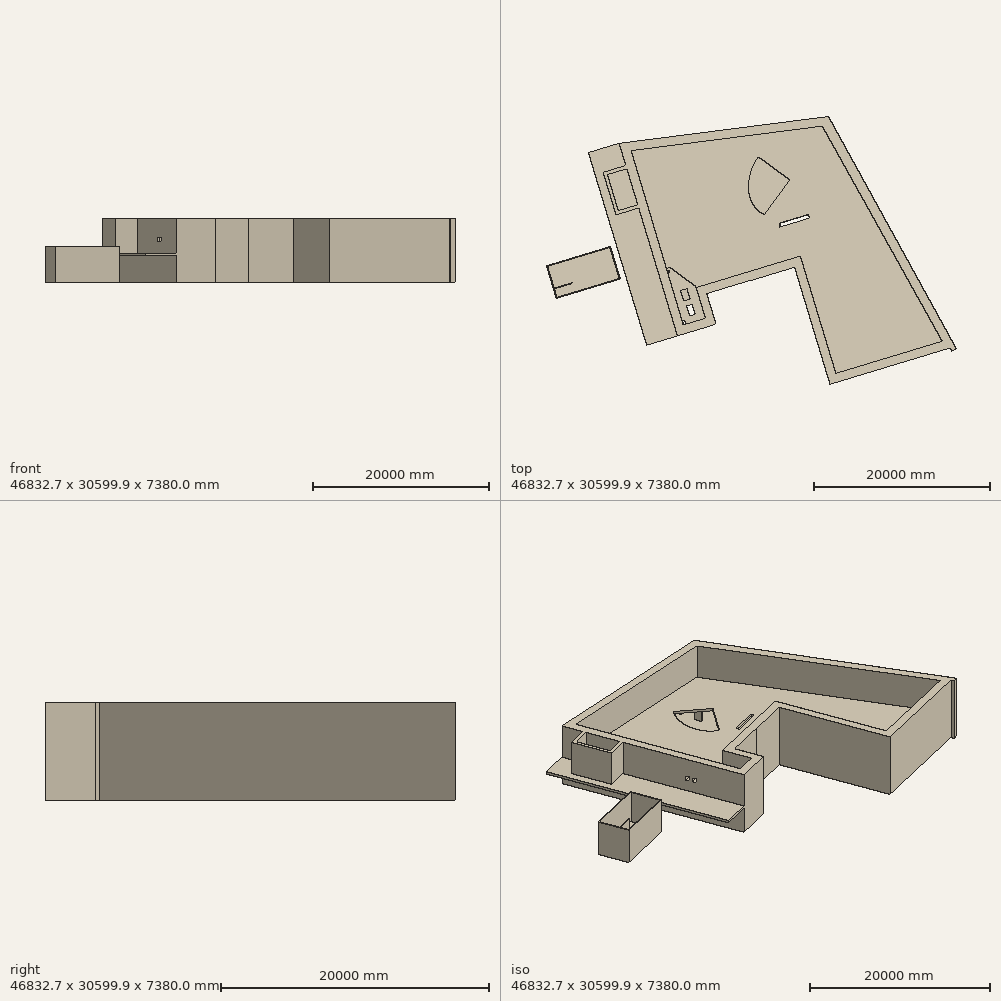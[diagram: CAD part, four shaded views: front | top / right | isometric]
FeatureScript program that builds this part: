
annotation { "Feature Type Name" : "Feature", "Feature Type Description" : "" }
export const myFeature = defineFeature(function(context is Context, id is Id, definition is map)
    precondition{}
    {
        {
            var Q0;
            Q0=qCreatedBy(makeId("Top.planeOp"),FACE);
            var sketch = newSketch(context, id + "F0", { "sketchPlane" : qUnion([Q0])});
            skLineSegment(sketch, "E0", {"start": v(49234.63, 59886.25) * mm, "end": v(49988.48, 60114.42) * mm});
            skLineSegment(sketch, "E1", {"start": v(49988.48, 60114.42) * mm, "end": v(49987.19, 60118.69) * mm});
            skLineSegment(sketch, "E2", {"start": v(49987.19, 60118.69) * mm, "end": v(50833.48, 60374.84) * mm});
            skLineSegment(sketch, "E3", {"start": v(50833.48, 60374.84) * mm, "end": v(51268.03, 58939.17) * mm});
            skLineSegment(sketch, "E4", {"start": v(51268.03, 58939.17) * mm, "end": v(50789.46, 58794.31) * mm});
            skLineSegment(sketch, "E5", {"start": v(50789.46, 58794.31) * mm, "end": v(51212.24, 57397.54) * mm});
            skLineSegment(sketch, "E6", {"start": v(51212.24, 57397.54) * mm, "end": v(53506.66, 49817.17) * mm});
            skLineSegment(sketch, "E7", {"start": v(53506.66, 49817.17) * mm, "end": v(54276.86, 47272.58) * mm});
            skLineSegment(sketch, "E8", {"start": v(54276.86, 47272.58) * mm, "end": v(54412.26, 46825.25) * mm});
            skLineSegment(sketch, "E9", {"start": v(54412.26, 46825.25) * mm, "end": v(62384.2, 49238.2) * mm});
            skLineSegment(sketch, "E10", {"start": v(62384.2, 49238.2) * mm, "end": v(62391.57, 49240.5) * mm});
            skLineSegment(sketch, "E11", {"start": v(62391.57, 49240.5) * mm, "end": v(50014.81, 71440.03) * mm});
            skLineSegment(sketch, "E12", {"start": v(50014.81, 71440.03) * mm, "end": v(49601.87, 74661.93) * mm});
            skLineSegment(sketch, "E13", {"start": v(49601.87, 74661.93) * mm, "end": v(39442.05, 73358.6) * mm});
            skLineSegment(sketch, "E14", {"start": v(39442.05, 73358.6) * mm, "end": v(40440.6, 70059.64) * mm});
            skLineSegment(sketch, "E15", {"start": v(40440.6, 70059.64) * mm, "end": v(33357.72, 67915.8) * mm});
            skLineSegment(sketch, "E16", {"start": v(33357.72, 67915.8) * mm, "end": v(31999.28, 72403.84) * mm});
            skLineSegment(sketch, "E17", {"start": v(31999.28, 72403.84) * mm, "end": v(31027.55, 72279.2) * mm});
            skLineSegment(sketch, "E18", {"start": v(31027.55, 72279.2) * mm, "end": v(32898.58, 66097.65) * mm});
            skLineSegment(sketch, "E19", {"start": v(32898.58, 66097.65) * mm, "end": v(32831.58, 66077.37) * mm});
            skLineSegment(sketch, "E20", {"start": v(32831.58, 66077.37) * mm, "end": v(35924.87, 55857.68) * mm});
            skLineSegment(sketch, "E21", {"start": v(35924.87, 55857.68) * mm, "end": v(35924.9, 55857.68) * mm});
            skLineSegment(sketch, "E22", {"start": v(35924.9, 55857.68) * mm, "end": v(36984.58, 52356.66) * mm});
            skLineSegment(sketch, "E23", {"start": v(36984.58, 52356.66) * mm, "end": v(39517.02, 53123.18) * mm});
            skLineSegment(sketch, "E24", {"start": v(39517.02, 53123.18) * mm, "end": v(38457.33, 56624.2) * mm});
            skLineSegment(sketch, "E25", {"start": v(38457.33, 56624.2) * mm, "end": v(38699.27, 56697.43) * mm});
            skLineSegment(sketch, "E26", {"start": v(38699.27, 56697.43) * mm, "end": v(38699.29, 56697.38) * mm});
            skLineSegment(sketch, "E27", {"start": v(38699.29, 56697.38) * mm, "end": v(39127.68, 56827.04) * mm});
            skLineSegment(sketch, "E28", {"start": v(39127.68, 56827.04) * mm, "end": v(38801.77, 57903.8) * mm});
            skLineSegment(sketch, "E29", {"start": v(38801.77, 57903.8) * mm, "end": v(42989.16, 59171.24) * mm});
            skLineSegment(sketch, "E30", {"start": v(42989.16, 59171.24) * mm, "end": v(43315.06, 58094.54) * mm});
            skLineSegment(sketch, "E31", {"start": v(43315.06, 58094.54) * mm, "end": v(44386.8, 58418.93) * mm});
            skLineSegment(sketch, "E32", {"start": v(44386.8, 58418.93) * mm, "end": v(43824.83, 60275.54) * mm});
            skLineSegment(sketch, "E33", {"start": v(43824.83, 60275.54) * mm, "end": v(48658.2, 61738.5) * mm});
            skLineSegment(sketch, "E34", {"start": v(48658.2, 61738.5) * mm, "end": v(48658.23, 61738.41) * mm});
            skLineSegment(sketch, "E35", {"start": v(48658.23, 61738.41) * mm, "end": v(48672.7, 61742.8) * mm});
            skLineSegment(sketch, "E36", {"start": v(48672.7, 61742.8) * mm, "end": v(48803.06, 61312.13) * mm});
            skLineSegment(sketch, "E37", {"start": v(48803.06, 61312.13) * mm, "end": v(49377.38, 61485.96) * mm});
            skLineSegment(sketch, "E38", {"start": v(49377.38, 61485.96) * mm, "end": v(49667.08, 60528.84) * mm});
            skLineSegment(sketch, "E39", {"start": v(49667.08, 60528.84) * mm, "end": v(49092.75, 60355) * mm});
            skLineSegment(sketch, "E40", {"start": v(49092.75, 60355) * mm, "end": v(49234.63, 59886.25) * mm});
            skLineSegment(sketch, "E41", {"start": v(54024.33, 50564.9) * mm, "end": v(51967.54, 57360.16) * mm});
            skLineSegment(sketch, "E42", {"start": v(51967.54, 57360.16) * mm, "end": v(51853.69, 57325.7) * mm});
            skLineSegment(sketch, "E43", {"start": v(51853.69, 57325.7) * mm, "end": v(51428.05, 58731.95) * mm});
            skLineSegment(sketch, "E44", {"start": v(51428.05, 58731.95) * mm, "end": v(51667.33, 58804.37) * mm});
            skLineSegment(sketch, "E45", {"start": v(51667.33, 58804.37) * mm, "end": v(52092.97, 57398.13) * mm});
            skLineSegment(sketch, "E46", {"start": v(52092.97, 57398.13) * mm, "end": v(54481.09, 58120.96) * mm});
            skLineSegment(sketch, "E47", {"start": v(54481.09, 58120.96) * mm, "end": v(53322.5, 61948.71) * mm});
            skLineSegment(sketch, "E48", {"start": v(53322.5, 61948.71) * mm, "end": v(53566.56, 62022.58) * mm});
            skLineSegment(sketch, "E49", {"start": v(53566.56, 62022.58) * mm, "end": v(54725.14, 58194.83) * mm});
            skLineSegment(sketch, "E50", {"start": v(54725.14, 58194.83) * mm, "end": v(54739.4, 58147.73) * mm});
            skLineSegment(sketch, "E51", {"start": v(54739.4, 58147.73) * mm, "end": v(55773.88, 58460.84) * mm});
            skLineSegment(sketch, "E52", {"start": v(55773.88, 58460.84) * mm, "end": v(59288.16, 52158.17) * mm});
            skLineSegment(sketch, "E53", {"start": v(59288.16, 52158.17) * mm, "end": v(54024.33, 50564.9) * mm});
            skLineSegment(sketch, "E54", {"start": v(51615.9, 65546.25) * mm, "end": v(50850.2, 65314.51) * mm});
            skLineSegment(sketch, "E55", {"start": v(50850.2, 65314.51) * mm, "end": v(50777.79, 65553.8) * mm});
            skLineSegment(sketch, "E56", {"start": v(50777.79, 65553.8) * mm, "end": v(51543.49, 65785.53) * mm});
            skLineSegment(sketch, "E57", {"start": v(51543.49, 65785.53) * mm, "end": v(51615.9, 65546.25) * mm});
            skLineSegment(sketch, "E58", {"start": v(51763.97, 62799.89) * mm, "end": v(51728.86, 62915.9) * mm});
            skLineSegment(sketch, "E59", {"start": v(51728.86, 62915.9) * mm, "end": v(52398.85, 63118.67) * mm});
            skLineSegment(sketch, "E60", {"start": v(52398.85, 63118.67) * mm, "end": v(52433.96, 63002.65) * mm});
            skLineSegment(sketch, "E61", {"start": v(52433.96, 63002.65) * mm, "end": v(51763.97, 62799.89) * mm});
            skLineSegment(sketch, "E62", {"start": v(48119.06, 63518.92) * mm, "end": v(48056.28, 63967.48) * mm});
            skLineSegment(sketch, "E63", {"start": v(48056.28, 63967.48) * mm, "end": v(51272.91, 64941.22) * mm});
            skLineSegment(sketch, "E64", {"start": v(51272.91, 64941.22) * mm, "end": v(51403.27, 64510.51) * mm});
            skLineSegment(sketch, "E65", {"start": v(51403.27, 64510.51) * mm, "end": v(48119.06, 63518.92) * mm});
            skLineSegment(sketch, "E66", {"start": v(57976.54, 65897.74) * mm, "end": v(66562.27, 50502.76) * mm});
            skLineSegment(sketch, "E67", {"start": v(66562.27, 50502.76) * mm, "end": v(65252.8, 50106.47) * mm});
            skLineSegment(sketch, "E68", {"start": v(65252.8, 50106.47) * mm, "end": v(51430.06, 74896.45) * mm});
            skLineSegment(sketch, "E69", {"start": v(51430.06, 74896.45) * mm, "end": v(52856, 75079.32) * mm});
            skLineSegment(sketch, "E70", {"start": v(52856, 75079.32) * mm, "end": v(52856, 75079.3) * mm});
            skLineSegment(sketch, "E71", {"start": v(52856, 75079.3) * mm, "end": v(52857.63, 75079.51) * mm});
            skLineSegment(sketch, "E72", {"start": v(52857.63, 75079.51) * mm, "end": v(57976.54, 65897.74) * mm});
            skLineSegment(sketch, "E73", {"start": v(51575.28, 74914.98) * mm, "end": v(65384.36, 50146.35) * mm});
            skLineSegment(sketch, "E74", {"start": v(65384.36, 50146.35) * mm, "end": v(62391.57, 49240.5) * mm});
            skLineSegment(sketch, "E75", {"start": v(62391.57, 49240.5) * mm, "end": v(50012.55, 71444.1) * mm});
            skLineSegment(sketch, "E76", {"start": v(50012.55, 71444.1) * mm, "end": v(49601.81, 74661.66) * mm});
            skLineSegment(sketch, "E77", {"start": v(49601.81, 74661.66) * mm, "end": v(51575.28, 74914.98) * mm});
            skCircle(sketch, "E78", {"center": v(0, 0) * mm, "radius": 1927.6 * mm});
            skLineSegment(sketch, "E79", {"start": v(0, 5000) * mm, "end": v(0, -5000) * mm});
            skLineSegment(sketch, "E80", {"start": v(5000, 0) * mm, "end": v(-5000, 0) * mm});
            skLineSegment(sketch, "E81", {"start": v(34100, 72522.1) * mm, "end": v(32052.06, 72259.39) * mm});
            skLineSegment(sketch, "E82", {"start": v(32052.06, 72259.39) * mm, "end": v(32032.97, 72408.17) * mm});
            skLineSegment(sketch, "E83", {"start": v(32032.97, 72408.17) * mm, "end": v(39441.15, 73358.44) * mm});
            skLineSegment(sketch, "E84", {"start": v(39441.15, 73358.44) * mm, "end": v(39460.24, 73209.66) * mm});
            skLineSegment(sketch, "E85", {"start": v(39460.24, 73209.66) * mm, "end": v(37865.53, 73005.14) * mm});
            skLineSegment(sketch, "E86", {"start": v(52182.8, 73250.46) * mm, "end": v(52173.55, 73267.05) * mm});
            skLineSegment(sketch, "E87", {"start": v(52173.55, 73267.05) * mm, "end": v(52159.34, 73259.13) * mm});
            skLineSegment(sketch, "E88", {"start": v(34858.83, 59379.88) * mm, "end": v(38413.86, 56763.64) * mm});
            skLineSegment(sketch, "E89", {"start": v(38413.86, 56763.64) * mm, "end": v(39517.39, 53123.3) * mm});
            skLineSegment(sketch, "E90", {"start": v(39517.39, 53123.3) * mm, "end": v(36984.58, 52356.66) * mm});
            skLineSegment(sketch, "E91", {"start": v(36984.58, 52356.66) * mm, "end": v(34858.83, 59379.88) * mm});
            skLineSegment(sketch, "E92", {"start": v(31997.32, 72403.55) * mm, "end": v(33353.34, 67923.5) * mm});
            skLineSegment(sketch, "E93", {"start": v(40437.2, 70067.64) * mm, "end": v(39441.15, 73358.44) * mm});
            skLineSegment(sketch, "E94", {"start": v(38345.1, 73217.84) * mm, "end": v(38345.1, 73217.85) * mm});
            skLineSegment(sketch, "E95", {"start": v(35567.85, 72861.58) * mm, "end": v(35567.85, 72861.59) * mm});
            skLineSegment(sketch, "E96", {"start": v(48630.18, 64524.82) * mm, "end": v(50782.31, 65176.37) * mm});
            skLineSegment(sketch, "E97", {"start": v(50853.58, 64936.6) * mm, "end": v(48702.6, 64285.54) * mm});
            skLineSegment(sketch, "E98", {"start": v(53328.4, 61951.88) * mm, "end": v(48991, 60639.04) * mm});
            skLineSegment(sketch, "E99", {"start": v(53328.4, 61951.88) * mm, "end": v(53400.82, 61712.6) * mm});
            skLineSegment(sketch, "E100", {"start": v(57239.17, 51925.82) * mm, "end": v(54176.2, 50998.75) * mm});
            skLineSegment(sketch, "E101", {"start": v(55604.89, 57867.13) * mm, "end": v(57345.71, 52125.24) * mm});
            skLineSegment(sketch, "E102", {"start": v(52345.35, 57047.72) * mm, "end": v(55408.08, 57974.72) * mm});
            skLineSegment(sketch, "E103", {"start": v(53976.63, 51105.79) * mm, "end": v(52238.56, 56848.23) * mm});
            skLineSegment(sketch, "E104", {"start": v(52391.7, 56894.58) * mm, "end": v(54129.84, 51151.89) * mm});
            skLineSegment(sketch, "E105", {"start": v(55454.43, 57821.58) * mm, "end": v(52391.7, 56894.58) * mm});
            skLineSegment(sketch, "E106", {"start": v(57192.58, 52078.89) * mm, "end": v(55454.43, 57821.58) * mm});
            skLineSegment(sketch, "E107", {"start": v(54129.84, 51151.89) * mm, "end": v(57192.58, 52078.89) * mm});
            skLineSegment(sketch, "E108", {"start": v(54176.2, 50998.75) * mm, "end": v(54023.05, 50952.4) * mm});
            skLineSegment(sketch, "E109", {"start": v(54023.05, 50952.4) * mm, "end": v(54020.55, 50960.69) * mm});
            skLineSegment(sketch, "E110", {"start": v(54020.55, 50960.69) * mm, "end": v(54086.56, 50980.7) * mm});
            skArc(sketch, "E111", {"start": v(54086.56, 50980.7) * mm, "mid": v(54091.32, 50984.6) * mm, "end": v(54091.92, 50990.7) * mm});
            skLineSegment(sketch, "E112", {"start": v(54091.92, 50990.7) * mm, "end": v(54055.4, 51111.92) * mm});
            skArc(sketch, "E113", {"start": v(54055.4, 51111.92) * mm, "mid": v(54051.1, 51116.56) * mm, "end": v(54044.8, 51117.1) * mm});
            skLineSegment(sketch, "E114", {"start": v(54044.8, 51117.1) * mm, "end": v(53979.21, 51097.25) * mm});
            skLineSegment(sketch, "E115", {"start": v(53979.21, 51097.25) * mm, "end": v(53976.7, 51105.54) * mm});
            skLineSegment(sketch, "E116", {"start": v(53976.7, 51105.54) * mm, "end": v(54129.84, 51151.89) * mm});
            skLineSegment(sketch, "E117", {"start": v(54129.84, 51151.89) * mm, "end": v(54132.35, 51143.6) * mm});
            skLineSegment(sketch, "E118", {"start": v(54132.35, 51143.6) * mm, "end": v(54066.16, 51123.56) * mm});
            skArc(sketch, "E119", {"start": v(54066.16, 51123.56) * mm, "mid": v(54061.44, 51119.65) * mm, "end": v(54060.82, 51113.56) * mm});
            skLineSegment(sketch, "E120", {"start": v(54060.82, 51113.56) * mm, "end": v(54097.35, 50992.34) * mm});
            skArc(sketch, "E121", {"start": v(54097.35, 50992.34) * mm, "mid": v(54101.31, 50987.56) * mm, "end": v(54107.5, 50987) * mm});
            skLineSegment(sketch, "E122", {"start": v(54107.5, 50987) * mm, "end": v(54173.68, 51007.04) * mm});
            skLineSegment(sketch, "E123", {"start": v(54173.68, 51007.04) * mm, "end": v(54176.2, 50998.75) * mm});
            skLineSegment(sketch, "E124", {"start": v(57392.07, 51972.1) * mm, "end": v(57238.93, 51925.75) * mm});
            skLineSegment(sketch, "E125", {"start": v(57238.93, 51925.75) * mm, "end": v(57236.42, 51934.04) * mm});
            skLineSegment(sketch, "E126", {"start": v(57236.42, 51934.04) * mm, "end": v(57302.44, 51954.06) * mm});
            skArc(sketch, "E127", {"start": v(57302.44, 51954.06) * mm, "mid": v(57307.19, 51957.94) * mm, "end": v(57307.8, 51964.05) * mm});
            skLineSegment(sketch, "E128", {"start": v(57307.8, 51964.05) * mm, "end": v(57271.27, 52085.27) * mm});
            skArc(sketch, "E129", {"start": v(57271.27, 52085.27) * mm, "mid": v(57266.98, 52089.9) * mm, "end": v(57260.68, 52090.45) * mm});
            skLineSegment(sketch, "E130", {"start": v(57260.68, 52090.45) * mm, "end": v(57195.08, 52070.6) * mm});
            skLineSegment(sketch, "E131", {"start": v(57195.08, 52070.6) * mm, "end": v(57192.58, 52078.89) * mm});
            skLineSegment(sketch, "E132", {"start": v(57192.58, 52078.89) * mm, "end": v(57345.71, 52125.24) * mm});
            skLineSegment(sketch, "E133", {"start": v(57345.71, 52125.24) * mm, "end": v(57348.22, 52116.95) * mm});
            skLineSegment(sketch, "E134", {"start": v(57348.22, 52116.95) * mm, "end": v(57282.03, 52096.92) * mm});
            skArc(sketch, "E135", {"start": v(57282.03, 52096.92) * mm, "mid": v(57277.31, 52093) * mm, "end": v(57276.69, 52086.9) * mm});
            skLineSegment(sketch, "E136", {"start": v(57276.69, 52086.9) * mm, "end": v(57313.22, 51965.7) * mm});
            skArc(sketch, "E137", {"start": v(57313.22, 51965.7) * mm, "mid": v(57317.18, 51960.91) * mm, "end": v(57323.37, 51960.36) * mm});
            skLineSegment(sketch, "E138", {"start": v(57323.37, 51960.36) * mm, "end": v(57389.56, 51980.4) * mm});
            skLineSegment(sketch, "E139", {"start": v(57389.56, 51980.4) * mm, "end": v(57392.07, 51972.1) * mm});
            skLineSegment(sketch, "E140", {"start": v(55607.57, 57867.94) * mm, "end": v(55454.43, 57821.58) * mm});
            skLineSegment(sketch, "E141", {"start": v(55454.43, 57821.58) * mm, "end": v(55451.92, 57829.87) * mm});
            skLineSegment(sketch, "E142", {"start": v(55451.92, 57829.87) * mm, "end": v(55517.94, 57849.9) * mm});
            skArc(sketch, "E143", {"start": v(55517.94, 57849.9) * mm, "mid": v(55522.7, 57853.78) * mm, "end": v(55523.3, 57859.89) * mm});
            skLineSegment(sketch, "E144", {"start": v(55523.3, 57859.89) * mm, "end": v(55486.78, 57981.1) * mm});
            skArc(sketch, "E145", {"start": v(55486.78, 57981.1) * mm, "mid": v(55482.48, 57985.74) * mm, "end": v(55476.18, 57986.29) * mm});
            skLineSegment(sketch, "E146", {"start": v(55476.18, 57986.29) * mm, "end": v(55410.59, 57966.43) * mm});
            skLineSegment(sketch, "E147", {"start": v(55410.59, 57966.43) * mm, "end": v(55408.08, 57974.72) * mm});
            skLineSegment(sketch, "E148", {"start": v(55408.08, 57974.72) * mm, "end": v(55561.22, 58021.08) * mm});
            skLineSegment(sketch, "E149", {"start": v(55561.22, 58021.08) * mm, "end": v(55563.73, 58012.79) * mm});
            skLineSegment(sketch, "E150", {"start": v(55563.73, 58012.79) * mm, "end": v(55497.54, 57992.75) * mm});
            skArc(sketch, "E151", {"start": v(55497.54, 57992.75) * mm, "mid": v(55492.82, 57988.84) * mm, "end": v(55492.2, 57982.74) * mm});
            skLineSegment(sketch, "E152", {"start": v(55492.2, 57982.74) * mm, "end": v(55528.73, 57861.53) * mm});
            skArc(sketch, "E153", {"start": v(55528.73, 57861.53) * mm, "mid": v(55532.69, 57856.75) * mm, "end": v(55538.87, 57856.2) * mm});
            skLineSegment(sketch, "E154", {"start": v(55538.87, 57856.2) * mm, "end": v(55605.06, 57876.23) * mm});
            skLineSegment(sketch, "E155", {"start": v(55605.06, 57876.23) * mm, "end": v(55607.57, 57867.94) * mm});
            skLineSegment(sketch, "E156", {"start": v(52391.7, 56894.58) * mm, "end": v(52238.56, 56848.23) * mm});
            skLineSegment(sketch, "E157", {"start": v(52238.56, 56848.23) * mm, "end": v(52236.05, 56856.52) * mm});
            skLineSegment(sketch, "E158", {"start": v(52236.05, 56856.52) * mm, "end": v(52302.07, 56876.54) * mm});
            skArc(sketch, "E159", {"start": v(52302.07, 56876.54) * mm, "mid": v(52306.82, 56880.43) * mm, "end": v(52307.43, 56886.53) * mm});
            skLineSegment(sketch, "E160", {"start": v(52307.43, 56886.53) * mm, "end": v(52270.9, 57007.75) * mm});
            skArc(sketch, "E161", {"start": v(52270.9, 57007.75) * mm, "mid": v(52266.6, 57012.4) * mm, "end": v(52260.3, 57012.93) * mm});
            skLineSegment(sketch, "E162", {"start": v(52260.3, 57012.93) * mm, "end": v(52194.72, 56993.08) * mm});
            skLineSegment(sketch, "E163", {"start": v(52194.72, 56993.08) * mm, "end": v(52192.2, 57001.37) * mm});
            skLineSegment(sketch, "E164", {"start": v(52192.2, 57001.37) * mm, "end": v(52345.35, 57047.72) * mm});
            skLineSegment(sketch, "E165", {"start": v(52345.35, 57047.72) * mm, "end": v(52347.86, 57039.43) * mm});
            skLineSegment(sketch, "E166", {"start": v(52347.86, 57039.43) * mm, "end": v(52281.67, 57019.4) * mm});
            skArc(sketch, "E167", {"start": v(52281.67, 57019.4) * mm, "mid": v(52276.94, 57015.49) * mm, "end": v(52276.32, 57009.39) * mm});
            skLineSegment(sketch, "E168", {"start": v(52276.32, 57009.39) * mm, "end": v(52312.86, 56888.17) * mm});
            skArc(sketch, "E169", {"start": v(52312.86, 56888.17) * mm, "mid": v(52316.82, 56883.4) * mm, "end": v(52323, 56882.84) * mm});
            skLineSegment(sketch, "E170", {"start": v(52323, 56882.84) * mm, "end": v(52389.19, 56902.87) * mm});
            skLineSegment(sketch, "E171", {"start": v(52389.19, 56902.87) * mm, "end": v(52391.7, 56894.58) * mm});
            skLineSegment(sketch, "E172", {"start": v(55694.63, 56724.4) * mm, "end": v(55675.8, 56786.62) * mm});
            skLineSegment(sketch, "E173", {"start": v(55675.8, 56786.62) * mm, "end": v(55672.2, 56785.53) * mm});
            skArc(sketch, "E174", {"start": v(55672.2, 56785.53) * mm, "mid": v(55669.63, 56783.5) * mm, "end": v(55669.12, 56780.27) * mm});
            skLineSegment(sketch, "E175", {"start": v(55669.12, 56780.27) * mm, "end": v(55678.43, 56737.44) * mm});
            skArc(sketch, "E176", {"start": v(55671.21, 56725.15) * mm, "mid": v(55677.22, 56729.88) * mm, "end": v(55678.43, 56737.44) * mm});
            skLineSegment(sketch, "E177", {"start": v(55671.21, 56725.15) * mm, "end": v(55560.55, 56691.66) * mm});
            skArc(sketch, "E178", {"start": v(55547.74, 56697.88) * mm, "mid": v(55552.93, 56692.26) * mm, "end": v(55560.55, 56691.66) * mm});
            skLineSegment(sketch, "E179", {"start": v(55547.74, 56697.88) * mm, "end": v(55531.74, 56738.69) * mm});
            skArc(sketch, "E180", {"start": v(55531.74, 56738.69) * mm, "mid": v(55529.51, 56741.1) * mm, "end": v(55526.24, 56741.35) * mm});
            skLineSegment(sketch, "E181", {"start": v(55526.24, 56741.35) * mm, "end": v(55522.66, 56740.27) * mm});
            skLineSegment(sketch, "E182", {"start": v(55522.66, 56740.27) * mm, "end": v(55541.49, 56678.05) * mm});
            skLineSegment(sketch, "E183", {"start": v(55541.49, 56678.05) * mm, "end": v(55694.63, 56724.4) * mm});
            skLineSegment(sketch, "E184", {"start": v(55616.8, 56429.2) * mm, "end": v(55635.64, 56366.99) * mm});
            skLineSegment(sketch, "E185", {"start": v(55635.64, 56366.99) * mm, "end": v(55639.22, 56368.08) * mm});
            skArc(sketch, "E186", {"start": v(55639.22, 56368.08) * mm, "mid": v(55641.8, 56370.1) * mm, "end": v(55642.32, 56373.34) * mm});
            skLineSegment(sketch, "E187", {"start": v(55642.32, 56373.34) * mm, "end": v(55633, 56416.17) * mm});
            skArc(sketch, "E188", {"start": v(55640.22, 56428.45) * mm, "mid": v(55634.2, 56423.72) * mm, "end": v(55633, 56416.17) * mm});
            skLineSegment(sketch, "E189", {"start": v(55640.22, 56428.45) * mm, "end": v(55750.88, 56461.95) * mm});
            skArc(sketch, "E190", {"start": v(55763.7, 56455.73) * mm, "mid": v(55758.5, 56461.34) * mm, "end": v(55750.88, 56461.95) * mm});
            skLineSegment(sketch, "E191", {"start": v(55763.7, 56455.73) * mm, "end": v(55779.7, 56414.92) * mm});
            skArc(sketch, "E192", {"start": v(55779.7, 56414.92) * mm, "mid": v(55781.92, 56412.51) * mm, "end": v(55785.19, 56412.26) * mm});
            skLineSegment(sketch, "E193", {"start": v(55785.19, 56412.26) * mm, "end": v(55788.78, 56413.34) * mm});
            skLineSegment(sketch, "E194", {"start": v(55788.78, 56413.34) * mm, "end": v(55769.95, 56475.55) * mm});
            skLineSegment(sketch, "E195", {"start": v(55769.95, 56475.55) * mm, "end": v(55616.8, 56429.2) * mm});
            skCircle(sketch, "E196", {"center": v(55655.72, 56576.8) * mm, "radius": 0.25 * mm});
            skCircle(sketch, "E197", {"center": v(55655.72, 56576.8) * mm, "radius": 57.5 * mm});
            skCircle(sketch, "E198", {"center": v(55655.72, 56576.8) * mm, "radius": 59.5 * mm});
            skCircle(sketch, "E199", {"center": v(55655.72, 56576.8) * mm, "radius": 63.5 * mm});
            skLineSegment(sketch, "E200", {"start": v(55607.5, 56356.38) * mm, "end": v(55636.22, 56365.08) * mm});
            skLineSegment(sketch, "E201", {"start": v(55636.22, 56365.08) * mm, "end": v(55621.73, 56412.93) * mm});
            skLineSegment(sketch, "E202", {"start": v(55621.73, 56412.93) * mm, "end": v(55593.02, 56404.24) * mm});
            skLineSegment(sketch, "E203", {"start": v(55593.02, 56404.24) * mm, "end": v(55607.5, 56356.38) * mm});
            skLineSegment(sketch, "E204", {"start": v(55636.22, 56365.08) * mm, "end": v(55635.64, 56366.99) * mm});
            skLineSegment(sketch, "E205", {"start": v(55635.64, 56366.99) * mm, "end": v(55621.73, 56412.93) * mm});
            skLineSegment(sketch, "E206", {"start": v(52875.62, 55599.52) * mm, "end": v(52894.45, 55537.3) * mm});
            skLineSegment(sketch, "E207", {"start": v(52894.45, 55537.3) * mm, "end": v(52898.03, 55538.4) * mm});
            skArc(sketch, "E208", {"start": v(52898.03, 55538.4) * mm, "mid": v(52900.6, 55540.42) * mm, "end": v(52901.13, 55543.66) * mm});
            skLineSegment(sketch, "E209", {"start": v(52901.13, 55543.66) * mm, "end": v(52891.81, 55586.5) * mm});
            skArc(sketch, "E210", {"start": v(52899.03, 55598.77) * mm, "mid": v(52893.02, 55594.04) * mm, "end": v(52891.81, 55586.5) * mm});
            skLineSegment(sketch, "E211", {"start": v(52899.03, 55598.77) * mm, "end": v(53009.69, 55632.26) * mm});
            skArc(sketch, "E212", {"start": v(53022.5, 55626.05) * mm, "mid": v(53017.31, 55631.66) * mm, "end": v(53009.69, 55632.26) * mm});
            skLineSegment(sketch, "E213", {"start": v(53022.5, 55626.05) * mm, "end": v(53038.5, 55585.24) * mm});
            skArc(sketch, "E214", {"start": v(53038.5, 55585.24) * mm, "mid": v(53040.73, 55582.83) * mm, "end": v(53044, 55582.57) * mm});
            skLineSegment(sketch, "E215", {"start": v(53044, 55582.57) * mm, "end": v(53047.59, 55583.66) * mm});
            skLineSegment(sketch, "E216", {"start": v(53047.59, 55583.66) * mm, "end": v(53028.76, 55645.87) * mm});
            skLineSegment(sketch, "E217", {"start": v(53028.76, 55645.87) * mm, "end": v(52875.62, 55599.52) * mm});
            skLineSegment(sketch, "E218", {"start": v(52953.44, 55894.72) * mm, "end": v(52934.6, 55956.94) * mm});
            skLineSegment(sketch, "E219", {"start": v(52934.6, 55956.94) * mm, "end": v(52931.02, 55955.85) * mm});
            skArc(sketch, "E220", {"start": v(52931.02, 55955.85) * mm, "mid": v(52928.44, 55953.82) * mm, "end": v(52927.92, 55950.59) * mm});
            skLineSegment(sketch, "E221", {"start": v(52927.92, 55950.59) * mm, "end": v(52937.24, 55907.75) * mm});
            skArc(sketch, "E222", {"start": v(52930.02, 55895.47) * mm, "mid": v(52936.03, 55900.2) * mm, "end": v(52937.24, 55907.75) * mm});
            skLineSegment(sketch, "E223", {"start": v(52930.02, 55895.47) * mm, "end": v(52819.36, 55861.98) * mm});
            skArc(sketch, "E224", {"start": v(52806.55, 55868.2) * mm, "mid": v(52811.74, 55862.58) * mm, "end": v(52819.36, 55861.98) * mm});
            skLineSegment(sketch, "E225", {"start": v(52806.55, 55868.2) * mm, "end": v(52790.55, 55909) * mm});
            skArc(sketch, "E226", {"start": v(52790.55, 55909) * mm, "mid": v(52788.32, 55911.41) * mm, "end": v(52785.05, 55911.67) * mm});
            skLineSegment(sketch, "E227", {"start": v(52785.05, 55911.67) * mm, "end": v(52781.47, 55910.59) * mm});
            skLineSegment(sketch, "E228", {"start": v(52781.47, 55910.59) * mm, "end": v(52800.3, 55848.37) * mm});
            skLineSegment(sketch, "E229", {"start": v(52800.3, 55848.37) * mm, "end": v(52953.44, 55894.72) * mm});
            skCircle(sketch, "E230", {"center": v(52914.53, 55747.12) * mm, "radius": 0.25 * mm});
            skCircle(sketch, "E231", {"center": v(52914.53, 55747.12) * mm, "radius": 57.5 * mm});
            skCircle(sketch, "E232", {"center": v(52914.53, 55747.12) * mm, "radius": 59.5 * mm});
            skCircle(sketch, "E233", {"center": v(52914.53, 55747.12) * mm, "radius": 63.5 * mm});
            skLineSegment(sketch, "E234", {"start": v(53045.04, 55592.08) * mm, "end": v(53073.75, 55600.77) * mm});
            skLineSegment(sketch, "E235", {"start": v(53073.75, 55600.77) * mm, "end": v(53062.4, 55638.3) * mm});
            skLineSegment(sketch, "E236", {"start": v(53062.4, 55638.3) * mm, "end": v(53033.68, 55629.6) * mm});
            skLineSegment(sketch, "E237", {"start": v(53033.68, 55629.6) * mm, "end": v(53045.04, 55592.08) * mm});
            skLineSegment(sketch, "E238", {"start": v(53076.88, 55590.44) * mm, "end": v(53073.75, 55600.77) * mm});
            skLineSegment(sketch, "E239", {"start": v(53048.16, 55581.75) * mm, "end": v(53076.88, 55590.44) * mm});
            skLineSegment(sketch, "E240", {"start": v(53048.16, 55581.75) * mm, "end": v(53047.59, 55583.66) * mm});
            skLineSegment(sketch, "E241", {"start": v(53889.54, 52249.6) * mm, "end": v(53908.37, 52187.4) * mm});
            skLineSegment(sketch, "E242", {"start": v(53908.37, 52187.4) * mm, "end": v(53911.96, 52188.48) * mm});
            skArc(sketch, "E243", {"start": v(53911.96, 52188.48) * mm, "mid": v(53914.53, 52190.5) * mm, "end": v(53915.05, 52193.74) * mm});
            skLineSegment(sketch, "E244", {"start": v(53915.05, 52193.74) * mm, "end": v(53905.74, 52236.57) * mm});
            skArc(sketch, "E245", {"start": v(53912.96, 52248.85) * mm, "mid": v(53906.95, 52244.12) * mm, "end": v(53905.74, 52236.57) * mm});
            skLineSegment(sketch, "E246", {"start": v(53912.96, 52248.85) * mm, "end": v(54023.61, 52282.35) * mm});
            skArc(sketch, "E247", {"start": v(54036.43, 52276.13) * mm, "mid": v(54031.24, 52281.74) * mm, "end": v(54023.61, 52282.35) * mm});
            skLineSegment(sketch, "E248", {"start": v(54036.43, 52276.13) * mm, "end": v(54052.43, 52235.32) * mm});
            skArc(sketch, "E249", {"start": v(54052.43, 52235.32) * mm, "mid": v(54054.66, 52232.91) * mm, "end": v(54057.92, 52232.66) * mm});
            skLineSegment(sketch, "E250", {"start": v(54057.92, 52232.66) * mm, "end": v(54061.51, 52233.74) * mm});
            skLineSegment(sketch, "E251", {"start": v(54061.51, 52233.74) * mm, "end": v(54042.68, 52295.95) * mm});
            skLineSegment(sketch, "E252", {"start": v(54042.68, 52295.95) * mm, "end": v(53889.54, 52249.6) * mm});
            skLineSegment(sketch, "E253", {"start": v(53967.36, 52544.8) * mm, "end": v(53948.53, 52607.02) * mm});
            skLineSegment(sketch, "E254", {"start": v(53948.53, 52607.02) * mm, "end": v(53944.94, 52605.93) * mm});
            skArc(sketch, "E255", {"start": v(53944.94, 52605.93) * mm, "mid": v(53942.37, 52603.9) * mm, "end": v(53941.85, 52600.67) * mm});
            skLineSegment(sketch, "E256", {"start": v(53941.85, 52600.67) * mm, "end": v(53951.17, 52557.84) * mm});
            skArc(sketch, "E257", {"start": v(53943.95, 52545.55) * mm, "mid": v(53949.96, 52550.28) * mm, "end": v(53951.17, 52557.84) * mm});
            skLineSegment(sketch, "E258", {"start": v(53943.95, 52545.55) * mm, "end": v(53833.3, 52512.06) * mm});
            skArc(sketch, "E259", {"start": v(53820.47, 52518.28) * mm, "mid": v(53825.67, 52512.66) * mm, "end": v(53833.3, 52512.06) * mm});
            skLineSegment(sketch, "E260", {"start": v(53820.47, 52518.28) * mm, "end": v(53804.47, 52559.09) * mm});
            skArc(sketch, "E261", {"start": v(53804.47, 52559.09) * mm, "mid": v(53802.25, 52561.5) * mm, "end": v(53798.98, 52561.75) * mm});
            skLineSegment(sketch, "E262", {"start": v(53798.98, 52561.75) * mm, "end": v(53795.4, 52560.67) * mm});
            skLineSegment(sketch, "E263", {"start": v(53795.4, 52560.67) * mm, "end": v(53814.22, 52498.45) * mm});
            skLineSegment(sketch, "E264", {"start": v(53814.22, 52498.45) * mm, "end": v(53967.36, 52544.8) * mm});
            skCircle(sketch, "E265", {"center": v(53928.45, 52397.2) * mm, "radius": 0.25 * mm});
            skCircle(sketch, "E266", {"center": v(53928.45, 52397.2) * mm, "radius": 57.5 * mm});
            skCircle(sketch, "E267", {"center": v(53928.45, 52397.2) * mm, "radius": 59.5 * mm});
            skCircle(sketch, "E268", {"center": v(53928.45, 52397.2) * mm, "radius": 63.5 * mm});
            skLineSegment(sketch, "E269", {"start": v(53976.67, 52617.62) * mm, "end": v(53947.95, 52608.93) * mm});
            skLineSegment(sketch, "E270", {"start": v(53947.95, 52608.93) * mm, "end": v(53962.44, 52561.08) * mm});
            skLineSegment(sketch, "E271", {"start": v(53962.44, 52561.08) * mm, "end": v(53991.15, 52569.77) * mm});
            skLineSegment(sketch, "E272", {"start": v(53991.15, 52569.77) * mm, "end": v(53976.67, 52617.62) * mm});
            skLineSegment(sketch, "E273", {"start": v(53947.95, 52608.93) * mm, "end": v(53948.53, 52607.02) * mm});
            skLineSegment(sketch, "E274", {"start": v(53948.53, 52607.02) * mm, "end": v(53962.44, 52561.08) * mm});
            skLineSegment(sketch, "E275", {"start": v(56708.55, 53374.49) * mm, "end": v(56689.72, 53436.7) * mm});
            skLineSegment(sketch, "E276", {"start": v(56689.72, 53436.7) * mm, "end": v(56686.13, 53435.61) * mm});
            skArc(sketch, "E277", {"start": v(56686.13, 53435.61) * mm, "mid": v(56683.56, 53433.59) * mm, "end": v(56683.04, 53430.35) * mm});
            skLineSegment(sketch, "E278", {"start": v(56683.04, 53430.35) * mm, "end": v(56692.36, 53387.52) * mm});
            skArc(sketch, "E279", {"start": v(56685.14, 53375.24) * mm, "mid": v(56691.15, 53379.96) * mm, "end": v(56692.36, 53387.52) * mm});
            skLineSegment(sketch, "E280", {"start": v(56685.14, 53375.24) * mm, "end": v(56574.48, 53341.74) * mm});
            skArc(sketch, "E281", {"start": v(56561.66, 53347.96) * mm, "mid": v(56566.86, 53342.35) * mm, "end": v(56574.48, 53341.74) * mm});
            skLineSegment(sketch, "E282", {"start": v(56561.66, 53347.96) * mm, "end": v(56545.66, 53388.77) * mm});
            skArc(sketch, "E283", {"start": v(56545.66, 53388.77) * mm, "mid": v(56543.44, 53391.18) * mm, "end": v(56540.17, 53391.43) * mm});
            skLineSegment(sketch, "E284", {"start": v(56540.17, 53391.43) * mm, "end": v(56536.58, 53390.35) * mm});
            skLineSegment(sketch, "E285", {"start": v(56536.58, 53390.35) * mm, "end": v(56555.41, 53328.14) * mm});
            skLineSegment(sketch, "E286", {"start": v(56555.41, 53328.14) * mm, "end": v(56708.55, 53374.49) * mm});
            skLineSegment(sketch, "E287", {"start": v(56630.73, 53079.28) * mm, "end": v(56649.56, 53017.07) * mm});
            skLineSegment(sketch, "E288", {"start": v(56649.56, 53017.07) * mm, "end": v(56653.15, 53018.16) * mm});
            skArc(sketch, "E289", {"start": v(56653.15, 53018.16) * mm, "mid": v(56655.73, 53020.18) * mm, "end": v(56656.24, 53023.42) * mm});
            skLineSegment(sketch, "E290", {"start": v(56656.24, 53023.42) * mm, "end": v(56646.93, 53066.25) * mm});
            skArc(sketch, "E291", {"start": v(56654.15, 53078.53) * mm, "mid": v(56648.14, 53073.8) * mm, "end": v(56646.93, 53066.25) * mm});
            skLineSegment(sketch, "E292", {"start": v(56654.15, 53078.53) * mm, "end": v(56764.8, 53112.03) * mm});
            skArc(sketch, "E293", {"start": v(56777.62, 53105.81) * mm, "mid": v(56772.43, 53111.43) * mm, "end": v(56764.8, 53112.03) * mm});
            skLineSegment(sketch, "E294", {"start": v(56777.62, 53105.81) * mm, "end": v(56793.62, 53065) * mm});
            skArc(sketch, "E295", {"start": v(56793.62, 53065) * mm, "mid": v(56795.85, 53062.6) * mm, "end": v(56799.11, 53062.34) * mm});
            skLineSegment(sketch, "E296", {"start": v(56799.11, 53062.34) * mm, "end": v(56802.7, 53063.42) * mm});
            skLineSegment(sketch, "E297", {"start": v(56802.7, 53063.42) * mm, "end": v(56783.87, 53125.64) * mm});
            skLineSegment(sketch, "E298", {"start": v(56783.87, 53125.64) * mm, "end": v(56630.73, 53079.28) * mm});
            skCircle(sketch, "E299", {"center": v(56669.64, 53226.89) * mm, "radius": 0.25 * mm});
            skCircle(sketch, "E300", {"center": v(56669.64, 53226.89) * mm, "radius": 57.5 * mm});
            skCircle(sketch, "E301", {"center": v(56669.64, 53226.89) * mm, "radius": 59.5 * mm});
            skCircle(sketch, "E302", {"center": v(56669.64, 53226.89) * mm, "radius": 63.5 * mm});
            skLineSegment(sketch, "E303", {"start": v(56539.13, 53381.93) * mm, "end": v(56510.42, 53373.23) * mm});
            skLineSegment(sketch, "E304", {"start": v(56510.42, 53373.23) * mm, "end": v(56521.77, 53335.72) * mm});
            skLineSegment(sketch, "E305", {"start": v(56521.77, 53335.72) * mm, "end": v(56550.49, 53344.4) * mm});
            skLineSegment(sketch, "E306", {"start": v(56550.49, 53344.4) * mm, "end": v(56539.13, 53381.93) * mm});
            skLineSegment(sketch, "E307", {"start": v(56507.29, 53383.57) * mm, "end": v(56510.42, 53373.23) * mm});
            skLineSegment(sketch, "E308", {"start": v(56536, 53392.26) * mm, "end": v(56507.29, 53383.57) * mm});
            skLineSegment(sketch, "E309", {"start": v(56536, 53392.26) * mm, "end": v(56536.58, 53390.35) * mm});
            skLineSegment(sketch, "E310", {"start": v(54409.66, 51283.84) * mm, "end": v(52697.54, 56940.4) * mm});
            skLineSegment(sketch, "E311", {"start": v(52697.54, 56940.4) * mm, "end": v(55174.56, 57690.15) * mm});
            skLineSegment(sketch, "E312", {"start": v(55174.56, 57690.15) * mm, "end": v(56886.68, 52033.59) * mm});
            skLineSegment(sketch, "E313", {"start": v(56886.68, 52033.59) * mm, "end": v(54409.66, 51283.84) * mm});
            skLineSegment(sketch, "E314", {"start": v(67446.81, 49725.81) * mm, "end": v(53744.87, 45578.51) * mm});
            skLineSegment(sketch, "E315", {"start": v(67150.92, 50263.13) * mm, "end": v(54145.32, 46326.6) * mm});
            skLineSegment(sketch, "E316", {"start": v(53744.87, 45578.51) * mm, "end": v(49515.03, 59553.16) * mm});
            skLineSegment(sketch, "E317", {"start": v(50089.3, 59726.98) * mm, "end": v(49515.03, 59553.16) * mm});
            skLineSegment(sketch, "E318", {"start": v(54145.32, 46326.6) * mm, "end": v(50089.3, 59726.98) * mm});
            skLineSegment(sketch, "E319", {"start": v(53235.88, 75531.31) * mm, "end": v(30437.41, 72606.72) * mm});
            skLineSegment(sketch, "E320", {"start": v(53564.5, 76178.39) * mm, "end": v(29657.7, 73111.61) * mm});
            skLineSegment(sketch, "E321", {"start": v(30437.41, 72606.72) * mm, "end": v(36717.97, 51856.85) * mm});
            skLineSegment(sketch, "E322", {"start": v(29657.7, 73111.61) * mm, "end": v(36317.52, 51108.76) * mm});
            skLineSegment(sketch, "E323", {"start": v(38916.37, 56343.94) * mm, "end": v(44571.14, 58055.53) * mm});
            skLineSegment(sketch, "E324", {"start": v(39664.46, 55943.5) * mm, "end": v(44744.96, 57481.26) * mm});
            skLineSegment(sketch, "E325", {"start": v(36717.97, 51856.85) * mm, "end": v(39976.03, 52843) * mm});
            skLineSegment(sketch, "E326", {"start": v(36317.52, 51108.76) * mm, "end": v(40724.12, 52442.55) * mm});
            skLineSegment(sketch, "E327", {"start": v(39976.03, 52843) * mm, "end": v(38916.37, 56343.94) * mm});
            skLineSegment(sketch, "E328", {"start": v(40724.12, 52442.55) * mm, "end": v(39664.46, 55943.5) * mm});
            skLineSegment(sketch, "E329", {"start": v(67662.85, 49333.51) * mm, "end": v(53235.88, 75531.31) * mm});
            skLineSegment(sketch, "E330", {"start": v(67150.92, 50263.13) * mm, "end": v(53235.88, 75531.31) * mm});
            skLineSegment(sketch, "E331", {"start": v(68188.43, 49622.94) * mm, "end": v(53564.5, 76178.39) * mm});
            skLineSegment(sketch, "E332", {"start": v(67662.85, 49333.51) * mm, "end": v(67446.81, 49725.81) * mm});
            skLineSegment(sketch, "E333", {"start": v(68188.43, 49622.94) * mm, "end": v(67662.85, 49333.51) * mm});
            skLineSegment(sketch, "E334", {"start": v(38841.66, 63847.55) * mm, "end": v(39375.14, 64572.39) * mm});
            skLineSegment(sketch, "E335", {"start": v(39616.76, 64394.56) * mm, "end": v(39375.14, 64572.39) * mm});
            skLineSegment(sketch, "E336", {"start": v(39083.27, 63669.72) * mm, "end": v(39616.76, 64394.56) * mm});
            skLineSegment(sketch, "E337", {"start": v(39083.27, 63669.72) * mm, "end": v(38841.66, 63847.55) * mm});
            skLineSegment(sketch, "E338", {"start": v(34646.67, 67032.26) * mm, "end": v(35364.5, 67249.58) * mm});
            skLineSegment(sketch, "E339", {"start": v(35451.43, 66962.45) * mm, "end": v(35364.5, 67249.58) * mm});
            skLineSegment(sketch, "E340", {"start": v(34733.6, 66745.13) * mm, "end": v(35451.43, 66962.45) * mm});
            skLineSegment(sketch, "E341", {"start": v(34733.6, 66745.13) * mm, "end": v(34646.67, 67032.26) * mm});
            skLineSegment(sketch, "E342", {"start": v(41369.6, 67281.8) * mm, "end": v(41932.72, 68046.92) * mm});
            skLineSegment(sketch, "E343", {"start": v(42174.33, 67869.09) * mm, "end": v(41932.72, 68046.92) * mm});
            skLineSegment(sketch, "E344", {"start": v(41611.2, 67103.98) * mm, "end": v(42174.33, 67869.09) * mm});
            skLineSegment(sketch, "E345", {"start": v(41611.2, 67103.98) * mm, "end": v(41369.6, 67281.8) * mm});
            skLineSegment(sketch, "E346", {"start": v(47761.24, 64287.93) * mm, "end": v(48622.63, 64548.71) * mm});
            skLineSegment(sketch, "E347", {"start": v(48709.55, 64261.58) * mm, "end": v(48622.63, 64548.71) * mm});
            skLineSegment(sketch, "E348", {"start": v(47848.16, 64000.8) * mm, "end": v(48709.55, 64261.58) * mm});
            skLineSegment(sketch, "E349", {"start": v(47848.16, 64000.8) * mm, "end": v(47761.24, 64287.93) * mm});
            skLineSegment(sketch, "E350", {"start": v(50775.12, 65200.15) * mm, "end": v(51636.5, 65460.94) * mm});
            skLineSegment(sketch, "E351", {"start": v(51723.43, 65173.8) * mm, "end": v(51636.5, 65460.94) * mm});
            skLineSegment(sketch, "E352", {"start": v(50862.04, 64913.02) * mm, "end": v(51723.43, 65173.8) * mm});
            skLineSegment(sketch, "E353", {"start": v(50862.04, 64913.02) * mm, "end": v(50775.12, 65200.15) * mm});
            skLineSegment(sketch, "E354", {"start": v(51286.26, 57153.17) * mm, "end": v(54486.1, 58121.7) * mm});
            skLineSegment(sketch, "E355", {"start": v(52093.19, 57397.4) * mm, "end": v(54486.1, 58121.7) * mm});
            skLineSegment(sketch, "E356", {"start": v(51358.69, 56913.89) * mm, "end": v(54558.52, 57882.41) * mm});
            skLineSegment(sketch, "E357", {"start": v(51286.26, 57153.17) * mm, "end": v(51853.9, 57324.98) * mm});
            skLineSegment(sketch, "E358", {"start": v(54486.1, 58121.7) * mm, "end": v(54558.1, 57883.79) * mm});
            skLineSegment(sketch, "E359", {"start": v(54558.1, 57883.79) * mm, "end": v(54558.52, 57882.41) * mm});
            skLineSegment(sketch, "E360", {"start": v(54485.98, 58121.66) * mm, "end": v(53326.1, 61953.71) * mm});
            skLineSegment(sketch, "E361", {"start": v(53565.37, 62026.14) * mm, "end": v(53326.1, 61953.71) * mm});
            skLineSegment(sketch, "E362", {"start": v(54739.33, 58147.6) * mm, "end": v(53565.37, 62026.14) * mm});
            skLineSegment(sketch, "E363", {"start": v(54739.44, 58147.63) * mm, "end": v(55773.63, 58460.66) * mm});
            skLineSegment(sketch, "E364", {"start": v(54558.1, 57883.79) * mm, "end": v(55677.4, 58222.57) * mm});
            skLineSegment(sketch, "E365", {"start": v(52846.86, 58791.21) * mm, "end": v(52082.47, 61316.09) * mm});
            skLineSegment(sketch, "E366", {"start": v(52321.74, 61388.52) * mm, "end": v(52082.47, 61316.09) * mm});
            skLineSegment(sketch, "E367", {"start": v(53086.14, 58863.65) * mm, "end": v(52321.74, 61388.52) * mm});
            skLineSegment(sketch, "E368", {"start": v(53086.14, 58863.65) * mm, "end": v(52846.86, 58791.21) * mm});
            skLineSegment(sketch, "E369", {"start": v(57793.68, 52268.9) * mm, "end": v(58968.18, 52624.48) * mm});
            skLineSegment(sketch, "E370", {"start": v(59098.58, 52193.79) * mm, "end": v(58968.18, 52624.48) * mm});
            skLineSegment(sketch, "E371", {"start": v(57924.07, 51838.21) * mm, "end": v(59098.58, 52193.79) * mm});
            skLineSegment(sketch, "E372", {"start": v(57924.07, 51838.21) * mm, "end": v(57793.68, 52268.9) * mm});
            skLineSegment(sketch, "E373", {"start": v(55773.63, 58460.66) * mm, "end": v(59287.5, 52158.7) * mm});
            skLineSegment(sketch, "E374", {"start": v(55677.4, 58222.57) * mm, "end": v(58991.9, 52278.2) * mm});
            skLineSegment(sketch, "E375", {"start": v(59287.5, 52158.7) * mm, "end": v(53342.63, 50359.31) * mm});
            skLineSegment(sketch, "E376", {"start": v(58991.9, 52278.2) * mm, "end": v(53284.69, 50550.73) * mm});
            skFitSpline(sketch, "E377", {"points": [v(50033.58, 70237.61) * mm, v(50033.58, 70157.21) * mm, v(50114.02, 70018.01) * mm, v(50253.28, 69937.61) * mm, v(50414.15, 69937.61) * mm, v(50553.4, 70018.01) * mm, v(50633.84, 70157.21) * mm, v(50633.84, 70318.01) * mm, v(50553.4, 70457.21) * mm, v(50414.15, 70537.61) * mm, v(50253.28, 70537.61) * mm, v(50114.02, 70457.21) * mm, v(50033.58, 70318.01) * mm, v(50033.58, 70237.61) * mm]});
            skLineSegment(sketch, "E378", {"start": v(30437.38, 72606.71) * mm, "end": v(53075.2, 75510.7) * mm});
            skLineSegment(sketch, "E379", {"start": v(31027.58, 72279.15) * mm, "end": v(52857.63, 75079.51) * mm});
            skLineSegment(sketch, "E380", {"start": v(66559.72, 50502.1) * mm, "end": v(54412.29, 46825.33) * mm});
            skLineSegment(sketch, "E381", {"start": v(39517.02, 53123.18) * mm, "end": v(38457.35, 56624.15) * mm});
            skLineSegment(sketch, "E382", {"start": v(39977.46, 52844.63) * mm, "end": v(38917.8, 56345.6) * mm});
            skLineSegment(sketch, "E383", {"start": v(38457.35, 56624.15) * mm, "end": v(44386.82, 58418.88) * mm});
            skLineSegment(sketch, "E384", {"start": v(44502.7, 58036.03) * mm, "end": v(44386.82, 58418.88) * mm});
            skLineSegment(sketch, "E385", {"start": v(38917.8, 56345.6) * mm, "end": v(44502.7, 58036.03) * mm});
            skLineSegment(sketch, "E386", {"start": v(54412.29, 46825.33) * mm, "end": v(50356.27, 60225.7) * mm});
            skLineSegment(sketch, "E387", {"start": v(50089.3, 59726.98) * mm, "end": v(49336.06, 59499) * mm});
            skLineSegment(sketch, "E388", {"start": v(49220.18, 59881.84) * mm, "end": v(49336.06, 59499) * mm});
            skLineSegment(sketch, "E389", {"start": v(50356.27, 60225.7) * mm, "end": v(49220.18, 59881.84) * mm});
            skLineSegment(sketch, "E390", {"start": v(66559.72, 50502.1) * mm, "end": v(52857.63, 75079.51) * mm});
            skLineSegment(sketch, "E391", {"start": v(67150.92, 50263.13) * mm, "end": v(53075.2, 75510.7) * mm});
            skLineSegment(sketch, "E392", {"start": v(32831.65, 66077.32) * mm, "end": v(36984.61, 52356.67) * mm});
            skLineSegment(sketch, "E393", {"start": v(32448.8, 65961.44) * mm, "end": v(36717.64, 51857.95) * mm});
            skLineSegment(sketch, "E394", {"start": v(36984.61, 52356.67) * mm, "end": v(39517.02, 53123.18) * mm});
            skLineSegment(sketch, "E395", {"start": v(36717.64, 51857.95) * mm, "end": v(39977.46, 52844.63) * mm});
            skLineSegment(sketch, "E396", {"start": v(32448.77, 65961.43) * mm, "end": v(30437.38, 72606.71) * mm});
            skLineSegment(sketch, "E397", {"start": v(32898.61, 66097.6) * mm, "end": v(31027.58, 72279.15) * mm});
            skLineSegment(sketch, "E398", {"start": v(32448.77, 65961.43) * mm, "end": v(32448.8, 65961.44) * mm});
            skLineSegment(sketch, "E399", {"start": v(32831.65, 66077.32) * mm, "end": v(32898.61, 66097.6) * mm});
            skCircle(sketch, "E400", {"center": v(40161.14, 53266.98) * mm, "radius": 300 * mm});
            skCircle(sketch, "E401", {"center": v(39509.32, 55420.5) * mm, "radius": 300 * mm});
            skCircle(sketch, "E402", {"center": v(39726.6, 54702.66) * mm, "radius": 300 * mm});
            skCircle(sketch, "E403", {"center": v(39943.87, 53984.82) * mm, "radius": 300 * mm});
            skCircle(sketch, "E404", {"center": v(53400.19, 75854.85) * mm, "radius": 300 * mm});
            skCircle(sketch, "E405", {"center": v(53759.7, 75202) * mm, "radius": 300 * mm});
            skCircle(sketch, "E406", {"center": v(54119.23, 74549.16) * mm, "radius": 300 * mm});
            skCircle(sketch, "E407", {"center": v(54478.74, 73896.31) * mm, "radius": 300 * mm});
            skCircle(sketch, "E408", {"center": v(54838.26, 73243.47) * mm, "radius": 300 * mm});
            skCircle(sketch, "E409", {"center": v(55197.78, 72590.62) * mm, "radius": 300 * mm});
            skCircle(sketch, "E410", {"center": v(55557.3, 71937.77) * mm, "radius": 300 * mm});
            skCircle(sketch, "E411", {"center": v(55916.82, 71284.93) * mm, "radius": 300 * mm});
            skCircle(sketch, "E412", {"center": v(56276.34, 70632.08) * mm, "radius": 300 * mm});
            skCircle(sketch, "E413", {"center": v(56635.85, 69979.24) * mm, "radius": 300 * mm});
            skCircle(sketch, "E414", {"center": v(56995.37, 69326.4) * mm, "radius": 300 * mm});
            skCircle(sketch, "E415", {"center": v(57354.9, 68673.55) * mm, "radius": 300 * mm});
            skCircle(sketch, "E416", {"center": v(57714.4, 68020.7) * mm, "radius": 300 * mm});
            skCircle(sketch, "E417", {"center": v(58073.93, 67367.85) * mm, "radius": 300 * mm});
            skCircle(sketch, "E418", {"center": v(58433.45, 66715) * mm, "radius": 300 * mm});
            skCircle(sketch, "E419", {"center": v(58792.97, 66062.16) * mm, "radius": 300 * mm});
            skCircle(sketch, "E420", {"center": v(59152.48, 65409.32) * mm, "radius": 300 * mm});
            skCircle(sketch, "E421", {"center": v(59512, 64756.47) * mm, "radius": 300 * mm});
            skCircle(sketch, "E422", {"center": v(59871.52, 64103.62) * mm, "radius": 300 * mm});
            skCircle(sketch, "E423", {"center": v(60231.04, 63450.78) * mm, "radius": 300 * mm});
            skCircle(sketch, "E424", {"center": v(60590.56, 62797.93) * mm, "radius": 300 * mm});
            skCircle(sketch, "E425", {"center": v(60950.08, 62145.09) * mm, "radius": 300 * mm});
            skCircle(sketch, "E426", {"center": v(61309.6, 61492.24) * mm, "radius": 300 * mm});
            skCircle(sketch, "E427", {"center": v(61669.11, 60839.4) * mm, "radius": 300 * mm});
            skCircle(sketch, "E428", {"center": v(62028.63, 60186.55) * mm, "radius": 300 * mm});
            skCircle(sketch, "E429", {"center": v(62388.15, 59533.7) * mm, "radius": 300 * mm});
            skCircle(sketch, "E430", {"center": v(62747.67, 58880.86) * mm, "radius": 300 * mm});
            skCircle(sketch, "E431", {"center": v(63107.19, 58228.01) * mm, "radius": 300 * mm});
            skCircle(sketch, "E432", {"center": v(63466.7, 57575.16) * mm, "radius": 300 * mm});
            skCircle(sketch, "E433", {"center": v(63826.22, 56922.32) * mm, "radius": 300 * mm});
            skCircle(sketch, "E434", {"center": v(64185.74, 56269.47) * mm, "radius": 300 * mm});
            skCircle(sketch, "E435", {"center": v(64545.26, 55616.63) * mm, "radius": 300 * mm});
            skCircle(sketch, "E436", {"center": v(64904.78, 54963.78) * mm, "radius": 300 * mm});
            skCircle(sketch, "E437", {"center": v(65264.3, 54310.94) * mm, "radius": 300 * mm});
            skCircle(sketch, "E438", {"center": v(65623.81, 53658.09) * mm, "radius": 300 * mm});
            skCircle(sketch, "E439", {"center": v(65983.33, 53005.24) * mm, "radius": 300 * mm});
            skCircle(sketch, "E440", {"center": v(66342.85, 52352.4) * mm, "radius": 300 * mm});
            skCircle(sketch, "E441", {"center": v(66702.37, 51699.55) * mm, "radius": 300 * mm});
            skCircle(sketch, "E442", {"center": v(67061.89, 51046.7) * mm, "radius": 300 * mm});
            skCircle(sketch, "E443", {"center": v(67421.4, 50393.86) * mm, "radius": 300 * mm});
            skCircle(sketch, "E444", {"center": v(67780.92, 49741.01) * mm, "radius": 300 * mm});
            skCircle(sketch, "E445", {"center": v(53579.95, 75528.43) * mm, "radius": 300 * mm});
            skCircle(sketch, "E446", {"center": v(53939.47, 74875.58) * mm, "radius": 300 * mm});
            skCircle(sketch, "E447", {"center": v(54298.99, 74222.74) * mm, "radius": 300 * mm});
            skCircle(sketch, "E448", {"center": v(54658.5, 73569.89) * mm, "radius": 300 * mm});
            skCircle(sketch, "E449", {"center": v(55018.02, 72917.04) * mm, "radius": 300 * mm});
            skCircle(sketch, "E450", {"center": v(55377.54, 72264.2) * mm, "radius": 300 * mm});
            skCircle(sketch, "E451", {"center": v(55737.06, 71611.35) * mm, "radius": 300 * mm});
            skCircle(sketch, "E452", {"center": v(56096.58, 70958.5) * mm, "radius": 300 * mm});
            skCircle(sketch, "E453", {"center": v(56456.1, 70305.66) * mm, "radius": 300 * mm});
            skCircle(sketch, "E454", {"center": v(56815.61, 69652.81) * mm, "radius": 300 * mm});
            skCircle(sketch, "E455", {"center": v(57175.13, 68999.97) * mm, "radius": 300 * mm});
            skCircle(sketch, "E456", {"center": v(57534.65, 68347.12) * mm, "radius": 300 * mm});
            skCircle(sketch, "E457", {"center": v(57894.17, 67694.28) * mm, "radius": 300 * mm});
            skCircle(sketch, "E458", {"center": v(58253.69, 67041.43) * mm, "radius": 300 * mm});
            skCircle(sketch, "E459", {"center": v(58613.2, 66388.58) * mm, "radius": 300 * mm});
            skCircle(sketch, "E460", {"center": v(58972.72, 65735.74) * mm, "radius": 300 * mm});
            skCircle(sketch, "E461", {"center": v(59332.24, 65082.9) * mm, "radius": 300 * mm});
            skCircle(sketch, "E462", {"center": v(59691.76, 64430.05) * mm, "radius": 300 * mm});
            skCircle(sketch, "E463", {"center": v(60051.28, 63777.2) * mm, "radius": 300 * mm});
            skCircle(sketch, "E464", {"center": v(60410.8, 63124.35) * mm, "radius": 300 * mm});
            skCircle(sketch, "E465", {"center": v(60770.32, 62471.5) * mm, "radius": 300 * mm});
            skCircle(sketch, "E466", {"center": v(61129.83, 61818.66) * mm, "radius": 300 * mm});
            skCircle(sketch, "E467", {"center": v(61489.35, 61165.82) * mm, "radius": 300 * mm});
            skCircle(sketch, "E468", {"center": v(61848.87, 60512.97) * mm, "radius": 300 * mm});
            skCircle(sketch, "E469", {"center": v(62208.39, 59860.13) * mm, "radius": 300 * mm});
            skCircle(sketch, "E470", {"center": v(62567.9, 59207.28) * mm, "radius": 300 * mm});
            skCircle(sketch, "E471", {"center": v(62927.43, 58554.43) * mm, "radius": 300 * mm});
            skCircle(sketch, "E472", {"center": v(63286.94, 57901.59) * mm, "radius": 300 * mm});
            skCircle(sketch, "E473", {"center": v(63646.46, 57248.74) * mm, "radius": 300 * mm});
            skCircle(sketch, "E474", {"center": v(64005.98, 56595.9) * mm, "radius": 300 * mm});
            skCircle(sketch, "E475", {"center": v(64725.02, 55290.2) * mm, "radius": 300 * mm});
            skCircle(sketch, "E476", {"center": v(65084.54, 54637.36) * mm, "radius": 300 * mm});
            skCircle(sketch, "E477", {"center": v(65444.05, 53984.51) * mm, "radius": 300 * mm});
            skCircle(sketch, "E478", {"center": v(64365.5, 55943.05) * mm, "radius": 300 * mm});
            skCircle(sketch, "E479", {"center": v(65803.57, 53331.67) * mm, "radius": 300 * mm});
            skCircle(sketch, "E480", {"center": v(66163.1, 52678.82) * mm, "radius": 300 * mm});
            skCircle(sketch, "E481", {"center": v(66882.13, 51373.13) * mm, "radius": 300 * mm});
            skCircle(sketch, "E482", {"center": v(67241.65, 50720.28) * mm, "radius": 300 * mm});
            skCircle(sketch, "E483", {"center": v(67601.17, 50067.44) * mm, "radius": 300 * mm});
            skCircle(sketch, "E484", {"center": v(66522.61, 52025.97) * mm, "radius": 300 * mm});
            skCircle(sketch, "E485", {"center": v(49888.89, 59352.88) * mm, "radius": 300 * mm});
            skCircle(sketch, "E486", {"center": v(53945.1, 45952.56) * mm, "radius": 300 * mm});
            skCircle(sketch, "E487", {"center": v(44086.3, 57596.56) * mm, "radius": 300 * mm});
            skCircle(sketch, "E488", {"center": v(30047.42, 72859.15) * mm, "radius": 300 * mm});
            skCircle(sketch, "E489", {"center": v(42647.96, 57161.2) * mm, "radius": 300 * mm});
            skCircle(sketch, "E490", {"center": v(43367, 57378.84) * mm, "radius": 300 * mm});
            skCircle(sketch, "E491", {"center": v(33483.8, 61505.57) * mm, "radius": 300 * mm});
            skCircle(sketch, "E492", {"center": v(33275.53, 62192.53) * mm, "radius": 300 * mm});
            skCircle(sketch, "E493", {"center": v(33066.54, 62883.79) * mm, "radius": 300 * mm});
            skCircle(sketch, "E494", {"center": v(32860.74, 63564.43) * mm, "radius": 300 * mm});
            skCircle(sketch, "E495", {"center": v(32644.34, 64279.4) * mm, "radius": 300 * mm});
            skCircle(sketch, "E496", {"center": v(32427.93, 64994.36) * mm, "radius": 300 * mm});
            skCircle(sketch, "E497", {"center": v(32211.53, 65709.33) * mm, "radius": 300 * mm});
            skCircle(sketch, "E498", {"center": v(31995.12, 66424.3) * mm, "radius": 300 * mm});
            skCircle(sketch, "E499", {"center": v(31778.71, 67139.26) * mm, "radius": 300 * mm});
            skCircle(sketch, "E500", {"center": v(31562.3, 67854.23) * mm, "radius": 300 * mm});
            skCircle(sketch, "E501", {"center": v(31345.9, 68569.2) * mm, "radius": 300 * mm});
            skCircle(sketch, "E502", {"center": v(31129.5, 69284.16) * mm, "radius": 300 * mm});
            skCircle(sketch, "E503", {"center": v(30913.1, 69999.13) * mm, "radius": 300 * mm});
            skCircle(sketch, "E504", {"center": v(30696.68, 70714.1) * mm, "radius": 300 * mm});
            skCircle(sketch, "E505", {"center": v(30480.28, 71429.06) * mm, "radius": 300 * mm});
            skCircle(sketch, "E506", {"center": v(30263.87, 72144.03) * mm, "radius": 300 * mm});
            skCircle(sketch, "E507", {"center": v(30777.44, 72952.8) * mm, "radius": 300 * mm});
            skCircle(sketch, "E508", {"center": v(31507.46, 73046.44) * mm, "radius": 300 * mm});
            skCircle(sketch, "E509", {"center": v(32237.47, 73140.09) * mm, "radius": 300 * mm});
            skCircle(sketch, "E510", {"center": v(32967.5, 73233.74) * mm, "radius": 300 * mm});
            skCircle(sketch, "E511", {"center": v(33697.51, 73327.38) * mm, "radius": 300 * mm});
            skCircle(sketch, "E512", {"center": v(34427.53, 73421.03) * mm, "radius": 300 * mm});
            skCircle(sketch, "E513", {"center": v(35157.55, 73514.68) * mm, "radius": 300 * mm});
            skCircle(sketch, "E514", {"center": v(35887.56, 73608.32) * mm, "radius": 300 * mm});
            skCircle(sketch, "E515", {"center": v(36617.58, 73701.97) * mm, "radius": 300 * mm});
            skCircle(sketch, "E516", {"center": v(37347.6, 73795.62) * mm, "radius": 300 * mm});
            skCircle(sketch, "E517", {"center": v(38077.62, 73889.27) * mm, "radius": 300 * mm});
            skCircle(sketch, "E518", {"center": v(38807.64, 73982.91) * mm, "radius": 300 * mm});
            skCircle(sketch, "E519", {"center": v(39537.65, 74076.56) * mm, "radius": 300 * mm});
            skCircle(sketch, "E520", {"center": v(40267.67, 74170.2) * mm, "radius": 300 * mm});
            skCircle(sketch, "E521", {"center": v(40997.7, 74263.85) * mm, "radius": 300 * mm});
            skCircle(sketch, "E522", {"center": v(41727.7, 74357.5) * mm, "radius": 300 * mm});
            skCircle(sketch, "E523", {"center": v(42457.73, 74451.15) * mm, "radius": 300 * mm});
            skCircle(sketch, "E524", {"center": v(43187.74, 74544.8) * mm, "radius": 300 * mm});
            skCircle(sketch, "E525", {"center": v(43917.76, 74638.44) * mm, "radius": 300 * mm});
            skCircle(sketch, "E526", {"center": v(44647.78, 74732.09) * mm, "radius": 300 * mm});
            skCircle(sketch, "E527", {"center": v(45377.8, 74825.74) * mm, "radius": 300 * mm});
            skCircle(sketch, "E528", {"center": v(46107.82, 74919.38) * mm, "radius": 300 * mm});
            skCircle(sketch, "E529", {"center": v(46837.83, 75013.03) * mm, "radius": 300 * mm});
            skCircle(sketch, "E530", {"center": v(47567.85, 75106.68) * mm, "radius": 300 * mm});
            skCircle(sketch, "E531", {"center": v(48297.87, 75200.32) * mm, "radius": 300 * mm});
            skCircle(sketch, "E532", {"center": v(49027.89, 75293.97) * mm, "radius": 300 * mm});
            skCircle(sketch, "E533", {"center": v(49757.9, 75387.62) * mm, "radius": 300 * mm});
            skCircle(sketch, "E534", {"center": v(50487.92, 75481.26) * mm, "radius": 300 * mm});
            skCircle(sketch, "E535", {"center": v(51217.94, 75574.91) * mm, "radius": 300 * mm});
            skCircle(sketch, "E536", {"center": v(51947.96, 75668.56) * mm, "radius": 300 * mm});
            skCircle(sketch, "E537", {"center": v(52677.98, 75762.2) * mm, "radius": 300 * mm});
            skCircle(sketch, "E538", {"center": v(54664.85, 46170.41) * mm, "radius": 300 * mm});
            skCircle(sketch, "E539", {"center": v(55384.6, 46388.28) * mm, "radius": 300 * mm});
            skCircle(sketch, "E540", {"center": v(56104.35, 46606.14) * mm, "radius": 300 * mm});
            skCircle(sketch, "E541", {"center": v(56824.1, 46824) * mm, "radius": 300 * mm});
            skCircle(sketch, "E542", {"center": v(57543.85, 47041.87) * mm, "radius": 300 * mm});
            skCircle(sketch, "E543", {"center": v(58263.6, 47259.73) * mm, "radius": 300 * mm});
            skCircle(sketch, "E544", {"center": v(58983.35, 47477.6) * mm, "radius": 300 * mm});
            skCircle(sketch, "E545", {"center": v(59703.1, 47695.46) * mm, "radius": 300 * mm});
            skCircle(sketch, "E546", {"center": v(60422.84, 47913.33) * mm, "radius": 300 * mm});
            skCircle(sketch, "E547", {"center": v(61142.6, 48131.2) * mm, "radius": 300 * mm});
            skCircle(sketch, "E548", {"center": v(61862.34, 48349.06) * mm, "radius": 300 * mm});
            skCircle(sketch, "E549", {"center": v(62582.1, 48566.92) * mm, "radius": 300 * mm});
            skCircle(sketch, "E550", {"center": v(63301.84, 48784.78) * mm, "radius": 300 * mm});
            skCircle(sketch, "E551", {"center": v(64021.6, 49002.65) * mm, "radius": 300 * mm});
            skCircle(sketch, "E552", {"center": v(64741.34, 49220.51) * mm, "radius": 300 * mm});
            skCircle(sketch, "E553", {"center": v(65461.09, 49438.38) * mm, "radius": 300 * mm});
            skCircle(sketch, "E554", {"center": v(66180.84, 49656.24) * mm, "radius": 300 * mm});
            skCircle(sketch, "E555", {"center": v(66900.59, 49874.1) * mm, "radius": 300 * mm});
            skCircle(sketch, "E556", {"center": v(53731.58, 46657.95) * mm, "radius": 300 * mm});
            skCircle(sketch, "E557", {"center": v(53518.06, 47363.34) * mm, "radius": 300 * mm});
            skCircle(sketch, "E558", {"center": v(53304.54, 48068.73) * mm, "radius": 300 * mm});
            skCircle(sketch, "E559", {"center": v(53091.02, 48774.13) * mm, "radius": 300 * mm});
            skCircle(sketch, "E560", {"center": v(52877.5, 49479.52) * mm, "radius": 300 * mm});
            skCircle(sketch, "E561", {"center": v(52663.99, 50184.91) * mm, "radius": 300 * mm});
            skCircle(sketch, "E562", {"center": v(52450.47, 50890.3) * mm, "radius": 300 * mm});
            skCircle(sketch, "E563", {"center": v(52236.95, 51595.7) * mm, "radius": 300 * mm});
            skCircle(sketch, "E564", {"center": v(52023.43, 52301.1) * mm, "radius": 300 * mm});
            skCircle(sketch, "E565", {"center": v(51809.91, 53006.48) * mm, "radius": 300 * mm});
            skCircle(sketch, "E566", {"center": v(51596.4, 53711.88) * mm, "radius": 300 * mm});
            skCircle(sketch, "E567", {"center": v(51382.87, 54417.27) * mm, "radius": 300 * mm});
            skCircle(sketch, "E568", {"center": v(51169.35, 55122.66) * mm, "radius": 300 * mm});
            skCircle(sketch, "E569", {"center": v(50955.84, 55828.05) * mm, "radius": 300 * mm});
            skCircle(sketch, "E570", {"center": v(50742.32, 56533.45) * mm, "radius": 300 * mm});
            skCircle(sketch, "E571", {"center": v(50528.8, 57238.84) * mm, "radius": 300 * mm});
            skCircle(sketch, "E572", {"center": v(50315.28, 57944.23) * mm, "radius": 300 * mm});
            skCircle(sketch, "E573", {"center": v(50101.76, 58649.62) * mm, "radius": 300 * mm});
            skLineSegment(sketch, "E574", {"start": v(40350.08, 52642.78) * mm, "end": v(39290.08, 56144.84) * mm});
            skLineSegment(sketch, "E575", {"start": v(36517.3, 51483.84) * mm, "end": v(35457.62, 54984.83) * mm});
            skLineSegment(sketch, "E576", {"start": v(53945.1, 45952.56) * mm, "end": v(49888.89, 59352.88) * mm});
            skLineSegment(sketch, "E577", {"start": v(53945.1, 45952.56) * mm, "end": v(66900.59, 49874.1) * mm});
            skLineSegment(sketch, "E578", {"start": v(53400.19, 75854.85) * mm, "end": v(67780.92, 49741.01) * mm});
            skLineSegment(sketch, "E579", {"start": v(30047.42, 72859.15) * mm, "end": v(53400.19, 75854.85) * mm});
            skCircle(sketch, "E580", {"center": v(33621.22, 60726.77) * mm, "radius": 375 * mm});
            skLineSegment(sketch, "E581", {"start": v(35123.8, 56106.32) * mm, "end": v(35600.08, 54499.8) * mm});
            skLineSegment(sketch, "E582", {"start": v(34931.23, 56052.24) * mm, "end": v(35408.33, 54442.95) * mm});
            skLineSegment(sketch, "E583", {"start": v(34713.87, 57650.93) * mm, "end": v(35123.8, 56106.32) * mm});
            skLineSegment(sketch, "E584", {"start": v(34522.07, 57593.97) * mm, "end": v(34931.23, 56052.24) * mm});
            skLineSegment(sketch, "E585", {"start": v(34069.7, 59608.22) * mm, "end": v(34713.87, 57650.93) * mm});
            skLineSegment(sketch, "E586", {"start": v(33879.73, 59545.7) * mm, "end": v(34522.07, 57593.97) * mm});
            skLineSegment(sketch, "E587", {"start": v(33879.73, 59545.7) * mm, "end": v(34069.7, 59608.22) * mm});
            skCircle(sketch, "E588", {"center": v(35503.23, 54471.13) * mm, "radius": 375 * mm});
            skCircle(sketch, "E589", {"center": v(35024.65, 56078.4) * mm, "radius": 375 * mm});
            skCircle(sketch, "E590", {"center": v(34617.97, 57622.45) * mm, "radius": 300 * mm});
            skCircle(sketch, "E591", {"center": v(33974.72, 59576.96) * mm, "radius": 375 * mm});
            skCircle(sketch, "E592", {"center": v(35948.4, 52971.91) * mm, "radius": 375 * mm});
            skCircle(sketch, "E593", {"center": v(36387.31, 51517) * mm, "radius": 375 * mm});
            skCircle(sketch, "E594", {"center": v(37796.6, 51792.76) * mm, "radius": 375 * mm});
            skCircle(sketch, "E595", {"center": v(39835.27, 56332.54) * mm, "radius": 375 * mm});
            skCircle(sketch, "E596", {"center": v(41846.6, 56950.07) * mm, "radius": 375 * mm});
            skLineSegment(sketch, "E597", {"start": v(35706.21, 54140.42) * mm, "end": v(35937.9, 53360.17) * mm});
            skLineSegment(sketch, "E598", {"start": v(35746.17, 53303.24) * mm, "end": v(35937.9, 53360.17) * mm});
            skLineSegment(sketch, "E599", {"start": v(35514.49, 54083.49) * mm, "end": v(35746.17, 53303.24) * mm});
            skLineSegment(sketch, "E600", {"start": v(35514.49, 54083.49) * mm, "end": v(35706.21, 54140.42) * mm});
            skLineSegment(sketch, "E601", {"start": v(36152.82, 52642.08) * mm, "end": v(36375.12, 51905.21) * mm});
            skLineSegment(sketch, "E602", {"start": v(36183.64, 51847.45) * mm, "end": v(36375.12, 51905.21) * mm});
            skLineSegment(sketch, "E603", {"start": v(35961.34, 52584.32) * mm, "end": v(36183.64, 51847.45) * mm});
            skLineSegment(sketch, "E604", {"start": v(35961.34, 52584.32) * mm, "end": v(36152.82, 52642.08) * mm});
            skLineSegment(sketch, "E605", {"start": v(36736.53, 51687.4) * mm, "end": v(37409.39, 51818.95) * mm});
            skLineSegment(sketch, "E606", {"start": v(37447.76, 51622.67) * mm, "end": v(37409.39, 51818.95) * mm});
            skLineSegment(sketch, "E607", {"start": v(36774.9, 51491.12) * mm, "end": v(37447.76, 51622.67) * mm});
            skLineSegment(sketch, "E608", {"start": v(36774.9, 51491.12) * mm, "end": v(36736.53, 51687.4) * mm});
            skLineSegment(sketch, "E609", {"start": v(40164.4, 56538.2) * mm, "end": v(41458.77, 56935.6) * mm});
            skLineSegment(sketch, "E610", {"start": v(41517.47, 56744.4) * mm, "end": v(41458.77, 56935.6) * mm});
            skLineSegment(sketch, "E611", {"start": v(40223.1, 56347) * mm, "end": v(41517.47, 56744.4) * mm});
            skLineSegment(sketch, "E612", {"start": v(40223.1, 56347) * mm, "end": v(40164.4, 56538.2) * mm});
            skCircle(sketch, "E613", {"center": v(38530.81, 52093.36) * mm, "radius": 300 * mm});
            skCircle(sketch, "E614", {"center": v(39248.7, 52310.48) * mm, "radius": 300 * mm});
            skCircle(sketch, "E615", {"center": v(39966.5, 52527.84) * mm, "radius": 300 * mm});
            skLineSegment(sketch, "E616", {"start": v(39290.08, 56144.84) * mm, "end": v(49888.89, 59352.88) * mm});
            skLineSegment(sketch, "E617", {"start": v(36517.4, 51483.94) * mm, "end": v(40348.6, 52643.57) * mm});
            skLineSegment(sketch, "E618", {"start": v(30047.42, 72859.15) * mm, "end": v(36517.66, 51482.64) * mm});
            skLineSegment(sketch, "E619", {"start": v(43861.14, 60155.86) * mm, "end": v(43459.76, 61481.53) * mm});
            skLineSegment(sketch, "E620", {"start": v(43746.89, 61568.47) * mm, "end": v(43459.76, 61481.53) * mm});
            skLineSegment(sketch, "E621", {"start": v(44148.27, 60242.8) * mm, "end": v(43746.89, 61568.47) * mm});
            skLineSegment(sketch, "E622", {"start": v(44643.85, 60262.18) * mm, "end": v(44184.43, 60123.13) * mm});
            skLineSegment(sketch, "E623", {"start": v(44571.42, 60501.46) * mm, "end": v(43824.88, 60275.5) * mm});
            skLineSegment(sketch, "E624", {"start": v(46706.46, 60886.47) * mm, "end": v(45505.25, 60522.9) * mm});
            skLineSegment(sketch, "E625", {"start": v(46634.04, 61125.75) * mm, "end": v(45432.83, 60762.18) * mm});
            skLineSegment(sketch, "E626", {"start": v(48505.85, 61431.1) * mm, "end": v(47759.3, 61205.13) * mm});
            skLineSegment(sketch, "E627", {"start": v(48672.7, 61742.8) * mm, "end": v(47686.87, 61444.41) * mm});
            skLineSegment(sketch, "E628", {"start": v(45469.04, 60642.54) * mm, "end": v(45505.25, 60522.9) * mm});
            skLineSegment(sketch, "E629", {"start": v(44607.63, 60381.82) * mm, "end": v(44643.85, 60262.18) * mm});
            skLineSegment(sketch, "E630", {"start": v(45469.04, 60642.54) * mm, "end": v(45432.83, 60762.18) * mm});
            skLineSegment(sketch, "E631", {"start": v(44607.63, 60381.82) * mm, "end": v(44571.42, 60501.46) * mm});
            skLineSegment(sketch, "E632", {"start": v(44571.42, 60501.46) * mm, "end": v(45432.83, 60762.18) * mm});
            skLineSegment(sketch, "E633", {"start": v(44643.85, 60262.18) * mm, "end": v(45505.25, 60522.9) * mm});
            skLineSegment(sketch, "E634", {"start": v(47723.08, 61324.77) * mm, "end": v(47759.3, 61205.13) * mm});
            skLineSegment(sketch, "E635", {"start": v(46670.25, 61006.11) * mm, "end": v(46706.46, 60886.47) * mm});
            skLineSegment(sketch, "E636", {"start": v(47723.08, 61324.77) * mm, "end": v(47686.87, 61444.41) * mm});
            skLineSegment(sketch, "E637", {"start": v(46670.25, 61006.11) * mm, "end": v(46634.04, 61125.75) * mm});
            skLineSegment(sketch, "E638", {"start": v(46634.04, 61125.75) * mm, "end": v(47686.87, 61444.41) * mm});
            skLineSegment(sketch, "E639", {"start": v(46706.46, 60886.47) * mm, "end": v(47759.3, 61205.13) * mm});
            skLineSegment(sketch, "E640", {"start": v(48672.7, 61742.8) * mm, "end": v(49476.62, 59086.75) * mm});
            skLineSegment(sketch, "E641", {"start": v(48505.85, 61431.1) * mm, "end": v(49091.04, 59497.67) * mm});
            skLineSegment(sketch, "E642", {"start": v(44184.43, 60123.13) * mm, "end": v(44769.56, 58189.64) * mm});
            skLineSegment(sketch, "E643", {"start": v(43824.88, 60275.5) * mm, "end": v(44628.7, 57619.38) * mm});
            skLineSegment(sketch, "E644", {"start": v(46549.88, 58728.5) * mm, "end": v(45964.7, 60661.96) * mm});
            skLineSegment(sketch, "E645", {"start": v(46741.3, 58786.45) * mm, "end": v(46156.12, 60719.9) * mm});
            skLineSegment(sketch, "E646", {"start": v(49725.98, 58953.26) * mm, "end": v(44495.22, 57370.06) * mm});
            skLineSegment(sketch, "E647", {"start": v(49476.62, 59086.75) * mm, "end": v(44628.7, 57619.42) * mm});
            skLineSegment(sketch, "E648", {"start": v(49476.62, 59086.75) * mm, "end": v(44628.7, 57619.38) * mm});
            skLineSegment(sketch, "E649", {"start": v(46549.88, 58728.5) * mm, "end": v(44769.56, 58189.64) * mm});
            skLineSegment(sketch, "E650", {"start": v(49091.04, 59497.67) * mm, "end": v(46741.3, 58786.45) * mm});
            skLineSegment(sketch, "E651", {"start": v(44386.73, 58418.85) * mm, "end": v(44628.7, 57619.42) * mm});
            skLineSegment(sketch, "E652", {"start": v(44195.31, 58360.91) * mm, "end": v(44495.22, 57370.06) * mm});
            skLineSegment(sketch, "E653", {"start": v(44195.31, 58360.91) * mm, "end": v(44386.73, 58418.85) * mm});
            skLineSegment(sketch, "E654", {"start": v(49476.62, 59086.75) * mm, "end": v(49350.51, 59503.37) * mm});
            skLineSegment(sketch, "E655", {"start": v(49725.98, 58953.26) * mm, "end": v(49541.94, 59561.3) * mm});
            skLineSegment(sketch, "E656", {"start": v(34583.64, 74073.32) * mm, "end": v(34277.71, 74103.31) * mm});
            skLineSegment(sketch, "E657", {"start": v(36509.2, 74336.72) * mm, "end": v(36210.42, 74264.44) * mm});
            skLineSegment(sketch, "E658", {"start": v(38568.06, 74568.37) * mm, "end": v(38260.66, 74568.37) * mm});
            skLineSegment(sketch, "E659", {"start": v(40630.85, 74832.8) * mm, "end": v(40326.88, 74787.02) * mm});
            skLineSegment(sketch, "E660", {"start": v(42529.89, 75035.76) * mm, "end": v(42224.21, 75003.22) * mm});
            skLineSegment(sketch, "E661", {"start": v(44620.7, 75346.4) * mm, "end": v(44315.83, 75306.98) * mm});
            skLineSegment(sketch, "E662", {"start": v(46260.89, 75467.94) * mm, "end": v(45954.04, 75449.5) * mm});
            skLineSegment(sketch, "E663", {"start": v(48411.94, 75732.02) * mm, "end": v(48106.56, 75696.83) * mm});
            skLineSegment(sketch, "E664", {"start": v(34308.4, 74416.31) * mm, "end": v(34614.33, 74386.32) * mm});
            skLineSegment(sketch, "E665", {"start": v(34306.57, 74397.7) * mm, "end": v(34612.5, 74367.7) * mm});
            skLineSegment(sketch, "E666", {"start": v(34614.33, 74386.32) * mm, "end": v(34612.5, 74367.7) * mm});
            skLineSegment(sketch, "E667", {"start": v(34585.47, 74091.93) * mm, "end": v(34583.64, 74073.32) * mm});
            skLineSegment(sketch, "E668", {"start": v(34585.47, 74091.93) * mm, "end": v(34279.53, 74121.92) * mm});
            skLineSegment(sketch, "E669", {"start": v(34277.71, 74103.31) * mm, "end": v(34279.53, 74121.92) * mm});
            skLineSegment(sketch, "E670", {"start": v(34306.57, 74397.7) * mm, "end": v(34308.4, 74416.31) * mm});
            skLineSegment(sketch, "E671", {"start": v(34465.5, 74382.12) * mm, "end": v(34438.47, 74106.34) * mm});
            skLineSegment(sketch, "E672", {"start": v(34453.57, 74383.29) * mm, "end": v(34426.53, 74107.51) * mm});
            skLineSegment(sketch, "E673", {"start": v(36136.47, 74570.12) * mm, "end": v(36435.25, 74642.4) * mm});
            skLineSegment(sketch, "E674", {"start": v(36140.87, 74551.95) * mm, "end": v(36439.65, 74624.22) * mm});
            skLineSegment(sketch, "E675", {"start": v(36435.25, 74642.4) * mm, "end": v(36439.65, 74624.22) * mm});
            skLineSegment(sketch, "E676", {"start": v(36504.8, 74354.9) * mm, "end": v(36509.2, 74336.72) * mm});
            skLineSegment(sketch, "E677", {"start": v(36504.8, 74354.9) * mm, "end": v(36206.02, 74282.62) * mm});
            skLineSegment(sketch, "E678", {"start": v(36210.42, 74264.44) * mm, "end": v(36206.02, 74282.62) * mm});
            skLineSegment(sketch, "E679", {"start": v(36140.87, 74551.95) * mm, "end": v(36136.47, 74570.12) * mm});
            skLineSegment(sketch, "E680", {"start": v(36296.1, 74589.5) * mm, "end": v(36361.24, 74320.16) * mm});
            skLineSegment(sketch, "E681", {"start": v(36284.43, 74586.68) * mm, "end": v(36349.58, 74317.34) * mm});
            skLineSegment(sketch, "E682", {"start": v(38260.66, 74882.87) * mm, "end": v(38568.06, 74882.87) * mm});
            skLineSegment(sketch, "E683", {"start": v(38260.66, 74864.17) * mm, "end": v(38568.06, 74864.17) * mm});
            skLineSegment(sketch, "E684", {"start": v(38568.06, 74882.87) * mm, "end": v(38568.06, 74864.17) * mm});
            skLineSegment(sketch, "E685", {"start": v(38568.06, 74587.07) * mm, "end": v(38568.06, 74568.37) * mm});
            skLineSegment(sketch, "E686", {"start": v(38568.06, 74587.07) * mm, "end": v(38260.66, 74587.07) * mm});
            skLineSegment(sketch, "E687", {"start": v(38260.66, 74568.37) * mm, "end": v(38260.66, 74587.07) * mm});
            skLineSegment(sketch, "E688", {"start": v(38260.66, 74864.17) * mm, "end": v(38260.66, 74882.87) * mm});
            skLineSegment(sketch, "E689", {"start": v(38420.36, 74864.17) * mm, "end": v(38420.36, 74587.07) * mm});
            skLineSegment(sketch, "E690", {"start": v(38408.36, 74864.17) * mm, "end": v(38408.36, 74587.07) * mm});
            skLineSegment(sketch, "E691", {"start": v(40280.05, 75098.01) * mm, "end": v(40584.02, 75143.79) * mm});
            skLineSegment(sketch, "E692", {"start": v(40282.83, 75079.52) * mm, "end": v(40586.8, 75125.3) * mm});
            skLineSegment(sketch, "E693", {"start": v(40584.02, 75143.79) * mm, "end": v(40586.8, 75125.3) * mm});
            skLineSegment(sketch, "E694", {"start": v(40628.07, 74851.29) * mm, "end": v(40630.85, 74832.8) * mm});
            skLineSegment(sketch, "E695", {"start": v(40628.07, 74851.29) * mm, "end": v(40324.1, 74805.5) * mm});
            skLineSegment(sketch, "E696", {"start": v(40326.88, 74787.02) * mm, "end": v(40324.1, 74805.5) * mm});
            skLineSegment(sketch, "E697", {"start": v(40282.83, 75079.52) * mm, "end": v(40280.05, 75098.01) * mm});
            skLineSegment(sketch, "E698", {"start": v(40440.75, 75103.3) * mm, "end": v(40482.02, 74829.3) * mm});
            skLineSegment(sketch, "E699", {"start": v(40428.89, 75101.51) * mm, "end": v(40470.15, 74827.5) * mm});
            skLineSegment(sketch, "E700", {"start": v(42190.92, 75315.95) * mm, "end": v(42496.6, 75348.5) * mm});
            skLineSegment(sketch, "E701", {"start": v(42192.9, 75297.36) * mm, "end": v(42498.58, 75329.9) * mm});
            skLineSegment(sketch, "E702", {"start": v(42496.6, 75348.5) * mm, "end": v(42498.58, 75329.9) * mm});
            skLineSegment(sketch, "E703", {"start": v(42527.9, 75054.35) * mm, "end": v(42529.89, 75035.76) * mm});
            skLineSegment(sketch, "E704", {"start": v(42527.9, 75054.35) * mm, "end": v(42222.24, 75021.82) * mm});
            skLineSegment(sketch, "E705", {"start": v(42224.21, 75003.22) * mm, "end": v(42222.24, 75021.82) * mm});
            skLineSegment(sketch, "E706", {"start": v(42192.9, 75297.36) * mm, "end": v(42190.92, 75315.95) * mm});
            skLineSegment(sketch, "E707", {"start": v(42351.7, 75314.26) * mm, "end": v(42381.04, 75038.72) * mm});
            skLineSegment(sketch, "E708", {"start": v(42339.77, 75313) * mm, "end": v(42369.1, 75037.45) * mm});
            skLineSegment(sketch, "E709", {"start": v(44275.5, 75618.88) * mm, "end": v(44580.37, 75658.3) * mm});
            skLineSegment(sketch, "E710", {"start": v(44277.9, 75600.34) * mm, "end": v(44582.77, 75639.76) * mm});
            skLineSegment(sketch, "E711", {"start": v(44580.37, 75658.3) * mm, "end": v(44582.77, 75639.76) * mm});
            skLineSegment(sketch, "E712", {"start": v(44618.3, 75364.94) * mm, "end": v(44620.7, 75346.4) * mm});
            skLineSegment(sketch, "E713", {"start": v(44618.3, 75364.94) * mm, "end": v(44313.44, 75325.53) * mm});
            skLineSegment(sketch, "E714", {"start": v(44315.83, 75306.98) * mm, "end": v(44313.44, 75325.53) * mm});
            skLineSegment(sketch, "E715", {"start": v(44277.9, 75600.34) * mm, "end": v(44275.5, 75618.88) * mm});
            skLineSegment(sketch, "E716", {"start": v(44436.28, 75620.82) * mm, "end": v(44471.82, 75346) * mm});
            skLineSegment(sketch, "E717", {"start": v(44424.38, 75619.28) * mm, "end": v(44459.92, 75344.46) * mm});
            skLineSegment(sketch, "E718", {"start": v(45935.18, 75763.44) * mm, "end": v(46242.02, 75781.88) * mm});
            skLineSegment(sketch, "E719", {"start": v(45936.3, 75744.77) * mm, "end": v(46243.14, 75763.21) * mm});
            skLineSegment(sketch, "E720", {"start": v(46242.02, 75781.88) * mm, "end": v(46243.14, 75763.21) * mm});
            skLineSegment(sketch, "E721", {"start": v(46259.76, 75486.61) * mm, "end": v(46260.89, 75467.94) * mm});
            skLineSegment(sketch, "E722", {"start": v(46259.76, 75486.61) * mm, "end": v(45952.92, 75468.17) * mm});
            skLineSegment(sketch, "E723", {"start": v(45954.04, 75449.5) * mm, "end": v(45952.92, 75468.17) * mm});
            skLineSegment(sketch, "E724", {"start": v(45936.3, 75744.77) * mm, "end": v(45935.18, 75763.44) * mm});
            skLineSegment(sketch, "E725", {"start": v(46095.71, 75754.35) * mm, "end": v(46112.33, 75477.75) * mm});
            skLineSegment(sketch, "E726", {"start": v(46083.73, 75753.63) * mm, "end": v(46100.35, 75477.03) * mm});
            skLineSegment(sketch, "E727", {"start": v(48070.56, 76009.27) * mm, "end": v(48375.94, 76044.45) * mm});
            skLineSegment(sketch, "E728", {"start": v(48072.7, 75990.69) * mm, "end": v(48378.08, 76025.87) * mm});
            skLineSegment(sketch, "E729", {"start": v(48375.94, 76044.45) * mm, "end": v(48378.08, 76025.87) * mm});
            skLineSegment(sketch, "E730", {"start": v(48409.8, 75750.6) * mm, "end": v(48411.94, 75732.02) * mm});
            skLineSegment(sketch, "E731", {"start": v(48409.8, 75750.6) * mm, "end": v(48104.42, 75715.4) * mm});
            skLineSegment(sketch, "E732", {"start": v(48106.56, 75696.83) * mm, "end": v(48104.42, 75715.4) * mm});
            skLineSegment(sketch, "E733", {"start": v(48072.7, 75990.69) * mm, "end": v(48070.56, 76009.27) * mm});
            skLineSegment(sketch, "E734", {"start": v(48231.35, 76008.97) * mm, "end": v(48263.07, 75733.69) * mm});
            skLineSegment(sketch, "E735", {"start": v(48219.43, 76007.6) * mm, "end": v(48251.15, 75732.31) * mm});
            skLineSegment(sketch, "E736", {"start": v(34452, 74244.23) * mm, "end": v(34440.05, 74245.4) * mm});
            skLineSegment(sketch, "E737", {"start": v(36328.67, 74454.83) * mm, "end": v(36317, 74452) * mm});
            skLineSegment(sketch, "E738", {"start": v(38420.36, 74725.62) * mm, "end": v(38408.36, 74725.62) * mm});
            skLineSegment(sketch, "E739", {"start": v(40461.39, 74966.3) * mm, "end": v(40449.52, 74964.5) * mm});
            skLineSegment(sketch, "E740", {"start": v(42366.37, 75176.5) * mm, "end": v(42354.44, 75175.22) * mm});
            skLineSegment(sketch, "E741", {"start": v(44454.05, 75483.4) * mm, "end": v(44442.15, 75481.87) * mm});
            skLineSegment(sketch, "E742", {"start": v(46104.02, 75616.05) * mm, "end": v(46092.04, 75615.33) * mm});
            skLineSegment(sketch, "E743", {"start": v(48247.21, 75871.33) * mm, "end": v(48235.3, 75869.95) * mm});
            skCircle(sketch, "E744", {"center": v(34446.02, 74244.82) * mm, "radius": 300 * mm});
            skCircle(sketch, "E745", {"center": v(36322.84, 74453.42) * mm, "radius": 300 * mm});
            skCircle(sketch, "E746", {"center": v(38414.36, 74725.62) * mm, "radius": 300 * mm});
            skCircle(sketch, "E747", {"center": v(40455.45, 74965.4) * mm, "radius": 300 * mm});
            skCircle(sketch, "E748", {"center": v(42360.4, 75175.86) * mm, "radius": 300 * mm});
            skCircle(sketch, "E749", {"center": v(44448.1, 75482.64) * mm, "radius": 300 * mm});
            skCircle(sketch, "E750", {"center": v(46098.03, 75615.7) * mm, "radius": 300 * mm});
            skCircle(sketch, "E751", {"center": v(48241.25, 75870.64) * mm, "radius": 300 * mm});
            skLineSegment(sketch, "E752", {"start": v(35107.62, 70149.24) * mm, "end": v(35339.38, 69383.55) * mm});
            skLineSegment(sketch, "E753", {"start": v(35052.25, 69296.64) * mm, "end": v(35339.38, 69383.55) * mm});
            skLineSegment(sketch, "E754", {"start": v(34820.49, 70062.33) * mm, "end": v(35052.25, 69296.64) * mm});
            skLineSegment(sketch, "E755", {"start": v(34820.49, 70062.33) * mm, "end": v(35107.62, 70149.24) * mm});
            skLineSegment(sketch, "E756", {"start": v(44215.6, 60106.43) * mm, "end": v(45947.99, 60630.79) * mm});
            skLineSegment(sketch, "E757", {"start": v(45947.99, 60630.79) * mm, "end": v(46469.45, 58907.97) * mm});
            skLineSegment(sketch, "E758", {"start": v(46469.45, 58907.97) * mm, "end": v(44737.06, 58383.62) * mm});
            skLineSegment(sketch, "E759", {"start": v(44737.06, 58383.62) * mm, "end": v(44215.6, 60106.43) * mm});
            skLineSegment(sketch, "E760", {"start": v(46187.33, 60703.22) * mm, "end": v(48489.2, 61399.95) * mm});
            skLineSegment(sketch, "E761", {"start": v(48489.2, 61399.95) * mm, "end": v(49059.9, 59514.43) * mm});
            skLineSegment(sketch, "E762", {"start": v(49059.9, 59514.43) * mm, "end": v(46758.03, 58817.7) * mm});
            skLineSegment(sketch, "E763", {"start": v(46758.03, 58817.7) * mm, "end": v(46187.33, 60703.22) * mm});
            skLineSegment(sketch, "E764", {"start": v(46187.3, 60703.2) * mm, "end": v(49055.09, 59512.96) * mm});
            skLineSegment(sketch, "E765", {"start": v(48489.16, 61399.93) * mm, "end": v(46758, 58817.68) * mm});
            skLineSegment(sketch, "E766", {"start": v(45947.99, 60630.79) * mm, "end": v(44737.06, 58383.62) * mm});
            skLineSegment(sketch, "E767", {"start": v(44215.6, 60106.43) * mm, "end": v(46469.45, 58907.97) * mm});
            skLineSegment(sketch, "E768", {"start": v(51853.9, 57324.98) * mm, "end": v(51428.05, 58731.95) * mm});
            skLineSegment(sketch, "E769", {"start": v(51667.33, 58804.37) * mm, "end": v(51428.05, 58731.95) * mm});
            skLineSegment(sketch, "E770", {"start": v(52093.19, 57397.4) * mm, "end": v(51667.33, 58804.37) * mm});
            skLineSegment(sketch, "E771", {"start": v(58318.92, 63332.61) * mm, "end": v(58586.76, 62852.24) * mm});
            skLineSegment(sketch, "E772", {"start": v(58368.41, 62730.5) * mm, "end": v(58586.76, 62852.24) * mm});
            skLineSegment(sketch, "E773", {"start": v(58100.57, 63210.86) * mm, "end": v(58368.41, 62730.5) * mm});
            skLineSegment(sketch, "E774", {"start": v(58100.57, 63210.86) * mm, "end": v(58318.92, 63332.61) * mm});
            skLineSegment(sketch, "E775", {"start": v(59393.32, 61405.46) * mm, "end": v(59661.17, 60925.09) * mm});
            skLineSegment(sketch, "E776", {"start": v(59442.82, 60803.34) * mm, "end": v(59661.17, 60925.09) * mm});
            skLineSegment(sketch, "E777", {"start": v(59174.97, 61283.7) * mm, "end": v(59442.82, 60803.34) * mm});
            skLineSegment(sketch, "E778", {"start": v(59174.97, 61283.7) * mm, "end": v(59393.32, 61405.46) * mm});
            skLineSegment(sketch, "E779", {"start": v(61824.92, 57043.9) * mm, "end": v(62092.77, 56563.53) * mm});
            skLineSegment(sketch, "E780", {"start": v(61874.42, 56441.78) * mm, "end": v(62092.77, 56563.53) * mm});
            skLineSegment(sketch, "E781", {"start": v(61606.57, 56922.15) * mm, "end": v(61874.42, 56441.78) * mm});
            skLineSegment(sketch, "E782", {"start": v(61606.57, 56922.15) * mm, "end": v(61824.92, 57043.9) * mm});
            skLineSegment(sketch, "E783", {"start": v(62899.33, 55116.74) * mm, "end": v(63167.18, 54636.37) * mm});
            skLineSegment(sketch, "E784", {"start": v(62948.82, 54514.62) * mm, "end": v(63167.18, 54636.37) * mm});
            skLineSegment(sketch, "E785", {"start": v(62680.98, 54995) * mm, "end": v(62948.82, 54514.62) * mm});
            skLineSegment(sketch, "E786", {"start": v(62680.98, 54995) * mm, "end": v(62899.33, 55116.74) * mm});
            skLineSegment(sketch, "E787", {"start": v(55887.31, 67694.17) * mm, "end": v(56155.16, 67213.8) * mm});
            skLineSegment(sketch, "E788", {"start": v(55936.81, 67092.05) * mm, "end": v(56155.16, 67213.8) * mm});
            skLineSegment(sketch, "E789", {"start": v(55668.96, 67572.42) * mm, "end": v(55936.81, 67092.05) * mm});
            skLineSegment(sketch, "E790", {"start": v(55668.96, 67572.42) * mm, "end": v(55887.31, 67694.17) * mm});
            skLineSegment(sketch, "E791", {"start": v(54812.9, 69621.33) * mm, "end": v(55080.76, 69140.96) * mm});
            skLineSegment(sketch, "E792", {"start": v(54862.4, 69019.2) * mm, "end": v(55080.76, 69140.96) * mm});
            skLineSegment(sketch, "E793", {"start": v(54594.56, 69499.58) * mm, "end": v(54862.4, 69019.2) * mm});
            skLineSegment(sketch, "E794", {"start": v(54594.56, 69499.58) * mm, "end": v(54812.9, 69621.33) * mm});
            skLineSegment(sketch, "E795", {"start": v(50015.8, 71438.24) * mm, "end": v(49814.94, 71412.6) * mm});
            skLineSegment(sketch, "E796", {"start": v(49814.94, 71412.6) * mm, "end": v(49697.18, 72335.11) * mm});
            skLineSegment(sketch, "E797", {"start": v(49697.18, 72335.11) * mm, "end": v(49895.57, 72360.44) * mm});
            skLineSegment(sketch, "E798", {"start": v(49895.57, 72360.44) * mm, "end": v(49601.81, 74661.66) * mm});
            skLineSegment(sketch, "E799", {"start": v(51575.28, 74914.98) * mm, "end": v(64828.2, 51143.91) * mm});
            skLineSegment(sketch, "E800", {"start": v(64828.2, 51143.91) * mm, "end": v(64867.16, 51074.04) * mm});
            skLineSegment(sketch, "E801", {"start": v(64867.16, 51074.04) * mm, "end": v(62198.73, 49586.37) * mm});
            skLineSegment(sketch, "E802", {"start": v(62198.73, 49586.37) * mm, "end": v(62159.78, 49656.24) * mm});
            skLineSegment(sketch, "E803", {"start": v(62159.78, 49656.24) * mm, "end": v(50015.8, 71438.24) * mm});
            skLineSegment(sketch, "E804", {"start": v(53322.5, 61948.71) * mm, "end": v(49005.84, 60642.15) * mm});
            skLineSegment(sketch, "E805", {"start": v(53394.94, 61709.43) * mm, "end": v(52319.25, 61383.85) * mm});
            skLineSegment(sketch, "E806", {"start": v(52079.98, 61311.4) * mm, "end": v(49078.26, 60402.87) * mm});
            skLineSegment(sketch, "E807", {"start": v(52380.65, 73984.06) * mm, "end": v(52648.5, 73503.69) * mm});
            skLineSegment(sketch, "E808", {"start": v(52430.15, 73381.94) * mm, "end": v(52648.5, 73503.69) * mm});
            skLineSegment(sketch, "E809", {"start": v(52162.3, 73862.3) * mm, "end": v(52430.15, 73381.94) * mm});
            skLineSegment(sketch, "E810", {"start": v(52162.3, 73862.3) * mm, "end": v(52380.65, 73984.06) * mm});
            skLineSegment(sketch, "E811", {"start": v(50300.92, 71953.99) * mm, "end": v(62498.94, 50074.53) * mm});
            skLineSegment(sketch, "E812", {"start": v(62498.94, 50074.53) * mm, "end": v(64486, 51182.33) * mm});
            skLineSegment(sketch, "E813", {"start": v(64486, 51182.33) * mm, "end": v(52287.98, 73061.8) * mm});
            skArc(sketch, "E814", {"start": v(52287.98, 73061.8) * mm, "mid": v(51704.03, 73726.48) * mm, "end": v(50922.1, 74140.48) * mm});
            skLineSegment(sketch, "E815", {"start": v(50922.1, 74140.48) * mm, "end": v(50300.92, 71953.99) * mm});
            skLineSegment(sketch, "E816", {"start": v(50085.9, 71928.95) * mm, "end": v(62421.65, 49802.45) * mm});
            skLineSegment(sketch, "E817", {"start": v(62421.65, 49802.45) * mm, "end": v(64758.08, 51105.03) * mm});
            skLineSegment(sketch, "E818", {"start": v(64758.08, 51105.03) * mm, "end": v(52461.17, 73161.86) * mm});
            skLineSegment(sketch, "E819", {"start": v(52461.17, 73161.86) * mm, "end": v(52459.6, 73164.5) * mm});
            skArc(sketch, "E820", {"start": v(52459.6, 73164.5) * mm, "mid": v(51827.99, 73883.44) * mm, "end": v(50982.25, 74331.22) * mm});
            skLineSegment(sketch, "E821", {"start": v(50982.25, 74331.22) * mm, "end": v(50785.97, 74393.1) * mm});
            skLineSegment(sketch, "E822", {"start": v(50785.97, 74393.1) * mm, "end": v(50085.9, 71928.95) * mm});
            skLineSegment(sketch, "E823", {"start": v(35085.6, 70142.58) * mm, "end": v(34311.4, 72700.4) * mm});
            skLineSegment(sketch, "E824", {"start": v(34842.5, 70069) * mm, "end": v(34055.95, 72667.63) * mm});
            skLineSegment(sketch, "E825", {"start": v(37225.7, 69095.58) * mm, "end": v(36066.45, 72925.54) * mm});
            skLineSegment(sketch, "E826", {"start": v(36982.59, 69022) * mm, "end": v(35810.98, 72892.77) * mm});
            skLineSegment(sketch, "E827", {"start": v(38895.86, 69601.11) * mm, "end": v(37821.48, 73150.67) * mm});
            skLineSegment(sketch, "E828", {"start": v(38652.76, 69527.53) * mm, "end": v(37566.02, 73117.9) * mm});
            skLineSegment(sketch, "E829", {"start": v(34899.58, 69801.04) * mm, "end": v(32962.5, 69214.73) * mm});
            skLineSegment(sketch, "E830", {"start": v(32962.5, 69214.73) * mm, "end": v(33036.1, 68971.62) * mm});
            skLineSegment(sketch, "E831", {"start": v(33036.1, 68971.62) * mm, "end": v(34973.16, 69557.93) * mm});
            skLineSegment(sketch, "E832", {"start": v(36591.76, 70313.23) * mm, "end": v(35186.71, 69887.95) * mm});
            skLineSegment(sketch, "E833", {"start": v(35186.71, 69887.95) * mm, "end": v(35260.3, 69644.84) * mm});
            skLineSegment(sketch, "E834", {"start": v(35260.3, 69644.84) * mm, "end": v(36665.34, 70070.12) * mm});
            skLineSegment(sketch, "E835", {"start": v(36908.45, 70143.7) * mm, "end": v(38335.51, 70575.64) * mm});
            skLineSegment(sketch, "E836", {"start": v(38578.62, 70649.23) * mm, "end": v(40119.97, 71115.76) * mm});
            skLineSegment(sketch, "E837", {"start": v(40119.97, 71115.76) * mm, "end": v(40046.38, 71358.87) * mm});
            skLineSegment(sketch, "E838", {"start": v(40046.38, 71358.87) * mm, "end": v(38505.04, 70892.34) * mm});
            skLineSegment(sketch, "E839", {"start": v(38261.93, 70818.75) * mm, "end": v(36834.87, 70386.8) * mm});
            skLineSegment(sketch, "E840", {"start": v(35375.27, 69394.4) * mm, "end": v(35613.43, 68607.58) * mm});
            skLineSegment(sketch, "E841", {"start": v(35613.43, 68607.58) * mm, "end": v(35254.51, 68498.95) * mm});
            skLineSegment(sketch, "E842", {"start": v(35254.51, 68498.95) * mm, "end": v(35016.36, 69285.77) * mm});
            skLineSegment(sketch, "E843", {"start": v(35016.36, 69285.77) * mm, "end": v(35375.27, 69394.4) * mm});
            skLineSegment(sketch, "E844", {"start": v(37610.07, 72972.37) * mm, "end": v(36110.5, 72780) * mm});
            skLineSegment(sketch, "E845", {"start": v(35855.03, 72747.23) * mm, "end": v(34355.46, 72554.87) * mm});
            skLineSegment(sketch, "E846", {"start": v(36360.56, 71077.05) * mm, "end": v(34933.5, 70645.1) * mm});
            skLineSegment(sketch, "E847", {"start": v(34690.4, 70571.5) * mm, "end": v(32730.07, 69978.12) * mm});
            skLineSegment(sketch, "E848", {"start": v(32730.07, 69978.12) * mm, "end": v(32686.62, 70121.69) * mm});
            skLineSegment(sketch, "E849", {"start": v(32686.62, 70121.69) * mm, "end": v(34646.95, 70715.07) * mm});
            skLineSegment(sketch, "E850", {"start": v(34890.05, 70788.66) * mm, "end": v(36317.1, 71220.62) * mm});
            skLineSegment(sketch, "E851", {"start": v(36560.22, 71294.2) * mm, "end": v(37987.27, 71726.17) * mm});
            skLineSegment(sketch, "E852", {"start": v(38230.38, 71799.76) * mm, "end": v(39771.33, 72266.2) * mm});
            skLineSegment(sketch, "E853", {"start": v(39771.33, 72266.2) * mm, "end": v(39814.79, 72122.63) * mm});
            skLineSegment(sketch, "E854", {"start": v(39814.79, 72122.63) * mm, "end": v(38273.83, 71656.2) * mm});
            skLineSegment(sketch, "E855", {"start": v(38030.73, 71582.6) * mm, "end": v(36603.67, 71150.64) * mm});
            skLineSegment(sketch, "E856", {"start": v(36270.52, 72251.33) * mm, "end": v(37697.57, 72683.29) * mm});
            skLineSegment(sketch, "E857", {"start": v(37940.68, 72756.88) * mm, "end": v(39481.63, 73223.31) * mm});
            skLineSegment(sketch, "E858", {"start": v(39481.63, 73223.31) * mm, "end": v(39525.09, 73079.75) * mm});
            skLineSegment(sketch, "E859", {"start": v(39525.09, 73079.75) * mm, "end": v(37984.13, 72613.3) * mm});
            skLineSegment(sketch, "E860", {"start": v(37741.03, 72539.72) * mm, "end": v(36313.97, 72107.76) * mm});
            skLineSegment(sketch, "E861", {"start": v(36070.86, 72034.17) * mm, "end": v(34643.8, 71602.2) * mm});
            skLineSegment(sketch, "E862", {"start": v(34400.7, 71528.62) * mm, "end": v(32440.37, 70935.24) * mm});
            skLineSegment(sketch, "E863", {"start": v(32440.37, 70935.24) * mm, "end": v(32396.92, 71078.8) * mm});
            skLineSegment(sketch, "E864", {"start": v(32396.92, 71078.8) * mm, "end": v(34357.25, 71672.19) * mm});
            skLineSegment(sketch, "E865", {"start": v(34600.35, 71745.78) * mm, "end": v(36027.4, 72177.74) * mm});
            skLineSegment(sketch, "E866", {"start": v(32136.19, 71940.21) * mm, "end": v(34096.5, 72533.66) * mm});
            skLineSegment(sketch, "E867", {"start": v(34096.5, 72533.66) * mm, "end": v(34139.95, 72390.1) * mm});
            skLineSegment(sketch, "E868", {"start": v(34139.95, 72390.1) * mm, "end": v(32179.64, 71796.65) * mm});
            skLineSegment(sketch, "E869", {"start": v(32179.64, 71796.65) * mm, "end": v(32136.19, 71940.21) * mm});
            skLineSegment(sketch, "E870", {"start": v(35569.98, 68751.14) * mm, "end": v(36939.13, 69165.57) * mm});
            skLineSegment(sketch, "E871", {"start": v(37182.24, 69239.16) * mm, "end": v(38609.3, 69671.12) * mm});
            skLineSegment(sketch, "E872", {"start": v(38852.4, 69744.7) * mm, "end": v(40393.35, 70211.15) * mm});
            skLineSegment(sketch, "E873", {"start": v(40393.35, 70211.15) * mm, "end": v(40436.81, 70067.58) * mm});
            skLineSegment(sketch, "E874", {"start": v(40436.81, 70067.58) * mm, "end": v(33352.1, 67923.07) * mm});
            skLineSegment(sketch, "E875", {"start": v(33352.1, 67923.07) * mm, "end": v(33308.64, 68066.64) * mm});
            skLineSegment(sketch, "E876", {"start": v(33308.64, 68066.64) * mm, "end": v(35211.06, 68642.5) * mm});
            skLineSegment(sketch, "E877", {"start": v(52859.03, 63328.75) * mm, "end": v(52815.57, 63472.31) * mm});
            skLineSegment(sketch, "E878", {"start": v(52815.57, 63472.31) * mm, "end": v(52959.14, 63515.77) * mm});
            skLineSegment(sketch, "E879", {"start": v(52959.14, 63515.77) * mm, "end": v(53002.6, 63372.2) * mm});
            skLineSegment(sketch, "E880", {"start": v(53002.6, 63372.2) * mm, "end": v(52859.03, 63328.75) * mm});
            skLineSegment(sketch, "E881", {"start": v(50777.79, 65553.8) * mm, "end": v(51615.9, 65546.25) * mm});
            skLineSegment(sketch, "E882", {"start": v(52399.2, 63117.5) * mm, "end": v(52433.96, 63002.65) * mm});
            skLineSegment(sketch, "E883", {"start": v(51763.97, 62799.89) * mm, "end": v(51729.21, 62914.74) * mm});
            skLineSegment(sketch, "E884", {"start": v(51729.21, 62914.74) * mm, "end": v(52399.2, 63117.5) * mm});
            skLineSegment(sketch, "E885", {"start": v(52433.96, 63002.65) * mm, "end": v(51729.21, 62914.74) * mm});
            skLineSegment(sketch, "E886", {"start": v(48056.28, 63967.48) * mm, "end": v(51403.27, 64510.51) * mm});
            skLineSegment(sketch, "E887", {"start": v(48119.06, 63518.92) * mm, "end": v(48056.22, 63967.7) * mm});
            skLineSegment(sketch, "E888", {"start": v(48056.22, 63967.7) * mm, "end": v(51272.91, 64941.22) * mm});
            skLineSegment(sketch, "E889", {"start": v(4.94, 5000) * mm, "end": v(0, -5000) * mm});
            skLineSegment(sketch, "E890", {"start": v(5000, 0) * mm, "end": v(-5000, -4.94) * mm});
            skCircle(sketch, "E891", {"center": v(0, -2.47) * mm, "radius": 1929.43 * mm});
            skLineSegment(sketch, "E892", {"start": v(55288.15, 51156.63) * mm, "end": v(55346.09, 50965.2) * mm});
            skLineSegment(sketch, "E893", {"start": v(55346.09, 50965.2) * mm, "end": v(54676.1, 50762.41) * mm});
            skLineSegment(sketch, "E894", {"start": v(54676.1, 50762.41) * mm, "end": v(54618.17, 50953.84) * mm});
            skLineSegment(sketch, "E895", {"start": v(54618.17, 50953.84) * mm, "end": v(55288.15, 51156.63) * mm});
            skLineSegment(sketch, "E896", {"start": v(56436.78, 51503.96) * mm, "end": v(56494.72, 51312.54) * mm});
            skLineSegment(sketch, "E897", {"start": v(56494.72, 51312.54) * mm, "end": v(55824.74, 51109.75) * mm});
            skLineSegment(sketch, "E898", {"start": v(55824.74, 51109.75) * mm, "end": v(55766.8, 51301.17) * mm});
            skLineSegment(sketch, "E899", {"start": v(55766.8, 51301.17) * mm, "end": v(56436.78, 51503.96) * mm});
            skLineSegment(sketch, "E900", {"start": v(32882.84, 66524.7) * mm, "end": v(32930.7, 66539.19) * mm});
            skLineSegment(sketch, "E901", {"start": v(32139.44, 71933.99) * mm, "end": v(33354.29, 67920.36) * mm});
            skLineSegment(sketch, "E902", {"start": v(40437.2, 70067.64) * mm, "end": v(39582.82, 72886.93) * mm});
            skLineSegment(sketch, "E903", {"start": v(33353.34, 67923.5) * mm, "end": v(40437.2, 70067.64) * mm});
            skLineSegment(sketch, "E904", {"start": v(48803.1, 61312.14) * mm, "end": v(49377.38, 61485.96) * mm});
            skLineSegment(sketch, "E905", {"start": v(49667.08, 60528.84) * mm, "end": v(49092.8, 60355.02) * mm});
            skLineSegment(sketch, "E906", {"start": v(49092.8, 60355.02) * mm, "end": v(48803.1, 61312.14) * mm});
            skLineSegment(sketch, "E907", {"start": v(48803.1, 61312.14) * mm, "end": v(49667.08, 60528.84) * mm});
            skLineSegment(sketch, "E908", {"start": v(36888.61, 52850.02) * mm, "end": v(37127.49, 52922.32) * mm});
            skLineSegment(sketch, "E909", {"start": v(37127.49, 52922.32) * mm, "end": v(37272.34, 52443.76) * mm});
            skLineSegment(sketch, "E910", {"start": v(37272.34, 52443.76) * mm, "end": v(37033.46, 52371.46) * mm});
            skLineSegment(sketch, "E911", {"start": v(37033.46, 52371.46) * mm, "end": v(36888.61, 52850.02) * mm});
            skLineSegment(sketch, "E912", {"start": v(37033.46, 52371.46) * mm, "end": v(37127.49, 52922.32) * mm});
            skLineSegment(sketch, "E913", {"start": v(48012.96, 74458.04) * mm, "end": v(48044.72, 74210.49) * mm});
            skLineSegment(sketch, "E914", {"start": v(48044.72, 74210.49) * mm, "end": v(47548.78, 74146.87) * mm});
            skLineSegment(sketch, "E915", {"start": v(47548.78, 74146.87) * mm, "end": v(47517.02, 74394.42) * mm});
            skLineSegment(sketch, "E916", {"start": v(47517.02, 74394.42) * mm, "end": v(48012.96, 74458.04) * mm});
            skLineSegment(sketch, "E917", {"start": v(47517.02, 74394.42) * mm, "end": v(48044.72, 74210.49) * mm});
            skLineSegment(sketch, "E918", {"start": v(53750.5, 67368.35) * mm, "end": v(54375, 67716.51) * mm});
            skLineSegment(sketch, "E919", {"start": v(54375, 67716.51) * mm, "end": v(54723.16, 67092) * mm});
            skLineSegment(sketch, "E920", {"start": v(54723.16, 67092) * mm, "end": v(54098.66, 66743.84) * mm});
            skLineSegment(sketch, "E921", {"start": v(54098.66, 66743.84) * mm, "end": v(53750.5, 67368.35) * mm});
            skLineSegment(sketch, "E922", {"start": v(60461.83, 56798.62) * mm, "end": v(60185.5, 55825.95) * mm});
            skLineSegment(sketch, "E923", {"start": v(59837.33, 56450.45) * mm, "end": v(60461.83, 56798.62) * mm});
            skLineSegment(sketch, "E924", {"start": v(60461.83, 56798.62) * mm, "end": v(60810, 56174.12) * mm});
            skLineSegment(sketch, "E925", {"start": v(60810, 56174.12) * mm, "end": v(60185.5, 55825.95) * mm});
            skLineSegment(sketch, "E926", {"start": v(60185.5, 55825.95) * mm, "end": v(59837.33, 56450.45) * mm});
            skLineSegment(sketch, "E927", {"start": v(60810, 56174.12) * mm, "end": v(59837.33, 56450.45) * mm});
            skLineSegment(sketch, "E928", {"start": v(54375, 67716.51) * mm, "end": v(54098.66, 66743.84) * mm});
            skLineSegment(sketch, "E929", {"start": v(54723.16, 67092) * mm, "end": v(53750.5, 67368.35) * mm});
            skLineSegment(sketch, "E930", {"start": v(60786.28, 51104.38) * mm, "end": v(61212.6, 51342.09) * mm});
            skLineSegment(sketch, "E931", {"start": v(61212.6, 51342.09) * mm, "end": v(61456.1, 50905.39) * mm});
            skLineSegment(sketch, "E932", {"start": v(61456.1, 50905.39) * mm, "end": v(61029.78, 50667.68) * mm});
            skLineSegment(sketch, "E933", {"start": v(61029.78, 50667.68) * mm, "end": v(60786.28, 51104.38) * mm});
            skLineSegment(sketch, "E934", {"start": v(56066.37, 59569.28) * mm, "end": v(56492.7, 59806.99) * mm});
            skLineSegment(sketch, "E935", {"start": v(56492.7, 59806.99) * mm, "end": v(56736.2, 59370.28) * mm});
            skLineSegment(sketch, "E936", {"start": v(56736.2, 59370.28) * mm, "end": v(56309.87, 59132.57) * mm});
            skLineSegment(sketch, "E937", {"start": v(56309.87, 59132.57) * mm, "end": v(56066.37, 59569.28) * mm});
            skLineSegment(sketch, "E938", {"start": v(58411.88, 55362.74) * mm, "end": v(58838.2, 55600.45) * mm});
            skLineSegment(sketch, "E939", {"start": v(58838.2, 55600.45) * mm, "end": v(59081.7, 55163.75) * mm});
            skLineSegment(sketch, "E940", {"start": v(59081.7, 55163.75) * mm, "end": v(58655.38, 54926.04) * mm});
            skLineSegment(sketch, "E941", {"start": v(58655.38, 54926.04) * mm, "end": v(58411.88, 55362.74) * mm});
            skLineSegment(sketch, "E942", {"start": v(50444.2, 69652.33) * mm, "end": v(50876.96, 69893.63) * mm});
            skLineSegment(sketch, "E943", {"start": v(50876.96, 69893.63) * mm, "end": v(51120.46, 69456.93) * mm});
            skLineSegment(sketch, "E944", {"start": v(51120.46, 69456.93) * mm, "end": v(50687.7, 69215.63) * mm});
            skLineSegment(sketch, "E945", {"start": v(50687.7, 69215.63) * mm, "end": v(50444.2, 69652.33) * mm});
            skLineSegment(sketch, "E946", {"start": v(49895.57, 72360.44) * mm, "end": v(50013.33, 71437.92) * mm});
            skLineSegment(sketch, "E947", {"start": v(50013.33, 71437.92) * mm, "end": v(49814.94, 71412.6) * mm});
            skLineSegment(sketch, "E948", {"start": v(49304.21, 74623.77) * mm, "end": v(49601.8, 74661.76) * mm});
            skLineSegment(sketch, "E949", {"start": v(49601.8, 74661.76) * mm, "end": v(49677.77, 74066.6) * mm});
            skLineSegment(sketch, "E950", {"start": v(49677.77, 74066.6) * mm, "end": v(49380.19, 74028.6) * mm});
            skLineSegment(sketch, "E951", {"start": v(49380.19, 74028.6) * mm, "end": v(49304.21, 74623.77) * mm});
            skLineSegment(sketch, "E952", {"start": v(42989.16, 59171.24) * mm, "end": v(43315.07, 58094.48) * mm});
            skLineSegment(sketch, "E953", {"start": v(43315.07, 58094.48) * mm, "end": v(39127.68, 56827.04) * mm});
            skLineSegment(sketch, "E954", {"start": v(42989.16, 59171.24) * mm, "end": v(39127.68, 56827.04) * mm});
            skLineSegment(sketch, "E955", {"start": v(43315.07, 58094.48) * mm, "end": v(38801.77, 57903.8) * mm});
            skLineSegment(sketch, "E956", {"start": v(53966.18, 50757) * mm, "end": v(52040.19, 57120.16) * mm});
            skLineSegment(sketch, "E957", {"start": v(52040.19, 57120.16) * mm, "end": v(55677.4, 58222.57) * mm});
            skLineSegment(sketch, "E958", {"start": v(55677.4, 58222.57) * mm, "end": v(58823.27, 52580.61) * mm});
            skLineSegment(sketch, "E959", {"start": v(58823.27, 52580.61) * mm, "end": v(57793.68, 52268.9) * mm});
            skLineSegment(sketch, "E960", {"start": v(57793.68, 52268.9) * mm, "end": v(57891.69, 51945.18) * mm});
            skLineSegment(sketch, "E961", {"start": v(57891.69, 51945.18) * mm, "end": v(53966.18, 50757) * mm});
            skLineSegment(sketch, "E962", {"start": v(53966.18, 50757) * mm, "end": v(55677.4, 58222.57) * mm});
            skLineSegment(sketch, "E963", {"start": v(58823.27, 52580.61) * mm, "end": v(52040.19, 57120.16) * mm});
            skLineSegment(sketch, "E964", {"start": v(50354.93, 60230) * mm, "end": v(50833.48, 60374.84) * mm});
            skLineSegment(sketch, "E965", {"start": v(51268.03, 58939.17) * mm, "end": v(50789.48, 58794.32) * mm});
            skLineSegment(sketch, "E966", {"start": v(50789.48, 58794.32) * mm, "end": v(50354.93, 60230) * mm});
            skLineSegment(sketch, "E967", {"start": v(50354.93, 60230) * mm, "end": v(51268.03, 58939.17) * mm});
            skLineSegment(sketch, "E968", {"start": v(53162.93, 64776.44) * mm, "end": v(53595.41, 65017.58) * mm});
            skLineSegment(sketch, "E969", {"start": v(53595.41, 65017.58) * mm, "end": v(53838.91, 64580.88) * mm});
            skLineSegment(sketch, "E970", {"start": v(53838.91, 64580.88) * mm, "end": v(53406.43, 64339.73) * mm});
            skLineSegment(sketch, "E971", {"start": v(53406.43, 64339.73) * mm, "end": v(53162.93, 64776.44) * mm});
            skLineSegment(sketch, "E972", {"start": v(49750.6, 74680.66) * mm, "end": v(50345.77, 74756.63) * mm});
            skLineSegment(sketch, "E973", {"start": v(50345.77, 74756.63) * mm, "end": v(50421.75, 74161.46) * mm});
            skLineSegment(sketch, "E974", {"start": v(50421.75, 74161.46) * mm, "end": v(49826.58, 74085.49) * mm});
            skLineSegment(sketch, "E975", {"start": v(49826.58, 74085.49) * mm, "end": v(49750.6, 74680.66) * mm});
            skLineSegment(sketch, "E976", {"start": v(49826.58, 74085.49) * mm, "end": v(50345.77, 74756.63) * mm});
            skLineSegment(sketch, "E977", {"start": v(50421.75, 74161.46) * mm, "end": v(49750.6, 74680.66) * mm});
            skLineSegment(sketch, "E978", {"start": v(54817.6, 58562.1) * mm, "end": v(55009.03, 58620.04) * mm});
            skLineSegment(sketch, "E979", {"start": v(55009.03, 58620.04) * mm, "end": v(55066.97, 58428.62) * mm});
            skLineSegment(sketch, "E980", {"start": v(55066.97, 58428.62) * mm, "end": v(54875.54, 58370.68) * mm});
            skLineSegment(sketch, "E981", {"start": v(54875.54, 58370.68) * mm, "end": v(54817.6, 58562.1) * mm});
            skLineSegment(sketch, "E982", {"start": v(54875.54, 58370.68) * mm, "end": v(55007.31, 58619.53) * mm});
            skLineSegment(sketch, "E983", {"start": v(44014.37, 73479.49) * mm, "end": v(44212.74, 73504.92) * mm});
            skLineSegment(sketch, "E984", {"start": v(44212.74, 73504.92) * mm, "end": v(44238.18, 73306.54) * mm});
            skLineSegment(sketch, "E985", {"start": v(44238.18, 73306.54) * mm, "end": v(44039.8, 73281.1) * mm});
            skLineSegment(sketch, "E986", {"start": v(44039.8, 73281.1) * mm, "end": v(44014.37, 73479.49) * mm});
            skLineSegment(sketch, "E987", {"start": v(44039.8, 73281.1) * mm, "end": v(44210.97, 73504.7) * mm});
            skLineSegment(sketch, "E988", {"start": v(44450.64, 73789) * mm, "end": v(44649.01, 73814.43) * mm});
            skLineSegment(sketch, "E989", {"start": v(44649.01, 73814.43) * mm, "end": v(44674.45, 73616.05) * mm});
            skLineSegment(sketch, "E990", {"start": v(44674.45, 73616.05) * mm, "end": v(44476.07, 73590.62) * mm});
            skLineSegment(sketch, "E991", {"start": v(44476.07, 73590.62) * mm, "end": v(44450.64, 73789) * mm});
            skLineSegment(sketch, "E992", {"start": v(44476.07, 73590.62) * mm, "end": v(44647.24, 73814.2) * mm});
            skLineSegment(sketch, "E993", {"start": v(41945.24, 69090.17) * mm, "end": v(42136.66, 69148.11) * mm});
            skLineSegment(sketch, "E994", {"start": v(42136.66, 69148.11) * mm, "end": v(42194.6, 68956.69) * mm});
            skLineSegment(sketch, "E995", {"start": v(42194.6, 68956.69) * mm, "end": v(42003.18, 68898.75) * mm});
            skLineSegment(sketch, "E996", {"start": v(42003.18, 68898.75) * mm, "end": v(41945.24, 69090.17) * mm});
            skLineSegment(sketch, "E997", {"start": v(42003.18, 68898.75) * mm, "end": v(42134.95, 69147.6) * mm});
            skLineSegment(sketch, "E998", {"start": v(42114.91, 67788.36) * mm, "end": v(42276, 67669.8) * mm});
            skLineSegment(sketch, "E999", {"start": v(42276, 67669.8) * mm, "end": v(42157.44, 67508.73) * mm});
            skLineSegment(sketch, "E1000", {"start": v(42157.44, 67508.73) * mm, "end": v(41996.36, 67627.28) * mm});
            skLineSegment(sketch, "E1001", {"start": v(41996.36, 67627.28) * mm, "end": v(42114.91, 67788.36) * mm});
            skLineSegment(sketch, "E1002", {"start": v(41996.36, 67627.28) * mm, "end": v(42274.55, 67670.87) * mm});
            skLineSegment(sketch, "E1003", {"start": v(34666.3, 60274.62) * mm, "end": v(34857.72, 60332.56) * mm});
            skLineSegment(sketch, "E1004", {"start": v(34857.72, 60332.56) * mm, "end": v(34915.66, 60141.14) * mm});
            skLineSegment(sketch, "E1005", {"start": v(34915.66, 60141.14) * mm, "end": v(34724.24, 60083.2) * mm});
            skLineSegment(sketch, "E1006", {"start": v(34724.24, 60083.2) * mm, "end": v(34666.3, 60274.62) * mm});
            skLineSegment(sketch, "E1007", {"start": v(34724.24, 60083.2) * mm, "end": v(34856, 60332.05) * mm});
            skLineSegment(sketch, "E1008", {"start": v(32914.9, 66064.01) * mm, "end": v(33106.33, 66121.95) * mm});
            skLineSegment(sketch, "E1009", {"start": v(33106.33, 66121.95) * mm, "end": v(33164.27, 65930.53) * mm});
            skLineSegment(sketch, "E1010", {"start": v(33164.27, 65930.53) * mm, "end": v(32972.85, 65872.59) * mm});
            skLineSegment(sketch, "E1011", {"start": v(32972.85, 65872.59) * mm, "end": v(32914.9, 66064.01) * mm});
            skLineSegment(sketch, "E1012", {"start": v(32972.85, 65872.59) * mm, "end": v(33104.62, 66121.43) * mm});
            skEllipse(sketch, "E1013", {"center": v(50534.92, 62319.96) * mm, "majorRadius": 158.75 * mm, "minorRadius": 158.75 * mm, "majorAxis": v(1, 0)});
            skArc(sketch, "E1014", {"start": v(50382.98, 62273.97) * mm, "mid": v(50460, 62180) * mm, "end": v(50580.9, 62168.02) * mm});
            skArc(sketch, "E1015", {"start": v(50686.86, 62365.95) * mm, "mid": v(50609.84, 62459.92) * mm, "end": v(50488.93, 62471.9) * mm});
            skLineSegment(sketch, "E1016", {"start": v(50580.9, 62168.02) * mm, "end": v(50488.93, 62471.9) * mm});
            skLineSegment(sketch, "E1017", {"start": v(50686.86, 62365.95) * mm, "end": v(50382.98, 62273.97) * mm});
            skLineSegment(sketch, "E1018", {"start": v(50488.93, 62471.9) * mm, "end": v(50146.36, 63603.7) * mm});
            skEllipse(sketch, "E1019", {"center": v(56148.5, 63937.99) * mm, "majorRadius": 158.75 * mm, "minorRadius": 158.75 * mm, "majorAxis": v(1, 0)});
            skArc(sketch, "E1020", {"start": v(55996.56, 63892) * mm, "mid": v(56073.58, 63798.03) * mm, "end": v(56194.5, 63786.04) * mm});
            skArc(sketch, "E1021", {"start": v(56300.44, 63983.98) * mm, "mid": v(56223.42, 64077.94) * mm, "end": v(56102.51, 64089.93) * mm});
            skLineSegment(sketch, "E1022", {"start": v(56194.5, 63786.04) * mm, "end": v(56102.51, 64089.93) * mm});
            skLineSegment(sketch, "E1023", {"start": v(56300.44, 63983.98) * mm, "end": v(55996.56, 63892) * mm});
            skLineSegment(sketch, "E1024", {"start": v(56102.51, 64089.93) * mm, "end": v(55759.94, 65221.72) * mm});
            skLineSegment(sketch, "E1025", {"start": v(37367.92, 54535.6) * mm, "end": v(37990.05, 54723.9) * mm});
            skLineSegment(sketch, "E1026", {"start": v(37990.05, 54723.9) * mm, "end": v(38337.69, 53575.37) * mm});
            skLineSegment(sketch, "E1027", {"start": v(38337.69, 53575.37) * mm, "end": v(37715.56, 53387.06) * mm});
            skLineSegment(sketch, "E1028", {"start": v(37715.56, 53387.06) * mm, "end": v(37367.92, 54535.6) * mm});
            skLineSegment(sketch, "E1029", {"start": v(37305.58, 54568.97) * mm, "end": v(38023.42, 54786.25) * mm});
            skLineSegment(sketch, "E1030", {"start": v(38023.42, 54786.25) * mm, "end": v(38400.03, 53542) * mm});
            skLineSegment(sketch, "E1031", {"start": v(38400.03, 53542) * mm, "end": v(37682.2, 53324.72) * mm});
            skLineSegment(sketch, "E1032", {"start": v(37682.2, 53324.72) * mm, "end": v(37305.58, 54568.97) * mm});
            skCircle(sketch, "E1033", {"center": v(34859.77, 59971.76) * mm, "radius": 100 * mm});
            skCircle(sketch, "E1034", {"center": v(33845.6, 63524.72) * mm, "radius": 150 * mm});
            skCircle(sketch, "E1035", {"center": v(42962.38, 72270.77) * mm, "radius": 100 * mm});
            skCircle(sketch, "E1036", {"center": v(44009.01, 66971.1) * mm, "radius": 50 * mm});
            skCircle(sketch, "E1037", {"center": v(46019.97, 73321.4) * mm, "radius": 50 * mm});
            skCircle(sketch, "E1038", {"center": v(51528.34, 74753.64) * mm, "radius": 75 * mm});
            skCircle(sketch, "E1039", {"center": v(51206.19, 74656.13) * mm, "radius": 75 * mm});
            skCircle(sketch, "E1040", {"center": v(46278.12, 72377.02) * mm, "radius": 75 * mm});
            skCircle(sketch, "E1041", {"center": v(42403.04, 66446.16) * mm, "radius": 100 * mm});
            skCircle(sketch, "E1042", {"center": v(39975.07, 63798.53) * mm, "radius": 100 * mm});
            skCircle(sketch, "E1043", {"center": v(60065.62, 50226.34) * mm, "radius": 100 * mm});
            skCircle(sketch, "E1044", {"center": v(60145.29, 49963.13) * mm, "radius": 75 * mm});
            skCircle(sketch, "E1045", {"center": v(60217.71, 49723.85) * mm, "radius": 75 * mm});
            skCircle(sketch, "E1046", {"center": v(60253.93, 49604.21) * mm, "radius": 75 * mm});
            skLineSegment(sketch, "E1047", {"start": v(60172.3, 49684.01) * mm, "end": v(59032.93, 49339.14) * mm});
            skLineSegment(sketch, "E1048", {"start": v(60068.85, 49680.4) * mm, "end": v(60172.3, 49684.01) * mm});
            skLineSegment(sketch, "E1049", {"start": v(60172.3, 49684.01) * mm, "end": v(60084.52, 49629.15) * mm});
            skLineSegment(sketch, "E1050", {"start": v(60084.52, 49629.15) * mm, "end": v(60068.85, 49680.4) * mm});
            skLineSegment(sketch, "E1051", {"start": v(60066.26, 49965.35) * mm, "end": v(59544.25, 49807.35) * mm});
            skLineSegment(sketch, "E1052", {"start": v(59544.25, 49807.35) * mm, "end": v(59474.43, 50038.03) * mm});
            skLineSegment(sketch, "E1053", {"start": v(59962.8, 49961.74) * mm, "end": v(60066.26, 49965.35) * mm});
            skLineSegment(sketch, "E1054", {"start": v(60066.26, 49965.35) * mm, "end": v(59978.46, 49910.5) * mm});
            skLineSegment(sketch, "E1055", {"start": v(59978.46, 49910.5) * mm, "end": v(59962.8, 49961.74) * mm});
            skLineSegment(sketch, "E1056", {"start": v(60036.65, 50322.05) * mm, "end": v(59882.1, 50832.68) * mm});
            skLineSegment(sketch, "E1057", {"start": v(60034.84, 50425.55) * mm, "end": v(60036.65, 50322.05) * mm});
            skLineSegment(sketch, "E1058", {"start": v(60036.65, 50322.05) * mm, "end": v(59983.33, 50410.78) * mm});
            skLineSegment(sketch, "E1059", {"start": v(59983.33, 50410.78) * mm, "end": v(60034.84, 50425.55) * mm});
            skCircle(sketch, "E1060", {"center": v(42925.07, 63312.53) * mm, "radius": 100 * mm});
            skCircle(sketch, "E1061", {"center": v(43205.18, 63546.23) * mm, "radius": 75 * mm});
            skLineSegment(sketch, "E1062", {"start": v(52859.03, 63328.75) * mm, "end": v(52959.14, 63515.77) * mm});
            skCircle(sketch, "E1063", {"center": v(34494.04, 61192.02) * mm, "radius": 50 * mm});
            skCircle(sketch, "E1064", {"center": v(34378.16, 61574.87) * mm, "radius": 75 * mm});
            skCircle(sketch, "E1065", {"center": v(34436.1, 61383.45) * mm, "radius": 75 * mm});
            skCircle(sketch, "E1066", {"center": v(35316.95, 58473.27) * mm, "radius": 75 * mm});
            skCircle(sketch, "E1067", {"center": v(35374.9, 58281.84) * mm, "radius": 75 * mm});
            skLineSegment(sketch, "E1068", {"start": v(68800.03, 49613.6) * mm, "end": v(52895.98, 44799.76) * mm});
            skLineSegment(sketch, "E1069", {"start": v(64824.99, 62739.91) * mm, "end": v(48922.75, 57926.63) * mm});
            skLineSegment(sketch, "E1070", {"start": v(63051.1, 64454.54) * mm, "end": v(48298.44, 59989.21) * mm});
            skLineSegment(sketch, "E1071", {"start": v(58279.05, 77095.62) * mm, "end": v(29227.41, 73368.86) * mm});
            skLineSegment(sketch, "E1072", {"start": v(50700.72, 66312.66) * mm, "end": v(57291.8, 44536.93) * mm});
            skLineSegment(sketch, "E1073", {"start": v(56137.88, 61183.94) * mm, "end": v(34457.3, 54621.67) * mm});
            skLineSegment(sketch, "E1074", {"start": v(53763.43, 65950.46) * mm, "end": v(32900.17, 59635.57) * mm});
            skLineSegment(sketch, "E1075", {"start": v(37800.23, 67883.79) * mm, "end": v(31024.37, 65832.87) * mm});
            skLineSegment(sketch, "E1076", {"start": v(61637.16, 69125.21) * mm, "end": v(32680.7, 60360.68) * mm});
            skLineSegment(sketch, "E1077", {"start": v(59917.1, 70856.14) * mm, "end": v(32056.39, 62423.27) * mm});
            skLineSegment(sketch, "E1078", {"start": v(58503.37, 75526.87) * mm, "end": v(30642.65, 67094) * mm});
            skLineSegment(sketch, "E1079", {"start": v(66863.03, 56006.6) * mm, "end": v(50960.79, 51193.3) * mm});
            skLineSegment(sketch, "E1080", {"start": v(67188.94, 54929.83) * mm, "end": v(51286.7, 50116.55) * mm});
            skLineSegment(sketch, "E1081", {"start": v(48161.86, 80551.5) * mm, "end": v(59147.71, 44256.2) * mm});
            skLineSegment(sketch, "E1082", {"start": v(46080.13, 79921.4) * mm, "end": v(50825.96, 64242) * mm});
            skLineSegment(sketch, "E1083", {"start": v(38710.33, 77690.7) * mm, "end": v(45197.28, 56258.97) * mm});
            skLineSegment(sketch, "E1084", {"start": v(32335.92, 75761.3) * mm, "end": v(38822.87, 54329.57) * mm});
            skLineSegment(sketch, "E1085", {"start": v(29943.13, 75037.05) * mm, "end": v(36430.08, 53605.32) * mm});
            skLineSegment(sketch, "E1086", {"start": v(67769.85, 47708.43) * mm, "end": v(50010.94, 79562.53) * mm});
            skCircle(sketch, "E1087", {"center": v(29827.25, 75419.9) * mm, "radius": 400 * mm});
            skCircle(sketch, "E1088", {"center": v(58675.8, 77146.49) * mm, "radius": 400 * mm});
            skCircle(sketch, "E1089", {"center": v(55953.69, 77875.9) * mm, "radius": 400 * mm});
            skCircle(sketch, "E1090", {"center": v(58886.21, 75642.75) * mm, "radius": 400 * mm});
            skCircle(sketch, "E1091", {"center": v(60299.95, 70972.02) * mm, "radius": 400 * mm});
            skCircle(sketch, "E1092", {"center": v(62020, 69241.1) * mm, "radius": 400 * mm});
            skCircle(sketch, "E1093", {"center": v(63433.94, 64570.42) * mm, "radius": 400 * mm});
            skCircle(sketch, "E1094", {"center": v(65207.84, 62855.8) * mm, "radius": 400 * mm});
            skCircle(sketch, "E1095", {"center": v(66621.57, 58185.06) * mm, "radius": 400 * mm});
            skCircle(sketch, "E1096", {"center": v(67245.88, 56122.47) * mm, "radius": 400 * mm});
            skCircle(sketch, "E1097", {"center": v(69182.88, 49729.47) * mm, "radius": 400 * mm});
            skCircle(sketch, "E1098", {"center": v(30641.28, 65716.92) * mm, "radius": 400 * mm});
            skCircle(sketch, "E1099", {"center": v(32515.18, 59519.04) * mm, "radius": 400 * mm});
            skCircle(sketch, "E1100", {"center": v(34071.81, 54504.99) * mm, "radius": 400 * mm});
            skCircle(sketch, "E1101", {"center": v(48987.18, 56326.68) * mm, "radius": 400 * mm});
            skLineSegment(sketch, "E1102", {"start": v(36305.06, 74483.7) * mm, "end": v(29069.58, 72293.67) * mm});
            skLineSegment(sketch, "E1103", {"start": v(66238.73, 58069.18) * mm, "end": v(50336.48, 53255.9) * mm});
            skLineSegment(sketch, "E1104", {"start": v(53375.44, 75865.5) * mm, "end": v(51312.22, 74715.25) * mm});
            skLineSegment(sketch, "E1105", {"start": v(51499.4, 78348.17) * mm, "end": v(51983.24, 74576.36) * mm});
            skLineSegment(sketch, "E1106", {"start": v(35636.54, 59235.4) * mm, "end": v(51432.72, 80700.01) * mm});
            skLineSegment(sketch, "E1107", {"start": v(39916.94, 56084.63) * mm, "end": v(55716.5, 77553.82) * mm});
            skCircle(sketch, "E1108", {"center": v(67571.79, 55045.71) * mm, "radius": 400 * mm});
            skCircle(sketch, "E1109", {"center": v(65653.83, 61371.34) * mm, "radius": 400 * mm});
            skCircle(sketch, "E1110", {"center": v(63682.27, 63752.25) * mm, "radius": 400 * mm});
            skLineSegment(sketch, "E1111", {"start": v(65270.99, 61255.46) * mm, "end": v(49371.78, 56443.1) * mm});
            skCircle(sketch, "E1112", {"center": v(57407.68, 44154.09) * mm, "radius": 400 * mm});
            skCircle(sketch, "E1113", {"center": v(54584.18, 43299.47) * mm, "radius": 400 * mm});
            skCircle(sketch, "E1114", {"center": v(67964.63, 47359.05) * mm, "radius": 400 * mm});
            skLineSegment(sketch, "E1115", {"start": v(54468.58, 43682.4) * mm, "end": v(49533.34, 59987.56) * mm});
            skLineSegment(sketch, "E1116", {"start": v(67004.16, 47476.67) * mm, "end": v(49593.94, 78705.35) * mm});
            skCircle(sketch, "E1117", {"center": v(67198.94, 47127.3) * mm, "radius": 400 * mm});
            skLineSegment(sketch, "E1118", {"start": v(63299.42, 63636.4) * mm, "end": v(48546.14, 59170.88) * mm});
            skSolve(sketch);
        }
        {
            var Q0;
            Q0=qCreatedBy(makeId("Top.planeOp"),FACE);
            var sketch = newSketch(context, id + "F1", { "sketchPlane" : qUnion([Q0])});
            skPoint(sketch, "E1119.0", {"position": v(32972.85, 65872.59) * mm});
            skPoint(sketch, "E1119.1", {"position": v(32914.9, 66064.01) * mm});
            skPoint(sketch, "E1119.2", {"position": v(33106.33, 66121.95) * mm});
            skPoint(sketch, "E1119.3", {"position": v(33164.27, 65930.53) * mm});
            skLineSegment(sketch, "E1119.4", {"start": v(33106.33, 66121.95) * mm, "end": v(33164.27, 65930.53) * mm});
            skLineSegment(sketch, "E1119.5", {"start": v(32914.9, 66064.01) * mm, "end": v(33106.33, 66121.95) * mm});
            skLineSegment(sketch, "E1119.6", {"start": v(32972.85, 65872.59) * mm, "end": v(32914.9, 66064.01) * mm});
            skLineSegment(sketch, "E1119.7", {"start": v(33164.27, 65930.53) * mm, "end": v(32972.85, 65872.59) * mm});
            skPoint(sketch, "E1119.8", {"position": v(33135.3, 66026.24) * mm});
            skPoint(sketch, "E1119.9", {"position": v(33068.56, 65901.56) * mm});
            skLineSegment(sketch, "E1120.3", {"start": v(32032.97, 72408.17) * mm, "end": v(39441.15, 73358.44) * mm});
            skLineSegment(sketch, "E1121.0", {"start": v(53564.5, 76178.39) * mm, "end": v(29657.7, 73111.61) * mm});
            skLineSegment(sketch, "E1121.1", {"start": v(29657.7, 73111.61) * mm, "end": v(36317.52, 51108.76) * mm});
            skLineSegment(sketch, "E1121.2", {"start": v(68188.43, 49622.94) * mm, "end": v(53564.5, 76178.39) * mm});
            skLineSegment(sketch, "E1121.3", {"start": v(36317.52, 51108.76) * mm, "end": v(40724.12, 52442.55) * mm});
            skLineSegment(sketch, "E1121.4", {"start": v(40724.12, 52442.55) * mm, "end": v(39664.46, 55943.5) * mm});
            skLineSegment(sketch, "E1121.5", {"start": v(39664.46, 55943.5) * mm, "end": v(44744.96, 57481.26) * mm});
            skLineSegment(sketch, "E1121.6", {"start": v(49725.98, 58953.26) * mm, "end": v(44495.22, 57370.06) * mm});
            skLineSegment(sketch, "E1121.7", {"start": v(68188.43, 49622.94) * mm, "end": v(67662.85, 49333.51) * mm});
            skPoint(sketch, "E1121.8", {"position": v(67662.85, 49333.51) * mm});
            skLineSegment(sketch, "E1121.9", {"start": v(67662.85, 49333.51) * mm, "end": v(67446.81, 49725.81) * mm});
            skLineSegment(sketch, "E1121.10", {"start": v(67446.81, 49725.81) * mm, "end": v(53744.87, 45578.51) * mm});
            skLineSegment(sketch, "E1121.11", {"start": v(53744.87, 45578.51) * mm, "end": v(49515.03, 59553.16) * mm});
            skLineSegment(sketch, "E1122", {"start": v(44495.22, 57370.06) * mm, "end": v(44744.96, 57481.26) * mm});
            skCircle(sketch, "E1123.0", {"center": v(33845.6, 63524.72) * mm, "radius": 150 * mm});
            skCircle(sketch, "E1123.4", {"center": v(34859.77, 59971.76) * mm, "radius": 100 * mm});
            skLineSegment(sketch, "E1123.5", {"start": v(34857.72, 60332.56) * mm, "end": v(34915.66, 60141.14) * mm});
            skLineSegment(sketch, "E1123.6", {"start": v(34666.3, 60274.62) * mm, "end": v(34857.72, 60332.56) * mm});
            skLineSegment(sketch, "E1123.7", {"start": v(34724.24, 60083.2) * mm, "end": v(34666.3, 60274.62) * mm});
            skLineSegment(sketch, "E1123.8", {"start": v(34915.66, 60141.14) * mm, "end": v(34724.24, 60083.2) * mm});
            skCircle(sketch, "E1123.9", {"center": v(35316.95, 58473.27) * mm, "radius": 75 * mm});
            skCircle(sketch, "E1123.10", {"center": v(35374.9, 58281.84) * mm, "radius": 75 * mm});
            skLineSegment(sketch, "E1124.0", {"start": v(37715.56, 53387.06) * mm, "end": v(37367.92, 54535.6) * mm});
            skLineSegment(sketch, "E1124.1", {"start": v(37367.92, 54535.6) * mm, "end": v(37990.05, 54723.9) * mm});
            skLineSegment(sketch, "E1124.2", {"start": v(37990.05, 54723.9) * mm, "end": v(38337.69, 53575.37) * mm});
            skLineSegment(sketch, "E1124.3", {"start": v(38337.69, 53575.37) * mm, "end": v(37715.56, 53387.06) * mm});
            skLineSegment(sketch, "E1125.0", {"start": v(38801.77, 57903.8) * mm, "end": v(42989.16, 59171.24) * mm});
            skLineSegment(sketch, "E1125.1", {"start": v(42989.16, 59171.24) * mm, "end": v(43315.07, 58094.48) * mm});
            skLineSegment(sketch, "E1125.2", {"start": v(43315.07, 58094.48) * mm, "end": v(39127.68, 56827.04) * mm});
            skLineSegment(sketch, "E1125.3", {"start": v(39127.68, 56827.04) * mm, "end": v(38801.77, 57903.8) * mm});
            skLineSegment(sketch, "E1126.0", {"start": v(42136.66, 69148.11) * mm, "end": v(42194.6, 68956.69) * mm});
            skLineSegment(sketch, "E1126.1", {"start": v(41945.24, 69090.17) * mm, "end": v(42136.66, 69148.11) * mm});
            skLineSegment(sketch, "E1126.2", {"start": v(42003.18, 68898.75) * mm, "end": v(41945.24, 69090.17) * mm});
            skLineSegment(sketch, "E1126.3", {"start": v(42194.6, 68956.69) * mm, "end": v(42003.18, 68898.75) * mm});
            skLineSegment(sketch, "E1127.0", {"start": v(42114.91, 67788.36) * mm, "end": v(42276, 67669.8) * mm});
            skLineSegment(sketch, "E1127.1", {"start": v(41996.36, 67627.28) * mm, "end": v(42114.91, 67788.36) * mm});
            skLineSegment(sketch, "E1127.2", {"start": v(42157.44, 67508.73) * mm, "end": v(41996.36, 67627.28) * mm});
            skLineSegment(sketch, "E1127.3", {"start": v(42276, 67669.8) * mm, "end": v(42157.44, 67508.73) * mm});
            skCircle(sketch, "E1128.0", {"center": v(39975.07, 63798.53) * mm, "radius": 100 * mm});
            skCircle(sketch, "E1128.1", {"center": v(42925.07, 63312.53) * mm, "radius": 100 * mm});
            skCircle(sketch, "E1128.2", {"center": v(43205.18, 63546.23) * mm, "radius": 75 * mm});
            skCircle(sketch, "E1128.3", {"center": v(42403.04, 66446.16) * mm, "radius": 100 * mm});
            skCircle(sketch, "E1128.4", {"center": v(44009.01, 66971.1) * mm, "radius": 50 * mm});
            skCircle(sketch, "E1129.0", {"center": v(42962.38, 72270.77) * mm, "radius": 100 * mm});
            skCircle(sketch, "E1129.1", {"center": v(46278.12, 72377.02) * mm, "radius": 75 * mm});
            skCircle(sketch, "E1129.2", {"center": v(46019.97, 73321.4) * mm, "radius": 50 * mm});
            skLineSegment(sketch, "E1129.3", {"start": v(44649.01, 73814.43) * mm, "end": v(44674.45, 73616.05) * mm});
            skLineSegment(sketch, "E1129.4", {"start": v(44674.45, 73616.05) * mm, "end": v(44476.07, 73590.62) * mm});
            skLineSegment(sketch, "E1129.5", {"start": v(44476.07, 73590.62) * mm, "end": v(44450.64, 73789) * mm});
            skLineSegment(sketch, "E1129.6", {"start": v(44450.64, 73789) * mm, "end": v(44649.01, 73814.43) * mm});
            skLineSegment(sketch, "E1129.7", {"start": v(44014.37, 73479.49) * mm, "end": v(44212.74, 73504.92) * mm});
            skLineSegment(sketch, "E1129.8", {"start": v(44039.8, 73281.1) * mm, "end": v(44014.37, 73479.49) * mm});
            skLineSegment(sketch, "E1129.9", {"start": v(44238.18, 73306.54) * mm, "end": v(44039.8, 73281.1) * mm});
            skLineSegment(sketch, "E1129.10", {"start": v(44212.74, 73504.92) * mm, "end": v(44238.18, 73306.54) * mm});
            skLineSegment(sketch, "E1130.0", {"start": v(48012.96, 74458.04) * mm, "end": v(48044.72, 74210.49) * mm});
            skLineSegment(sketch, "E1130.1", {"start": v(48044.72, 74210.49) * mm, "end": v(47548.78, 74146.87) * mm});
            skLineSegment(sketch, "E1130.2", {"start": v(47548.78, 74146.87) * mm, "end": v(47517.02, 74394.42) * mm});
            skLineSegment(sketch, "E1131", {"start": v(47517.02, 74394.42) * mm, "end": v(48012.96, 74458.04) * mm});
            skCircle(sketch, "E1132.0", {"center": v(51206.19, 74656.13) * mm, "radius": 75 * mm});
            skCircle(sketch, "E1132.1", {"center": v(51528.34, 74753.64) * mm, "radius": 75 * mm});
            skLineSegment(sketch, "E1132.2", {"start": v(50345.77, 74756.63) * mm, "end": v(50421.75, 74161.46) * mm});
            skLineSegment(sketch, "E1132.3", {"start": v(50421.75, 74161.46) * mm, "end": v(49826.58, 74085.49) * mm});
            skLineSegment(sketch, "E1132.4", {"start": v(49826.58, 74085.49) * mm, "end": v(49750.6, 74680.66) * mm});
            skLineSegment(sketch, "E1132.5", {"start": v(49750.6, 74680.66) * mm, "end": v(50345.77, 74756.63) * mm});
            skCircle(sketch, "E1133.0", {"center": v(60253.93, 49604.21) * mm, "radius": 75 * mm});
            skCircle(sketch, "E1133.1", {"center": v(60217.71, 49723.85) * mm, "radius": 75 * mm});
            skCircle(sketch, "E1133.2", {"center": v(60145.29, 49963.13) * mm, "radius": 75 * mm});
            skCircle(sketch, "E1133.3", {"center": v(60065.62, 50226.34) * mm, "radius": 100 * mm});
            skLineSegment(sketch, "E1134.0", {"start": v(37127.49, 52922.32) * mm, "end": v(37272.34, 52443.76) * mm});
            skLineSegment(sketch, "E1134.1", {"start": v(36888.61, 52850.02) * mm, "end": v(37127.49, 52922.32) * mm});
            skLineSegment(sketch, "E1134.2", {"start": v(37033.46, 52371.46) * mm, "end": v(36888.61, 52850.02) * mm});
            skLineSegment(sketch, "E1134.3", {"start": v(37272.34, 52443.76) * mm, "end": v(37033.46, 52371.46) * mm});
            skLineSegment(sketch, "E1135", {"start": v(34859.77, 59971.76) * mm, "end": v(34601.33, 60825.62) * mm, "construction": true});
            skCircle(sketch, "E1136", {"center": v(34716.1, 60446.42) * mm, "radius": 100 * mm});
            skCircle(sketch, "E1137.0.1.0", {"center": v(34687.28, 60542.18) * mm, "radius": 100 * mm});
            skLineSegment(sketch, "E1137.0.1.1", {"start": v(34830.95, 60067.52) * mm, "end": v(34572.5, 60921.38) * mm, "construction": true});
            skCircle(sketch, "E1137.0.2.0", {"center": v(34658.45, 60637.93) * mm, "radius": 100 * mm});
            skLineSegment(sketch, "E1137.0.2.1", {"start": v(34802.12, 60163.27) * mm, "end": v(34543.67, 61017.13) * mm, "construction": true});
            skCircle(sketch, "E1137.0.3.0", {"center": v(34629.62, 60733.69) * mm, "radius": 100 * mm});
            skLineSegment(sketch, "E1137.0.3.1", {"start": v(34773.3, 60259.03) * mm, "end": v(34514.85, 61112.89) * mm, "construction": true});
            skLineSegment(sketch, "E1137.direction1", {"start": v(34859.77, 59971.76) * mm, "end": v(35300, 60100) * mm, "construction": true});
            skLineSegment(sketch, "E1137.direction2", {"start": v(34859.77, 59971.76) * mm, "end": v(34830.95, 60067.52) * mm, "construction": true});
            skLineSegment(sketch, "E1138.0", {"start": v(51403.27, 64510.51) * mm, "end": v(48119.06, 63518.92) * mm});
            skLineSegment(sketch, "E1138.1", {"start": v(48119.06, 63518.92) * mm, "end": v(48056.22, 63967.7) * mm});
            skLineSegment(sketch, "E1138.2", {"start": v(51272.91, 64941.22) * mm, "end": v(51403.27, 64510.51) * mm});
            skLineSegment(sketch, "E1138.3", {"start": v(48056.22, 63967.7) * mm, "end": v(51272.91, 64941.22) * mm});
            skLineSegment(sketch, "E1139.0", {"start": v(51615.9, 65546.25) * mm, "end": v(50850.2, 65314.51) * mm});
            skLineSegment(sketch, "E1139.1", {"start": v(51543.49, 65785.53) * mm, "end": v(51615.9, 65546.25) * mm});
            skLineSegment(sketch, "E1139.2", {"start": v(50777.79, 65553.8) * mm, "end": v(51543.49, 65785.53) * mm});
            skLineSegment(sketch, "E1139.3", {"start": v(50850.2, 65314.51) * mm, "end": v(50777.79, 65553.8) * mm});
            skLineSegment(sketch, "E1140", {"start": v(40436.81, 70067.58) * mm, "end": v(39441.15, 73358.44) * mm});
            skLineSegment(sketch, "E1141", {"start": v(33353.34, 67923.5) * mm, "end": v(40436.81, 70067.58) * mm});
            skLineSegment(sketch, "E1142", {"start": v(32032.97, 72408.17) * mm, "end": v(33353.34, 67923.5) * mm});
            skLineSegment(sketch, "E1143", {"start": v(36317.52, 51108.76) * mm, "end": v(24832.11, 47632.36) * mm, "construction": true});
            skLineSegment(sketch, "E1144", {"start": v(24832.11, 47632.36) * mm, "end": v(21355.71, 59117.77) * mm, "construction": true});
            skLineSegment(sketch, "E1145", {"start": v(21355.71, 59117.77) * mm, "end": v(32841.12, 62594.17) * mm, "construction": true});
            skLineSegment(sketch, "E1146", {"start": v(28663.3, 61329.63) * mm, "end": v(29791.98, 57600.7) * mm});
            skLineSegment(sketch, "E1147", {"start": v(29791.98, 57600.7) * mm, "end": v(22484.38, 55388.84) * mm});
            skLineSegment(sketch, "E1148", {"start": v(22484.38, 55388.84) * mm, "end": v(21355.71, 59117.77) * mm});
            skLineSegment(sketch, "E1149", {"start": v(28663.3, 61329.63) * mm, "end": v(21355.71, 59117.77) * mm});
            skSolve(sketch);
        }
        {
            var Q0;
            Q0 = qSketchRegion(id + "F1", true);
            extrude(context, id + "F2", {"entities" : qUnion([Q0]), "depth" : 400 * mm, "offsetDistance" : 25 * mm});
        }
        {
            var Q0;
            Q0=makeQuery(id+"F2.opExtrude","CAP_FACE",FACE,{"disambiguationData":[OSD([sQuery(id+"F1.wireOp",EDGE,"E1119.4"),sQuery(id+"F1.wireOp",EDGE,"E1119.5"),sQuery(id+"F1.wireOp",EDGE,"E1119.6"),sQuery(id+"F1.wireOp",EDGE,"E1119.7"),sQuery(id+"F1.wireOp",EDGE,"E1121.0"),sQuery(id+"F1.wireOp",EDGE,"E1121.1"),sQuery(id+"F1.wireOp",EDGE,"E1121.2"),sQuery(id+"F1.wireOp",EDGE,"E1121.3"),sQuery(id+"F1.wireOp",EDGE,"E1121.4"),sQuery(id+"F1.wireOp",EDGE,"E1121.5"),sQuery(id+"F1.wireOp",EDGE,"E1121.6"),sQuery(id+"F1.wireOp",EDGE,"E1121.7"),sQuery(id+"F1.wireOp",EDGE,"E1121.9"),sQuery(id+"F1.wireOp",EDGE,"E1121.10"),sQuery(id+"F1.wireOp",EDGE,"E1121.11"),sQuery(id+"F1.wireOp",EDGE,"E1122"),sQuery(id+"F1.wireOp",EDGE,"E1123.0"),sQuery(id+"F1.wireOp",EDGE,"E1123.1"),sQuery(id+"F1.wireOp",EDGE,"E1123.2"),sQuery(id+"F1.wireOp",EDGE,"E1123.3"),sQuery(id+"F1.wireOp",EDGE,"E1123.4"),sQuery(id+"F1.wireOp",EDGE,"E1123.5"),sQuery(id+"F1.wireOp",EDGE,"E1123.6"),sQuery(id+"F1.wireOp",EDGE,"E1123.7"),sQuery(id+"F1.wireOp",EDGE,"E1123.8"),sQuery(id+"F1.wireOp",EDGE,"E1123.9"),sQuery(id+"F1.wireOp",EDGE,"E1123.10"),sQuery(id+"F1.wireOp",EDGE,"E1124.0"),sQuery(id+"F1.wireOp",EDGE,"E1124.1"),sQuery(id+"F1.wireOp",EDGE,"E1124.2"),sQuery(id+"F1.wireOp",EDGE,"E1124.3"),sQuery(id+"F1.wireOp",EDGE,"E1125.0"),sQuery(id+"F1.wireOp",EDGE,"E1125.1"),sQuery(id+"F1.wireOp",EDGE,"E1125.2"),sQuery(id+"F1.wireOp",EDGE,"E1125.3"),sQuery(id+"F1.wireOp",EDGE,"E1126.0"),sQuery(id+"F1.wireOp",EDGE,"E1126.1"),sQuery(id+"F1.wireOp",EDGE,"E1126.2"),sQuery(id+"F1.wireOp",EDGE,"E1126.3"),sQuery(id+"F1.wireOp",EDGE,"E1127.0"),sQuery(id+"F1.wireOp",EDGE,"E1127.1"),sQuery(id+"F1.wireOp",EDGE,"E1127.2"),sQuery(id+"F1.wireOp",EDGE,"E1127.3"),sQuery(id+"F1.wireOp",EDGE,"E1128.0"),sQuery(id+"F1.wireOp",EDGE,"E1128.1"),sQuery(id+"F1.wireOp",EDGE,"E1128.2"),sQuery(id+"F1.wireOp",EDGE,"E1128.3"),sQuery(id+"F1.wireOp",EDGE,"E1128.4"),sQuery(id+"F1.wireOp",EDGE,"E1129.0"),sQuery(id+"F1.wireOp",EDGE,"E1129.1"),sQuery(id+"F1.wireOp",EDGE,"E1129.2"),sQuery(id+"F1.wireOp",EDGE,"E1129.3"),sQuery(id+"F1.wireOp",EDGE,"E1129.4"),sQuery(id+"F1.wireOp",EDGE,"E1129.5"),sQuery(id+"F1.wireOp",EDGE,"E1129.6"),sQuery(id+"F1.wireOp",EDGE,"E1129.7"),sQuery(id+"F1.wireOp",EDGE,"E1129.8"),sQuery(id+"F1.wireOp",EDGE,"E1129.9"),sQuery(id+"F1.wireOp",EDGE,"E1129.10"),sQuery(id+"F1.wireOp",EDGE,"E1130.0"),sQuery(id+"F1.wireOp",EDGE,"E1130.1"),sQuery(id+"F1.wireOp",EDGE,"E1130.2"),sQuery(id+"F1.wireOp",EDGE,"E1131"),sQuery(id+"F1.wireOp",EDGE,"E1132.0"),sQuery(id+"F1.wireOp",EDGE,"E1132.1"),sQuery(id+"F1.wireOp",EDGE,"E1132.2"),sQuery(id+"F1.wireOp",EDGE,"E1132.3"),sQuery(id+"F1.wireOp",EDGE,"E1132.4"),sQuery(id+"F1.wireOp",EDGE,"E1132.5"),sQuery(id+"F1.wireOp",EDGE,"E1133.0"),sQuery(id+"F1.wireOp",EDGE,"E1133.1"),sQuery(id+"F1.wireOp",EDGE,"E1133.2"),sQuery(id+"F1.wireOp",EDGE,"E1133.3")])],"isStart":false});
            var sketch = newSketch(context, id + "F3", { "sketchPlane" : qUnion([Q0])});
            skLineSegment(sketch, "E1150.0", {"start": v(36317.52, 51108.76) * mm, "end": v(40724.12, 52442.55) * mm});
            skLineSegment(sketch, "E1150.1", {"start": v(40724.12, 52442.55) * mm, "end": v(39664.46, 55943.5) * mm});
            skLineSegment(sketch, "E1150.2", {"start": v(29657.7, 73111.61) * mm, "end": v(36317.52, 51108.76) * mm});
            skLineSegment(sketch, "E1150.3", {"start": v(39664.46, 55943.5) * mm, "end": v(44744.96, 57481.26) * mm});
            skLineSegment(sketch, "E1150.4", {"start": v(44495.22, 57370.06) * mm, "end": v(44744.96, 57481.26) * mm});
            skLineSegment(sketch, "E1150.5", {"start": v(49699.07, 58945.12) * mm, "end": v(44495.22, 57370.06) * mm});
            skLineSegment(sketch, "E1150.6", {"start": v(53744.87, 45578.51) * mm, "end": v(49699.07, 58945.12) * mm});
            skLineSegment(sketch, "E1150.7", {"start": v(67446.81, 49725.81) * mm, "end": v(53744.87, 45578.51) * mm});
            skLineSegment(sketch, "E1150.8", {"start": v(67662.85, 49333.51) * mm, "end": v(67446.81, 49725.81) * mm});
            skLineSegment(sketch, "E1150.9", {"start": v(68188.43, 49622.94) * mm, "end": v(67662.85, 49333.51) * mm});
            skLineSegment(sketch, "E1150.10", {"start": v(68188.43, 49622.94) * mm, "end": v(53564.5, 76178.39) * mm});
            skLineSegment(sketch, "E1150.11", {"start": v(53564.5, 76178.39) * mm, "end": v(29657.7, 73111.61) * mm});
            skLineSegment(sketch, "E1151.1", {"start": v(32831.65, 66077.32) * mm, "end": v(32898.61, 66097.6) * mm});
            skPoint(sketch, "E1151.2", {"position": v(32865.13, 66087.46) * mm});
            skLineSegment(sketch, "E1152.0", {"start": v(39517.02, 53123.18) * mm, "end": v(38457.33, 56624.2) * mm});
            skLineSegment(sketch, "E1152.1", {"start": v(36984.58, 52356.66) * mm, "end": v(39517.02, 53123.18) * mm});
            skLineSegment(sketch, "E1153", {"start": v(54412.26, 46825.25) * mm, "end": v(50354.93, 60230) * mm});
            skLineSegment(sketch, "E1154", {"start": v(38457.33, 56624.2) * mm, "end": v(50354.93, 60230) * mm});
            skLineSegment(sketch, "E1155", {"start": v(36984.58, 52356.66) * mm, "end": v(31027.58, 72279.15) * mm});
            skLineSegment(sketch, "E1156", {"start": v(31027.58, 72279.15) * mm, "end": v(52857.63, 75079.51) * mm});
            skLineSegment(sketch, "E1157", {"start": v(54412.26, 46825.25) * mm, "end": v(66562.27, 50502.76) * mm});
            skLineSegment(sketch, "E1158", {"start": v(52857.63, 75079.51) * mm, "end": v(66562.27, 50502.76) * mm});
            skLineSegment(sketch, "E1159.0", {"start": v(35451.43, 66962.45) * mm, "end": v(35364.5, 67249.58) * mm});
            skLineSegment(sketch, "E1159.1", {"start": v(34733.6, 66745.13) * mm, "end": v(35451.43, 66962.45) * mm});
            skLineSegment(sketch, "E1159.2", {"start": v(34733.6, 66745.13) * mm, "end": v(34646.67, 67032.26) * mm});
            skLineSegment(sketch, "E1159.3", {"start": v(34646.67, 67032.26) * mm, "end": v(35364.5, 67249.58) * mm});
            skLineSegment(sketch, "E1159.4", {"start": v(39083.27, 63669.72) * mm, "end": v(39616.76, 64394.56) * mm});
            skLineSegment(sketch, "E1159.5", {"start": v(38841.66, 63847.55) * mm, "end": v(39375.14, 64572.39) * mm});
            skLineSegment(sketch, "E1159.6", {"start": v(39616.76, 64394.56) * mm, "end": v(39375.14, 64572.39) * mm});
            skLineSegment(sketch, "E1159.7", {"start": v(39083.27, 63669.72) * mm, "end": v(38841.66, 63847.55) * mm});
            skLineSegment(sketch, "E1159.8", {"start": v(41611.2, 67103.98) * mm, "end": v(42174.33, 67869.09) * mm});
            skLineSegment(sketch, "E1159.9", {"start": v(41369.6, 67281.8) * mm, "end": v(41932.72, 68046.92) * mm});
            skLineSegment(sketch, "E1159.10", {"start": v(41611.2, 67103.98) * mm, "end": v(41369.6, 67281.8) * mm});
            skLineSegment(sketch, "E1159.11", {"start": v(42174.33, 67869.09) * mm, "end": v(41932.72, 68046.92) * mm});
            skSolve(sketch);
        }
        {
            var Q0;
            Q0 = qSketchRegion(id + "F3", true);
            var Q1;
            Q1 = qSketchRegion(id + "F8", true);
            extrude(context, id + "F4", {"entities" : qUnion([Q0, Q1]), "operationType" : NewBodyOperationType.ADD, "depth" : 2680 * mm, "offsetDistance" : 25 * mm});
        }
        {
            var Q0;
            Q0=makeQuery(id+"F4.opExtrude","CAP_FACE",FACE,{"disambiguationData":[OSD([sQuery(id+"F3.wireOp",EDGE,"E1150.0"),sQuery(id+"F3.wireOp",EDGE,"E1150.1"),sQuery(id+"F3.wireOp",EDGE,"E1150.2"),sQuery(id+"F3.wireOp",EDGE,"E1150.3"),sQuery(id+"F3.wireOp",EDGE,"E1150.4"),sQuery(id+"F3.wireOp",EDGE,"E1150.5"),sQuery(id+"F3.wireOp",EDGE,"E1150.6"),sQuery(id+"F3.wireOp",EDGE,"E1150.7"),sQuery(id+"F3.wireOp",EDGE,"E1150.8"),sQuery(id+"F3.wireOp",EDGE,"E1150.9"),sQuery(id+"F3.wireOp",EDGE,"E1150.10"),sQuery(id+"F3.wireOp",EDGE,"E1150.11"),sQuery(id+"F3.wireOp",EDGE,"E1152.0"),sQuery(id+"F3.wireOp",EDGE,"E1152.1"),sQuery(id+"F3.wireOp",EDGE,"E1153"),sQuery(id+"F3.wireOp",EDGE,"E1154"),sQuery(id+"F3.wireOp",EDGE,"E1155"),sQuery(id+"F3.wireOp",EDGE,"E1156"),sQuery(id+"F3.wireOp",EDGE,"E1157"),sQuery(id+"F3.wireOp",EDGE,"E1158")])],"isStart":false});
            var sketch = newSketch(context, id + "F5", { "sketchPlane" : qUnion([Q0])});
            skLineSegment(sketch, "E1160", {"start": v(51770.17, 58464.6) * mm, "end": v(54162.96, 59188.84) * mm});
            skLineSegment(sketch, "E1161", {"start": v(54162.96, 59188.84) * mm, "end": v(54485.98, 58121.66) * mm});
            skLineSegment(sketch, "E1162", {"start": v(54485.98, 58121.66) * mm, "end": v(52093.19, 57397.4) * mm});
            skLineSegment(sketch, "E1163", {"start": v(52093.19, 57397.4) * mm, "end": v(51770.17, 58464.6) * mm});
            skLineSegment(sketch, "E1164", {"start": v(32836.43, 66170.24) * mm, "end": v(32873.25, 66181.39) * mm});
            skLineSegment(sketch, "E1165", {"start": v(32873.25, 66181.39) * mm, "end": v(32848.77, 66262.26) * mm});
            skLineSegment(sketch, "E1166", {"start": v(32848.77, 66262.26) * mm, "end": v(32811.95, 66251.1) * mm});
            skLineSegment(sketch, "E1167", {"start": v(32811.95, 66251.1) * mm, "end": v(32836.43, 66170.24) * mm});
            skLineSegment(sketch, "E1168", {"start": v(43960, 58289.69) * mm, "end": v(38456.19, 56623.8) * mm});
            skLineSegment(sketch, "E1169", {"start": v(38456.19, 56623.8) * mm, "end": v(38245.58, 57319.62) * mm});
            skLineSegment(sketch, "E1170", {"start": v(38245.58, 57319.62) * mm, "end": v(35059.89, 59662.4) * mm});
            skLineSegment(sketch, "E1171", {"start": v(35059.89, 59662.4) * mm, "end": v(34797.37, 59582.93) * mm});
            skLineSegment(sketch, "E1172", {"start": v(34797.37, 59582.93) * mm, "end": v(34691.26, 59933.49) * mm});
            skLineSegment(sketch, "E1173", {"start": v(34691.26, 59933.49) * mm, "end": v(34691.26, 59933.49) * mm});
            skLineSegment(sketch, "E1174", {"start": v(34691.26, 59933.49) * mm, "end": v(32831.61, 66077.32) * mm});
            skLineSegment(sketch, "E1175", {"start": v(32831.61, 66077.32) * mm, "end": v(32898.61, 66097.6) * mm});
            skLineSegment(sketch, "E1176", {"start": v(32898.61, 66097.6) * mm, "end": v(32873.25, 66181.4) * mm});
            skLineSegment(sketch, "E1177", {"start": v(32873.25, 66181.4) * mm, "end": v(32873.25, 66181.4) * mm});
            skLineSegment(sketch, "E1178", {"start": v(32873.25, 66181.4) * mm, "end": v(32848.77, 66262.26) * mm});
            skLineSegment(sketch, "E1179", {"start": v(32848.77, 66262.26) * mm, "end": v(34498.21, 66761.5) * mm});
            skLineSegment(sketch, "E1180", {"start": v(34498.21, 66761.5) * mm, "end": v(43976.87, 59773.24) * mm});
            skLineSegment(sketch, "E1181", {"start": v(43976.87, 59773.24) * mm, "end": v(44386.76, 58418.84) * mm});
            skLineSegment(sketch, "E1182", {"start": v(44386.76, 58418.84) * mm, "end": v(43960, 58289.69) * mm});
            skCircle(sketch, "E1183", {"center": v(0, 0) * mm, "radius": 1927.6 * mm});
            skLineSegment(sketch, "E1184", {"start": v(0, 5000) * mm, "end": v(0, -5000) * mm});
            skLineSegment(sketch, "E1185", {"start": v(5000, 0) * mm, "end": v(-5000, 0) * mm});
            skLineSegment(sketch, "E1186", {"start": v(40821.64, 52368.74) * mm, "end": v(36180.25, 50963.89) * mm});
            skLineSegment(sketch, "E1187", {"start": v(36180.25, 50963.89) * mm, "end": v(32064.85, 64250) * mm});
            skLineSegment(sketch, "E1188", {"start": v(32064.85, 64250) * mm, "end": v(32173.04, 64283.5) * mm});
            skLineSegment(sketch, "E1189", {"start": v(32173.04, 64283.5) * mm, "end": v(30808.41, 68792) * mm});
            skLineSegment(sketch, "E1190", {"start": v(30808.41, 68792) * mm, "end": v(31976.13, 69145.44) * mm});
            skLineSegment(sketch, "E1191", {"start": v(31976.13, 69145.44) * mm, "end": v(32873.26, 66181.36) * mm});
            skLineSegment(sketch, "E1192", {"start": v(32873.26, 66181.36) * mm, "end": v(32898.62, 66097.57) * mm});
            skLineSegment(sketch, "E1193", {"start": v(32898.62, 66097.57) * mm, "end": v(32831.62, 66077.29) * mm});
            skLineSegment(sketch, "E1194", {"start": v(32831.62, 66077.29) * mm, "end": v(34858.84, 59379.85) * mm});
            skLineSegment(sketch, "E1195", {"start": v(34858.84, 59379.85) * mm, "end": v(36984.59, 52356.63) * mm});
            skLineSegment(sketch, "E1196", {"start": v(36984.59, 52356.63) * mm, "end": v(39517.4, 53123.26) * mm});
            skLineSegment(sketch, "E1197", {"start": v(39517.4, 53123.26) * mm, "end": v(38456.26, 56623.78) * mm});
            skLineSegment(sketch, "E1198", {"start": v(38456.26, 56623.78) * mm, "end": v(44173.39, 58354.24) * mm});
            skLineSegment(sketch, "E1199", {"start": v(44173.39, 58354.24) * mm, "end": v(44173.38, 58354.26) * mm});
            skLineSegment(sketch, "E1200", {"start": v(44173.38, 58354.26) * mm, "end": v(44386.76, 58418.84) * mm});
            skLineSegment(sketch, "E1201", {"start": v(44386.76, 58418.84) * mm, "end": v(44698.03, 57390.3) * mm});
            skLineSegment(sketch, "E1202", {"start": v(44698.03, 57390.3) * mm, "end": v(44535, 57340.97) * mm});
            skLineSegment(sketch, "E1203", {"start": v(44535, 57340.97) * mm, "end": v(40352.33, 56051.35) * mm});
            skLineSegment(sketch, "E1204", {"start": v(40352.33, 56051.35) * mm, "end": v(39761.15, 55872.41) * mm});
            skLineSegment(sketch, "E1205", {"start": v(39761.15, 55872.41) * mm, "end": v(40821.64, 52368.74) * mm});
            skLineSegment(sketch, "E1206", {"start": v(41514, 49288.29) * mm, "end": v(41733.89, 49354.84) * mm});
            skLineSegment(sketch, "E1207", {"start": v(41733.89, 49354.84) * mm, "end": v(40821.64, 52368.74) * mm});
            skLineSegment(sketch, "E1208", {"start": v(36180.25, 50963.89) * mm, "end": v(37092.14, 47951.16) * mm});
            skLineSegment(sketch, "E1209", {"start": v(37092.14, 47951.16) * mm, "end": v(40092.18, 48859.21) * mm});
            skLineSegment(sketch, "E1210", {"start": v(40092.18, 48859.21) * mm, "end": v(40939.74, 49114.47) * mm});
            skLineSegment(sketch, "E1211", {"start": v(40939.74, 49114.47) * mm, "end": v(40939.38, 49115.64) * mm});
            skLineSegment(sketch, "E1212", {"start": v(40939.38, 49115.64) * mm, "end": v(41513.65, 49289.46) * mm});
            skLineSegment(sketch, "E1213", {"start": v(41513.65, 49289.46) * mm, "end": v(41514, 49288.29) * mm});
            skLineSegment(sketch, "E1214", {"start": v(52857.63, 75079.5) * mm, "end": v(30993.3, 72260.06) * mm});
            skLineSegment(sketch, "E1215", {"start": v(30993.3, 72260.06) * mm, "end": v(32811.95, 66251.1) * mm});
            skLineSegment(sketch, "E1216", {"start": v(32811.95, 66251.1) * mm, "end": v(34498.21, 66761.5) * mm});
            skLineSegment(sketch, "E1217", {"start": v(43976.87, 59773.24) * mm, "end": v(43824.88, 60275.5) * mm});
            skLineSegment(sketch, "E1218", {"start": v(43824.88, 60275.5) * mm, "end": v(43657.05, 60829.94) * mm});
            skLineSegment(sketch, "E1219", {"start": v(43657.05, 60829.94) * mm, "end": v(43529.65, 61250.85) * mm});
            skLineSegment(sketch, "E1220", {"start": v(43529.65, 61250.85) * mm, "end": v(43816.78, 61337.76) * mm});
            skLineSegment(sketch, "E1221", {"start": v(43816.78, 61337.76) * mm, "end": v(44112, 60362.4) * mm});
            skLineSegment(sketch, "E1222", {"start": v(44112, 60362.4) * mm, "end": v(44912.08, 60604.56) * mm});
            skLineSegment(sketch, "E1223", {"start": v(44912.08, 60604.56) * mm, "end": v(48658.24, 61738.45) * mm});
            skLineSegment(sketch, "E1224", {"start": v(48658.24, 61738.45) * mm, "end": v(48658.25, 61738.42) * mm});
            skLineSegment(sketch, "E1225", {"start": v(48658.25, 61738.42) * mm, "end": v(48672.7, 61742.8) * mm});
            skLineSegment(sketch, "E1226", {"start": v(48672.7, 61742.8) * mm, "end": v(48691.53, 61680.62) * mm});
            skLineSegment(sketch, "E1227", {"start": v(48691.53, 61680.62) * mm, "end": v(49237.07, 61845.75) * mm});
            skLineSegment(sketch, "E1228", {"start": v(49237.07, 61845.75) * mm, "end": v(49551.4, 60807.28) * mm});
            skLineSegment(sketch, "E1229", {"start": v(49551.4, 60807.28) * mm, "end": v(49005.84, 60642.15) * mm});
            skLineSegment(sketch, "E1230", {"start": v(49005.84, 60642.15) * mm, "end": v(49234.65, 59886.19) * mm});
            skLineSegment(sketch, "E1231", {"start": v(49234.65, 59886.19) * mm, "end": v(49686.26, 60022.88) * mm});
            skLineSegment(sketch, "E1232", {"start": v(49686.26, 60022.88) * mm, "end": v(50519.2, 57271.05) * mm});
            skLineSegment(sketch, "E1233", {"start": v(50519.2, 57271.05) * mm, "end": v(50997.74, 57415.9) * mm});
            skLineSegment(sketch, "E1234", {"start": v(50997.74, 57415.9) * mm, "end": v(51286.65, 56461.42) * mm});
            skLineSegment(sketch, "E1235", {"start": v(51286.65, 56461.42) * mm, "end": v(50808.12, 56316.58) * mm});
            skLineSegment(sketch, "E1236", {"start": v(50808.12, 56316.58) * mm, "end": v(52360, 51189.43) * mm});
            skLineSegment(sketch, "E1237", {"start": v(52360, 51189.43) * mm, "end": v(53029.95, 51392.2) * mm});
            skLineSegment(sketch, "E1238", {"start": v(53029.95, 51392.2) * mm, "end": v(53284.88, 50550) * mm});
            skLineSegment(sketch, "E1239", {"start": v(53284.88, 50550) * mm, "end": v(53284.88, 50549.99) * mm});
            skLineSegment(sketch, "E1240", {"start": v(53284.88, 50549.99) * mm, "end": v(53284.9, 50550) * mm});
            skLineSegment(sketch, "E1241", {"start": v(53284.9, 50550) * mm, "end": v(53342.85, 50358.57) * mm});
            skLineSegment(sketch, "E1242", {"start": v(53342.85, 50358.57) * mm, "end": v(53342.82, 50358.56) * mm});
            skLineSegment(sketch, "E1243", {"start": v(53342.82, 50358.56) * mm, "end": v(52672.88, 50155.74) * mm});
            skLineSegment(sketch, "E1244", {"start": v(52672.88, 50155.74) * mm, "end": v(53923.22, 46024.85) * mm});
            skLineSegment(sketch, "E1245", {"start": v(53923.22, 46024.85) * mm, "end": v(66870.92, 49943.91) * mm});
            skLineSegment(sketch, "E1246", {"start": v(66870.92, 49943.91) * mm, "end": v(52857.63, 75079.5) * mm});
            skLineSegment(sketch, "E1247", {"start": v(55773.92, 58460.79) * mm, "end": v(59288.2, 52158.11) * mm});
            skLineSegment(sketch, "E1248", {"start": v(59288.2, 52158.11) * mm, "end": v(54024.35, 50564.85) * mm});
            skLineSegment(sketch, "E1249", {"start": v(54024.35, 50564.85) * mm, "end": v(53776.84, 51382.57) * mm});
            skLineSegment(sketch, "E1250", {"start": v(53776.84, 51382.57) * mm, "end": v(52040.99, 57121.13) * mm});
            skLineSegment(sketch, "E1251", {"start": v(52040.99, 57121.13) * mm, "end": v(51926.13, 57086.36) * mm});
            skLineSegment(sketch, "E1252", {"start": v(51926.13, 57086.36) * mm, "end": v(51428.05, 58731.95) * mm});
            skLineSegment(sketch, "E1253", {"start": v(51428.05, 58731.95) * mm, "end": v(51667.33, 58804.37) * mm});
            skLineSegment(sketch, "E1254", {"start": v(51667.33, 58804.37) * mm, "end": v(51006.81, 60986.6) * mm});
            skLineSegment(sketch, "E1255", {"start": v(51006.81, 60986.6) * mm, "end": v(53399.6, 61710.85) * mm});
            skLineSegment(sketch, "E1256", {"start": v(53399.6, 61710.85) * mm, "end": v(53326.1, 61953.71) * mm});
            skLineSegment(sketch, "E1257", {"start": v(53326.1, 61953.71) * mm, "end": v(53565.37, 62026.14) * mm});
            skLineSegment(sketch, "E1258", {"start": v(53565.37, 62026.14) * mm, "end": v(54725.26, 58194.08) * mm});
            skLineSegment(sketch, "E1259", {"start": v(54725.26, 58194.08) * mm, "end": v(54725.37, 58194.12) * mm});
            skLineSegment(sketch, "E1260", {"start": v(54725.37, 58194.12) * mm, "end": v(54739.43, 58147.67) * mm});
            skLineSegment(sketch, "E1261", {"start": v(54739.43, 58147.67) * mm, "end": v(55773.92, 58460.79) * mm});
            skLineSegment(sketch, "E1262", {"start": v(50807.1, 66172.13) * mm, "end": v(50736.28, 66075.25) * mm});
            skLineSegment(sketch, "E1263", {"start": v(50736.28, 66075.25) * mm, "end": v(49929.2, 66665.23) * mm});
            skLineSegment(sketch, "E1264", {"start": v(49929.2, 66665.23) * mm, "end": v(50000.02, 66762.1) * mm});
            skLineSegment(sketch, "E1265", {"start": v(50000.02, 66762.1) * mm, "end": v(50807.1, 66172.13) * mm});
            skLineSegment(sketch, "E1266", {"start": v(51388.26, 64560.11) * mm, "end": v(48028.73, 63543.32) * mm});
            skLineSegment(sketch, "E1267", {"start": v(48028.73, 63543.32) * mm, "end": v(47898.37, 63974.02) * mm});
            skLineSegment(sketch, "E1268", {"start": v(47898.37, 63974.02) * mm, "end": v(51257.9, 64990.82) * mm});
            skLineSegment(sketch, "E1269", {"start": v(51257.9, 64990.82) * mm, "end": v(51388.26, 64560.11) * mm});
            skLineSegment(sketch, "E1270", {"start": v(50006.48, 65066.83) * mm, "end": v(50041.24, 64951.98) * mm});
            skLineSegment(sketch, "E1271", {"start": v(50041.24, 64951.98) * mm, "end": v(49371.25, 64749.21) * mm});
            skLineSegment(sketch, "E1272", {"start": v(49371.25, 64749.21) * mm, "end": v(49336.5, 64864.07) * mm});
            skLineSegment(sketch, "E1273", {"start": v(49336.5, 64864.07) * mm, "end": v(50006.48, 65066.83) * mm});
            skLineSegment(sketch, "E1274", {"start": v(49171.71, 68915.44) * mm, "end": v(46261.51, 64962.01) * mm});
            skArc(sketch, "E1275", {"start": v(46261.51, 64962.01) * mm, "mid": v(45571.88, 65400.69) * mm, "end": v(45027.16, 66010.05) * mm});
            skArc(sketch, "E1276", {"start": v(45027.16, 66010.05) * mm, "mid": v(44701.21, 66634.86) * mm, "end": v(44503.26, 67311.2) * mm});
            skArc(sketch, "E1277", {"start": v(44503.26, 67311.2) * mm, "mid": v(44425.4, 68182.91) * mm, "end": v(44504.03, 69054.56) * mm});
            skArc(sketch, "E1278", {"start": v(44504.03, 69054.56) * mm, "mid": v(44896.73, 70371.08) * mm, "end": v(45559.41, 71574.53) * mm});
            skLineSegment(sketch, "E1279", {"start": v(45559.41, 71574.53) * mm, "end": v(49171.71, 68915.44) * mm});
            skLineSegment(sketch, "E1280", {"start": v(40453.38, 52549.86) * mm, "end": v(37222.13, 51571.83) * mm});
            skLineSegment(sketch, "E1281", {"start": v(39517.39, 53123.3) * mm, "end": v(36993.27, 52359.3) * mm});
            skLineSegment(sketch, "E1282", {"start": v(39419.14, 55966.8) * mm, "end": v(40453.38, 52549.86) * mm});
            skLineSegment(sketch, "E1283", {"start": v(38457.35, 56624.15) * mm, "end": v(39525.71, 53094.47) * mm});
            skLineSegment(sketch, "E1284", {"start": v(38457.35, 56624.15) * mm, "end": v(38977.28, 56781.52) * mm});
            skLineSegment(sketch, "E1285", {"start": v(52846.93, 58790.53) * mm, "end": v(52890.38, 58646.96) * mm});
            skLineSegment(sketch, "E1286", {"start": v(52890.38, 58646.96) * mm, "end": v(51813.62, 58321.05) * mm});
            skLineSegment(sketch, "E1287", {"start": v(53086.2, 58862.95) * mm, "end": v(53129.66, 58719.38) * mm});
            skLineSegment(sketch, "E1288", {"start": v(53129.66, 58719.38) * mm, "end": v(54206.41, 59045.3) * mm});
            skLineSegment(sketch, "E1289", {"start": v(51853.5, 57326.35) * mm, "end": v(54485.56, 58123.03) * mm});
            skLineSegment(sketch, "E1290", {"start": v(51925.92, 57087.08) * mm, "end": v(54797.27, 57956.18) * mm});
            skLineSegment(sketch, "E1291", {"start": v(51094.4, 57096.6) * mm, "end": v(51097.37, 57097.5) * mm});
            skLineSegment(sketch, "E1292", {"start": v(51166.82, 56857.31) * mm, "end": v(51169.8, 56858.21) * mm});
            skLineSegment(sketch, "E1293", {"start": v(51133.58, 56977.85) * mm, "end": v(51169.8, 56858.21) * mm});
            skLineSegment(sketch, "E1294", {"start": v(51889.7, 57206.71) * mm, "end": v(51925.92, 57087.08) * mm});
            skLineSegment(sketch, "E1295", {"start": v(51133.58, 56977.85) * mm, "end": v(51097.37, 57097.5) * mm});
            skLineSegment(sketch, "E1296", {"start": v(51889.7, 57206.71) * mm, "end": v(51853.5, 57326.35) * mm});
            skLineSegment(sketch, "E1297", {"start": v(51853.5, 57326.35) * mm, "end": v(51097.37, 57097.5) * mm});
            skLineSegment(sketch, "E1298", {"start": v(51925.92, 57087.08) * mm, "end": v(51169.8, 56858.21) * mm});
            skLineSegment(sketch, "E1299", {"start": v(53498.03, 76270.68) * mm, "end": v(68289.07, 49740.02) * mm});
            skLineSegment(sketch, "E1300", {"start": v(67328.3, 49204.38) * mm, "end": v(68289.07, 49740.02) * mm});
            skLineSegment(sketch, "E1301", {"start": v(52899.7, 75084.91) * mm, "end": v(67328.3, 49204.38) * mm});
            skLineSegment(sketch, "E1302", {"start": v(30569.38, 69581.67) * mm, "end": v(29477.51, 73189.4) * mm});
            skLineSegment(sketch, "E1303", {"start": v(31622.22, 69900.3) * mm, "end": v(30906.93, 72263.75) * mm});
            skLineSegment(sketch, "E1304", {"start": v(31622.22, 69900.3) * mm, "end": v(30569.38, 69581.67) * mm});
            skLineSegment(sketch, "E1305", {"start": v(29477.51, 73189.4) * mm, "end": v(32537.66, 73581.95) * mm});
            skLineSegment(sketch, "E1306", {"start": v(30906.93, 72263.75) * mm, "end": v(32677.62, 72490.9) * mm});
            skLineSegment(sketch, "E1307", {"start": v(32537.66, 73581.95) * mm, "end": v(32537.67, 73581.87) * mm});
            skLineSegment(sketch, "E1308", {"start": v(32588.56, 73185.12) * mm, "end": v(32677.62, 72490.9) * mm});
            skLineSegment(sketch, "E1309", {"start": v(32626.74, 72887.57) * mm, "end": v(30437.27, 72606.7) * mm});
            skLineSegment(sketch, "E1310", {"start": v(32550.4, 73482.69) * mm, "end": v(29657.57, 73111.6) * mm});
            skLineSegment(sketch, "E1311", {"start": v(32550.4, 73482.69) * mm, "end": v(32626.74, 72887.57) * mm});
            skLineSegment(sketch, "E1312", {"start": v(30437.27, 72606.7) * mm, "end": v(31287.14, 69798.9) * mm});
            skLineSegment(sketch, "E1313", {"start": v(30712.86, 69625.09) * mm, "end": v(31287.14, 69798.9) * mm});
            skLineSegment(sketch, "E1314", {"start": v(29657.57, 73111.6) * mm, "end": v(30712.86, 69625.09) * mm});
            skCircle(sketch, "E1315", {"center": v(36210.85, 49260.02) * mm, "radius": 154.35 * mm});
            skCircle(sketch, "E1316", {"center": v(35484.62, 51646.41) * mm, "radius": 154.35 * mm});
            skCircle(sketch, "E1317", {"center": v(34754.87, 54023.97) * mm, "radius": 154.35 * mm});
            skCircle(sketch, "E1318", {"center": v(34035.42, 56408.45) * mm, "radius": 154.35 * mm});
            skCircle(sketch, "E1319", {"center": v(33322.69, 58769.91) * mm, "radius": 154.35 * mm});
            skCircle(sketch, "E1320", {"center": v(32605.9, 61113.56) * mm, "radius": 154.35 * mm});
            skCircle(sketch, "E1321", {"center": v(31866.74, 63488.68) * mm, "radius": 154.35 * mm});
            skLineSegment(sketch, "E1322", {"start": v(48630.18, 64524.82) * mm, "end": v(50782.31, 65176.37) * mm});
            skLineSegment(sketch, "E1323", {"start": v(50853.58, 64936.6) * mm, "end": v(48702.6, 64285.54) * mm});
            skLineSegment(sketch, "E1324", {"start": v(53328.4, 61951.88) * mm, "end": v(53400.82, 61712.6) * mm});
            skLineSegment(sketch, "E1325", {"start": v(54739.14, 58147.54) * mm, "end": v(55773.63, 58460.66) * mm});
            skLineSegment(sketch, "E1326", {"start": v(54797.08, 57956.12) * mm, "end": v(55677.4, 58222.57) * mm});
            skLineSegment(sketch, "E1327", {"start": v(52846.93, 58790.5) * mm, "end": v(52082.46, 61316.08) * mm});
            skLineSegment(sketch, "E1328", {"start": v(52321.73, 61388.5) * mm, "end": v(52082.46, 61316.08) * mm});
            skLineSegment(sketch, "E1329", {"start": v(53086.2, 58862.93) * mm, "end": v(52321.73, 61388.5) * mm});
            skLineSegment(sketch, "E1330", {"start": v(53086.2, 58862.93) * mm, "end": v(52846.93, 58790.5) * mm});
            skLineSegment(sketch, "E1331", {"start": v(57793.68, 52268.9) * mm, "end": v(58968.18, 52624.48) * mm});
            skLineSegment(sketch, "E1332", {"start": v(59098.58, 52193.79) * mm, "end": v(58968.18, 52624.48) * mm});
            skLineSegment(sketch, "E1333", {"start": v(57924.07, 51838.21) * mm, "end": v(59098.58, 52193.79) * mm});
            skLineSegment(sketch, "E1334", {"start": v(57924.07, 51838.21) * mm, "end": v(57793.68, 52268.9) * mm});
            skLineSegment(sketch, "E1335", {"start": v(55773.63, 58460.66) * mm, "end": v(59287.5, 52158.7) * mm});
            skLineSegment(sketch, "E1336", {"start": v(55677.4, 58222.57) * mm, "end": v(58991.9, 52278.2) * mm});
            skLineSegment(sketch, "E1337", {"start": v(59287.5, 52158.7) * mm, "end": v(53342.63, 50359.31) * mm});
            skLineSegment(sketch, "E1338", {"start": v(58991.9, 52278.2) * mm, "end": v(53284.69, 50550.73) * mm});
            skLineSegment(sketch, "E1339", {"start": v(58318.92, 63332.61) * mm, "end": v(58586.76, 62852.24) * mm});
            skLineSegment(sketch, "E1340", {"start": v(58368.41, 62730.5) * mm, "end": v(58586.76, 62852.24) * mm});
            skLineSegment(sketch, "E1341", {"start": v(58100.57, 63210.86) * mm, "end": v(58368.41, 62730.5) * mm});
            skLineSegment(sketch, "E1342", {"start": v(58100.57, 63210.86) * mm, "end": v(58318.92, 63332.61) * mm});
            skLineSegment(sketch, "E1343", {"start": v(59393.32, 61405.46) * mm, "end": v(59661.17, 60925.09) * mm});
            skLineSegment(sketch, "E1344", {"start": v(59442.82, 60803.34) * mm, "end": v(59661.17, 60925.09) * mm});
            skLineSegment(sketch, "E1345", {"start": v(59174.97, 61283.7) * mm, "end": v(59442.82, 60803.34) * mm});
            skLineSegment(sketch, "E1346", {"start": v(59174.97, 61283.7) * mm, "end": v(59393.32, 61405.46) * mm});
            skLineSegment(sketch, "E1347", {"start": v(61824.92, 57043.9) * mm, "end": v(62092.77, 56563.53) * mm});
            skLineSegment(sketch, "E1348", {"start": v(61874.42, 56441.78) * mm, "end": v(62092.77, 56563.53) * mm});
            skLineSegment(sketch, "E1349", {"start": v(61606.57, 56922.15) * mm, "end": v(61874.42, 56441.78) * mm});
            skLineSegment(sketch, "E1350", {"start": v(61606.57, 56922.15) * mm, "end": v(61824.92, 57043.9) * mm});
            skLineSegment(sketch, "E1351", {"start": v(62899.33, 55116.74) * mm, "end": v(63167.18, 54636.37) * mm});
            skLineSegment(sketch, "E1352", {"start": v(62948.82, 54514.62) * mm, "end": v(63167.18, 54636.37) * mm});
            skLineSegment(sketch, "E1353", {"start": v(62680.98, 54995) * mm, "end": v(62948.82, 54514.62) * mm});
            skLineSegment(sketch, "E1354", {"start": v(62680.98, 54995) * mm, "end": v(62899.33, 55116.74) * mm});
            skLineSegment(sketch, "E1355", {"start": v(55887.31, 67694.17) * mm, "end": v(56155.16, 67213.8) * mm});
            skLineSegment(sketch, "E1356", {"start": v(55936.81, 67092.05) * mm, "end": v(56155.16, 67213.8) * mm});
            skLineSegment(sketch, "E1357", {"start": v(55668.96, 67572.42) * mm, "end": v(55936.81, 67092.05) * mm});
            skLineSegment(sketch, "E1358", {"start": v(55668.96, 67572.42) * mm, "end": v(55887.31, 67694.17) * mm});
            skLineSegment(sketch, "E1359", {"start": v(54812.9, 69621.33) * mm, "end": v(55080.76, 69140.96) * mm});
            skLineSegment(sketch, "E1360", {"start": v(54862.4, 69019.2) * mm, "end": v(55080.76, 69140.96) * mm});
            skLineSegment(sketch, "E1361", {"start": v(54594.56, 69499.58) * mm, "end": v(54862.4, 69019.2) * mm});
            skLineSegment(sketch, "E1362", {"start": v(54594.56, 69499.58) * mm, "end": v(54812.9, 69621.33) * mm});
            skLineSegment(sketch, "E1363", {"start": v(34646.9, 67031.55) * mm, "end": v(35364.72, 67248.87) * mm});
            skLineSegment(sketch, "E1364", {"start": v(35451.65, 66961.74) * mm, "end": v(35364.72, 67248.87) * mm});
            skLineSegment(sketch, "E1365", {"start": v(34733.82, 66744.42) * mm, "end": v(35451.65, 66961.74) * mm});
            skLineSegment(sketch, "E1366", {"start": v(34733.82, 66744.42) * mm, "end": v(34646.9, 67031.55) * mm});
            skLineSegment(sketch, "E1367", {"start": v(38841.67, 63847.56) * mm, "end": v(39375.15, 64572.4) * mm});
            skLineSegment(sketch, "E1368", {"start": v(39616.77, 64394.58) * mm, "end": v(39375.15, 64572.4) * mm});
            skLineSegment(sketch, "E1369", {"start": v(39083.28, 63669.74) * mm, "end": v(39616.77, 64394.58) * mm});
            skLineSegment(sketch, "E1370", {"start": v(39083.28, 63669.74) * mm, "end": v(38841.67, 63847.56) * mm});
            skLineSegment(sketch, "E1371", {"start": v(41369.6, 67281.8) * mm, "end": v(41932.72, 68046.92) * mm});
            skLineSegment(sketch, "E1372", {"start": v(42174.33, 67869.09) * mm, "end": v(41932.72, 68046.92) * mm});
            skLineSegment(sketch, "E1373", {"start": v(41611.2, 67103.98) * mm, "end": v(42174.33, 67869.09) * mm});
            skLineSegment(sketch, "E1374", {"start": v(41611.2, 67103.98) * mm, "end": v(41369.6, 67281.8) * mm});
            skLineSegment(sketch, "E1375", {"start": v(47761.19, 64288.06) * mm, "end": v(48622.58, 64548.84) * mm});
            skLineSegment(sketch, "E1376", {"start": v(48709.5, 64261.7) * mm, "end": v(48622.58, 64548.84) * mm});
            skLineSegment(sketch, "E1377", {"start": v(47848.11, 64000.93) * mm, "end": v(48709.5, 64261.7) * mm});
            skLineSegment(sketch, "E1378", {"start": v(47848.11, 64000.93) * mm, "end": v(47761.19, 64288.06) * mm});
            skLineSegment(sketch, "E1379", {"start": v(50775.01, 65200.48) * mm, "end": v(51636.4, 65461.26) * mm});
            skLineSegment(sketch, "E1380", {"start": v(51723.33, 65174.13) * mm, "end": v(51636.4, 65461.26) * mm});
            skLineSegment(sketch, "E1381", {"start": v(50861.94, 64913.35) * mm, "end": v(51723.33, 65174.13) * mm});
            skLineSegment(sketch, "E1382", {"start": v(50861.94, 64913.35) * mm, "end": v(50775.01, 65200.48) * mm});
            skFitSpline(sketch, "E1383", {"points": [v(31716.6, 63488.68) * mm, v(31716.6, 63448.48) * mm, v(31756.84, 63378.88) * mm, v(31826.5, 63338.68) * mm, v(31906.97, 63338.68) * mm, v(31976.63, 63378.88) * mm, v(32016.86, 63448.48) * mm, v(32016.86, 63528.88) * mm, v(31976.63, 63598.48) * mm, v(31906.97, 63638.68) * mm, v(31826.5, 63638.68) * mm, v(31756.84, 63598.48) * mm, v(31716.6, 63528.88) * mm, v(31716.6, 63488.68) * mm]});
            skFitSpline(sketch, "E1384", {"points": [v(32455.78, 61113.56) * mm, v(32455.78, 61073.36) * mm, v(32496, 61003.76) * mm, v(32565.67, 60963.56) * mm, v(32646.14, 60963.56) * mm, v(32715.8, 61003.76) * mm, v(32756.03, 61073.36) * mm, v(32756.03, 61153.76) * mm, v(32715.8, 61223.36) * mm, v(32646.14, 61263.56) * mm, v(32565.67, 61263.56) * mm, v(32496, 61223.36) * mm, v(32455.78, 61153.76) * mm, v(32455.78, 61113.56) * mm]});
            skFitSpline(sketch, "E1385", {"points": [v(33172.56, 58769.91) * mm, v(33172.56, 58729.71) * mm, v(33212.8, 58660.11) * mm, v(33282.45, 58619.91) * mm, v(33362.92, 58619.91) * mm, v(33432.58, 58660.11) * mm, v(33472.81, 58729.71) * mm, v(33472.81, 58810.11) * mm, v(33432.58, 58879.71) * mm, v(33362.92, 58919.91) * mm, v(33282.45, 58919.91) * mm, v(33212.8, 58879.71) * mm, v(33172.56, 58810.11) * mm, v(33172.56, 58769.91) * mm]});
            skFitSpline(sketch, "E1386", {"points": [v(33885.3, 56408.45) * mm, v(33885.3, 56368.25) * mm, v(33925.53, 56298.65) * mm, v(33995.19, 56258.45) * mm, v(34075.65, 56258.45) * mm, v(34145.31, 56298.65) * mm, v(34185.55, 56368.25) * mm, v(34185.55, 56448.65) * mm, v(34145.31, 56518.25) * mm, v(34075.65, 56558.45) * mm, v(33995.19, 56558.45) * mm, v(33925.53, 56518.25) * mm, v(33885.3, 56448.65) * mm, v(33885.3, 56408.45) * mm]});
            skFitSpline(sketch, "E1387", {"points": [v(34604.74, 54023.97) * mm, v(34604.74, 53983.77) * mm, v(34644.97, 53914.17) * mm, v(34714.63, 53873.97) * mm, v(34795.1, 53873.97) * mm, v(34864.76, 53914.17) * mm, v(34905, 53983.77) * mm, v(34905, 54064.17) * mm, v(34864.76, 54133.77) * mm, v(34795.1, 54173.97) * mm, v(34714.63, 54173.97) * mm, v(34644.97, 54133.77) * mm, v(34604.74, 54064.17) * mm, v(34604.74, 54023.97) * mm]});
            skFitSpline(sketch, "E1388", {"points": [v(35334.5, 51646.41) * mm, v(35334.5, 51606.21) * mm, v(35374.72, 51536.61) * mm, v(35444.38, 51496.41) * mm, v(35524.85, 51496.41) * mm, v(35594.5, 51536.61) * mm, v(35634.74, 51606.21) * mm, v(35634.74, 51686.61) * mm, v(35594.5, 51756.21) * mm, v(35524.85, 51796.41) * mm, v(35444.38, 51796.41) * mm, v(35374.72, 51756.21) * mm, v(35334.5, 51686.61) * mm, v(35334.5, 51646.41) * mm]});
            skFitSpline(sketch, "E1389", {"points": [v(36060.72, 49260.02) * mm, v(36060.72, 49219.82) * mm, v(36100.96, 49150.22) * mm, v(36170.62, 49110.02) * mm, v(36251.08, 49110.02) * mm, v(36320.74, 49150.22) * mm, v(36360.98, 49219.82) * mm, v(36360.98, 49300.22) * mm, v(36320.74, 49369.82) * mm, v(36251.08, 49410.02) * mm, v(36170.62, 49410.02) * mm, v(36100.96, 49369.82) * mm, v(36060.72, 49300.22) * mm, v(36060.72, 49260.02) * mm]});
            skLineSegment(sketch, "E1390", {"start": v(44643.85, 60262.18) * mm, "end": v(43994.5, 60065.64) * mm});
            skLineSegment(sketch, "E1391", {"start": v(44571.42, 60501.46) * mm, "end": v(43922.08, 60304.92) * mm});
            skLineSegment(sketch, "E1392", {"start": v(46706.46, 60886.47) * mm, "end": v(45505.25, 60522.9) * mm});
            skLineSegment(sketch, "E1393", {"start": v(45964.73, 60661.97) * mm, "end": v(45505.25, 60522.9) * mm});
            skLineSegment(sketch, "E1394", {"start": v(46634.04, 61125.75) * mm, "end": v(45432.83, 60762.18) * mm});
            skLineSegment(sketch, "E1395", {"start": v(46706.46, 60886.47) * mm, "end": v(46156.15, 60719.9) * mm});
            skLineSegment(sketch, "E1396", {"start": v(48505.85, 61431.1) * mm, "end": v(47759.3, 61205.13) * mm});
            skLineSegment(sketch, "E1397", {"start": v(48672.7, 61742.8) * mm, "end": v(47686.87, 61444.41) * mm});
            skLineSegment(sketch, "E1398", {"start": v(45469.04, 60642.54) * mm, "end": v(45505.25, 60522.9) * mm});
            skLineSegment(sketch, "E1399", {"start": v(44607.63, 60381.82) * mm, "end": v(44643.85, 60262.18) * mm});
            skLineSegment(sketch, "E1400", {"start": v(45469.04, 60642.54) * mm, "end": v(45432.83, 60762.18) * mm});
            skLineSegment(sketch, "E1401", {"start": v(44607.63, 60381.82) * mm, "end": v(44571.42, 60501.46) * mm});
            skLineSegment(sketch, "E1402", {"start": v(44571.42, 60501.46) * mm, "end": v(45432.83, 60762.18) * mm});
            skLineSegment(sketch, "E1403", {"start": v(44643.85, 60262.18) * mm, "end": v(45505.25, 60522.9) * mm});
            skLineSegment(sketch, "E1404", {"start": v(47723.08, 61324.77) * mm, "end": v(47759.3, 61205.13) * mm});
            skLineSegment(sketch, "E1405", {"start": v(46670.25, 61006.11) * mm, "end": v(46706.46, 60886.47) * mm});
            skLineSegment(sketch, "E1406", {"start": v(47723.08, 61324.77) * mm, "end": v(47686.87, 61444.41) * mm});
            skLineSegment(sketch, "E1407", {"start": v(46670.25, 61006.11) * mm, "end": v(46634.04, 61125.75) * mm});
            skLineSegment(sketch, "E1408", {"start": v(46634.04, 61125.75) * mm, "end": v(47686.87, 61444.41) * mm});
            skLineSegment(sketch, "E1409", {"start": v(46706.46, 60886.47) * mm, "end": v(47759.3, 61205.13) * mm});
            skLineSegment(sketch, "E1410", {"start": v(48672.7, 61742.8) * mm, "end": v(49476.62, 59086.75) * mm});
            skLineSegment(sketch, "E1411", {"start": v(48505.85, 61431.1) * mm, "end": v(49091.04, 59497.67) * mm});
            skLineSegment(sketch, "E1412", {"start": v(43816.8, 61337.9) * mm, "end": v(44769.56, 58189.64) * mm});
            skLineSegment(sketch, "E1413", {"start": v(43529.67, 61251) * mm, "end": v(44628.7, 57619.38) * mm});
            skLineSegment(sketch, "E1414", {"start": v(43529.67, 61251) * mm, "end": v(43816.8, 61337.9) * mm});
            skLineSegment(sketch, "E1415", {"start": v(46623.05, 58486.85) * mm, "end": v(45964.73, 60661.97) * mm});
            skLineSegment(sketch, "E1416", {"start": v(46814.48, 58544.78) * mm, "end": v(46156.15, 60719.9) * mm});
            skLineSegment(sketch, "E1417", {"start": v(53518.26, 76262.35) * mm, "end": v(68188.43, 49622.94) * mm});
            skLineSegment(sketch, "E1418", {"start": v(52992.69, 75972.92) * mm, "end": v(67662.85, 49333.51) * mm});
            skLineSegment(sketch, "E1419", {"start": v(52992.69, 75972.92) * mm, "end": v(53518.26, 76262.35) * mm});
            skCircle(sketch, "E1420", {"center": v(67421.4, 50393.86) * mm, "radius": 300 * mm});
            skCircle(sketch, "E1421", {"center": v(67780.92, 49741.01) * mm, "radius": 300 * mm});
            skCircle(sketch, "E1422", {"center": v(53400.19, 75854.85) * mm, "radius": 300 * mm});
            skLineSegment(sketch, "E1423", {"start": v(53400.19, 75854.85) * mm, "end": v(66847.85, 51435.37) * mm});
            skCircle(sketch, "E1424", {"center": v(53759.7, 75202) * mm, "radius": 300 * mm});
            skCircle(sketch, "E1425", {"center": v(54119.23, 74549.16) * mm, "radius": 300 * mm});
            skCircle(sketch, "E1426", {"center": v(54478.74, 73896.31) * mm, "radius": 300 * mm});
            skCircle(sketch, "E1427", {"center": v(54838.26, 73243.47) * mm, "radius": 300 * mm});
            skCircle(sketch, "E1428", {"center": v(55197.78, 72590.62) * mm, "radius": 300 * mm});
            skCircle(sketch, "E1429", {"center": v(55557.3, 71937.77) * mm, "radius": 300 * mm});
            skCircle(sketch, "E1430", {"center": v(55916.82, 71284.93) * mm, "radius": 300 * mm});
            skCircle(sketch, "E1431", {"center": v(56276.34, 70632.08) * mm, "radius": 300 * mm});
            skCircle(sketch, "E1432", {"center": v(56635.85, 69979.24) * mm, "radius": 300 * mm});
            skCircle(sketch, "E1433", {"center": v(56995.37, 69326.4) * mm, "radius": 300 * mm});
            skCircle(sketch, "E1434", {"center": v(57354.9, 68673.55) * mm, "radius": 300 * mm});
            skCircle(sketch, "E1435", {"center": v(57714.4, 68020.7) * mm, "radius": 300 * mm});
            skCircle(sketch, "E1436", {"center": v(58073.93, 67367.85) * mm, "radius": 300 * mm});
            skCircle(sketch, "E1437", {"center": v(58433.45, 66715) * mm, "radius": 300 * mm});
            skCircle(sketch, "E1438", {"center": v(58792.97, 66062.16) * mm, "radius": 300 * mm});
            skCircle(sketch, "E1439", {"center": v(59152.48, 65409.32) * mm, "radius": 300 * mm});
            skCircle(sketch, "E1440", {"center": v(59512, 64756.47) * mm, "radius": 300 * mm});
            skCircle(sketch, "E1441", {"center": v(59871.52, 64103.62) * mm, "radius": 300 * mm});
            skCircle(sketch, "E1442", {"center": v(60231.04, 63450.78) * mm, "radius": 300 * mm});
            skCircle(sketch, "E1443", {"center": v(60590.56, 62797.93) * mm, "radius": 300 * mm});
            skCircle(sketch, "E1444", {"center": v(60950.08, 62145.09) * mm, "radius": 300 * mm});
            skCircle(sketch, "E1445", {"center": v(61309.6, 61492.24) * mm, "radius": 300 * mm});
            skCircle(sketch, "E1446", {"center": v(61669.11, 60839.4) * mm, "radius": 300 * mm});
            skCircle(sketch, "E1447", {"center": v(62028.63, 60186.55) * mm, "radius": 300 * mm});
            skCircle(sketch, "E1448", {"center": v(62388.15, 59533.7) * mm, "radius": 300 * mm});
            skCircle(sketch, "E1449", {"center": v(62747.67, 58880.86) * mm, "radius": 300 * mm});
            skCircle(sketch, "E1450", {"center": v(63107.19, 58228.01) * mm, "radius": 300 * mm});
            skCircle(sketch, "E1451", {"center": v(63466.7, 57575.16) * mm, "radius": 300 * mm});
            skCircle(sketch, "E1452", {"center": v(63826.22, 56922.32) * mm, "radius": 300 * mm});
            skCircle(sketch, "E1453", {"center": v(64185.74, 56269.47) * mm, "radius": 300 * mm});
            skCircle(sketch, "E1454", {"center": v(64545.26, 55616.63) * mm, "radius": 300 * mm});
            skCircle(sketch, "E1455", {"center": v(64904.78, 54963.78) * mm, "radius": 300 * mm});
            skCircle(sketch, "E1456", {"center": v(65264.3, 54310.94) * mm, "radius": 300 * mm});
            skCircle(sketch, "E1457", {"center": v(65623.81, 53658.09) * mm, "radius": 300 * mm});
            skCircle(sketch, "E1458", {"center": v(65983.33, 53005.24) * mm, "radius": 300 * mm});
            skCircle(sketch, "E1459", {"center": v(66342.85, 52352.4) * mm, "radius": 300 * mm});
            skCircle(sketch, "E1460", {"center": v(66702.37, 51699.55) * mm, "radius": 300 * mm});
            skCircle(sketch, "E1461", {"center": v(53579.95, 75528.43) * mm, "radius": 300 * mm});
            skCircle(sketch, "E1462", {"center": v(53939.47, 74875.58) * mm, "radius": 300 * mm});
            skCircle(sketch, "E1463", {"center": v(54298.99, 74222.74) * mm, "radius": 300 * mm});
            skCircle(sketch, "E1464", {"center": v(54658.5, 73569.89) * mm, "radius": 300 * mm});
            skCircle(sketch, "E1465", {"center": v(55018.02, 72917.04) * mm, "radius": 300 * mm});
            skCircle(sketch, "E1466", {"center": v(55377.54, 72264.2) * mm, "radius": 300 * mm});
            skCircle(sketch, "E1467", {"center": v(55737.06, 71611.35) * mm, "radius": 300 * mm});
            skCircle(sketch, "E1468", {"center": v(56096.58, 70958.5) * mm, "radius": 300 * mm});
            skCircle(sketch, "E1469", {"center": v(56456.1, 70305.66) * mm, "radius": 300 * mm});
            skCircle(sketch, "E1470", {"center": v(56815.61, 69652.81) * mm, "radius": 300 * mm});
            skCircle(sketch, "E1471", {"center": v(57175.13, 68999.97) * mm, "radius": 300 * mm});
            skCircle(sketch, "E1472", {"center": v(57534.65, 68347.12) * mm, "radius": 300 * mm});
            skCircle(sketch, "E1473", {"center": v(57894.17, 67694.28) * mm, "radius": 300 * mm});
            skCircle(sketch, "E1474", {"center": v(58253.69, 67041.43) * mm, "radius": 300 * mm});
            skCircle(sketch, "E1475", {"center": v(58613.2, 66388.58) * mm, "radius": 300 * mm});
            skCircle(sketch, "E1476", {"center": v(58972.72, 65735.74) * mm, "radius": 300 * mm});
            skCircle(sketch, "E1477", {"center": v(59332.24, 65082.9) * mm, "radius": 300 * mm});
            skCircle(sketch, "E1478", {"center": v(59691.76, 64430.05) * mm, "radius": 300 * mm});
            skCircle(sketch, "E1479", {"center": v(60051.28, 63777.2) * mm, "radius": 300 * mm});
            skCircle(sketch, "E1480", {"center": v(60410.8, 63124.35) * mm, "radius": 300 * mm});
            skCircle(sketch, "E1481", {"center": v(60770.32, 62471.5) * mm, "radius": 300 * mm});
            skCircle(sketch, "E1482", {"center": v(61129.83, 61818.66) * mm, "radius": 300 * mm});
            skCircle(sketch, "E1483", {"center": v(61489.35, 61165.82) * mm, "radius": 300 * mm});
            skCircle(sketch, "E1484", {"center": v(61848.87, 60512.97) * mm, "radius": 300 * mm});
            skCircle(sketch, "E1485", {"center": v(62208.39, 59860.13) * mm, "radius": 300 * mm});
            skCircle(sketch, "E1486", {"center": v(62567.9, 59207.28) * mm, "radius": 300 * mm});
            skCircle(sketch, "E1487", {"center": v(62927.43, 58554.43) * mm, "radius": 300 * mm});
            skCircle(sketch, "E1488", {"center": v(63286.94, 57901.59) * mm, "radius": 300 * mm});
            skCircle(sketch, "E1489", {"center": v(63646.46, 57248.74) * mm, "radius": 300 * mm});
            skCircle(sketch, "E1490", {"center": v(64005.98, 56595.9) * mm, "radius": 300 * mm});
            skCircle(sketch, "E1491", {"center": v(64725.02, 55290.2) * mm, "radius": 300 * mm});
            skCircle(sketch, "E1492", {"center": v(65084.54, 54637.36) * mm, "radius": 300 * mm});
            skCircle(sketch, "E1493", {"center": v(65444.05, 53984.51) * mm, "radius": 300 * mm});
            skCircle(sketch, "E1494", {"center": v(64365.5, 55943.05) * mm, "radius": 300 * mm});
            skCircle(sketch, "E1495", {"center": v(65803.57, 53331.67) * mm, "radius": 300 * mm});
            skCircle(sketch, "E1496", {"center": v(66163.1, 52678.82) * mm, "radius": 300 * mm});
            skCircle(sketch, "E1497", {"center": v(66522.61, 52025.97) * mm, "radius": 300 * mm});
            skCircle(sketch, "E1498", {"center": v(67061.89, 51046.7) * mm, "radius": 300 * mm});
            skCircle(sketch, "E1499", {"center": v(67241.65, 50720.28) * mm, "radius": 300 * mm});
            skCircle(sketch, "E1500", {"center": v(67601.17, 50067.44) * mm, "radius": 300 * mm});
            skCircle(sketch, "E1501", {"center": v(66882.13, 51373.13) * mm, "radius": 300 * mm});
            skLineSegment(sketch, "E1502", {"start": v(53400.19, 75854.85) * mm, "end": v(67780.92, 49741.01) * mm});
            skCircle(sketch, "E1503", {"center": v(30047.42, 72859.15) * mm, "radius": 300 * mm});
            skCircle(sketch, "E1504", {"center": v(30913.1, 69999.13) * mm, "radius": 300 * mm});
            skCircle(sketch, "E1505", {"center": v(30696.68, 70714.1) * mm, "radius": 300 * mm});
            skCircle(sketch, "E1506", {"center": v(30480.28, 71429.06) * mm, "radius": 300 * mm});
            skCircle(sketch, "E1507", {"center": v(30263.87, 72144.03) * mm, "radius": 300 * mm});
            skCircle(sketch, "E1508", {"center": v(30777.44, 72952.8) * mm, "radius": 300 * mm});
            skCircle(sketch, "E1509", {"center": v(31507.46, 73046.44) * mm, "radius": 300 * mm});
            skCircle(sketch, "E1510", {"center": v(32237.47, 73140.09) * mm, "radius": 300 * mm});
            skLineSegment(sketch, "E1511", {"start": v(30047.42, 72859.15) * mm, "end": v(31000, 69712) * mm});
            skLineSegment(sketch, "E1512", {"start": v(30047.42, 72859.15) * mm, "end": v(32588.56, 73185.13) * mm});
            skLineSegment(sketch, "E1513", {"start": v(45136.03, 55943.24) * mm, "end": v(44646.08, 57561.95) * mm});
            skLineSegment(sketch, "E1514", {"start": v(44933.22, 57648.86) * mm, "end": v(44646.08, 57561.95) * mm});
            skLineSegment(sketch, "E1515", {"start": v(45423.17, 56030.15) * mm, "end": v(44933.22, 57648.86) * mm});
            skLineSegment(sketch, "E1516", {"start": v(45423.17, 56030.15) * mm, "end": v(45136.03, 55943.24) * mm});
            skLineSegment(sketch, "E1517", {"start": v(35427.73, 72843.6) * mm, "end": v(39394.7, 73352.48) * mm});
            skLineSegment(sketch, "E1518", {"start": v(39394.7, 73352.48) * mm, "end": v(39305.64, 74046.8) * mm});
            skLineSegment(sketch, "E1519", {"start": v(39305.64, 74046.8) * mm, "end": v(35338.66, 73537.9) * mm});
            skLineSegment(sketch, "E1520", {"start": v(35338.66, 73537.9) * mm, "end": v(35367.57, 73312.56) * mm});
            skLineSegment(sketch, "E1521", {"start": v(35367.57, 73312.56) * mm, "end": v(35427.73, 72843.6) * mm});
            skLineSegment(sketch, "E1522", {"start": v(40386.58, 73479.72) * mm, "end": v(43188.62, 73839.17) * mm});
            skLineSegment(sketch, "E1523", {"start": v(43188.62, 73839.17) * mm, "end": v(43099.56, 74533.48) * mm});
            skLineSegment(sketch, "E1524", {"start": v(43099.56, 74533.48) * mm, "end": v(40297.51, 74174.03) * mm});
            skLineSegment(sketch, "E1525", {"start": v(40297.51, 74174.03) * mm, "end": v(40329.31, 73926.13) * mm});
            skLineSegment(sketch, "E1526", {"start": v(40329.31, 73926.13) * mm, "end": v(40386.58, 73479.72) * mm});
            skLineSegment(sketch, "E1527", {"start": v(44180.5, 73966.4) * mm, "end": v(47030, 74331.94) * mm});
            skLineSegment(sketch, "E1528", {"start": v(47030, 74331.94) * mm, "end": v(46940.94, 75026.25) * mm});
            skLineSegment(sketch, "E1529", {"start": v(46940.94, 75026.25) * mm, "end": v(44091.43, 74660.71) * mm});
            skLineSegment(sketch, "E1530", {"start": v(44091.43, 74660.71) * mm, "end": v(44107.75, 74533.48) * mm});
            skLineSegment(sketch, "E1531", {"start": v(44107.75, 74533.48) * mm, "end": v(44180.5, 73966.4) * mm});
            skLineSegment(sketch, "E1532", {"start": v(48021.88, 74459.18) * mm, "end": v(50970.78, 74837.52) * mm});
            skLineSegment(sketch, "E1533", {"start": v(50970.78, 74837.52) * mm, "end": v(50881.72, 75531.78) * mm});
            skLineSegment(sketch, "E1534", {"start": v(50881.72, 75531.78) * mm, "end": v(47932.81, 75153.49) * mm});
            skLineSegment(sketch, "E1535", {"start": v(47932.81, 75153.49) * mm, "end": v(48011.55, 74539.7) * mm});
            skLineSegment(sketch, "E1536", {"start": v(48011.55, 74539.7) * mm, "end": v(48021.88, 74459.18) * mm});
            skLineSegment(sketch, "E1537", {"start": v(34583.64, 74073.32) * mm, "end": v(34277.71, 74103.31) * mm});
            skLineSegment(sketch, "E1538", {"start": v(36509.2, 74336.72) * mm, "end": v(36210.42, 74264.44) * mm});
            skLineSegment(sketch, "E1539", {"start": v(38568.06, 74568.37) * mm, "end": v(38260.66, 74568.37) * mm});
            skLineSegment(sketch, "E1540", {"start": v(40630.85, 74832.8) * mm, "end": v(40326.88, 74787.02) * mm});
            skLineSegment(sketch, "E1541", {"start": v(42529.89, 75035.76) * mm, "end": v(42224.21, 75003.22) * mm});
            skLineSegment(sketch, "E1542", {"start": v(44620.7, 75346.4) * mm, "end": v(44315.83, 75306.98) * mm});
            skLineSegment(sketch, "E1543", {"start": v(46260.89, 75467.94) * mm, "end": v(45954.04, 75449.5) * mm});
            skLineSegment(sketch, "E1544", {"start": v(48411.94, 75732.02) * mm, "end": v(48106.56, 75696.83) * mm});
            skLineSegment(sketch, "E1545", {"start": v(34308.4, 74416.31) * mm, "end": v(34614.33, 74386.32) * mm});
            skLineSegment(sketch, "E1546", {"start": v(34306.57, 74397.7) * mm, "end": v(34612.5, 74367.7) * mm});
            skLineSegment(sketch, "E1547", {"start": v(34614.33, 74386.32) * mm, "end": v(34612.5, 74367.7) * mm});
            skLineSegment(sketch, "E1548", {"start": v(34585.47, 74091.93) * mm, "end": v(34583.64, 74073.32) * mm});
            skLineSegment(sketch, "E1549", {"start": v(34585.47, 74091.93) * mm, "end": v(34279.53, 74121.92) * mm});
            skLineSegment(sketch, "E1550", {"start": v(34277.71, 74103.31) * mm, "end": v(34279.53, 74121.92) * mm});
            skLineSegment(sketch, "E1551", {"start": v(34306.57, 74397.7) * mm, "end": v(34308.4, 74416.31) * mm});
            skLineSegment(sketch, "E1552", {"start": v(34465.5, 74382.12) * mm, "end": v(34438.47, 74106.34) * mm});
            skLineSegment(sketch, "E1553", {"start": v(34453.57, 74383.29) * mm, "end": v(34426.53, 74107.51) * mm});
            skLineSegment(sketch, "E1554", {"start": v(36136.47, 74570.12) * mm, "end": v(36435.25, 74642.4) * mm});
            skLineSegment(sketch, "E1555", {"start": v(36140.87, 74551.95) * mm, "end": v(36439.65, 74624.22) * mm});
            skLineSegment(sketch, "E1556", {"start": v(36435.25, 74642.4) * mm, "end": v(36439.65, 74624.22) * mm});
            skLineSegment(sketch, "E1557", {"start": v(36504.8, 74354.9) * mm, "end": v(36509.2, 74336.72) * mm});
            skLineSegment(sketch, "E1558", {"start": v(36504.8, 74354.9) * mm, "end": v(36206.02, 74282.62) * mm});
            skLineSegment(sketch, "E1559", {"start": v(36210.42, 74264.44) * mm, "end": v(36206.02, 74282.62) * mm});
            skLineSegment(sketch, "E1560", {"start": v(36140.87, 74551.95) * mm, "end": v(36136.47, 74570.12) * mm});
            skLineSegment(sketch, "E1561", {"start": v(36296.1, 74589.5) * mm, "end": v(36361.24, 74320.16) * mm});
            skLineSegment(sketch, "E1562", {"start": v(36284.43, 74586.68) * mm, "end": v(36349.58, 74317.34) * mm});
            skLineSegment(sketch, "E1563", {"start": v(38260.66, 74882.87) * mm, "end": v(38568.06, 74882.87) * mm});
            skLineSegment(sketch, "E1564", {"start": v(38260.66, 74864.17) * mm, "end": v(38568.06, 74864.17) * mm});
            skLineSegment(sketch, "E1565", {"start": v(38568.06, 74882.87) * mm, "end": v(38568.06, 74864.17) * mm});
            skLineSegment(sketch, "E1566", {"start": v(38568.06, 74587.07) * mm, "end": v(38568.06, 74568.37) * mm});
            skLineSegment(sketch, "E1567", {"start": v(38568.06, 74587.07) * mm, "end": v(38260.66, 74587.07) * mm});
            skLineSegment(sketch, "E1568", {"start": v(38260.66, 74568.37) * mm, "end": v(38260.66, 74587.07) * mm});
            skLineSegment(sketch, "E1569", {"start": v(38260.66, 74864.17) * mm, "end": v(38260.66, 74882.87) * mm});
            skLineSegment(sketch, "E1570", {"start": v(38420.36, 74864.17) * mm, "end": v(38420.36, 74587.07) * mm});
            skLineSegment(sketch, "E1571", {"start": v(38408.36, 74864.17) * mm, "end": v(38408.36, 74587.07) * mm});
            skLineSegment(sketch, "E1572", {"start": v(40280.05, 75098.01) * mm, "end": v(40584.02, 75143.79) * mm});
            skLineSegment(sketch, "E1573", {"start": v(40282.83, 75079.52) * mm, "end": v(40586.8, 75125.3) * mm});
            skLineSegment(sketch, "E1574", {"start": v(40584.02, 75143.79) * mm, "end": v(40586.8, 75125.3) * mm});
            skLineSegment(sketch, "E1575", {"start": v(40628.07, 74851.29) * mm, "end": v(40630.85, 74832.8) * mm});
            skLineSegment(sketch, "E1576", {"start": v(40628.07, 74851.29) * mm, "end": v(40324.1, 74805.5) * mm});
            skLineSegment(sketch, "E1577", {"start": v(40326.88, 74787.02) * mm, "end": v(40324.1, 74805.5) * mm});
            skLineSegment(sketch, "E1578", {"start": v(40282.83, 75079.52) * mm, "end": v(40280.05, 75098.01) * mm});
            skLineSegment(sketch, "E1579", {"start": v(40440.75, 75103.3) * mm, "end": v(40482.02, 74829.3) * mm});
            skLineSegment(sketch, "E1580", {"start": v(40428.89, 75101.51) * mm, "end": v(40470.15, 74827.5) * mm});
            skLineSegment(sketch, "E1581", {"start": v(42190.92, 75315.95) * mm, "end": v(42496.6, 75348.5) * mm});
            skLineSegment(sketch, "E1582", {"start": v(42192.9, 75297.36) * mm, "end": v(42498.58, 75329.9) * mm});
            skLineSegment(sketch, "E1583", {"start": v(42496.6, 75348.5) * mm, "end": v(42498.58, 75329.9) * mm});
            skLineSegment(sketch, "E1584", {"start": v(42527.9, 75054.35) * mm, "end": v(42529.89, 75035.76) * mm});
            skLineSegment(sketch, "E1585", {"start": v(42527.9, 75054.35) * mm, "end": v(42222.24, 75021.82) * mm});
            skLineSegment(sketch, "E1586", {"start": v(42224.21, 75003.22) * mm, "end": v(42222.24, 75021.82) * mm});
            skLineSegment(sketch, "E1587", {"start": v(42192.9, 75297.36) * mm, "end": v(42190.92, 75315.95) * mm});
            skLineSegment(sketch, "E1588", {"start": v(42351.7, 75314.26) * mm, "end": v(42381.04, 75038.72) * mm});
            skLineSegment(sketch, "E1589", {"start": v(42339.77, 75313) * mm, "end": v(42369.1, 75037.45) * mm});
            skLineSegment(sketch, "E1590", {"start": v(44275.5, 75618.88) * mm, "end": v(44580.37, 75658.3) * mm});
            skLineSegment(sketch, "E1591", {"start": v(44277.9, 75600.34) * mm, "end": v(44582.77, 75639.76) * mm});
            skLineSegment(sketch, "E1592", {"start": v(44580.37, 75658.3) * mm, "end": v(44582.77, 75639.76) * mm});
            skLineSegment(sketch, "E1593", {"start": v(44618.3, 75364.94) * mm, "end": v(44620.7, 75346.4) * mm});
            skLineSegment(sketch, "E1594", {"start": v(44618.3, 75364.94) * mm, "end": v(44313.44, 75325.53) * mm});
            skLineSegment(sketch, "E1595", {"start": v(44315.83, 75306.98) * mm, "end": v(44313.44, 75325.53) * mm});
            skLineSegment(sketch, "E1596", {"start": v(44277.9, 75600.34) * mm, "end": v(44275.5, 75618.88) * mm});
            skLineSegment(sketch, "E1597", {"start": v(44436.28, 75620.82) * mm, "end": v(44471.82, 75346) * mm});
            skLineSegment(sketch, "E1598", {"start": v(44424.38, 75619.28) * mm, "end": v(44459.92, 75344.46) * mm});
            skLineSegment(sketch, "E1599", {"start": v(45935.18, 75763.44) * mm, "end": v(46242.02, 75781.88) * mm});
            skLineSegment(sketch, "E1600", {"start": v(45936.3, 75744.77) * mm, "end": v(46243.14, 75763.21) * mm});
            skLineSegment(sketch, "E1601", {"start": v(46242.02, 75781.88) * mm, "end": v(46243.14, 75763.21) * mm});
            skLineSegment(sketch, "E1602", {"start": v(46259.76, 75486.61) * mm, "end": v(46260.89, 75467.94) * mm});
            skLineSegment(sketch, "E1603", {"start": v(46259.76, 75486.61) * mm, "end": v(45952.92, 75468.17) * mm});
            skLineSegment(sketch, "E1604", {"start": v(45954.04, 75449.5) * mm, "end": v(45952.92, 75468.17) * mm});
            skLineSegment(sketch, "E1605", {"start": v(45936.3, 75744.77) * mm, "end": v(45935.18, 75763.44) * mm});
            skLineSegment(sketch, "E1606", {"start": v(46095.71, 75754.35) * mm, "end": v(46112.33, 75477.75) * mm});
            skLineSegment(sketch, "E1607", {"start": v(46083.73, 75753.63) * mm, "end": v(46100.35, 75477.03) * mm});
            skLineSegment(sketch, "E1608", {"start": v(48070.56, 76009.27) * mm, "end": v(48375.94, 76044.45) * mm});
            skLineSegment(sketch, "E1609", {"start": v(48072.7, 75990.69) * mm, "end": v(48378.08, 76025.87) * mm});
            skLineSegment(sketch, "E1610", {"start": v(48375.94, 76044.45) * mm, "end": v(48378.08, 76025.87) * mm});
            skLineSegment(sketch, "E1611", {"start": v(48409.8, 75750.6) * mm, "end": v(48411.94, 75732.02) * mm});
            skLineSegment(sketch, "E1612", {"start": v(48409.8, 75750.6) * mm, "end": v(48104.42, 75715.4) * mm});
            skLineSegment(sketch, "E1613", {"start": v(48106.56, 75696.83) * mm, "end": v(48104.42, 75715.4) * mm});
            skLineSegment(sketch, "E1614", {"start": v(48072.7, 75990.69) * mm, "end": v(48070.56, 76009.27) * mm});
            skLineSegment(sketch, "E1615", {"start": v(48231.35, 76008.97) * mm, "end": v(48263.07, 75733.69) * mm});
            skLineSegment(sketch, "E1616", {"start": v(48219.43, 76007.6) * mm, "end": v(48251.15, 75732.31) * mm});
            skLineSegment(sketch, "E1617", {"start": v(34452, 74244.23) * mm, "end": v(34440.05, 74245.4) * mm});
            skLineSegment(sketch, "E1618", {"start": v(36328.67, 74454.83) * mm, "end": v(36317, 74452) * mm});
            skLineSegment(sketch, "E1619", {"start": v(38420.36, 74725.62) * mm, "end": v(38408.36, 74725.62) * mm});
            skLineSegment(sketch, "E1620", {"start": v(40461.39, 74966.3) * mm, "end": v(40449.52, 74964.5) * mm});
            skLineSegment(sketch, "E1621", {"start": v(42366.37, 75176.5) * mm, "end": v(42354.44, 75175.22) * mm});
            skLineSegment(sketch, "E1622", {"start": v(44454.05, 75483.4) * mm, "end": v(44442.15, 75481.87) * mm});
            skLineSegment(sketch, "E1623", {"start": v(46104.02, 75616.05) * mm, "end": v(46092.04, 75615.33) * mm});
            skLineSegment(sketch, "E1624", {"start": v(48247.21, 75871.33) * mm, "end": v(48235.3, 75869.95) * mm});
            skCircle(sketch, "E1625", {"center": v(34446.02, 74244.82) * mm, "radius": 300 * mm});
            skCircle(sketch, "E1626", {"center": v(36322.84, 74453.42) * mm, "radius": 300 * mm});
            skCircle(sketch, "E1627", {"center": v(38414.36, 74725.62) * mm, "radius": 300 * mm});
            skCircle(sketch, "E1628", {"center": v(40455.45, 74965.4) * mm, "radius": 300 * mm});
            skCircle(sketch, "E1629", {"center": v(42360.4, 75175.86) * mm, "radius": 300 * mm});
            skCircle(sketch, "E1630", {"center": v(44448.1, 75482.64) * mm, "radius": 300 * mm});
            skCircle(sketch, "E1631", {"center": v(46098.03, 75615.7) * mm, "radius": 300 * mm});
            skCircle(sketch, "E1632", {"center": v(48241.25, 75870.64) * mm, "radius": 300 * mm});
            skLineSegment(sketch, "E1633", {"start": v(39297.3, 47569.74) * mm, "end": v(38737.79, 49416.4) * mm});
            skLineSegment(sketch, "E1634", {"start": v(41083.78, 50136.16) * mm, "end": v(41309.02, 49409.11) * mm});
            skLineSegment(sketch, "E1635", {"start": v(40436.26, 47922.69) * mm, "end": v(39911.47, 49671.67) * mm});
            skArc(sketch, "E1636", {"start": v(41083.78, 50136.16) * mm, "mid": v(39584.79, 50838.86) * mm, "end": v(38737.79, 49416.4) * mm});
            skLineSegment(sketch, "E1637", {"start": v(41645.2, 48288.73) * mm, "end": v(41309.02, 49409.11) * mm});
            skLineSegment(sketch, "E1638", {"start": v(40502.74, 47945.94) * mm, "end": v(39978.68, 49692.5) * mm});
            skLineSegment(sketch, "E1639", {"start": v(39911.47, 49671.67) * mm, "end": v(39978.68, 49692.5) * mm});
            skLineSegment(sketch, "E1640", {"start": v(41645.2, 48288.73) * mm, "end": v(40502.74, 47945.94) * mm});
            skLineSegment(sketch, "E1641", {"start": v(40436.26, 47922.69) * mm, "end": v(39297.3, 47569.74) * mm});
            skCircle(sketch, "E1642", {"center": v(34776.7, 58413.82) * mm, "radius": 328.69 * mm});
            skCircle(sketch, "E1643", {"center": v(35224.5, 57091.4) * mm, "radius": 323.11 * mm});
            skCircle(sketch, "E1644", {"center": v(35826.9, 55480) * mm, "radius": 308.82 * mm});
            skCircle(sketch, "E1645", {"center": v(36309.94, 53902.1) * mm, "radius": 312.62 * mm});
            skCircle(sketch, "E1646", {"center": v(36823.57, 52431.1) * mm, "radius": 314.17 * mm});
            skCircle(sketch, "E1647", {"center": v(37258.05, 50987.66) * mm, "radius": 280.53 * mm});
            skLineSegment(sketch, "E1648", {"start": v(33763.42, 59374.46) * mm, "end": v(34053.12, 58417.34) * mm});
            skLineSegment(sketch, "E1649", {"start": v(33718.13, 58315.95) * mm, "end": v(34053.12, 58417.34) * mm});
            skLineSegment(sketch, "E1650", {"start": v(33428.43, 59273.07) * mm, "end": v(33718.13, 58315.95) * mm});
            skLineSegment(sketch, "E1651", {"start": v(33428.43, 59273.07) * mm, "end": v(33763.42, 59374.46) * mm});
            skLineSegment(sketch, "E1652", {"start": v(33039.17, 61767.25) * mm, "end": v(33328.87, 60810.14) * mm});
            skLineSegment(sketch, "E1653", {"start": v(32993.88, 60708.74) * mm, "end": v(33328.87, 60810.14) * mm});
            skLineSegment(sketch, "E1654", {"start": v(32704.18, 61665.86) * mm, "end": v(32993.88, 60708.74) * mm});
            skLineSegment(sketch, "E1655", {"start": v(32704.18, 61665.86) * mm, "end": v(33039.17, 61767.25) * mm});
            skLineSegment(sketch, "E1656", {"start": v(32822.04, 66108.96) * mm, "end": v(37853.03, 49487.47) * mm});
            skLineSegment(sketch, "E1657", {"start": v(37565.9, 49400.56) * mm, "end": v(37853.03, 49487.47) * mm});
            skLineSegment(sketch, "E1658", {"start": v(32534.9, 66022.05) * mm, "end": v(37565.9, 49400.56) * mm});
            skLineSegment(sketch, "E1659", {"start": v(32534.9, 66022.05) * mm, "end": v(32822.04, 66108.96) * mm});
            skLineSegment(sketch, "E1660", {"start": v(37042.19, 48197.24) * mm, "end": v(40019.76, 49098.5) * mm});
            skLineSegment(sketch, "E1661", {"start": v(40092.18, 48859.21) * mm, "end": v(40019.76, 49098.5) * mm});
            skLineSegment(sketch, "E1662", {"start": v(37114.61, 47957.96) * mm, "end": v(40092.18, 48859.21) * mm});
            skLineSegment(sketch, "E1663", {"start": v(37114.61, 47957.96) * mm, "end": v(37042.19, 48197.24) * mm});
            skLineSegment(sketch, "E1664", {"start": v(40977.23, 49387.02) * mm, "end": v(41455.68, 49531.83) * mm});
            skLineSegment(sketch, "E1665", {"start": v(41528.1, 49292.55) * mm, "end": v(41455.68, 49531.83) * mm});
            skLineSegment(sketch, "E1666", {"start": v(41049.66, 49147.74) * mm, "end": v(41528.1, 49292.55) * mm});
            skLineSegment(sketch, "E1667", {"start": v(41049.66, 49147.74) * mm, "end": v(40977.23, 49387.02) * mm});
            skLineSegment(sketch, "E1668", {"start": v(40827.42, 52349.63) * mm, "end": v(40943.3, 51966.79) * mm});
            skLineSegment(sketch, "E1669", {"start": v(40656.17, 51879.88) * mm, "end": v(40943.3, 51966.79) * mm});
            skLineSegment(sketch, "E1670", {"start": v(40540.29, 52262.72) * mm, "end": v(40656.17, 51879.88) * mm});
            skLineSegment(sketch, "E1671", {"start": v(40540.29, 52262.72) * mm, "end": v(40827.42, 52349.63) * mm});
            skLineSegment(sketch, "E1672", {"start": v(39619.37, 56340.84) * mm, "end": v(39706.28, 56053.7) * mm});
            skLineSegment(sketch, "E1673", {"start": v(39419.14, 55966.8) * mm, "end": v(39706.28, 56053.7) * mm});
            skLineSegment(sketch, "E1674", {"start": v(39332.23, 56253.93) * mm, "end": v(39419.14, 55966.8) * mm});
            skLineSegment(sketch, "E1675", {"start": v(39332.23, 56253.93) * mm, "end": v(39619.37, 56340.84) * mm});
            skLineSegment(sketch, "E1676", {"start": v(32934, 61079.59) * mm, "end": v(32861.58, 61318.87) * mm});
            skLineSegment(sketch, "E1677", {"start": v(33100.86, 61391.3) * mm, "end": v(32861.58, 61318.87) * mm});
            skLineSegment(sketch, "E1678", {"start": v(33173.28, 61152.01) * mm, "end": v(33100.86, 61391.3) * mm});
            skLineSegment(sketch, "E1679", {"start": v(33173.28, 61152.01) * mm, "end": v(32934, 61079.59) * mm});
            skLineSegment(sketch, "E1680", {"start": v(33643.26, 58736.34) * mm, "end": v(33570.83, 58975.62) * mm});
            skLineSegment(sketch, "E1681", {"start": v(33810.11, 59048.05) * mm, "end": v(33570.83, 58975.62) * mm});
            skLineSegment(sketch, "E1682", {"start": v(33882.54, 58808.77) * mm, "end": v(33810.11, 59048.05) * mm});
            skLineSegment(sketch, "E1683", {"start": v(33882.54, 58808.77) * mm, "end": v(33643.26, 58736.34) * mm});
            skLineSegment(sketch, "E1684", {"start": v(50830.55, 75928.5) * mm, "end": v(53498.03, 76270.68) * mm});
            skLineSegment(sketch, "E1685", {"start": v(50970.51, 74837.43) * mm, "end": v(52899.7, 75084.91) * mm});
            skLineSegment(sketch, "E1686", {"start": v(50830.55, 75928.5) * mm, "end": v(50830.55, 75928.49) * mm});
            skLineSegment(sketch, "E1687", {"start": v(50881.45, 75531.74) * mm, "end": v(50970.51, 74837.43) * mm});
            skLineSegment(sketch, "E1688", {"start": v(31976.13, 69145.44) * mm, "end": v(32786.56, 66468.52) * mm});
            skLineSegment(sketch, "E1689", {"start": v(32499.43, 66381.6) * mm, "end": v(32786.56, 66468.52) * mm});
            skLineSegment(sketch, "E1690", {"start": v(31689, 69058.52) * mm, "end": v(32499.43, 66381.6) * mm});
            skLineSegment(sketch, "E1691", {"start": v(31689, 69058.52) * mm, "end": v(31976.13, 69145.44) * mm});
            skLineSegment(sketch, "E1692", {"start": v(53075.2, 75510.7) * mm, "end": v(67524.4, 49593.2) * mm});
            skLineSegment(sketch, "E1693", {"start": v(52857.63, 75079.5) * mm, "end": v(66870.92, 49943.92) * mm});
            skLineSegment(sketch, "E1694", {"start": v(54593.2, 46227.65) * mm, "end": v(54897.38, 45222.68) * mm});
            skLineSegment(sketch, "E1695", {"start": v(53844.55, 44904) * mm, "end": v(54897.38, 45222.68) * mm});
            skLineSegment(sketch, "E1696", {"start": v(53540.37, 45908.98) * mm, "end": v(53844.55, 44904) * mm});
            skLineSegment(sketch, "E1697", {"start": v(54593.2, 46227.65) * mm, "end": v(53923.21, 46024.86) * mm});
            skLineSegment(sketch, "E1698", {"start": v(53029.98, 51392.22) * mm, "end": v(53342.86, 50358.54) * mm});
            skLineSegment(sketch, "E1699", {"start": v(51977.15, 51073.55) * mm, "end": v(52290.03, 50039.87) * mm});
            skLineSegment(sketch, "E1700", {"start": v(53029.98, 51392.22) * mm, "end": v(52360, 51189.43) * mm});
            skLineSegment(sketch, "E1701", {"start": v(53342.86, 50358.54) * mm, "end": v(52672.88, 50155.75) * mm});
            skLineSegment(sketch, "E1702", {"start": v(50830.55, 75928.5) * mm, "end": v(52332.62, 76121.18) * mm});
            skLineSegment(sketch, "E1703", {"start": v(50970.51, 74837.43) * mm, "end": v(52472.58, 75030.12) * mm});
            skLineSegment(sketch, "E1704", {"start": v(32537.66, 73581.95) * mm, "end": v(35287.76, 73934.73) * mm});
            skLineSegment(sketch, "E1705", {"start": v(32677.62, 72490.9) * mm, "end": v(35427.72, 72843.67) * mm});
            skLineSegment(sketch, "E1706", {"start": v(32537.66, 73581.95) * mm, "end": v(32626.73, 72887.64) * mm});
            skLineSegment(sketch, "E1707", {"start": v(35287.76, 73934.73) * mm, "end": v(35287.77, 73934.65) * mm});
            skLineSegment(sketch, "E1708", {"start": v(35338.66, 73537.9) * mm, "end": v(35427.72, 72843.67) * mm});
            skLineSegment(sketch, "E1709", {"start": v(43048.65, 74930.3) * mm, "end": v(44040.52, 75057.54) * mm});
            skLineSegment(sketch, "E1710", {"start": v(43188.61, 73839.24) * mm, "end": v(44180.48, 73966.48) * mm});
            skLineSegment(sketch, "E1711", {"start": v(43048.65, 74930.3) * mm, "end": v(43048.66, 74930.22) * mm});
            skLineSegment(sketch, "E1712", {"start": v(43099.56, 74533.48) * mm, "end": v(43188.61, 73839.24) * mm});
            skLineSegment(sketch, "E1713", {"start": v(44040.52, 75057.54) * mm, "end": v(44040.53, 75057.46) * mm});
            skLineSegment(sketch, "E1714", {"start": v(44091.43, 74660.71) * mm, "end": v(44180.48, 73966.48) * mm});
            skLineSegment(sketch, "E1715", {"start": v(39254.74, 74443.62) * mm, "end": v(40246.6, 74570.86) * mm});
            skLineSegment(sketch, "E1716", {"start": v(39394.7, 73352.56) * mm, "end": v(40386.57, 73479.8) * mm});
            skLineSegment(sketch, "E1717", {"start": v(39254.74, 74443.62) * mm, "end": v(39254.75, 74443.54) * mm});
            skLineSegment(sketch, "E1718", {"start": v(39305.64, 74046.8) * mm, "end": v(39394.7, 73352.56) * mm});
            skLineSegment(sketch, "E1719", {"start": v(40246.6, 74570.86) * mm, "end": v(40246.62, 74570.78) * mm});
            skLineSegment(sketch, "E1720", {"start": v(40297.51, 74174.03) * mm, "end": v(40386.57, 73479.8) * mm});
            skLineSegment(sketch, "E1721", {"start": v(32677.62, 72490.9) * mm, "end": v(31027.6, 72279.22) * mm});
            skLineSegment(sketch, "E1722", {"start": v(32626.73, 72887.64) * mm, "end": v(30437.4, 72606.8) * mm});
            skLineSegment(sketch, "E1723", {"start": v(54593.15, 46227.69) * mm, "end": v(66870.92, 49943.92) * mm});
            skLineSegment(sketch, "E1724", {"start": v(54745.24, 45725.2) * mm, "end": v(67524.4, 49593.2) * mm});
            skLineSegment(sketch, "E1725", {"start": v(39254.75, 74443.54) * mm, "end": v(35287.77, 73934.65) * mm});
            skLineSegment(sketch, "E1726", {"start": v(40246.62, 74570.78) * mm, "end": v(43048.66, 74930.22) * mm});
            skLineSegment(sketch, "E1727", {"start": v(40297.51, 74174.03) * mm, "end": v(43099.56, 74533.48) * mm});
            skLineSegment(sketch, "E1728", {"start": v(44040.53, 75057.46) * mm, "end": v(46890.05, 75423) * mm});
            skLineSegment(sketch, "E1729", {"start": v(44091.43, 74660.71) * mm, "end": v(46940.94, 75026.25) * mm});
            skLineSegment(sketch, "E1730", {"start": v(46890.05, 75423) * mm, "end": v(46890.06, 75422.87) * mm});
            skLineSegment(sketch, "E1731", {"start": v(46890.06, 75422.87) * mm, "end": v(47881.94, 75550.1) * mm});
            skLineSegment(sketch, "E1732", {"start": v(47030.03, 74331.8) * mm, "end": v(48021.9, 74459.04) * mm});
            skLineSegment(sketch, "E1733", {"start": v(46940.94, 75026.25) * mm, "end": v(47030.03, 74331.8) * mm});
            skLineSegment(sketch, "E1734", {"start": v(47932.81, 75153.49) * mm, "end": v(48021.9, 74459.04) * mm});
            skLineSegment(sketch, "E1735", {"start": v(50881.45, 75531.74) * mm, "end": v(47932.81, 75153.49) * mm});
            skLineSegment(sketch, "E1736", {"start": v(50830.55, 75928.49) * mm, "end": v(47881.92, 75550.24) * mm});
            skLineSegment(sketch, "E1737", {"start": v(47881.94, 75550.1) * mm, "end": v(47881.92, 75550.24) * mm});
            skLineSegment(sketch, "E1738", {"start": v(31027.6, 72279.22) * mm, "end": v(31976.12, 69145.48) * mm});
            skLineSegment(sketch, "E1739", {"start": v(30437.4, 72606.8) * mm, "end": v(31287.27, 69798.94) * mm});
            skLineSegment(sketch, "E1740", {"start": v(30569.4, 69581.66) * mm, "end": v(31287.27, 69798.94) * mm});
            skLineSegment(sketch, "E1741", {"start": v(30808.4, 68792.03) * mm, "end": v(31976.12, 69145.48) * mm});
            skLineSegment(sketch, "E1742", {"start": v(30569.4, 69581.66) * mm, "end": v(30692.52, 69174.88) * mm});
            skLineSegment(sketch, "E1743", {"start": v(50425.27, 56200.7) * mm, "end": v(51977.15, 51073.55) * mm});
            skLineSegment(sketch, "E1744", {"start": v(52672.88, 50155.75) * mm, "end": v(53923.21, 46024.86) * mm});
            skLineSegment(sketch, "E1745", {"start": v(52290.03, 50039.87) * mm, "end": v(53540.37, 45908.98) * mm});
            skLineSegment(sketch, "E1746", {"start": v(30692.52, 69174.88) * mm, "end": v(30692.53, 69174.88) * mm});
            skLineSegment(sketch, "E1747", {"start": v(30429.3, 69095.21) * mm, "end": v(30692.52, 69174.88) * mm});
            skLineSegment(sketch, "E1748", {"start": v(30545.18, 68712.37) * mm, "end": v(30808.4, 68792.03) * mm});
            skLineSegment(sketch, "E1749", {"start": v(30545.18, 68712.37) * mm, "end": v(30429.3, 69095.21) * mm});
            skLineSegment(sketch, "E1750", {"start": v(30569.4, 69581.66) * mm, "end": v(31737.14, 69935.1) * mm});
            skLineSegment(sketch, "E1751", {"start": v(30808.4, 68792.03) * mm, "end": v(31976.14, 69145.49) * mm});
            skLineSegment(sketch, "E1752", {"start": v(52421.69, 75426.86) * mm, "end": v(53075.2, 75510.7) * mm});
            skLineSegment(sketch, "E1753", {"start": v(52472.58, 75030.12) * mm, "end": v(52857.63, 75079.5) * mm});
            skLineSegment(sketch, "E1754", {"start": v(52332.6, 76121.17) * mm, "end": v(52332.62, 76121.17) * mm});
            skLineSegment(sketch, "E1755", {"start": v(52472.56, 75030.11) * mm, "end": v(52472.58, 75030.12) * mm});
            skLineSegment(sketch, "E1756", {"start": v(52332.62, 76121.17) * mm, "end": v(52421.69, 75426.86) * mm});
            skLineSegment(sketch, "E1757", {"start": v(50997.37, 57417.12) * mm, "end": v(51286.64, 56461.42) * mm});
            skLineSegment(sketch, "E1758", {"start": v(50135.97, 57156.4) * mm, "end": v(50425.24, 56200.7) * mm});
            skLineSegment(sketch, "E1759", {"start": v(50997.37, 57417.12) * mm, "end": v(50643.24, 57309.93) * mm});
            skLineSegment(sketch, "E1760", {"start": v(51286.64, 56461.42) * mm, "end": v(50808.12, 56316.58) * mm});
            skLineSegment(sketch, "E1761", {"start": v(50425.27, 56200.7) * mm, "end": v(50425.24, 56200.7) * mm});
            skLineSegment(sketch, "E1762", {"start": v(57239.17, 51925.82) * mm, "end": v(54176.2, 50998.75) * mm});
            skLineSegment(sketch, "E1763", {"start": v(55604.89, 57867.13) * mm, "end": v(57345.71, 52125.24) * mm});
            skLineSegment(sketch, "E1764", {"start": v(52345.35, 57047.72) * mm, "end": v(55408.08, 57974.72) * mm});
            skLineSegment(sketch, "E1765", {"start": v(53976.63, 51105.79) * mm, "end": v(52238.56, 56848.23) * mm});
            skLineSegment(sketch, "E1766", {"start": v(52391.7, 56894.58) * mm, "end": v(54129.84, 51151.89) * mm});
            skLineSegment(sketch, "E1767", {"start": v(55454.43, 57821.58) * mm, "end": v(52391.7, 56894.58) * mm});
            skLineSegment(sketch, "E1768", {"start": v(57192.58, 52078.89) * mm, "end": v(55454.43, 57821.58) * mm});
            skLineSegment(sketch, "E1769", {"start": v(54129.84, 51151.89) * mm, "end": v(57192.58, 52078.89) * mm});
            skLineSegment(sketch, "E1770", {"start": v(54176.2, 50998.75) * mm, "end": v(54023.05, 50952.4) * mm});
            skLineSegment(sketch, "E1771", {"start": v(54023.05, 50952.4) * mm, "end": v(54020.55, 50960.69) * mm});
            skLineSegment(sketch, "E1772", {"start": v(54020.55, 50960.69) * mm, "end": v(54086.56, 50980.7) * mm});
            skArc(sketch, "E1773", {"start": v(54086.56, 50980.7) * mm, "mid": v(54091.32, 50984.6) * mm, "end": v(54091.92, 50990.7) * mm});
            skLineSegment(sketch, "E1774", {"start": v(54091.92, 50990.7) * mm, "end": v(54055.4, 51111.92) * mm});
            skArc(sketch, "E1775", {"start": v(54055.4, 51111.92) * mm, "mid": v(54051.1, 51116.56) * mm, "end": v(54044.8, 51117.1) * mm});
            skLineSegment(sketch, "E1776", {"start": v(54044.8, 51117.1) * mm, "end": v(53979.21, 51097.25) * mm});
            skLineSegment(sketch, "E1777", {"start": v(53979.21, 51097.25) * mm, "end": v(53976.7, 51105.54) * mm});
            skLineSegment(sketch, "E1778", {"start": v(53976.7, 51105.54) * mm, "end": v(54129.84, 51151.89) * mm});
            skLineSegment(sketch, "E1779", {"start": v(54129.84, 51151.89) * mm, "end": v(54132.35, 51143.6) * mm});
            skLineSegment(sketch, "E1780", {"start": v(54132.35, 51143.6) * mm, "end": v(54066.16, 51123.56) * mm});
            skArc(sketch, "E1781", {"start": v(54066.16, 51123.56) * mm, "mid": v(54061.44, 51119.65) * mm, "end": v(54060.82, 51113.56) * mm});
            skLineSegment(sketch, "E1782", {"start": v(54060.82, 51113.56) * mm, "end": v(54097.35, 50992.34) * mm});
            skArc(sketch, "E1783", {"start": v(54097.35, 50992.34) * mm, "mid": v(54101.31, 50987.56) * mm, "end": v(54107.5, 50987) * mm});
            skLineSegment(sketch, "E1784", {"start": v(54107.5, 50987) * mm, "end": v(54173.68, 51007.04) * mm});
            skLineSegment(sketch, "E1785", {"start": v(54173.68, 51007.04) * mm, "end": v(54176.2, 50998.75) * mm});
            skLineSegment(sketch, "E1786", {"start": v(57392.07, 51972.1) * mm, "end": v(57238.93, 51925.75) * mm});
            skLineSegment(sketch, "E1787", {"start": v(57238.93, 51925.75) * mm, "end": v(57236.42, 51934.04) * mm});
            skLineSegment(sketch, "E1788", {"start": v(57236.42, 51934.04) * mm, "end": v(57302.44, 51954.06) * mm});
            skArc(sketch, "E1789", {"start": v(57302.44, 51954.06) * mm, "mid": v(57307.19, 51957.94) * mm, "end": v(57307.8, 51964.05) * mm});
            skLineSegment(sketch, "E1790", {"start": v(57307.8, 51964.05) * mm, "end": v(57271.27, 52085.27) * mm});
            skArc(sketch, "E1791", {"start": v(57271.27, 52085.27) * mm, "mid": v(57266.98, 52089.9) * mm, "end": v(57260.68, 52090.45) * mm});
            skLineSegment(sketch, "E1792", {"start": v(57260.68, 52090.45) * mm, "end": v(57195.08, 52070.6) * mm});
            skLineSegment(sketch, "E1793", {"start": v(57195.08, 52070.6) * mm, "end": v(57192.58, 52078.89) * mm});
            skLineSegment(sketch, "E1794", {"start": v(57192.58, 52078.89) * mm, "end": v(57345.71, 52125.24) * mm});
            skLineSegment(sketch, "E1795", {"start": v(57345.71, 52125.24) * mm, "end": v(57348.22, 52116.95) * mm});
            skLineSegment(sketch, "E1796", {"start": v(57348.22, 52116.95) * mm, "end": v(57282.03, 52096.92) * mm});
            skArc(sketch, "E1797", {"start": v(57282.03, 52096.92) * mm, "mid": v(57277.31, 52093) * mm, "end": v(57276.69, 52086.9) * mm});
            skLineSegment(sketch, "E1798", {"start": v(57276.69, 52086.9) * mm, "end": v(57313.22, 51965.7) * mm});
            skArc(sketch, "E1799", {"start": v(57313.22, 51965.7) * mm, "mid": v(57317.18, 51960.91) * mm, "end": v(57323.37, 51960.36) * mm});
            skLineSegment(sketch, "E1800", {"start": v(57323.37, 51960.36) * mm, "end": v(57389.56, 51980.4) * mm});
            skLineSegment(sketch, "E1801", {"start": v(57389.56, 51980.4) * mm, "end": v(57392.07, 51972.1) * mm});
            skLineSegment(sketch, "E1802", {"start": v(55607.57, 57867.94) * mm, "end": v(55454.43, 57821.58) * mm});
            skLineSegment(sketch, "E1803", {"start": v(55454.43, 57821.58) * mm, "end": v(55451.92, 57829.87) * mm});
            skLineSegment(sketch, "E1804", {"start": v(55451.92, 57829.87) * mm, "end": v(55517.94, 57849.9) * mm});
            skArc(sketch, "E1805", {"start": v(55517.94, 57849.9) * mm, "mid": v(55522.7, 57853.78) * mm, "end": v(55523.3, 57859.89) * mm});
            skLineSegment(sketch, "E1806", {"start": v(55523.3, 57859.89) * mm, "end": v(55486.78, 57981.1) * mm});
            skArc(sketch, "E1807", {"start": v(55486.78, 57981.1) * mm, "mid": v(55482.48, 57985.74) * mm, "end": v(55476.18, 57986.29) * mm});
            skLineSegment(sketch, "E1808", {"start": v(55476.18, 57986.29) * mm, "end": v(55410.59, 57966.43) * mm});
            skLineSegment(sketch, "E1809", {"start": v(55410.59, 57966.43) * mm, "end": v(55408.08, 57974.72) * mm});
            skLineSegment(sketch, "E1810", {"start": v(55408.08, 57974.72) * mm, "end": v(55561.22, 58021.08) * mm});
            skLineSegment(sketch, "E1811", {"start": v(55561.22, 58021.08) * mm, "end": v(55563.73, 58012.79) * mm});
            skLineSegment(sketch, "E1812", {"start": v(55563.73, 58012.79) * mm, "end": v(55497.54, 57992.75) * mm});
            skArc(sketch, "E1813", {"start": v(55497.54, 57992.75) * mm, "mid": v(55492.82, 57988.84) * mm, "end": v(55492.2, 57982.74) * mm});
            skLineSegment(sketch, "E1814", {"start": v(55492.2, 57982.74) * mm, "end": v(55528.73, 57861.53) * mm});
            skArc(sketch, "E1815", {"start": v(55528.73, 57861.53) * mm, "mid": v(55532.69, 57856.75) * mm, "end": v(55538.87, 57856.2) * mm});
            skLineSegment(sketch, "E1816", {"start": v(55538.87, 57856.2) * mm, "end": v(55605.06, 57876.23) * mm});
            skLineSegment(sketch, "E1817", {"start": v(55605.06, 57876.23) * mm, "end": v(55607.57, 57867.94) * mm});
            skLineSegment(sketch, "E1818", {"start": v(52391.7, 56894.58) * mm, "end": v(52238.56, 56848.23) * mm});
            skLineSegment(sketch, "E1819", {"start": v(52238.56, 56848.23) * mm, "end": v(52236.05, 56856.52) * mm});
            skLineSegment(sketch, "E1820", {"start": v(52236.05, 56856.52) * mm, "end": v(52302.07, 56876.54) * mm});
            skArc(sketch, "E1821", {"start": v(52302.07, 56876.54) * mm, "mid": v(52306.82, 56880.43) * mm, "end": v(52307.43, 56886.53) * mm});
            skLineSegment(sketch, "E1822", {"start": v(52307.43, 56886.53) * mm, "end": v(52270.9, 57007.75) * mm});
            skArc(sketch, "E1823", {"start": v(52270.9, 57007.75) * mm, "mid": v(52266.6, 57012.4) * mm, "end": v(52260.3, 57012.93) * mm});
            skLineSegment(sketch, "E1824", {"start": v(52260.3, 57012.93) * mm, "end": v(52194.72, 56993.08) * mm});
            skLineSegment(sketch, "E1825", {"start": v(52194.72, 56993.08) * mm, "end": v(52192.2, 57001.37) * mm});
            skLineSegment(sketch, "E1826", {"start": v(52192.2, 57001.37) * mm, "end": v(52345.35, 57047.72) * mm});
            skLineSegment(sketch, "E1827", {"start": v(52345.35, 57047.72) * mm, "end": v(52347.86, 57039.43) * mm});
            skLineSegment(sketch, "E1828", {"start": v(52347.86, 57039.43) * mm, "end": v(52281.67, 57019.4) * mm});
            skArc(sketch, "E1829", {"start": v(52281.67, 57019.4) * mm, "mid": v(52276.94, 57015.49) * mm, "end": v(52276.32, 57009.39) * mm});
            skLineSegment(sketch, "E1830", {"start": v(52276.32, 57009.39) * mm, "end": v(52312.86, 56888.17) * mm});
            skArc(sketch, "E1831", {"start": v(52312.86, 56888.17) * mm, "mid": v(52316.82, 56883.4) * mm, "end": v(52323, 56882.84) * mm});
            skLineSegment(sketch, "E1832", {"start": v(52323, 56882.84) * mm, "end": v(52389.19, 56902.87) * mm});
            skLineSegment(sketch, "E1833", {"start": v(52389.19, 56902.87) * mm, "end": v(52391.7, 56894.58) * mm});
            skLineSegment(sketch, "E1834", {"start": v(55694.63, 56724.4) * mm, "end": v(55675.8, 56786.62) * mm});
            skLineSegment(sketch, "E1835", {"start": v(55675.8, 56786.62) * mm, "end": v(55672.2, 56785.53) * mm});
            skArc(sketch, "E1836", {"start": v(55672.2, 56785.53) * mm, "mid": v(55669.63, 56783.5) * mm, "end": v(55669.12, 56780.27) * mm});
            skLineSegment(sketch, "E1837", {"start": v(55669.12, 56780.27) * mm, "end": v(55678.43, 56737.44) * mm});
            skArc(sketch, "E1838", {"start": v(55671.21, 56725.15) * mm, "mid": v(55677.22, 56729.88) * mm, "end": v(55678.43, 56737.44) * mm});
            skLineSegment(sketch, "E1839", {"start": v(55671.21, 56725.15) * mm, "end": v(55560.55, 56691.66) * mm});
            skArc(sketch, "E1840", {"start": v(55547.74, 56697.88) * mm, "mid": v(55552.93, 56692.26) * mm, "end": v(55560.55, 56691.66) * mm});
            skLineSegment(sketch, "E1841", {"start": v(55547.74, 56697.88) * mm, "end": v(55531.74, 56738.69) * mm});
            skArc(sketch, "E1842", {"start": v(55531.74, 56738.69) * mm, "mid": v(55529.51, 56741.1) * mm, "end": v(55526.24, 56741.35) * mm});
            skLineSegment(sketch, "E1843", {"start": v(55526.24, 56741.35) * mm, "end": v(55522.66, 56740.27) * mm});
            skLineSegment(sketch, "E1844", {"start": v(55522.66, 56740.27) * mm, "end": v(55541.49, 56678.05) * mm});
            skLineSegment(sketch, "E1845", {"start": v(55541.49, 56678.05) * mm, "end": v(55694.63, 56724.4) * mm});
            skLineSegment(sketch, "E1846", {"start": v(55616.8, 56429.2) * mm, "end": v(55635.64, 56366.99) * mm});
            skLineSegment(sketch, "E1847", {"start": v(55635.64, 56366.99) * mm, "end": v(55639.22, 56368.08) * mm});
            skArc(sketch, "E1848", {"start": v(55639.22, 56368.08) * mm, "mid": v(55641.8, 56370.1) * mm, "end": v(55642.32, 56373.34) * mm});
            skLineSegment(sketch, "E1849", {"start": v(55642.32, 56373.34) * mm, "end": v(55633, 56416.17) * mm});
            skArc(sketch, "E1850", {"start": v(55640.22, 56428.45) * mm, "mid": v(55634.2, 56423.72) * mm, "end": v(55633, 56416.17) * mm});
            skLineSegment(sketch, "E1851", {"start": v(55640.22, 56428.45) * mm, "end": v(55750.88, 56461.95) * mm});
            skArc(sketch, "E1852", {"start": v(55763.7, 56455.73) * mm, "mid": v(55758.5, 56461.34) * mm, "end": v(55750.88, 56461.95) * mm});
            skLineSegment(sketch, "E1853", {"start": v(55763.7, 56455.73) * mm, "end": v(55779.7, 56414.92) * mm});
            skArc(sketch, "E1854", {"start": v(55779.7, 56414.92) * mm, "mid": v(55781.92, 56412.51) * mm, "end": v(55785.19, 56412.26) * mm});
            skLineSegment(sketch, "E1855", {"start": v(55785.19, 56412.26) * mm, "end": v(55788.78, 56413.34) * mm});
            skLineSegment(sketch, "E1856", {"start": v(55788.78, 56413.34) * mm, "end": v(55769.95, 56475.55) * mm});
            skLineSegment(sketch, "E1857", {"start": v(55769.95, 56475.55) * mm, "end": v(55616.8, 56429.2) * mm});
            skCircle(sketch, "E1858", {"center": v(55655.72, 56576.8) * mm, "radius": 0.25 * mm});
            skCircle(sketch, "E1859", {"center": v(55655.72, 56576.8) * mm, "radius": 57.5 * mm});
            skCircle(sketch, "E1860", {"center": v(55655.72, 56576.8) * mm, "radius": 59.5 * mm});
            skCircle(sketch, "E1861", {"center": v(55655.72, 56576.8) * mm, "radius": 63.5 * mm});
            skLineSegment(sketch, "E1862", {"start": v(55607.5, 56356.38) * mm, "end": v(55636.22, 56365.08) * mm});
            skLineSegment(sketch, "E1863", {"start": v(55636.22, 56365.08) * mm, "end": v(55621.73, 56412.93) * mm});
            skLineSegment(sketch, "E1864", {"start": v(55621.73, 56412.93) * mm, "end": v(55593.02, 56404.24) * mm});
            skLineSegment(sketch, "E1865", {"start": v(55593.02, 56404.24) * mm, "end": v(55607.5, 56356.38) * mm});
            skLineSegment(sketch, "E1866", {"start": v(55636.22, 56365.08) * mm, "end": v(55635.64, 56366.99) * mm});
            skLineSegment(sketch, "E1867", {"start": v(55635.64, 56366.99) * mm, "end": v(55621.73, 56412.93) * mm});
            skLineSegment(sketch, "E1868", {"start": v(52875.62, 55599.52) * mm, "end": v(52894.45, 55537.3) * mm});
            skLineSegment(sketch, "E1869", {"start": v(52894.45, 55537.3) * mm, "end": v(52898.03, 55538.4) * mm});
            skArc(sketch, "E1870", {"start": v(52898.03, 55538.4) * mm, "mid": v(52900.6, 55540.42) * mm, "end": v(52901.13, 55543.66) * mm});
            skLineSegment(sketch, "E1871", {"start": v(52901.13, 55543.66) * mm, "end": v(52891.81, 55586.5) * mm});
            skArc(sketch, "E1872", {"start": v(52899.03, 55598.77) * mm, "mid": v(52893.02, 55594.04) * mm, "end": v(52891.81, 55586.5) * mm});
            skLineSegment(sketch, "E1873", {"start": v(52899.03, 55598.77) * mm, "end": v(53009.69, 55632.26) * mm});
            skArc(sketch, "E1874", {"start": v(53022.5, 55626.05) * mm, "mid": v(53017.31, 55631.66) * mm, "end": v(53009.69, 55632.26) * mm});
            skLineSegment(sketch, "E1875", {"start": v(53022.5, 55626.05) * mm, "end": v(53038.5, 55585.24) * mm});
            skArc(sketch, "E1876", {"start": v(53038.5, 55585.24) * mm, "mid": v(53040.73, 55582.83) * mm, "end": v(53044, 55582.57) * mm});
            skLineSegment(sketch, "E1877", {"start": v(53044, 55582.57) * mm, "end": v(53047.59, 55583.66) * mm});
            skLineSegment(sketch, "E1878", {"start": v(53047.59, 55583.66) * mm, "end": v(53028.76, 55645.87) * mm});
            skLineSegment(sketch, "E1879", {"start": v(53028.76, 55645.87) * mm, "end": v(52875.62, 55599.52) * mm});
            skLineSegment(sketch, "E1880", {"start": v(52953.44, 55894.72) * mm, "end": v(52934.6, 55956.94) * mm});
            skLineSegment(sketch, "E1881", {"start": v(52934.6, 55956.94) * mm, "end": v(52931.02, 55955.85) * mm});
            skArc(sketch, "E1882", {"start": v(52931.02, 55955.85) * mm, "mid": v(52928.44, 55953.82) * mm, "end": v(52927.92, 55950.59) * mm});
            skLineSegment(sketch, "E1883", {"start": v(52927.92, 55950.59) * mm, "end": v(52937.24, 55907.75) * mm});
            skArc(sketch, "E1884", {"start": v(52930.02, 55895.47) * mm, "mid": v(52936.03, 55900.2) * mm, "end": v(52937.24, 55907.75) * mm});
            skLineSegment(sketch, "E1885", {"start": v(52930.02, 55895.47) * mm, "end": v(52819.36, 55861.98) * mm});
            skArc(sketch, "E1886", {"start": v(52806.55, 55868.2) * mm, "mid": v(52811.74, 55862.58) * mm, "end": v(52819.36, 55861.98) * mm});
            skLineSegment(sketch, "E1887", {"start": v(52806.55, 55868.2) * mm, "end": v(52790.55, 55909) * mm});
            skArc(sketch, "E1888", {"start": v(52790.55, 55909) * mm, "mid": v(52788.32, 55911.41) * mm, "end": v(52785.05, 55911.67) * mm});
            skLineSegment(sketch, "E1889", {"start": v(52785.05, 55911.67) * mm, "end": v(52781.47, 55910.59) * mm});
            skLineSegment(sketch, "E1890", {"start": v(52781.47, 55910.59) * mm, "end": v(52800.3, 55848.37) * mm});
            skLineSegment(sketch, "E1891", {"start": v(52800.3, 55848.37) * mm, "end": v(52953.44, 55894.72) * mm});
            skCircle(sketch, "E1892", {"center": v(52914.53, 55747.12) * mm, "radius": 0.25 * mm});
            skCircle(sketch, "E1893", {"center": v(52914.53, 55747.12) * mm, "radius": 57.5 * mm});
            skCircle(sketch, "E1894", {"center": v(52914.53, 55747.12) * mm, "radius": 59.5 * mm});
            skCircle(sketch, "E1895", {"center": v(52914.53, 55747.12) * mm, "radius": 63.5 * mm});
            skLineSegment(sketch, "E1896", {"start": v(53045.04, 55592.08) * mm, "end": v(53073.75, 55600.77) * mm});
            skLineSegment(sketch, "E1897", {"start": v(53073.75, 55600.77) * mm, "end": v(53062.4, 55638.3) * mm});
            skLineSegment(sketch, "E1898", {"start": v(53062.4, 55638.3) * mm, "end": v(53033.68, 55629.6) * mm});
            skLineSegment(sketch, "E1899", {"start": v(53033.68, 55629.6) * mm, "end": v(53045.04, 55592.08) * mm});
            skLineSegment(sketch, "E1900", {"start": v(53076.88, 55590.44) * mm, "end": v(53073.75, 55600.77) * mm});
            skLineSegment(sketch, "E1901", {"start": v(53048.16, 55581.75) * mm, "end": v(53076.88, 55590.44) * mm});
            skLineSegment(sketch, "E1902", {"start": v(53048.16, 55581.75) * mm, "end": v(53047.59, 55583.66) * mm});
            skLineSegment(sketch, "E1903", {"start": v(53889.54, 52249.6) * mm, "end": v(53908.37, 52187.4) * mm});
            skLineSegment(sketch, "E1904", {"start": v(53908.37, 52187.4) * mm, "end": v(53911.96, 52188.48) * mm});
            skArc(sketch, "E1905", {"start": v(53911.96, 52188.48) * mm, "mid": v(53914.53, 52190.5) * mm, "end": v(53915.05, 52193.74) * mm});
            skLineSegment(sketch, "E1906", {"start": v(53915.05, 52193.74) * mm, "end": v(53905.74, 52236.57) * mm});
            skArc(sketch, "E1907", {"start": v(53912.96, 52248.85) * mm, "mid": v(53906.95, 52244.12) * mm, "end": v(53905.74, 52236.57) * mm});
            skLineSegment(sketch, "E1908", {"start": v(53912.96, 52248.85) * mm, "end": v(54023.61, 52282.35) * mm});
            skArc(sketch, "E1909", {"start": v(54036.43, 52276.13) * mm, "mid": v(54031.24, 52281.74) * mm, "end": v(54023.61, 52282.35) * mm});
            skLineSegment(sketch, "E1910", {"start": v(54036.43, 52276.13) * mm, "end": v(54052.43, 52235.32) * mm});
            skArc(sketch, "E1911", {"start": v(54052.43, 52235.32) * mm, "mid": v(54054.66, 52232.91) * mm, "end": v(54057.92, 52232.66) * mm});
            skLineSegment(sketch, "E1912", {"start": v(54057.92, 52232.66) * mm, "end": v(54061.51, 52233.74) * mm});
            skLineSegment(sketch, "E1913", {"start": v(54061.51, 52233.74) * mm, "end": v(54042.68, 52295.95) * mm});
            skLineSegment(sketch, "E1914", {"start": v(54042.68, 52295.95) * mm, "end": v(53889.54, 52249.6) * mm});
            skLineSegment(sketch, "E1915", {"start": v(53967.36, 52544.8) * mm, "end": v(53948.53, 52607.02) * mm});
            skLineSegment(sketch, "E1916", {"start": v(53948.53, 52607.02) * mm, "end": v(53944.94, 52605.93) * mm});
            skArc(sketch, "E1917", {"start": v(53944.94, 52605.93) * mm, "mid": v(53942.37, 52603.9) * mm, "end": v(53941.85, 52600.67) * mm});
            skLineSegment(sketch, "E1918", {"start": v(53941.85, 52600.67) * mm, "end": v(53951.17, 52557.84) * mm});
            skArc(sketch, "E1919", {"start": v(53943.95, 52545.55) * mm, "mid": v(53949.96, 52550.28) * mm, "end": v(53951.17, 52557.84) * mm});
            skLineSegment(sketch, "E1920", {"start": v(53943.95, 52545.55) * mm, "end": v(53833.3, 52512.06) * mm});
            skArc(sketch, "E1921", {"start": v(53820.47, 52518.28) * mm, "mid": v(53825.67, 52512.66) * mm, "end": v(53833.3, 52512.06) * mm});
            skLineSegment(sketch, "E1922", {"start": v(53820.47, 52518.28) * mm, "end": v(53804.47, 52559.09) * mm});
            skArc(sketch, "E1923", {"start": v(53804.47, 52559.09) * mm, "mid": v(53802.25, 52561.5) * mm, "end": v(53798.98, 52561.75) * mm});
            skLineSegment(sketch, "E1924", {"start": v(53798.98, 52561.75) * mm, "end": v(53795.4, 52560.67) * mm});
            skLineSegment(sketch, "E1925", {"start": v(53795.4, 52560.67) * mm, "end": v(53814.22, 52498.45) * mm});
            skLineSegment(sketch, "E1926", {"start": v(53814.22, 52498.45) * mm, "end": v(53967.36, 52544.8) * mm});
            skCircle(sketch, "E1927", {"center": v(53928.45, 52397.2) * mm, "radius": 0.25 * mm});
            skCircle(sketch, "E1928", {"center": v(53928.45, 52397.2) * mm, "radius": 57.5 * mm});
            skCircle(sketch, "E1929", {"center": v(53928.45, 52397.2) * mm, "radius": 59.5 * mm});
            skCircle(sketch, "E1930", {"center": v(53928.45, 52397.2) * mm, "radius": 63.5 * mm});
            skLineSegment(sketch, "E1931", {"start": v(53976.67, 52617.62) * mm, "end": v(53947.95, 52608.93) * mm});
            skLineSegment(sketch, "E1932", {"start": v(53947.95, 52608.93) * mm, "end": v(53962.44, 52561.08) * mm});
            skLineSegment(sketch, "E1933", {"start": v(53962.44, 52561.08) * mm, "end": v(53991.15, 52569.77) * mm});
            skLineSegment(sketch, "E1934", {"start": v(53991.15, 52569.77) * mm, "end": v(53976.67, 52617.62) * mm});
            skLineSegment(sketch, "E1935", {"start": v(53947.95, 52608.93) * mm, "end": v(53948.53, 52607.02) * mm});
            skLineSegment(sketch, "E1936", {"start": v(53948.53, 52607.02) * mm, "end": v(53962.44, 52561.08) * mm});
            skLineSegment(sketch, "E1937", {"start": v(56708.55, 53374.49) * mm, "end": v(56689.72, 53436.7) * mm});
            skLineSegment(sketch, "E1938", {"start": v(56689.72, 53436.7) * mm, "end": v(56686.13, 53435.61) * mm});
            skArc(sketch, "E1939", {"start": v(56686.13, 53435.61) * mm, "mid": v(56683.56, 53433.59) * mm, "end": v(56683.04, 53430.35) * mm});
            skLineSegment(sketch, "E1940", {"start": v(56683.04, 53430.35) * mm, "end": v(56692.36, 53387.52) * mm});
            skArc(sketch, "E1941", {"start": v(56685.14, 53375.24) * mm, "mid": v(56691.15, 53379.96) * mm, "end": v(56692.36, 53387.52) * mm});
            skLineSegment(sketch, "E1942", {"start": v(56685.14, 53375.24) * mm, "end": v(56574.48, 53341.74) * mm});
            skArc(sketch, "E1943", {"start": v(56561.66, 53347.96) * mm, "mid": v(56566.86, 53342.35) * mm, "end": v(56574.48, 53341.74) * mm});
            skLineSegment(sketch, "E1944", {"start": v(56561.66, 53347.96) * mm, "end": v(56545.66, 53388.77) * mm});
            skArc(sketch, "E1945", {"start": v(56545.66, 53388.77) * mm, "mid": v(56543.44, 53391.18) * mm, "end": v(56540.17, 53391.43) * mm});
            skLineSegment(sketch, "E1946", {"start": v(56540.17, 53391.43) * mm, "end": v(56536.58, 53390.35) * mm});
            skLineSegment(sketch, "E1947", {"start": v(56536.58, 53390.35) * mm, "end": v(56555.41, 53328.14) * mm});
            skLineSegment(sketch, "E1948", {"start": v(56555.41, 53328.14) * mm, "end": v(56708.55, 53374.49) * mm});
            skLineSegment(sketch, "E1949", {"start": v(56630.73, 53079.28) * mm, "end": v(56649.56, 53017.07) * mm});
            skLineSegment(sketch, "E1950", {"start": v(56649.56, 53017.07) * mm, "end": v(56653.15, 53018.16) * mm});
            skArc(sketch, "E1951", {"start": v(56653.15, 53018.16) * mm, "mid": v(56655.73, 53020.18) * mm, "end": v(56656.24, 53023.42) * mm});
            skLineSegment(sketch, "E1952", {"start": v(56656.24, 53023.42) * mm, "end": v(56646.93, 53066.25) * mm});
            skArc(sketch, "E1953", {"start": v(56654.15, 53078.53) * mm, "mid": v(56648.14, 53073.8) * mm, "end": v(56646.93, 53066.25) * mm});
            skLineSegment(sketch, "E1954", {"start": v(56654.15, 53078.53) * mm, "end": v(56764.8, 53112.03) * mm});
            skArc(sketch, "E1955", {"start": v(56777.62, 53105.81) * mm, "mid": v(56772.43, 53111.43) * mm, "end": v(56764.8, 53112.03) * mm});
            skLineSegment(sketch, "E1956", {"start": v(56777.62, 53105.81) * mm, "end": v(56793.62, 53065) * mm});
            skArc(sketch, "E1957", {"start": v(56793.62, 53065) * mm, "mid": v(56795.85, 53062.6) * mm, "end": v(56799.11, 53062.34) * mm});
            skLineSegment(sketch, "E1958", {"start": v(56799.11, 53062.34) * mm, "end": v(56802.7, 53063.42) * mm});
            skLineSegment(sketch, "E1959", {"start": v(56802.7, 53063.42) * mm, "end": v(56783.87, 53125.64) * mm});
            skLineSegment(sketch, "E1960", {"start": v(56783.87, 53125.64) * mm, "end": v(56630.73, 53079.28) * mm});
            skCircle(sketch, "E1961", {"center": v(56669.64, 53226.89) * mm, "radius": 0.25 * mm});
            skCircle(sketch, "E1962", {"center": v(56669.64, 53226.89) * mm, "radius": 57.5 * mm});
            skCircle(sketch, "E1963", {"center": v(56669.64, 53226.89) * mm, "radius": 59.5 * mm});
            skCircle(sketch, "E1964", {"center": v(56669.64, 53226.89) * mm, "radius": 63.5 * mm});
            skLineSegment(sketch, "E1965", {"start": v(56539.13, 53381.93) * mm, "end": v(56510.42, 53373.23) * mm});
            skLineSegment(sketch, "E1966", {"start": v(56510.42, 53373.23) * mm, "end": v(56521.77, 53335.72) * mm});
            skLineSegment(sketch, "E1967", {"start": v(56521.77, 53335.72) * mm, "end": v(56550.49, 53344.4) * mm});
            skLineSegment(sketch, "E1968", {"start": v(56550.49, 53344.4) * mm, "end": v(56539.13, 53381.93) * mm});
            skLineSegment(sketch, "E1969", {"start": v(56507.29, 53383.57) * mm, "end": v(56510.42, 53373.23) * mm});
            skLineSegment(sketch, "E1970", {"start": v(56536, 53392.26) * mm, "end": v(56507.29, 53383.57) * mm});
            skLineSegment(sketch, "E1971", {"start": v(56536, 53392.26) * mm, "end": v(56536.58, 53390.35) * mm});
            skLineSegment(sketch, "E1972", {"start": v(54409.66, 51283.84) * mm, "end": v(52697.54, 56940.4) * mm});
            skLineSegment(sketch, "E1973", {"start": v(52697.54, 56940.4) * mm, "end": v(55174.56, 57690.15) * mm});
            skLineSegment(sketch, "E1974", {"start": v(55174.56, 57690.15) * mm, "end": v(56886.68, 52033.59) * mm});
            skLineSegment(sketch, "E1975", {"start": v(56886.68, 52033.59) * mm, "end": v(54409.66, 51283.84) * mm});
            skLineSegment(sketch, "E1976", {"start": v(54485.56, 58123.03) * mm, "end": v(53326.1, 61953.71) * mm});
            skLineSegment(sketch, "E1977", {"start": v(53565.37, 62026.14) * mm, "end": v(53326.1, 61953.71) * mm});
            skLineSegment(sketch, "E1978", {"start": v(54797.27, 57956.18) * mm, "end": v(53565.37, 62026.14) * mm});
            skLineSegment(sketch, "E1979", {"start": v(53394.94, 61709.43) * mm, "end": v(52319.25, 61383.85) * mm});
            skLineSegment(sketch, "E1980", {"start": v(51926.33, 57085.7) * mm, "end": v(51428.05, 58731.95) * mm});
            skLineSegment(sketch, "E1981", {"start": v(51667.33, 58804.37) * mm, "end": v(51428.05, 58731.95) * mm});
            skLineSegment(sketch, "E1982", {"start": v(52093.19, 57397.4) * mm, "end": v(51667.33, 58804.37) * mm});
            skLineSegment(sketch, "E1983", {"start": v(52380.65, 73984.06) * mm, "end": v(52648.5, 73503.69) * mm});
            skLineSegment(sketch, "E1984", {"start": v(52430.15, 73381.94) * mm, "end": v(52648.5, 73503.69) * mm});
            skLineSegment(sketch, "E1985", {"start": v(52162.3, 73862.3) * mm, "end": v(52430.15, 73381.94) * mm});
            skLineSegment(sketch, "E1986", {"start": v(52162.3, 73862.3) * mm, "end": v(52380.65, 73984.06) * mm});
            skLineSegment(sketch, "E1987", {"start": v(49476.62, 59086.75) * mm, "end": v(44628.7, 57619.38) * mm});
            skLineSegment(sketch, "E1988", {"start": v(46549.88, 58728.5) * mm, "end": v(44769.56, 58189.64) * mm});
            skLineSegment(sketch, "E1989", {"start": v(49091.04, 59497.67) * mm, "end": v(46741.3, 58786.45) * mm});
            skLineSegment(sketch, "E1990", {"start": v(60902.9, 47249.4) * mm, "end": v(60232.9, 47046.62) * mm});
            skLineSegment(sketch, "E1991", {"start": v(60146, 47333.75) * mm, "end": v(60232.9, 47046.62) * mm});
            skLineSegment(sketch, "E1992", {"start": v(60815.98, 47536.54) * mm, "end": v(60146, 47333.75) * mm});
            skLineSegment(sketch, "E1993", {"start": v(60815.98, 47536.54) * mm, "end": v(60902.9, 47249.4) * mm});
            skLineSegment(sketch, "E1994", {"start": v(57660.34, 46581.4) * mm, "end": v(58330.32, 46784.18) * mm});
            skLineSegment(sketch, "E1995", {"start": v(58417.23, 46497.05) * mm, "end": v(58330.32, 46784.18) * mm});
            skLineSegment(sketch, "E1996", {"start": v(57747.25, 46294.26) * mm, "end": v(58417.23, 46497.05) * mm});
            skLineSegment(sketch, "E1997", {"start": v(57747.25, 46294.26) * mm, "end": v(57660.34, 46581.4) * mm});
            skLineSegment(sketch, "E1998", {"start": v(66123.9, 48829.7) * mm, "end": v(65453.93, 48626.91) * mm});
            skLineSegment(sketch, "E1999", {"start": v(65367.02, 48914.05) * mm, "end": v(65453.93, 48626.91) * mm});
            skLineSegment(sketch, "E2000", {"start": v(66037, 49116.84) * mm, "end": v(65367.02, 48914.05) * mm});
            skLineSegment(sketch, "E2001", {"start": v(66037, 49116.84) * mm, "end": v(66123.9, 48829.7) * mm});
            skLineSegment(sketch, "E2002", {"start": v(66797.61, 49033.62) * mm, "end": v(54839.43, 45414.12) * mm});
            skLineSegment(sketch, "E2003", {"start": v(50674.63, 70450.6) * mm, "end": v(50230.84, 69847.7) * mm});
            skLineSegment(sketch, "E2004", {"start": v(49989.23, 70025.54) * mm, "end": v(50230.84, 69847.7) * mm});
            skLineSegment(sketch, "E2005", {"start": v(50433.02, 70628.44) * mm, "end": v(49989.23, 70025.54) * mm});
            skLineSegment(sketch, "E2006", {"start": v(50433.02, 70628.44) * mm, "end": v(50674.63, 70450.6) * mm});
            skLineSegment(sketch, "E2007", {"start": v(42897.6, 69357.64) * mm, "end": v(43592.33, 70299.2) * mm});
            skLineSegment(sketch, "E2008", {"start": v(43833.73, 70121.08) * mm, "end": v(43592.33, 70299.2) * mm});
            skLineSegment(sketch, "E2009", {"start": v(43139, 69179.52) * mm, "end": v(43833.73, 70121.08) * mm});
            skLineSegment(sketch, "E2010", {"start": v(43139, 69179.52) * mm, "end": v(42897.6, 69357.64) * mm});
            skLineSegment(sketch, "E2011", {"start": v(47178.16, 66206.94) * mm, "end": v(47872.9, 67148.5) * mm});
            skLineSegment(sketch, "E2012", {"start": v(48114.3, 66970.39) * mm, "end": v(47872.9, 67148.5) * mm});
            skLineSegment(sketch, "E2013", {"start": v(47419.56, 66028.82) * mm, "end": v(48114.3, 66970.39) * mm});
            skLineSegment(sketch, "E2014", {"start": v(47419.56, 66028.82) * mm, "end": v(47178.16, 66206.94) * mm});
            skLineSegment(sketch, "E2015", {"start": v(49810.68, 60060.55) * mm, "end": v(50643.24, 57309.93) * mm});
            skLineSegment(sketch, "E2016", {"start": v(49303.41, 59907) * mm, "end": v(50135.97, 57156.4) * mm});
            skLineSegment(sketch, "E2017", {"start": v(49303.41, 59907) * mm, "end": v(49810.68, 60060.55) * mm});
            skEllipse(sketch, "E2018", {"center": v(52380.83, 57810.32) * mm, "majorRadius": 158.75 * mm, "minorRadius": 158.75 * mm, "majorAxis": v(1, 0)});
            skArc(sketch, "E2019", {"start": v(52532.77, 57856.31) * mm, "mid": v(52455.75, 57950.28) * mm, "end": v(52334.84, 57962.26) * mm});
            skArc(sketch, "E2020", {"start": v(52228.9, 57764.33) * mm, "mid": v(52305.91, 57670.36) * mm, "end": v(52426.82, 57658.38) * mm});
            skLineSegment(sketch, "E2021", {"start": v(52334.84, 57962.26) * mm, "end": v(52426.82, 57658.38) * mm});
            skLineSegment(sketch, "E2022", {"start": v(52228.9, 57764.33) * mm, "end": v(52532.77, 57856.31) * mm});
            skLineSegment(sketch, "E2023", {"start": v(52426.82, 57658.38) * mm, "end": v(52769.4, 56526.59) * mm});
            skLineSegment(sketch, "E2024", {"start": v(44215.6, 60106.43) * mm, "end": v(45947.99, 60630.79) * mm});
            skLineSegment(sketch, "E2025", {"start": v(45947.99, 60630.79) * mm, "end": v(46469.45, 58907.97) * mm});
            skLineSegment(sketch, "E2026", {"start": v(46469.45, 58907.97) * mm, "end": v(44737.06, 58383.62) * mm});
            skLineSegment(sketch, "E2027", {"start": v(44737.06, 58383.62) * mm, "end": v(44215.6, 60106.43) * mm});
            skLineSegment(sketch, "E2028", {"start": v(46187.33, 60703.22) * mm, "end": v(48489.2, 61399.95) * mm});
            skLineSegment(sketch, "E2029", {"start": v(48489.2, 61399.95) * mm, "end": v(49059.9, 59514.43) * mm});
            skLineSegment(sketch, "E2030", {"start": v(49059.9, 59514.43) * mm, "end": v(46758.03, 58817.7) * mm});
            skLineSegment(sketch, "E2031", {"start": v(46758.03, 58817.7) * mm, "end": v(46187.33, 60703.22) * mm});
            skLineSegment(sketch, "E2032", {"start": v(46187.3, 60703.2) * mm, "end": v(49055.09, 59512.96) * mm});
            skLineSegment(sketch, "E2033", {"start": v(48489.16, 61399.93) * mm, "end": v(46758, 58817.68) * mm});
            skLineSegment(sketch, "E2034", {"start": v(45947.99, 60630.79) * mm, "end": v(44737.06, 58383.62) * mm});
            skLineSegment(sketch, "E2035", {"start": v(44215.6, 60106.43) * mm, "end": v(46469.45, 58907.97) * mm});
            skLineSegment(sketch, "E2036", {"start": v(34594.6, 60252.83) * mm, "end": v(39514.82, 56634.47) * mm});
            skLineSegment(sketch, "E2037", {"start": v(39514.82, 56634.47) * mm, "end": v(39605, 56336.5) * mm});
            skLineSegment(sketch, "E2038", {"start": v(39605, 56336.5) * mm, "end": v(39413.58, 56278.55) * mm});
            skLineSegment(sketch, "E2039", {"start": v(39413.58, 56278.55) * mm, "end": v(39342.68, 56512.8) * mm});
            skLineSegment(sketch, "E2040", {"start": v(39342.68, 56512.8) * mm, "end": v(34691.26, 59933.49) * mm});
            skLineSegment(sketch, "E2041", {"start": v(34691.26, 59933.49) * mm, "end": v(34594.6, 60252.83) * mm});
            skLineSegment(sketch, "E2042", {"start": v(35650.6, 66135.53) * mm, "end": v(34532.41, 66959.92) * mm});
            skLineSegment(sketch, "E2043", {"start": v(34532.41, 66959.92) * mm, "end": v(34321.7, 66896.15) * mm});
            skLineSegment(sketch, "E2044", {"start": v(39418.85, 55967.75) * mm, "end": v(39705.98, 56054.66) * mm});
            skLineSegment(sketch, "E2045", {"start": v(39705.98, 56054.66) * mm, "end": v(40827.42, 52349.63) * mm});
            skLineSegment(sketch, "E2046", {"start": v(40827.42, 52349.63) * mm, "end": v(40540.29, 52262.72) * mm});
            skLineSegment(sketch, "E2047", {"start": v(40540.29, 52262.72) * mm, "end": v(39418.85, 55967.75) * mm});
            skLineSegment(sketch, "E2048", {"start": v(40943.3, 51966.79) * mm, "end": v(42050.67, 48308.25) * mm});
            skLineSegment(sketch, "E2049", {"start": v(42050.67, 48308.25) * mm, "end": v(41763.53, 48221.34) * mm});
            skLineSegment(sketch, "E2050", {"start": v(41763.53, 48221.34) * mm, "end": v(40656.17, 51879.88) * mm});
            skArc(sketch, "E2051", {"start": v(26492, 69028.42) * mm, "mid": v(26377.76, 69039.74) * mm, "end": v(26304.98, 69128.53) * mm});
            skLineSegment(sketch, "E2052", {"start": v(26304.98, 69128.53) * mm, "end": v(25968.93, 70238.79) * mm});
            skArc(sketch, "E2053", {"start": v(25968.93, 70238.79) * mm, "mid": v(25980.25, 70353.04) * mm, "end": v(26069.04, 70425.81) * mm});
            skLineSegment(sketch, "E2054", {"start": v(26069.04, 70425.81) * mm, "end": v(28811, 71255.75) * mm});
            skArc(sketch, "E2055", {"start": v(28811, 71255.75) * mm, "mid": v(28925.25, 71244.43) * mm, "end": v(28998.02, 71155.64) * mm});
            skLineSegment(sketch, "E2056", {"start": v(28998.02, 71155.64) * mm, "end": v(29334.08, 70045.38) * mm});
            skArc(sketch, "E2057", {"start": v(29334.08, 70045.38) * mm, "mid": v(29322.75, 69931.13) * mm, "end": v(29233.96, 69858.36) * mm});
            skLineSegment(sketch, "E2058", {"start": v(29233.96, 69858.36) * mm, "end": v(26492, 69028.42) * mm});
            skLineSegment(sketch, "E2059", {"start": v(32882.84, 66524.7) * mm, "end": v(32930.7, 66539.19) * mm});
            skLineSegment(sketch, "E2060", {"start": v(49929.2, 66665.23) * mm, "end": v(50000.34, 66761.87) * mm});
            skLineSegment(sketch, "E2061", {"start": v(50000.34, 66761.87) * mm, "end": v(50805.67, 66169.05) * mm});
            skLineSegment(sketch, "E2062", {"start": v(50805.67, 66169.05) * mm, "end": v(50734.53, 66072.4) * mm});
            skLineSegment(sketch, "E2063", {"start": v(50734.53, 66072.4) * mm, "end": v(49929.2, 66665.23) * mm});
            skLineSegment(sketch, "E2064", {"start": v(49929.2, 66665.23) * mm, "end": v(50805.2, 66169.07) * mm});
            skLineSegment(sketch, "E2065", {"start": v(43594.3, 60519.15) * mm, "end": v(43737.87, 60562.6) * mm});
            skLineSegment(sketch, "E2066", {"start": v(43737.87, 60562.6) * mm, "end": v(43824.77, 60275.47) * mm});
            skLineSegment(sketch, "E2067", {"start": v(43824.77, 60275.47) * mm, "end": v(43681.2, 60232.02) * mm});
            skLineSegment(sketch, "E2068", {"start": v(43681.2, 60232.02) * mm, "end": v(43594.3, 60519.15) * mm});
            skLineSegment(sketch, "E2069", {"start": v(43681.2, 60232.02) * mm, "end": v(43737.87, 60562.6) * mm});
            skLineSegment(sketch, "E2070", {"start": v(50041.24, 64951.98) * mm, "end": v(49336.5, 64864.07) * mm});
            skLineSegment(sketch, "E2071", {"start": v(50611.99, 70617.58) * mm, "end": v(50491.18, 70706.49) * mm});
            skLineSegment(sketch, "E2072", {"start": v(50491.18, 70706.49) * mm, "end": v(50669, 70948.11) * mm});
            skLineSegment(sketch, "E2073", {"start": v(50669, 70948.11) * mm, "end": v(50789.8, 70859.2) * mm});
            skLineSegment(sketch, "E2074", {"start": v(50789.8, 70859.2) * mm, "end": v(50611.99, 70617.58) * mm});
            skLineSegment(sketch, "E2075", {"start": v(40168.76, 60876.96) * mm, "end": v(40300.53, 61125.8) * mm});
            skLineSegment(sketch, "E2076", {"start": v(40110.82, 61068.38) * mm, "end": v(40302.24, 61126.32) * mm});
            skLineSegment(sketch, "E2077", {"start": v(40302.24, 61126.32) * mm, "end": v(40360.18, 60934.9) * mm});
            skLineSegment(sketch, "E2078", {"start": v(40360.18, 60934.9) * mm, "end": v(40168.76, 60876.96) * mm});
            skLineSegment(sketch, "E2079", {"start": v(40168.76, 60876.96) * mm, "end": v(40110.82, 61068.38) * mm});
            skLineSegment(sketch, "E2080", {"start": v(48691.52, 61680.62) * mm, "end": v(49237.07, 61845.75) * mm});
            skLineSegment(sketch, "E2081", {"start": v(49005.84, 60642.15) * mm, "end": v(48691.52, 61680.62) * mm});
            skLineSegment(sketch, "E2082", {"start": v(48691.52, 61680.62) * mm, "end": v(49551.4, 60807.28) * mm});
            skLineSegment(sketch, "E2083", {"start": v(58567.6, 53039.13) * mm, "end": v(58742.29, 53136.53) * mm});
            skLineSegment(sketch, "E2084", {"start": v(58742.29, 53136.53) * mm, "end": v(58888.39, 52874.5) * mm});
            skLineSegment(sketch, "E2085", {"start": v(58888.39, 52874.5) * mm, "end": v(58713.7, 52777.1) * mm});
            skLineSegment(sketch, "E2086", {"start": v(58713.7, 52777.1) * mm, "end": v(58567.6, 53039.13) * mm});
            skLineSegment(sketch, "E2087", {"start": v(47898.37, 63974.02) * mm, "end": v(51386.01, 64567.4) * mm});
            skLineSegment(sketch, "E2088", {"start": v(53966.18, 50757) * mm, "end": v(52040.19, 57120.16) * mm});
            skLineSegment(sketch, "E2089", {"start": v(52040.19, 57120.16) * mm, "end": v(55677.4, 58222.57) * mm});
            skLineSegment(sketch, "E2090", {"start": v(55677.4, 58222.57) * mm, "end": v(58823.27, 52580.61) * mm});
            skLineSegment(sketch, "E2091", {"start": v(58823.27, 52580.61) * mm, "end": v(57793.68, 52268.9) * mm});
            skLineSegment(sketch, "E2092", {"start": v(57793.68, 52268.9) * mm, "end": v(57891.69, 51945.18) * mm});
            skLineSegment(sketch, "E2093", {"start": v(57891.69, 51945.18) * mm, "end": v(53966.18, 50757) * mm});
            skLineSegment(sketch, "E2094", {"start": v(53966.18, 50757) * mm, "end": v(55677.4, 58222.57) * mm});
            skLineSegment(sketch, "E2095", {"start": v(58823.27, 52580.61) * mm, "end": v(52040.19, 57120.16) * mm});
            skLineSegment(sketch, "E2096", {"start": v(39517.4, 53123.26) * mm, "end": v(38245.58, 57319.62) * mm});
            skLineSegment(sketch, "E2097", {"start": v(34797.37, 59582.93) * mm, "end": v(36984.59, 52356.63) * mm});
            skLineSegment(sketch, "E2098", {"start": v(36984.59, 52356.63) * mm, "end": v(38245.58, 57319.62) * mm});
            skLineSegment(sketch, "E2099", {"start": v(39516.16, 53122.89) * mm, "end": v(34797.37, 59582.93) * mm});
            skLineSegment(sketch, "E2100", {"start": v(54510.66, 63468.68) * mm, "end": v(54641.67, 63541.72) * mm});
            skLineSegment(sketch, "E2101", {"start": v(54641.67, 63541.72) * mm, "end": v(54787.76, 63279.7) * mm});
            skLineSegment(sketch, "E2102", {"start": v(54787.76, 63279.7) * mm, "end": v(54656.74, 63206.65) * mm});
            skLineSegment(sketch, "E2103", {"start": v(54656.74, 63206.65) * mm, "end": v(54510.66, 63468.68) * mm});
            skLineSegment(sketch, "E2104", {"start": v(54656.74, 63206.65) * mm, "end": v(54641.67, 63541.72) * mm});
            skLineSegment(sketch, "E2105", {"start": v(51785.35, 68062.5) * mm, "end": v(51874.2, 68183.36) * mm});
            skLineSegment(sketch, "E2106", {"start": v(51874.2, 68183.36) * mm, "end": v(52115.9, 68005.67) * mm});
            skLineSegment(sketch, "E2107", {"start": v(52115.9, 68005.67) * mm, "end": v(52027.06, 67884.81) * mm});
            skLineSegment(sketch, "E2108", {"start": v(52027.06, 67884.81) * mm, "end": v(51785.35, 68062.5) * mm});
            skLineSegment(sketch, "E2109", {"start": v(52027.06, 67884.81) * mm, "end": v(51874.2, 68183.36) * mm});
            skLineSegment(sketch, "E2110", {"start": v(50491.18, 70706.49) * mm, "end": v(50789.8, 70859.2) * mm});
            skLineSegment(sketch, "E2111", {"start": v(38896.6, 63412.25) * mm, "end": v(38807.68, 63291.44) * mm});
            skLineSegment(sketch, "E2112", {"start": v(38807.68, 63291.44) * mm, "end": v(38566.06, 63469.26) * mm});
            skLineSegment(sketch, "E2113", {"start": v(38566.06, 63469.26) * mm, "end": v(38654.97, 63590.07) * mm});
            skLineSegment(sketch, "E2114", {"start": v(38654.97, 63590.07) * mm, "end": v(38896.6, 63412.25) * mm});
            skLineSegment(sketch, "E2115", {"start": v(38807.68, 63291.44) * mm, "end": v(38654.97, 63590.07) * mm});
            skLineSegment(sketch, "E2116", {"start": v(53537.13, 69760.28) * mm, "end": v(52095.63, 72345.89) * mm});
            skLineSegment(sketch, "E2117", {"start": v(52095.63, 72345.89) * mm, "end": v(52130.57, 72365.37) * mm});
            skLineSegment(sketch, "E2118", {"start": v(52130.57, 72365.37) * mm, "end": v(52130.67, 72365.2) * mm});
            skLineSegment(sketch, "E2119", {"start": v(52130.67, 72365.2) * mm, "end": v(52270.42, 72443.1) * mm});
            skLineSegment(sketch, "E2120", {"start": v(52270.42, 72443.1) * mm, "end": v(53711.78, 69857.74) * mm});
            skLineSegment(sketch, "E2121", {"start": v(53711.78, 69857.74) * mm, "end": v(53572.03, 69779.83) * mm});
            skLineSegment(sketch, "E2122", {"start": v(53572.03, 69779.83) * mm, "end": v(53572.07, 69779.76) * mm});
            skLineSegment(sketch, "E2123", {"start": v(53572.07, 69779.76) * mm, "end": v(53537.13, 69760.28) * mm});
            skLineSegment(sketch, "E2124", {"start": v(43897.3, 60036.2) * mm, "end": v(43897.27, 60036.22) * mm});
            skLineSegment(sketch, "E2125", {"start": v(43897.27, 60036.22) * mm, "end": v(43976.87, 59773.24) * mm});
            skLineSegment(sketch, "E2126", {"start": v(43976.87, 59773.24) * mm, "end": v(42927.44, 60546.94) * mm});
            skLineSegment(sketch, "E2127", {"start": v(42927.44, 60546.94) * mm, "end": v(43046.13, 60707.92) * mm});
            skLineSegment(sketch, "E2128", {"start": v(43046.13, 60707.92) * mm, "end": v(43880.08, 60093.07) * mm});
            skLineSegment(sketch, "E2129", {"start": v(43880.08, 60093.07) * mm, "end": v(43897.3, 60036.2) * mm});
            skLineSegment(sketch, "E2130", {"start": v(34315.91, 66915.29) * mm, "end": v(34536.21, 66981.97) * mm});
            skLineSegment(sketch, "E2131", {"start": v(34536.21, 66981.97) * mm, "end": v(35662.57, 66151.55) * mm});
            skLineSegment(sketch, "E2132", {"start": v(35662.57, 66151.55) * mm, "end": v(35638.83, 66119.35) * mm});
            skLineSegment(sketch, "E2133", {"start": v(35638.83, 66119.35) * mm, "end": v(35638.75, 66119.41) * mm});
            skLineSegment(sketch, "E2134", {"start": v(35638.75, 66119.41) * mm, "end": v(35634.65, 66113.9) * mm});
            skLineSegment(sketch, "E2135", {"start": v(35634.65, 66113.9) * mm, "end": v(35543.78, 65990.65) * mm});
            skLineSegment(sketch, "E2136", {"start": v(35543.78, 65990.65) * mm, "end": v(34498.21, 66761.5) * mm});
            skLineSegment(sketch, "E2137", {"start": v(34498.21, 66761.5) * mm, "end": v(34373.85, 66723.87) * mm});
            skLineSegment(sketch, "E2138", {"start": v(34373.85, 66723.87) * mm, "end": v(34315.91, 66915.29) * mm});
            skLineSegment(sketch, "E2139", {"start": v(35662.55, 66151.56) * mm, "end": v(38535.92, 64033.13) * mm});
            skLineSegment(sketch, "E2140", {"start": v(38535.92, 64033.13) * mm, "end": v(38417.25, 63872.14) * mm});
            skLineSegment(sketch, "E2141", {"start": v(38417.25, 63872.14) * mm, "end": v(35543.78, 65990.65) * mm});
            skLineSegment(sketch, "E2142", {"start": v(35543.78, 65990.65) * mm, "end": v(35662.55, 66151.56) * mm});
            skLineSegment(sketch, "E2143", {"start": v(60257.35, 61806.65) * mm, "end": v(60354.74, 61631.96) * mm});
            skLineSegment(sketch, "E2144", {"start": v(60354.74, 61631.96) * mm, "end": v(59524.96, 61169.35) * mm});
            skLineSegment(sketch, "E2145", {"start": v(59524.96, 61169.35) * mm, "end": v(59427.57, 61344.04) * mm});
            skLineSegment(sketch, "E2146", {"start": v(59427.57, 61344.04) * mm, "end": v(60257.35, 61806.65) * mm});
            skLineSegment(sketch, "E2147", {"start": v(59232.56, 63644.81) * mm, "end": v(59329.95, 63470.13) * mm});
            skLineSegment(sketch, "E2148", {"start": v(59329.95, 63470.13) * mm, "end": v(58500.18, 63007.53) * mm});
            skLineSegment(sketch, "E2149", {"start": v(58500.18, 63007.53) * mm, "end": v(58402.8, 63182.21) * mm});
            skLineSegment(sketch, "E2150", {"start": v(58402.8, 63182.21) * mm, "end": v(59232.56, 63644.81) * mm});
            skLineSegment(sketch, "E2151", {"start": v(56749.74, 68097.33) * mm, "end": v(56847.13, 67922.65) * mm});
            skLineSegment(sketch, "E2152", {"start": v(56847.13, 67922.65) * mm, "end": v(56017.76, 67460.27) * mm});
            skLineSegment(sketch, "E2153", {"start": v(56017.76, 67460.27) * mm, "end": v(55920.37, 67634.95) * mm});
            skLineSegment(sketch, "E2154", {"start": v(55920.37, 67634.95) * mm, "end": v(56749.74, 68097.33) * mm});
            skLineSegment(sketch, "E2155", {"start": v(55778.9, 69839.64) * mm, "end": v(55876.29, 69664.95) * mm});
            skLineSegment(sketch, "E2156", {"start": v(55876.29, 69664.95) * mm, "end": v(55046.51, 69202.35) * mm});
            skLineSegment(sketch, "E2157", {"start": v(55046.51, 69202.35) * mm, "end": v(54949.13, 69377.03) * mm});
            skLineSegment(sketch, "E2158", {"start": v(54949.13, 69377.03) * mm, "end": v(55778.9, 69839.64) * mm});
            skLineSegment(sketch, "E2159", {"start": v(53344.56, 74206.1) * mm, "end": v(53441.95, 74031.41) * mm});
            skLineSegment(sketch, "E2160", {"start": v(53441.95, 74031.41) * mm, "end": v(52612.17, 73568.8) * mm});
            skLineSegment(sketch, "E2161", {"start": v(52612.17, 73568.8) * mm, "end": v(52514.78, 73743.49) * mm});
            skLineSegment(sketch, "E2162", {"start": v(52514.78, 73743.49) * mm, "end": v(53344.56, 74206.1) * mm});
            skLineSegment(sketch, "E2163", {"start": v(62790.91, 57262.2) * mm, "end": v(62888.3, 57087.52) * mm});
            skLineSegment(sketch, "E2164", {"start": v(62888.3, 57087.52) * mm, "end": v(62058.53, 56624.91) * mm});
            skLineSegment(sketch, "E2165", {"start": v(62058.53, 56624.91) * mm, "end": v(61961.14, 56799.6) * mm});
            skLineSegment(sketch, "E2166", {"start": v(61961.14, 56799.6) * mm, "end": v(62790.91, 57262.2) * mm});
            skLineSegment(sketch, "E2167", {"start": v(38417.25, 63872.14) * mm, "end": v(38535.93, 64033.12) * mm});
            skLineSegment(sketch, "E2168", {"start": v(38535.93, 64033.12) * mm, "end": v(39122.27, 63600.84) * mm});
            skLineSegment(sketch, "E2169", {"start": v(39122.27, 63600.84) * mm, "end": v(39003.58, 63439.86) * mm});
            skLineSegment(sketch, "E2170", {"start": v(39003.58, 63439.86) * mm, "end": v(38417.25, 63872.14) * mm});
            skLineSegment(sketch, "E2171", {"start": v(39003.58, 63439.86) * mm, "end": v(39122.27, 63600.84) * mm});
            skLineSegment(sketch, "E2172", {"start": v(39122.27, 63600.84) * mm, "end": v(43046.13, 60707.92) * mm});
            skLineSegment(sketch, "E2173", {"start": v(43046.13, 60707.92) * mm, "end": v(42927.44, 60546.94) * mm});
            skLineSegment(sketch, "E2174", {"start": v(42927.44, 60546.94) * mm, "end": v(39003.58, 63439.86) * mm});
            skLineSegment(sketch, "E2175", {"start": v(60731.4, 57490.47) * mm, "end": v(60906.09, 57587.87) * mm});
            skLineSegment(sketch, "E2176", {"start": v(60906.09, 57587.87) * mm, "end": v(61003.49, 57413.19) * mm});
            skLineSegment(sketch, "E2177", {"start": v(61003.49, 57413.19) * mm, "end": v(60828.8, 57315.79) * mm});
            skLineSegment(sketch, "E2178", {"start": v(60828.8, 57315.79) * mm, "end": v(60731.4, 57490.47) * mm});
            skLineSegment(sketch, "E2179", {"start": v(60828.8, 57315.79) * mm, "end": v(60906.09, 57587.87) * mm});
            skLineSegment(sketch, "E2180", {"start": v(59363.44, 59944.2) * mm, "end": v(59538.12, 60041.6) * mm});
            skLineSegment(sketch, "E2181", {"start": v(59538.12, 60041.6) * mm, "end": v(59635.52, 59866.93) * mm});
            skLineSegment(sketch, "E2182", {"start": v(59635.52, 59866.93) * mm, "end": v(59460.84, 59769.53) * mm});
            skLineSegment(sketch, "E2183", {"start": v(59460.84, 59769.53) * mm, "end": v(59363.44, 59944.2) * mm});
            skLineSegment(sketch, "E2184", {"start": v(59460.84, 59769.53) * mm, "end": v(59538.12, 60041.6) * mm});
            skLineSegment(sketch, "E2185", {"start": v(57225.38, 63779.25) * mm, "end": v(57400.06, 63876.65) * mm});
            skLineSegment(sketch, "E2186", {"start": v(57400.06, 63876.65) * mm, "end": v(57497.46, 63701.97) * mm});
            skLineSegment(sketch, "E2187", {"start": v(57497.46, 63701.97) * mm, "end": v(57322.78, 63604.57) * mm});
            skLineSegment(sketch, "E2188", {"start": v(57322.78, 63604.57) * mm, "end": v(57225.38, 63779.25) * mm});
            skLineSegment(sketch, "E2189", {"start": v(57322.78, 63604.57) * mm, "end": v(57400.06, 63876.65) * mm});
            skLineSegment(sketch, "E2190", {"start": v(55857.3, 66233.17) * mm, "end": v(56031.98, 66330.57) * mm});
            skLineSegment(sketch, "E2191", {"start": v(56031.98, 66330.57) * mm, "end": v(56129.38, 66155.88) * mm});
            skLineSegment(sketch, "E2192", {"start": v(56129.38, 66155.88) * mm, "end": v(55954.7, 66058.49) * mm});
            skLineSegment(sketch, "E2193", {"start": v(55954.7, 66058.49) * mm, "end": v(55857.3, 66233.17) * mm});
            skLineSegment(sketch, "E2194", {"start": v(55954.7, 66058.49) * mm, "end": v(56031.98, 66330.57) * mm});
            skLineSegment(sketch, "E2195", {"start": v(53719.23, 70068.22) * mm, "end": v(53893.9, 70165.62) * mm});
            skLineSegment(sketch, "E2196", {"start": v(53893.9, 70165.62) * mm, "end": v(53991.3, 69990.94) * mm});
            skLineSegment(sketch, "E2197", {"start": v(53991.3, 69990.94) * mm, "end": v(53816.63, 69893.54) * mm});
            skLineSegment(sketch, "E2198", {"start": v(53816.63, 69893.54) * mm, "end": v(53719.23, 70068.22) * mm});
            skLineSegment(sketch, "E2199", {"start": v(53816.63, 69893.54) * mm, "end": v(53893.9, 70165.62) * mm});
            skLineSegment(sketch, "E2200", {"start": v(52350.9, 72522.56) * mm, "end": v(52525.58, 72619.96) * mm});
            skLineSegment(sketch, "E2201", {"start": v(52525.58, 72619.96) * mm, "end": v(52622.98, 72445.28) * mm});
            skLineSegment(sketch, "E2202", {"start": v(52622.98, 72445.28) * mm, "end": v(52448.3, 72347.88) * mm});
            skLineSegment(sketch, "E2203", {"start": v(52448.3, 72347.88) * mm, "end": v(52350.9, 72522.56) * mm});
            skLineSegment(sketch, "E2204", {"start": v(52448.3, 72347.88) * mm, "end": v(52525.58, 72619.96) * mm});
            skLineSegment(sketch, "E2205", {"start": v(54817.6, 58562.1) * mm, "end": v(55009.03, 58620.04) * mm});
            skLineSegment(sketch, "E2206", {"start": v(55009.03, 58620.04) * mm, "end": v(55066.97, 58428.62) * mm});
            skLineSegment(sketch, "E2207", {"start": v(55066.97, 58428.62) * mm, "end": v(54875.54, 58370.68) * mm});
            skLineSegment(sketch, "E2208", {"start": v(54875.54, 58370.68) * mm, "end": v(54817.6, 58562.1) * mm});
            skLineSegment(sketch, "E2209", {"start": v(54875.54, 58370.68) * mm, "end": v(55007.31, 58619.53) * mm});
            skLineSegment(sketch, "E2210", {"start": v(51984.6, 72545.04) * mm, "end": v(52103.49, 72743.99) * mm});
            skLineSegment(sketch, "E2211", {"start": v(52103.49, 72743.99) * mm, "end": v(52275.17, 72641.4) * mm});
            skLineSegment(sketch, "E2212", {"start": v(52275.17, 72641.4) * mm, "end": v(52215.52, 72541.57) * mm});
            skLineSegment(sketch, "E2213", {"start": v(52215.52, 72541.57) * mm, "end": v(52270.42, 72443.1) * mm});
            skLineSegment(sketch, "E2214", {"start": v(52270.42, 72443.1) * mm, "end": v(52117.57, 72357.89) * mm});
            skLineSegment(sketch, "E2215", {"start": v(52117.57, 72357.89) * mm, "end": v(52117.5, 72358.02) * mm});
            skLineSegment(sketch, "E2216", {"start": v(52117.5, 72358.02) * mm, "end": v(52113.1, 72355.63) * mm});
            skLineSegment(sketch, "E2217", {"start": v(52113.1, 72355.63) * mm, "end": v(52095.63, 72345.89) * mm});
            skLineSegment(sketch, "E2218", {"start": v(52095.63, 72345.89) * mm, "end": v(51984.6, 72545.04) * mm});
            skLineSegment(sketch, "E2219", {"start": v(52471.3, 73359.53) * mm, "end": v(52452, 73394.12) * mm});
            skLineSegment(sketch, "E2220", {"start": v(52452, 73394.12) * mm, "end": v(52626.69, 73491.52) * mm});
            skLineSegment(sketch, "E2221", {"start": v(52626.69, 73491.52) * mm, "end": v(52702.21, 73356.07) * mm});
            skLineSegment(sketch, "E2222", {"start": v(52702.21, 73356.07) * mm, "end": v(52639.36, 73250.88) * mm});
            skLineSegment(sketch, "E2223", {"start": v(52639.36, 73250.88) * mm, "end": v(52467.68, 73353.47) * mm});
            skLineSegment(sketch, "E2224", {"start": v(52467.68, 73353.47) * mm, "end": v(52471.3, 73359.53) * mm});
            skLineSegment(sketch, "E2225", {"start": v(52103.49, 72743.99) * mm, "end": v(52467.68, 73353.47) * mm});
            skLineSegment(sketch, "E2226", {"start": v(52467.68, 73353.47) * mm, "end": v(52639.36, 73250.88) * mm});
            skLineSegment(sketch, "E2227", {"start": v(52639.36, 73250.88) * mm, "end": v(52275.17, 72641.4) * mm});
            skLineSegment(sketch, "E2228", {"start": v(52275.17, 72641.4) * mm, "end": v(52103.49, 72743.99) * mm});
            skLineSegment(sketch, "E2229", {"start": v(60661.38, 56982.93) * mm, "end": v(60549.13, 57182.87) * mm});
            skLineSegment(sketch, "E2230", {"start": v(60549.13, 57182.87) * mm, "end": v(60584, 57202.46) * mm});
            skLineSegment(sketch, "E2231", {"start": v(60584, 57202.46) * mm, "end": v(60584.04, 57202.4) * mm});
            skLineSegment(sketch, "E2232", {"start": v(60584.04, 57202.4) * mm, "end": v(60723.79, 57280.31) * mm});
            skLineSegment(sketch, "E2233", {"start": v(60723.79, 57280.31) * mm, "end": v(60779.93, 57179.6) * mm});
            skLineSegment(sketch, "E2234", {"start": v(60779.93, 57179.6) * mm, "end": v(60895.21, 57177.99) * mm});
            skLineSegment(sketch, "E2235", {"start": v(60895.21, 57177.99) * mm, "end": v(60892.97, 57018) * mm});
            skLineSegment(sketch, "E2236", {"start": v(60892.97, 57018) * mm, "end": v(60893.12, 57018) * mm});
            skLineSegment(sketch, "E2237", {"start": v(60893.12, 57018) * mm, "end": v(60892.27, 56978.01) * mm});
            skLineSegment(sketch, "E2238", {"start": v(60892.27, 56978.01) * mm, "end": v(60661.38, 56982.93) * mm});
            skLineSegment(sketch, "E2239", {"start": v(61612.44, 56967.92) * mm, "end": v(61602.34, 56968.06) * mm});
            skLineSegment(sketch, "E2240", {"start": v(61602.34, 56968.06) * mm, "end": v(61605.14, 57168.04) * mm});
            skLineSegment(sketch, "E2241", {"start": v(61605.14, 57168.04) * mm, "end": v(61732.31, 57166.26) * mm});
            skLineSegment(sketch, "E2242", {"start": v(61732.31, 57166.26) * mm, "end": v(61806.05, 57030.49) * mm});
            skLineSegment(sketch, "E2243", {"start": v(61806.05, 57030.49) * mm, "end": v(61630.3, 56935.04) * mm});
            skLineSegment(sketch, "E2244", {"start": v(61630.3, 56935.04) * mm, "end": v(61612.44, 56967.92) * mm});
            skLineSegment(sketch, "E2245", {"start": v(58997.42, 59967.56) * mm, "end": v(59114.95, 60167.07) * mm});
            skLineSegment(sketch, "E2246", {"start": v(59114.95, 60167.07) * mm, "end": v(59149.42, 60146.77) * mm});
            skLineSegment(sketch, "E2247", {"start": v(59149.42, 60146.77) * mm, "end": v(59149.34, 60146.64) * mm});
            skLineSegment(sketch, "E2248", {"start": v(59149.34, 60146.64) * mm, "end": v(59286.6, 60064.44) * mm});
            skLineSegment(sketch, "E2249", {"start": v(59286.6, 60064.44) * mm, "end": v(59227.06, 59965) * mm});
            skLineSegment(sketch, "E2250", {"start": v(59227.06, 59965) * mm, "end": v(59282.43, 59865.67) * mm});
            skLineSegment(sketch, "E2251", {"start": v(59282.43, 59865.67) * mm, "end": v(59142.68, 59787.76) * mm});
            skLineSegment(sketch, "E2252", {"start": v(59142.68, 59787.76) * mm, "end": v(59142.7, 59787.71) * mm});
            skLineSegment(sketch, "E2253", {"start": v(59142.7, 59787.71) * mm, "end": v(59107.71, 59768.34) * mm});
            skLineSegment(sketch, "E2254", {"start": v(59107.71, 59768.34) * mm, "end": v(58997.42, 59967.56) * mm});
            skLineSegment(sketch, "E2255", {"start": v(59484.53, 60784.17) * mm, "end": v(59465.92, 60818.12) * mm});
            skLineSegment(sketch, "E2256", {"start": v(59465.92, 60818.12) * mm, "end": v(59641.29, 60914.28) * mm});
            skLineSegment(sketch, "E2257", {"start": v(59641.29, 60914.28) * mm, "end": v(59715.03, 60779.78) * mm});
            skLineSegment(sketch, "E2258", {"start": v(59715.03, 60779.78) * mm, "end": v(59651.4, 60673.55) * mm});
            skLineSegment(sketch, "E2259", {"start": v(59651.4, 60673.55) * mm, "end": v(59479.83, 60776.31) * mm});
            skLineSegment(sketch, "E2260", {"start": v(59479.83, 60776.31) * mm, "end": v(59484.53, 60784.17) * mm});
            skLineSegment(sketch, "E2261", {"start": v(59115.03, 60167.2) * mm, "end": v(59479.83, 60776.31) * mm});
            skLineSegment(sketch, "E2262", {"start": v(59479.83, 60776.31) * mm, "end": v(59651.4, 60673.55) * mm});
            skLineSegment(sketch, "E2263", {"start": v(59651.4, 60673.55) * mm, "end": v(59286.6, 60064.44) * mm});
            skLineSegment(sketch, "E2264", {"start": v(59286.6, 60064.44) * mm, "end": v(59115.03, 60167.2) * mm});
            skLineSegment(sketch, "E2265", {"start": v(60549.1, 57182.93) * mm, "end": v(59107.74, 59768.29) * mm});
            skLineSegment(sketch, "E2266", {"start": v(59107.74, 59768.29) * mm, "end": v(59282.43, 59865.67) * mm});
            skLineSegment(sketch, "E2267", {"start": v(59282.43, 59865.67) * mm, "end": v(60723.79, 57280.31) * mm});
            skLineSegment(sketch, "E2268", {"start": v(60723.79, 57280.31) * mm, "end": v(60549.1, 57182.93) * mm});
            skLineSegment(sketch, "E2269", {"start": v(61602.34, 56968.06) * mm, "end": v(60892.41, 56978) * mm});
            skLineSegment(sketch, "E2270", {"start": v(60892.41, 56978) * mm, "end": v(60895.21, 57177.99) * mm});
            skLineSegment(sketch, "E2271", {"start": v(60895.21, 57177.99) * mm, "end": v(61605.14, 57168.04) * mm});
            skLineSegment(sketch, "E2272", {"start": v(61605.14, 57168.04) * mm, "end": v(61602.34, 56968.06) * mm});
            skLineSegment(sketch, "E2273", {"start": v(56000.8, 67073.82) * mm, "end": v(55976.5, 67117.5) * mm});
            skLineSegment(sketch, "E2274", {"start": v(55976.5, 67117.5) * mm, "end": v(56133.8, 67205) * mm});
            skLineSegment(sketch, "E2275", {"start": v(56133.8, 67205) * mm, "end": v(56208.56, 67070.6) * mm});
            skLineSegment(sketch, "E2276", {"start": v(56208.56, 67070.6) * mm, "end": v(56144.58, 66963.53) * mm});
            skLineSegment(sketch, "E2277", {"start": v(56144.58, 66963.53) * mm, "end": v(55990.35, 67055.76) * mm});
            skLineSegment(sketch, "E2278", {"start": v(55990.35, 67055.76) * mm, "end": v(56000.8, 67073.82) * mm});
            skLineSegment(sketch, "E2279", {"start": v(57164.87, 63294.28) * mm, "end": v(57060.56, 63481.38) * mm});
            skLineSegment(sketch, "E2280", {"start": v(57060.56, 63481.38) * mm, "end": v(57217.78, 63569.03) * mm});
            skLineSegment(sketch, "E2281", {"start": v(57217.78, 63569.03) * mm, "end": v(57271.49, 63472.7) * mm});
            skLineSegment(sketch, "E2282", {"start": v(57271.49, 63472.7) * mm, "end": v(57387.73, 63470.95) * mm});
            skLineSegment(sketch, "E2283", {"start": v(57387.73, 63470.95) * mm, "end": v(57385.01, 63290.97) * mm});
            skLineSegment(sketch, "E2284", {"start": v(57385.01, 63290.97) * mm, "end": v(57164.87, 63294.28) * mm});
            skLineSegment(sketch, "E2285", {"start": v(58115.86, 63279.94) * mm, "end": v(58095.05, 63280.24) * mm});
            skLineSegment(sketch, "E2286", {"start": v(58095.05, 63280.24) * mm, "end": v(58095, 63285.32) * mm});
            skLineSegment(sketch, "E2287", {"start": v(58095, 63285.32) * mm, "end": v(58097.65, 63460.22) * mm});
            skLineSegment(sketch, "E2288", {"start": v(58097.65, 63460.22) * mm, "end": v(58222.43, 63458.42) * mm});
            skLineSegment(sketch, "E2289", {"start": v(58222.43, 63458.42) * mm, "end": v(58298.83, 63321.41) * mm});
            skLineSegment(sketch, "E2290", {"start": v(58298.83, 63321.41) * mm, "end": v(58141.62, 63233.75) * mm});
            skLineSegment(sketch, "E2291", {"start": v(58141.62, 63233.75) * mm, "end": v(58115.86, 63279.94) * mm});
            skLineSegment(sketch, "E2292", {"start": v(55619.2, 66066.74) * mm, "end": v(55512.9, 66257.4) * mm});
            skLineSegment(sketch, "E2293", {"start": v(55512.9, 66257.4) * mm, "end": v(55625.94, 66446.41) * mm});
            skLineSegment(sketch, "E2294", {"start": v(55625.94, 66446.41) * mm, "end": v(55780.39, 66354.05) * mm});
            skLineSegment(sketch, "E2295", {"start": v(55780.39, 66354.05) * mm, "end": v(55720.75, 66254.25) * mm});
            skLineSegment(sketch, "E2296", {"start": v(55720.75, 66254.25) * mm, "end": v(55776.42, 66154.39) * mm});
            skLineSegment(sketch, "E2297", {"start": v(55776.42, 66154.39) * mm, "end": v(55619.2, 66066.74) * mm});
            skLineSegment(sketch, "E2298", {"start": v(55619.2, 66066.74) * mm, "end": v(55776.42, 66154.39) * mm});
            skLineSegment(sketch, "E2299", {"start": v(55776.42, 66154.39) * mm, "end": v(57217.78, 63569.03) * mm});
            skLineSegment(sketch, "E2300", {"start": v(57217.78, 63569.03) * mm, "end": v(57060.56, 63481.38) * mm});
            skLineSegment(sketch, "E2301", {"start": v(57060.56, 63481.38) * mm, "end": v(55619.2, 66066.74) * mm});
            skLineSegment(sketch, "E2302", {"start": v(55990.35, 67055.76) * mm, "end": v(56144.83, 66963.38) * mm});
            skLineSegment(sketch, "E2303", {"start": v(56144.83, 66963.38) * mm, "end": v(55780.42, 66354.03) * mm});
            skLineSegment(sketch, "E2304", {"start": v(55780.42, 66354.03) * mm, "end": v(55625.94, 66446.41) * mm});
            skLineSegment(sketch, "E2305", {"start": v(55625.94, 66446.41) * mm, "end": v(55990.35, 67055.76) * mm});
            skLineSegment(sketch, "E2306", {"start": v(57387.73, 63470.95) * mm, "end": v(58097.65, 63460.22) * mm});
            skLineSegment(sketch, "E2307", {"start": v(58097.65, 63460.22) * mm, "end": v(58094.93, 63280.25) * mm});
            skLineSegment(sketch, "E2308", {"start": v(58094.93, 63280.25) * mm, "end": v(57385.01, 63290.97) * mm});
            skLineSegment(sketch, "E2309", {"start": v(57385.01, 63290.97) * mm, "end": v(57387.73, 63470.95) * mm});
            skLineSegment(sketch, "E2310", {"start": v(53882.45, 69756.1) * mm, "end": v(53882.8, 69756.1) * mm});
            skLineSegment(sketch, "E2311", {"start": v(53882.8, 69756.1) * mm, "end": v(53882.45, 69756.1) * mm});
            skLineSegment(sketch, "E2312", {"start": v(53882.45, 69756.1) * mm, "end": v(53882.45, 69756.1) * mm});
            skLineSegment(sketch, "E2313", {"start": v(54589.38, 69545.15) * mm, "end": v(53879.6, 69556.11) * mm});
            skLineSegment(sketch, "E2314", {"start": v(53879.6, 69556.11) * mm, "end": v(53880.21, 69596.11) * mm});
            skLineSegment(sketch, "E2315", {"start": v(53880.21, 69596.11) * mm, "end": v(53880.32, 69596.1) * mm});
            skLineSegment(sketch, "E2316", {"start": v(53880.32, 69596.1) * mm, "end": v(53882.8, 69756.1) * mm});
            skLineSegment(sketch, "E2317", {"start": v(53882.8, 69756.1) * mm, "end": v(54592.71, 69745.12) * mm});
            skLineSegment(sketch, "E2318", {"start": v(54592.71, 69745.12) * mm, "end": v(54590, 69570.14) * mm});
            skLineSegment(sketch, "E2319", {"start": v(54590, 69570.14) * mm, "end": v(54589.85, 69570.14) * mm});
            skLineSegment(sketch, "E2320", {"start": v(54589.85, 69570.14) * mm, "end": v(54589.69, 69565.15) * mm});
            skLineSegment(sketch, "E2321", {"start": v(54589.69, 69565.15) * mm, "end": v(54589.38, 69545.15) * mm});
            skLineSegment(sketch, "E2322", {"start": v(31493.9, 66061.12) * mm, "end": v(32870.67, 66477.84) * mm});
            skLineSegment(sketch, "E2323", {"start": v(32870.67, 66477.84) * mm, "end": v(32928.6, 66286.42) * mm});
            skLineSegment(sketch, "E2324", {"start": v(32928.6, 66286.42) * mm, "end": v(31551.84, 65869.7) * mm});
            skLineSegment(sketch, "E2325", {"start": v(31551.84, 65869.7) * mm, "end": v(31493.9, 66061.12) * mm});
            skLineSegment(sketch, "E2326", {"start": v(34315.91, 66915.29) * mm, "end": v(34373.85, 66723.87) * mm});
            skLineSegment(sketch, "E2327", {"start": v(34373.85, 66723.87) * mm, "end": v(32928.6, 66286.42) * mm});
            skLineSegment(sketch, "E2328", {"start": v(32928.6, 66286.42) * mm, "end": v(32870.67, 66477.84) * mm});
            skLineSegment(sketch, "E2329", {"start": v(32870.67, 66477.84) * mm, "end": v(34315.91, 66915.29) * mm});
            skLineSegment(sketch, "E2330", {"start": v(53649.31, 69559.06) * mm, "end": v(53537.13, 69760.28) * mm});
            skLineSegment(sketch, "E2331", {"start": v(53537.13, 69760.28) * mm, "end": v(53554.6, 69770.02) * mm});
            skLineSegment(sketch, "E2332", {"start": v(53554.6, 69770.02) * mm, "end": v(53558.92, 69772.53) * mm});
            skLineSegment(sketch, "E2333", {"start": v(53558.92, 69772.53) * mm, "end": v(53711.78, 69857.74) * mm});
            skLineSegment(sketch, "E2334", {"start": v(53711.78, 69857.74) * mm, "end": v(53767.63, 69757.56) * mm});
            skLineSegment(sketch, "E2335", {"start": v(53767.63, 69757.56) * mm, "end": v(53882.8, 69756.1) * mm});
            skLineSegment(sketch, "E2336", {"start": v(53882.8, 69756.1) * mm, "end": v(53880.1, 69581.11) * mm});
            skLineSegment(sketch, "E2337", {"start": v(53880.1, 69581.11) * mm, "end": v(53880, 69581.11) * mm});
            skLineSegment(sketch, "E2338", {"start": v(53880, 69581.11) * mm, "end": v(53879.9, 69576.11) * mm});
            skLineSegment(sketch, "E2339", {"start": v(53879.9, 69576.11) * mm, "end": v(53879.65, 69556.11) * mm});
            skLineSegment(sketch, "E2340", {"start": v(53879.65, 69556.11) * mm, "end": v(53649.31, 69559.06) * mm});
            skLineSegment(sketch, "E2341", {"start": v(54600.18, 69544.98) * mm, "end": v(54589.38, 69545.15) * mm});
            skLineSegment(sketch, "E2342", {"start": v(54589.38, 69545.15) * mm, "end": v(54590, 69585.14) * mm});
            skLineSegment(sketch, "E2343", {"start": v(54590, 69585.14) * mm, "end": v(54590.24, 69585.14) * mm});
            skLineSegment(sketch, "E2344", {"start": v(54590.24, 69585.14) * mm, "end": v(54592.71, 69745.12) * mm});
            skLineSegment(sketch, "E2345", {"start": v(54592.71, 69745.12) * mm, "end": v(54718.8, 69743.17) * mm});
            skLineSegment(sketch, "E2346", {"start": v(54718.8, 69743.17) * mm, "end": v(54793.6, 69608.67) * mm});
            skLineSegment(sketch, "E2347", {"start": v(54793.6, 69608.67) * mm, "end": v(54618.83, 69511.45) * mm});
            skLineSegment(sketch, "E2348", {"start": v(54618.83, 69511.45) * mm, "end": v(54600.18, 69544.98) * mm});
            skLineSegment(sketch, "E2349", {"start": v(47368.4, 74068.2) * mm, "end": v(47349.7, 74217.02) * mm});
            skLineSegment(sketch, "E2350", {"start": v(47349.7, 74217.02) * mm, "end": v(47647.35, 74254.45) * mm});
            skLineSegment(sketch, "E2351", {"start": v(47647.35, 74254.45) * mm, "end": v(47666.06, 74105.62) * mm});
            skLineSegment(sketch, "E2352", {"start": v(47666.06, 74105.62) * mm, "end": v(47368.4, 74068.2) * mm});
            skLineSegment(sketch, "E2353", {"start": v(47666.06, 74105.62) * mm, "end": v(47349.7, 74217.02) * mm});
            skLineSegment(sketch, "E2354", {"start": v(53347.46, 61883.13) * mm, "end": v(53399.6, 61710.85) * mm});
            skLineSegment(sketch, "E2355", {"start": v(53399.6, 61710.85) * mm, "end": v(51006.78, 60986.7) * mm});
            skLineSegment(sketch, "E2356", {"start": v(51006.78, 60986.7) * mm, "end": v(50954.64, 61158.98) * mm});
            skLineSegment(sketch, "E2357", {"start": v(50954.64, 61158.98) * mm, "end": v(53347.46, 61883.13) * mm});
            skArc(sketch, "E2358", {"start": v(29137.14, 60289.37) * mm, "mid": v(29022.9, 60300.69) * mm, "end": v(28950.12, 60389.48) * mm});
            skLineSegment(sketch, "E2359", {"start": v(28950.12, 60389.48) * mm, "end": v(28614.06, 61499.74) * mm});
            skArc(sketch, "E2360", {"start": v(28614.06, 61499.74) * mm, "mid": v(28625.39, 61613.98) * mm, "end": v(28714.18, 61686.76) * mm});
            skLineSegment(sketch, "E2361", {"start": v(28714.18, 61686.76) * mm, "end": v(31456.14, 62516.7) * mm});
            skArc(sketch, "E2362", {"start": v(31456.14, 62516.7) * mm, "mid": v(31570.38, 62505.37) * mm, "end": v(31643.16, 62416.58) * mm});
            skLineSegment(sketch, "E2363", {"start": v(31643.16, 62416.58) * mm, "end": v(31979.21, 61306.33) * mm});
            skArc(sketch, "E2364", {"start": v(31979.21, 61306.33) * mm, "mid": v(31967.89, 61192.08) * mm, "end": v(31879.1, 61119.3) * mm});
            skLineSegment(sketch, "E2365", {"start": v(31879.1, 61119.3) * mm, "end": v(29137.14, 60289.37) * mm});
            skLineSegment(sketch, "E2366", {"start": v(50700.72, 66312.66) * mm, "end": v(57291.8, 44536.93) * mm});
            skLineSegment(sketch, "E2367", {"start": v(52093.19, 57397.4) * mm, "end": v(53399.6, 61710.85) * mm});
            skLineSegment(sketch, "E2368", {"start": v(54485.98, 58121.66) * mm, "end": v(51006.81, 60986.6) * mm});
            skLineSegment(sketch, "E2369", {"start": v(54621.5, 57673.95) * mm, "end": v(53399.6, 61710.85) * mm});
            skLineSegment(sketch, "E2370", {"start": v(53399.6, 61710.85) * mm, "end": v(51006.81, 60986.6) * mm});
            skLineSegment(sketch, "E2371", {"start": v(51006.81, 60986.6) * mm, "end": v(52093.19, 57397.4) * mm});
            skLineSegment(sketch, "E2372", {"start": v(52093.19, 57397.4) * mm, "end": v(54485.98, 58121.66) * mm});
            skLineSegment(sketch, "E2373", {"start": v(54485.98, 58121.66) * mm, "end": v(54621.5, 57673.95) * mm});
            skLineSegment(sketch, "E2374", {"start": v(54621.5, 57673.95) * mm, "end": v(54621.5, 57673.95) * mm});
            skLineSegment(sketch, "E2375", {"start": v(46253.87, 64965.52) * mm, "end": v(45559.41, 71574.53) * mm});
            skLineSegment(sketch, "E2376", {"start": v(49171.71, 68915.44) * mm, "end": v(44431.36, 67939.34) * mm});
            skArc(sketch, "E2377", {"start": v(46261.51, 64962.01) * mm, "mid": v(45390.76, 65567.71) * mm, "end": v(44786.65, 66439.56) * mm});
            skArc(sketch, "E2378", {"start": v(44786.65, 66439.56) * mm, "mid": v(44578.5, 66997.27) * mm, "end": v(44462.27, 67581.1) * mm});
            skArc(sketch, "E2379", {"start": v(44462.27, 67581.1) * mm, "mid": v(44427.37, 68319.4) * mm, "end": v(44504.03, 69054.56) * mm});
            skLineSegment(sketch, "E2380", {"start": v(49171.71, 68915.44) * mm, "end": v(45559.41, 71574.53) * mm});
            skEllipse(sketch, "E2381", {"center": v(56751.68, 58895.3) * mm, "majorRadius": 158.75 * mm, "minorRadius": 158.75 * mm, "majorAxis": v(1, 0)});
            skArc(sketch, "E2382", {"start": v(56599.74, 58849.3) * mm, "mid": v(56676.76, 58755.34) * mm, "end": v(56797.67, 58743.35) * mm});
            skArc(sketch, "E2383", {"start": v(56903.63, 58941.28) * mm, "mid": v(56826.6, 59035.25) * mm, "end": v(56705.7, 59047.24) * mm});
            skLineSegment(sketch, "E2384", {"start": v(56797.67, 58743.35) * mm, "end": v(56705.7, 59047.24) * mm});
            skLineSegment(sketch, "E2385", {"start": v(56903.63, 58941.28) * mm, "end": v(56599.74, 58849.3) * mm});
            skLineSegment(sketch, "E2386", {"start": v(56705.7, 59047.24) * mm, "end": v(56363.12, 60179.03) * mm});
            skCircle(sketch, "E2387", {"center": v(62196.79, 56099.65) * mm, "radius": 50 * mm});
            skCircle(sketch, "E2388", {"center": v(50636.26, 64206.64) * mm, "radius": 100 * mm});
            skCircle(sketch, "E2389", {"center": v(50407.42, 64137.38) * mm, "radius": 100 * mm});
            skCircle(sketch, "E2390", {"center": v(47731.12, 74189.4) * mm, "radius": 75 * mm});
            skCircle(sketch, "E2391", {"center": v(62687.58, 49072.55) * mm, "radius": 100 * mm});
            skCircle(sketch, "E2392", {"center": v(60371.2, 49021.4) * mm, "radius": 100 * mm});
            skCircle(sketch, "E2393", {"center": v(59790.25, 50147.73) * mm, "radius": 75 * mm});
            skCircle(sketch, "E2394", {"center": v(59616.43, 50722) * mm, "radius": 75 * mm});
            skCircle(sketch, "E2395", {"center": v(39683.35, 67406.92) * mm, "radius": 50 * mm});
            skCircle(sketch, "E2396", {"center": v(39774.14, 67342.64) * mm, "radius": 50 * mm});
            skCircle(sketch, "E2397", {"center": v(35194.2, 66751.7) * mm, "radius": 75 * mm});
            skCircle(sketch, "E2398", {"center": v(35046.3, 60696.8) * mm, "radius": 75 * mm});
            skCircle(sketch, "E2399", {"center": v(38014.69, 58141.04) * mm, "radius": 75 * mm});
            skCircle(sketch, "E2400", {"center": v(36995, 60368.56) * mm, "radius": 75 * mm});
            skLineSegment(sketch, "E2401", {"start": v(35172.48, 66823.48) * mm, "end": v(35029.54, 67295.73) * mm});
            skLineSegment(sketch, "E2402", {"start": v(35169.6, 66987.8) * mm, "end": v(35172.48, 66823.48) * mm});
            skLineSegment(sketch, "E2403", {"start": v(35172.48, 66823.48) * mm, "end": v(35087.83, 66964.36) * mm});
            skLineSegment(sketch, "E2404", {"start": v(35087.83, 66964.36) * mm, "end": v(35169.6, 66987.8) * mm});
            skLineSegment(sketch, "E2405", {"start": v(43781.44, 60419.07) * mm, "end": v(43737.99, 60562.64) * mm});
            skLineSegment(sketch, "E2406", {"start": v(43737.99, 60562.64) * mm, "end": v(44025.13, 60649.54) * mm});
            skLineSegment(sketch, "E2407", {"start": v(44025.13, 60649.54) * mm, "end": v(44068.58, 60505.98) * mm});
            skLineSegment(sketch, "E2408", {"start": v(44068.58, 60505.98) * mm, "end": v(43781.44, 60419.07) * mm});
            skLineSegment(sketch, "E2409", {"start": v(43939.7, 60623.18) * mm, "end": v(43705.55, 61396.78) * mm});
            skLineSegment(sketch, "E2410", {"start": v(43936.84, 60787.5) * mm, "end": v(43939.7, 60623.18) * mm});
            skLineSegment(sketch, "E2411", {"start": v(43939.7, 60623.18) * mm, "end": v(43855.06, 60764.06) * mm});
            skLineSegment(sketch, "E2412", {"start": v(43855.06, 60764.06) * mm, "end": v(43936.84, 60787.5) * mm});
            skCircle(sketch, "E2413", {"center": v(42046.55, 68502.37) * mm, "radius": 100 * mm});
            skCircle(sketch, "E2414", {"center": v(36489.3, 63764.07) * mm, "radius": 100 * mm});
            skLineSegment(sketch, "E2415", {"start": v(68800.03, 49613.6) * mm, "end": v(52895.98, 44799.76) * mm});
            skLineSegment(sketch, "E2416", {"start": v(64824.99, 62739.91) * mm, "end": v(48922.75, 57926.63) * mm});
            skLineSegment(sketch, "E2417", {"start": v(63051.1, 64454.54) * mm, "end": v(48298.44, 59989.21) * mm});
            skLineSegment(sketch, "E2418", {"start": v(58279.05, 77095.62) * mm, "end": v(29227.41, 73368.86) * mm});
            skLineSegment(sketch, "E2419", {"start": v(56137.88, 61183.94) * mm, "end": v(34457.3, 54621.67) * mm});
            skLineSegment(sketch, "E2420", {"start": v(53763.43, 65950.46) * mm, "end": v(32900.17, 59635.57) * mm});
            skLineSegment(sketch, "E2421", {"start": v(37800.23, 67883.79) * mm, "end": v(31024.37, 65832.87) * mm});
            skLineSegment(sketch, "E2422", {"start": v(61637.16, 69125.21) * mm, "end": v(32680.7, 60360.68) * mm});
            skLineSegment(sketch, "E2423", {"start": v(59917.1, 70856.14) * mm, "end": v(32056.39, 62423.27) * mm});
            skLineSegment(sketch, "E2424", {"start": v(58503.37, 75526.87) * mm, "end": v(30642.65, 67094) * mm});
            skLineSegment(sketch, "E2425", {"start": v(66863.03, 56006.6) * mm, "end": v(50960.79, 51193.3) * mm});
            skLineSegment(sketch, "E2426", {"start": v(67188.94, 54929.83) * mm, "end": v(51286.7, 50116.55) * mm});
            skLineSegment(sketch, "E2427", {"start": v(48161.86, 80551.5) * mm, "end": v(59147.71, 44256.2) * mm});
            skLineSegment(sketch, "E2428", {"start": v(46080.13, 79921.4) * mm, "end": v(50825.96, 64242) * mm});
            skLineSegment(sketch, "E2429", {"start": v(38710.33, 77690.7) * mm, "end": v(45197.28, 56258.97) * mm});
            skLineSegment(sketch, "E2430", {"start": v(32335.92, 75761.3) * mm, "end": v(38822.87, 54329.57) * mm});
            skLineSegment(sketch, "E2431", {"start": v(29943.13, 75037.05) * mm, "end": v(36430.08, 53605.32) * mm});
            skLineSegment(sketch, "E2432", {"start": v(67769.85, 47708.43) * mm, "end": v(50010.94, 79562.53) * mm});
            skCircle(sketch, "E2433", {"center": v(29827.25, 75419.9) * mm, "radius": 400 * mm});
            skCircle(sketch, "E2434", {"center": v(32220.04, 76144.15) * mm, "radius": 400 * mm});
            skCircle(sketch, "E2435", {"center": v(38594.44, 78073.55) * mm, "radius": 400 * mm});
            skCircle(sketch, "E2436", {"center": v(45967.29, 80305.16) * mm, "radius": 400 * mm});
            skCircle(sketch, "E2437", {"center": v(48042.95, 80933.4) * mm, "radius": 400 * mm});
            skCircle(sketch, "E2438", {"center": v(58675.8, 77146.49) * mm, "radius": 400 * mm});
            skCircle(sketch, "E2439", {"center": v(51669.85, 81022.14) * mm, "radius": 400 * mm});
            skCircle(sketch, "E2440", {"center": v(55953.69, 77875.9) * mm, "radius": 400 * mm});
            skCircle(sketch, "E2441", {"center": v(58886.21, 75642.75) * mm, "radius": 400 * mm});
            skCircle(sketch, "E2442", {"center": v(60299.95, 70972.02) * mm, "radius": 400 * mm});
            skCircle(sketch, "E2443", {"center": v(62020, 69241.1) * mm, "radius": 400 * mm});
            skCircle(sketch, "E2444", {"center": v(63433.94, 64570.42) * mm, "radius": 400 * mm});
            skCircle(sketch, "E2445", {"center": v(65207.84, 62855.8) * mm, "radius": 400 * mm});
            skCircle(sketch, "E2446", {"center": v(66621.57, 58185.06) * mm, "radius": 400 * mm});
            skCircle(sketch, "E2447", {"center": v(67245.88, 56122.47) * mm, "radius": 400 * mm});
            skCircle(sketch, "E2448", {"center": v(69182.88, 49729.47) * mm, "radius": 400 * mm});
            skCircle(sketch, "E2449", {"center": v(28686.24, 72177.64) * mm, "radius": 400 * mm});
            skCircle(sketch, "E2450", {"center": v(30641.28, 65716.92) * mm, "radius": 400 * mm});
            skCircle(sketch, "E2451", {"center": v(32515.18, 59519.04) * mm, "radius": 400 * mm});
            skCircle(sketch, "E2452", {"center": v(34071.81, 54504.99) * mm, "radius": 400 * mm});
            skCircle(sketch, "E2453", {"center": v(48987.18, 56326.68) * mm, "radius": 400 * mm});
            skCircle(sketch, "E2454", {"center": v(49399.16, 79054.72) * mm, "radius": 400 * mm});
            skLineSegment(sketch, "E2455", {"start": v(36305.06, 74483.7) * mm, "end": v(29069.58, 72293.67) * mm});
            skLineSegment(sketch, "E2456", {"start": v(66238.73, 58069.18) * mm, "end": v(50336.48, 53255.9) * mm});
            skLineSegment(sketch, "E2457", {"start": v(53375.44, 75865.5) * mm, "end": v(51312.22, 74715.25) * mm});
            skLineSegment(sketch, "E2458", {"start": v(51499.4, 78348.17) * mm, "end": v(51983.24, 74576.36) * mm});
            skLineSegment(sketch, "E2459", {"start": v(35636.54, 59235.4) * mm, "end": v(51432.72, 80700.01) * mm});
            skLineSegment(sketch, "E2460", {"start": v(39916.94, 56084.63) * mm, "end": v(55716.5, 77553.82) * mm});
            skCircle(sketch, "E2461", {"center": v(67571.79, 55045.71) * mm, "radius": 400 * mm});
            skCircle(sketch, "E2462", {"center": v(65653.83, 61371.34) * mm, "radius": 400 * mm});
            skCircle(sketch, "E2463", {"center": v(63682.27, 63752.25) * mm, "radius": 400 * mm});
            skLineSegment(sketch, "E2464", {"start": v(65270.99, 61255.46) * mm, "end": v(49371.78, 56443.1) * mm});
            skCircle(sketch, "E2465", {"center": v(57407.68, 44154.09) * mm, "radius": 400 * mm});
            skCircle(sketch, "E2466", {"center": v(54584.18, 43299.47) * mm, "radius": 400 * mm});
            skCircle(sketch, "E2467", {"center": v(67964.63, 47359.05) * mm, "radius": 400 * mm});
            skLineSegment(sketch, "E2468", {"start": v(54468.58, 43682.4) * mm, "end": v(49533.34, 59987.56) * mm});
            skLineSegment(sketch, "E2469", {"start": v(67004.16, 47476.67) * mm, "end": v(49593.94, 78705.35) * mm});
            skCircle(sketch, "E2470", {"center": v(49816.16, 79911.9) * mm, "radius": 400 * mm});
            skCircle(sketch, "E2471", {"center": v(67198.94, 47127.3) * mm, "radius": 400 * mm});
            skLineSegment(sketch, "E2472", {"start": v(63299.42, 63636.4) * mm, "end": v(48546.14, 59170.88) * mm});
            skSolve(sketch);
        }
        {
            var Q0;
            Q0=makeQuery(id+"F2.opExtrude","CAP_FACE",FACE,{"disambiguationData":[OSD([sQuery(id+"F1.wireOp",EDGE,"E1119.4"),sQuery(id+"F1.wireOp",EDGE,"E1119.5"),sQuery(id+"F1.wireOp",EDGE,"E1119.6"),sQuery(id+"F1.wireOp",EDGE,"E1119.7"),sQuery(id+"F1.wireOp",EDGE,"E1120.3"),sQuery(id+"F1.wireOp",EDGE,"E1121.0"),sQuery(id+"F1.wireOp",EDGE,"E1121.1"),sQuery(id+"F1.wireOp",EDGE,"E1121.2"),sQuery(id+"F1.wireOp",EDGE,"E1121.3"),sQuery(id+"F1.wireOp",EDGE,"E1121.4"),sQuery(id+"F1.wireOp",EDGE,"E1121.5"),sQuery(id+"F1.wireOp",EDGE,"E1121.6"),sQuery(id+"F1.wireOp",EDGE,"E1121.7"),sQuery(id+"F1.wireOp",EDGE,"E1121.9"),sQuery(id+"F1.wireOp",EDGE,"E1121.10"),sQuery(id+"F1.wireOp",EDGE,"E1121.11"),sQuery(id+"F1.wireOp",EDGE,"E1122"),sQuery(id+"F1.wireOp",EDGE,"E1123.0"),sQuery(id+"F1.wireOp",EDGE,"E1123.4"),sQuery(id+"F1.wireOp",EDGE,"E1123.5"),sQuery(id+"F1.wireOp",EDGE,"E1123.6"),sQuery(id+"F1.wireOp",EDGE,"E1123.7"),sQuery(id+"F1.wireOp",EDGE,"E1123.8"),sQuery(id+"F1.wireOp",EDGE,"E1123.9"),sQuery(id+"F1.wireOp",EDGE,"E1123.10"),sQuery(id+"F1.wireOp",EDGE,"E1124.0"),sQuery(id+"F1.wireOp",EDGE,"E1124.1"),sQuery(id+"F1.wireOp",EDGE,"E1124.2"),sQuery(id+"F1.wireOp",EDGE,"E1124.3"),sQuery(id+"F1.wireOp",EDGE,"E1125.0"),sQuery(id+"F1.wireOp",EDGE,"E1125.1"),sQuery(id+"F1.wireOp",EDGE,"E1125.2"),sQuery(id+"F1.wireOp",EDGE,"E1125.3"),sQuery(id+"F1.wireOp",EDGE,"E1126.0"),sQuery(id+"F1.wireOp",EDGE,"E1126.1"),sQuery(id+"F1.wireOp",EDGE,"E1126.2"),sQuery(id+"F1.wireOp",EDGE,"E1126.3"),sQuery(id+"F1.wireOp",EDGE,"E1127.0"),sQuery(id+"F1.wireOp",EDGE,"E1127.1"),sQuery(id+"F1.wireOp",EDGE,"E1127.2"),sQuery(id+"F1.wireOp",EDGE,"E1127.3"),sQuery(id+"F1.wireOp",EDGE,"E1128.0"),sQuery(id+"F1.wireOp",EDGE,"E1128.1"),sQuery(id+"F1.wireOp",EDGE,"E1128.2"),sQuery(id+"F1.wireOp",EDGE,"E1128.3"),sQuery(id+"F1.wireOp",EDGE,"E1128.4"),sQuery(id+"F1.wireOp",EDGE,"E1129.0"),sQuery(id+"F1.wireOp",EDGE,"E1129.1"),sQuery(id+"F1.wireOp",EDGE,"E1129.2"),sQuery(id+"F1.wireOp",EDGE,"E1129.3"),sQuery(id+"F1.wireOp",EDGE,"E1129.4"),sQuery(id+"F1.wireOp",EDGE,"E1129.5"),sQuery(id+"F1.wireOp",EDGE,"E1129.6"),sQuery(id+"F1.wireOp",EDGE,"E1129.7"),sQuery(id+"F1.wireOp",EDGE,"E1129.8"),sQuery(id+"F1.wireOp",EDGE,"E1129.9"),sQuery(id+"F1.wireOp",EDGE,"E1129.10"),sQuery(id+"F1.wireOp",EDGE,"E1130.0"),sQuery(id+"F1.wireOp",EDGE,"E1130.1"),sQuery(id+"F1.wireOp",EDGE,"E1130.2"),sQuery(id+"F1.wireOp",EDGE,"E1131"),sQuery(id+"F1.wireOp",EDGE,"E1132.0"),sQuery(id+"F1.wireOp",EDGE,"E1132.1"),sQuery(id+"F1.wireOp",EDGE,"E1132.2"),sQuery(id+"F1.wireOp",EDGE,"E1132.3"),sQuery(id+"F1.wireOp",EDGE,"E1132.4"),sQuery(id+"F1.wireOp",EDGE,"E1132.5"),sQuery(id+"F1.wireOp",EDGE,"E1133.0"),sQuery(id+"F1.wireOp",EDGE,"E1133.1"),sQuery(id+"F1.wireOp",EDGE,"E1133.2"),sQuery(id+"F1.wireOp",EDGE,"E1133.3"),sQuery(id+"F1.wireOp",EDGE,"E1134.0"),sQuery(id+"F1.wireOp",EDGE,"E1134.1"),sQuery(id+"F1.wireOp",EDGE,"E1134.2"),sQuery(id+"F1.wireOp",EDGE,"E1134.3"),sQuery(id+"F1.wireOp",EDGE,"E1136"),sQuery(id+"F1.wireOp",EDGE,"E1137.0.1.0"),sQuery(id+"F1.wireOp",EDGE,"E1137.0.2.0"),sQuery(id+"F1.wireOp",EDGE,"E1137.0.3.0"),sQuery(id+"F1.wireOp",EDGE,"E1138.0"),sQuery(id+"F1.wireOp",EDGE,"E1138.1"),sQuery(id+"F1.wireOp",EDGE,"E1138.2"),sQuery(id+"F1.wireOp",EDGE,"E1138.3"),sQuery(id+"F1.wireOp",EDGE,"E1139.0"),sQuery(id+"F1.wireOp",EDGE,"E1139.1"),sQuery(id+"F1.wireOp",EDGE,"E1139.2"),sQuery(id+"F1.wireOp",EDGE,"E1139.3"),sQuery(id+"F1.wireOp",EDGE,"E1140"),sQuery(id+"F1.wireOp",EDGE,"E1141"),sQuery(id+"F1.wireOp",EDGE,"E1142")])],"isStart":false});
            var sketch = newSketch(context, id + "F6", { "sketchPlane" : qUnion([Q0])});
            skLineSegment(sketch, "E2473.0", {"start": v(41611.2, 67103.98) * mm, "end": v(41369.6, 67281.8) * mm});
            skLineSegment(sketch, "E2473.1", {"start": v(41611.2, 67103.98) * mm, "end": v(42174.33, 67869.09) * mm});
            skLineSegment(sketch, "E2473.2", {"start": v(42174.33, 67869.09) * mm, "end": v(41932.72, 68046.92) * mm});
            skLineSegment(sketch, "E2473.3", {"start": v(41369.6, 67281.8) * mm, "end": v(41932.72, 68046.92) * mm});
            skLineSegment(sketch, "E2473.4", {"start": v(38841.66, 63847.55) * mm, "end": v(39375.14, 64572.39) * mm});
            skLineSegment(sketch, "E2473.5", {"start": v(39616.76, 64394.56) * mm, "end": v(39375.14, 64572.39) * mm});
            skLineSegment(sketch, "E2473.6", {"start": v(39083.27, 63669.72) * mm, "end": v(39616.76, 64394.56) * mm});
            skLineSegment(sketch, "E2473.7", {"start": v(39083.27, 63669.72) * mm, "end": v(38841.66, 63847.55) * mm});
            skLineSegment(sketch, "E2473.8", {"start": v(34646.67, 67032.26) * mm, "end": v(35364.5, 67249.58) * mm});
            skLineSegment(sketch, "E2473.9", {"start": v(34733.6, 66745.13) * mm, "end": v(34646.67, 67032.26) * mm});
            skLineSegment(sketch, "E2473.10", {"start": v(35451.43, 66962.45) * mm, "end": v(35364.5, 67249.58) * mm});
            skLineSegment(sketch, "E2473.11", {"start": v(34733.6, 66745.13) * mm, "end": v(35451.43, 66962.45) * mm});
            skLineSegment(sketch, "E2474.0", {"start": v(52380.65, 73984.06) * mm, "end": v(52648.5, 73503.69) * mm});
            skLineSegment(sketch, "E2474.1", {"start": v(52162.3, 73862.3) * mm, "end": v(52380.65, 73984.06) * mm});
            skLineSegment(sketch, "E2474.2", {"start": v(52430.15, 73381.94) * mm, "end": v(52648.5, 73503.69) * mm});
            skPoint(sketch, "E2474.3", {"position": v(52271.48, 73923.18) * mm});
            skLineSegment(sketch, "E2475.0", {"start": v(49601.8, 74661.76) * mm, "end": v(49677.77, 74066.6) * mm});
            skLineSegment(sketch, "E2475.1", {"start": v(49380.19, 74028.6) * mm, "end": v(49304.21, 74623.77) * mm});
            skLineSegment(sketch, "E2475.2", {"start": v(49304.21, 74623.77) * mm, "end": v(49601.8, 74661.76) * mm});
            skLineSegment(sketch, "E2475.3", {"start": v(49677.77, 74066.6) * mm, "end": v(49380.19, 74028.6) * mm});
            skLineSegment(sketch, "E2475.4", {"start": v(49697.18, 72335.11) * mm, "end": v(49895.57, 72360.44) * mm});
            skLineSegment(sketch, "E2475.5", {"start": v(49814.94, 71412.6) * mm, "end": v(49697.18, 72335.11) * mm});
            skLineSegment(sketch, "E2475.6", {"start": v(50013.33, 71437.92) * mm, "end": v(49814.94, 71412.6) * mm});
            skPoint(sketch, "E2475.7", {"position": v(49796.38, 72347.77) * mm});
            skLineSegment(sketch, "E2476", {"start": v(49895.57, 72360.44) * mm, "end": v(50013.33, 71437.92) * mm});
            skLineSegment(sketch, "E2477", {"start": v(52162.3, 73862.3) * mm, "end": v(52430.15, 73381.94) * mm});
            skLineSegment(sketch, "E2478.0", {"start": v(50876.96, 69893.63) * mm, "end": v(51120.46, 69456.93) * mm});
            skLineSegment(sketch, "E2478.1", {"start": v(51120.46, 69456.93) * mm, "end": v(50687.7, 69215.63) * mm});
            skLineSegment(sketch, "E2478.2", {"start": v(50687.7, 69215.63) * mm, "end": v(50444.2, 69652.33) * mm});
            skLineSegment(sketch, "E2478.3", {"start": v(50444.2, 69652.33) * mm, "end": v(50876.96, 69893.63) * mm});
            skLineSegment(sketch, "E2478.4", {"start": v(53838.91, 64580.88) * mm, "end": v(53406.43, 64339.73) * mm});
            skLineSegment(sketch, "E2478.5", {"start": v(53162.93, 64776.44) * mm, "end": v(53595.41, 65017.58) * mm});
            skLineSegment(sketch, "E2478.6", {"start": v(53406.43, 64339.73) * mm, "end": v(53162.93, 64776.44) * mm});
            skLineSegment(sketch, "E2478.7", {"start": v(53595.41, 65017.58) * mm, "end": v(53838.91, 64580.88) * mm});
            skLineSegment(sketch, "E2479.0", {"start": v(56736.2, 59370.28) * mm, "end": v(56309.87, 59132.57) * mm});
            skLineSegment(sketch, "E2479.1", {"start": v(56309.87, 59132.57) * mm, "end": v(56066.37, 59569.28) * mm});
            skLineSegment(sketch, "E2479.2", {"start": v(56066.37, 59569.28) * mm, "end": v(56492.7, 59806.99) * mm});
            skLineSegment(sketch, "E2479.3", {"start": v(56492.7, 59806.99) * mm, "end": v(56736.2, 59370.28) * mm});
            skLineSegment(sketch, "E2480.0", {"start": v(59081.7, 55163.75) * mm, "end": v(58655.38, 54926.04) * mm});
            skLineSegment(sketch, "E2480.1", {"start": v(58655.38, 54926.04) * mm, "end": v(58411.88, 55362.74) * mm});
            skLineSegment(sketch, "E2480.2", {"start": v(58411.88, 55362.74) * mm, "end": v(58838.2, 55600.45) * mm});
            skLineSegment(sketch, "E2480.3", {"start": v(58838.2, 55600.45) * mm, "end": v(59081.7, 55163.75) * mm});
            skLineSegment(sketch, "E2480.4", {"start": v(61212.6, 51342.09) * mm, "end": v(61456.1, 50905.39) * mm});
            skLineSegment(sketch, "E2480.5", {"start": v(60786.28, 51104.38) * mm, "end": v(61212.6, 51342.09) * mm});
            skLineSegment(sketch, "E2480.6", {"start": v(61456.1, 50905.39) * mm, "end": v(61029.78, 50667.68) * mm});
            skLineSegment(sketch, "E2480.7", {"start": v(61029.78, 50667.68) * mm, "end": v(60786.28, 51104.38) * mm});
            skSolve(sketch);
        }
        {
            var Q0;
            Q0 = qSketchRegion(id + "F6", true);
            extrude(context, id + "F7", {"entities" : qUnion([Q0]), "operationType" : NewBodyOperationType.ADD, "depth" : 2680 * mm, "offsetDistance" : 25 * mm});
        }
        {
            var Q0;
            Q0=makeQuery(id+"F4.opExtrude","CAP_FACE",FACE,{"disambiguationData":[OSD([sQuery(id+"F3.wireOp",EDGE,"E1150.0"),sQuery(id+"F3.wireOp",EDGE,"E1150.1"),sQuery(id+"F3.wireOp",EDGE,"E1150.2"),sQuery(id+"F3.wireOp",EDGE,"E1150.3"),sQuery(id+"F3.wireOp",EDGE,"E1150.4"),sQuery(id+"F3.wireOp",EDGE,"E1150.5"),sQuery(id+"F3.wireOp",EDGE,"E1150.6"),sQuery(id+"F3.wireOp",EDGE,"E1150.7"),sQuery(id+"F3.wireOp",EDGE,"E1150.8"),sQuery(id+"F3.wireOp",EDGE,"E1150.9"),sQuery(id+"F3.wireOp",EDGE,"E1150.10"),sQuery(id+"F3.wireOp",EDGE,"E1150.11"),sQuery(id+"F3.wireOp",EDGE,"E1152.0"),sQuery(id+"F3.wireOp",EDGE,"E1152.1"),sQuery(id+"F3.wireOp",EDGE,"E1153"),sQuery(id+"F3.wireOp",EDGE,"E1154"),sQuery(id+"F3.wireOp",EDGE,"E1155"),sQuery(id+"F3.wireOp",EDGE,"E1156"),sQuery(id+"F3.wireOp",EDGE,"E1157"),sQuery(id+"F3.wireOp",EDGE,"E1158")])],"isStart":false});
            var sketch = newSketch(context, id + "F8", { "sketchPlane" : qUnion([Q0])});
            skLineSegment(sketch, "E2481.0", {"start": v(53564.5, 76178.39) * mm, "end": v(29657.7, 73111.61) * mm});
            skLineSegment(sketch, "E2481.1", {"start": v(68188.43, 49622.94) * mm, "end": v(53564.5, 76178.39) * mm});
            skLineSegment(sketch, "E2481.2", {"start": v(68188.43, 49622.94) * mm, "end": v(67662.85, 49333.51) * mm});
            skLineSegment(sketch, "E2482.0", {"start": v(67446.81, 49725.81) * mm, "end": v(53744.87, 45578.51) * mm});
            skLineSegment(sketch, "E2482.1", {"start": v(67662.85, 49333.51) * mm, "end": v(67446.81, 49725.81) * mm});
            skLineSegment(sketch, "E2483.0", {"start": v(53744.87, 45578.51) * mm, "end": v(49699.07, 58945.12) * mm});
            skLineSegment(sketch, "E2483.1", {"start": v(49699.07, 58945.12) * mm, "end": v(44495.22, 57370.06) * mm});
            skLineSegment(sketch, "E2483.2", {"start": v(44495.22, 57370.06) * mm, "end": v(44744.96, 57481.26) * mm});
            skLineSegment(sketch, "E2483.3", {"start": v(39664.46, 55943.5) * mm, "end": v(44744.96, 57481.26) * mm});
            skLineSegment(sketch, "E2483.4", {"start": v(40724.12, 52442.55) * mm, "end": v(39664.46, 55943.5) * mm});
            skLineSegment(sketch, "E2483.5", {"start": v(36317.52, 51108.76) * mm, "end": v(40724.12, 52442.55) * mm});
            skLineSegment(sketch, "E2484.0", {"start": v(35463.94, 58934.57) * mm, "end": v(38413.86, 56763.64) * mm});
            skLineSegment(sketch, "E2485.0", {"start": v(36984.58, 52356.66) * mm, "end": v(35054.35, 58812.1) * mm});
            skPoint(sketch, "E2486.orphan", {"position": v(31027.58, 72279.15) * mm});
            skPoint(sketch, "E2487.orphan", {"position": v(34858.83, 59379.88) * mm});
            skLineSegment(sketch, "E2488.0", {"start": v(36984.58, 52356.66) * mm, "end": v(39517.02, 53123.18) * mm});
            skLineSegment(sketch, "E2488.1", {"start": v(39517.02, 53123.18) * mm, "end": v(38457.33, 56624.2) * mm});
            skLineSegment(sketch, "E2489", {"start": v(38413.86, 56763.64) * mm, "end": v(38457.33, 56624.2) * mm});
            skLineSegment(sketch, "E2490", {"start": v(36317.52, 51108.76) * mm, "end": v(32803.5, 50045.14) * mm});
            skLineSegment(sketch, "E2491", {"start": v(32803.5, 50045.14) * mm, "end": v(26143.67, 72047.99) * mm});
            skLineSegment(sketch, "E2492", {"start": v(29657.7, 73111.61) * mm, "end": v(26143.67, 72047.99) * mm});
            skLineSegment(sketch, "E2493", {"start": v(35054.35, 58812.1) * mm, "end": v(36101.64, 59125.24) * mm});
            skLineSegment(sketch, "E2494.0", {"start": v(48028.73, 63543.32) * mm, "end": v(47898.37, 63974.02) * mm});
            skLineSegment(sketch, "E2494.1", {"start": v(47898.37, 63974.02) * mm, "end": v(51257.9, 64990.82) * mm});
            skLineSegment(sketch, "E2494.2", {"start": v(51388.26, 64560.11) * mm, "end": v(48028.73, 63543.32) * mm});
            skLineSegment(sketch, "E2494.3", {"start": v(51257.9, 64990.82) * mm, "end": v(51388.26, 64560.11) * mm});
            skLineSegment(sketch, "E2494.4", {"start": v(49336.5, 64864.07) * mm, "end": v(50006.48, 65066.83) * mm});
            skLineSegment(sketch, "E2494.5", {"start": v(50041.24, 64951.98) * mm, "end": v(49371.25, 64749.21) * mm});
            skLineSegment(sketch, "E2494.6", {"start": v(50006.48, 65066.83) * mm, "end": v(50041.24, 64951.98) * mm});
            skLineSegment(sketch, "E2494.7", {"start": v(49371.25, 64749.21) * mm, "end": v(49336.5, 64864.07) * mm});
            skLineSegment(sketch, "E2495.0", {"start": v(50734.53, 66072.4) * mm, "end": v(49929.2, 66665.23) * mm});
            skLineSegment(sketch, "E2495.1", {"start": v(50000.02, 66762.1) * mm, "end": v(50807.1, 66172.13) * mm});
            skLineSegment(sketch, "E2495.2", {"start": v(49929.2, 66665.23) * mm, "end": v(50000.34, 66761.87) * mm});
            skLineSegment(sketch, "E2495.3", {"start": v(50805.67, 66169.05) * mm, "end": v(50734.53, 66072.4) * mm});
            skLineSegment(sketch, "E2496.0", {"start": v(49171.71, 68915.44) * mm, "end": v(45559.41, 71574.53) * mm});
            skLineSegment(sketch, "E2496.1", {"start": v(49171.71, 68915.44) * mm, "end": v(46261.51, 64962.01) * mm});
            skArc(sketch, "E2496.2", {"start": v(46261.51, 64962.01) * mm, "mid": v(45571.88, 65400.69) * mm, "end": v(45027.16, 66010.05) * mm});
            skArc(sketch, "E2496.3", {"start": v(45027.16, 66010.05) * mm, "mid": v(44701.21, 66634.86) * mm, "end": v(44503.26, 67311.2) * mm});
            skArc(sketch, "E2496.4", {"start": v(44786.65, 66439.56) * mm, "mid": v(44578.5, 66997.27) * mm, "end": v(44462.27, 67581.1) * mm});
            skArc(sketch, "E2496.5", {"start": v(44503.26, 67311.2) * mm, "mid": v(44425.4, 68182.91) * mm, "end": v(44504.03, 69054.56) * mm});
            skArc(sketch, "E2496.6", {"start": v(44504.03, 69054.56) * mm, "mid": v(44896.73, 70371.08) * mm, "end": v(45559.41, 71574.53) * mm});
            skSolve(sketch);
        }
        {
            var Q0;
            Q0 = qSketchRegion(id + "F8", true);
            var Q1;
            Q1 = qSketchRegion(id + "F10", true);
            extrude(context, id + "F9", {"entities" : qUnion([Q0, Q1]), "depth" : 300 * mm, "offsetDistance" : 25 * mm});
        }
        {
            var Q0;
            Q0=makeQuery(id+"F9.opExtrude","CAP_FACE",FACE,{"disambiguationData":[OSD([sQuery(id+"F8.wireOp",EDGE,"E2481.0"),sQuery(id+"F8.wireOp",EDGE,"E2481.1"),sQuery(id+"F8.wireOp",EDGE,"E2481.2"),sQuery(id+"F8.wireOp",EDGE,"E2482.0"),sQuery(id+"F8.wireOp",EDGE,"E2482.1"),sQuery(id+"F8.wireOp",EDGE,"E2483.0"),sQuery(id+"F8.wireOp",EDGE,"E2483.1"),sQuery(id+"F8.wireOp",EDGE,"E2483.2"),sQuery(id+"F8.wireOp",EDGE,"E2483.3"),sQuery(id+"F8.wireOp",EDGE,"E2483.4"),sQuery(id+"F8.wireOp",EDGE,"E2483.5"),sQuery(id+"F8.wireOp",EDGE,"E2483.6")])],"isStart":false});
            var sketch = newSketch(context, id + "F10", { "sketchPlane" : qUnion([Q0])});
            skLineSegment(sketch, "E2497.0", {"start": v(36317.52, 51108.76) * mm, "end": v(40724.12, 52442.55) * mm});
            skLineSegment(sketch, "E2497.1", {"start": v(40724.12, 52442.55) * mm, "end": v(39664.46, 55943.5) * mm});
            skLineSegment(sketch, "E2497.2", {"start": v(29657.7, 73111.61) * mm, "end": v(30424.93, 70576.85) * mm});
            skLineSegment(sketch, "E2497.3", {"start": v(39664.46, 55943.5) * mm, "end": v(44744.96, 57481.26) * mm});
            skLineSegment(sketch, "E2497.4", {"start": v(44495.22, 57370.06) * mm, "end": v(44744.96, 57481.26) * mm});
            skLineSegment(sketch, "E2497.5", {"start": v(49699.07, 58945.12) * mm, "end": v(44495.22, 57370.06) * mm});
            skLineSegment(sketch, "E2497.6", {"start": v(53744.87, 45578.51) * mm, "end": v(49699.07, 58945.12) * mm});
            skLineSegment(sketch, "E2497.7", {"start": v(67446.81, 49725.81) * mm, "end": v(53744.87, 45578.51) * mm});
            skLineSegment(sketch, "E2497.8", {"start": v(67662.85, 49333.51) * mm, "end": v(67446.81, 49725.81) * mm});
            skLineSegment(sketch, "E2497.9", {"start": v(68188.43, 49622.94) * mm, "end": v(67662.85, 49333.51) * mm});
            skLineSegment(sketch, "E2497.10", {"start": v(68188.43, 49622.94) * mm, "end": v(53564.5, 76178.39) * mm});
            skLineSegment(sketch, "E2497.11", {"start": v(53564.5, 76178.39) * mm, "end": v(29657.7, 73111.61) * mm});
            skLineSegment(sketch, "E2497.12", {"start": v(32831.65, 66077.32) * mm, "end": v(32898.61, 66097.6) * mm});
            skPoint(sketch, "E2497.13", {"position": v(32865.13, 66087.46) * mm});
            skLineSegment(sketch, "E2497.14", {"start": v(39517.02, 53123.18) * mm, "end": v(38457.33, 56624.2) * mm});
            skLineSegment(sketch, "E2497.15", {"start": v(36984.58, 52356.66) * mm, "end": v(39517.02, 53123.18) * mm});
            skLineSegment(sketch, "E2497.16", {"start": v(54412.26, 46825.25) * mm, "end": v(50354.93, 60230) * mm});
            skLineSegment(sketch, "E2497.17", {"start": v(38457.33, 56624.2) * mm, "end": v(50354.93, 60230) * mm});
            skLineSegment(sketch, "E2497.18", {"start": v(36984.58, 52356.66) * mm, "end": v(31027.58, 72279.15) * mm});
            skLineSegment(sketch, "E2497.19", {"start": v(31027.58, 72279.15) * mm, "end": v(52857.63, 75079.51) * mm});
            skLineSegment(sketch, "E2497.20", {"start": v(54412.26, 46825.25) * mm, "end": v(66562.27, 50502.76) * mm});
            skLineSegment(sketch, "E2497.21", {"start": v(52857.63, 75079.51) * mm, "end": v(66562.27, 50502.76) * mm});
            skLineSegment(sketch, "E2498.0", {"start": v(37800.23, 67883.79) * mm, "end": v(31024.37, 65832.87) * mm, "construction": true});
            skLineSegment(sketch, "E2499", {"start": v(31896.32, 65715.64) * mm, "end": v(29301.63, 64930.28) * mm});
            skLineSegment(sketch, "E2500", {"start": v(29301.63, 64930.28) * mm, "end": v(27830.24, 69791.5) * mm});
            skLineSegment(sketch, "E2501", {"start": v(27830.24, 69791.5) * mm, "end": v(30424.93, 70576.85) * mm});
            skLineSegment(sketch, "E2502.trimOffspring", {"start": v(31896.32, 65715.64) * mm, "end": v(36317.52, 51108.76) * mm});
            skLineSegment(sketch, "E2503.0", {"start": v(28316.5, 69531.2) * mm, "end": v(30537.91, 70203.58) * mm});
            skLineSegment(sketch, "E2503.1", {"start": v(29561.93, 65416.54) * mm, "end": v(28316.5, 69531.2) * mm});
            skLineSegment(sketch, "E2503.2", {"start": v(31783.34, 66088.92) * mm, "end": v(29561.93, 65416.54) * mm});
            skLineSegment(sketch, "E2504", {"start": v(31783.34, 66088.92) * mm, "end": v(30537.91, 70203.58) * mm});
            skSolve(sketch);
        }
        {
            var Q0;
            Q0 = qSketchRegion(id + "F10", true);
            extrude(context, id + "F11", {"entities" : qUnion([Q0]), "operationType" : NewBodyOperationType.ADD, "depth" : 4000 * mm, "offsetDistance" : 25 * mm});
        }
        {
            var Q0;
            Q0=makeQuery(id+"F11.boolean.opBoolean","MERGE",FACE,{"derivedFrom":[makeQuery(id+"F9.boolean.opBoolean","MERGE",FACE,{"derivedFrom":[makeQuery(id+"F4.opExtrude","SWEPT_FACE",FACE,{"disambiguationData":[OSD([sQuery(id+"F3.wireOp",EDGE,"E1155")])]}),makeQuery(id+"F9.opExtrude","SWEPT_FACE",FACE,{"disambiguationData":[OSD([sQuery(id+"F8.wireOp",EDGE,"E2485.0")])]})]}),makeQuery(id+"F11.opExtrude","SWEPT_FACE",FACE,{"disambiguationData":[OSD([sQuery(id+"F10.wireOp",EDGE,"E2497.18")])]})]});
            var sketch = newSketch(context, id + "F12", { "sketchPlane" : qUnion([Q0])});
            skLineSegment(sketch, "E2505.bottom", {"start": v(45936.42, 4705) * mm, "end": v(45436.42, 4705) * mm});
            skLineSegment(sketch, "E2505.top", {"start": v(45936.42, 5205) * mm, "end": v(45436.42, 5205) * mm});
            skLineSegment(sketch, "E2505.left", {"start": v(45936.42, 4705) * mm, "end": v(45936.42, 5205) * mm});
            skLineSegment(sketch, "E2505.right", {"start": v(45436.42, 4705) * mm, "end": v(45436.42, 5205) * mm});
            skLineSegment(sketch, "E2506.1.0.0", {"start": v(45136.42, 5205) * mm, "end": v(44636.42, 5205) * mm});
            skLineSegment(sketch, "E2506.1.0.1", {"start": v(45136.42, 4705) * mm, "end": v(45136.42, 5205) * mm});
            skLineSegment(sketch, "E2506.1.0.2", {"start": v(45136.42, 4705) * mm, "end": v(44636.42, 4705) * mm});
            skLineSegment(sketch, "E2506.1.0.3", {"start": v(44636.42, 4705) * mm, "end": v(44636.42, 5205) * mm});
            skLineSegment(sketch, "E2506.direction1", {"start": v(45436.42, 4705) * mm, "end": v(44636.42, 4705) * mm, "construction": true});
            skSolve(sketch);
        }
        {
            var Q0;
            Q0=qCreatedBy(makeId("Top.planeOp"),FACE);
            var sketch = newSketch(context, id + "F13", { "sketchPlane" : qUnion([Q0])});
            skLineSegment(sketch, "E2507", {"start": v(36671.54, 56289.56) * mm, "end": v(37404.48, 56508.72) * mm});
            skLineSegment(sketch, "E2508", {"start": v(37404.48, 56508.72) * mm, "end": v(37759.7, 55320.69) * mm});
            skLineSegment(sketch, "E2509", {"start": v(37759.7, 55320.69) * mm, "end": v(37026.77, 55101.53) * mm});
            skLineSegment(sketch, "E2510", {"start": v(36671.54, 56289.56) * mm, "end": v(37026.77, 55101.53) * mm});
            skSolve(sketch);
        }
        {
            var Q0;
            Q0 = qSketchRegion(id + "F13", true);
            extrude(context, id + "F14", {"entities" : qUnion([Q0]), "depth" : 1900 * mm, "offsetDistance" : 25 * mm});
        }
        {
            var Q0;
            Q0 = qSketchRegion(id + "F12", true);
            extrude(context, id + "F15", {"entities" : qUnion([Q0]), "operationType" : NewBodyOperationType.REMOVE, "endBound" : BoundingType.THROUGH_ALL, "oppositeDirection" : true, "depth" : 25 * mm, "offsetDistance" : 25 * mm});
        }
        {
            var Q0;
            Q0=makeQuery(id+"F9.opExtrude","CAP_FACE",FACE,{"disambiguationData":[OSD([sQuery(id+"F8.wireOp",EDGE,"E2481.0"),sQuery(id+"F8.wireOp",EDGE,"E2481.1"),sQuery(id+"F8.wireOp",EDGE,"E2481.2"),sQuery(id+"F8.wireOp",EDGE,"E2482.0"),sQuery(id+"F8.wireOp",EDGE,"E2482.1"),sQuery(id+"F8.wireOp",EDGE,"E2483.0"),sQuery(id+"F8.wireOp",EDGE,"E2483.1"),sQuery(id+"F8.wireOp",EDGE,"E2483.2"),sQuery(id+"F8.wireOp",EDGE,"E2483.3"),sQuery(id+"F8.wireOp",EDGE,"E2483.4"),sQuery(id+"F8.wireOp",EDGE,"E2483.5"),sQuery(id+"F8.wireOp",EDGE,"E2484.0"),sQuery(id+"F8.wireOp",EDGE,"E2485.0"),sQuery(id+"F8.wireOp",EDGE,"E2488.0"),sQuery(id+"F8.wireOp",EDGE,"E2488.1"),sQuery(id+"F8.wireOp",EDGE,"E2489"),sQuery(id+"F8.wireOp",EDGE,"E2490"),sQuery(id+"F8.wireOp",EDGE,"E2491"),sQuery(id+"F8.wireOp",EDGE,"E2492"),sQuery(id+"F8.wireOp",EDGE,"E2493"),sQuery(id+"F8.wireOp",EDGE,"E2494.0"),sQuery(id+"F8.wireOp",EDGE,"E2494.1"),sQuery(id+"F8.wireOp",EDGE,"E2494.2"),sQuery(id+"F8.wireOp",EDGE,"E2494.3"),sQuery(id+"F8.wireOp",EDGE,"E2496.0"),sQuery(id+"F8.wireOp",EDGE,"E2496.1"),sQuery(id+"F8.wireOp",EDGE,"E2496.2"),sQuery(id+"F8.wireOp",EDGE,"E2496.3"),sQuery(id+"F8.wireOp",EDGE,"E2496.4"),sQuery(id+"F8.wireOp",EDGE,"E2496.5"),sQuery(id+"F8.wireOp",EDGE,"E2496.6")])],"isStart":false});
            var sketch = newSketch(context, id + "F16", { "sketchPlane" : qUnion([Q0])});
            skLineSegment(sketch, "E2511.0", {"start": v(47935.78, 63954) * mm, "end": v(51237.88, 64953.41) * mm, "construction": true});
            skLineSegment(sketch, "E2511.1", {"start": v(48048.75, 63580.72) * mm, "end": v(47935.78, 63954) * mm, "construction": true});
            skLineSegment(sketch, "E2511.2", {"start": v(51350.85, 64580.13) * mm, "end": v(48048.75, 63580.72) * mm, "construction": true});
            skLineSegment(sketch, "E2511.3", {"start": v(51237.88, 64953.41) * mm, "end": v(51350.85, 64580.13) * mm, "construction": true});
            skCircle(sketch, "E2512", {"center": v(51078.32, 64790.2) * mm, "radius": 12.5 * mm});
            skCircle(sketch, "E2513", {"center": v(50867.75, 64726.46) * mm, "radius": 25 * mm});
            skLineSegment(sketch, "E2514.0", {"start": v(47950.26, 63906.14) * mm, "end": v(51252.36, 64905.56) * mm, "construction": true});
            skCircle(sketch, "E2515", {"center": v(50417.9, 64590.31) * mm, "radius": 57.5 * mm});
            skCircle(sketch, "E2516", {"center": v(50207.34, 64526.58) * mm, "radius": 37.5 * mm});
            skCircle(sketch, "E2517", {"center": v(49968.05, 64454.16) * mm, "radius": 37.5 * mm});
            skCircle(sketch, "E2518", {"center": v(48025.29, 63872.98) * mm, "radius": 27.5 * mm});
            skCircle(sketch, "E2519", {"center": v(48111.42, 63809.47) * mm, "radius": 25 * mm});
            skCircle(sketch, "E2520", {"center": v(48193.34, 63744.4) * mm, "radius": 20 * mm});
            skCircle(sketch, "E2521.1.0.0", {"center": v(48384.87, 63801.97) * mm, "radius": 20 * mm});
            skCircle(sketch, "E2521.1.0.1", {"center": v(48302.96, 63867.04) * mm, "radius": 25 * mm});
            skCircle(sketch, "E2521.1.0.2", {"center": v(48216.82, 63930.55) * mm, "radius": 27.5 * mm});
            skCircle(sketch, "E2521.2.0.0", {"center": v(48576.4, 63859.53) * mm, "radius": 20 * mm});
            skCircle(sketch, "E2521.2.0.1", {"center": v(48494.5, 63924.6) * mm, "radius": 25 * mm});
            skCircle(sketch, "E2521.2.0.2", {"center": v(48408.36, 63988.11) * mm, "radius": 27.5 * mm});
            skCircle(sketch, "E2521.3.0.0", {"center": v(48767.94, 63917.1) * mm, "radius": 20 * mm});
            skCircle(sketch, "E2521.3.0.1", {"center": v(48686.03, 63982.17) * mm, "radius": 25 * mm});
            skCircle(sketch, "E2521.3.0.2", {"center": v(48599.9, 64045.68) * mm, "radius": 27.5 * mm});
            skCircle(sketch, "E2521.4.0.0", {"center": v(48959.48, 63974.67) * mm, "radius": 20 * mm});
            skCircle(sketch, "E2521.4.0.1", {"center": v(48877.57, 64039.74) * mm, "radius": 25 * mm});
            skCircle(sketch, "E2521.4.0.2", {"center": v(48791.43, 64103.25) * mm, "radius": 27.5 * mm});
            skCircle(sketch, "E2521.5.0.0", {"center": v(49151.02, 64032.23) * mm, "radius": 20 * mm});
            skCircle(sketch, "E2521.5.0.1", {"center": v(49069.1, 64097.3) * mm, "radius": 25 * mm});
            skCircle(sketch, "E2521.5.0.2", {"center": v(48982.97, 64160.81) * mm, "radius": 27.5 * mm});
            skCircle(sketch, "E2521.6.0.0", {"center": v(49342.55, 64089.8) * mm, "radius": 20 * mm});
            skCircle(sketch, "E2521.6.0.1", {"center": v(49260.64, 64154.87) * mm, "radius": 25 * mm});
            skCircle(sketch, "E2521.6.0.2", {"center": v(49174.5, 64218.38) * mm, "radius": 27.5 * mm});
            skCircle(sketch, "E2521.7.0.0", {"center": v(49534.09, 64147.37) * mm, "radius": 20 * mm});
            skCircle(sketch, "E2521.7.0.1", {"center": v(49452.18, 64212.44) * mm, "radius": 25 * mm});
            skCircle(sketch, "E2521.7.0.2", {"center": v(49366.04, 64275.95) * mm, "radius": 27.5 * mm});
            skLineSegment(sketch, "E2521.direction1", {"start": v(48025.29, 63872.98) * mm, "end": v(48216.82, 63930.55) * mm, "construction": true});
            skCircle(sketch, "E2522", {"center": v(50700.56, 64567) * mm, "radius": 155 * mm});
            skCircle(sketch, "E2523", {"center": v(49766.18, 64278.66) * mm, "radius": 155 * mm});
            skCircle(sketch, "E2524", {"center": v(50133.64, 64341.79) * mm, "radius": 80 * mm});
            skLineSegment(sketch, "E2525.0", {"start": v(51257.9, 64990.82) * mm, "end": v(51388.26, 64560.11) * mm, "construction": true});
            skLineSegment(sketch, "E2525.1", {"start": v(51388.26, 64560.11) * mm, "end": v(48028.73, 63543.32) * mm, "construction": true});
            skSolve(sketch);
        }
        {
            var Q0;
            Q0=makeQuery(id+"F2.opExtrude","CAP_FACE",FACE,{"disambiguationData":[OSD([sQuery(id+"F1.wireOp",EDGE,"E1119.4"),sQuery(id+"F1.wireOp",EDGE,"E1119.5"),sQuery(id+"F1.wireOp",EDGE,"E1119.6"),sQuery(id+"F1.wireOp",EDGE,"E1119.7"),sQuery(id+"F1.wireOp",EDGE,"E1120.3"),sQuery(id+"F1.wireOp",EDGE,"E1121.0"),sQuery(id+"F1.wireOp",EDGE,"E1121.1"),sQuery(id+"F1.wireOp",EDGE,"E1121.2"),sQuery(id+"F1.wireOp",EDGE,"E1121.3"),sQuery(id+"F1.wireOp",EDGE,"E1121.4"),sQuery(id+"F1.wireOp",EDGE,"E1121.5"),sQuery(id+"F1.wireOp",EDGE,"E1121.6"),sQuery(id+"F1.wireOp",EDGE,"E1121.7"),sQuery(id+"F1.wireOp",EDGE,"E1121.9"),sQuery(id+"F1.wireOp",EDGE,"E1121.10"),sQuery(id+"F1.wireOp",EDGE,"E1121.11"),sQuery(id+"F1.wireOp",EDGE,"E1122"),sQuery(id+"F1.wireOp",EDGE,"E1123.0"),sQuery(id+"F1.wireOp",EDGE,"E1123.4"),sQuery(id+"F1.wireOp",EDGE,"E1123.5"),sQuery(id+"F1.wireOp",EDGE,"E1123.6"),sQuery(id+"F1.wireOp",EDGE,"E1123.7"),sQuery(id+"F1.wireOp",EDGE,"E1123.8"),sQuery(id+"F1.wireOp",EDGE,"E1123.9"),sQuery(id+"F1.wireOp",EDGE,"E1123.10"),sQuery(id+"F1.wireOp",EDGE,"E1124.0"),sQuery(id+"F1.wireOp",EDGE,"E1124.1"),sQuery(id+"F1.wireOp",EDGE,"E1124.2"),sQuery(id+"F1.wireOp",EDGE,"E1124.3"),sQuery(id+"F1.wireOp",EDGE,"E1125.0"),sQuery(id+"F1.wireOp",EDGE,"E1125.1"),sQuery(id+"F1.wireOp",EDGE,"E1125.2"),sQuery(id+"F1.wireOp",EDGE,"E1125.3"),sQuery(id+"F1.wireOp",EDGE,"E1126.0"),sQuery(id+"F1.wireOp",EDGE,"E1126.1"),sQuery(id+"F1.wireOp",EDGE,"E1126.2"),sQuery(id+"F1.wireOp",EDGE,"E1126.3"),sQuery(id+"F1.wireOp",EDGE,"E1127.0"),sQuery(id+"F1.wireOp",EDGE,"E1127.1"),sQuery(id+"F1.wireOp",EDGE,"E1127.2"),sQuery(id+"F1.wireOp",EDGE,"E1127.3"),sQuery(id+"F1.wireOp",EDGE,"E1128.0"),sQuery(id+"F1.wireOp",EDGE,"E1128.1"),sQuery(id+"F1.wireOp",EDGE,"E1128.2"),sQuery(id+"F1.wireOp",EDGE,"E1128.3"),sQuery(id+"F1.wireOp",EDGE,"E1128.4"),sQuery(id+"F1.wireOp",EDGE,"E1129.0"),sQuery(id+"F1.wireOp",EDGE,"E1129.1"),sQuery(id+"F1.wireOp",EDGE,"E1129.2"),sQuery(id+"F1.wireOp",EDGE,"E1129.3"),sQuery(id+"F1.wireOp",EDGE,"E1129.4"),sQuery(id+"F1.wireOp",EDGE,"E1129.5"),sQuery(id+"F1.wireOp",EDGE,"E1129.6"),sQuery(id+"F1.wireOp",EDGE,"E1129.7"),sQuery(id+"F1.wireOp",EDGE,"E1129.8"),sQuery(id+"F1.wireOp",EDGE,"E1129.9"),sQuery(id+"F1.wireOp",EDGE,"E1129.10"),sQuery(id+"F1.wireOp",EDGE,"E1130.0"),sQuery(id+"F1.wireOp",EDGE,"E1130.1"),sQuery(id+"F1.wireOp",EDGE,"E1130.2"),sQuery(id+"F1.wireOp",EDGE,"E1131"),sQuery(id+"F1.wireOp",EDGE,"E1132.0"),sQuery(id+"F1.wireOp",EDGE,"E1132.1"),sQuery(id+"F1.wireOp",EDGE,"E1132.2"),sQuery(id+"F1.wireOp",EDGE,"E1132.3"),sQuery(id+"F1.wireOp",EDGE,"E1132.4"),sQuery(id+"F1.wireOp",EDGE,"E1132.5"),sQuery(id+"F1.wireOp",EDGE,"E1133.0"),sQuery(id+"F1.wireOp",EDGE,"E1133.1"),sQuery(id+"F1.wireOp",EDGE,"E1133.2"),sQuery(id+"F1.wireOp",EDGE,"E1133.3"),sQuery(id+"F1.wireOp",EDGE,"E1134.0"),sQuery(id+"F1.wireOp",EDGE,"E1134.1"),sQuery(id+"F1.wireOp",EDGE,"E1134.2"),sQuery(id+"F1.wireOp",EDGE,"E1134.3"),sQuery(id+"F1.wireOp",EDGE,"E1136"),sQuery(id+"F1.wireOp",EDGE,"E1137.0.1.0"),sQuery(id+"F1.wireOp",EDGE,"E1137.0.2.0"),sQuery(id+"F1.wireOp",EDGE,"E1137.0.3.0"),sQuery(id+"F1.wireOp",EDGE,"E1138.0"),sQuery(id+"F1.wireOp",EDGE,"E1138.1"),sQuery(id+"F1.wireOp",EDGE,"E1138.2"),sQuery(id+"F1.wireOp",EDGE,"E1138.3"),sQuery(id+"F1.wireOp",EDGE,"E1139.0"),sQuery(id+"F1.wireOp",EDGE,"E1139.1"),sQuery(id+"F1.wireOp",EDGE,"E1139.2"),sQuery(id+"F1.wireOp",EDGE,"E1139.3"),sQuery(id+"F1.wireOp",EDGE,"E1140"),sQuery(id+"F1.wireOp",EDGE,"E1141"),sQuery(id+"F1.wireOp",EDGE,"E1142")])],"isStart":false});
            var sketch = newSketch(context, id + "F17", { "sketchPlane" : qUnion([Q0])});
            skLineSegment(sketch, "E2526.0", {"start": v(37800.23, 67883.79) * mm, "end": v(31024.37, 65832.87) * mm, "construction": true});
            skLineSegment(sketch, "E2526.1", {"start": v(32335.92, 75761.3) * mm, "end": v(38822.87, 54329.57) * mm, "construction": true});
            skLineSegment(sketch, "E2526.2", {"start": v(59917.1, 70856.14) * mm, "end": v(32056.39, 62423.27) * mm, "construction": true});
            skLineSegment(sketch, "E2526.3", {"start": v(32831.58, 66077.37) * mm, "end": v(35924.87, 55857.68) * mm, "construction": true});
            skLineSegment(sketch, "E2527", {"start": v(34293.94, 63100.53) * mm, "end": v(34871.14, 63275.24) * mm});
            skLineSegment(sketch, "E2528", {"start": v(34871.14, 63275.24) * mm, "end": v(34607.52, 64146.21) * mm});
            skLineSegment(sketch, "E2529", {"start": v(34607.52, 64146.21) * mm, "end": v(34033.25, 63972.4) * mm});
            skLineSegment(sketch, "E2530", {"start": v(34033.25, 63972.4) * mm, "end": v(34293.94, 63100.53) * mm});
            skSolve(sketch);
        }
        {
            var Q0;
            Q0 = qSketchRegion(id + "F17", true);
            extrude(context, id + "F18", {"entities" : qUnion([Q0]), "depth" : (470 - (814 / 2)) * mm, "offsetDistance" : 25 * mm});
        }
        {
            var Q0;
            Q0=makeQuery(id+"F18.opExtrude","SWEPT_FACE",FACE,{"disambiguationData":[OSD([sQuery(id+"F17.wireOp",EDGE,"E2527")])]});
            var sketch = newSketch(context, id + "F19", { "sketchPlane" : qUnion([Q0])});
            skLineSegment(sketch, "E2531", {"start": v(51405.1, 463) * mm, "end": v(51405.1, 870) * mm, "construction": true});
            skArc(sketch, "E2532", {"start": v(51647.37, 542.97) * mm, "mid": v(51405.1, 1277) * mm, "end": v(51162.8, 542.97) * mm});
            skLineSegment(sketch, "E2533", {"start": v(51162.8, 542.97) * mm, "end": v(51103.56, 463) * mm});
            skLineSegment(sketch, "E2534", {"start": v(51647.37, 542.97) * mm, "end": v(51706.62, 463) * mm});
            skArc(sketch, "E2535", {"start": v(51390.13, 986.58) * mm, "mid": v(51354.84, 976.25) * mm, "end": v(51324.46, 955.53) * mm});
            skArc(sketch, "E2536", {"start": v(51249.66, 585.98) * mm, "mid": v(51345.04, 551.85) * mm, "end": v(51446.3, 548.87) * mm});
            skLineSegment(sketch, "E2537", {"start": v(51511.34, 920.25) * mm, "end": v(51697.78, 1008.42) * mm});
            skLineSegment(sketch, "E2538.1.0", {"start": v(51461.52, 973.1) * mm, "end": v(51560.52, 1154.02) * mm});
            skLineSegment(sketch, "E2538.2.0", {"start": v(51390.13, 986.58) * mm, "end": v(51363.89, 1191.13) * mm});
            skLineSegment(sketch, "E2539.2.3.0", {"start": v(51324.46, 955.53) * mm, "end": v(51183, 1105.59) * mm});
            skLineSegment(sketch, "E2539.2.4.0", {"start": v(51289.6, 891.8) * mm, "end": v(51086.94, 930.05) * mm});
            skLineSegment(sketch, "E2539.2.5.0", {"start": v(51298.84, 819.75) * mm, "end": v(51112.4, 731.58) * mm});
            skLineSegment(sketch, "E2539.2.6.0", {"start": v(51348.67, 766.9) * mm, "end": v(51249.66, 585.98) * mm});
            skLineSegment(sketch, "E2539.2.7.0", {"start": v(51420.05, 753.42) * mm, "end": v(51446.3, 548.87) * mm});
            skLineSegment(sketch, "E2540.2.8.0", {"start": v(51485.72, 784.47) * mm, "end": v(51627.18, 634.41) * mm});
            skLineSegment(sketch, "E2540.2.9.0", {"start": v(51520.59, 848.2) * mm, "end": v(51723.24, 809.95) * mm});
            skArc(sketch, "E2541.trimOffspring", {"start": v(51289.6, 891.8) * mm, "mid": v(51288.5, 855.04) * mm, "end": v(51298.84, 819.75) * mm});
            skArc(sketch, "E2542.trimOffspring", {"start": v(51348.67, 766.9) * mm, "mid": v(51383.29, 754.5) * mm, "end": v(51420.05, 753.42) * mm});
            skArc(sketch, "E2543.trimOffspring", {"start": v(51485.72, 784.47) * mm, "mid": v(51508.2, 813.58) * mm, "end": v(51520.59, 848.2) * mm});
            skArc(sketch, "E2544.trimOffspring", {"start": v(51511.34, 920.25) * mm, "mid": v(51490.62, 950.63) * mm, "end": v(51461.52, 973.1) * mm});
            skArc(sketch, "E2545.trimOffspring", {"start": v(51627.18, 634.41) * mm, "mid": v(51689.11, 714.57) * mm, "end": v(51723.24, 809.95) * mm});
            skArc(sketch, "E2546.trimOffspring", {"start": v(51697.78, 1008.42) * mm, "mid": v(51640.68, 1092.1) * mm, "end": v(51560.52, 1154.02) * mm});
            skArc(sketch, "E2547.trimOffspring", {"start": v(51086.94, 930.05) * mm, "mid": v(51083.96, 828.8) * mm, "end": v(51112.4, 731.58) * mm});
            skArc(sketch, "E2548.trimOffspring", {"start": v(51363.89, 1191.13) * mm, "mid": v(51266.67, 1162.69) * mm, "end": v(51183, 1105.59) * mm});
            skLineSegment(sketch, "E2549", {"start": v(51103.56, 463) * mm, "end": v(51706.62, 463) * mm});
            skSolve(sketch);
        }
        {
            var Q0;
            Q0 = qSketchRegion(id + "F19", true);
            extrude(context, id + "F20", {"entities" : qUnion([Q0]), "operationType" : NewBodyOperationType.ADD, "oppositeDirection" : true, "depth" : 910 * mm, "offsetDistance" : 25 * mm});
        }
        {
            var Q0;
            Q0=makeQuery(id+"F17.imprint","IMPRINT",FACE,{"disambiguationData":[TD([[makeQuery(id+"F17.imprint","IMPRINT",EDGE,{"derivedFrom":sQuery(id+"F17.wireOp",EDGE,"E2527")}),-1.0]])]});
            var sketch = newSketch(context, id + "F21", { "sketchPlane" : qUnion([Q0])});
            skLineSegment(sketch, "E2550.0", {"start": v(33353.34, 67923.5) * mm, "end": v(40436.81, 70067.58) * mm, "construction": true});
            skLineSegment(sketch, "E2551", {"start": v(35243.48, 68495.62) * mm, "end": v(36516.4, 64290.24) * mm, "construction": true});
            skLineSegment(sketch, "E2552", {"start": v(35243.48, 68495.62) * mm, "end": v(36170.54, 65432.85) * mm});
            skLineSegment(sketch, "E2553", {"start": v(36170.54, 65432.85) * mm, "end": v(37414.8, 65809.47) * mm});
            skLineSegment(sketch, "E2554", {"start": v(37414.8, 65809.47) * mm, "end": v(36487.73, 68872.24) * mm});
            skLineSegment(sketch, "E2555", {"start": v(36487.73, 68872.24) * mm, "end": v(35243.48, 68495.62) * mm});
            skSolve(sketch);
        }
        {
            var Q0;
            Q0 = qSketchRegion(id + "F21", true);
            extrude(context, id + "F22", {"entities" : qUnion([Q0]), "depth" : 2156 * mm, "offsetDistance" : 25 * mm});
        }
        {
            var Q0;
            Q0=makeQuery(id+"F17.imprint","IMPRINT",FACE,{"disambiguationData":[TD([[makeQuery(id+"F17.imprint","IMPRINT",EDGE,{"derivedFrom":sQuery(id+"F17.wireOp",EDGE,"E2527")}),-1.0]])]});
            var sketch = newSketch(context, id + "F23", { "sketchPlane" : qUnion([Q0])});
            skLineSegment(sketch, "E2556.0", {"start": v(32335.92, 75761.3) * mm, "end": v(38822.87, 54329.57) * mm, "construction": true});
            skLineSegment(sketch, "E2557.0", {"start": v(59917.1, 70856.14) * mm, "end": v(32056.39, 62423.27) * mm, "construction": true});
            skLineSegment(sketch, "E2558", {"start": v(36970.17, 60450.57) * mm, "end": v(36237.98, 60228.95) * mm});
            skLineSegment(sketch, "E2559", {"start": v(36237.98, 60228.95) * mm, "end": v(36507.4, 59338.83) * mm});
            skLineSegment(sketch, "E2560", {"start": v(36507.4, 59338.83) * mm, "end": v(37239.6, 59560.45) * mm});
            skLineSegment(sketch, "E2561", {"start": v(37239.6, 59560.45) * mm, "end": v(36970.17, 60450.57) * mm});
            skSolve(sketch);
        }
        {
            var Q0;
            Q0 = qSketchRegion(id + "F23", true);
            extrude(context, id + "F24", {"entities" : qUnion([Q0]), "depth" : 1900 * mm, "offsetDistance" : 25 * mm});
        }
        {
            var Q0;
            Q0=makeQuery(id+"F17.imprint","IMPRINT",FACE,{"disambiguationData":[TD([[makeQuery(id+"F17.imprint","IMPRINT",EDGE,{"derivedFrom":sQuery(id+"F17.wireOp",EDGE,"E2527")}),-1.0]])]});
            var sketch = newSketch(context, id + "F25", { "sketchPlane" : qUnion([Q0])});
            skLineSegment(sketch, "E2562", {"start": v(43753, 61922.98) * mm, "end": v(44215.97, 60393.4) * mm});
            skLineSegment(sketch, "E2563", {"start": v(43771.19, 61928.48) * mm, "end": v(44234.16, 60398.9) * mm});
            skLineSegment(sketch, "E2564", {"start": v(43729.08, 61915.73) * mm, "end": v(44192.05, 60386.16) * mm});
            skLineSegment(sketch, "E2565", {"start": v(43717.11, 61912.11) * mm, "end": v(44180.08, 60382.54) * mm});
            skLineSegment(sketch, "E2566", {"start": v(43648.2, 61891.26) * mm, "end": v(44111.17, 60361.68) * mm});
            skLineSegment(sketch, "E2567", {"start": v(43431.74, 62984.39) * mm, "end": v(43460.4, 62889.67) * mm});
            skLineSegment(sketch, "E2568", {"start": v(43452.68, 62980.79) * mm, "end": v(43478.6, 62895.17) * mm});
            skLineSegment(sketch, "E2569", {"start": v(43404.18, 62989.13) * mm, "end": v(43436.48, 62882.42) * mm});
            skLineSegment(sketch, "E2570", {"start": v(43390.4, 62991.5) * mm, "end": v(43424.51, 62878.8) * mm});
            skLineSegment(sketch, "E2571", {"start": v(43311.05, 63005.14) * mm, "end": v(43355.6, 62857.94) * mm});
            skLineSegment(sketch, "E2572", {"start": v(43472.13, 62893.21) * mm, "end": v(43362.06, 62859.9) * mm});
            skLineSegment(sketch, "E2573", {"start": v(43764.73, 61926.53) * mm, "end": v(43654.66, 61893.21) * mm});
            skLineSegment(sketch, "E2574", {"start": v(43472.13, 62893.21) * mm, "end": v(43484.3, 62853.02) * mm});
            skLineSegment(sketch, "E2575", {"start": v(43484.3, 62853.02) * mm, "end": v(43374.23, 62819.7) * mm});
            skLineSegment(sketch, "E2576", {"start": v(43374.23, 62819.7) * mm, "end": v(43362.06, 62859.9) * mm});
            skLineSegment(sketch, "E2577", {"start": v(43362.06, 62859.9) * mm, "end": v(43472.13, 62893.21) * mm});
            skLineSegment(sketch, "E2578", {"start": v(43752.56, 61966.72) * mm, "end": v(43764.73, 61926.53) * mm});
            skLineSegment(sketch, "E2579", {"start": v(43654.66, 61893.21) * mm, "end": v(43642.5, 61933.4) * mm});
            skLineSegment(sketch, "E2580", {"start": v(43642.5, 61933.4) * mm, "end": v(43752.56, 61966.72) * mm});
            skLineSegment(sketch, "E2581", {"start": v(43764.73, 61926.53) * mm, "end": v(43752.56, 61966.72) * mm});
            skLineSegment(sketch, "E2582", {"start": v(43362.06, 62859.9) * mm, "end": v(43374.23, 62819.7) * mm});
            skLineSegment(sketch, "E2583", {"start": v(43752.56, 61966.72) * mm, "end": v(43642.5, 61933.4) * mm});
            skArc(sketch, "E2584", {"start": v(43752.56, 61966.72) * mm, "mid": v(44300.69, 62416) * mm, "end": v(44370.59, 63121.28) * mm});
            skLineSegment(sketch, "E2585", {"start": v(43484.3, 62853.02) * mm, "end": v(44370.59, 63121.28) * mm});
            skLineSegment(sketch, "E2586", {"start": v(44370.59, 63121.28) * mm, "end": v(44383.47, 63078.73) * mm});
            skLineSegment(sketch, "E2587", {"start": v(44383.47, 63078.73) * mm, "end": v(43497.17, 62810.47) * mm});
            skLineSegment(sketch, "E2588", {"start": v(43497.17, 62810.47) * mm, "end": v(43484.3, 62853.02) * mm});
            skLineSegment(sketch, "E2589", {"start": v(43497.17, 62810.47) * mm, "end": v(44383.47, 63078.73) * mm});
            skLineSegment(sketch, "E2590", {"start": v(43484.3, 62853.02) * mm, "end": v(43497.17, 62810.47) * mm});
            skLineSegment(sketch, "E2591", {"start": v(59482.9, 51933.33) * mm, "end": v(59339.9, 52189.81) * mm});
            skLineSegment(sketch, "E2592", {"start": v(59471.97, 51927.24) * mm, "end": v(59328.98, 52183.72) * mm});
            skLineSegment(sketch, "E2593", {"start": v(59556.7, 51974.47) * mm, "end": v(59413.7, 52230.96) * mm});
            skLineSegment(sketch, "E2594", {"start": v(59545.78, 51968.39) * mm, "end": v(59402.79, 52224.87) * mm});
            skLineSegment(sketch, "E2595", {"start": v(59567.61, 51980.56) * mm, "end": v(59424.62, 52237.04) * mm});
            skLineSegment(sketch, "E2596", {"start": v(59576.35, 51985.43) * mm, "end": v(59433.36, 52241.91) * mm});
            skLineSegment(sketch, "E2597", {"start": v(60077.97, 50865.94) * mm, "end": v(59963.02, 51072.12) * mm});
            skLineSegment(sketch, "E2598", {"start": v(60060.97, 50870.77) * mm, "end": v(59952.1, 51066.04) * mm});
            skLineSegment(sketch, "E2599", {"start": v(60192.92, 50833.28) * mm, "end": v(60036.83, 51113.27) * mm});
            skLineSegment(sketch, "E2600", {"start": v(60175.92, 50838.11) * mm, "end": v(60025.9, 51107.18) * mm});
            skLineSegment(sketch, "E2601", {"start": v(60209.93, 50828.45) * mm, "end": v(60047.74, 51119.36) * mm});
            skLineSegment(sketch, "E2602", {"start": v(60223.53, 50824.58) * mm, "end": v(60056.48, 51124.23) * mm});
            skLineSegment(sketch, "E2603", {"start": v(59582.52, 52002.6) * mm, "end": v(59462.86, 51935.9) * mm});
            skLineSegment(sketch, "E2604", {"start": v(60074.33, 51120.44) * mm, "end": v(59954.67, 51053.73) * mm});
            skLineSegment(sketch, "E2605", {"start": v(59582.52, 52002.6) * mm, "end": v(59602.97, 51965.92) * mm});
            skLineSegment(sketch, "E2606", {"start": v(59602.97, 51965.92) * mm, "end": v(59483.3, 51899.21) * mm});
            skLineSegment(sketch, "E2607", {"start": v(59483.3, 51899.21) * mm, "end": v(59462.86, 51935.9) * mm});
            skLineSegment(sketch, "E2608", {"start": v(59462.86, 51935.9) * mm, "end": v(59582.52, 52002.6) * mm});
            skLineSegment(sketch, "E2609", {"start": v(60053.88, 51157.12) * mm, "end": v(60074.33, 51120.44) * mm});
            skLineSegment(sketch, "E2610", {"start": v(59954.67, 51053.73) * mm, "end": v(59934.22, 51090.41) * mm});
            skLineSegment(sketch, "E2611", {"start": v(59934.22, 51090.41) * mm, "end": v(60053.88, 51157.12) * mm});
            skLineSegment(sketch, "E2612", {"start": v(60074.33, 51120.44) * mm, "end": v(60053.88, 51157.12) * mm});
            skLineSegment(sketch, "E2613", {"start": v(59462.86, 51935.9) * mm, "end": v(59483.3, 51899.21) * mm});
            skLineSegment(sketch, "E2614", {"start": v(60053.88, 51157.12) * mm, "end": v(59934.22, 51090.41) * mm});
            skArc(sketch, "E2615", {"start": v(60053.88, 51157.12) * mm, "mid": v(60493.72, 51712.86) * mm, "end": v(60411.77, 52416.83) * mm});
            skLineSegment(sketch, "E2616", {"start": v(59602.97, 51965.92) * mm, "end": v(60411.77, 52416.83) * mm});
            skLineSegment(sketch, "E2617", {"start": v(60411.77, 52416.83) * mm, "end": v(60433.2, 52378.4) * mm});
            skLineSegment(sketch, "E2618", {"start": v(60433.2, 52378.4) * mm, "end": v(59624.4, 51927.5) * mm});
            skLineSegment(sketch, "E2619", {"start": v(59624.4, 51927.5) * mm, "end": v(59602.97, 51965.92) * mm});
            skLineSegment(sketch, "E2620", {"start": v(59624.4, 51927.5) * mm, "end": v(60433.2, 52378.4) * mm});
            skLineSegment(sketch, "E2621", {"start": v(59602.97, 51965.92) * mm, "end": v(59624.4, 51927.5) * mm});
            skLineSegment(sketch, "E2622", {"start": v(59979.27, 50810.91) * mm, "end": v(60077.97, 50865.94) * mm});
            skLineSegment(sketch, "E2623", {"start": v(59962.27, 50815.74) * mm, "end": v(60060.97, 50870.77) * mm});
            skLineSegment(sketch, "E2624", {"start": v(60094.22, 50778.25) * mm, "end": v(60192.92, 50833.28) * mm});
            skLineSegment(sketch, "E2625", {"start": v(60077.22, 50783.09) * mm, "end": v(60175.92, 50838.11) * mm});
            skLineSegment(sketch, "E2626", {"start": v(60111.23, 50773.42) * mm, "end": v(60209.93, 50828.45) * mm});
            skLineSegment(sketch, "E2627", {"start": v(60124.83, 50769.56) * mm, "end": v(60223.53, 50824.58) * mm});
            skLineSegment(sketch, "E2628", {"start": v(55839.38, 58636.06) * mm, "end": v(59411.09, 52229.5) * mm});
            skLineSegment(sketch, "E2629", {"start": v(55846.6, 58653.92) * mm, "end": v(59424.19, 52236.8) * mm});
            skLineSegment(sketch, "E2630", {"start": v(55832.16, 58618.2) * mm, "end": v(59397.98, 52222.2) * mm});
            skLineSegment(sketch, "E2631", {"start": v(55824.94, 58600.35) * mm, "end": v(59384.88, 52214.89) * mm});
            skLineSegment(sketch, "E2632", {"start": v(55781.63, 58493.2) * mm, "end": v(59306.27, 52171.06) * mm});
            skLineSegment(sketch, "E2633", {"start": v(55816.28, 58578.92) * mm, "end": v(59369.16, 52206.12) * mm});
            skLineSegment(sketch, "E2634", {"start": v(55767.2, 58457.5) * mm, "end": v(59280.07, 52156.45) * mm});
            skLineSegment(sketch, "E2635", {"start": v(53445.33, 62941.8) * mm, "end": v(54840.14, 58333.61) * mm});
            skLineSegment(sketch, "E2636", {"start": v(53459.69, 62946.15) * mm, "end": v(54850.15, 58352.31) * mm});
            skLineSegment(sketch, "E2637", {"start": v(53430.97, 62937.46) * mm, "end": v(54830.13, 58314.9) * mm});
            skLineSegment(sketch, "E2638", {"start": v(53416.62, 62933.12) * mm, "end": v(54820.12, 58296.2) * mm});
            skLineSegment(sketch, "E2639", {"start": v(53330.47, 62907.05) * mm, "end": v(54760.05, 58184) * mm});
            skLineSegment(sketch, "E2640", {"start": v(53399.39, 62927.9) * mm, "end": v(54808.1, 58273.76) * mm});
            skLineSegment(sketch, "E2641", {"start": v(53301.76, 62898.35) * mm, "end": v(54740.03, 58146.59) * mm});
            skLineSegment(sketch, "E2642", {"start": v(54840.14, 58333.61) * mm, "end": v(55798.6, 58623.72) * mm});
            skLineSegment(sketch, "E2643", {"start": v(54850.15, 58352.31) * mm, "end": v(55794.26, 58638.08) * mm});
            skLineSegment(sketch, "E2644", {"start": v(54830.13, 58314.9) * mm, "end": v(55802.95, 58609.36) * mm});
            skLineSegment(sketch, "E2645", {"start": v(54820.12, 58296.2) * mm, "end": v(55807.3, 58595) * mm});
            skLineSegment(sketch, "E2646", {"start": v(54760.05, 58184) * mm, "end": v(55833.37, 58508.87) * mm});
            skLineSegment(sketch, "E2647", {"start": v(54808.1, 58273.76) * mm, "end": v(55812.51, 58577.78) * mm});
            skLineSegment(sketch, "E2648", {"start": v(54740.03, 58146.59) * mm, "end": v(55842.06, 58480.15) * mm});
            skLineSegment(sketch, "E2649", {"start": v(55447.29, 58664.82) * mm, "end": v(55769.55, 58844.48) * mm});
            skLineSegment(sketch, "E2650", {"start": v(55454.63, 58690.67) * mm, "end": v(55776.9, 58870.33) * mm});
            skLineSegment(sketch, "E2651", {"start": v(55437.63, 58630.8) * mm, "end": v(55759.89, 58810.47) * mm});
            skLineSegment(sketch, "E2652", {"start": v(55432.8, 58613.8) * mm, "end": v(55755.06, 58793.47) * mm});
            skLineSegment(sketch, "E2653", {"start": v(55404.97, 58515.86) * mm, "end": v(55727.23, 58695.52) * mm});
            skLineSegment(sketch, "E2654", {"start": v(54136.1, 61016.48) * mm, "end": v(55447.29, 58664.82) * mm});
            skLineSegment(sketch, "E2655", {"start": v(54161.94, 61009.13) * mm, "end": v(55454.63, 58690.67) * mm});
            skLineSegment(sketch, "E2656", {"start": v(54102.08, 61026.14) * mm, "end": v(55437.63, 58630.8) * mm});
            skLineSegment(sketch, "E2657", {"start": v(54085.08, 61030.97) * mm, "end": v(55432.8, 58613.8) * mm});
            skLineSegment(sketch, "E2658", {"start": v(53987.13, 61058.8) * mm, "end": v(55404.97, 58515.86) * mm});
            skLineSegment(sketch, "E2659", {"start": v(54462.39, 61198.4) * mm, "end": v(54136.1, 61016.48) * mm});
            skLineSegment(sketch, "E2660", {"start": v(54488.24, 61191.07) * mm, "end": v(54161.94, 61009.13) * mm});
            skLineSegment(sketch, "E2661", {"start": v(54428.38, 61208.07) * mm, "end": v(54102.08, 61026.14) * mm});
            skLineSegment(sketch, "E2662", {"start": v(54411.38, 61212.9) * mm, "end": v(54085.08, 61030.97) * mm});
            skLineSegment(sketch, "E2663", {"start": v(54313.43, 61240.72) * mm, "end": v(53987.13, 61058.8) * mm});
            skLineSegment(sketch, "E2664", {"start": v(51276.1, 66688.64) * mm, "end": v(51371.8, 66742) * mm});
            skLineSegment(sketch, "E2665", {"start": v(51282.28, 66713.84) * mm, "end": v(51379.14, 66767.85) * mm});
            skLineSegment(sketch, "E2666", {"start": v(51267.97, 66655.49) * mm, "end": v(51362.13, 66707.99) * mm});
            skLineSegment(sketch, "E2667", {"start": v(51263.9, 66638.9) * mm, "end": v(51357.3, 66690.98) * mm});
            skLineSegment(sketch, "E2668", {"start": v(51240.48, 66543.42) * mm, "end": v(51329.48, 66593.03) * mm});
            skLineSegment(sketch, "E2669", {"start": v(51244.85, 66561.24) * mm, "end": v(51108.92, 66805.05) * mm});
            skLineSegment(sketch, "E2670", {"start": v(51240.48, 66543.42) * mm, "end": v(51093.74, 66806.6) * mm});
            skLineSegment(sketch, "E2671", {"start": v(51274.4, 66681.75) * mm, "end": v(51211.53, 66794.52) * mm});
            skLineSegment(sketch, "E2672", {"start": v(51270.04, 66663.93) * mm, "end": v(51196.35, 66796.08) * mm});
            skLineSegment(sketch, "E2673", {"start": v(51278.78, 66699.58) * mm, "end": v(51226.71, 66792.96) * mm});
            skLineSegment(sketch, "E2674", {"start": v(51282.28, 66713.84) * mm, "end": v(51238.86, 66791.72) * mm});
            skLineSegment(sketch, "E2675", {"start": v(41865.79, 69228.74) * mm, "end": v(42507.66, 67108.13) * mm});
            skLineSegment(sketch, "E2676", {"start": v(41872.46, 69241.2) * mm, "end": v(42516.26, 67114.2) * mm});
            skLineSegment(sketch, "E2677", {"start": v(41857.45, 69213.15) * mm, "end": v(42496.9, 67100.52) * mm});
            skLineSegment(sketch, "E2678", {"start": v(41849.1, 69197.57) * mm, "end": v(42486.14, 67092.92) * mm});
            skLineSegment(sketch, "E2679", {"start": v(41801.05, 69107.8) * mm, "end": v(42424.17, 67049.13) * mm});
            skLineSegment(sketch, "E2680", {"start": v(42270.58, 68012.18) * mm, "end": v(42773.07, 68164.28) * mm});
            skLineSegment(sketch, "E2681", {"start": v(42773.07, 68164.28) * mm, "end": v(42946.9, 67590) * mm});
            skLineSegment(sketch, "E2682", {"start": v(42946.9, 67590) * mm, "end": v(42444.4, 67437.91) * mm});
            skLineSegment(sketch, "E2683", {"start": v(42420.48, 67430.67) * mm, "end": v(42246.66, 68004.94) * mm});
            skLineSegment(sketch, "E2684", {"start": v(42246.66, 68004.94) * mm, "end": v(42270.58, 68012.18) * mm});
            skLineSegment(sketch, "E2685", {"start": v(42270.58, 68012.18) * mm, "end": v(42444.4, 67437.91) * mm});
            skLineSegment(sketch, "E2686", {"start": v(42444.4, 67437.91) * mm, "end": v(42420.48, 67430.67) * mm});
            skArc(sketch, "E2687", {"start": v(42627.92, 67806.9) * mm, "mid": v(42602.35, 67838.1) * mm, "end": v(42562.22, 67842.07) * mm});
            skArc(sketch, "E2688", {"start": v(42562.22, 67842.07) * mm, "mid": v(42531.03, 67816.5) * mm, "end": v(42527.06, 67776.37) * mm});
            skArc(sketch, "E2689", {"start": v(42527.06, 67776.37) * mm, "mid": v(42552.62, 67745.18) * mm, "end": v(42592.75, 67741.2) * mm});
            skArc(sketch, "E2690", {"start": v(42592.75, 67741.2) * mm, "mid": v(42623.94, 67766.77) * mm, "end": v(42627.92, 67806.9) * mm});
            skLineSegment(sketch, "E2691", {"start": v(42337.88, 67789.84) * mm, "end": v(42345.21, 67792.06) * mm});
            skLineSegment(sketch, "E2692", {"start": v(42345.21, 67792.06) * mm, "end": v(42330.73, 67839.91) * mm});
            skLineSegment(sketch, "E2693", {"start": v(42330.73, 67839.91) * mm, "end": v(42323.4, 67837.7) * mm});
            skArc(sketch, "E2694", {"start": v(42517.29, 67771.01) * mm, "mid": v(42517.29, 67771.04) * mm, "end": v(42517.29, 67771.06) * mm});
            skLineSegment(sketch, "E2695", {"start": v(42517.29, 67771.06) * mm, "end": v(42517.27, 67771.27) * mm});
            skArc(sketch, "E2696", {"start": v(42517.27, 67771.27) * mm, "mid": v(42517.24, 67771.5) * mm, "end": v(42517.21, 67771.73) * mm});
            skLineSegment(sketch, "E2697", {"start": v(42517.21, 67771.73) * mm, "end": v(42517.16, 67772.05) * mm});
            skArc(sketch, "E2698", {"start": v(42517.16, 67772.05) * mm, "mid": v(42517.05, 67772.6) * mm, "end": v(42516.9, 67773.14) * mm});
            skLineSegment(sketch, "E2699", {"start": v(42516.9, 67773.14) * mm, "end": v(42516.87, 67773.24) * mm});
            skArc(sketch, "E2700", {"start": v(42516.87, 67773.24) * mm, "mid": v(42516.87, 67773.27) * mm, "end": v(42516.86, 67773.29) * mm});
            skArc(sketch, "E2701", {"start": v(42516.86, 67773.29) * mm, "mid": v(42516.86, 67773.3) * mm, "end": v(42516.85, 67773.31) * mm});
            skLineSegment(sketch, "E2702", {"start": v(42516.85, 67773.31) * mm, "end": v(42516.8, 67773.47) * mm});
            skArc(sketch, "E2703", {"start": v(42516.8, 67773.47) * mm, "mid": v(42516.75, 67773.65) * mm, "end": v(42516.69, 67773.82) * mm});
            skLineSegment(sketch, "E2704", {"start": v(42516.69, 67773.82) * mm, "end": v(42516.62, 67774) * mm});
            skArc(sketch, "E2705", {"start": v(42516.62, 67774) * mm, "mid": v(42516.48, 67774.35) * mm, "end": v(42516.32, 67774.7) * mm});
            skLineSegment(sketch, "E2706", {"start": v(42516.32, 67774.7) * mm, "end": v(42516.31, 67774.72) * mm});
            skArc(sketch, "E2707", {"start": v(42516.31, 67774.72) * mm, "mid": v(42516.3, 67774.73) * mm, "end": v(42516.3, 67774.75) * mm});
            skLineSegment(sketch, "E2708", {"start": v(42347.23, 67803.41) * mm, "end": v(42347.37, 67802.92) * mm});
            skLineSegment(sketch, "E2709", {"start": v(42347.37, 67802.92) * mm, "end": v(42347.52, 67802.45) * mm});
            skLineSegment(sketch, "E2710", {"start": v(42347.52, 67802.45) * mm, "end": v(42347.65, 67802) * mm});
            skLineSegment(sketch, "E2711", {"start": v(42347.65, 67802) * mm, "end": v(42347.78, 67801.58) * mm});
            skLineSegment(sketch, "E2712", {"start": v(42347.78, 67801.58) * mm, "end": v(42347.9, 67801.19) * mm});
            skLineSegment(sketch, "E2713", {"start": v(42347.9, 67801.19) * mm, "end": v(42348.01, 67800.82) * mm});
            skLineSegment(sketch, "E2714", {"start": v(42348.01, 67800.82) * mm, "end": v(42348.12, 67800.47) * mm});
            skLineSegment(sketch, "E2715", {"start": v(42348.12, 67800.47) * mm, "end": v(42348.21, 67800.16) * mm});
            skLineSegment(sketch, "E2716", {"start": v(42348.21, 67800.16) * mm, "end": v(42348.3, 67799.87) * mm});
            skLineSegment(sketch, "E2717", {"start": v(42348.3, 67799.87) * mm, "end": v(42348.38, 67799.6) * mm});
            skLineSegment(sketch, "E2718", {"start": v(42348.38, 67799.6) * mm, "end": v(42348.45, 67799.38) * mm});
            skLineSegment(sketch, "E2719", {"start": v(42348.45, 67799.38) * mm, "end": v(42348.5, 67799.18) * mm});
            skLineSegment(sketch, "E2720", {"start": v(42348.5, 67799.18) * mm, "end": v(42348.56, 67799) * mm});
            skLineSegment(sketch, "E2721", {"start": v(42348.56, 67799) * mm, "end": v(42348.6, 67798.86) * mm});
            skLineSegment(sketch, "E2722", {"start": v(42348.6, 67798.86) * mm, "end": v(42348.64, 67798.75) * mm});
            skLineSegment(sketch, "E2723", {"start": v(42348.64, 67798.75) * mm, "end": v(42348.66, 67798.66) * mm});
            skLineSegment(sketch, "E2724", {"start": v(42348.66, 67798.66) * mm, "end": v(42348.68, 67798.6) * mm});
            skLineSegment(sketch, "E2725", {"start": v(42348.68, 67798.6) * mm, "end": v(42348.69, 67798.58) * mm});
            skLineSegment(sketch, "E2726", {"start": v(42348.69, 67798.58) * mm, "end": v(42348.73, 67798.42) * mm});
            skLineSegment(sketch, "E2727", {"start": v(42348.73, 67798.42) * mm, "end": v(42348.77, 67798.25) * mm});
            skLineSegment(sketch, "E2728", {"start": v(42348.77, 67798.25) * mm, "end": v(42348.8, 67798.08) * mm});
            skLineSegment(sketch, "E2729", {"start": v(42348.8, 67798.08) * mm, "end": v(42348.83, 67797.9) * mm});
            skLineSegment(sketch, "E2730", {"start": v(42348.83, 67797.9) * mm, "end": v(42348.85, 67797.73) * mm});
            skLineSegment(sketch, "E2731", {"start": v(42348.85, 67797.73) * mm, "end": v(42348.87, 67797.56) * mm});
            skLineSegment(sketch, "E2732", {"start": v(42348.87, 67797.56) * mm, "end": v(42348.87, 67797.38) * mm});
            skLineSegment(sketch, "E2733", {"start": v(42348.87, 67797.38) * mm, "end": v(42348.87, 67797.21) * mm});
            skLineSegment(sketch, "E2734", {"start": v(42348.87, 67797.21) * mm, "end": v(42348.86, 67797.04) * mm});
            skLineSegment(sketch, "E2735", {"start": v(42348.86, 67797.04) * mm, "end": v(42348.85, 67796.86) * mm});
            skLineSegment(sketch, "E2736", {"start": v(42348.85, 67796.86) * mm, "end": v(42348.83, 67796.7) * mm});
            skLineSegment(sketch, "E2737", {"start": v(42348.83, 67796.7) * mm, "end": v(42348.8, 67796.52) * mm});
            skLineSegment(sketch, "E2738", {"start": v(42348.8, 67796.52) * mm, "end": v(42348.76, 67796.35) * mm});
            skLineSegment(sketch, "E2739", {"start": v(42348.76, 67796.35) * mm, "end": v(42348.72, 67796.18) * mm});
            skLineSegment(sketch, "E2740", {"start": v(42348.72, 67796.18) * mm, "end": v(42348.67, 67796.01) * mm});
            skLineSegment(sketch, "E2741", {"start": v(42348.67, 67796.01) * mm, "end": v(42348.62, 67795.85) * mm});
            skLineSegment(sketch, "E2742", {"start": v(42348.62, 67795.85) * mm, "end": v(42348.55, 67795.69) * mm});
            skLineSegment(sketch, "E2743", {"start": v(42348.55, 67795.69) * mm, "end": v(42348.48, 67795.53) * mm});
            skLineSegment(sketch, "E2744", {"start": v(42348.48, 67795.53) * mm, "end": v(42348.4, 67795.37) * mm});
            skLineSegment(sketch, "E2745", {"start": v(42348.4, 67795.37) * mm, "end": v(42348.33, 67795.22) * mm});
            skLineSegment(sketch, "E2746", {"start": v(42348.33, 67795.22) * mm, "end": v(42348.24, 67795.06) * mm});
            skLineSegment(sketch, "E2747", {"start": v(42348.24, 67795.06) * mm, "end": v(42348.15, 67794.92) * mm});
            skLineSegment(sketch, "E2748", {"start": v(42348.15, 67794.92) * mm, "end": v(42348.05, 67794.78) * mm});
            skLineSegment(sketch, "E2749", {"start": v(42348.05, 67794.78) * mm, "end": v(42347.94, 67794.64) * mm});
            skLineSegment(sketch, "E2750", {"start": v(42347.94, 67794.64) * mm, "end": v(42347.83, 67794.5) * mm});
            skLineSegment(sketch, "E2751", {"start": v(42347.83, 67794.5) * mm, "end": v(42347.72, 67794.37) * mm});
            skLineSegment(sketch, "E2752", {"start": v(42347.72, 67794.37) * mm, "end": v(42347.6, 67794.25) * mm});
            skLineSegment(sketch, "E2753", {"start": v(42347.6, 67794.25) * mm, "end": v(42347.47, 67794.13) * mm});
            skLineSegment(sketch, "E2754", {"start": v(42347.47, 67794.13) * mm, "end": v(42347.34, 67794.01) * mm});
            skLineSegment(sketch, "E2755", {"start": v(42347.34, 67794.01) * mm, "end": v(42347.2, 67793.9) * mm});
            skLineSegment(sketch, "E2756", {"start": v(42347.2, 67793.9) * mm, "end": v(42347.07, 67793.8) * mm});
            skLineSegment(sketch, "E2757", {"start": v(42347.07, 67793.8) * mm, "end": v(42346.92, 67793.7) * mm});
            skLineSegment(sketch, "E2758", {"start": v(42346.92, 67793.7) * mm, "end": v(42346.78, 67793.6) * mm});
            skLineSegment(sketch, "E2759", {"start": v(42346.78, 67793.6) * mm, "end": v(42346.63, 67793.52) * mm});
            skLineSegment(sketch, "E2760", {"start": v(42346.63, 67793.52) * mm, "end": v(42346.47, 67793.44) * mm});
            skLineSegment(sketch, "E2761", {"start": v(42346.47, 67793.44) * mm, "end": v(42346.32, 67793.36) * mm});
            skLineSegment(sketch, "E2762", {"start": v(42346.32, 67793.36) * mm, "end": v(42346.16, 67793.3) * mm});
            skLineSegment(sketch, "E2763", {"start": v(42346.16, 67793.3) * mm, "end": v(42346, 67793.23) * mm});
            skLineSegment(sketch, "E2764", {"start": v(42346, 67793.23) * mm, "end": v(42345.83, 67793.17) * mm});
            skLineSegment(sketch, "E2765", {"start": v(42345.83, 67793.17) * mm, "end": v(42345.78, 67793.16) * mm});
            skLineSegment(sketch, "E2766", {"start": v(42345.78, 67793.16) * mm, "end": v(42344.95, 67792.9) * mm});
            skLineSegment(sketch, "E2767", {"start": v(42348.69, 67798.58) * mm, "end": v(42348.68, 67798.6) * mm});
            skLineSegment(sketch, "E2768", {"start": v(42348.68, 67798.6) * mm, "end": v(42348.67, 67798.64) * mm});
            skLineSegment(sketch, "E2769", {"start": v(42348.67, 67798.64) * mm, "end": v(42348.65, 67798.72) * mm});
            skLineSegment(sketch, "E2770", {"start": v(42348.65, 67798.72) * mm, "end": v(42348.61, 67798.83) * mm});
            skLineSegment(sketch, "E2771", {"start": v(42348.61, 67798.83) * mm, "end": v(42348.57, 67798.96) * mm});
            skLineSegment(sketch, "E2772", {"start": v(42348.57, 67798.96) * mm, "end": v(42348.52, 67799.13) * mm});
            skLineSegment(sketch, "E2773", {"start": v(42348.52, 67799.13) * mm, "end": v(42348.46, 67799.32) * mm});
            skLineSegment(sketch, "E2774", {"start": v(42348.46, 67799.32) * mm, "end": v(42348.4, 67799.54) * mm});
            skLineSegment(sketch, "E2775", {"start": v(42348.4, 67799.54) * mm, "end": v(42348.32, 67799.8) * mm});
            skLineSegment(sketch, "E2776", {"start": v(42348.32, 67799.8) * mm, "end": v(42348.24, 67800.08) * mm});
            skLineSegment(sketch, "E2777", {"start": v(42348.24, 67800.08) * mm, "end": v(42348.14, 67800.39) * mm});
            skLineSegment(sketch, "E2778", {"start": v(42348.14, 67800.39) * mm, "end": v(42348.04, 67800.72) * mm});
            skLineSegment(sketch, "E2779", {"start": v(42348.04, 67800.72) * mm, "end": v(42347.93, 67801.08) * mm});
            skLineSegment(sketch, "E2780", {"start": v(42347.93, 67801.08) * mm, "end": v(42347.81, 67801.47) * mm});
            skLineSegment(sketch, "E2781", {"start": v(42347.81, 67801.47) * mm, "end": v(42347.69, 67801.89) * mm});
            skLineSegment(sketch, "E2782", {"start": v(42347.69, 67801.89) * mm, "end": v(42347.55, 67802.33) * mm});
            skLineSegment(sketch, "E2783", {"start": v(42347.55, 67802.33) * mm, "end": v(42347.41, 67802.8) * mm});
            skLineSegment(sketch, "E2784", {"start": v(42347.41, 67802.8) * mm, "end": v(42347.27, 67803.28) * mm});
            skLineSegment(sketch, "E2785", {"start": v(42347.27, 67803.28) * mm, "end": v(42347.11, 67803.79) * mm});
            skLineSegment(sketch, "E2786", {"start": v(42347.11, 67803.79) * mm, "end": v(42346.95, 67804.32) * mm});
            skLineSegment(sketch, "E2787", {"start": v(42346.95, 67804.32) * mm, "end": v(42346.78, 67804.87) * mm});
            skLineSegment(sketch, "E2788", {"start": v(42346.78, 67804.87) * mm, "end": v(42346.61, 67805.45) * mm});
            skLineSegment(sketch, "E2789", {"start": v(42346.61, 67805.45) * mm, "end": v(42346.43, 67806.04) * mm});
            skLineSegment(sketch, "E2790", {"start": v(42346.43, 67806.04) * mm, "end": v(42346.25, 67806.65) * mm});
            skLineSegment(sketch, "E2791", {"start": v(42346.25, 67806.65) * mm, "end": v(42346.06, 67807.28) * mm});
            skLineSegment(sketch, "E2792", {"start": v(42346.06, 67807.28) * mm, "end": v(42345.86, 67807.92) * mm});
            skLineSegment(sketch, "E2793", {"start": v(42345.86, 67807.92) * mm, "end": v(42345.66, 67808.58) * mm});
            skLineSegment(sketch, "E2794", {"start": v(42345.66, 67808.58) * mm, "end": v(42345.46, 67809.26) * mm});
            skLineSegment(sketch, "E2795", {"start": v(42345.46, 67809.26) * mm, "end": v(42345.25, 67809.94) * mm});
            skLineSegment(sketch, "E2796", {"start": v(42345.25, 67809.94) * mm, "end": v(42345.04, 67810.64) * mm});
            skLineSegment(sketch, "E2797", {"start": v(42345.04, 67810.64) * mm, "end": v(42344.82, 67811.35) * mm});
            skLineSegment(sketch, "E2798", {"start": v(42344.82, 67811.35) * mm, "end": v(42344.6, 67812.07) * mm});
            skLineSegment(sketch, "E2799", {"start": v(42344.6, 67812.07) * mm, "end": v(42344.38, 67812.8) * mm});
            skLineSegment(sketch, "E2800", {"start": v(42344.38, 67812.8) * mm, "end": v(42344.16, 67813.54) * mm});
            skLineSegment(sketch, "E2801", {"start": v(42344.16, 67813.54) * mm, "end": v(42343.94, 67814.28) * mm});
            skLineSegment(sketch, "E2802", {"start": v(42343.94, 67814.28) * mm, "end": v(42343.7, 67815.03) * mm});
            skLineSegment(sketch, "E2803", {"start": v(42343.7, 67815.03) * mm, "end": v(42343.48, 67815.78) * mm});
            skLineSegment(sketch, "E2804", {"start": v(42343.48, 67815.78) * mm, "end": v(42343.25, 67816.53) * mm});
            skLineSegment(sketch, "E2805", {"start": v(42343.25, 67816.53) * mm, "end": v(42343.02, 67817.3) * mm});
            skLineSegment(sketch, "E2806", {"start": v(42343.02, 67817.3) * mm, "end": v(42342.96, 67817.5) * mm});
            skLineSegment(sketch, "E2807", {"start": v(42342.96, 67817.5) * mm, "end": v(42342.73, 67818.25) * mm});
            skLineSegment(sketch, "E2808", {"start": v(42342.73, 67818.25) * mm, "end": v(42342.5, 67819) * mm});
            skLineSegment(sketch, "E2809", {"start": v(42342.5, 67819) * mm, "end": v(42342.28, 67819.76) * mm});
            skLineSegment(sketch, "E2810", {"start": v(42342.28, 67819.76) * mm, "end": v(42342.05, 67820.5) * mm});
            skLineSegment(sketch, "E2811", {"start": v(42342.05, 67820.5) * mm, "end": v(42341.83, 67821.25) * mm});
            skLineSegment(sketch, "E2812", {"start": v(42341.83, 67821.25) * mm, "end": v(42341.6, 67821.99) * mm});
            skLineSegment(sketch, "E2813", {"start": v(42341.6, 67821.99) * mm, "end": v(42341.38, 67822.72) * mm});
            skLineSegment(sketch, "E2814", {"start": v(42341.38, 67822.72) * mm, "end": v(42341.16, 67823.44) * mm});
            skLineSegment(sketch, "E2815", {"start": v(42341.16, 67823.44) * mm, "end": v(42340.95, 67824.16) * mm});
            skLineSegment(sketch, "E2816", {"start": v(42340.95, 67824.16) * mm, "end": v(42340.73, 67824.86) * mm});
            skLineSegment(sketch, "E2817", {"start": v(42340.73, 67824.86) * mm, "end": v(42340.53, 67825.55) * mm});
            skLineSegment(sketch, "E2818", {"start": v(42340.53, 67825.55) * mm, "end": v(42340.32, 67826.23) * mm});
            skLineSegment(sketch, "E2819", {"start": v(42340.32, 67826.23) * mm, "end": v(42340.12, 67826.9) * mm});
            skLineSegment(sketch, "E2820", {"start": v(42340.12, 67826.9) * mm, "end": v(42339.92, 67827.54) * mm});
            skLineSegment(sketch, "E2821", {"start": v(42339.92, 67827.54) * mm, "end": v(42339.73, 67828.17) * mm});
            skLineSegment(sketch, "E2822", {"start": v(42339.73, 67828.17) * mm, "end": v(42339.54, 67828.79) * mm});
            skLineSegment(sketch, "E2823", {"start": v(42339.54, 67828.79) * mm, "end": v(42339.36, 67829.39) * mm});
            skLineSegment(sketch, "E2824", {"start": v(42339.36, 67829.39) * mm, "end": v(42339.19, 67829.96) * mm});
            skLineSegment(sketch, "E2825", {"start": v(42339.19, 67829.96) * mm, "end": v(42339.02, 67830.52) * mm});
            skLineSegment(sketch, "E2826", {"start": v(42339.02, 67830.52) * mm, "end": v(42338.86, 67831.06) * mm});
            skLineSegment(sketch, "E2827", {"start": v(42338.86, 67831.06) * mm, "end": v(42338.7, 67831.58) * mm});
            skLineSegment(sketch, "E2828", {"start": v(42338.7, 67831.58) * mm, "end": v(42338.55, 67832.07) * mm});
            skLineSegment(sketch, "E2829", {"start": v(42338.55, 67832.07) * mm, "end": v(42338.4, 67832.54) * mm});
            skLineSegment(sketch, "E2830", {"start": v(42338.4, 67832.54) * mm, "end": v(42338.27, 67832.99) * mm});
            skLineSegment(sketch, "E2831", {"start": v(42338.27, 67832.99) * mm, "end": v(42338.15, 67833.4) * mm});
            skLineSegment(sketch, "E2832", {"start": v(42338.15, 67833.4) * mm, "end": v(42338.03, 67833.8) * mm});
            skLineSegment(sketch, "E2833", {"start": v(42338.03, 67833.8) * mm, "end": v(42337.91, 67834.17) * mm});
            skLineSegment(sketch, "E2834", {"start": v(42337.91, 67834.17) * mm, "end": v(42337.81, 67834.52) * mm});
            skLineSegment(sketch, "E2835", {"start": v(42337.81, 67834.52) * mm, "end": v(42337.72, 67834.83) * mm});
            skLineSegment(sketch, "E2836", {"start": v(42337.72, 67834.83) * mm, "end": v(42337.63, 67835.12) * mm});
            skLineSegment(sketch, "E2837", {"start": v(42337.63, 67835.12) * mm, "end": v(42337.55, 67835.38) * mm});
            skLineSegment(sketch, "E2838", {"start": v(42337.55, 67835.38) * mm, "end": v(42337.48, 67835.61) * mm});
            skLineSegment(sketch, "E2839", {"start": v(42337.48, 67835.61) * mm, "end": v(42337.42, 67835.81) * mm});
            skLineSegment(sketch, "E2840", {"start": v(42337.42, 67835.81) * mm, "end": v(42337.37, 67835.99) * mm});
            skLineSegment(sketch, "E2841", {"start": v(42337.37, 67835.99) * mm, "end": v(42337.32, 67836.13) * mm});
            skLineSegment(sketch, "E2842", {"start": v(42337.32, 67836.13) * mm, "end": v(42337.29, 67836.24) * mm});
            skLineSegment(sketch, "E2843", {"start": v(42337.29, 67836.24) * mm, "end": v(42337.26, 67836.33) * mm});
            skLineSegment(sketch, "E2844", {"start": v(42337.26, 67836.33) * mm, "end": v(42337.25, 67836.38) * mm});
            skLineSegment(sketch, "E2845", {"start": v(42337.25, 67836.38) * mm, "end": v(42337.24, 67836.4) * mm});
            skLineSegment(sketch, "E2846", {"start": v(42337.24, 67836.4) * mm, "end": v(42337.23, 67836.45) * mm});
            skLineSegment(sketch, "E2847", {"start": v(42337.23, 67836.45) * mm, "end": v(42337.17, 67836.62) * mm});
            skLineSegment(sketch, "E2848", {"start": v(42337.17, 67836.62) * mm, "end": v(42337.1, 67836.78) * mm});
            skLineSegment(sketch, "E2849", {"start": v(42337.1, 67836.78) * mm, "end": v(42337.04, 67836.94) * mm});
            skLineSegment(sketch, "E2850", {"start": v(42337.04, 67836.94) * mm, "end": v(42336.96, 67837.1) * mm});
            skLineSegment(sketch, "E2851", {"start": v(42336.96, 67837.1) * mm, "end": v(42336.88, 67837.25) * mm});
            skLineSegment(sketch, "E2852", {"start": v(42336.88, 67837.25) * mm, "end": v(42336.8, 67837.4) * mm});
            skLineSegment(sketch, "E2853", {"start": v(42336.8, 67837.4) * mm, "end": v(42336.7, 67837.55) * mm});
            skLineSegment(sketch, "E2854", {"start": v(42336.7, 67837.55) * mm, "end": v(42336.6, 67837.69) * mm});
            skLineSegment(sketch, "E2855", {"start": v(42336.6, 67837.69) * mm, "end": v(42336.5, 67837.83) * mm});
            skLineSegment(sketch, "E2856", {"start": v(42336.5, 67837.83) * mm, "end": v(42336.39, 67837.96) * mm});
            skLineSegment(sketch, "E2857", {"start": v(42336.39, 67837.96) * mm, "end": v(42336.27, 67838.1) * mm});
            skLineSegment(sketch, "E2858", {"start": v(42336.27, 67838.1) * mm, "end": v(42336.15, 67838.22) * mm});
            skLineSegment(sketch, "E2859", {"start": v(42336.15, 67838.22) * mm, "end": v(42336.03, 67838.34) * mm});
            skLineSegment(sketch, "E2860", {"start": v(42336.03, 67838.34) * mm, "end": v(42335.9, 67838.45) * mm});
            skLineSegment(sketch, "E2861", {"start": v(42335.9, 67838.45) * mm, "end": v(42335.76, 67838.57) * mm});
            skLineSegment(sketch, "E2862", {"start": v(42335.76, 67838.57) * mm, "end": v(42335.62, 67838.67) * mm});
            skLineSegment(sketch, "E2863", {"start": v(42335.62, 67838.67) * mm, "end": v(42335.48, 67838.77) * mm});
            skLineSegment(sketch, "E2864", {"start": v(42335.48, 67838.77) * mm, "end": v(42335.34, 67838.86) * mm});
            skLineSegment(sketch, "E2865", {"start": v(42335.34, 67838.86) * mm, "end": v(42335.18, 67838.95) * mm});
            skLineSegment(sketch, "E2866", {"start": v(42335.18, 67838.95) * mm, "end": v(42335.03, 67839.03) * mm});
            skLineSegment(sketch, "E2867", {"start": v(42335.03, 67839.03) * mm, "end": v(42334.87, 67839.1) * mm});
            skLineSegment(sketch, "E2868", {"start": v(42334.87, 67839.1) * mm, "end": v(42334.71, 67839.17) * mm});
            skLineSegment(sketch, "E2869", {"start": v(42334.71, 67839.17) * mm, "end": v(42334.55, 67839.24) * mm});
            skLineSegment(sketch, "E2870", {"start": v(42334.55, 67839.24) * mm, "end": v(42334.39, 67839.3) * mm});
            skLineSegment(sketch, "E2871", {"start": v(42334.39, 67839.3) * mm, "end": v(42334.22, 67839.34) * mm});
            skLineSegment(sketch, "E2872", {"start": v(42334.22, 67839.34) * mm, "end": v(42334.05, 67839.38) * mm});
            skLineSegment(sketch, "E2873", {"start": v(42334.05, 67839.38) * mm, "end": v(42333.88, 67839.42) * mm});
            skLineSegment(sketch, "E2874", {"start": v(42333.88, 67839.42) * mm, "end": v(42333.7, 67839.45) * mm});
            skLineSegment(sketch, "E2875", {"start": v(42333.7, 67839.45) * mm, "end": v(42333.54, 67839.47) * mm});
            skLineSegment(sketch, "E2876", {"start": v(42333.54, 67839.47) * mm, "end": v(42333.36, 67839.49) * mm});
            skLineSegment(sketch, "E2877", {"start": v(42333.36, 67839.49) * mm, "end": v(42333.19, 67839.5) * mm});
            skLineSegment(sketch, "E2878", {"start": v(42333.19, 67839.5) * mm, "end": v(42333.02, 67839.5) * mm});
            skLineSegment(sketch, "E2879", {"start": v(42333.02, 67839.5) * mm, "end": v(42332.84, 67839.49) * mm});
            skLineSegment(sketch, "E2880", {"start": v(42332.84, 67839.49) * mm, "end": v(42332.67, 67839.48) * mm});
            skLineSegment(sketch, "E2881", {"start": v(42332.67, 67839.48) * mm, "end": v(42332.5, 67839.46) * mm});
            skLineSegment(sketch, "E2882", {"start": v(42332.5, 67839.46) * mm, "end": v(42332.32, 67839.43) * mm});
            skLineSegment(sketch, "E2883", {"start": v(42332.32, 67839.43) * mm, "end": v(42332.15, 67839.4) * mm});
            skLineSegment(sketch, "E2884", {"start": v(42332.15, 67839.4) * mm, "end": v(42331.98, 67839.36) * mm});
            skLineSegment(sketch, "E2885", {"start": v(42331.98, 67839.36) * mm, "end": v(42331.82, 67839.3) * mm});
            skLineSegment(sketch, "E2886", {"start": v(42331.82, 67839.3) * mm, "end": v(42330.99, 67839.06) * mm});
            skLineSegment(sketch, "E2887", {"start": v(42502.84, 67758.68) * mm, "end": v(42503.3, 67758.54) * mm});
            skLineSegment(sketch, "E2888", {"start": v(42503.3, 67758.54) * mm, "end": v(42503.77, 67758.42) * mm});
            skLineSegment(sketch, "E2889", {"start": v(42503.77, 67758.42) * mm, "end": v(42504.24, 67758.31) * mm});
            skLineSegment(sketch, "E2890", {"start": v(42504.24, 67758.31) * mm, "end": v(42504.72, 67758.23) * mm});
            skLineSegment(sketch, "E2891", {"start": v(42504.72, 67758.23) * mm, "end": v(42505.2, 67758.16) * mm});
            skLineSegment(sketch, "E2892", {"start": v(42505.2, 67758.16) * mm, "end": v(42505.68, 67758.12) * mm});
            skLineSegment(sketch, "E2893", {"start": v(42505.68, 67758.12) * mm, "end": v(42506.16, 67758.09) * mm});
            skLineSegment(sketch, "E2894", {"start": v(42506.16, 67758.09) * mm, "end": v(42506.65, 67758.08) * mm});
            skLineSegment(sketch, "E2895", {"start": v(42506.65, 67758.08) * mm, "end": v(42507.13, 67758.1) * mm});
            skLineSegment(sketch, "E2896", {"start": v(42507.13, 67758.1) * mm, "end": v(42507.61, 67758.12) * mm});
            skLineSegment(sketch, "E2897", {"start": v(42507.61, 67758.12) * mm, "end": v(42508.1, 67758.17) * mm});
            skLineSegment(sketch, "E2898", {"start": v(42508.1, 67758.17) * mm, "end": v(42508.57, 67758.24) * mm});
            skLineSegment(sketch, "E2899", {"start": v(42508.57, 67758.24) * mm, "end": v(42509.05, 67758.33) * mm});
            skLineSegment(sketch, "E2900", {"start": v(42509.05, 67758.33) * mm, "end": v(42509.52, 67758.44) * mm});
            skLineSegment(sketch, "E2901", {"start": v(42509.52, 67758.44) * mm, "end": v(42509.99, 67758.56) * mm});
            skLineSegment(sketch, "E2902", {"start": v(42509.99, 67758.56) * mm, "end": v(42510.45, 67758.7) * mm});
            skLineSegment(sketch, "E2903", {"start": v(42510.45, 67758.7) * mm, "end": v(42510.9, 67758.87) * mm});
            skLineSegment(sketch, "E2904", {"start": v(42510.9, 67758.87) * mm, "end": v(42511.36, 67759.05) * mm});
            skLineSegment(sketch, "E2905", {"start": v(42511.36, 67759.05) * mm, "end": v(42511.8, 67759.25) * mm});
            skLineSegment(sketch, "E2906", {"start": v(42511.8, 67759.25) * mm, "end": v(42512.23, 67759.47) * mm});
            skLineSegment(sketch, "E2907", {"start": v(42512.23, 67759.47) * mm, "end": v(42512.64, 67759.69) * mm});
            skLineSegment(sketch, "E2908", {"start": v(42512.64, 67759.69) * mm, "end": v(42512.78, 67759.77) * mm});
            skArc(sketch, "E2909", {"start": v(42512.78, 67759.77) * mm, "mid": v(42512.76, 67759.76) * mm, "end": v(42512.73, 67759.74) * mm});
            skArc(sketch, "E2910", {"start": v(42512.73, 67759.74) * mm, "mid": v(42512.38, 67759.55) * mm, "end": v(42512.02, 67759.37) * mm});
            skLineSegment(sketch, "E2911", {"start": v(42512.02, 67759.37) * mm, "end": v(42512, 67759.36) * mm});
            skArc(sketch, "E2912", {"start": v(42512, 67759.36) * mm, "mid": v(42511.6, 67759.18) * mm, "end": v(42511.21, 67759.01) * mm});
            skLineSegment(sketch, "E2913", {"start": v(42511.21, 67759.01) * mm, "end": v(42510.98, 67758.93) * mm});
            skArc(sketch, "E2914", {"start": v(42510.98, 67758.93) * mm, "mid": v(42510.76, 67758.84) * mm, "end": v(42510.53, 67758.77) * mm});
            skLineSegment(sketch, "E2915", {"start": v(42510.53, 67758.77) * mm, "end": v(42510.32, 67758.7) * mm});
            skArc(sketch, "E2916", {"start": v(42510.32, 67758.7) * mm, "mid": v(42510.3, 67758.7) * mm, "end": v(42510.27, 67758.69) * mm});
            skLineSegment(sketch, "E2917", {"start": v(42361.34, 67804.1) * mm, "end": v(42361.38, 67803.96) * mm});
            skLineSegment(sketch, "E2918", {"start": v(42361.38, 67803.96) * mm, "end": v(42361.42, 67803.85) * mm});
            skLineSegment(sketch, "E2919", {"start": v(42361.42, 67803.85) * mm, "end": v(42361.44, 67803.77) * mm});
            skLineSegment(sketch, "E2920", {"start": v(42361.44, 67803.77) * mm, "end": v(42361.46, 67803.72) * mm});
            skLineSegment(sketch, "E2921", {"start": v(42361.46, 67803.72) * mm, "end": v(42361.46, 67803.7) * mm});
            skLineSegment(sketch, "E2922", {"start": v(42361.46, 67803.7) * mm, "end": v(42361.48, 67803.65) * mm});
            skLineSegment(sketch, "E2923", {"start": v(42361.48, 67803.65) * mm, "end": v(42361.49, 67803.6) * mm});
            skLineSegment(sketch, "E2924", {"start": v(42361.49, 67803.6) * mm, "end": v(42361.5, 67803.55) * mm});
            skLineSegment(sketch, "E2925", {"start": v(42361.5, 67803.55) * mm, "end": v(42361.5, 67803.5) * mm});
            skLineSegment(sketch, "E2926", {"start": v(42361.5, 67803.5) * mm, "end": v(42361.51, 67803.45) * mm});
            skLineSegment(sketch, "E2927", {"start": v(42361.51, 67803.45) * mm, "end": v(42361.52, 67803.4) * mm});
            skLineSegment(sketch, "E2928", {"start": v(42361.52, 67803.4) * mm, "end": v(42361.52, 67803.35) * mm});
            skLineSegment(sketch, "E2929", {"start": v(42361.52, 67803.35) * mm, "end": v(42361.52, 67803.3) * mm});
            skLineSegment(sketch, "E2930", {"start": v(42361.52, 67803.3) * mm, "end": v(42361.51, 67803.25) * mm});
            skLineSegment(sketch, "E2931", {"start": v(42361.51, 67803.25) * mm, "end": v(42361.5, 67803.2) * mm});
            skLineSegment(sketch, "E2932", {"start": v(42361.5, 67803.2) * mm, "end": v(42361.5, 67803.15) * mm});
            skLineSegment(sketch, "E2933", {"start": v(42361.5, 67803.15) * mm, "end": v(42361.5, 67803.1) * mm});
            skLineSegment(sketch, "E2934", {"start": v(42361.5, 67803.1) * mm, "end": v(42361.48, 67803.05) * mm});
            skLineSegment(sketch, "E2935", {"start": v(42361.48, 67803.05) * mm, "end": v(42361.47, 67803) * mm});
            skLineSegment(sketch, "E2936", {"start": v(42361.47, 67803) * mm, "end": v(42361.46, 67802.95) * mm});
            skLineSegment(sketch, "E2937", {"start": v(42361.46, 67802.95) * mm, "end": v(42361.44, 67802.9) * mm});
            skLineSegment(sketch, "E2938", {"start": v(42361.44, 67802.9) * mm, "end": v(42361.42, 67802.85) * mm});
            skLineSegment(sketch, "E2939", {"start": v(42361.42, 67802.85) * mm, "end": v(42361.4, 67802.8) * mm});
            skLineSegment(sketch, "E2940", {"start": v(42361.4, 67802.8) * mm, "end": v(42361.38, 67802.76) * mm});
            skLineSegment(sketch, "E2941", {"start": v(42361.38, 67802.76) * mm, "end": v(42361.36, 67802.71) * mm});
            skLineSegment(sketch, "E2942", {"start": v(42361.36, 67802.71) * mm, "end": v(42361.33, 67802.67) * mm});
            skLineSegment(sketch, "E2943", {"start": v(42361.33, 67802.67) * mm, "end": v(42361.3, 67802.63) * mm});
            skLineSegment(sketch, "E2944", {"start": v(42361.3, 67802.63) * mm, "end": v(42361.28, 67802.58) * mm});
            skLineSegment(sketch, "E2945", {"start": v(42361.28, 67802.58) * mm, "end": v(42361.25, 67802.54) * mm});
            skLineSegment(sketch, "E2946", {"start": v(42361.25, 67802.54) * mm, "end": v(42361.21, 67802.5) * mm});
            skLineSegment(sketch, "E2947", {"start": v(42361.21, 67802.5) * mm, "end": v(42361.18, 67802.47) * mm});
            skLineSegment(sketch, "E2948", {"start": v(42361.18, 67802.47) * mm, "end": v(42361.14, 67802.43) * mm});
            skLineSegment(sketch, "E2949", {"start": v(42361.14, 67802.43) * mm, "end": v(42361.1, 67802.4) * mm});
            skLineSegment(sketch, "E2950", {"start": v(42361.1, 67802.4) * mm, "end": v(42361.07, 67802.36) * mm});
            skLineSegment(sketch, "E2951", {"start": v(42361.07, 67802.36) * mm, "end": v(42361.03, 67802.33) * mm});
            skLineSegment(sketch, "E2952", {"start": v(42361.03, 67802.33) * mm, "end": v(42360.99, 67802.3) * mm});
            skLineSegment(sketch, "E2953", {"start": v(42360.99, 67802.3) * mm, "end": v(42360.95, 67802.27) * mm});
            skLineSegment(sketch, "E2954", {"start": v(42360.95, 67802.27) * mm, "end": v(42360.9, 67802.24) * mm});
            skLineSegment(sketch, "E2955", {"start": v(42360.9, 67802.24) * mm, "end": v(42360.86, 67802.22) * mm});
            skLineSegment(sketch, "E2956", {"start": v(42360.86, 67802.22) * mm, "end": v(42360.81, 67802.2) * mm});
            skLineSegment(sketch, "E2957", {"start": v(42360.81, 67802.2) * mm, "end": v(42360.77, 67802.17) * mm});
            skLineSegment(sketch, "E2958", {"start": v(42360.77, 67802.17) * mm, "end": v(42360.72, 67802.15) * mm});
            skLineSegment(sketch, "E2959", {"start": v(42360.72, 67802.15) * mm, "end": v(42360.67, 67802.13) * mm});
            skLineSegment(sketch, "E2960", {"start": v(42360.67, 67802.13) * mm, "end": v(42360.63, 67802.12) * mm});
            skLineSegment(sketch, "E2961", {"start": v(42360.63, 67802.12) * mm, "end": v(42360.61, 67802.11) * mm});
            skLineSegment(sketch, "E2962", {"start": v(42360.61, 67802.11) * mm, "end": v(42360.5, 67802.08) * mm});
            skLineSegment(sketch, "E2963", {"start": v(42360.5, 67802.08) * mm, "end": v(42360.4, 67802.06) * mm});
            skLineSegment(sketch, "E2964", {"start": v(42360.4, 67802.06) * mm, "end": v(42360.3, 67802.04) * mm});
            skLineSegment(sketch, "E2965", {"start": v(42360.3, 67802.04) * mm, "end": v(42360.2, 67802.02) * mm});
            skLineSegment(sketch, "E2966", {"start": v(42360.2, 67802.02) * mm, "end": v(42360.08, 67802) * mm});
            skLineSegment(sketch, "E2967", {"start": v(42360.08, 67802) * mm, "end": v(42359.98, 67802) * mm});
            skLineSegment(sketch, "E2968", {"start": v(42359.98, 67802) * mm, "end": v(42359.87, 67802) * mm});
            skLineSegment(sketch, "E2969", {"start": v(42359.87, 67802) * mm, "end": v(42359.76, 67802) * mm});
            skLineSegment(sketch, "E2970", {"start": v(42359.76, 67802) * mm, "end": v(42359.7, 67802) * mm});
            skLineSegment(sketch, "E2971", {"start": v(42359.7, 67802) * mm, "end": v(42359.18, 67802.02) * mm});
            skLineSegment(sketch, "E2972", {"start": v(42359.18, 67802.02) * mm, "end": v(42358.68, 67802.03) * mm});
            skLineSegment(sketch, "E2973", {"start": v(42358.68, 67802.03) * mm, "end": v(42358.17, 67802.01) * mm});
            skLineSegment(sketch, "E2974", {"start": v(42358.17, 67802.01) * mm, "end": v(42357.67, 67801.98) * mm});
            skLineSegment(sketch, "E2975", {"start": v(42357.67, 67801.98) * mm, "end": v(42357.16, 67801.92) * mm});
            skLineSegment(sketch, "E2976", {"start": v(42357.16, 67801.92) * mm, "end": v(42356.66, 67801.84) * mm});
            skLineSegment(sketch, "E2977", {"start": v(42356.66, 67801.84) * mm, "end": v(42356.17, 67801.75) * mm});
            skLineSegment(sketch, "E2978", {"start": v(42356.17, 67801.75) * mm, "end": v(42355.67, 67801.63) * mm});
            skLineSegment(sketch, "E2979", {"start": v(42355.67, 67801.63) * mm, "end": v(42355.19, 67801.5) * mm});
            skLineSegment(sketch, "E2980", {"start": v(42355.19, 67801.5) * mm, "end": v(42354.7, 67801.34) * mm});
            skLineSegment(sketch, "E2981", {"start": v(42354.7, 67801.34) * mm, "end": v(42354.23, 67801.16) * mm});
            skLineSegment(sketch, "E2982", {"start": v(42354.23, 67801.16) * mm, "end": v(42353.76, 67800.97) * mm});
            skLineSegment(sketch, "E2983", {"start": v(42353.76, 67800.97) * mm, "end": v(42353.3, 67800.76) * mm});
            skLineSegment(sketch, "E2984", {"start": v(42353.3, 67800.76) * mm, "end": v(42352.85, 67800.53) * mm});
            skLineSegment(sketch, "E2985", {"start": v(42352.85, 67800.53) * mm, "end": v(42352.4, 67800.28) * mm});
            skLineSegment(sketch, "E2986", {"start": v(42352.4, 67800.28) * mm, "end": v(42351.98, 67800.02) * mm});
            skLineSegment(sketch, "E2987", {"start": v(42351.98, 67800.02) * mm, "end": v(42351.56, 67799.73) * mm});
            skLineSegment(sketch, "E2988", {"start": v(42351.56, 67799.73) * mm, "end": v(42351.15, 67799.43) * mm});
            skLineSegment(sketch, "E2989", {"start": v(42351.15, 67799.43) * mm, "end": v(42351.1, 67799.4) * mm});
            skLineSegment(sketch, "E2990", {"start": v(42351.1, 67799.4) * mm, "end": v(42351, 67799.32) * mm});
            skLineSegment(sketch, "E2991", {"start": v(42351, 67799.32) * mm, "end": v(42350.9, 67799.25) * mm});
            skLineSegment(sketch, "E2992", {"start": v(42350.9, 67799.25) * mm, "end": v(42350.78, 67799.18) * mm});
            skLineSegment(sketch, "E2993", {"start": v(42350.78, 67799.18) * mm, "end": v(42350.67, 67799.12) * mm});
            skLineSegment(sketch, "E2994", {"start": v(42350.67, 67799.12) * mm, "end": v(42350.55, 67799.06) * mm});
            skLineSegment(sketch, "E2995", {"start": v(42350.55, 67799.06) * mm, "end": v(42350.43, 67799) * mm});
            skLineSegment(sketch, "E2996", {"start": v(42350.43, 67799) * mm, "end": v(42350.31, 67798.95) * mm});
            skLineSegment(sketch, "E2997", {"start": v(42350.31, 67798.95) * mm, "end": v(42350.19, 67798.9) * mm});
            skLineSegment(sketch, "E2998", {"start": v(42350.19, 67798.9) * mm, "end": v(42350.06, 67798.86) * mm});
            skLineSegment(sketch, "E2999", {"start": v(42350.06, 67798.86) * mm, "end": v(42349.94, 67798.83) * mm});
            skLineSegment(sketch, "E3000", {"start": v(42349.94, 67798.83) * mm, "end": v(42349.81, 67798.8) * mm});
            skLineSegment(sketch, "E3001", {"start": v(42349.81, 67798.8) * mm, "end": v(42349.68, 67798.77) * mm});
            skLineSegment(sketch, "E3002", {"start": v(42349.68, 67798.77) * mm, "end": v(42349.55, 67798.75) * mm});
            skLineSegment(sketch, "E3003", {"start": v(42349.55, 67798.75) * mm, "end": v(42349.48, 67798.74) * mm});
            skLineSegment(sketch, "E3004", {"start": v(42349.48, 67798.74) * mm, "end": v(42348.94, 67797.74) * mm});
            skLineSegment(sketch, "E3005", {"start": v(42369.88, 67846.37) * mm, "end": v(42381.24, 67808.84) * mm});
            skLineSegment(sketch, "E3006", {"start": v(42381.24, 67808.84) * mm, "end": v(42381.94, 67806.53) * mm});
            skLineSegment(sketch, "E3007", {"start": v(42381.94, 67806.53) * mm, "end": v(42389.23, 67782.44) * mm});
            skLineSegment(sketch, "E3008", {"start": v(42389.23, 67782.44) * mm, "end": v(42390.11, 67779.53) * mm});
            skLineSegment(sketch, "E3009", {"start": v(42390.11, 67779.53) * mm, "end": v(42372.03, 67774.05) * mm});
            skLineSegment(sketch, "E3010", {"start": v(42372.03, 67774.05) * mm, "end": v(42371.15, 67776.97) * mm});
            skLineSegment(sketch, "E3011", {"start": v(42371.15, 67776.97) * mm, "end": v(42363.86, 67801.05) * mm});
            skLineSegment(sketch, "E3012", {"start": v(42363.86, 67801.05) * mm, "end": v(42363.16, 67803.37) * mm});
            skLineSegment(sketch, "E3013", {"start": v(42363.16, 67803.37) * mm, "end": v(42351.8, 67840.9) * mm});
            skLineSegment(sketch, "E3014", {"start": v(42337.24, 67836.4) * mm, "end": v(42337.24, 67836.4) * mm});
            skLineSegment(sketch, "E3015", {"start": v(42337.24, 67836.4) * mm, "end": v(42337.26, 67836.34) * mm});
            skLineSegment(sketch, "E3016", {"start": v(42337.26, 67836.34) * mm, "end": v(42337.28, 67836.27) * mm});
            skLineSegment(sketch, "E3017", {"start": v(42337.28, 67836.27) * mm, "end": v(42337.31, 67836.16) * mm});
            skLineSegment(sketch, "E3018", {"start": v(42337.31, 67836.16) * mm, "end": v(42337.35, 67836.03) * mm});
            skLineSegment(sketch, "E3019", {"start": v(42337.35, 67836.03) * mm, "end": v(42337.4, 67835.86) * mm});
            skLineSegment(sketch, "E3020", {"start": v(42337.4, 67835.86) * mm, "end": v(42337.46, 67835.67) * mm});
            skLineSegment(sketch, "E3021", {"start": v(42337.46, 67835.67) * mm, "end": v(42337.53, 67835.45) * mm});
            skLineSegment(sketch, "E3022", {"start": v(42337.53, 67835.45) * mm, "end": v(42337.6, 67835.2) * mm});
            skLineSegment(sketch, "E3023", {"start": v(42337.6, 67835.2) * mm, "end": v(42337.7, 67834.91) * mm});
            skLineSegment(sketch, "E3024", {"start": v(42337.7, 67834.91) * mm, "end": v(42337.78, 67834.6) * mm});
            skLineSegment(sketch, "E3025", {"start": v(42337.78, 67834.6) * mm, "end": v(42337.89, 67834.27) * mm});
            skLineSegment(sketch, "E3026", {"start": v(42337.89, 67834.27) * mm, "end": v(42338, 67833.9) * mm});
            skLineSegment(sketch, "E3027", {"start": v(42338, 67833.9) * mm, "end": v(42338.11, 67833.52) * mm});
            skLineSegment(sketch, "E3028", {"start": v(42338.11, 67833.52) * mm, "end": v(42338.24, 67833.1) * mm});
            skLineSegment(sketch, "E3029", {"start": v(42338.24, 67833.1) * mm, "end": v(42338.37, 67832.66) * mm});
            skLineSegment(sketch, "E3030", {"start": v(42338.37, 67832.66) * mm, "end": v(42338.51, 67832.2) * mm});
            skLineSegment(sketch, "E3031", {"start": v(42338.51, 67832.2) * mm, "end": v(42338.66, 67831.71) * mm});
            skLineSegment(sketch, "E3032", {"start": v(42369.83, 67846.52) * mm, "end": v(42351.75, 67841.05) * mm});
            skLineSegment(sketch, "E3033", {"start": v(42350.7, 67839.23) * mm, "end": v(42350.71, 67839.22) * mm});
            skLineSegment(sketch, "E3034", {"start": v(42350.71, 67839.22) * mm, "end": v(42350.72, 67839.18) * mm});
            skLineSegment(sketch, "E3035", {"start": v(42350.72, 67839.18) * mm, "end": v(42350.75, 67839.1) * mm});
            skLineSegment(sketch, "E3036", {"start": v(42350.75, 67839.1) * mm, "end": v(42350.78, 67839) * mm});
            skLineSegment(sketch, "E3037", {"start": v(42350.78, 67839) * mm, "end": v(42350.81, 67838.88) * mm});
            skLineSegment(sketch, "E3038", {"start": v(42363.16, 67803.37) * mm, "end": v(42381.24, 67808.84) * mm});
            skLineSegment(sketch, "E3039", {"start": v(42363.86, 67801.05) * mm, "end": v(42381.94, 67806.53) * mm});
            skLineSegment(sketch, "E3040", {"start": v(42347.2, 67803.52) * mm, "end": v(42348.24, 67800.07) * mm});
            skLineSegment(sketch, "E3041", {"start": v(42365.46, 67698.73) * mm, "end": v(42373.2, 67701.07) * mm});
            skLineSegment(sketch, "E3042", {"start": v(42357.26, 67753.71) * mm, "end": v(42349.53, 67751.37) * mm});
            skLineSegment(sketch, "E3043", {"start": v(42357.65, 67752.42) * mm, "end": v(42365.23, 67727.4) * mm});
            skLineSegment(sketch, "E3044", {"start": v(42365.23, 67727.4) * mm, "end": v(42372.8, 67702.36) * mm});
            skLineSegment(sketch, "E3045", {"start": v(42348.9, 67797.87) * mm, "end": v(42342.96, 67817.5) * mm});
            skLineSegment(sketch, "E3046", {"start": v(42342.96, 67817.5) * mm, "end": v(42337.26, 67836.35) * mm});
            skLineSegment(sketch, "E3047", {"start": v(42463.23, 67746.6) * mm, "end": v(42465.12, 67747.18) * mm});
            skLineSegment(sketch, "E3048", {"start": v(42465.12, 67747.18) * mm, "end": v(42467, 67747.75) * mm});
            skLineSegment(sketch, "E3049", {"start": v(42467, 67747.75) * mm, "end": v(42468.88, 67748.32) * mm});
            skLineSegment(sketch, "E3050", {"start": v(42468.88, 67748.32) * mm, "end": v(42470.75, 67748.88) * mm});
            skLineSegment(sketch, "E3051", {"start": v(42470.75, 67748.88) * mm, "end": v(42472.6, 67749.44) * mm});
            skLineSegment(sketch, "E3052", {"start": v(42472.6, 67749.44) * mm, "end": v(42474.44, 67750) * mm});
            skLineSegment(sketch, "E3053", {"start": v(42474.44, 67750) * mm, "end": v(42476.26, 67750.55) * mm});
            skLineSegment(sketch, "E3054", {"start": v(42476.26, 67750.55) * mm, "end": v(42478.05, 67751.1) * mm});
            skLineSegment(sketch, "E3055", {"start": v(42478.05, 67751.1) * mm, "end": v(42479.82, 67751.63) * mm});
            skLineSegment(sketch, "E3056", {"start": v(42479.82, 67751.63) * mm, "end": v(42481.56, 67752.16) * mm});
            skLineSegment(sketch, "E3057", {"start": v(42481.56, 67752.16) * mm, "end": v(42483.27, 67752.67) * mm});
            skLineSegment(sketch, "E3058", {"start": v(42483.27, 67752.67) * mm, "end": v(42484.95, 67753.18) * mm});
            skLineSegment(sketch, "E3059", {"start": v(42484.95, 67753.18) * mm, "end": v(42486.6, 67753.68) * mm});
            skLineSegment(sketch, "E3060", {"start": v(42486.6, 67753.68) * mm, "end": v(42488.2, 67754.16) * mm});
            skLineSegment(sketch, "E3061", {"start": v(42488.2, 67754.16) * mm, "end": v(42489.76, 67754.64) * mm});
            skLineSegment(sketch, "E3062", {"start": v(42489.76, 67754.64) * mm, "end": v(42491.28, 67755.1) * mm});
            skLineSegment(sketch, "E3063", {"start": v(42491.28, 67755.1) * mm, "end": v(42492.75, 67755.54) * mm});
            skLineSegment(sketch, "E3064", {"start": v(42492.75, 67755.54) * mm, "end": v(42494.17, 67755.97) * mm});
            skLineSegment(sketch, "E3065", {"start": v(42494.17, 67755.97) * mm, "end": v(42495.54, 67756.39) * mm});
            skLineSegment(sketch, "E3066", {"start": v(42495.54, 67756.39) * mm, "end": v(42496.86, 67756.79) * mm});
            skLineSegment(sketch, "E3067", {"start": v(42496.86, 67756.79) * mm, "end": v(42498.12, 67757.17) * mm});
            skLineSegment(sketch, "E3068", {"start": v(42498.12, 67757.17) * mm, "end": v(42499.33, 67757.53) * mm});
            skLineSegment(sketch, "E3069", {"start": v(42499.33, 67757.53) * mm, "end": v(42500.48, 67757.88) * mm});
            skLineSegment(sketch, "E3070", {"start": v(42500.48, 67757.88) * mm, "end": v(42501.56, 67758.2) * mm});
            skLineSegment(sketch, "E3071", {"start": v(42501.56, 67758.2) * mm, "end": v(42502.59, 67758.52) * mm});
            skLineSegment(sketch, "E3072", {"start": v(42502.59, 67758.52) * mm, "end": v(42503.55, 67758.8) * mm});
            skLineSegment(sketch, "E3073", {"start": v(42503.55, 67758.8) * mm, "end": v(42504.44, 67759.08) * mm});
            skLineSegment(sketch, "E3074", {"start": v(42504.44, 67759.08) * mm, "end": v(42505.27, 67759.33) * mm});
            skLineSegment(sketch, "E3075", {"start": v(42505.27, 67759.33) * mm, "end": v(42506.02, 67759.56) * mm});
            skLineSegment(sketch, "E3076", {"start": v(42506.02, 67759.56) * mm, "end": v(42506.71, 67759.77) * mm});
            skLineSegment(sketch, "E3077", {"start": v(42506.71, 67759.77) * mm, "end": v(42507.33, 67759.95) * mm});
            skLineSegment(sketch, "E3078", {"start": v(42507.33, 67759.95) * mm, "end": v(42507.87, 67760.12) * mm});
            skLineSegment(sketch, "E3079", {"start": v(42507.87, 67760.12) * mm, "end": v(42508.34, 67760.26) * mm});
            skLineSegment(sketch, "E3080", {"start": v(42508.34, 67760.26) * mm, "end": v(42508.74, 67760.38) * mm});
            skLineSegment(sketch, "E3081", {"start": v(42508.74, 67760.38) * mm, "end": v(42509.07, 67760.48) * mm});
            skLineSegment(sketch, "E3082", {"start": v(42509.07, 67760.48) * mm, "end": v(42509.31, 67760.55) * mm});
            skLineSegment(sketch, "E3083", {"start": v(42509.31, 67760.55) * mm, "end": v(42509.49, 67760.6) * mm});
            skLineSegment(sketch, "E3084", {"start": v(42509.49, 67760.6) * mm, "end": v(42509.59, 67760.64) * mm});
            skLineSegment(sketch, "E3085", {"start": v(42509.59, 67760.64) * mm, "end": v(42509.61, 67760.64) * mm});
            skLineSegment(sketch, "E3086", {"start": v(42503.82, 67779.79) * mm, "end": v(42503.78, 67779.78) * mm});
            skLineSegment(sketch, "E3087", {"start": v(42503.78, 67779.78) * mm, "end": v(42503.67, 67779.74) * mm});
            skLineSegment(sketch, "E3088", {"start": v(42503.67, 67779.74) * mm, "end": v(42503.48, 67779.68) * mm});
            skLineSegment(sketch, "E3089", {"start": v(42503.48, 67779.68) * mm, "end": v(42503.21, 67779.6) * mm});
            skLineSegment(sketch, "E3090", {"start": v(42503.21, 67779.6) * mm, "end": v(42502.88, 67779.5) * mm});
            skLineSegment(sketch, "E3091", {"start": v(42502.88, 67779.5) * mm, "end": v(42502.46, 67779.38) * mm});
            skLineSegment(sketch, "E3092", {"start": v(42502.46, 67779.38) * mm, "end": v(42501.98, 67779.23) * mm});
            skLineSegment(sketch, "E3093", {"start": v(42501.98, 67779.23) * mm, "end": v(42501.42, 67779.06) * mm});
            skLineSegment(sketch, "E3094", {"start": v(42501.42, 67779.06) * mm, "end": v(42500.79, 67778.87) * mm});
            skLineSegment(sketch, "E3095", {"start": v(42500.79, 67778.87) * mm, "end": v(42500.09, 67778.66) * mm});
            skLineSegment(sketch, "E3096", {"start": v(42500.09, 67778.66) * mm, "end": v(42499.32, 67778.42) * mm});
            skLineSegment(sketch, "E3097", {"start": v(42499.32, 67778.42) * mm, "end": v(42498.48, 67778.17) * mm});
            skLineSegment(sketch, "E3098", {"start": v(42498.48, 67778.17) * mm, "end": v(42497.57, 67777.9) * mm});
            skLineSegment(sketch, "E3099", {"start": v(42497.57, 67777.9) * mm, "end": v(42496.6, 67777.6) * mm});
            skLineSegment(sketch, "E3100", {"start": v(42496.6, 67777.6) * mm, "end": v(42495.56, 67777.29) * mm});
            skLineSegment(sketch, "E3101", {"start": v(42495.56, 67777.29) * mm, "end": v(42494.47, 67776.96) * mm});
            skLineSegment(sketch, "E3102", {"start": v(42494.47, 67776.96) * mm, "end": v(42493.3, 67776.6) * mm});
            skLineSegment(sketch, "E3103", {"start": v(42493.3, 67776.6) * mm, "end": v(42492.09, 67776.24) * mm});
            skLineSegment(sketch, "E3104", {"start": v(42492.09, 67776.24) * mm, "end": v(42490.82, 67775.85) * mm});
            skLineSegment(sketch, "E3105", {"start": v(42490.82, 67775.85) * mm, "end": v(42489.49, 67775.45) * mm});
            skLineSegment(sketch, "E3106", {"start": v(42489.49, 67775.45) * mm, "end": v(42488.1, 67775.03) * mm});
            skLineSegment(sketch, "E3107", {"start": v(42488.1, 67775.03) * mm, "end": v(42486.67, 67774.6) * mm});
            skLineSegment(sketch, "E3108", {"start": v(42486.67, 67774.6) * mm, "end": v(42485.2, 67774.15) * mm});
            skLineSegment(sketch, "E3109", {"start": v(42485.2, 67774.15) * mm, "end": v(42483.66, 67773.69) * mm});
            skLineSegment(sketch, "E3110", {"start": v(42483.66, 67773.69) * mm, "end": v(42482.1, 67773.21) * mm});
            skLineSegment(sketch, "E3111", {"start": v(42482.1, 67773.21) * mm, "end": v(42480.48, 67772.72) * mm});
            skLineSegment(sketch, "E3112", {"start": v(42480.48, 67772.72) * mm, "end": v(42478.84, 67772.23) * mm});
            skLineSegment(sketch, "E3113", {"start": v(42478.84, 67772.23) * mm, "end": v(42477.15, 67771.72) * mm});
            skLineSegment(sketch, "E3114", {"start": v(42477.15, 67771.72) * mm, "end": v(42475.43, 67771.2) * mm});
            skLineSegment(sketch, "E3115", {"start": v(42475.43, 67771.2) * mm, "end": v(42473.69, 67770.67) * mm});
            skLineSegment(sketch, "E3116", {"start": v(42473.69, 67770.67) * mm, "end": v(42471.91, 67770.13) * mm});
            skLineSegment(sketch, "E3117", {"start": v(42471.91, 67770.13) * mm, "end": v(42470.11, 67769.58) * mm});
            skLineSegment(sketch, "E3118", {"start": v(42470.11, 67769.58) * mm, "end": v(42468.3, 67769.03) * mm});
            skLineSegment(sketch, "E3119", {"start": v(42468.3, 67769.03) * mm, "end": v(42466.45, 67768.48) * mm});
            skLineSegment(sketch, "E3120", {"start": v(42466.45, 67768.48) * mm, "end": v(42464.6, 67767.91) * mm});
            skLineSegment(sketch, "E3121", {"start": v(42464.6, 67767.91) * mm, "end": v(42462.73, 67767.35) * mm});
            skLineSegment(sketch, "E3122", {"start": v(42462.73, 67767.35) * mm, "end": v(42460.85, 67766.78) * mm});
            skLineSegment(sketch, "E3123", {"start": v(42460.85, 67766.78) * mm, "end": v(42458.96, 67766.21) * mm});
            skLineSegment(sketch, "E3124", {"start": v(42458.96, 67766.21) * mm, "end": v(42457.44, 67765.75) * mm});
            skLineSegment(sketch, "E3125", {"start": v(42509.85, 67760.05) * mm, "end": v(42509.9, 67760.07) * mm});
            skLineSegment(sketch, "E3126", {"start": v(42503.74, 67780.43) * mm, "end": v(42503.7, 67780.41) * mm});
            skLineSegment(sketch, "E3127", {"start": v(42361.46, 67803.7) * mm, "end": v(42361.46, 67803.71) * mm});
            skLineSegment(sketch, "E3128", {"start": v(42361.46, 67803.71) * mm, "end": v(42361.45, 67803.76) * mm});
            skLineSegment(sketch, "E3129", {"start": v(42361.45, 67803.76) * mm, "end": v(42361.42, 67803.83) * mm});
            skLineSegment(sketch, "E3130", {"start": v(42361.42, 67803.83) * mm, "end": v(42361.4, 67803.93) * mm});
            skLineSegment(sketch, "E3131", {"start": v(42361.4, 67803.93) * mm, "end": v(42361.36, 67804.05) * mm});
            skLineSegment(sketch, "E3132", {"start": v(42361.36, 67804.05) * mm, "end": v(42361.3, 67804.2) * mm});
            skLineSegment(sketch, "E3133", {"start": v(42361.3, 67804.2) * mm, "end": v(42361.25, 67804.4) * mm});
            skLineSegment(sketch, "E3134", {"start": v(42361.25, 67804.4) * mm, "end": v(42361.19, 67804.6) * mm});
            skLineSegment(sketch, "E3135", {"start": v(42361.19, 67804.6) * mm, "end": v(42361.12, 67804.84) * mm});
            skLineSegment(sketch, "E3136", {"start": v(42361.12, 67804.84) * mm, "end": v(42361.04, 67805.1) * mm});
            skLineSegment(sketch, "E3137", {"start": v(42361.04, 67805.1) * mm, "end": v(42360.95, 67805.4) * mm});
            skLineSegment(sketch, "E3138", {"start": v(42360.95, 67805.4) * mm, "end": v(42360.85, 67805.7) * mm});
            skLineSegment(sketch, "E3139", {"start": v(42360.85, 67805.7) * mm, "end": v(42360.75, 67806.05) * mm});
            skLineSegment(sketch, "E3140", {"start": v(42360.75, 67806.05) * mm, "end": v(42360.64, 67806.41) * mm});
            skLineSegment(sketch, "E3141", {"start": v(42360.64, 67806.41) * mm, "end": v(42360.52, 67806.8) * mm});
            skLineSegment(sketch, "E3142", {"start": v(42360.52, 67806.8) * mm, "end": v(42360.4, 67807.22) * mm});
            skLineSegment(sketch, "E3143", {"start": v(42360.4, 67807.22) * mm, "end": v(42360.27, 67807.65) * mm});
            skLineSegment(sketch, "E3144", {"start": v(42360.27, 67807.65) * mm, "end": v(42360.13, 67808.1) * mm});
            skLineSegment(sketch, "E3145", {"start": v(42360.13, 67808.1) * mm, "end": v(42359.98, 67808.59) * mm});
            skLineSegment(sketch, "E3146", {"start": v(42359.98, 67808.59) * mm, "end": v(42359.83, 67809.09) * mm});
            skLineSegment(sketch, "E3147", {"start": v(42359.83, 67809.09) * mm, "end": v(42359.67, 67809.6) * mm});
            skLineSegment(sketch, "E3148", {"start": v(42359.67, 67809.6) * mm, "end": v(42359.51, 67810.15) * mm});
            skLineSegment(sketch, "E3149", {"start": v(42359.51, 67810.15) * mm, "end": v(42359.34, 67810.7) * mm});
            skLineSegment(sketch, "E3150", {"start": v(42359.34, 67810.7) * mm, "end": v(42359.17, 67811.28) * mm});
            skLineSegment(sketch, "E3151", {"start": v(42359.17, 67811.28) * mm, "end": v(42359, 67811.87) * mm});
            skLineSegment(sketch, "E3152", {"start": v(42359, 67811.87) * mm, "end": v(42358.8, 67812.47) * mm});
            skLineSegment(sketch, "E3153", {"start": v(42358.8, 67812.47) * mm, "end": v(42358.62, 67813.1) * mm});
            skLineSegment(sketch, "E3154", {"start": v(42358.62, 67813.1) * mm, "end": v(42358.43, 67813.73) * mm});
            skLineSegment(sketch, "E3155", {"start": v(42358.43, 67813.73) * mm, "end": v(42358.23, 67814.37) * mm});
            skLineSegment(sketch, "E3156", {"start": v(42358.23, 67814.37) * mm, "end": v(42358.03, 67815.03) * mm});
            skLineSegment(sketch, "E3157", {"start": v(42358.03, 67815.03) * mm, "end": v(42357.83, 67815.7) * mm});
            skLineSegment(sketch, "E3158", {"start": v(42357.83, 67815.7) * mm, "end": v(42357.63, 67816.37) * mm});
            skLineSegment(sketch, "E3159", {"start": v(42357.63, 67816.37) * mm, "end": v(42357.42, 67817.06) * mm});
            skLineSegment(sketch, "E3160", {"start": v(42357.42, 67817.06) * mm, "end": v(42357.2, 67817.75) * mm});
            skLineSegment(sketch, "E3161", {"start": v(42357.2, 67817.75) * mm, "end": v(42357, 67818.45) * mm});
            skLineSegment(sketch, "E3162", {"start": v(42357, 67818.45) * mm, "end": v(42356.79, 67819.15) * mm});
            skLineSegment(sketch, "E3163", {"start": v(42356.79, 67819.15) * mm, "end": v(42356.57, 67819.86) * mm});
            skLineSegment(sketch, "E3164", {"start": v(42356.57, 67819.86) * mm, "end": v(42356.36, 67820.56) * mm});
            skLineSegment(sketch, "E3165", {"start": v(42356.36, 67820.56) * mm, "end": v(42356.14, 67821.27) * mm});
            skLineSegment(sketch, "E3166", {"start": v(42356.14, 67821.27) * mm, "end": v(42356.08, 67821.47) * mm});
            skLineSegment(sketch, "E3167", {"start": v(42356.08, 67821.47) * mm, "end": v(42355.87, 67822.18) * mm});
            skLineSegment(sketch, "E3168", {"start": v(42355.87, 67822.18) * mm, "end": v(42355.65, 67822.89) * mm});
            skLineSegment(sketch, "E3169", {"start": v(42355.65, 67822.89) * mm, "end": v(42355.44, 67823.6) * mm});
            skLineSegment(sketch, "E3170", {"start": v(42355.44, 67823.6) * mm, "end": v(42355.23, 67824.3) * mm});
            skLineSegment(sketch, "E3171", {"start": v(42355.23, 67824.3) * mm, "end": v(42355.02, 67825) * mm});
            skLineSegment(sketch, "E3172", {"start": v(42355.02, 67825) * mm, "end": v(42354.8, 67825.69) * mm});
            skLineSegment(sketch, "E3173", {"start": v(42354.8, 67825.69) * mm, "end": v(42354.6, 67826.38) * mm});
            skLineSegment(sketch, "E3174", {"start": v(42354.6, 67826.38) * mm, "end": v(42354.4, 67827.06) * mm});
            skLineSegment(sketch, "E3175", {"start": v(42354.4, 67827.06) * mm, "end": v(42354.2, 67827.73) * mm});
            skLineSegment(sketch, "E3176", {"start": v(42354.2, 67827.73) * mm, "end": v(42354, 67828.39) * mm});
            skLineSegment(sketch, "E3177", {"start": v(42354, 67828.39) * mm, "end": v(42353.8, 67829.03) * mm});
            skLineSegment(sketch, "E3178", {"start": v(42353.8, 67829.03) * mm, "end": v(42353.6, 67829.67) * mm});
            skLineSegment(sketch, "E3179", {"start": v(42353.6, 67829.67) * mm, "end": v(42353.41, 67830.3) * mm});
            skLineSegment(sketch, "E3180", {"start": v(42353.41, 67830.3) * mm, "end": v(42353.23, 67830.9) * mm});
            skLineSegment(sketch, "E3181", {"start": v(42353.23, 67830.9) * mm, "end": v(42353.05, 67831.5) * mm});
            skLineSegment(sketch, "E3182", {"start": v(42353.05, 67831.5) * mm, "end": v(42352.87, 67832.08) * mm});
            skLineSegment(sketch, "E3183", {"start": v(42352.87, 67832.08) * mm, "end": v(42352.7, 67832.64) * mm});
            skLineSegment(sketch, "E3184", {"start": v(42352.7, 67832.64) * mm, "end": v(42352.54, 67833.18) * mm});
            skLineSegment(sketch, "E3185", {"start": v(42352.54, 67833.18) * mm, "end": v(42352.38, 67833.7) * mm});
            skLineSegment(sketch, "E3186", {"start": v(42352.38, 67833.7) * mm, "end": v(42352.23, 67834.21) * mm});
            skLineSegment(sketch, "E3187", {"start": v(42352.23, 67834.21) * mm, "end": v(42352.08, 67834.7) * mm});
            skLineSegment(sketch, "E3188", {"start": v(42352.08, 67834.7) * mm, "end": v(42351.94, 67835.16) * mm});
            skLineSegment(sketch, "E3189", {"start": v(42351.94, 67835.16) * mm, "end": v(42351.8, 67835.6) * mm});
            skLineSegment(sketch, "E3190", {"start": v(42351.8, 67835.6) * mm, "end": v(42351.68, 67836.02) * mm});
            skLineSegment(sketch, "E3191", {"start": v(42351.68, 67836.02) * mm, "end": v(42351.56, 67836.42) * mm});
            skLineSegment(sketch, "E3192", {"start": v(42351.56, 67836.42) * mm, "end": v(42351.45, 67836.79) * mm});
            skLineSegment(sketch, "E3193", {"start": v(42351.45, 67836.79) * mm, "end": v(42351.34, 67837.14) * mm});
            skLineSegment(sketch, "E3194", {"start": v(42351.34, 67837.14) * mm, "end": v(42351.24, 67837.46) * mm});
            skLineSegment(sketch, "E3195", {"start": v(42351.24, 67837.46) * mm, "end": v(42351.15, 67837.76) * mm});
            skLineSegment(sketch, "E3196", {"start": v(42351.15, 67837.76) * mm, "end": v(42351.07, 67838.03) * mm});
            skLineSegment(sketch, "E3197", {"start": v(42351.07, 67838.03) * mm, "end": v(42351, 67838.27) * mm});
            skLineSegment(sketch, "E3198", {"start": v(42351, 67838.27) * mm, "end": v(42350.93, 67838.49) * mm});
            skLineSegment(sketch, "E3199", {"start": v(42350.93, 67838.49) * mm, "end": v(42350.87, 67838.68) * mm});
            skLineSegment(sketch, "E3200", {"start": v(42350.87, 67838.68) * mm, "end": v(42350.83, 67838.84) * mm});
            skLineSegment(sketch, "E3201", {"start": v(42350.83, 67838.84) * mm, "end": v(42350.78, 67838.98) * mm});
            skLineSegment(sketch, "E3202", {"start": v(42350.78, 67838.98) * mm, "end": v(42350.75, 67839.08) * mm});
            skLineSegment(sketch, "E3203", {"start": v(42350.75, 67839.08) * mm, "end": v(42350.73, 67839.16) * mm});
            skLineSegment(sketch, "E3204", {"start": v(42350.73, 67839.16) * mm, "end": v(42350.71, 67839.21) * mm});
            skLineSegment(sketch, "E3205", {"start": v(42350.71, 67839.21) * mm, "end": v(42350.7, 67839.23) * mm});
            skLineSegment(sketch, "E3206", {"start": v(42350.7, 67839.23) * mm, "end": v(42350.7, 67839.25) * mm});
            skLineSegment(sketch, "E3207", {"start": v(42350.7, 67839.25) * mm, "end": v(42350.69, 67839.3) * mm});
            skLineSegment(sketch, "E3208", {"start": v(42350.69, 67839.3) * mm, "end": v(42350.67, 67839.34) * mm});
            skLineSegment(sketch, "E3209", {"start": v(42350.67, 67839.34) * mm, "end": v(42350.65, 67839.39) * mm});
            skLineSegment(sketch, "E3210", {"start": v(42350.65, 67839.39) * mm, "end": v(42350.63, 67839.44) * mm});
            skLineSegment(sketch, "E3211", {"start": v(42350.63, 67839.44) * mm, "end": v(42350.6, 67839.48) * mm});
            skLineSegment(sketch, "E3212", {"start": v(42350.6, 67839.48) * mm, "end": v(42350.58, 67839.52) * mm});
            skLineSegment(sketch, "E3213", {"start": v(42350.58, 67839.52) * mm, "end": v(42350.55, 67839.57) * mm});
            skLineSegment(sketch, "E3214", {"start": v(42350.55, 67839.57) * mm, "end": v(42350.52, 67839.6) * mm});
            skLineSegment(sketch, "E3215", {"start": v(42350.52, 67839.6) * mm, "end": v(42350.5, 67839.65) * mm});
            skLineSegment(sketch, "E3216", {"start": v(42350.5, 67839.65) * mm, "end": v(42350.46, 67839.69) * mm});
            skLineSegment(sketch, "E3217", {"start": v(42350.46, 67839.69) * mm, "end": v(42350.42, 67839.73) * mm});
            skLineSegment(sketch, "E3218", {"start": v(42350.42, 67839.73) * mm, "end": v(42350.39, 67839.76) * mm});
            skLineSegment(sketch, "E3219", {"start": v(42350.39, 67839.76) * mm, "end": v(42350.35, 67839.8) * mm});
            skLineSegment(sketch, "E3220", {"start": v(42350.35, 67839.8) * mm, "end": v(42350.31, 67839.83) * mm});
            skLineSegment(sketch, "E3221", {"start": v(42350.31, 67839.83) * mm, "end": v(42350.28, 67839.87) * mm});
            skLineSegment(sketch, "E3222", {"start": v(42350.28, 67839.87) * mm, "end": v(42350.23, 67839.9) * mm});
            skLineSegment(sketch, "E3223", {"start": v(42350.23, 67839.9) * mm, "end": v(42350.2, 67839.92) * mm});
            skLineSegment(sketch, "E3224", {"start": v(42350.2, 67839.92) * mm, "end": v(42350.15, 67839.95) * mm});
            skLineSegment(sketch, "E3225", {"start": v(42350.15, 67839.95) * mm, "end": v(42350.1, 67839.98) * mm});
            skLineSegment(sketch, "E3226", {"start": v(42350.1, 67839.98) * mm, "end": v(42350.06, 67840) * mm});
            skLineSegment(sketch, "E3227", {"start": v(42350.06, 67840) * mm, "end": v(42350.01, 67840.02) * mm});
            skLineSegment(sketch, "E3228", {"start": v(42350.01, 67840.02) * mm, "end": v(42349.97, 67840.04) * mm});
            skLineSegment(sketch, "E3229", {"start": v(42349.97, 67840.04) * mm, "end": v(42349.92, 67840.06) * mm});
            skLineSegment(sketch, "E3230", {"start": v(42349.92, 67840.06) * mm, "end": v(42349.87, 67840.08) * mm});
            skLineSegment(sketch, "E3231", {"start": v(42349.87, 67840.08) * mm, "end": v(42349.82, 67840.1) * mm});
            skLineSegment(sketch, "E3232", {"start": v(42349.82, 67840.1) * mm, "end": v(42349.77, 67840.1) * mm});
            skLineSegment(sketch, "E3233", {"start": v(42349.77, 67840.1) * mm, "end": v(42349.72, 67840.12) * mm});
            skLineSegment(sketch, "E3234", {"start": v(42349.72, 67840.12) * mm, "end": v(42349.67, 67840.12) * mm});
            skLineSegment(sketch, "E3235", {"start": v(42349.67, 67840.12) * mm, "end": v(42349.62, 67840.13) * mm});
            skLineSegment(sketch, "E3236", {"start": v(42349.62, 67840.13) * mm, "end": v(42349.57, 67840.13) * mm});
            skLineSegment(sketch, "E3237", {"start": v(42349.57, 67840.13) * mm, "end": v(42349.52, 67840.14) * mm});
            skLineSegment(sketch, "E3238", {"start": v(42349.52, 67840.14) * mm, "end": v(42349.47, 67840.14) * mm});
            skLineSegment(sketch, "E3239", {"start": v(42349.47, 67840.14) * mm, "end": v(42349.42, 67840.14) * mm});
            skLineSegment(sketch, "E3240", {"start": v(42349.42, 67840.14) * mm, "end": v(42349.37, 67840.13) * mm});
            skLineSegment(sketch, "E3241", {"start": v(42349.37, 67840.13) * mm, "end": v(42349.32, 67840.13) * mm});
            skLineSegment(sketch, "E3242", {"start": v(42349.32, 67840.13) * mm, "end": v(42349.27, 67840.12) * mm});
            skLineSegment(sketch, "E3243", {"start": v(42349.27, 67840.12) * mm, "end": v(42349.22, 67840.1) * mm});
            skLineSegment(sketch, "E3244", {"start": v(42349.22, 67840.1) * mm, "end": v(42349.17, 67840.1) * mm});
            skLineSegment(sketch, "E3245", {"start": v(42349.17, 67840.1) * mm, "end": v(42349.12, 67840.08) * mm});
            skLineSegment(sketch, "E3246", {"start": v(42349.12, 67840.08) * mm, "end": v(42349.05, 67840.06) * mm});
            skLineSegment(sketch, "E3247", {"start": v(42349.05, 67840.06) * mm, "end": v(42348.95, 67840.03) * mm});
            skLineSegment(sketch, "E3248", {"start": v(42348.95, 67840.03) * mm, "end": v(42348.85, 67839.99) * mm});
            skLineSegment(sketch, "E3249", {"start": v(42348.85, 67839.99) * mm, "end": v(42348.75, 67839.94) * mm});
            skLineSegment(sketch, "E3250", {"start": v(42348.75, 67839.94) * mm, "end": v(42348.66, 67839.9) * mm});
            skLineSegment(sketch, "E3251", {"start": v(42348.66, 67839.9) * mm, "end": v(42348.56, 67839.84) * mm});
            skLineSegment(sketch, "E3252", {"start": v(42348.56, 67839.84) * mm, "end": v(42348.47, 67839.79) * mm});
            skLineSegment(sketch, "E3253", {"start": v(42348.47, 67839.79) * mm, "end": v(42348.38, 67839.73) * mm});
            skLineSegment(sketch, "E3254", {"start": v(42348.38, 67839.73) * mm, "end": v(42348.3, 67839.66) * mm});
            skLineSegment(sketch, "E3255", {"start": v(42505.97, 67782.27) * mm, "end": v(42505.8, 67782.26) * mm});
            skLineSegment(sketch, "E3256", {"start": v(42505.8, 67782.26) * mm, "end": v(42505.32, 67782.22) * mm});
            skLineSegment(sketch, "E3257", {"start": v(42505.32, 67782.22) * mm, "end": v(42504.84, 67782.16) * mm});
            skLineSegment(sketch, "E3258", {"start": v(42504.84, 67782.16) * mm, "end": v(42504.37, 67782.08) * mm});
            skLineSegment(sketch, "E3259", {"start": v(42504.37, 67782.08) * mm, "end": v(42503.9, 67781.98) * mm});
            skLineSegment(sketch, "E3260", {"start": v(42503.9, 67781.98) * mm, "end": v(42503.42, 67781.86) * mm});
            skLineSegment(sketch, "E3261", {"start": v(42503.42, 67781.86) * mm, "end": v(42502.96, 67781.72) * mm});
            skLineSegment(sketch, "E3262", {"start": v(42502.96, 67781.72) * mm, "end": v(42502.5, 67781.57) * mm});
            skLineSegment(sketch, "E3263", {"start": v(42502.5, 67781.57) * mm, "end": v(42502.05, 67781.4) * mm});
            skLineSegment(sketch, "E3264", {"start": v(42502.05, 67781.4) * mm, "end": v(42501.6, 67781.2) * mm});
            skLineSegment(sketch, "E3265", {"start": v(42501.6, 67781.2) * mm, "end": v(42501.17, 67781) * mm});
            skLineSegment(sketch, "E3266", {"start": v(42501.17, 67781) * mm, "end": v(42500.74, 67780.77) * mm});
            skLineSegment(sketch, "E3267", {"start": v(42500.74, 67780.77) * mm, "end": v(42500.32, 67780.52) * mm});
            skLineSegment(sketch, "E3268", {"start": v(42500.32, 67780.52) * mm, "end": v(42499.91, 67780.26) * mm});
            skLineSegment(sketch, "E3269", {"start": v(42499.91, 67780.26) * mm, "end": v(42499.51, 67779.99) * mm});
            skLineSegment(sketch, "E3270", {"start": v(42499.51, 67779.99) * mm, "end": v(42499.13, 67779.7) * mm});
            skLineSegment(sketch, "E3271", {"start": v(42499.13, 67779.7) * mm, "end": v(42498.75, 67779.4) * mm});
            skLineSegment(sketch, "E3272", {"start": v(42498.75, 67779.4) * mm, "end": v(42498.4, 67779.07) * mm});
            skLineSegment(sketch, "E3273", {"start": v(42498.4, 67779.07) * mm, "end": v(42498.04, 67778.73) * mm});
            skLineSegment(sketch, "E3274", {"start": v(42498.04, 67778.73) * mm, "end": v(42497.7, 67778.38) * mm});
            skLineSegment(sketch, "E3275", {"start": v(42497.7, 67778.38) * mm, "end": v(42497.39, 67778.02) * mm});
            skLineSegment(sketch, "E3276", {"start": v(42497.39, 67778.02) * mm, "end": v(42497.08, 67777.65) * mm});
            skLineSegment(sketch, "E3277", {"start": v(42347.8, 67804.3) * mm, "end": v(42343.74, 67817.73) * mm});
            skLineSegment(sketch, "E3278", {"start": v(42343.74, 67817.73) * mm, "end": v(42339.67, 67831.15) * mm});
            skLineSegment(sketch, "E3279", {"start": v(42352.12, 67839.83) * mm, "end": v(42350.66, 67839.4) * mm});
            skLineSegment(sketch, "E3280", {"start": v(42350.66, 67839.4) * mm, "end": v(42361.51, 67803.54) * mm});
            skLineSegment(sketch, "E3281", {"start": v(42361.51, 67803.54) * mm, "end": v(42362.97, 67803.98) * mm});
            skArc(sketch, "E3282", {"start": v(42507.73, 67782.26) * mm, "mid": v(42507.68, 67782.26) * mm, "end": v(42507.62, 67782.27) * mm});
            skLineSegment(sketch, "E3283", {"start": v(42507.62, 67782.27) * mm, "end": v(42507.38, 67782.28) * mm});
            skArc(sketch, "E3284", {"start": v(42507.38, 67782.28) * mm, "mid": v(42507.09, 67782.3) * mm, "end": v(42506.8, 67782.3) * mm});
            skLineSegment(sketch, "E3285", {"start": v(42506.8, 67782.3) * mm, "end": v(42506.39, 67782.3) * mm});
            skArc(sketch, "E3286", {"start": v(42506.39, 67782.3) * mm, "mid": v(42505.7, 67782.26) * mm, "end": v(42505, 67782.17) * mm});
            skLineSegment(sketch, "E3287", {"start": v(42505, 67782.17) * mm, "end": v(42504.84, 67782.14) * mm});
            skArc(sketch, "E3288", {"start": v(42504.84, 67782.14) * mm, "mid": v(42504.1, 67782) * mm, "end": v(42503.38, 67781.81) * mm});
            skArc(sketch, "E3289", {"start": v(42503.38, 67781.81) * mm, "mid": v(42503.33, 67781.8) * mm, "end": v(42503.28, 67781.78) * mm});
            skLineSegment(sketch, "E3290", {"start": v(42359.7, 67802) * mm, "end": v(42354, 67820.83) * mm});
            skLineSegment(sketch, "E3291", {"start": v(42354, 67820.83) * mm, "end": v(42348.3, 67839.66) * mm});
            skLineSegment(sketch, "E3292", {"start": v(42348.3, 67839.66) * mm, "end": v(42348.25, 67839.63) * mm});
            skLineSegment(sketch, "E3293", {"start": v(42348.25, 67839.63) * mm, "end": v(42347.84, 67839.33) * mm});
            skLineSegment(sketch, "E3294", {"start": v(42347.84, 67839.33) * mm, "end": v(42347.42, 67839.05) * mm});
            skLineSegment(sketch, "E3295", {"start": v(42347.42, 67839.05) * mm, "end": v(42346.99, 67838.79) * mm});
            skLineSegment(sketch, "E3296", {"start": v(42346.99, 67838.79) * mm, "end": v(42346.55, 67838.54) * mm});
            skLineSegment(sketch, "E3297", {"start": v(42346.55, 67838.54) * mm, "end": v(42346.1, 67838.3) * mm});
            skLineSegment(sketch, "E3298", {"start": v(42346.1, 67838.3) * mm, "end": v(42345.64, 67838.1) * mm});
            skLineSegment(sketch, "E3299", {"start": v(42345.64, 67838.1) * mm, "end": v(42345.17, 67837.9) * mm});
            skLineSegment(sketch, "E3300", {"start": v(42345.17, 67837.9) * mm, "end": v(42344.7, 67837.73) * mm});
            skLineSegment(sketch, "E3301", {"start": v(42344.7, 67837.73) * mm, "end": v(42344.21, 67837.57) * mm});
            skLineSegment(sketch, "E3302", {"start": v(42344.21, 67837.57) * mm, "end": v(42343.72, 67837.44) * mm});
            skLineSegment(sketch, "E3303", {"start": v(42343.72, 67837.44) * mm, "end": v(42343.23, 67837.32) * mm});
            skLineSegment(sketch, "E3304", {"start": v(42343.23, 67837.32) * mm, "end": v(42342.73, 67837.22) * mm});
            skLineSegment(sketch, "E3305", {"start": v(42342.73, 67837.22) * mm, "end": v(42342.23, 67837.15) * mm});
            skLineSegment(sketch, "E3306", {"start": v(42342.23, 67837.15) * mm, "end": v(42341.73, 67837.1) * mm});
            skLineSegment(sketch, "E3307", {"start": v(42341.73, 67837.1) * mm, "end": v(42341.23, 67837.05) * mm});
            skLineSegment(sketch, "E3308", {"start": v(42341.23, 67837.05) * mm, "end": v(42340.72, 67837.04) * mm});
            skLineSegment(sketch, "E3309", {"start": v(42340.72, 67837.04) * mm, "end": v(42340.21, 67837.04) * mm});
            skLineSegment(sketch, "E3310", {"start": v(42340.21, 67837.04) * mm, "end": v(42339.7, 67837.07) * mm});
            skLineSegment(sketch, "E3311", {"start": v(42339.7, 67837.07) * mm, "end": v(42339.64, 67837.07) * mm});
            skLineSegment(sketch, "E3312", {"start": v(42339.64, 67837.07) * mm, "end": v(42339.5, 67837.07) * mm});
            skLineSegment(sketch, "E3313", {"start": v(42339.5, 67837.07) * mm, "end": v(42339.37, 67837.07) * mm});
            skLineSegment(sketch, "E3314", {"start": v(42339.37, 67837.07) * mm, "end": v(42339.24, 67837.07) * mm});
            skLineSegment(sketch, "E3315", {"start": v(42339.24, 67837.07) * mm, "end": v(42339.11, 67837.05) * mm});
            skLineSegment(sketch, "E3316", {"start": v(42339.11, 67837.05) * mm, "end": v(42338.98, 67837.04) * mm});
            skLineSegment(sketch, "E3317", {"start": v(42338.98, 67837.04) * mm, "end": v(42338.85, 67837.01) * mm});
            skLineSegment(sketch, "E3318", {"start": v(42338.85, 67837.01) * mm, "end": v(42338.73, 67836.99) * mm});
            skLineSegment(sketch, "E3319", {"start": v(42338.73, 67836.99) * mm, "end": v(42338.6, 67836.95) * mm});
            skLineSegment(sketch, "E3320", {"start": v(42338.6, 67836.95) * mm, "end": v(42338.47, 67836.91) * mm});
            skLineSegment(sketch, "E3321", {"start": v(42338.47, 67836.91) * mm, "end": v(42338.35, 67836.87) * mm});
            skLineSegment(sketch, "E3322", {"start": v(42338.35, 67836.87) * mm, "end": v(42338.23, 67836.82) * mm});
            skLineSegment(sketch, "E3323", {"start": v(42338.23, 67836.82) * mm, "end": v(42338.1, 67836.77) * mm});
            skLineSegment(sketch, "E3324", {"start": v(42338.1, 67836.77) * mm, "end": v(42337.99, 67836.71) * mm});
            skLineSegment(sketch, "E3325", {"start": v(42337.99, 67836.71) * mm, "end": v(42336.98, 67837.25) * mm});
            skArc(sketch, "E3326", {"start": v(42513.44, 67761.9) * mm, "mid": v(42513.46, 67761.93) * mm, "end": v(42513.48, 67761.95) * mm});
            skLineSegment(sketch, "E3327", {"start": v(42513.48, 67761.95) * mm, "end": v(42513.66, 67762.1) * mm});
            skArc(sketch, "E3328", {"start": v(42513.66, 67762.1) * mm, "mid": v(42513.86, 67762.27) * mm, "end": v(42514.05, 67762.45) * mm});
            skLineSegment(sketch, "E3329", {"start": v(42514.05, 67762.45) * mm, "end": v(42514.23, 67762.64) * mm});
            skArc(sketch, "E3330", {"start": v(42514.23, 67762.64) * mm, "mid": v(42514.55, 67762.97) * mm, "end": v(42514.85, 67763.33) * mm});
            skLineSegment(sketch, "E3331", {"start": v(42514.85, 67763.33) * mm, "end": v(42514.87, 67763.35) * mm});
            skArc(sketch, "E3332", {"start": v(42514.87, 67763.35) * mm, "mid": v(42515.14, 67763.69) * mm, "end": v(42515.4, 67764.04) * mm});
            skArc(sketch, "E3333", {"start": v(42515.4, 67764.04) * mm, "mid": v(42515.41, 67764.06) * mm, "end": v(42515.43, 67764.09) * mm});
            skArc(sketch, "E3334", {"start": v(42518.83, 67770.3) * mm, "mid": v(42518.83, 67770.34) * mm, "end": v(42518.83, 67770.38) * mm});
            skLineSegment(sketch, "E3335", {"start": v(42518.83, 67770.38) * mm, "end": v(42518.83, 67770.6) * mm});
            skArc(sketch, "E3336", {"start": v(42518.83, 67770.6) * mm, "mid": v(42518.82, 67770.85) * mm, "end": v(42518.8, 67771.1) * mm});
            skLineSegment(sketch, "E3337", {"start": v(42518.8, 67771.1) * mm, "end": v(42518.78, 67771.4) * mm});
            skArc(sketch, "E3338", {"start": v(42518.78, 67771.4) * mm, "mid": v(42518.71, 67771.95) * mm, "end": v(42518.62, 67772.5) * mm});
            skLineSegment(sketch, "E3339", {"start": v(42518.62, 67772.5) * mm, "end": v(42518.6, 67772.58) * mm});
            skArc(sketch, "E3340", {"start": v(42518.6, 67772.58) * mm, "mid": v(42518.48, 67773.12) * mm, "end": v(42518.34, 67773.65) * mm});
            skArc(sketch, "E3341", {"start": v(42518.34, 67773.65) * mm, "mid": v(42518.33, 67773.69) * mm, "end": v(42518.32, 67773.73) * mm});
            skArc(sketch, "E3342", {"start": v(42518.32, 67773.73) * mm, "mid": v(42518.31, 67773.75) * mm, "end": v(42518.3, 67773.76) * mm});
            skLineSegment(sketch, "E3343", {"start": v(42518.3, 67773.76) * mm, "end": v(42518.25, 67773.96) * mm});
            skArc(sketch, "E3344", {"start": v(42518.25, 67773.96) * mm, "mid": v(42518.18, 67774.17) * mm, "end": v(42518.1, 67774.38) * mm});
            skLineSegment(sketch, "E3345", {"start": v(42518.1, 67774.38) * mm, "end": v(42518, 67774.64) * mm});
            skArc(sketch, "E3346", {"start": v(42518, 67774.64) * mm, "mid": v(42517.8, 67775.11) * mm, "end": v(42517.6, 67775.57) * mm});
            skLineSegment(sketch, "E3347", {"start": v(42517.6, 67775.57) * mm, "end": v(42517.56, 67775.64) * mm});
            skArc(sketch, "E3348", {"start": v(42517.56, 67775.64) * mm, "mid": v(42517.55, 67775.65) * mm, "end": v(42517.54, 67775.67) * mm});
            skArc(sketch, "E3349", {"start": v(42510.34, 67780.24) * mm, "mid": v(42510.31, 67780.25) * mm, "end": v(42510.29, 67780.26) * mm});
            skLineSegment(sketch, "E3350", {"start": v(42510.29, 67780.26) * mm, "end": v(42510.12, 67780.32) * mm});
            skArc(sketch, "E3351", {"start": v(42510.12, 67780.32) * mm, "mid": v(42509.92, 67780.39) * mm, "end": v(42509.71, 67780.45) * mm});
            skLineSegment(sketch, "E3352", {"start": v(42509.71, 67780.45) * mm, "end": v(42509.51, 67780.5) * mm});
            skArc(sketch, "E3353", {"start": v(42509.51, 67780.5) * mm, "mid": v(42509.1, 67780.62) * mm, "end": v(42508.69, 67780.7) * mm});
            skLineSegment(sketch, "E3354", {"start": v(42508.69, 67780.7) * mm, "end": v(42508.66, 67780.71) * mm});
            skArc(sketch, "E3355", {"start": v(42508.66, 67780.71) * mm, "mid": v(42508.22, 67780.8) * mm, "end": v(42507.77, 67780.85) * mm});
            skArc(sketch, "E3356", {"start": v(42507.77, 67780.85) * mm, "mid": v(42507.74, 67780.85) * mm, "end": v(42507.71, 67780.86) * mm});
            skArc(sketch, "E3357", {"start": v(42754.55, 67845.23) * mm, "mid": v(42664.8, 67954.74) * mm, "end": v(42523.9, 67968.7) * mm});
            skArc(sketch, "E3358", {"start": v(42523.9, 67968.7) * mm, "mid": v(42414.39, 67878.95) * mm, "end": v(42400.42, 67738.04) * mm});
            skArc(sketch, "E3359", {"start": v(42400.42, 67738.04) * mm, "mid": v(42490.18, 67628.54) * mm, "end": v(42631.08, 67614.57) * mm});
            skArc(sketch, "E3360", {"start": v(42631.08, 67614.57) * mm, "mid": v(42740.6, 67704.33) * mm, "end": v(42754.55, 67845.23) * mm});
            skArc(sketch, "E3361", {"start": v(42426.54, 67745.95) * mm, "mid": v(42503.06, 67652.6) * mm, "end": v(42623.18, 67640.7) * mm});
            skArc(sketch, "E3362", {"start": v(42623.18, 67640.7) * mm, "mid": v(42716.53, 67717.2) * mm, "end": v(42728.43, 67837.33) * mm});
            skArc(sketch, "E3363", {"start": v(42728.43, 67837.33) * mm, "mid": v(42651.92, 67930.68) * mm, "end": v(42531.8, 67942.58) * mm});
            skArc(sketch, "E3364", {"start": v(42531.8, 67942.58) * mm, "mid": v(42438.45, 67866.07) * mm, "end": v(42426.54, 67745.95) * mm});
            skLineSegment(sketch, "E3365", {"start": v(51108.92, 66805.05) * mm, "end": v(51186.33, 66894.55) * mm});
            skLineSegment(sketch, "E3366", {"start": v(51093.74, 66806.6) * mm, "end": v(51171.15, 66896.1) * mm});
            skLineSegment(sketch, "E3367", {"start": v(51211.53, 66794.52) * mm, "end": v(51288.94, 66884.02) * mm});
            skLineSegment(sketch, "E3368", {"start": v(51196.35, 66796.08) * mm, "end": v(51273.76, 66885.58) * mm});
            skLineSegment(sketch, "E3369", {"start": v(51226.71, 66792.96) * mm, "end": v(51304.12, 66882.46) * mm});
            skLineSegment(sketch, "E3370", {"start": v(51238.86, 66791.72) * mm, "end": v(51316.27, 66881.22) * mm});
            skLineSegment(sketch, "E3371", {"start": v(48276.64, 61941.14) * mm, "end": v(48357.76, 61673.12) * mm});
            skLineSegment(sketch, "E3372", {"start": v(48300.57, 61948.38) * mm, "end": v(48388.93, 61656.43) * mm});
            skLineSegment(sketch, "E3373", {"start": v(48258.45, 61935.63) * mm, "end": v(48334.07, 61685.8) * mm});
            skLineSegment(sketch, "E3374", {"start": v(47830.02, 63416.73) * mm, "end": v(48008.38, 62827.43) * mm});
            skLineSegment(sketch, "E3375", {"start": v(47861.2, 63400.04) * mm, "end": v(48032.31, 62834.67) * mm});
            skLineSegment(sketch, "E3376", {"start": v(47806.33, 63429.4) * mm, "end": v(47990.2, 62821.93) * mm});
            skLineSegment(sketch, "E3377", {"start": v(48011.25, 62828.3) * mm, "end": v(47990.2, 62821.93) * mm});
            skLineSegment(sketch, "E3378", {"start": v(48279.5, 61942) * mm, "end": v(48258.45, 61935.63) * mm});
            skLineSegment(sketch, "E3379", {"start": v(48011.25, 62828.3) * mm, "end": v(48032.31, 62834.67) * mm});
            skLineSegment(sketch, "E3380", {"start": v(48279.5, 61942) * mm, "end": v(48300.57, 61948.38) * mm});
            skArc(sketch, "E3381", {"start": v(48032.31, 62834.67) * mm, "mid": v(47863.55, 61132) * mm, "end": v(49186.86, 62216.63) * mm});
            skLineSegment(sketch, "E3382", {"start": v(48300.57, 61948.38) * mm, "end": v(49186.86, 62216.63) * mm});
            skLineSegment(sketch, "E3383", {"start": v(49186.86, 62216.63) * mm, "end": v(49175.85, 62253) * mm});
            skLineSegment(sketch, "E3384", {"start": v(49175.85, 62253) * mm, "end": v(48289.56, 61984.75) * mm});
            skLineSegment(sketch, "E3385", {"start": v(48289.56, 61984.75) * mm, "end": v(48300.57, 61948.38) * mm});
            skLineSegment(sketch, "E3386", {"start": v(48289.56, 61984.75) * mm, "end": v(49175.85, 62253) * mm});
            skLineSegment(sketch, "E3387", {"start": v(48300.57, 61948.38) * mm, "end": v(48289.56, 61984.75) * mm});
            skLineSegment(sketch, "E3388", {"start": v(48300.57, 61948.38) * mm, "end": v(48032.31, 62834.67) * mm});
            skLineSegment(sketch, "E3389", {"start": v(48258.45, 61935.63) * mm, "end": v(47990.2, 62821.93) * mm});
            skLineSegment(sketch, "E3390", {"start": v(47908.95, 63440.62) * mm, "end": v(47830.02, 63416.73) * mm});
            skLineSegment(sketch, "E3391", {"start": v(47940.12, 63423.93) * mm, "end": v(47861.2, 63400.04) * mm});
            skLineSegment(sketch, "E3392", {"start": v(47885.26, 63453.3) * mm, "end": v(47806.33, 63429.4) * mm});
            skLineSegment(sketch, "E3393", {"start": v(47524.8, 64709.79) * mm, "end": v(47908.95, 63440.62) * mm});
            skLineSegment(sketch, "E3394", {"start": v(47545.3, 64728.34) * mm, "end": v(47940.12, 63423.93) * mm});
            skLineSegment(sketch, "E3395", {"start": v(47503.54, 64714.43) * mm, "end": v(47885.26, 63453.3) * mm});
            skLineSegment(sketch, "E3396", {"start": v(47517.27, 64820.95) * mm, "end": v(47545.3, 64728.34) * mm});
            skLineSegment(sketch, "E3397", {"start": v(47545.3, 64728.34) * mm, "end": v(47517.34, 64734.45) * mm});
            skLineSegment(sketch, "E3398", {"start": v(47517.34, 64734.45) * mm, "end": v(47524.8, 64709.79) * mm});
            skLineSegment(sketch, "E3399", {"start": v(47524.8, 64709.79) * mm, "end": v(47503.54, 64714.43) * mm});
            skLineSegment(sketch, "E3400", {"start": v(44564.55, 60525.03) * mm, "end": v(44124.98, 60391.98) * mm});
            skLineSegment(sketch, "E3401", {"start": v(44571.8, 60501.1) * mm, "end": v(44132.23, 60368.05) * mm});
            skLineSegment(sketch, "E3402", {"start": v(44559.05, 60543.21) * mm, "end": v(44119.48, 60410.17) * mm});
            skLineSegment(sketch, "E3403", {"start": v(46626.93, 61149.25) * mm, "end": v(45425.96, 60785.75) * mm});
            skLineSegment(sketch, "E3404", {"start": v(46634.17, 61125.32) * mm, "end": v(45433.2, 60761.82) * mm});
            skLineSegment(sketch, "E3405", {"start": v(46621.43, 61167.43) * mm, "end": v(45420.46, 60803.93) * mm});
            skLineSegment(sketch, "E3406", {"start": v(48357.76, 61673.12) * mm, "end": v(47679.76, 61467.9) * mm});
            skLineSegment(sketch, "E3407", {"start": v(48388.93, 61656.43) * mm, "end": v(47687, 61443.98) * mm});
            skLineSegment(sketch, "E3408", {"start": v(48334.07, 61685.8) * mm, "end": v(47674.26, 61486.1) * mm});
            skLineSegment(sketch, "E3409", {"start": v(44565.42, 60522.15) * mm, "end": v(44571.8, 60501.1) * mm});
            skLineSegment(sketch, "E3410", {"start": v(45426.83, 60782.88) * mm, "end": v(45433.2, 60761.82) * mm});
            skLineSegment(sketch, "E3411", {"start": v(44565.42, 60522.15) * mm, "end": v(44559.05, 60543.21) * mm});
            skLineSegment(sketch, "E3412", {"start": v(45426.83, 60782.88) * mm, "end": v(45420.46, 60803.93) * mm});
            skLineSegment(sketch, "E3413", {"start": v(45420.46, 60803.93) * mm, "end": v(44559.05, 60543.21) * mm});
            skLineSegment(sketch, "E3414", {"start": v(45433.2, 60761.82) * mm, "end": v(44571.8, 60501.1) * mm});
            skLineSegment(sketch, "E3415", {"start": v(46627.8, 61146.37) * mm, "end": v(46634.17, 61125.32) * mm});
            skLineSegment(sketch, "E3416", {"start": v(47680.63, 61465.04) * mm, "end": v(47687, 61443.98) * mm});
            skLineSegment(sketch, "E3417", {"start": v(46627.8, 61146.37) * mm, "end": v(46621.43, 61167.43) * mm});
            skLineSegment(sketch, "E3418", {"start": v(47680.63, 61465.04) * mm, "end": v(47674.26, 61486.1) * mm});
            skLineSegment(sketch, "E3419", {"start": v(47674.26, 61486.1) * mm, "end": v(46621.43, 61167.43) * mm});
            skLineSegment(sketch, "E3420", {"start": v(47687, 61443.98) * mm, "end": v(46634.17, 61125.32) * mm});
            skArc(sketch, "E3421", {"start": v(43455.5, 66290.19) * mm, "mid": v(44803.53, 66771.62) * mm, "end": v(43894.8, 67877.6) * mm});
            skArc(sketch, "E3422", {"start": v(43504.23, 66359.22) * mm, "mid": v(44722.09, 66794.16) * mm, "end": v(43901.12, 67793.34) * mm});
            skArc(sketch, "E3423", {"start": v(43497.02, 66349) * mm, "mid": v(44734.14, 66790.82) * mm, "end": v(43900.19, 67805.8) * mm});
            skArc(sketch, "E3424", {"start": v(43511.44, 66369.43) * mm, "mid": v(44710.04, 66797.5) * mm, "end": v(43902.05, 67780.88) * mm});
            skArc(sketch, "E3425", {"start": v(43517.2, 66377.6) * mm, "mid": v(44700.4, 66800.16) * mm, "end": v(43902.8, 67770.9) * mm});
            skLineSegment(sketch, "E3426", {"start": v(41501.26, 73443.26) * mm, "end": v(41633.78, 72409.81) * mm});
            skLineSegment(sketch, "E3427", {"start": v(41512.45, 73434.61) * mm, "end": v(41643.7, 72411.08) * mm});
            skLineSegment(sketch, "E3428", {"start": v(41487.27, 73454.06) * mm, "end": v(41621.38, 72408.22) * mm});
            skLineSegment(sketch, "E3429", {"start": v(41473.28, 73464.87) * mm, "end": v(41608.98, 72406.63) * mm});
            skLineSegment(sketch, "E3430", {"start": v(41392.71, 73527.13) * mm, "end": v(41537.56, 72397.47) * mm});
            skLineSegment(sketch, "E3431", {"start": v(42619.99, 69993.15) * mm, "end": v(43193.07, 69571.3) * mm});
            skLineSegment(sketch, "E3432", {"start": v(42636.6, 69993.33) * mm, "end": v(43199, 69579.34) * mm});
            skLineSegment(sketch, "E3433", {"start": v(42599.22, 69992.92) * mm, "end": v(43185.66, 69561.22) * mm});
            skLineSegment(sketch, "E3434", {"start": v(42578.45, 69992.68) * mm, "end": v(43178.25, 69551.16) * mm});
            skLineSegment(sketch, "E3435", {"start": v(42458.81, 69991.34) * mm, "end": v(43135.57, 69493.17) * mm});
            skLineSegment(sketch, "E3436", {"start": v(43315.39, 69327.9) * mm, "end": v(43113.65, 69476.4) * mm});
            skLineSegment(sketch, "E3437", {"start": v(43309.46, 69319.84) * mm, "end": v(43109.28, 69467.2) * mm});
            skLineSegment(sketch, "E3438", {"start": v(43322.8, 69337.96) * mm, "end": v(43119.12, 69487.9) * mm});
            skLineSegment(sketch, "E3439", {"start": v(43330.2, 69348.03) * mm, "end": v(43124.59, 69499.4) * mm});
            skLineSegment(sketch, "E3440", {"start": v(43380.3, 69416.08) * mm, "end": v(43161.56, 69577.1) * mm});
            skLineSegment(sketch, "E3441", {"start": v(43372.9, 69406.01) * mm, "end": v(43156.09, 69565.6) * mm});
            skLineSegment(sketch, "E3442", {"start": v(43387.71, 69426.15) * mm, "end": v(43167.02, 69588.6) * mm});
            skLineSegment(sketch, "E3443", {"start": v(43393.64, 69434.2) * mm, "end": v(43171.4, 69597.8) * mm});
            skLineSegment(sketch, "E3444", {"start": v(44318, 68589.85) * mm, "end": v(44032.14, 68800.28) * mm});
            skLineSegment(sketch, "E3445", {"start": v(44304.02, 68587.73) * mm, "end": v(44026.2, 68792.23) * mm});
            skLineSegment(sketch, "E3446", {"start": v(44335.48, 68592.5) * mm, "end": v(44039.55, 68810.35) * mm});
            skLineSegment(sketch, "E3447", {"start": v(44423.42, 68543.3) * mm, "end": v(44046.96, 68820.42) * mm});
            skLineSegment(sketch, "E3448", {"start": v(44473.51, 68611.34) * mm, "end": v(44097.05, 68888.47) * mm});
            skLineSegment(sketch, "E3449", {"start": v(44466.1, 68601.28) * mm, "end": v(44089.64, 68878.4) * mm});
            skLineSegment(sketch, "E3450", {"start": v(44490.99, 68614) * mm, "end": v(44104.46, 68898.53) * mm});
            skLineSegment(sketch, "E3451", {"start": v(44504.97, 68616.13) * mm, "end": v(44110.39, 68906.59) * mm});
            skLineSegment(sketch, "E3452", {"start": v(44335.48, 68592.5) * mm, "end": v(44405.94, 68540.64) * mm});
            skLineSegment(sketch, "E3453", {"start": v(44423.42, 68543.3) * mm, "end": v(44466.1, 68601.28) * mm});
            skLineSegment(sketch, "E3454", {"start": v(44466.1, 68601.28) * mm, "end": v(44473.51, 68611.34) * mm});
            skLineSegment(sketch, "E3455", {"start": v(44068.3, 68849.4) * mm, "end": v(44110.39, 68906.59) * mm});
            skLineSegment(sketch, "E3456", {"start": v(43351.55, 69377.02) * mm, "end": v(43393.64, 69434.2) * mm});
            skLineSegment(sketch, "E3457", {"start": v(44068.3, 68849.4) * mm, "end": v(44026.2, 68792.23) * mm});
            skLineSegment(sketch, "E3458", {"start": v(43351.55, 69377.02) * mm, "end": v(43309.46, 69319.84) * mm});
            skLineSegment(sketch, "E3459", {"start": v(43309.46, 69319.84) * mm, "end": v(43393.64, 69434.2) * mm});
            skLineSegment(sketch, "E3460", {"start": v(44026.2, 68792.23) * mm, "end": v(44110.39, 68906.59) * mm});
            skLineSegment(sketch, "E3461", {"start": v(43309.46, 69319.84) * mm, "end": v(43335.23, 69300.87) * mm});
            skLineSegment(sketch, "E3462", {"start": v(43335.23, 69300.87) * mm, "end": v(43419.41, 69415.23) * mm});
            skLineSegment(sketch, "E3463", {"start": v(43419.41, 69415.23) * mm, "end": v(43393.64, 69434.2) * mm});
            skLineSegment(sketch, "E3464", {"start": v(43393.64, 69434.2) * mm, "end": v(43309.46, 69319.84) * mm});
            skLineSegment(sketch, "E3465", {"start": v(44000.44, 68811.2) * mm, "end": v(44026.2, 68792.23) * mm});
            skLineSegment(sketch, "E3466", {"start": v(44110.39, 68906.59) * mm, "end": v(44084.62, 68925.56) * mm});
            skLineSegment(sketch, "E3467", {"start": v(44084.62, 68925.56) * mm, "end": v(44000.44, 68811.2) * mm});
            skLineSegment(sketch, "E3468", {"start": v(44026.2, 68792.23) * mm, "end": v(44000.44, 68811.2) * mm});
            skLineSegment(sketch, "E3469", {"start": v(43393.64, 69434.2) * mm, "end": v(43419.41, 69415.23) * mm});
            skLineSegment(sketch, "E3470", {"start": v(44000.44, 68811.2) * mm, "end": v(44084.62, 68925.56) * mm});
            skArc(sketch, "E3471", {"start": v(44000.44, 68811.2) * mm, "mid": v(43211.11, 70117.5) * mm, "end": v(42845.56, 68635.67) * mm});
            skLineSegment(sketch, "E3472", {"start": v(43335.23, 69300.87) * mm, "end": v(42845.56, 68635.67) * mm});
            skLineSegment(sketch, "E3473", {"start": v(42845.56, 68635.67) * mm, "end": v(42876.16, 68613.14) * mm});
            skLineSegment(sketch, "E3474", {"start": v(42876.16, 68613.14) * mm, "end": v(43365.83, 69278.34) * mm});
            skLineSegment(sketch, "E3475", {"start": v(43365.83, 69278.34) * mm, "end": v(43335.23, 69300.87) * mm});
            skLineSegment(sketch, "E3476", {"start": v(43365.83, 69278.34) * mm, "end": v(42876.16, 68613.14) * mm});
            skLineSegment(sketch, "E3477", {"start": v(43335.23, 69300.87) * mm, "end": v(43365.83, 69278.34) * mm});
            skLineSegment(sketch, "E3478", {"start": v(43309.46, 69319.84) * mm, "end": v(44026.2, 68792.23) * mm});
            skLineSegment(sketch, "E3479", {"start": v(43393.64, 69434.2) * mm, "end": v(44110.39, 68906.59) * mm});
            skLineSegment(sketch, "E3480", {"start": v(45225.14, 73684.2) * mm, "end": v(43907.2, 73515.5) * mm});
            skLineSegment(sketch, "E3481", {"start": v(45216.5, 73673.02) * mm, "end": v(43908.47, 73505.57) * mm});
            skLineSegment(sketch, "E3482", {"start": v(45235.95, 73698.19) * mm, "end": v(43905.61, 73527.89) * mm});
            skLineSegment(sketch, "E3483", {"start": v(45246.76, 73712.18) * mm, "end": v(43904.03, 73540.29) * mm});
            skLineSegment(sketch, "E3484", {"start": v(45309.02, 73792.73) * mm, "end": v(43894.88, 73611.7) * mm});
            skLineSegment(sketch, "E3485", {"start": v(43919.85, 71959.25) * mm, "end": v(44026.37, 72103.95) * mm});
            skLineSegment(sketch, "E3486", {"start": v(43911.8, 71965.17) * mm, "end": v(44015.94, 72106.66) * mm});
            skLineSegment(sketch, "E3487", {"start": v(43929.91, 71951.84) * mm, "end": v(44039.4, 72100.58) * mm});
            skLineSegment(sketch, "E3488", {"start": v(43939.98, 71944.43) * mm, "end": v(44052.44, 72097.2) * mm});
            skLineSegment(sketch, "E3489", {"start": v(44008.03, 71894.33) * mm, "end": v(44140.55, 72074.36) * mm});
            skLineSegment(sketch, "E3490", {"start": v(43997.96, 71901.74) * mm, "end": v(44127.52, 72077.74) * mm});
            skLineSegment(sketch, "E3491", {"start": v(44018.1, 71886.92) * mm, "end": v(44153.59, 72070.98) * mm});
            skLineSegment(sketch, "E3492", {"start": v(44026.15, 71881) * mm, "end": v(44164.01, 72068.28) * mm});
            skLineSegment(sketch, "E3493", {"start": v(43117.2, 70868.87) * mm, "end": v(43392.23, 71242.5) * mm});
            skLineSegment(sketch, "E3494", {"start": v(43109.14, 70874.8) * mm, "end": v(43384.18, 71248.43) * mm});
            skLineSegment(sketch, "E3495", {"start": v(43127.26, 70861.46) * mm, "end": v(43402.3, 71235.09) * mm});
            skLineSegment(sketch, "E3496", {"start": v(43137.33, 70854.05) * mm, "end": v(43412.37, 71227.68) * mm});
            skLineSegment(sketch, "E3497", {"start": v(43205.38, 70803.95) * mm, "end": v(43480.42, 71177.59) * mm});
            skLineSegment(sketch, "E3498", {"start": v(43195.31, 70811.36) * mm, "end": v(43470.35, 71185) * mm});
            skLineSegment(sketch, "E3499", {"start": v(43215.45, 70796.54) * mm, "end": v(43490.49, 71170.18) * mm});
            skLineSegment(sketch, "E3500", {"start": v(43223.5, 70790.61) * mm, "end": v(43498.54, 71164.25) * mm});
            skLineSegment(sketch, "E3501", {"start": v(43340.88, 71189.6) * mm, "end": v(43384.18, 71248.43) * mm});
            skLineSegment(sketch, "E3502", {"start": v(43109.14, 70874.8) * mm, "end": v(43256.7, 71075.25) * mm});
            skLineSegment(sketch, "E3503", {"start": v(42471.34, 69991.48) * mm, "end": v(42589.58, 70152.12) * mm});
            skLineSegment(sketch, "E3504", {"start": v(42458.81, 69991.34) * mm, "end": v(42581.53, 70158.05) * mm});
            skLineSegment(sketch, "E3505", {"start": v(42486.99, 69991.66) * mm, "end": v(42599.65, 70144.7) * mm});
            skLineSegment(sketch, "E3506", {"start": v(42502.64, 69991.83) * mm, "end": v(42609.72, 70137.3) * mm});
            skLineSegment(sketch, "E3507", {"start": v(42608.43, 69993.02) * mm, "end": v(42677.77, 70087.2) * mm});
            skLineSegment(sketch, "E3508", {"start": v(42592.78, 69992.84) * mm, "end": v(42667.7, 70094.62) * mm});
            skLineSegment(sketch, "E3509", {"start": v(42624.08, 69993.2) * mm, "end": v(42687.83, 70079.8) * mm});
            skLineSegment(sketch, "E3510", {"start": v(42636.6, 69993.33) * mm, "end": v(42695.89, 70073.87) * mm});
            skLineSegment(sketch, "E3511", {"start": v(43441.36, 71206.34) * mm, "end": v(43384.18, 71248.43) * mm});
            skLineSegment(sketch, "E3512", {"start": v(43968.97, 71923.08) * mm, "end": v(43911.8, 71965.17) * mm});
            skLineSegment(sketch, "E3513", {"start": v(43441.36, 71206.34) * mm, "end": v(43498.54, 71164.25) * mm});
            skLineSegment(sketch, "E3514", {"start": v(43968.97, 71923.08) * mm, "end": v(44026.15, 71881) * mm});
            skLineSegment(sketch, "E3515", {"start": v(44026.15, 71881) * mm, "end": v(43911.8, 71965.17) * mm});
            skLineSegment(sketch, "E3516", {"start": v(43498.54, 71164.25) * mm, "end": v(43384.18, 71248.43) * mm});
            skLineSegment(sketch, "E3517", {"start": v(44026.15, 71881) * mm, "end": v(44007.18, 71855.22) * mm});
            skLineSegment(sketch, "E3518", {"start": v(44007.18, 71855.22) * mm, "end": v(43892.82, 71939.4) * mm});
            skLineSegment(sketch, "E3519", {"start": v(43892.82, 71939.4) * mm, "end": v(43911.8, 71965.17) * mm});
            skLineSegment(sketch, "E3520", {"start": v(43911.8, 71965.17) * mm, "end": v(44026.15, 71881) * mm});
            skLineSegment(sketch, "E3521", {"start": v(43517.5, 71190.02) * mm, "end": v(43498.54, 71164.25) * mm});
            skLineSegment(sketch, "E3522", {"start": v(43384.18, 71248.43) * mm, "end": v(43403.15, 71274.2) * mm});
            skLineSegment(sketch, "E3523", {"start": v(43403.15, 71274.2) * mm, "end": v(43517.5, 71190.02) * mm});
            skLineSegment(sketch, "E3524", {"start": v(43498.54, 71164.25) * mm, "end": v(43517.5, 71190.02) * mm});
            skLineSegment(sketch, "E3525", {"start": v(43911.8, 71965.17) * mm, "end": v(43892.82, 71939.4) * mm});
            skLineSegment(sketch, "E3526", {"start": v(43517.5, 71190.02) * mm, "end": v(43403.15, 71274.2) * mm});
            skArc(sketch, "E3527", {"start": v(43517.5, 71190.02) * mm, "mid": v(44131.3, 71038.6) * mm, "end": v(44672.39, 71365.55) * mm});
            skLineSegment(sketch, "E3528", {"start": v(44007.18, 71855.22) * mm, "end": v(44672.39, 71365.55) * mm});
            skLineSegment(sketch, "E3529", {"start": v(44672.39, 71365.55) * mm, "end": v(44649.86, 71334.95) * mm});
            skLineSegment(sketch, "E3530", {"start": v(44649.86, 71334.95) * mm, "end": v(43984.65, 71824.62) * mm});
            skLineSegment(sketch, "E3531", {"start": v(43984.65, 71824.62) * mm, "end": v(44007.18, 71855.22) * mm});
            skLineSegment(sketch, "E3532", {"start": v(43984.65, 71824.62) * mm, "end": v(44649.86, 71334.95) * mm});
            skLineSegment(sketch, "E3533", {"start": v(44007.18, 71855.22) * mm, "end": v(43984.65, 71824.62) * mm});
            skLineSegment(sketch, "E3534", {"start": v(44026.15, 71881) * mm, "end": v(43498.54, 71164.25) * mm});
            skLineSegment(sketch, "E3535", {"start": v(43911.8, 71965.17) * mm, "end": v(43384.18, 71248.43) * mm});
            skLineSegment(sketch, "E3536", {"start": v(43166.32, 70832.7) * mm, "end": v(43109.14, 70874.8) * mm});
            skLineSegment(sketch, "E3537", {"start": v(42638.7, 70115.96) * mm, "end": v(42581.53, 70158.05) * mm});
            skLineSegment(sketch, "E3538", {"start": v(43166.32, 70832.7) * mm, "end": v(43223.5, 70790.61) * mm});
            skLineSegment(sketch, "E3539", {"start": v(42638.7, 70115.96) * mm, "end": v(42695.89, 70073.87) * mm});
            skLineSegment(sketch, "E3540", {"start": v(42695.89, 70073.87) * mm, "end": v(42581.53, 70158.05) * mm});
            skLineSegment(sketch, "E3541", {"start": v(43223.5, 70790.61) * mm, "end": v(43109.14, 70874.8) * mm});
            skLineSegment(sketch, "E3542", {"start": v(42695.89, 70073.87) * mm, "end": v(42714.86, 70099.64) * mm});
            skLineSegment(sketch, "E3543", {"start": v(42714.86, 70099.64) * mm, "end": v(42600.5, 70183.82) * mm});
            skLineSegment(sketch, "E3544", {"start": v(42600.5, 70183.82) * mm, "end": v(42581.53, 70158.05) * mm});
            skLineSegment(sketch, "E3545", {"start": v(42581.53, 70158.05) * mm, "end": v(42695.89, 70073.87) * mm});
            skLineSegment(sketch, "E3546", {"start": v(43204.53, 70764.84) * mm, "end": v(43223.5, 70790.61) * mm});
            skLineSegment(sketch, "E3547", {"start": v(43109.14, 70874.8) * mm, "end": v(43090.17, 70849.02) * mm});
            skLineSegment(sketch, "E3548", {"start": v(43090.17, 70849.02) * mm, "end": v(43204.53, 70764.84) * mm});
            skLineSegment(sketch, "E3549", {"start": v(43223.5, 70790.61) * mm, "end": v(43204.53, 70764.84) * mm});
            skLineSegment(sketch, "E3550", {"start": v(42581.53, 70158.05) * mm, "end": v(42600.5, 70183.82) * mm});
            skLineSegment(sketch, "E3551", {"start": v(43204.53, 70764.84) * mm, "end": v(43090.17, 70849.02) * mm});
            skArc(sketch, "E3552", {"start": v(43204.53, 70764.84) * mm, "mid": v(41898.24, 69975.52) * mm, "end": v(43380.06, 69609.97) * mm});
            skLineSegment(sketch, "E3553", {"start": v(42714.86, 70099.64) * mm, "end": v(43380.06, 69609.97) * mm});
            skLineSegment(sketch, "E3554", {"start": v(43380.06, 69609.97) * mm, "end": v(43402.59, 69640.57) * mm});
            skLineSegment(sketch, "E3555", {"start": v(43402.59, 69640.57) * mm, "end": v(42737.38, 70130.24) * mm});
            skLineSegment(sketch, "E3556", {"start": v(42737.38, 70130.24) * mm, "end": v(42714.86, 70099.64) * mm});
            skLineSegment(sketch, "E3557", {"start": v(42737.38, 70130.24) * mm, "end": v(43402.59, 69640.57) * mm});
            skLineSegment(sketch, "E3558", {"start": v(42714.86, 70099.64) * mm, "end": v(42737.38, 70130.24) * mm});
            skLineSegment(sketch, "E3559", {"start": v(42695.89, 70073.87) * mm, "end": v(43223.5, 70790.61) * mm});
            skLineSegment(sketch, "E3560", {"start": v(42581.53, 70158.05) * mm, "end": v(43109.14, 70874.8) * mm});
            skLineSegment(sketch, "E3561", {"start": v(45140.11, 71349.06) * mm, "end": v(45189.75, 71312.52) * mm});
            skLineSegment(sketch, "E3562", {"start": v(45146.04, 71357.12) * mm, "end": v(45187.63, 71326.5) * mm});
            skLineSegment(sketch, "E3563", {"start": v(45132.7, 71339) * mm, "end": v(45192.4, 71295.04) * mm});
            skLineSegment(sketch, "E3564", {"start": v(45125.3, 71328.93) * mm, "end": v(45195.06, 71277.57) * mm});
            skLineSegment(sketch, "E3565", {"start": v(45075.2, 71260.88) * mm, "end": v(45213.02, 71159.42) * mm});
            skLineSegment(sketch, "E3566", {"start": v(45082.6, 71270.95) * mm, "end": v(45210.37, 71176.9) * mm});
            skLineSegment(sketch, "E3567", {"start": v(45067.79, 71250.81) * mm, "end": v(45215.68, 71141.95) * mm});
            skLineSegment(sketch, "E3568", {"start": v(45061.86, 71242.76) * mm, "end": v(45217.8, 71127.96) * mm});
            skLineSegment(sketch, "E3569", {"start": v(44155.63, 72073.76) * mm, "end": v(44423.36, 71876.68) * mm});
            skLineSegment(sketch, "E3570", {"start": v(44161.56, 72081.81) * mm, "end": v(44429.3, 71884.73) * mm});
            skLineSegment(sketch, "E3571", {"start": v(44148.22, 72063.7) * mm, "end": v(44415.95, 71866.6) * mm});
            skLineSegment(sketch, "E3572", {"start": v(44140.81, 72053.63) * mm, "end": v(44408.54, 71856.54) * mm});
            skLineSegment(sketch, "E3573", {"start": v(44090.72, 71985.57) * mm, "end": v(44358.45, 71788.5) * mm});
            skLineSegment(sketch, "E3574", {"start": v(44098.13, 71995.64) * mm, "end": v(44365.86, 71798.56) * mm});
            skLineSegment(sketch, "E3575", {"start": v(44083.3, 71975.5) * mm, "end": v(44351.04, 71778.42) * mm});
            skLineSegment(sketch, "E3576", {"start": v(44077.38, 71967.45) * mm, "end": v(44345.11, 71770.37) * mm});
            skLineSegment(sketch, "E3577", {"start": v(45103.95, 71299.94) * mm, "end": v(45061.86, 71242.76) * mm});
            skLineSegment(sketch, "E3578", {"start": v(44387.2, 71827.55) * mm, "end": v(44345.11, 71770.37) * mm});
            skLineSegment(sketch, "E3579", {"start": v(45103.95, 71299.94) * mm, "end": v(45146.04, 71357.12) * mm});
            skLineSegment(sketch, "E3580", {"start": v(44387.2, 71827.55) * mm, "end": v(44429.3, 71884.73) * mm});
            skLineSegment(sketch, "E3581", {"start": v(44429.3, 71884.73) * mm, "end": v(44345.11, 71770.37) * mm});
            skLineSegment(sketch, "E3582", {"start": v(45146.04, 71357.12) * mm, "end": v(45061.86, 71242.76) * mm});
            skLineSegment(sketch, "E3583", {"start": v(44429.3, 71884.73) * mm, "end": v(44455.06, 71865.76) * mm});
            skLineSegment(sketch, "E3584", {"start": v(44455.06, 71865.76) * mm, "end": v(44370.88, 71751.4) * mm});
            skLineSegment(sketch, "E3585", {"start": v(44370.88, 71751.4) * mm, "end": v(44345.11, 71770.37) * mm});
            skLineSegment(sketch, "E3586", {"start": v(44345.11, 71770.37) * mm, "end": v(44429.3, 71884.73) * mm});
            skLineSegment(sketch, "E3587", {"start": v(45120.27, 71376.09) * mm, "end": v(45146.04, 71357.12) * mm});
            skLineSegment(sketch, "E3588", {"start": v(45061.86, 71242.76) * mm, "end": v(45036.09, 71261.73) * mm});
            skLineSegment(sketch, "E3589", {"start": v(45036.09, 71261.73) * mm, "end": v(45120.27, 71376.09) * mm});
            skLineSegment(sketch, "E3590", {"start": v(45146.04, 71357.12) * mm, "end": v(45120.27, 71376.09) * mm});
            skLineSegment(sketch, "E3591", {"start": v(44345.11, 71770.37) * mm, "end": v(44370.88, 71751.4) * mm});
            skLineSegment(sketch, "E3592", {"start": v(45120.27, 71376.09) * mm, "end": v(45036.09, 71261.73) * mm});
            skArc(sketch, "E3593", {"start": v(45120.27, 71376.09) * mm, "mid": v(45271.68, 71989.88) * mm, "end": v(44944.74, 72530.96) * mm});
            skLineSegment(sketch, "E3594", {"start": v(44455.06, 71865.76) * mm, "end": v(44944.74, 72530.96) * mm});
            skLineSegment(sketch, "E3595", {"start": v(44944.74, 72530.96) * mm, "end": v(44975.34, 72508.44) * mm});
            skLineSegment(sketch, "E3596", {"start": v(44975.34, 72508.44) * mm, "end": v(44485.67, 71843.23) * mm});
            skLineSegment(sketch, "E3597", {"start": v(44485.67, 71843.23) * mm, "end": v(44455.06, 71865.76) * mm});
            skLineSegment(sketch, "E3598", {"start": v(44485.67, 71843.23) * mm, "end": v(44975.34, 72508.44) * mm});
            skLineSegment(sketch, "E3599", {"start": v(44455.06, 71865.76) * mm, "end": v(44485.67, 71843.23) * mm});
            skLineSegment(sketch, "E3600", {"start": v(44429.3, 71884.73) * mm, "end": v(45146.04, 71357.12) * mm});
            skLineSegment(sketch, "E3601", {"start": v(44345.11, 71770.37) * mm, "end": v(45061.86, 71242.76) * mm});
            skLineSegment(sketch, "E3602", {"start": v(42589.36, 69385.58) * mm, "end": v(42425.01, 69928.56) * mm});
            skLineSegment(sketch, "E3603", {"start": v(42579.79, 69382.68) * mm, "end": v(42414, 69930.45) * mm});
            skLineSegment(sketch, "E3604", {"start": v(42601.33, 69389.2) * mm, "end": v(42438.8, 69926.19) * mm});
            skLineSegment(sketch, "E3605", {"start": v(42613.29, 69392.82) * mm, "end": v(42452.57, 69923.82) * mm});
            skLineSegment(sketch, "E3606", {"start": v(42682.2, 69413.68) * mm, "end": v(42531.92, 69910.17) * mm});
            skLineSegment(sketch, "E3607", {"start": v(43968.97, 73513.32) * mm, "end": v(44153.59, 72070.98) * mm});
            skLineSegment(sketch, "E3608", {"start": v(43978.9, 73514.59) * mm, "end": v(44164.01, 72068.28) * mm});
            skLineSegment(sketch, "E3609", {"start": v(43956.58, 73511.73) * mm, "end": v(44140.55, 72074.36) * mm});
            skLineSegment(sketch, "E3610", {"start": v(43944.18, 73510.14) * mm, "end": v(44127.52, 72077.74) * mm});
            skLineSegment(sketch, "E3611", {"start": v(43860.36, 73499.42) * mm, "end": v(44039.4, 72100.58) * mm});
            skLineSegment(sketch, "E3612", {"start": v(43872.76, 73501) * mm, "end": v(44052.44, 72097.2) * mm});
            skLineSegment(sketch, "E3613", {"start": v(43847.96, 73497.83) * mm, "end": v(44026.37, 72103.95) * mm});
            skLineSegment(sketch, "E3614", {"start": v(43838.04, 73496.56) * mm, "end": v(44015.94, 72106.66) * mm});
            skArc(sketch, "E3615", {"start": v(45901.23, 72580.8) * mm, "mid": v(46669.06, 73597.14) * mm, "end": v(45429.37, 73304.43) * mm});
            skArc(sketch, "E3616", {"start": v(45897.07, 72592.6) * mm, "mid": v(46660.43, 73592.06) * mm, "end": v(45438.4, 73294.96) * mm});
            skArc(sketch, "E3617", {"start": v(45906.37, 72566.18) * mm, "mid": v(46679.83, 73603.5) * mm, "end": v(45418.2, 73316.14) * mm});
            skArc(sketch, "E3618", {"start": v(45911.47, 72551.7) * mm, "mid": v(46690.6, 73609.87) * mm, "end": v(45407.18, 73327.71) * mm});
            skArc(sketch, "E3619", {"start": v(45940.04, 72470.48) * mm, "mid": v(46752.46, 73646.8) * mm, "end": v(45345.72, 73392.17) * mm});
            skLineSegment(sketch, "E3620", {"start": v(45277.47, 73276.13) * mm, "end": v(45225.14, 73684.2) * mm});
            skLineSegment(sketch, "E3621", {"start": v(45267.55, 73274.86) * mm, "end": v(45216.5, 73673.02) * mm});
            skLineSegment(sketch, "E3622", {"start": v(45289.87, 73277.72) * mm, "end": v(45235.95, 73698.19) * mm});
            skLineSegment(sketch, "E3623", {"start": v(45302.27, 73279.3) * mm, "end": v(45246.76, 73712.18) * mm});
            skLineSegment(sketch, "E3624", {"start": v(45373.68, 73288.46) * mm, "end": v(45309.02, 73792.73) * mm});
            skLineSegment(sketch, "E3625", {"start": v(45956.17, 72353.67) * mm, "end": v(45803.77, 72465.85) * mm});
            skLineSegment(sketch, "E3626", {"start": v(45942.18, 72351.55) * mm, "end": v(45797.84, 72457.8) * mm});
            skLineSegment(sketch, "E3627", {"start": v(45973.64, 72356.33) * mm, "end": v(45811.18, 72475.92) * mm});
            skLineSegment(sketch, "E3628", {"start": v(45991.12, 72358.98) * mm, "end": v(45818.59, 72485.99) * mm});
            skLineSegment(sketch, "E3629", {"start": v(46091.79, 72374.28) * mm, "end": v(45861.27, 72543.97) * mm});
            skLineSegment(sketch, "E3630", {"start": v(45811.82, 72459.93) * mm, "end": v(45901.09, 72581.2) * mm});
            skLineSegment(sketch, "E3631", {"start": v(45803.77, 72465.85) * mm, "end": v(45897.07, 72592.6) * mm});
            skLineSegment(sketch, "E3632", {"start": v(45821.89, 72452.52) * mm, "end": v(45906.1, 72566.93) * mm});
            skLineSegment(sketch, "E3633", {"start": v(45831.95, 72445.1) * mm, "end": v(45911.13, 72552.66) * mm});
            skLineSegment(sketch, "E3634", {"start": v(45889.94, 72402.42) * mm, "end": v(45940.04, 72470.48) * mm});
            skLineSegment(sketch, "E3635", {"start": v(45429.74, 73304.04) * mm, "end": v(45275.46, 73286.62) * mm});
            skLineSegment(sketch, "E3636", {"start": v(45438.4, 73294.96) * mm, "end": v(45276.58, 73276.69) * mm});
            skLineSegment(sketch, "E3637", {"start": v(45418.91, 73315.4) * mm, "end": v(45274.06, 73299.05) * mm});
            skLineSegment(sketch, "E3638", {"start": v(45408.09, 73326.76) * mm, "end": v(45272.66, 73311.47) * mm});
            skLineSegment(sketch, "E3639", {"start": v(45345.72, 73392.17) * mm, "end": v(45264.58, 73383.01) * mm});
            skLineSegment(sketch, "E3640", {"start": v(44877.67, 73590.12) * mm, "end": v(44944.33, 73069.37) * mm});
            skLineSegment(sketch, "E3641", {"start": v(44944.33, 73069.37) * mm, "end": v(44349.19, 72993.18) * mm});
            skLineSegment(sketch, "E3642", {"start": v(44349.19, 72993.18) * mm, "end": v(44282.53, 73513.93) * mm});
            skLineSegment(sketch, "E3643", {"start": v(44279.35, 73538.73) * mm, "end": v(44874.5, 73614.92) * mm});
            skLineSegment(sketch, "E3644", {"start": v(44874.5, 73614.92) * mm, "end": v(44877.67, 73590.12) * mm});
            skLineSegment(sketch, "E3645", {"start": v(44877.67, 73590.12) * mm, "end": v(44282.53, 73513.93) * mm});
            skLineSegment(sketch, "E3646", {"start": v(44282.53, 73513.93) * mm, "end": v(44279.35, 73538.73) * mm});
            skArc(sketch, "E3647", {"start": v(44615.97, 73271.77) * mm, "mid": v(44650.97, 73291.8) * mm, "end": v(44661.55, 73330.73) * mm});
            skArc(sketch, "E3648", {"start": v(44661.55, 73330.73) * mm, "mid": v(44641.5, 73365.72) * mm, "end": v(44602.6, 73376.3) * mm});
            skArc(sketch, "E3649", {"start": v(44602.6, 73376.3) * mm, "mid": v(44567.6, 73356.26) * mm, "end": v(44557.02, 73317.35) * mm});
            skArc(sketch, "E3650", {"start": v(44557.02, 73317.35) * mm, "mid": v(44577.06, 73282.35) * mm, "end": v(44615.97, 73271.77) * mm});
            skLineSegment(sketch, "E3651", {"start": v(44647.24, 73560.62) * mm, "end": v(44648.21, 73553.03) * mm});
            skLineSegment(sketch, "E3652", {"start": v(44648.21, 73553.03) * mm, "end": v(44697.8, 73559.37) * mm});
            skLineSegment(sketch, "E3653", {"start": v(44697.8, 73559.37) * mm, "end": v(44696.84, 73566.97) * mm});
            skArc(sketch, "E3654", {"start": v(44598.93, 73386.82) * mm, "mid": v(44598.95, 73386.82) * mm, "end": v(44598.97, 73386.82) * mm});
            skLineSegment(sketch, "E3655", {"start": v(44598.97, 73386.82) * mm, "end": v(44599.18, 73386.8) * mm});
            skArc(sketch, "E3656", {"start": v(44599.18, 73386.8) * mm, "mid": v(44599.42, 73386.78) * mm, "end": v(44599.65, 73386.78) * mm});
            skLineSegment(sketch, "E3657", {"start": v(44599.65, 73386.78) * mm, "end": v(44599.97, 73386.78) * mm});
            skArc(sketch, "E3658", {"start": v(44599.97, 73386.78) * mm, "mid": v(44600.53, 73386.8) * mm, "end": v(44601.09, 73386.85) * mm});
            skLineSegment(sketch, "E3659", {"start": v(44601.09, 73386.85) * mm, "end": v(44601.2, 73386.86) * mm});
            skArc(sketch, "E3660", {"start": v(44601.2, 73386.86) * mm, "mid": v(44601.22, 73386.86) * mm, "end": v(44601.24, 73386.87) * mm});
            skArc(sketch, "E3661", {"start": v(44601.24, 73386.87) * mm, "mid": v(44601.25, 73386.87) * mm, "end": v(44601.27, 73386.87) * mm});
            skLineSegment(sketch, "E3662", {"start": v(44601.27, 73386.87) * mm, "end": v(44601.43, 73386.9) * mm});
            skArc(sketch, "E3663", {"start": v(44601.43, 73386.9) * mm, "mid": v(44601.61, 73386.92) * mm, "end": v(44601.8, 73386.95) * mm});
            skLineSegment(sketch, "E3664", {"start": v(44601.8, 73386.95) * mm, "end": v(44601.99, 73386.99) * mm});
            skArc(sketch, "E3665", {"start": v(44601.99, 73386.99) * mm, "mid": v(44602.35, 73387.07) * mm, "end": v(44602.72, 73387.16) * mm});
            skLineSegment(sketch, "E3666", {"start": v(44602.72, 73387.16) * mm, "end": v(44602.75, 73387.17) * mm});
            skArc(sketch, "E3667", {"start": v(44602.75, 73387.17) * mm, "mid": v(44602.76, 73387.17) * mm, "end": v(44602.77, 73387.18) * mm});
            skLineSegment(sketch, "E3668", {"start": v(44659.08, 73549.16) * mm, "end": v(44658.57, 73549.1) * mm});
            skLineSegment(sketch, "E3669", {"start": v(44658.57, 73549.1) * mm, "end": v(44658.08, 73549.03) * mm});
            skLineSegment(sketch, "E3670", {"start": v(44658.08, 73549.03) * mm, "end": v(44657.62, 73548.97) * mm});
            skLineSegment(sketch, "E3671", {"start": v(44657.62, 73548.97) * mm, "end": v(44657.18, 73548.91) * mm});
            skLineSegment(sketch, "E3672", {"start": v(44657.18, 73548.91) * mm, "end": v(44656.77, 73548.86) * mm});
            skLineSegment(sketch, "E3673", {"start": v(44656.77, 73548.86) * mm, "end": v(44656.39, 73548.81) * mm});
            skLineSegment(sketch, "E3674", {"start": v(44656.39, 73548.81) * mm, "end": v(44656.03, 73548.77) * mm});
            skLineSegment(sketch, "E3675", {"start": v(44656.03, 73548.77) * mm, "end": v(44655.7, 73548.73) * mm});
            skLineSegment(sketch, "E3676", {"start": v(44655.7, 73548.73) * mm, "end": v(44655.4, 73548.69) * mm});
            skLineSegment(sketch, "E3677", {"start": v(44655.4, 73548.69) * mm, "end": v(44655.14, 73548.65) * mm});
            skLineSegment(sketch, "E3678", {"start": v(44655.14, 73548.65) * mm, "end": v(44654.9, 73548.62) * mm});
            skLineSegment(sketch, "E3679", {"start": v(44654.9, 73548.62) * mm, "end": v(44654.69, 73548.6) * mm});
            skLineSegment(sketch, "E3680", {"start": v(44654.69, 73548.6) * mm, "end": v(44654.5, 73548.57) * mm});
            skLineSegment(sketch, "E3681", {"start": v(44654.5, 73548.57) * mm, "end": v(44654.36, 73548.55) * mm});
            skLineSegment(sketch, "E3682", {"start": v(44654.36, 73548.55) * mm, "end": v(44654.24, 73548.54) * mm});
            skLineSegment(sketch, "E3683", {"start": v(44654.24, 73548.54) * mm, "end": v(44654.15, 73548.53) * mm});
            skLineSegment(sketch, "E3684", {"start": v(44654.15, 73548.53) * mm, "end": v(44654.1, 73548.52) * mm});
            skLineSegment(sketch, "E3685", {"start": v(44654.1, 73548.52) * mm, "end": v(44654.07, 73548.52) * mm});
            skLineSegment(sketch, "E3686", {"start": v(44654.07, 73548.52) * mm, "end": v(44653.9, 73548.5) * mm});
            skLineSegment(sketch, "E3687", {"start": v(44653.9, 73548.5) * mm, "end": v(44653.73, 73548.49) * mm});
            skLineSegment(sketch, "E3688", {"start": v(44653.73, 73548.49) * mm, "end": v(44653.55, 73548.48) * mm});
            skLineSegment(sketch, "E3689", {"start": v(44653.55, 73548.48) * mm, "end": v(44653.38, 73548.48) * mm});
            skLineSegment(sketch, "E3690", {"start": v(44653.38, 73548.48) * mm, "end": v(44653.2, 73548.5) * mm});
            skLineSegment(sketch, "E3691", {"start": v(44653.2, 73548.5) * mm, "end": v(44653.03, 73548.5) * mm});
            skLineSegment(sketch, "E3692", {"start": v(44653.03, 73548.5) * mm, "end": v(44652.86, 73548.53) * mm});
            skLineSegment(sketch, "E3693", {"start": v(44652.86, 73548.53) * mm, "end": v(44652.69, 73548.56) * mm});
            skLineSegment(sketch, "E3694", {"start": v(44652.69, 73548.56) * mm, "end": v(44652.52, 73548.6) * mm});
            skLineSegment(sketch, "E3695", {"start": v(44652.52, 73548.6) * mm, "end": v(44652.35, 73548.64) * mm});
            skLineSegment(sketch, "E3696", {"start": v(44652.35, 73548.64) * mm, "end": v(44652.18, 73548.7) * mm});
            skLineSegment(sketch, "E3697", {"start": v(44652.18, 73548.7) * mm, "end": v(44652.02, 73548.75) * mm});
            skLineSegment(sketch, "E3698", {"start": v(44652.02, 73548.75) * mm, "end": v(44651.86, 73548.81) * mm});
            skLineSegment(sketch, "E3699", {"start": v(44651.86, 73548.81) * mm, "end": v(44651.7, 73548.88) * mm});
            skLineSegment(sketch, "E3700", {"start": v(44651.7, 73548.88) * mm, "end": v(44651.54, 73548.96) * mm});
            skLineSegment(sketch, "E3701", {"start": v(44651.54, 73548.96) * mm, "end": v(44651.39, 73549.04) * mm});
            skLineSegment(sketch, "E3702", {"start": v(44651.39, 73549.04) * mm, "end": v(44651.24, 73549.13) * mm});
            skLineSegment(sketch, "E3703", {"start": v(44651.24, 73549.13) * mm, "end": v(44651.1, 73549.22) * mm});
            skLineSegment(sketch, "E3704", {"start": v(44651.1, 73549.22) * mm, "end": v(44650.95, 73549.32) * mm});
            skLineSegment(sketch, "E3705", {"start": v(44650.95, 73549.32) * mm, "end": v(44650.81, 73549.43) * mm});
            skLineSegment(sketch, "E3706", {"start": v(44650.81, 73549.43) * mm, "end": v(44650.68, 73549.54) * mm});
            skLineSegment(sketch, "E3707", {"start": v(44650.68, 73549.54) * mm, "end": v(44650.55, 73549.66) * mm});
            skLineSegment(sketch, "E3708", {"start": v(44650.55, 73549.66) * mm, "end": v(44650.42, 73549.78) * mm});
            skLineSegment(sketch, "E3709", {"start": v(44650.42, 73549.78) * mm, "end": v(44650.3, 73549.9) * mm});
            skLineSegment(sketch, "E3710", {"start": v(44650.3, 73549.9) * mm, "end": v(44650.19, 73550.04) * mm});
            skLineSegment(sketch, "E3711", {"start": v(44650.19, 73550.04) * mm, "end": v(44650.08, 73550.17) * mm});
            skLineSegment(sketch, "E3712", {"start": v(44650.08, 73550.17) * mm, "end": v(44649.98, 73550.31) * mm});
            skLineSegment(sketch, "E3713", {"start": v(44649.98, 73550.31) * mm, "end": v(44649.88, 73550.45) * mm});
            skLineSegment(sketch, "E3714", {"start": v(44649.88, 73550.45) * mm, "end": v(44649.79, 73550.6) * mm});
            skLineSegment(sketch, "E3715", {"start": v(44649.79, 73550.6) * mm, "end": v(44649.7, 73550.75) * mm});
            skLineSegment(sketch, "E3716", {"start": v(44649.7, 73550.75) * mm, "end": v(44649.62, 73550.9) * mm});
            skLineSegment(sketch, "E3717", {"start": v(44649.62, 73550.9) * mm, "end": v(44649.55, 73551.07) * mm});
            skLineSegment(sketch, "E3718", {"start": v(44649.55, 73551.07) * mm, "end": v(44649.48, 73551.23) * mm});
            skLineSegment(sketch, "E3719", {"start": v(44649.48, 73551.23) * mm, "end": v(44649.42, 73551.39) * mm});
            skLineSegment(sketch, "E3720", {"start": v(44649.42, 73551.39) * mm, "end": v(44649.36, 73551.55) * mm});
            skLineSegment(sketch, "E3721", {"start": v(44649.36, 73551.55) * mm, "end": v(44649.32, 73551.72) * mm});
            skLineSegment(sketch, "E3722", {"start": v(44649.32, 73551.72) * mm, "end": v(44649.28, 73551.9) * mm});
            skLineSegment(sketch, "E3723", {"start": v(44649.28, 73551.9) * mm, "end": v(44649.24, 73552.06) * mm});
            skLineSegment(sketch, "E3724", {"start": v(44649.24, 73552.06) * mm, "end": v(44649.21, 73552.23) * mm});
            skLineSegment(sketch, "E3725", {"start": v(44649.21, 73552.23) * mm, "end": v(44649.2, 73552.28) * mm});
            skLineSegment(sketch, "E3726", {"start": v(44649.2, 73552.28) * mm, "end": v(44649.1, 73553.14) * mm});
            skLineSegment(sketch, "E3727", {"start": v(44654.07, 73548.52) * mm, "end": v(44654.09, 73548.52) * mm});
            skLineSegment(sketch, "E3728", {"start": v(44654.09, 73548.52) * mm, "end": v(44654.14, 73548.53) * mm});
            skLineSegment(sketch, "E3729", {"start": v(44654.14, 73548.53) * mm, "end": v(44654.22, 73548.54) * mm});
            skLineSegment(sketch, "E3730", {"start": v(44654.22, 73548.54) * mm, "end": v(44654.32, 73548.55) * mm});
            skLineSegment(sketch, "E3731", {"start": v(44654.32, 73548.55) * mm, "end": v(44654.46, 73548.57) * mm});
            skLineSegment(sketch, "E3732", {"start": v(44654.46, 73548.57) * mm, "end": v(44654.64, 73548.59) * mm});
            skLineSegment(sketch, "E3733", {"start": v(44654.64, 73548.59) * mm, "end": v(44654.84, 73548.61) * mm});
            skLineSegment(sketch, "E3734", {"start": v(44654.84, 73548.61) * mm, "end": v(44655.07, 73548.64) * mm});
            skLineSegment(sketch, "E3735", {"start": v(44655.07, 73548.64) * mm, "end": v(44655.33, 73548.68) * mm});
            skLineSegment(sketch, "E3736", {"start": v(44655.33, 73548.68) * mm, "end": v(44655.62, 73548.72) * mm});
            skLineSegment(sketch, "E3737", {"start": v(44655.62, 73548.72) * mm, "end": v(44655.94, 73548.76) * mm});
            skLineSegment(sketch, "E3738", {"start": v(44655.94, 73548.76) * mm, "end": v(44656.29, 73548.8) * mm});
            skLineSegment(sketch, "E3739", {"start": v(44656.29, 73548.8) * mm, "end": v(44656.66, 73548.85) * mm});
            skLineSegment(sketch, "E3740", {"start": v(44656.66, 73548.85) * mm, "end": v(44657.07, 73548.9) * mm});
            skLineSegment(sketch, "E3741", {"start": v(44657.07, 73548.9) * mm, "end": v(44657.5, 73548.96) * mm});
            skLineSegment(sketch, "E3742", {"start": v(44657.5, 73548.96) * mm, "end": v(44657.95, 73549.01) * mm});
            skLineSegment(sketch, "E3743", {"start": v(44657.95, 73549.01) * mm, "end": v(44658.43, 73549.08) * mm});
            skLineSegment(sketch, "E3744", {"start": v(44658.43, 73549.08) * mm, "end": v(44658.94, 73549.14) * mm});
            skLineSegment(sketch, "E3745", {"start": v(44658.94, 73549.14) * mm, "end": v(44659.47, 73549.2) * mm});
            skLineSegment(sketch, "E3746", {"start": v(44659.47, 73549.2) * mm, "end": v(44660.02, 73549.28) * mm});
            skLineSegment(sketch, "E3747", {"start": v(44660.02, 73549.28) * mm, "end": v(44660.6, 73549.35) * mm});
            skLineSegment(sketch, "E3748", {"start": v(44660.6, 73549.35) * mm, "end": v(44661.19, 73549.43) * mm});
            skLineSegment(sketch, "E3749", {"start": v(44661.19, 73549.43) * mm, "end": v(44661.8, 73549.5) * mm});
            skLineSegment(sketch, "E3750", {"start": v(44661.8, 73549.5) * mm, "end": v(44662.43, 73549.59) * mm});
            skLineSegment(sketch, "E3751", {"start": v(44662.43, 73549.59) * mm, "end": v(44663.08, 73549.67) * mm});
            skLineSegment(sketch, "E3752", {"start": v(44663.08, 73549.67) * mm, "end": v(44663.75, 73549.76) * mm});
            skLineSegment(sketch, "E3753", {"start": v(44663.75, 73549.76) * mm, "end": v(44664.44, 73549.84) * mm});
            skLineSegment(sketch, "E3754", {"start": v(44664.44, 73549.84) * mm, "end": v(44665.13, 73549.93) * mm});
            skLineSegment(sketch, "E3755", {"start": v(44665.13, 73549.93) * mm, "end": v(44665.85, 73550.02) * mm});
            skLineSegment(sketch, "E3756", {"start": v(44665.85, 73550.02) * mm, "end": v(44666.57, 73550.12) * mm});
            skLineSegment(sketch, "E3757", {"start": v(44666.57, 73550.12) * mm, "end": v(44667.3, 73550.21) * mm});
            skLineSegment(sketch, "E3758", {"start": v(44667.3, 73550.21) * mm, "end": v(44668.05, 73550.3) * mm});
            skLineSegment(sketch, "E3759", {"start": v(44668.05, 73550.3) * mm, "end": v(44668.8, 73550.4) * mm});
            skLineSegment(sketch, "E3760", {"start": v(44668.8, 73550.4) * mm, "end": v(44669.57, 73550.5) * mm});
            skLineSegment(sketch, "E3761", {"start": v(44669.57, 73550.5) * mm, "end": v(44670.34, 73550.6) * mm});
            skLineSegment(sketch, "E3762", {"start": v(44670.34, 73550.6) * mm, "end": v(44671.12, 73550.7) * mm});
            skLineSegment(sketch, "E3763", {"start": v(44671.12, 73550.7) * mm, "end": v(44671.9, 73550.8) * mm});
            skLineSegment(sketch, "E3764", {"start": v(44671.9, 73550.8) * mm, "end": v(44672.68, 73550.9) * mm});
            skLineSegment(sketch, "E3765", {"start": v(44672.68, 73550.9) * mm, "end": v(44673.46, 73551) * mm});
            skLineSegment(sketch, "E3766", {"start": v(44673.46, 73551) * mm, "end": v(44673.67, 73551.03) * mm});
            skLineSegment(sketch, "E3767", {"start": v(44673.67, 73551.03) * mm, "end": v(44674.46, 73551.13) * mm});
            skLineSegment(sketch, "E3768", {"start": v(44674.46, 73551.13) * mm, "end": v(44675.24, 73551.23) * mm});
            skLineSegment(sketch, "E3769", {"start": v(44675.24, 73551.23) * mm, "end": v(44676.02, 73551.33) * mm});
            skLineSegment(sketch, "E3770", {"start": v(44676.02, 73551.33) * mm, "end": v(44676.8, 73551.43) * mm});
            skLineSegment(sketch, "E3771", {"start": v(44676.8, 73551.43) * mm, "end": v(44677.57, 73551.52) * mm});
            skLineSegment(sketch, "E3772", {"start": v(44677.57, 73551.52) * mm, "end": v(44678.33, 73551.62) * mm});
            skLineSegment(sketch, "E3773", {"start": v(44678.33, 73551.62) * mm, "end": v(44679.09, 73551.72) * mm});
            skLineSegment(sketch, "E3774", {"start": v(44679.09, 73551.72) * mm, "end": v(44679.84, 73551.81) * mm});
            skLineSegment(sketch, "E3775", {"start": v(44679.84, 73551.81) * mm, "end": v(44680.58, 73551.9) * mm});
            skLineSegment(sketch, "E3776", {"start": v(44680.58, 73551.9) * mm, "end": v(44681.3, 73552) * mm});
            skLineSegment(sketch, "E3777", {"start": v(44681.3, 73552) * mm, "end": v(44682.02, 73552.1) * mm});
            skLineSegment(sketch, "E3778", {"start": v(44682.02, 73552.1) * mm, "end": v(44682.72, 73552.18) * mm});
            skLineSegment(sketch, "E3779", {"start": v(44682.72, 73552.18) * mm, "end": v(44683.41, 73552.27) * mm});
            skLineSegment(sketch, "E3780", {"start": v(44683.41, 73552.27) * mm, "end": v(44684.08, 73552.36) * mm});
            skLineSegment(sketch, "E3781", {"start": v(44684.08, 73552.36) * mm, "end": v(44684.74, 73552.44) * mm});
            skLineSegment(sketch, "E3782", {"start": v(44684.74, 73552.44) * mm, "end": v(44685.38, 73552.52) * mm});
            skLineSegment(sketch, "E3783", {"start": v(44685.38, 73552.52) * mm, "end": v(44686, 73552.6) * mm});
            skLineSegment(sketch, "E3784", {"start": v(44686, 73552.6) * mm, "end": v(44686.6, 73552.68) * mm});
            skLineSegment(sketch, "E3785", {"start": v(44686.6, 73552.68) * mm, "end": v(44687.17, 73552.75) * mm});
            skLineSegment(sketch, "E3786", {"start": v(44687.17, 73552.75) * mm, "end": v(44687.73, 73552.83) * mm});
            skLineSegment(sketch, "E3787", {"start": v(44687.73, 73552.83) * mm, "end": v(44688.27, 73552.9) * mm});
            skLineSegment(sketch, "E3788", {"start": v(44688.27, 73552.9) * mm, "end": v(44688.78, 73552.96) * mm});
            skLineSegment(sketch, "E3789", {"start": v(44688.78, 73552.96) * mm, "end": v(44689.26, 73553.02) * mm});
            skLineSegment(sketch, "E3790", {"start": v(44689.26, 73553.02) * mm, "end": v(44689.73, 73553.08) * mm});
            skLineSegment(sketch, "E3791", {"start": v(44689.73, 73553.08) * mm, "end": v(44690.16, 73553.14) * mm});
            skLineSegment(sketch, "E3792", {"start": v(44690.16, 73553.14) * mm, "end": v(44690.57, 73553.19) * mm});
            skLineSegment(sketch, "E3793", {"start": v(44690.57, 73553.19) * mm, "end": v(44690.96, 73553.24) * mm});
            skLineSegment(sketch, "E3794", {"start": v(44690.96, 73553.24) * mm, "end": v(44691.31, 73553.28) * mm});
            skLineSegment(sketch, "E3795", {"start": v(44691.31, 73553.28) * mm, "end": v(44691.64, 73553.33) * mm});
            skLineSegment(sketch, "E3796", {"start": v(44691.64, 73553.33) * mm, "end": v(44691.94, 73553.36) * mm});
            skLineSegment(sketch, "E3797", {"start": v(44691.94, 73553.36) * mm, "end": v(44692.2, 73553.4) * mm});
            skLineSegment(sketch, "E3798", {"start": v(44692.2, 73553.4) * mm, "end": v(44692.45, 73553.43) * mm});
            skLineSegment(sketch, "E3799", {"start": v(44692.45, 73553.43) * mm, "end": v(44692.66, 73553.46) * mm});
            skLineSegment(sketch, "E3800", {"start": v(44692.66, 73553.46) * mm, "end": v(44692.84, 73553.48) * mm});
            skLineSegment(sketch, "E3801", {"start": v(44692.84, 73553.48) * mm, "end": v(44692.99, 73553.5) * mm});
            skLineSegment(sketch, "E3802", {"start": v(44692.99, 73553.5) * mm, "end": v(44693.1, 73553.51) * mm});
            skLineSegment(sketch, "E3803", {"start": v(44693.1, 73553.51) * mm, "end": v(44693.19, 73553.52) * mm});
            skLineSegment(sketch, "E3804", {"start": v(44693.19, 73553.52) * mm, "end": v(44693.24, 73553.53) * mm});
            skLineSegment(sketch, "E3805", {"start": v(44693.24, 73553.53) * mm, "end": v(44693.27, 73553.53) * mm});
            skLineSegment(sketch, "E3806", {"start": v(44693.27, 73553.53) * mm, "end": v(44693.32, 73553.54) * mm});
            skLineSegment(sketch, "E3807", {"start": v(44693.32, 73553.54) * mm, "end": v(44693.49, 73553.57) * mm});
            skLineSegment(sketch, "E3808", {"start": v(44693.49, 73553.57) * mm, "end": v(44693.66, 73553.6) * mm});
            skLineSegment(sketch, "E3809", {"start": v(44693.66, 73553.6) * mm, "end": v(44693.83, 73553.64) * mm});
            skLineSegment(sketch, "E3810", {"start": v(44693.83, 73553.64) * mm, "end": v(44694, 73553.7) * mm});
            skLineSegment(sketch, "E3811", {"start": v(44694, 73553.7) * mm, "end": v(44694.16, 73553.75) * mm});
            skLineSegment(sketch, "E3812", {"start": v(44694.16, 73553.75) * mm, "end": v(44694.32, 73553.8) * mm});
            skLineSegment(sketch, "E3813", {"start": v(44694.32, 73553.8) * mm, "end": v(44694.48, 73553.87) * mm});
            skLineSegment(sketch, "E3814", {"start": v(44694.48, 73553.87) * mm, "end": v(44694.64, 73553.95) * mm});
            skLineSegment(sketch, "E3815", {"start": v(44694.64, 73553.95) * mm, "end": v(44694.8, 73554.03) * mm});
            skLineSegment(sketch, "E3816", {"start": v(44694.8, 73554.03) * mm, "end": v(44694.95, 73554.11) * mm});
            skLineSegment(sketch, "E3817", {"start": v(44694.95, 73554.11) * mm, "end": v(44695.1, 73554.2) * mm});
            skLineSegment(sketch, "E3818", {"start": v(44695.1, 73554.2) * mm, "end": v(44695.24, 73554.3) * mm});
            skLineSegment(sketch, "E3819", {"start": v(44695.24, 73554.3) * mm, "end": v(44695.38, 73554.4) * mm});
            skLineSegment(sketch, "E3820", {"start": v(44695.38, 73554.4) * mm, "end": v(44695.51, 73554.52) * mm});
            skLineSegment(sketch, "E3821", {"start": v(44695.51, 73554.52) * mm, "end": v(44695.64, 73554.63) * mm});
            skLineSegment(sketch, "E3822", {"start": v(44695.64, 73554.63) * mm, "end": v(44695.77, 73554.75) * mm});
            skLineSegment(sketch, "E3823", {"start": v(44695.77, 73554.75) * mm, "end": v(44695.9, 73554.88) * mm});
            skLineSegment(sketch, "E3824", {"start": v(44695.9, 73554.88) * mm, "end": v(44696, 73555) * mm});
            skLineSegment(sketch, "E3825", {"start": v(44696, 73555) * mm, "end": v(44696.12, 73555.14) * mm});
            skLineSegment(sketch, "E3826", {"start": v(44696.12, 73555.14) * mm, "end": v(44696.23, 73555.28) * mm});
            skLineSegment(sketch, "E3827", {"start": v(44696.23, 73555.28) * mm, "end": v(44696.33, 73555.42) * mm});
            skLineSegment(sketch, "E3828", {"start": v(44696.33, 73555.42) * mm, "end": v(44696.42, 73555.57) * mm});
            skLineSegment(sketch, "E3829", {"start": v(44696.42, 73555.57) * mm, "end": v(44696.5, 73555.72) * mm});
            skLineSegment(sketch, "E3830", {"start": v(44696.5, 73555.72) * mm, "end": v(44696.6, 73555.87) * mm});
            skLineSegment(sketch, "E3831", {"start": v(44696.6, 73555.87) * mm, "end": v(44696.67, 73556.03) * mm});
            skLineSegment(sketch, "E3832", {"start": v(44696.67, 73556.03) * mm, "end": v(44696.74, 73556.18) * mm});
            skLineSegment(sketch, "E3833", {"start": v(44696.74, 73556.18) * mm, "end": v(44696.8, 73556.35) * mm});
            skLineSegment(sketch, "E3834", {"start": v(44696.8, 73556.35) * mm, "end": v(44696.86, 73556.51) * mm});
            skLineSegment(sketch, "E3835", {"start": v(44696.86, 73556.51) * mm, "end": v(44696.9, 73556.68) * mm});
            skLineSegment(sketch, "E3836", {"start": v(44696.9, 73556.68) * mm, "end": v(44696.95, 73556.85) * mm});
            skLineSegment(sketch, "E3837", {"start": v(44696.95, 73556.85) * mm, "end": v(44696.99, 73557.02) * mm});
            skLineSegment(sketch, "E3838", {"start": v(44696.99, 73557.02) * mm, "end": v(44697.02, 73557.19) * mm});
            skLineSegment(sketch, "E3839", {"start": v(44697.02, 73557.19) * mm, "end": v(44697.04, 73557.36) * mm});
            skLineSegment(sketch, "E3840", {"start": v(44697.04, 73557.36) * mm, "end": v(44697.06, 73557.53) * mm});
            skLineSegment(sketch, "E3841", {"start": v(44697.06, 73557.53) * mm, "end": v(44697.07, 73557.7) * mm});
            skLineSegment(sketch, "E3842", {"start": v(44697.07, 73557.7) * mm, "end": v(44697.07, 73557.88) * mm});
            skLineSegment(sketch, "E3843", {"start": v(44697.07, 73557.88) * mm, "end": v(44697.06, 73558.05) * mm});
            skLineSegment(sketch, "E3844", {"start": v(44697.06, 73558.05) * mm, "end": v(44697.05, 73558.23) * mm});
            skLineSegment(sketch, "E3845", {"start": v(44697.05, 73558.23) * mm, "end": v(44697.03, 73558.4) * mm});
            skLineSegment(sketch, "E3846", {"start": v(44697.03, 73558.4) * mm, "end": v(44696.92, 73559.26) * mm});
            skLineSegment(sketch, "E3847", {"start": v(44589.16, 73403.12) * mm, "end": v(44588.95, 73402.68) * mm});
            skLineSegment(sketch, "E3848", {"start": v(44588.95, 73402.68) * mm, "end": v(44588.75, 73402.24) * mm});
            skLineSegment(sketch, "E3849", {"start": v(44588.75, 73402.24) * mm, "end": v(44588.57, 73401.8) * mm});
            skLineSegment(sketch, "E3850", {"start": v(44588.57, 73401.8) * mm, "end": v(44588.4, 73401.34) * mm});
            skLineSegment(sketch, "E3851", {"start": v(44588.4, 73401.34) * mm, "end": v(44588.26, 73400.88) * mm});
            skLineSegment(sketch, "E3852", {"start": v(44588.26, 73400.88) * mm, "end": v(44588.13, 73400.4) * mm});
            skLineSegment(sketch, "E3853", {"start": v(44588.13, 73400.4) * mm, "end": v(44588.03, 73399.94) * mm});
            skLineSegment(sketch, "E3854", {"start": v(44588.03, 73399.94) * mm, "end": v(44587.94, 73399.46) * mm});
            skLineSegment(sketch, "E3855", {"start": v(44587.94, 73399.46) * mm, "end": v(44587.87, 73398.98) * mm});
            skLineSegment(sketch, "E3856", {"start": v(44587.87, 73398.98) * mm, "end": v(44587.82, 73398.5) * mm});
            skLineSegment(sketch, "E3857", {"start": v(44587.82, 73398.5) * mm, "end": v(44587.79, 73398.02) * mm});
            skLineSegment(sketch, "E3858", {"start": v(44587.79, 73398.02) * mm, "end": v(44587.78, 73397.53) * mm});
            skLineSegment(sketch, "E3859", {"start": v(44587.78, 73397.53) * mm, "end": v(44587.78, 73397.05) * mm});
            skLineSegment(sketch, "E3860", {"start": v(44587.78, 73397.05) * mm, "end": v(44587.81, 73396.57) * mm});
            skLineSegment(sketch, "E3861", {"start": v(44587.81, 73396.57) * mm, "end": v(44587.86, 73396.08) * mm});
            skLineSegment(sketch, "E3862", {"start": v(44587.86, 73396.08) * mm, "end": v(44587.92, 73395.6) * mm});
            skLineSegment(sketch, "E3863", {"start": v(44587.92, 73395.6) * mm, "end": v(44588, 73395.13) * mm});
            skLineSegment(sketch, "E3864", {"start": v(44588, 73395.13) * mm, "end": v(44588.11, 73394.66) * mm});
            skLineSegment(sketch, "E3865", {"start": v(44588.11, 73394.66) * mm, "end": v(44588.24, 73394.19) * mm});
            skLineSegment(sketch, "E3866", {"start": v(44588.24, 73394.19) * mm, "end": v(44588.38, 73393.72) * mm});
            skLineSegment(sketch, "E3867", {"start": v(44588.38, 73393.72) * mm, "end": v(44588.53, 73393.29) * mm});
            skLineSegment(sketch, "E3868", {"start": v(44588.53, 73393.29) * mm, "end": v(44588.59, 73393.13) * mm});
            skArc(sketch, "E3869", {"start": v(44588.59, 73393.13) * mm, "mid": v(44588.58, 73393.16) * mm, "end": v(44588.57, 73393.19) * mm});
            skArc(sketch, "E3870", {"start": v(44588.57, 73393.19) * mm, "mid": v(44588.44, 73393.56) * mm, "end": v(44588.32, 73393.95) * mm});
            skLineSegment(sketch, "E3871", {"start": v(44588.32, 73393.95) * mm, "end": v(44588.31, 73393.97) * mm});
            skArc(sketch, "E3872", {"start": v(44588.31, 73393.97) * mm, "mid": v(44588.2, 73394.39) * mm, "end": v(44588.1, 73394.8) * mm});
            skLineSegment(sketch, "E3873", {"start": v(44588.1, 73394.8) * mm, "end": v(44588.05, 73395.04) * mm});
            skArc(sketch, "E3874", {"start": v(44588.05, 73395.04) * mm, "mid": v(44588, 73395.28) * mm, "end": v(44587.97, 73395.52) * mm});
            skLineSegment(sketch, "E3875", {"start": v(44587.97, 73395.52) * mm, "end": v(44587.94, 73395.73) * mm});
            skArc(sketch, "E3876", {"start": v(44587.94, 73395.73) * mm, "mid": v(44587.94, 73395.76) * mm, "end": v(44587.93, 73395.8) * mm});
            skLineSegment(sketch, "E3877", {"start": v(44657.4, 73535.12) * mm, "end": v(44657.27, 73535.1) * mm});
            skLineSegment(sketch, "E3878", {"start": v(44657.27, 73535.1) * mm, "end": v(44657.16, 73535.1) * mm});
            skLineSegment(sketch, "E3879", {"start": v(44657.16, 73535.1) * mm, "end": v(44657.08, 73535.08) * mm});
            skLineSegment(sketch, "E3880", {"start": v(44657.08, 73535.08) * mm, "end": v(44657.02, 73535.07) * mm});
            skLineSegment(sketch, "E3881", {"start": v(44657.02, 73535.07) * mm, "end": v(44657, 73535.07) * mm});
            skLineSegment(sketch, "E3882", {"start": v(44657, 73535.07) * mm, "end": v(44656.95, 73535.06) * mm});
            skLineSegment(sketch, "E3883", {"start": v(44656.95, 73535.06) * mm, "end": v(44656.9, 73535.06) * mm});
            skLineSegment(sketch, "E3884", {"start": v(44656.9, 73535.06) * mm, "end": v(44656.85, 73535.06) * mm});
            skLineSegment(sketch, "E3885", {"start": v(44656.85, 73535.06) * mm, "end": v(44656.8, 73535.06) * mm});
            skLineSegment(sketch, "E3886", {"start": v(44656.8, 73535.06) * mm, "end": v(44656.75, 73535.06) * mm});
            skLineSegment(sketch, "E3887", {"start": v(44656.75, 73535.06) * mm, "end": v(44656.7, 73535.07) * mm});
            skLineSegment(sketch, "E3888", {"start": v(44656.7, 73535.07) * mm, "end": v(44656.64, 73535.07) * mm});
            skLineSegment(sketch, "E3889", {"start": v(44656.64, 73535.07) * mm, "end": v(44656.6, 73535.08) * mm});
            skLineSegment(sketch, "E3890", {"start": v(44656.6, 73535.08) * mm, "end": v(44656.54, 73535.1) * mm});
            skLineSegment(sketch, "E3891", {"start": v(44656.54, 73535.1) * mm, "end": v(44656.5, 73535.1) * mm});
            skLineSegment(sketch, "E3892", {"start": v(44656.5, 73535.1) * mm, "end": v(44656.45, 73535.12) * mm});
            skLineSegment(sketch, "E3893", {"start": v(44656.45, 73535.12) * mm, "end": v(44656.4, 73535.14) * mm});
            skLineSegment(sketch, "E3894", {"start": v(44656.4, 73535.14) * mm, "end": v(44656.35, 73535.16) * mm});
            skLineSegment(sketch, "E3895", {"start": v(44656.35, 73535.16) * mm, "end": v(44656.3, 73535.18) * mm});
            skLineSegment(sketch, "E3896", {"start": v(44656.3, 73535.18) * mm, "end": v(44656.26, 73535.2) * mm});
            skLineSegment(sketch, "E3897", {"start": v(44656.26, 73535.2) * mm, "end": v(44656.21, 73535.22) * mm});
            skLineSegment(sketch, "E3898", {"start": v(44656.21, 73535.22) * mm, "end": v(44656.17, 73535.25) * mm});
            skLineSegment(sketch, "E3899", {"start": v(44656.17, 73535.25) * mm, "end": v(44656.13, 73535.28) * mm});
            skLineSegment(sketch, "E3900", {"start": v(44656.13, 73535.28) * mm, "end": v(44656.09, 73535.3) * mm});
            skLineSegment(sketch, "E3901", {"start": v(44656.09, 73535.3) * mm, "end": v(44656.05, 73535.34) * mm});
            skLineSegment(sketch, "E3902", {"start": v(44656.05, 73535.34) * mm, "end": v(44656, 73535.37) * mm});
            skLineSegment(sketch, "E3903", {"start": v(44656, 73535.37) * mm, "end": v(44655.97, 73535.4) * mm});
            skLineSegment(sketch, "E3904", {"start": v(44655.97, 73535.4) * mm, "end": v(44655.93, 73535.44) * mm});
            skLineSegment(sketch, "E3905", {"start": v(44655.93, 73535.44) * mm, "end": v(44655.9, 73535.48) * mm});
            skLineSegment(sketch, "E3906", {"start": v(44655.9, 73535.48) * mm, "end": v(44655.86, 73535.51) * mm});
            skLineSegment(sketch, "E3907", {"start": v(44655.86, 73535.51) * mm, "end": v(44655.83, 73535.55) * mm});
            skLineSegment(sketch, "E3908", {"start": v(44655.83, 73535.55) * mm, "end": v(44655.8, 73535.6) * mm});
            skLineSegment(sketch, "E3909", {"start": v(44655.8, 73535.6) * mm, "end": v(44655.77, 73535.64) * mm});
            skLineSegment(sketch, "E3910", {"start": v(44655.77, 73535.64) * mm, "end": v(44655.75, 73535.68) * mm});
            skLineSegment(sketch, "E3911", {"start": v(44655.75, 73535.68) * mm, "end": v(44655.72, 73535.72) * mm});
            skLineSegment(sketch, "E3912", {"start": v(44655.72, 73535.72) * mm, "end": v(44655.7, 73535.77) * mm});
            skLineSegment(sketch, "E3913", {"start": v(44655.7, 73535.77) * mm, "end": v(44655.68, 73535.82) * mm});
            skLineSegment(sketch, "E3914", {"start": v(44655.68, 73535.82) * mm, "end": v(44655.66, 73535.86) * mm});
            skLineSegment(sketch, "E3915", {"start": v(44655.66, 73535.86) * mm, "end": v(44655.64, 73535.91) * mm});
            skLineSegment(sketch, "E3916", {"start": v(44655.64, 73535.91) * mm, "end": v(44655.62, 73535.96) * mm});
            skLineSegment(sketch, "E3917", {"start": v(44655.62, 73535.96) * mm, "end": v(44655.6, 73536) * mm});
            skLineSegment(sketch, "E3918", {"start": v(44655.6, 73536) * mm, "end": v(44655.6, 73536.06) * mm});
            skLineSegment(sketch, "E3919", {"start": v(44655.6, 73536.06) * mm, "end": v(44655.59, 73536.1) * mm});
            skLineSegment(sketch, "E3920", {"start": v(44655.59, 73536.1) * mm, "end": v(44655.58, 73536.16) * mm});
            skLineSegment(sketch, "E3921", {"start": v(44655.58, 73536.16) * mm, "end": v(44655.58, 73536.17) * mm});
            skLineSegment(sketch, "E3922", {"start": v(44655.58, 73536.17) * mm, "end": v(44655.56, 73536.28) * mm});
            skLineSegment(sketch, "E3923", {"start": v(44655.56, 73536.28) * mm, "end": v(44655.56, 73536.39) * mm});
            skLineSegment(sketch, "E3924", {"start": v(44655.56, 73536.39) * mm, "end": v(44655.55, 73536.5) * mm});
            skLineSegment(sketch, "E3925", {"start": v(44655.55, 73536.5) * mm, "end": v(44655.56, 73536.6) * mm});
            skLineSegment(sketch, "E3926", {"start": v(44655.56, 73536.6) * mm, "end": v(44655.56, 73536.71) * mm});
            skLineSegment(sketch, "E3927", {"start": v(44655.56, 73536.71) * mm, "end": v(44655.57, 73536.82) * mm});
            skLineSegment(sketch, "E3928", {"start": v(44655.57, 73536.82) * mm, "end": v(44655.59, 73536.93) * mm});
            skLineSegment(sketch, "E3929", {"start": v(44655.59, 73536.93) * mm, "end": v(44655.6, 73537.03) * mm});
            skLineSegment(sketch, "E3930", {"start": v(44655.6, 73537.03) * mm, "end": v(44655.62, 73537.1) * mm});
            skLineSegment(sketch, "E3931", {"start": v(44655.62, 73537.1) * mm, "end": v(44655.73, 73537.6) * mm});
            skLineSegment(sketch, "E3932", {"start": v(44655.73, 73537.6) * mm, "end": v(44655.81, 73538.1) * mm});
            skLineSegment(sketch, "E3933", {"start": v(44655.81, 73538.1) * mm, "end": v(44655.88, 73538.6) * mm});
            skLineSegment(sketch, "E3934", {"start": v(44655.88, 73538.6) * mm, "end": v(44655.93, 73539.1) * mm});
            skLineSegment(sketch, "E3935", {"start": v(44655.93, 73539.1) * mm, "end": v(44655.96, 73539.6) * mm});
            skLineSegment(sketch, "E3936", {"start": v(44655.96, 73539.6) * mm, "end": v(44655.97, 73540.11) * mm});
            skLineSegment(sketch, "E3937", {"start": v(44655.97, 73540.11) * mm, "end": v(44655.95, 73540.62) * mm});
            skLineSegment(sketch, "E3938", {"start": v(44655.95, 73540.62) * mm, "end": v(44655.92, 73541.12) * mm});
            skLineSegment(sketch, "E3939", {"start": v(44655.92, 73541.12) * mm, "end": v(44655.87, 73541.62) * mm});
            skLineSegment(sketch, "E3940", {"start": v(44655.87, 73541.62) * mm, "end": v(44655.8, 73542.13) * mm});
            skLineSegment(sketch, "E3941", {"start": v(44655.8, 73542.13) * mm, "end": v(44655.7, 73542.62) * mm});
            skLineSegment(sketch, "E3942", {"start": v(44655.7, 73542.62) * mm, "end": v(44655.59, 73543.12) * mm});
            skLineSegment(sketch, "E3943", {"start": v(44655.59, 73543.12) * mm, "end": v(44655.45, 73543.6) * mm});
            skLineSegment(sketch, "E3944", {"start": v(44655.45, 73543.6) * mm, "end": v(44655.3, 73544.09) * mm});
            skLineSegment(sketch, "E3945", {"start": v(44655.3, 73544.09) * mm, "end": v(44655.13, 73544.56) * mm});
            skLineSegment(sketch, "E3946", {"start": v(44655.13, 73544.56) * mm, "end": v(44654.94, 73545.03) * mm});
            skLineSegment(sketch, "E3947", {"start": v(44654.94, 73545.03) * mm, "end": v(44654.73, 73545.5) * mm});
            skLineSegment(sketch, "E3948", {"start": v(44654.73, 73545.5) * mm, "end": v(44654.5, 73545.95) * mm});
            skLineSegment(sketch, "E3949", {"start": v(44654.5, 73545.95) * mm, "end": v(44654.48, 73546) * mm});
            skLineSegment(sketch, "E3950", {"start": v(44654.48, 73546) * mm, "end": v(44654.42, 73546.11) * mm});
            skLineSegment(sketch, "E3951", {"start": v(44654.42, 73546.11) * mm, "end": v(44654.37, 73546.23) * mm});
            skLineSegment(sketch, "E3952", {"start": v(44654.37, 73546.23) * mm, "end": v(44654.32, 73546.35) * mm});
            skLineSegment(sketch, "E3953", {"start": v(44654.32, 73546.35) * mm, "end": v(44654.27, 73546.47) * mm});
            skLineSegment(sketch, "E3954", {"start": v(44654.27, 73546.47) * mm, "end": v(44654.23, 73546.6) * mm});
            skLineSegment(sketch, "E3955", {"start": v(44654.23, 73546.6) * mm, "end": v(44654.2, 73546.73) * mm});
            skLineSegment(sketch, "E3956", {"start": v(44654.2, 73546.73) * mm, "end": v(44654.17, 73546.85) * mm});
            skLineSegment(sketch, "E3957", {"start": v(44654.17, 73546.85) * mm, "end": v(44654.14, 73546.98) * mm});
            skLineSegment(sketch, "E3958", {"start": v(44654.14, 73546.98) * mm, "end": v(44654.12, 73547.11) * mm});
            skLineSegment(sketch, "E3959", {"start": v(44654.12, 73547.11) * mm, "end": v(44654.1, 73547.24) * mm});
            skLineSegment(sketch, "E3960", {"start": v(44654.1, 73547.24) * mm, "end": v(44654.1, 73547.37) * mm});
            skLineSegment(sketch, "E3961", {"start": v(44654.1, 73547.37) * mm, "end": v(44654.1, 73547.5) * mm});
            skLineSegment(sketch, "E3962", {"start": v(44654.1, 73547.5) * mm, "end": v(44654.1, 73547.64) * mm});
            skLineSegment(sketch, "E3963", {"start": v(44654.1, 73547.64) * mm, "end": v(44654.1, 73547.7) * mm});
            skLineSegment(sketch, "E3964", {"start": v(44654.1, 73547.7) * mm, "end": v(44653.2, 73548.4) * mm});
            skLineSegment(sketch, "E3965", {"start": v(44697.69, 73519.7) * mm, "end": v(44658.79, 73514.72) * mm});
            skLineSegment(sketch, "E3966", {"start": v(44658.79, 73514.72) * mm, "end": v(44656.4, 73514.4) * mm});
            skLineSegment(sketch, "E3967", {"start": v(44656.4, 73514.4) * mm, "end": v(44631.43, 73511.21) * mm});
            skLineSegment(sketch, "E3968", {"start": v(44631.43, 73511.21) * mm, "end": v(44628.41, 73510.83) * mm});
            skLineSegment(sketch, "E3969", {"start": v(44628.41, 73510.83) * mm, "end": v(44626.01, 73529.56) * mm});
            skLineSegment(sketch, "E3970", {"start": v(44626.01, 73529.56) * mm, "end": v(44629.03, 73529.95) * mm});
            skLineSegment(sketch, "E3971", {"start": v(44629.03, 73529.95) * mm, "end": v(44654, 73533.14) * mm});
            skLineSegment(sketch, "E3972", {"start": v(44654, 73533.14) * mm, "end": v(44656.4, 73533.45) * mm});
            skLineSegment(sketch, "E3973", {"start": v(44656.4, 73533.45) * mm, "end": v(44695.29, 73538.43) * mm});
            skLineSegment(sketch, "E3974", {"start": v(44693.27, 73553.53) * mm, "end": v(44693.25, 73553.53) * mm});
            skLineSegment(sketch, "E3975", {"start": v(44693.25, 73553.53) * mm, "end": v(44693.2, 73553.53) * mm});
            skLineSegment(sketch, "E3976", {"start": v(44693.2, 73553.53) * mm, "end": v(44693.13, 73553.52) * mm});
            skLineSegment(sketch, "E3977", {"start": v(44693.13, 73553.52) * mm, "end": v(44693.02, 73553.5) * mm});
            skLineSegment(sketch, "E3978", {"start": v(44693.02, 73553.5) * mm, "end": v(44692.88, 73553.48) * mm});
            skLineSegment(sketch, "E3979", {"start": v(44692.88, 73553.48) * mm, "end": v(44692.7, 73553.46) * mm});
            skLineSegment(sketch, "E3980", {"start": v(44692.7, 73553.46) * mm, "end": v(44692.5, 73553.44) * mm});
            skLineSegment(sketch, "E3981", {"start": v(44692.5, 73553.44) * mm, "end": v(44692.28, 73553.4) * mm});
            skLineSegment(sketch, "E3982", {"start": v(44692.28, 73553.4) * mm, "end": v(44692.01, 73553.37) * mm});
            skLineSegment(sketch, "E3983", {"start": v(44692.01, 73553.37) * mm, "end": v(44691.72, 73553.34) * mm});
            skLineSegment(sketch, "E3984", {"start": v(44691.72, 73553.34) * mm, "end": v(44691.4, 73553.3) * mm});
            skLineSegment(sketch, "E3985", {"start": v(44691.4, 73553.3) * mm, "end": v(44691.06, 73553.25) * mm});
            skLineSegment(sketch, "E3986", {"start": v(44691.06, 73553.25) * mm, "end": v(44690.68, 73553.2) * mm});
            skLineSegment(sketch, "E3987", {"start": v(44690.68, 73553.2) * mm, "end": v(44690.28, 73553.15) * mm});
            skLineSegment(sketch, "E3988", {"start": v(44690.28, 73553.15) * mm, "end": v(44689.85, 73553.1) * mm});
            skLineSegment(sketch, "E3989", {"start": v(44689.85, 73553.1) * mm, "end": v(44689.4, 73553.04) * mm});
            skLineSegment(sketch, "E3990", {"start": v(44689.4, 73553.04) * mm, "end": v(44688.91, 73552.98) * mm});
            skLineSegment(sketch, "E3991", {"start": v(44688.91, 73552.98) * mm, "end": v(44688.4, 73552.91) * mm});
            skLineSegment(sketch, "E3992", {"start": v(44697.84, 73519.72) * mm, "end": v(44695.45, 73538.45) * mm});
            skLineSegment(sketch, "E3993", {"start": v(44693.83, 73539.78) * mm, "end": v(44693.81, 73539.78) * mm});
            skLineSegment(sketch, "E3994", {"start": v(44693.81, 73539.78) * mm, "end": v(44693.77, 73539.78) * mm});
            skLineSegment(sketch, "E3995", {"start": v(44693.77, 73539.78) * mm, "end": v(44693.7, 73539.77) * mm});
            skLineSegment(sketch, "E3996", {"start": v(44693.7, 73539.77) * mm, "end": v(44693.6, 73539.75) * mm});
            skLineSegment(sketch, "E3997", {"start": v(44693.6, 73539.75) * mm, "end": v(44693.46, 73539.74) * mm});
            skLineSegment(sketch, "E3998", {"start": v(44656.4, 73533.45) * mm, "end": v(44658.79, 73514.72) * mm});
            skLineSegment(sketch, "E3999", {"start": v(44654, 73533.14) * mm, "end": v(44656.4, 73514.4) * mm});
            skLineSegment(sketch, "E4000", {"start": v(44659.2, 73549.17) * mm, "end": v(44655.61, 73548.71) * mm});
            skLineSegment(sketch, "E4001", {"start": v(44552.82, 73548.53) * mm, "end": v(44553.85, 73540.52) * mm});
            skLineSegment(sketch, "E4002", {"start": v(44608.4, 73547.5) * mm, "end": v(44607.37, 73555.52) * mm});
            skLineSegment(sketch, "E4003", {"start": v(44607.07, 73547.33) * mm, "end": v(44581.12, 73544.01) * mm});
            skLineSegment(sketch, "E4004", {"start": v(44581.12, 73544.01) * mm, "end": v(44555.18, 73540.7) * mm});
            skLineSegment(sketch, "E4005", {"start": v(44653.33, 73548.42) * mm, "end": v(44673.67, 73551.03) * mm});
            skLineSegment(sketch, "E4006", {"start": v(44673.67, 73551.03) * mm, "end": v(44693.22, 73553.53) * mm});
            skLineSegment(sketch, "E4007", {"start": v(44583.82, 73444.18) * mm, "end": v(44584.07, 73442.22) * mm});
            skLineSegment(sketch, "E4008", {"start": v(44584.07, 73442.22) * mm, "end": v(44584.32, 73440.26) * mm});
            skLineSegment(sketch, "E4009", {"start": v(44584.32, 73440.26) * mm, "end": v(44584.57, 73438.32) * mm});
            skLineSegment(sketch, "E4010", {"start": v(44584.57, 73438.32) * mm, "end": v(44584.82, 73436.39) * mm});
            skLineSegment(sketch, "E4011", {"start": v(44584.82, 73436.39) * mm, "end": v(44585.07, 73434.47) * mm});
            skLineSegment(sketch, "E4012", {"start": v(44585.07, 73434.47) * mm, "end": v(44585.3, 73432.56) * mm});
            skLineSegment(sketch, "E4013", {"start": v(44585.3, 73432.56) * mm, "end": v(44585.55, 73430.68) * mm});
            skLineSegment(sketch, "E4014", {"start": v(44585.55, 73430.68) * mm, "end": v(44585.79, 73428.82) * mm});
            skLineSegment(sketch, "E4015", {"start": v(44585.79, 73428.82) * mm, "end": v(44586.02, 73426.98) * mm});
            skLineSegment(sketch, "E4016", {"start": v(44586.02, 73426.98) * mm, "end": v(44586.25, 73425.18) * mm});
            skLineSegment(sketch, "E4017", {"start": v(44586.25, 73425.18) * mm, "end": v(44586.48, 73423.4) * mm});
            skLineSegment(sketch, "E4018", {"start": v(44586.48, 73423.4) * mm, "end": v(44586.7, 73421.67) * mm});
            skLineSegment(sketch, "E4019", {"start": v(44586.7, 73421.67) * mm, "end": v(44586.92, 73419.97) * mm});
            skLineSegment(sketch, "E4020", {"start": v(44586.92, 73419.97) * mm, "end": v(44587.13, 73418.3) * mm});
            skLineSegment(sketch, "E4021", {"start": v(44587.13, 73418.3) * mm, "end": v(44587.34, 73416.69) * mm});
            skLineSegment(sketch, "E4022", {"start": v(44587.34, 73416.69) * mm, "end": v(44587.54, 73415.11) * mm});
            skLineSegment(sketch, "E4023", {"start": v(44587.54, 73415.11) * mm, "end": v(44587.74, 73413.59) * mm});
            skLineSegment(sketch, "E4024", {"start": v(44587.74, 73413.59) * mm, "end": v(44587.93, 73412.11) * mm});
            skLineSegment(sketch, "E4025", {"start": v(44587.93, 73412.11) * mm, "end": v(44588.1, 73410.7) * mm});
            skLineSegment(sketch, "E4026", {"start": v(44588.1, 73410.7) * mm, "end": v(44588.28, 73409.33) * mm});
            skLineSegment(sketch, "E4027", {"start": v(44588.28, 73409.33) * mm, "end": v(44588.45, 73408.02) * mm});
            skLineSegment(sketch, "E4028", {"start": v(44588.45, 73408.02) * mm, "end": v(44588.61, 73406.77) * mm});
            skLineSegment(sketch, "E4029", {"start": v(44588.61, 73406.77) * mm, "end": v(44588.76, 73405.58) * mm});
            skLineSegment(sketch, "E4030", {"start": v(44588.76, 73405.58) * mm, "end": v(44588.9, 73404.45) * mm});
            skLineSegment(sketch, "E4031", {"start": v(44588.9, 73404.45) * mm, "end": v(44589.04, 73403.4) * mm});
            skLineSegment(sketch, "E4032", {"start": v(44589.04, 73403.4) * mm, "end": v(44589.17, 73402.4) * mm});
            skLineSegment(sketch, "E4033", {"start": v(44589.17, 73402.4) * mm, "end": v(44589.29, 73401.47) * mm});
            skLineSegment(sketch, "E4034", {"start": v(44589.29, 73401.47) * mm, "end": v(44589.4, 73400.61) * mm});
            skLineSegment(sketch, "E4035", {"start": v(44589.4, 73400.61) * mm, "end": v(44589.5, 73399.83) * mm});
            skLineSegment(sketch, "E4036", {"start": v(44589.5, 73399.83) * mm, "end": v(44589.6, 73399.12) * mm});
            skLineSegment(sketch, "E4037", {"start": v(44589.6, 73399.12) * mm, "end": v(44589.67, 73398.48) * mm});
            skLineSegment(sketch, "E4038", {"start": v(44589.67, 73398.48) * mm, "end": v(44589.74, 73397.91) * mm});
            skLineSegment(sketch, "E4039", {"start": v(44589.74, 73397.91) * mm, "end": v(44589.8, 73397.43) * mm});
            skLineSegment(sketch, "E4040", {"start": v(44589.8, 73397.43) * mm, "end": v(44589.86, 73397.01) * mm});
            skLineSegment(sketch, "E4041", {"start": v(44589.86, 73397.01) * mm, "end": v(44589.9, 73396.68) * mm});
            skLineSegment(sketch, "E4042", {"start": v(44589.9, 73396.68) * mm, "end": v(44589.94, 73396.42) * mm});
            skLineSegment(sketch, "E4043", {"start": v(44589.94, 73396.42) * mm, "end": v(44589.96, 73396.24) * mm});
            skLineSegment(sketch, "E4044", {"start": v(44589.96, 73396.24) * mm, "end": v(44589.97, 73396.14) * mm});
            skLineSegment(sketch, "E4045", {"start": v(44589.97, 73396.14) * mm, "end": v(44589.98, 73396.11) * mm});
            skLineSegment(sketch, "E4046", {"start": v(44609.81, 73398.65) * mm, "end": v(44609.8, 73398.69) * mm});
            skLineSegment(sketch, "E4047", {"start": v(44609.8, 73398.69) * mm, "end": v(44609.8, 73398.8) * mm});
            skLineSegment(sketch, "E4048", {"start": v(44609.8, 73398.8) * mm, "end": v(44609.77, 73399) * mm});
            skLineSegment(sketch, "E4049", {"start": v(44609.77, 73399) * mm, "end": v(44609.73, 73399.28) * mm});
            skLineSegment(sketch, "E4050", {"start": v(44609.73, 73399.28) * mm, "end": v(44609.69, 73399.63) * mm});
            skLineSegment(sketch, "E4051", {"start": v(44609.69, 73399.63) * mm, "end": v(44609.63, 73400.05) * mm});
            skLineSegment(sketch, "E4052", {"start": v(44609.63, 73400.05) * mm, "end": v(44609.57, 73400.56) * mm});
            skLineSegment(sketch, "E4053", {"start": v(44609.57, 73400.56) * mm, "end": v(44609.5, 73401.14) * mm});
            skLineSegment(sketch, "E4054", {"start": v(44609.5, 73401.14) * mm, "end": v(44609.41, 73401.79) * mm});
            skLineSegment(sketch, "E4055", {"start": v(44609.41, 73401.79) * mm, "end": v(44609.32, 73402.52) * mm});
            skLineSegment(sketch, "E4056", {"start": v(44609.32, 73402.52) * mm, "end": v(44609.22, 73403.32) * mm});
            skLineSegment(sketch, "E4057", {"start": v(44609.22, 73403.32) * mm, "end": v(44609.1, 73404.18) * mm});
            skLineSegment(sketch, "E4058", {"start": v(44609.1, 73404.18) * mm, "end": v(44608.98, 73405.12) * mm});
            skLineSegment(sketch, "E4059", {"start": v(44608.98, 73405.12) * mm, "end": v(44608.86, 73406.13) * mm});
            skLineSegment(sketch, "E4060", {"start": v(44608.86, 73406.13) * mm, "end": v(44608.72, 73407.2) * mm});
            skLineSegment(sketch, "E4061", {"start": v(44608.72, 73407.2) * mm, "end": v(44608.57, 73408.34) * mm});
            skLineSegment(sketch, "E4062", {"start": v(44608.57, 73408.34) * mm, "end": v(44608.42, 73409.54) * mm});
            skLineSegment(sketch, "E4063", {"start": v(44608.42, 73409.54) * mm, "end": v(44608.26, 73410.8) * mm});
            skLineSegment(sketch, "E4064", {"start": v(44608.26, 73410.8) * mm, "end": v(44608.09, 73412.13) * mm});
            skLineSegment(sketch, "E4065", {"start": v(44608.09, 73412.13) * mm, "end": v(44607.91, 73413.5) * mm});
            skLineSegment(sketch, "E4066", {"start": v(44607.91, 73413.5) * mm, "end": v(44607.73, 73414.94) * mm});
            skLineSegment(sketch, "E4067", {"start": v(44607.73, 73414.94) * mm, "end": v(44607.54, 73416.42) * mm});
            skLineSegment(sketch, "E4068", {"start": v(44607.54, 73416.42) * mm, "end": v(44607.34, 73417.95) * mm});
            skLineSegment(sketch, "E4069", {"start": v(44607.34, 73417.95) * mm, "end": v(44607.14, 73419.54) * mm});
            skLineSegment(sketch, "E4070", {"start": v(44607.14, 73419.54) * mm, "end": v(44606.93, 73421.16) * mm});
            skLineSegment(sketch, "E4071", {"start": v(44606.93, 73421.16) * mm, "end": v(44606.72, 73422.83) * mm});
            skLineSegment(sketch, "E4072", {"start": v(44606.72, 73422.83) * mm, "end": v(44606.5, 73424.54) * mm});
            skLineSegment(sketch, "E4073", {"start": v(44606.5, 73424.54) * mm, "end": v(44606.28, 73426.29) * mm});
            skLineSegment(sketch, "E4074", {"start": v(44606.28, 73426.29) * mm, "end": v(44606.05, 73428.07) * mm});
            skLineSegment(sketch, "E4075", {"start": v(44606.05, 73428.07) * mm, "end": v(44605.82, 73429.88) * mm});
            skLineSegment(sketch, "E4076", {"start": v(44605.82, 73429.88) * mm, "end": v(44605.58, 73431.72) * mm});
            skLineSegment(sketch, "E4077", {"start": v(44605.58, 73431.72) * mm, "end": v(44605.34, 73433.58) * mm});
            skLineSegment(sketch, "E4078", {"start": v(44605.34, 73433.58) * mm, "end": v(44605.1, 73435.47) * mm});
            skLineSegment(sketch, "E4079", {"start": v(44605.1, 73435.47) * mm, "end": v(44604.86, 73437.38) * mm});
            skLineSegment(sketch, "E4080", {"start": v(44604.86, 73437.38) * mm, "end": v(44604.6, 73439.3) * mm});
            skLineSegment(sketch, "E4081", {"start": v(44604.6, 73439.3) * mm, "end": v(44604.36, 73441.24) * mm});
            skLineSegment(sketch, "E4082", {"start": v(44604.36, 73441.24) * mm, "end": v(44604.11, 73443.18) * mm});
            skLineSegment(sketch, "E4083", {"start": v(44604.11, 73443.18) * mm, "end": v(44603.86, 73445.14) * mm});
            skLineSegment(sketch, "E4084", {"start": v(44603.86, 73445.14) * mm, "end": v(44603.66, 73446.71) * mm});
            skLineSegment(sketch, "E4085", {"start": v(44589.35, 73395.97) * mm, "end": v(44589.36, 73395.92) * mm});
            skLineSegment(sketch, "E4086", {"start": v(44610.46, 73398.62) * mm, "end": v(44610.45, 73398.67) * mm});
            skLineSegment(sketch, "E4087", {"start": v(44657, 73535.07) * mm, "end": v(44657.01, 73535.07) * mm});
            skLineSegment(sketch, "E4088", {"start": v(44657.01, 73535.07) * mm, "end": v(44657.06, 73535.08) * mm});
            skLineSegment(sketch, "E4089", {"start": v(44657.06, 73535.08) * mm, "end": v(44657.13, 73535.09) * mm});
            skLineSegment(sketch, "E4090", {"start": v(44657.13, 73535.09) * mm, "end": v(44657.23, 73535.1) * mm});
            skLineSegment(sketch, "E4091", {"start": v(44657.23, 73535.1) * mm, "end": v(44657.37, 73535.12) * mm});
            skLineSegment(sketch, "E4092", {"start": v(44657.37, 73535.12) * mm, "end": v(44657.53, 73535.14) * mm});
            skLineSegment(sketch, "E4093", {"start": v(44657.53, 73535.14) * mm, "end": v(44657.72, 73535.16) * mm});
            skLineSegment(sketch, "E4094", {"start": v(44657.72, 73535.16) * mm, "end": v(44657.93, 73535.2) * mm});
            skLineSegment(sketch, "E4095", {"start": v(44657.93, 73535.2) * mm, "end": v(44658.18, 73535.22) * mm});
            skLineSegment(sketch, "E4096", {"start": v(44658.18, 73535.22) * mm, "end": v(44658.45, 73535.26) * mm});
            skLineSegment(sketch, "E4097", {"start": v(44658.45, 73535.26) * mm, "end": v(44658.75, 73535.3) * mm});
            skLineSegment(sketch, "E4098", {"start": v(44658.75, 73535.3) * mm, "end": v(44659.08, 73535.34) * mm});
            skLineSegment(sketch, "E4099", {"start": v(44659.08, 73535.34) * mm, "end": v(44659.43, 73535.38) * mm});
            skLineSegment(sketch, "E4100", {"start": v(44659.43, 73535.38) * mm, "end": v(44659.81, 73535.43) * mm});
            skLineSegment(sketch, "E4101", {"start": v(44659.81, 73535.43) * mm, "end": v(44660.22, 73535.48) * mm});
            skLineSegment(sketch, "E4102", {"start": v(44660.22, 73535.48) * mm, "end": v(44660.64, 73535.54) * mm});
            skLineSegment(sketch, "E4103", {"start": v(44660.64, 73535.54) * mm, "end": v(44661.1, 73535.6) * mm});
            skLineSegment(sketch, "E4104", {"start": v(44661.1, 73535.6) * mm, "end": v(44661.57, 73535.66) * mm});
            skLineSegment(sketch, "E4105", {"start": v(44661.57, 73535.66) * mm, "end": v(44662.07, 73535.72) * mm});
            skLineSegment(sketch, "E4106", {"start": v(44662.07, 73535.72) * mm, "end": v(44662.58, 73535.79) * mm});
            skLineSegment(sketch, "E4107", {"start": v(44662.58, 73535.79) * mm, "end": v(44663.12, 73535.85) * mm});
            skLineSegment(sketch, "E4108", {"start": v(44663.12, 73535.85) * mm, "end": v(44663.68, 73535.93) * mm});
            skLineSegment(sketch, "E4109", {"start": v(44663.68, 73535.93) * mm, "end": v(44664.26, 73536) * mm});
            skLineSegment(sketch, "E4110", {"start": v(44664.26, 73536) * mm, "end": v(44664.85, 73536.08) * mm});
            skLineSegment(sketch, "E4111", {"start": v(44664.85, 73536.08) * mm, "end": v(44665.46, 73536.15) * mm});
            skLineSegment(sketch, "E4112", {"start": v(44665.46, 73536.15) * mm, "end": v(44666.1, 73536.23) * mm});
            skLineSegment(sketch, "E4113", {"start": v(44666.1, 73536.23) * mm, "end": v(44666.73, 73536.32) * mm});
            skLineSegment(sketch, "E4114", {"start": v(44666.73, 73536.32) * mm, "end": v(44667.4, 73536.4) * mm});
            skLineSegment(sketch, "E4115", {"start": v(44667.4, 73536.4) * mm, "end": v(44668.06, 73536.49) * mm});
            skLineSegment(sketch, "E4116", {"start": v(44668.06, 73536.49) * mm, "end": v(44668.74, 73536.57) * mm});
            skLineSegment(sketch, "E4117", {"start": v(44668.74, 73536.57) * mm, "end": v(44669.43, 73536.66) * mm});
            skLineSegment(sketch, "E4118", {"start": v(44669.43, 73536.66) * mm, "end": v(44670.13, 73536.75) * mm});
            skLineSegment(sketch, "E4119", {"start": v(44670.13, 73536.75) * mm, "end": v(44670.84, 73536.84) * mm});
            skLineSegment(sketch, "E4120", {"start": v(44670.84, 73536.84) * mm, "end": v(44671.56, 73536.93) * mm});
            skLineSegment(sketch, "E4121", {"start": v(44671.56, 73536.93) * mm, "end": v(44672.28, 73537.03) * mm});
            skLineSegment(sketch, "E4122", {"start": v(44672.28, 73537.03) * mm, "end": v(44673.01, 73537.12) * mm});
            skLineSegment(sketch, "E4123", {"start": v(44673.01, 73537.12) * mm, "end": v(44673.74, 73537.21) * mm});
            skLineSegment(sketch, "E4124", {"start": v(44673.74, 73537.21) * mm, "end": v(44674.48, 73537.3) * mm});
            skLineSegment(sketch, "E4125", {"start": v(44674.48, 73537.3) * mm, "end": v(44675.21, 73537.4) * mm});
            skLineSegment(sketch, "E4126", {"start": v(44675.21, 73537.4) * mm, "end": v(44675.41, 73537.43) * mm});
            skLineSegment(sketch, "E4127", {"start": v(44675.41, 73537.43) * mm, "end": v(44676.15, 73537.52) * mm});
            skLineSegment(sketch, "E4128", {"start": v(44676.15, 73537.52) * mm, "end": v(44676.88, 73537.62) * mm});
            skLineSegment(sketch, "E4129", {"start": v(44676.88, 73537.62) * mm, "end": v(44677.62, 73537.7) * mm});
            skLineSegment(sketch, "E4130", {"start": v(44677.62, 73537.7) * mm, "end": v(44678.35, 73537.8) * mm});
            skLineSegment(sketch, "E4131", {"start": v(44678.35, 73537.8) * mm, "end": v(44679.07, 73537.9) * mm});
            skLineSegment(sketch, "E4132", {"start": v(44679.07, 73537.9) * mm, "end": v(44679.79, 73537.99) * mm});
            skLineSegment(sketch, "E4133", {"start": v(44679.79, 73537.99) * mm, "end": v(44680.5, 73538.08) * mm});
            skLineSegment(sketch, "E4134", {"start": v(44680.5, 73538.08) * mm, "end": v(44681.2, 73538.17) * mm});
            skLineSegment(sketch, "E4135", {"start": v(44681.2, 73538.17) * mm, "end": v(44681.9, 73538.26) * mm});
            skLineSegment(sketch, "E4136", {"start": v(44681.9, 73538.26) * mm, "end": v(44682.58, 73538.35) * mm});
            skLineSegment(sketch, "E4137", {"start": v(44682.58, 73538.35) * mm, "end": v(44683.26, 73538.43) * mm});
            skLineSegment(sketch, "E4138", {"start": v(44683.26, 73538.43) * mm, "end": v(44683.92, 73538.52) * mm});
            skLineSegment(sketch, "E4139", {"start": v(44683.92, 73538.52) * mm, "end": v(44684.56, 73538.6) * mm});
            skLineSegment(sketch, "E4140", {"start": v(44684.56, 73538.6) * mm, "end": v(44685.2, 73538.68) * mm});
            skLineSegment(sketch, "E4141", {"start": v(44685.2, 73538.68) * mm, "end": v(44685.8, 73538.76) * mm});
            skLineSegment(sketch, "E4142", {"start": v(44685.8, 73538.76) * mm, "end": v(44686.4, 73538.84) * mm});
            skLineSegment(sketch, "E4143", {"start": v(44686.4, 73538.84) * mm, "end": v(44687, 73538.9) * mm});
            skLineSegment(sketch, "E4144", {"start": v(44687, 73538.9) * mm, "end": v(44687.55, 73538.98) * mm});
            skLineSegment(sketch, "E4145", {"start": v(44687.55, 73538.98) * mm, "end": v(44688.1, 73539.05) * mm});
            skLineSegment(sketch, "E4146", {"start": v(44688.1, 73539.05) * mm, "end": v(44688.62, 73539.12) * mm});
            skLineSegment(sketch, "E4147", {"start": v(44688.62, 73539.12) * mm, "end": v(44689.12, 73539.18) * mm});
            skLineSegment(sketch, "E4148", {"start": v(44689.12, 73539.18) * mm, "end": v(44689.6, 73539.24) * mm});
            skLineSegment(sketch, "E4149", {"start": v(44689.6, 73539.24) * mm, "end": v(44690.06, 73539.3) * mm});
            skLineSegment(sketch, "E4150", {"start": v(44690.06, 73539.3) * mm, "end": v(44690.5, 73539.36) * mm});
            skLineSegment(sketch, "E4151", {"start": v(44690.5, 73539.36) * mm, "end": v(44690.9, 73539.41) * mm});
            skLineSegment(sketch, "E4152", {"start": v(44690.9, 73539.41) * mm, "end": v(44691.3, 73539.46) * mm});
            skLineSegment(sketch, "E4153", {"start": v(44691.3, 73539.46) * mm, "end": v(44691.65, 73539.5) * mm});
            skLineSegment(sketch, "E4154", {"start": v(44691.65, 73539.5) * mm, "end": v(44691.99, 73539.55) * mm});
            skLineSegment(sketch, "E4155", {"start": v(44691.99, 73539.55) * mm, "end": v(44692.3, 73539.59) * mm});
            skLineSegment(sketch, "E4156", {"start": v(44692.3, 73539.59) * mm, "end": v(44692.57, 73539.62) * mm});
            skLineSegment(sketch, "E4157", {"start": v(44692.57, 73539.62) * mm, "end": v(44692.83, 73539.66) * mm});
            skLineSegment(sketch, "E4158", {"start": v(44692.83, 73539.66) * mm, "end": v(44693.05, 73539.69) * mm});
            skLineSegment(sketch, "E4159", {"start": v(44693.05, 73539.69) * mm, "end": v(44693.25, 73539.71) * mm});
            skLineSegment(sketch, "E4160", {"start": v(44693.25, 73539.71) * mm, "end": v(44693.42, 73539.73) * mm});
            skLineSegment(sketch, "E4161", {"start": v(44693.42, 73539.73) * mm, "end": v(44693.56, 73539.75) * mm});
            skLineSegment(sketch, "E4162", {"start": v(44693.56, 73539.75) * mm, "end": v(44693.67, 73539.76) * mm});
            skLineSegment(sketch, "E4163", {"start": v(44693.67, 73539.76) * mm, "end": v(44693.75, 73539.77) * mm});
            skLineSegment(sketch, "E4164", {"start": v(44693.75, 73539.77) * mm, "end": v(44693.8, 73539.78) * mm});
            skLineSegment(sketch, "E4165", {"start": v(44693.8, 73539.78) * mm, "end": v(44693.83, 73539.78) * mm});
            skLineSegment(sketch, "E4166", {"start": v(44693.83, 73539.78) * mm, "end": v(44693.84, 73539.79) * mm});
            skLineSegment(sketch, "E4167", {"start": v(44693.84, 73539.79) * mm, "end": v(44693.89, 73539.8) * mm});
            skLineSegment(sketch, "E4168", {"start": v(44693.89, 73539.8) * mm, "end": v(44693.94, 73539.8) * mm});
            skLineSegment(sketch, "E4169", {"start": v(44693.94, 73539.8) * mm, "end": v(44693.99, 73539.82) * mm});
            skLineSegment(sketch, "E4170", {"start": v(44693.99, 73539.82) * mm, "end": v(44694.04, 73539.83) * mm});
            skLineSegment(sketch, "E4171", {"start": v(44694.04, 73539.83) * mm, "end": v(44694.09, 73539.85) * mm});
            skLineSegment(sketch, "E4172", {"start": v(44694.09, 73539.85) * mm, "end": v(44694.13, 73539.86) * mm});
            skLineSegment(sketch, "E4173", {"start": v(44694.13, 73539.86) * mm, "end": v(44694.18, 73539.88) * mm});
            skLineSegment(sketch, "E4174", {"start": v(44694.18, 73539.88) * mm, "end": v(44694.23, 73539.9) * mm});
            skLineSegment(sketch, "E4175", {"start": v(44694.23, 73539.9) * mm, "end": v(44694.27, 73539.93) * mm});
            skLineSegment(sketch, "E4176", {"start": v(44694.27, 73539.93) * mm, "end": v(44694.32, 73539.95) * mm});
            skLineSegment(sketch, "E4177", {"start": v(44694.32, 73539.95) * mm, "end": v(44694.36, 73539.98) * mm});
            skLineSegment(sketch, "E4178", {"start": v(44694.36, 73539.98) * mm, "end": v(44694.4, 73540) * mm});
            skLineSegment(sketch, "E4179", {"start": v(44694.4, 73540) * mm, "end": v(44694.44, 73540.04) * mm});
            skLineSegment(sketch, "E4180", {"start": v(44694.44, 73540.04) * mm, "end": v(44694.48, 73540.07) * mm});
            skLineSegment(sketch, "E4181", {"start": v(44694.48, 73540.07) * mm, "end": v(44694.52, 73540.1) * mm});
            skLineSegment(sketch, "E4182", {"start": v(44694.52, 73540.1) * mm, "end": v(44694.56, 73540.14) * mm});
            skLineSegment(sketch, "E4183", {"start": v(44694.56, 73540.14) * mm, "end": v(44694.6, 73540.18) * mm});
            skLineSegment(sketch, "E4184", {"start": v(44694.6, 73540.18) * mm, "end": v(44694.63, 73540.21) * mm});
            skLineSegment(sketch, "E4185", {"start": v(44694.63, 73540.21) * mm, "end": v(44694.66, 73540.25) * mm});
            skLineSegment(sketch, "E4186", {"start": v(44694.66, 73540.25) * mm, "end": v(44694.7, 73540.3) * mm});
            skLineSegment(sketch, "E4187", {"start": v(44694.7, 73540.3) * mm, "end": v(44694.72, 73540.34) * mm});
            skLineSegment(sketch, "E4188", {"start": v(44694.72, 73540.34) * mm, "end": v(44694.75, 73540.38) * mm});
            skLineSegment(sketch, "E4189", {"start": v(44694.75, 73540.38) * mm, "end": v(44694.77, 73540.42) * mm});
            skLineSegment(sketch, "E4190", {"start": v(44694.77, 73540.42) * mm, "end": v(44694.8, 73540.47) * mm});
            skLineSegment(sketch, "E4191", {"start": v(44694.8, 73540.47) * mm, "end": v(44694.82, 73540.51) * mm});
            skLineSegment(sketch, "E4192", {"start": v(44694.82, 73540.51) * mm, "end": v(44694.84, 73540.56) * mm});
            skLineSegment(sketch, "E4193", {"start": v(44694.84, 73540.56) * mm, "end": v(44694.86, 73540.6) * mm});
            skLineSegment(sketch, "E4194", {"start": v(44694.86, 73540.6) * mm, "end": v(44694.88, 73540.66) * mm});
            skLineSegment(sketch, "E4195", {"start": v(44694.88, 73540.66) * mm, "end": v(44694.89, 73540.7) * mm});
            skLineSegment(sketch, "E4196", {"start": v(44694.89, 73540.7) * mm, "end": v(44694.9, 73540.75) * mm});
            skLineSegment(sketch, "E4197", {"start": v(44694.9, 73540.75) * mm, "end": v(44694.91, 73540.8) * mm});
            skLineSegment(sketch, "E4198", {"start": v(44694.91, 73540.8) * mm, "end": v(44694.92, 73540.85) * mm});
            skLineSegment(sketch, "E4199", {"start": v(44694.92, 73540.85) * mm, "end": v(44694.93, 73540.9) * mm});
            skLineSegment(sketch, "E4200", {"start": v(44694.93, 73540.9) * mm, "end": v(44694.93, 73540.95) * mm});
            skLineSegment(sketch, "E4201", {"start": v(44694.93, 73540.95) * mm, "end": v(44694.94, 73541) * mm});
            skLineSegment(sketch, "E4202", {"start": v(44694.94, 73541) * mm, "end": v(44694.94, 73541.06) * mm});
            skLineSegment(sketch, "E4203", {"start": v(44694.94, 73541.06) * mm, "end": v(44694.94, 73541.1) * mm});
            skLineSegment(sketch, "E4204", {"start": v(44694.94, 73541.1) * mm, "end": v(44694.93, 73541.16) * mm});
            skLineSegment(sketch, "E4205", {"start": v(44694.93, 73541.16) * mm, "end": v(44694.93, 73541.2) * mm});
            skLineSegment(sketch, "E4206", {"start": v(44694.93, 73541.2) * mm, "end": v(44694.92, 73541.28) * mm});
            skLineSegment(sketch, "E4207", {"start": v(44694.92, 73541.28) * mm, "end": v(44694.9, 73541.38) * mm});
            skLineSegment(sketch, "E4208", {"start": v(44694.9, 73541.38) * mm, "end": v(44694.88, 73541.49) * mm});
            skLineSegment(sketch, "E4209", {"start": v(44694.88, 73541.49) * mm, "end": v(44694.85, 73541.6) * mm});
            skLineSegment(sketch, "E4210", {"start": v(44694.85, 73541.6) * mm, "end": v(44694.82, 73541.7) * mm});
            skLineSegment(sketch, "E4211", {"start": v(44694.82, 73541.7) * mm, "end": v(44694.78, 73541.8) * mm});
            skLineSegment(sketch, "E4212", {"start": v(44694.78, 73541.8) * mm, "end": v(44694.74, 73541.9) * mm});
            skLineSegment(sketch, "E4213", {"start": v(44694.74, 73541.9) * mm, "end": v(44694.7, 73542) * mm});
            skLineSegment(sketch, "E4214", {"start": v(44694.7, 73542) * mm, "end": v(44694.65, 73542.1) * mm});
            skLineSegment(sketch, "E4215", {"start": v(44611.9, 73396.12) * mm, "end": v(44611.92, 73396.28) * mm});
            skLineSegment(sketch, "E4216", {"start": v(44611.92, 73396.28) * mm, "end": v(44611.96, 73396.76) * mm});
            skLineSegment(sketch, "E4217", {"start": v(44611.96, 73396.76) * mm, "end": v(44611.98, 73397.25) * mm});
            skLineSegment(sketch, "E4218", {"start": v(44611.98, 73397.25) * mm, "end": v(44611.98, 73397.73) * mm});
            skLineSegment(sketch, "E4219", {"start": v(44611.98, 73397.73) * mm, "end": v(44611.96, 73398.22) * mm});
            skLineSegment(sketch, "E4220", {"start": v(44611.96, 73398.22) * mm, "end": v(44611.92, 73398.7) * mm});
            skLineSegment(sketch, "E4221", {"start": v(44611.92, 73398.7) * mm, "end": v(44611.86, 73399.18) * mm});
            skLineSegment(sketch, "E4222", {"start": v(44611.86, 73399.18) * mm, "end": v(44611.79, 73399.66) * mm});
            skLineSegment(sketch, "E4223", {"start": v(44611.79, 73399.66) * mm, "end": v(44611.7, 73400.13) * mm});
            skLineSegment(sketch, "E4224", {"start": v(44611.7, 73400.13) * mm, "end": v(44611.58, 73400.6) * mm});
            skLineSegment(sketch, "E4225", {"start": v(44611.58, 73400.6) * mm, "end": v(44611.44, 73401.07) * mm});
            skLineSegment(sketch, "E4226", {"start": v(44611.44, 73401.07) * mm, "end": v(44611.3, 73401.53) * mm});
            skLineSegment(sketch, "E4227", {"start": v(44611.3, 73401.53) * mm, "end": v(44611.12, 73401.98) * mm});
            skLineSegment(sketch, "E4228", {"start": v(44611.12, 73401.98) * mm, "end": v(44610.93, 73402.42) * mm});
            skLineSegment(sketch, "E4229", {"start": v(44610.93, 73402.42) * mm, "end": v(44610.73, 73402.86) * mm});
            skLineSegment(sketch, "E4230", {"start": v(44610.73, 73402.86) * mm, "end": v(44610.5, 73403.3) * mm});
            skLineSegment(sketch, "E4231", {"start": v(44610.5, 73403.3) * mm, "end": v(44610.26, 73403.71) * mm});
            skLineSegment(sketch, "E4232", {"start": v(44610.26, 73403.71) * mm, "end": v(44610, 73404.12) * mm});
            skLineSegment(sketch, "E4233", {"start": v(44610, 73404.12) * mm, "end": v(44609.73, 73404.52) * mm});
            skLineSegment(sketch, "E4234", {"start": v(44609.73, 73404.52) * mm, "end": v(44609.44, 73404.9) * mm});
            skLineSegment(sketch, "E4235", {"start": v(44609.44, 73404.9) * mm, "end": v(44609.14, 73405.29) * mm});
            skLineSegment(sketch, "E4236", {"start": v(44609.14, 73405.29) * mm, "end": v(44608.82, 73405.65) * mm});
            skLineSegment(sketch, "E4237", {"start": v(44659.86, 73548.44) * mm, "end": v(44673.77, 73550.23) * mm});
            skLineSegment(sketch, "E4238", {"start": v(44673.77, 73550.23) * mm, "end": v(44687.69, 73552) * mm});
            skLineSegment(sketch, "E4239", {"start": v(44694.18, 73538.29) * mm, "end": v(44693.99, 73539.8) * mm});
            skLineSegment(sketch, "E4240", {"start": v(44693.99, 73539.8) * mm, "end": v(44656.84, 73535.05) * mm});
            skLineSegment(sketch, "E4241", {"start": v(44656.84, 73535.05) * mm, "end": v(44657.03, 73533.53) * mm});
            skArc(sketch, "E4242", {"start": v(44611.6, 73394.38) * mm, "mid": v(44611.62, 73394.44) * mm, "end": v(44611.63, 73394.49) * mm});
            skLineSegment(sketch, "E4243", {"start": v(44611.63, 73394.49) * mm, "end": v(44611.69, 73394.72) * mm});
            skArc(sketch, "E4244", {"start": v(44611.69, 73394.72) * mm, "mid": v(44611.75, 73395) * mm, "end": v(44611.8, 73395.3) * mm});
            skLineSegment(sketch, "E4245", {"start": v(44611.8, 73395.3) * mm, "end": v(44611.86, 73395.7) * mm});
            skArc(sketch, "E4246", {"start": v(44611.86, 73395.7) * mm, "mid": v(44611.94, 73396.4) * mm, "end": v(44611.97, 73397.09) * mm});
            skLineSegment(sketch, "E4247", {"start": v(44611.97, 73397.09) * mm, "end": v(44611.97, 73397.25) * mm});
            skArc(sketch, "E4248", {"start": v(44611.97, 73397.25) * mm, "mid": v(44611.95, 73398) * mm, "end": v(44611.88, 73398.75) * mm});
            skArc(sketch, "E4249", {"start": v(44611.88, 73398.75) * mm, "mid": v(44611.88, 73398.8) * mm, "end": v(44611.87, 73398.85) * mm});
            skLineSegment(sketch, "E4250", {"start": v(44655.62, 73537.1) * mm, "end": v(44675.14, 73539.6) * mm});
            skLineSegment(sketch, "E4251", {"start": v(44675.14, 73539.6) * mm, "end": v(44694.65, 73542.1) * mm});
            skLineSegment(sketch, "E4252", {"start": v(44694.65, 73542.1) * mm, "end": v(44694.63, 73542.14) * mm});
            skLineSegment(sketch, "E4253", {"start": v(44694.63, 73542.14) * mm, "end": v(44694.4, 73542.6) * mm});
            skLineSegment(sketch, "E4254", {"start": v(44694.4, 73542.6) * mm, "end": v(44694.2, 73543.06) * mm});
            skLineSegment(sketch, "E4255", {"start": v(44694.2, 73543.06) * mm, "end": v(44694, 73543.53) * mm});
            skLineSegment(sketch, "E4256", {"start": v(44694, 73543.53) * mm, "end": v(44693.83, 73544) * mm});
            skLineSegment(sketch, "E4257", {"start": v(44693.83, 73544) * mm, "end": v(44693.68, 73544.49) * mm});
            skLineSegment(sketch, "E4258", {"start": v(44693.68, 73544.49) * mm, "end": v(44693.54, 73544.97) * mm});
            skLineSegment(sketch, "E4259", {"start": v(44693.54, 73544.97) * mm, "end": v(44693.43, 73545.47) * mm});
            skLineSegment(sketch, "E4260", {"start": v(44693.43, 73545.47) * mm, "end": v(44693.34, 73545.96) * mm});
            skLineSegment(sketch, "E4261", {"start": v(44693.34, 73545.96) * mm, "end": v(44693.26, 73546.47) * mm});
            skLineSegment(sketch, "E4262", {"start": v(44693.26, 73546.47) * mm, "end": v(44693.21, 73546.97) * mm});
            skLineSegment(sketch, "E4263", {"start": v(44693.21, 73546.97) * mm, "end": v(44693.18, 73547.47) * mm});
            skLineSegment(sketch, "E4264", {"start": v(44693.18, 73547.47) * mm, "end": v(44693.17, 73547.98) * mm});
            skLineSegment(sketch, "E4265", {"start": v(44693.17, 73547.98) * mm, "end": v(44693.17, 73548.49) * mm});
            skLineSegment(sketch, "E4266", {"start": v(44693.17, 73548.49) * mm, "end": v(44693.2, 73549) * mm});
            skLineSegment(sketch, "E4267", {"start": v(44693.2, 73549) * mm, "end": v(44693.25, 73549.5) * mm});
            skLineSegment(sketch, "E4268", {"start": v(44693.25, 73549.5) * mm, "end": v(44693.32, 73550) * mm});
            skLineSegment(sketch, "E4269", {"start": v(44693.32, 73550) * mm, "end": v(44693.4, 73550.5) * mm});
            skLineSegment(sketch, "E4270", {"start": v(44693.4, 73550.5) * mm, "end": v(44693.51, 73551) * mm});
            skLineSegment(sketch, "E4271", {"start": v(44693.51, 73551) * mm, "end": v(44693.53, 73551.06) * mm});
            skLineSegment(sketch, "E4272", {"start": v(44693.53, 73551.06) * mm, "end": v(44693.55, 73551.19) * mm});
            skLineSegment(sketch, "E4273", {"start": v(44693.55, 73551.19) * mm, "end": v(44693.57, 73551.32) * mm});
            skLineSegment(sketch, "E4274", {"start": v(44693.57, 73551.32) * mm, "end": v(44693.59, 73551.45) * mm});
            skLineSegment(sketch, "E4275", {"start": v(44693.59, 73551.45) * mm, "end": v(44693.6, 73551.58) * mm});
            skLineSegment(sketch, "E4276", {"start": v(44693.6, 73551.58) * mm, "end": v(44693.6, 73551.71) * mm});
            skLineSegment(sketch, "E4277", {"start": v(44693.6, 73551.71) * mm, "end": v(44693.6, 73551.84) * mm});
            skLineSegment(sketch, "E4278", {"start": v(44693.6, 73551.84) * mm, "end": v(44693.6, 73551.97) * mm});
            skLineSegment(sketch, "E4279", {"start": v(44693.6, 73551.97) * mm, "end": v(44693.58, 73552.1) * mm});
            skLineSegment(sketch, "E4280", {"start": v(44693.58, 73552.1) * mm, "end": v(44693.57, 73552.23) * mm});
            skLineSegment(sketch, "E4281", {"start": v(44693.57, 73552.23) * mm, "end": v(44693.55, 73552.36) * mm});
            skLineSegment(sketch, "E4282", {"start": v(44693.55, 73552.36) * mm, "end": v(44693.52, 73552.5) * mm});
            skLineSegment(sketch, "E4283", {"start": v(44693.52, 73552.5) * mm, "end": v(44693.49, 73552.62) * mm});
            skLineSegment(sketch, "E4284", {"start": v(44693.49, 73552.62) * mm, "end": v(44693.45, 73552.74) * mm});
            skLineSegment(sketch, "E4285", {"start": v(44693.45, 73552.74) * mm, "end": v(44694.15, 73553.65) * mm});
            skArc(sketch, "E4286", {"start": v(44590.59, 73392.13) * mm, "mid": v(44590.6, 73392.1) * mm, "end": v(44590.62, 73392.08) * mm});
            skLineSegment(sketch, "E4287", {"start": v(44590.62, 73392.08) * mm, "end": v(44590.73, 73391.88) * mm});
            skArc(sketch, "E4288", {"start": v(44590.73, 73391.88) * mm, "mid": v(44590.87, 73391.65) * mm, "end": v(44591.02, 73391.44) * mm});
            skLineSegment(sketch, "E4289", {"start": v(44591.02, 73391.44) * mm, "end": v(44591.17, 73391.22) * mm});
            skArc(sketch, "E4290", {"start": v(44591.17, 73391.22) * mm, "mid": v(44591.45, 73390.85) * mm, "end": v(44591.75, 73390.5) * mm});
            skLineSegment(sketch, "E4291", {"start": v(44591.75, 73390.5) * mm, "end": v(44591.77, 73390.47) * mm});
            skArc(sketch, "E4292", {"start": v(44591.77, 73390.47) * mm, "mid": v(44592.06, 73390.15) * mm, "end": v(44592.36, 73389.84) * mm});
            skArc(sketch, "E4293", {"start": v(44592.36, 73389.84) * mm, "mid": v(44592.38, 73389.82) * mm, "end": v(44592.4, 73389.8) * mm});
            skArc(sketch, "E4294", {"start": v(44597.97, 73385.42) * mm, "mid": v(44598, 73385.4) * mm, "end": v(44598.04, 73385.4) * mm});
            skLineSegment(sketch, "E4295", {"start": v(44598.04, 73385.4) * mm, "end": v(44598.26, 73385.37) * mm});
            skArc(sketch, "E4296", {"start": v(44598.26, 73385.37) * mm, "mid": v(44598.51, 73385.34) * mm, "end": v(44598.77, 73385.31) * mm});
            skLineSegment(sketch, "E4297", {"start": v(44598.77, 73385.31) * mm, "end": v(44599.07, 73385.29) * mm});
            skArc(sketch, "E4298", {"start": v(44599.07, 73385.29) * mm, "mid": v(44599.62, 73385.26) * mm, "end": v(44600.17, 73385.26) * mm});
            skLineSegment(sketch, "E4299", {"start": v(44600.17, 73385.26) * mm, "end": v(44600.25, 73385.26) * mm});
            skArc(sketch, "E4300", {"start": v(44600.25, 73385.26) * mm, "mid": v(44600.8, 73385.3) * mm, "end": v(44601.35, 73385.35) * mm});
            skArc(sketch, "E4301", {"start": v(44601.35, 73385.35) * mm, "mid": v(44601.4, 73385.35) * mm, "end": v(44601.43, 73385.36) * mm});
            skArc(sketch, "E4302", {"start": v(44601.43, 73385.36) * mm, "mid": v(44601.45, 73385.36) * mm, "end": v(44601.47, 73385.36) * mm});
            skLineSegment(sketch, "E4303", {"start": v(44601.47, 73385.36) * mm, "end": v(44601.67, 73385.39) * mm});
            skArc(sketch, "E4304", {"start": v(44601.67, 73385.39) * mm, "mid": v(44601.9, 73385.42) * mm, "end": v(44602.11, 73385.46) * mm});
            skLineSegment(sketch, "E4305", {"start": v(44602.11, 73385.46) * mm, "end": v(44602.4, 73385.52) * mm});
            skArc(sketch, "E4306", {"start": v(44602.4, 73385.52) * mm, "mid": v(44602.88, 73385.63) * mm, "end": v(44603.37, 73385.77) * mm});
            skLineSegment(sketch, "E4307", {"start": v(44603.37, 73385.77) * mm, "end": v(44603.44, 73385.8) * mm});
            skArc(sketch, "E4308", {"start": v(44603.44, 73385.8) * mm, "mid": v(44603.46, 73385.8) * mm, "end": v(44603.48, 73385.8) * mm});
            skArc(sketch, "E4309", {"start": v(44609.18, 73392.14) * mm, "mid": v(44609.19, 73392.17) * mm, "end": v(44609.2, 73392.2) * mm});
            skLineSegment(sketch, "E4310", {"start": v(44609.2, 73392.2) * mm, "end": v(44609.3, 73392.35) * mm});
            skArc(sketch, "E4311", {"start": v(44609.3, 73392.35) * mm, "mid": v(44609.4, 73392.54) * mm, "end": v(44609.49, 73392.73) * mm});
            skLineSegment(sketch, "E4312", {"start": v(44609.49, 73392.73) * mm, "end": v(44609.58, 73392.92) * mm});
            skArc(sketch, "E4313", {"start": v(44609.58, 73392.92) * mm, "mid": v(44609.76, 73393.3) * mm, "end": v(44609.91, 73393.7) * mm});
            skLineSegment(sketch, "E4314", {"start": v(44609.91, 73393.7) * mm, "end": v(44609.92, 73393.72) * mm});
            skArc(sketch, "E4315", {"start": v(44609.92, 73393.72) * mm, "mid": v(44610.07, 73394.15) * mm, "end": v(44610.2, 73394.58) * mm});
            skArc(sketch, "E4316", {"start": v(44610.2, 73394.58) * mm, "mid": v(44610.21, 73394.6) * mm, "end": v(44610.22, 73394.63) * mm});
            skArc(sketch, "E4317", {"start": v(44632.77, 73140.53) * mm, "mid": v(44755.65, 73210.9) * mm, "end": v(44792.79, 73347.53) * mm});
            skArc(sketch, "E4318", {"start": v(44792.79, 73347.53) * mm, "mid": v(44722.43, 73470.4) * mm, "end": v(44585.8, 73507.54) * mm});
            skArc(sketch, "E4319", {"start": v(44585.8, 73507.54) * mm, "mid": v(44462.92, 73437.18) * mm, "end": v(44425.78, 73300.55) * mm});
            skArc(sketch, "E4320", {"start": v(44425.78, 73300.55) * mm, "mid": v(44496.14, 73177.67) * mm, "end": v(44632.77, 73140.53) * mm});
            skArc(sketch, "E4321", {"start": v(44589.26, 73480.47) * mm, "mid": v(44484.5, 73420.5) * mm, "end": v(44452.85, 73304.01) * mm});
            skArc(sketch, "E4322", {"start": v(44452.85, 73304.01) * mm, "mid": v(44512.83, 73199.26) * mm, "end": v(44629.3, 73167.6) * mm});
            skArc(sketch, "E4323", {"start": v(44629.3, 73167.6) * mm, "mid": v(44734.06, 73227.58) * mm, "end": v(44765.72, 73344.06) * mm});
            skArc(sketch, "E4324", {"start": v(44765.72, 73344.06) * mm, "mid": v(44705.74, 73448.81) * mm, "end": v(44589.26, 73480.47) * mm});
            skLineSegment(sketch, "E4325", {"start": v(42425.01, 69928.56) * mm, "end": v(42466.87, 69985.42) * mm});
            skLineSegment(sketch, "E4326", {"start": v(42414, 69930.45) * mm, "end": v(42458.81, 69991.34) * mm});
            skLineSegment(sketch, "E4327", {"start": v(42438.8, 69926.19) * mm, "end": v(42476.93, 69978) * mm});
            skLineSegment(sketch, "E4328", {"start": v(42452.57, 69923.82) * mm, "end": v(42487, 69970.6) * mm});
            skLineSegment(sketch, "E4329", {"start": v(42531.92, 69910.17) * mm, "end": v(42544.99, 69927.91) * mm});
            skLineSegment(sketch, "E4330", {"start": v(43115.08, 69479.4) * mm, "end": v(42700.3, 69353.86) * mm});
            skLineSegment(sketch, "E4331", {"start": v(43109.28, 69467.2) * mm, "end": v(42703.2, 69344.3) * mm});
            skLineSegment(sketch, "E4332", {"start": v(43122.34, 69494.66) * mm, "end": v(42696.69, 69365.83) * mm});
            skLineSegment(sketch, "E4333", {"start": v(43129.6, 69509.92) * mm, "end": v(42693.07, 69377.8) * mm});
            skLineSegment(sketch, "E4334", {"start": v(43171.4, 69597.8) * mm, "end": v(42672.2, 69446.7) * mm});
            skLineSegment(sketch, "E4335", {"start": v(45329.68, 71142.62) * mm, "end": v(45253.43, 71198.75) * mm});
            skLineSegment(sketch, "E4336", {"start": v(45315.7, 71140.5) * mm, "end": v(45258.19, 71182.83) * mm});
            skLineSegment(sketch, "E4337", {"start": v(45347.16, 71145.27) * mm, "end": v(45247.48, 71218.65) * mm});
            skLineSegment(sketch, "E4338", {"start": v(45364.63, 71147.93) * mm, "end": v(45241.53, 71238.55) * mm});
            skLineSegment(sketch, "E4339", {"start": v(45465.3, 71163.23) * mm, "end": v(45207.26, 71353.18) * mm});
            skLineSegment(sketch, "E4340", {"start": v(45491.31, 70935.94) * mm, "end": v(45287.81, 71085.74) * mm});
            skLineSegment(sketch, "E4341", {"start": v(45494.73, 70921) * mm, "end": v(45273.83, 71083.62) * mm});
            skLineSegment(sketch, "E4342", {"start": v(45487.04, 70954.6) * mm, "end": v(45305.29, 71088.4) * mm});
            skLineSegment(sketch, "E4343", {"start": v(45482.77, 70973.27) * mm, "end": v(45322.77, 71091.05) * mm});
            skLineSegment(sketch, "E4344", {"start": v(45458.16, 71080.8) * mm, "end": v(45423.43, 71106.36) * mm});
            skLineSegment(sketch, "E4345", {"start": v(45287.81, 71085.74) * mm, "end": v(45329.68, 71142.62) * mm});
            skLineSegment(sketch, "E4346", {"start": v(45273.83, 71083.62) * mm, "end": v(45315.7, 71140.5) * mm});
            skLineSegment(sketch, "E4347", {"start": v(45305.29, 71088.4) * mm, "end": v(45347.16, 71145.27) * mm});
            skLineSegment(sketch, "E4348", {"start": v(45322.77, 71091.05) * mm, "end": v(45364.63, 71147.93) * mm});
            skLineSegment(sketch, "E4349", {"start": v(45423.43, 71106.36) * mm, "end": v(45465.3, 71163.23) * mm});
            skLineSegment(sketch, "E4350", {"start": v(44459.55, 68554.42) * mm, "end": v(44525.99, 68505.5) * mm});
            skLineSegment(sketch, "E4351", {"start": v(44465.47, 68562.47) * mm, "end": v(44523.86, 68519.5) * mm});
            skLineSegment(sketch, "E4352", {"start": v(44452.14, 68544.35) * mm, "end": v(44528.64, 68488.03) * mm});
            skLineSegment(sketch, "E4353", {"start": v(44444.73, 68534.28) * mm, "end": v(44531.3, 68470.56) * mm});
            skLineSegment(sketch, "E4354", {"start": v(44402.04, 68476.3) * mm, "end": v(44546.6, 68369.89) * mm});
            skLineSegment(sketch, "E4355", {"start": v(44567.85, 68562.39) * mm, "end": v(44777.16, 68408.3) * mm});
            skLineSegment(sketch, "E4356", {"start": v(44565.73, 68576.37) * mm, "end": v(44787.37, 68413.2) * mm});
            skLineSegment(sketch, "E4357", {"start": v(44570.51, 68544.9) * mm, "end": v(44764.4, 68402.18) * mm});
            skLineSegment(sketch, "E4358", {"start": v(44573.17, 68527.43) * mm, "end": v(44751.64, 68396.06) * mm});
            skLineSegment(sketch, "E4359", {"start": v(44588.47, 68426.76) * mm, "end": v(44678.12, 68360.77) * mm});
            skLineSegment(sketch, "E4360", {"start": v(44525.99, 68505.5) * mm, "end": v(44567.85, 68562.39) * mm});
            skLineSegment(sketch, "E4361", {"start": v(44523.86, 68519.5) * mm, "end": v(44565.73, 68576.37) * mm});
            skLineSegment(sketch, "E4362", {"start": v(44528.64, 68488.03) * mm, "end": v(44570.51, 68544.9) * mm});
            skLineSegment(sketch, "E4363", {"start": v(44531.3, 68470.56) * mm, "end": v(44573.17, 68527.43) * mm});
            skLineSegment(sketch, "E4364", {"start": v(44546.6, 68369.89) * mm, "end": v(44588.47, 68426.76) * mm});
            skLineSegment(sketch, "E4365", {"start": v(43855.66, 67961.78) * mm, "end": v(44293.32, 68556.33) * mm});
            skLineSegment(sketch, "E4366", {"start": v(43844.64, 67963.68) * mm, "end": v(44285.27, 68562.26) * mm});
            skLineSegment(sketch, "E4367", {"start": v(43869.44, 67959.41) * mm, "end": v(44303.39, 68548.92) * mm});
            skLineSegment(sketch, "E4368", {"start": v(43883.22, 67957.04) * mm, "end": v(44313.46, 68541.51) * mm});
            skLineSegment(sketch, "E4369", {"start": v(43962.57, 67943.4) * mm, "end": v(44371.44, 68498.83) * mm});
            skLineSegment(sketch, "E4370", {"start": v(43911.5, 67777.28) * mm, "end": v(43855.66, 67961.78) * mm});
            skLineSegment(sketch, "E4371", {"start": v(43901.93, 67774.39) * mm, "end": v(43844.64, 67963.68) * mm});
            skLineSegment(sketch, "E4372", {"start": v(43923.47, 67780.9) * mm, "end": v(43869.44, 67959.41) * mm});
            skLineSegment(sketch, "E4373", {"start": v(43935.43, 67784.53) * mm, "end": v(43883.22, 67957.04) * mm});
            skLineSegment(sketch, "E4374", {"start": v(44004.35, 67805.38) * mm, "end": v(43962.57, 67943.4) * mm});
            skLineSegment(sketch, "E4375", {"start": v(45366.3, 65592.82) * mm, "end": v(45299.69, 65641.86) * mm});
            skLineSegment(sketch, "E4376", {"start": v(45368.43, 65578.84) * mm, "end": v(45303.43, 65626.69) * mm});
            skLineSegment(sketch, "E4377", {"start": v(45363.65, 65610.3) * mm, "end": v(45295, 65660.83) * mm});
            skLineSegment(sketch, "E4378", {"start": v(45360.99, 65627.78) * mm, "end": v(45290.33, 65679.8) * mm});
            skLineSegment(sketch, "E4379", {"start": v(45345.68, 65728.45) * mm, "end": v(45263.37, 65789.04) * mm});
            skLineSegment(sketch, "E4380", {"start": v(47384.13, 64750.73) * mm, "end": v(47469.71, 65142.82) * mm});
            skLineSegment(sketch, "E4381", {"start": v(47372.23, 64743.09) * mm, "end": v(47461.88, 65153.83) * mm});
            skLineSegment(sketch, "E4382", {"start": v(47399.01, 64760.27) * mm, "end": v(47479.5, 65129.05) * mm});
            skLineSegment(sketch, "E4383", {"start": v(47413.89, 64769.82) * mm, "end": v(47489.3, 65115.28) * mm});
            skLineSegment(sketch, "E4384", {"start": v(47499.59, 64824.81) * mm, "end": v(47545.68, 65035.98) * mm});
            skArc(sketch, "E4385", {"start": v(46383.35, 65067.97) * mm, "mid": v(46609.01, 63797.3) * mm, "end": v(47853.14, 63454.27) * mm});
            skLineSegment(sketch, "E4386", {"start": v(47502.83, 64611.4) * mm, "end": v(47853.14, 63454.27) * mm});
            skLineSegment(sketch, "E4387", {"start": v(47853.14, 63454.27) * mm, "end": v(47803.37, 63439.2) * mm});
            skLineSegment(sketch, "E4388", {"start": v(47803.37, 63439.2) * mm, "end": v(47453.06, 64596.34) * mm});
            skLineSegment(sketch, "E4389", {"start": v(47453.06, 64596.34) * mm, "end": v(47502.83, 64611.4) * mm});
            skLineSegment(sketch, "E4390", {"start": v(47453.06, 64596.34) * mm, "end": v(47803.37, 63439.2) * mm});
            skLineSegment(sketch, "E4391", {"start": v(47502.83, 64611.4) * mm, "end": v(47453.06, 64596.34) * mm});
            skArc(sketch, "E4392", {"start": v(47536.97, 65048.23) * mm, "mid": v(48208.68, 65127.88) * mm, "end": v(48855.47, 65325.9) * mm});
            skArc(sketch, "E4393", {"start": v(47545.68, 65035.98) * mm, "mid": v(48215.35, 65116.52) * mm, "end": v(48860.19, 65314.32) * mm});
            skArc(sketch, "E4394", {"start": v(47477.76, 65131.5) * mm, "mid": v(48163.45, 65204.82) * mm, "end": v(48823.61, 65404.16) * mm});
            skArc(sketch, "E4395", {"start": v(47486.56, 65119.13) * mm, "mid": v(48170.16, 65193.43) * mm, "end": v(48828.33, 65392.58) * mm});
            skArc(sketch, "E4396", {"start": v(47468.94, 65143.9) * mm, "mid": v(48156.73, 65216.22) * mm, "end": v(48818.9, 65415.74) * mm});
            skArc(sketch, "E4397", {"start": v(47461.88, 65153.83) * mm, "mid": v(48151.35, 65225.34) * mm, "end": v(48815.13, 65425) * mm});
            skLineSegment(sketch, "E4398", {"start": v(48859.92, 65314.21) * mm, "end": v(48859.92, 65314.21) * mm});
            skLineSegment(sketch, "E4399", {"start": v(48815.4, 65425.11) * mm, "end": v(48815.4, 65425.11) * mm});
            skArc(sketch, "E4400", {"start": v(48855.26, 65325.81) * mm, "mid": v(49667.78, 65731.29) * mm, "end": v(50404.11, 66262.71) * mm});
            skArc(sketch, "E4401", {"start": v(48859.92, 65314.21) * mm, "mid": v(49674.25, 65720.6) * mm, "end": v(50412.23, 66253.2) * mm});
            skArc(sketch, "E4402", {"start": v(48823.78, 65404.23) * mm, "mid": v(49624.05, 65803.59) * mm, "end": v(50349.27, 66327) * mm});
            skArc(sketch, "E4403", {"start": v(48828.44, 65392.63) * mm, "mid": v(49630.52, 65792.9) * mm, "end": v(50357.38, 66317.5) * mm});
            skArc(sketch, "E4404", {"start": v(48819.12, 65415.83) * mm, "mid": v(49617.58, 65814.28) * mm, "end": v(50341.16, 66336.5) * mm});
            skArc(sketch, "E4405", {"start": v(48815.4, 65425.11) * mm, "mid": v(49612.4, 65822.84) * mm, "end": v(50334.67, 66344.12) * mm});
            skLineSegment(sketch, "E4406", {"start": v(50412.1, 66253.1) * mm, "end": v(50412.1, 66253.1) * mm});
            skLineSegment(sketch, "E4407", {"start": v(50334.79, 66344.22) * mm, "end": v(50334.79, 66344.22) * mm});
            skArc(sketch, "E4408", {"start": v(50404.02, 66262.63) * mm, "mid": v(50783.67, 66609.05) * mm, "end": v(51137.41, 66981.89) * mm});
            skArc(sketch, "E4409", {"start": v(50412.1, 66253.1) * mm, "mid": v(50786.19, 66594.02) * mm, "end": v(51135.22, 66960.54) * mm});
            skArc(sketch, "E4410", {"start": v(50349.35, 66327.06) * mm, "mid": v(50767.03, 66711.44) * mm, "end": v(51152.46, 67128.16) * mm});
            skArc(sketch, "E4411", {"start": v(50357.43, 66317.53) * mm, "mid": v(50769.45, 66696.2) * mm, "end": v(51150.2, 67106.3) * mm});
            skArc(sketch, "E4412", {"start": v(50341.26, 66336.6) * mm, "mid": v(50764.63, 66726.7) * mm, "end": v(51154.71, 67150.1) * mm});
            skArc(sketch, "E4413", {"start": v(50334.79, 66344.22) * mm, "mid": v(50762.72, 66738.95) * mm, "end": v(51156.52, 67167.72) * mm});
            skArc(sketch, "E4414", {"start": v(51599.5, 73905) * mm, "mid": v(50950.64, 74218.08) * mm, "end": v(50241.56, 74345.58) * mm});
            skArc(sketch, "E4415", {"start": v(51552.81, 73834.57) * mm, "mid": v(50924.56, 74137.7) * mm, "end": v(50238, 74261.15) * mm});
            skArc(sketch, "E4416", {"start": v(51559.72, 73844.99) * mm, "mid": v(50928.42, 74149.6) * mm, "end": v(50238.53, 74273.64) * mm});
            skArc(sketch, "E4417", {"start": v(51545.9, 73824.15) * mm, "mid": v(50920.7, 74125.81) * mm, "end": v(50237.48, 74248.66) * mm});
            skArc(sketch, "E4418", {"start": v(51540.38, 73815.81) * mm, "mid": v(50917.62, 74116.3) * mm, "end": v(50237.06, 74238.67) * mm});
            skArc(sketch, "E4419", {"start": v(50241.32, 74345.59) * mm, "mid": v(49440.65, 74291.22) * mm, "end": v(48669.46, 74069.16) * mm});
            skArc(sketch, "E4420", {"start": v(50238.07, 74261.15) * mm, "mid": v(49455.28, 74208) * mm, "end": v(48701.32, 73990.9) * mm});
            skArc(sketch, "E4421", {"start": v(50238.55, 74273.64) * mm, "mid": v(49453.12, 74220.3) * mm, "end": v(48696.6, 74002.48) * mm});
            skArc(sketch, "E4422", {"start": v(50237.6, 74248.66) * mm, "mid": v(49457.45, 74195.68) * mm, "end": v(48706.03, 73979.32) * mm});
            skArc(sketch, "E4423", {"start": v(50237.2, 74238.67) * mm, "mid": v(49459.18, 74185.83) * mm, "end": v(48709.8, 73970.06) * mm});
            skLineSegment(sketch, "E4424", {"start": v(48669.7, 74069.26) * mm, "end": v(48669.7, 74069.26) * mm});
            skLineSegment(sketch, "E4425", {"start": v(48709.56, 73969.96) * mm, "end": v(48709.56, 73969.96) * mm});
            skArc(sketch, "E4426", {"start": v(48669.7, 74069.26) * mm, "mid": v(47857.17, 73663.78) * mm, "end": v(47120.83, 73132.35) * mm});
            skArc(sketch, "E4427", {"start": v(48701.18, 73990.84) * mm, "mid": v(47900.9, 73591.48) * mm, "end": v(47175.68, 73068.06) * mm});
            skArc(sketch, "E4428", {"start": v(48696.52, 74002.44) * mm, "mid": v(47894.44, 73602.18) * mm, "end": v(47167.56, 73077.57) * mm});
            skArc(sketch, "E4429", {"start": v(48705.84, 73979.24) * mm, "mid": v(47907.38, 73580.79) * mm, "end": v(47183.8, 73058.55) * mm});
            skArc(sketch, "E4430", {"start": v(48709.56, 73969.96) * mm, "mid": v(47912.55, 73572.23) * mm, "end": v(47190.28, 73050.95) * mm});
            skLineSegment(sketch, "E4431", {"start": v(47120.94, 73132.44) * mm, "end": v(47120.94, 73132.44) * mm});
            skLineSegment(sketch, "E4432", {"start": v(47190.17, 73050.85) * mm, "end": v(47190.17, 73050.85) * mm});
            skArc(sketch, "E4433", {"start": v(47120.94, 73132.44) * mm, "mid": v(46193.84, 72184.19) * mm, "end": v(45458.16, 71080.8) * mm});
            skArc(sketch, "E4434", {"start": v(47175.61, 73068.01) * mm, "mid": v(46229.04, 72093.16) * mm, "end": v(45486.98, 70954.88) * mm});
            skArc(sketch, "E4435", {"start": v(47167.53, 73077.54) * mm, "mid": v(46223.85, 72106.67) * mm, "end": v(45482.69, 70973.63) * mm});
            skArc(sketch, "E4436", {"start": v(47183.7, 73058.48) * mm, "mid": v(46234.23, 72079.62) * mm, "end": v(45491.28, 70936.08) * mm});
            skArc(sketch, "E4437", {"start": v(47190.17, 73050.85) * mm, "mid": v(46238.38, 72068.78) * mm, "end": v(45494.73, 70921) * mm});
            skArc(sketch, "E4438", {"start": v(44678.12, 68360.77) * mm, "mid": v(44675.27, 68253.17) * mm, "end": v(44674.49, 68145.54) * mm});
            skArc(sketch, "E4439", {"start": v(44764.35, 68402.16) * mm, "mid": v(44760.18, 68273.98) * mm, "end": v(44758.99, 68145.74) * mm});
            skArc(sketch, "E4440", {"start": v(44751.57, 68396.02) * mm, "mid": v(44747.61, 68270.9) * mm, "end": v(44746.49, 68145.7) * mm});
            skArc(sketch, "E4441", {"start": v(44777.14, 68408.3) * mm, "mid": v(44772.75, 68277.07) * mm, "end": v(44771.49, 68145.77) * mm});
            skArc(sketch, "E4442", {"start": v(44787.37, 68413.2) * mm, "mid": v(44782.8, 68279.54) * mm, "end": v(44781.49, 68145.8) * mm});
            skLineSegment(sketch, "E4443", {"start": v(44674.49, 68145.8) * mm, "end": v(44674.49, 68145.8) * mm});
            skLineSegment(sketch, "E4444", {"start": v(44781.49, 68145.53) * mm, "end": v(44781.49, 68145.53) * mm});
            skArc(sketch, "E4445", {"start": v(44674.49, 68145.8) * mm, "mid": v(44757.57, 67347.54) * mm, "end": v(45007.2, 66584.77) * mm});
            skArc(sketch, "E4446", {"start": v(44758.99, 68145.59) * mm, "mid": v(44840.22, 67365.15) * mm, "end": v(45084.27, 66619.42) * mm});
            skArc(sketch, "E4447", {"start": v(44746.49, 68145.62) * mm, "mid": v(44828, 67362.55) * mm, "end": v(45072.87, 66614.3) * mm});
            skArc(sketch, "E4448", {"start": v(44771.49, 68145.56) * mm, "mid": v(44852.44, 67367.76) * mm, "end": v(45095.67, 66624.55) * mm});
            skArc(sketch, "E4449", {"start": v(44781.49, 68145.53) * mm, "mid": v(44862.22, 67369.84) * mm, "end": v(45104.79, 66628.65) * mm});
            skLineSegment(sketch, "E4450", {"start": v(45007.28, 66584.6) * mm, "end": v(45007.28, 66584.6) * mm});
            skLineSegment(sketch, "E4451", {"start": v(45104.7, 66628.83) * mm, "end": v(45104.7, 66628.83) * mm});
            skArc(sketch, "E4452", {"start": v(45007.28, 66584.6) * mm, "mid": v(45208.86, 66219.6) * mm, "end": v(45465, 65890.6) * mm});
            skArc(sketch, "E4453", {"start": v(45084.22, 66619.52) * mm, "mid": v(45298.56, 66237.5) * mm, "end": v(45574.54, 65897.3) * mm});
            skArc(sketch, "E4454", {"start": v(45072.84, 66614.36) * mm, "mid": v(45285.24, 66234.87) * mm, "end": v(45558.18, 65896.3) * mm});
            skArc(sketch, "E4455", {"start": v(45095.6, 66624.7) * mm, "mid": v(45311.9, 66240.1) * mm, "end": v(45590.95, 65898.31) * mm});
            skArc(sketch, "E4456", {"start": v(45104.7, 66628.83) * mm, "mid": v(45322.6, 66242.2) * mm, "end": v(45604.13, 65899.12) * mm});
            skArc(sketch, "E4457", {"start": v(52355.84, 73108.48) * mm, "mid": v(52021.22, 73547.33) * mm, "end": v(51600.42, 73904.38) * mm});
            skArc(sketch, "E4458", {"start": v(52283.52, 73064.78) * mm, "mid": v(51959.93, 73489.16) * mm, "end": v(51553, 73834.44) * mm});
            skArc(sketch, "E4459", {"start": v(52294.22, 73071.24) * mm, "mid": v(51969, 73497.76) * mm, "end": v(51560.02, 73844.78) * mm});
            skArc(sketch, "E4460", {"start": v(52272.82, 73058.31) * mm, "mid": v(51950.87, 73480.55) * mm, "end": v(51546, 73824.1) * mm});
            skArc(sketch, "E4461", {"start": v(52264.26, 73053.14) * mm, "mid": v(51943.61, 73473.67) * mm, "end": v(51540.38, 73815.81) * mm});
            skArc(sketch, "E4462", {"start": v(46375.02, 65071.36) * mm, "mid": v(44925.07, 66690.88) * mm, "end": v(44543.42, 64550.9) * mm});
            skLineSegment(sketch, "E4463", {"start": v(45255.54, 65527.92) * mm, "end": v(44543.42, 64550.9) * mm});
            skLineSegment(sketch, "E4464", {"start": v(44543.42, 64550.9) * mm, "end": v(44585.44, 64520.27) * mm});
            skLineSegment(sketch, "E4465", {"start": v(44585.44, 64520.27) * mm, "end": v(45297.56, 65497.3) * mm});
            skLineSegment(sketch, "E4466", {"start": v(45297.56, 65497.3) * mm, "end": v(45255.54, 65527.92) * mm});
            skLineSegment(sketch, "E4467", {"start": v(45297.56, 65497.3) * mm, "end": v(44585.44, 64520.27) * mm});
            skLineSegment(sketch, "E4468", {"start": v(45255.54, 65527.92) * mm, "end": v(45297.56, 65497.3) * mm});
            skLineSegment(sketch, "E4469", {"start": v(45591.13, 65898.33) * mm, "end": v(45366.3, 65592.82) * mm});
            skLineSegment(sketch, "E4470", {"start": v(45604.13, 65899.12) * mm, "end": v(45368.43, 65578.84) * mm});
            skLineSegment(sketch, "E4471", {"start": v(45574.87, 65897.33) * mm, "end": v(45363.65, 65610.3) * mm});
            skLineSegment(sketch, "E4472", {"start": v(45558.62, 65896.33) * mm, "end": v(45360.99, 65627.78) * mm});
            skLineSegment(sketch, "E4473", {"start": v(45465, 65890.6) * mm, "end": v(45345.68, 65728.45) * mm});
            skArc(sketch, "E4474", {"start": v(52356.08, 73108.07) * mm, "mid": v(52021.39, 73547.16) * mm, "end": v(51600.42, 73904.38) * mm});
            skArc(sketch, "E4475", {"start": v(52283.2, 73065.32) * mm, "mid": v(51959.72, 73489.39) * mm, "end": v(51553, 73834.44) * mm});
            skArc(sketch, "E4476", {"start": v(52293.97, 73071.64) * mm, "mid": v(51968.84, 73497.93) * mm, "end": v(51560.02, 73844.78) * mm});
            skArc(sketch, "E4477", {"start": v(52272.4, 73059) * mm, "mid": v(51950.6, 73480.84) * mm, "end": v(51546, 73824.1) * mm});
            skArc(sketch, "E4478", {"start": v(52263.78, 73053.93) * mm, "mid": v(51943.3, 73474) * mm, "end": v(51540.38, 73815.81) * mm});
            skLineSegment(sketch, "E4479", {"start": v(61186.15, 51653.76) * mm, "end": v(61176.4, 51671.24) * mm});
            skLineSegment(sketch, "E4480", {"start": v(61176.4, 51671.24) * mm, "end": v(61793.91, 52015.54) * mm});
            skLineSegment(sketch, "E4481", {"start": v(61793.91, 52015.54) * mm, "end": v(61803.66, 51998.06) * mm});
            skLineSegment(sketch, "E4482", {"start": v(61803.66, 51998.06) * mm, "end": v(61186.15, 51653.76) * mm});
            skLineSegment(sketch, "E4483", {"start": v(60908.55, 52151.61) * mm, "end": v(60898.82, 52169.07) * mm});
            skLineSegment(sketch, "E4484", {"start": v(60898.82, 52169.07) * mm, "end": v(61516.33, 52513.37) * mm});
            skLineSegment(sketch, "E4485", {"start": v(61516.33, 52513.37) * mm, "end": v(61526.06, 52495.92) * mm});
            skLineSegment(sketch, "E4486", {"start": v(61526.06, 52495.92) * mm, "end": v(60908.55, 52151.61) * mm});
            skLineSegment(sketch, "E4487", {"start": v(61308.82, 52374.79) * mm, "end": v(61326.3, 52384.53) * mm});
            skLineSegment(sketch, "E4488", {"start": v(61326.3, 52384.53) * mm, "end": v(61594.14, 51904.16) * mm});
            skLineSegment(sketch, "E4489", {"start": v(61594.14, 51904.16) * mm, "end": v(61576.67, 51894.42) * mm});
            skLineSegment(sketch, "E4490", {"start": v(61576.67, 51894.42) * mm, "end": v(61308.82, 52374.79) * mm});
            skArc(sketch, "E4491", {"start": v(51600.08, 73903.95) * mm, "mid": v(50951.22, 74217.03) * mm, "end": v(50242.15, 74344.53) * mm});
            skArc(sketch, "E4492", {"start": v(51553.4, 73833.52) * mm, "mid": v(50925.14, 74136.66) * mm, "end": v(50238.6, 74260.1) * mm});
            skArc(sketch, "E4493", {"start": v(51560.3, 73843.94) * mm, "mid": v(50929, 74148.55) * mm, "end": v(50239.12, 74272.6) * mm});
            skArc(sketch, "E4494", {"start": v(51546.49, 73823.1) * mm, "mid": v(50921.28, 74124.77) * mm, "end": v(50238.06, 74247.62) * mm});
            skArc(sketch, "E4495", {"start": v(51540.96, 73814.77) * mm, "mid": v(50918.2, 74115.25) * mm, "end": v(50237.64, 74237.63) * mm});
            skArc(sketch, "E4496", {"start": v(52356.3, 73107.64) * mm, "mid": v(52021.72, 73546.37) * mm, "end": v(51601, 73903.33) * mm});
            skArc(sketch, "E4497", {"start": v(52283.98, 73063.93) * mm, "mid": v(51960.44, 73488.2) * mm, "end": v(51553.59, 73833.4) * mm});
            skArc(sketch, "E4498", {"start": v(52294.68, 73070.4) * mm, "mid": v(51969.5, 73496.8) * mm, "end": v(51560.6, 73843.74) * mm});
            skArc(sketch, "E4499", {"start": v(52273.28, 73057.46) * mm, "mid": v(51951.37, 73479.6) * mm, "end": v(51546.57, 73823.05) * mm});
            skArc(sketch, "E4500", {"start": v(52264.73, 73052.29) * mm, "mid": v(51944.12, 73472.7) * mm, "end": v(51540.96, 73814.77) * mm});
            skArc(sketch, "E4501", {"start": v(52356.67, 73107.03) * mm, "mid": v(52021.97, 73546.11) * mm, "end": v(51601, 73903.33) * mm});
            skArc(sketch, "E4502", {"start": v(52283.77, 73064.27) * mm, "mid": v(51960.3, 73488.34) * mm, "end": v(51553.59, 73833.4) * mm});
            skArc(sketch, "E4503", {"start": v(52294.56, 73070.6) * mm, "mid": v(51969.42, 73496.89) * mm, "end": v(51560.6, 73843.74) * mm});
            skArc(sketch, "E4504", {"start": v(52273, 73057.95) * mm, "mid": v(51951.18, 73479.8) * mm, "end": v(51546.57, 73823.05) * mm});
            skArc(sketch, "E4505", {"start": v(52264.36, 73052.89) * mm, "mid": v(51943.88, 73472.96) * mm, "end": v(51540.96, 73814.77) * mm});
            skLineSegment(sketch, "E4506", {"start": v(50791.24, 73050.23) * mm, "end": v(50805.93, 73596.54) * mm});
            skLineSegment(sketch, "E4507", {"start": v(50805.93, 73596.54) * mm, "end": v(51194.77, 74007.38) * mm});
            skLineSegment(sketch, "E4508", {"start": v(50664.27, 73100.35) * mm, "end": v(50970.1, 74176.85) * mm});
            skLineSegment(sketch, "E4509", {"start": v(50791.24, 73050.23) * mm, "end": v(51194.77, 74007.38) * mm});
            skLineSegment(sketch, "E4510", {"start": v(50929.11, 72977.21) * mm, "end": v(51444.8, 73875.47) * mm});
            skLineSegment(sketch, "E4511", {"start": v(51049, 72894.92) * mm, "end": v(51668.97, 73721.84) * mm});
            skLineSegment(sketch, "E4512", {"start": v(51158.91, 72800.1) * mm, "end": v(51873.7, 73543.92) * mm});
            skLineSegment(sketch, "E4513", {"start": v(51257.7, 72693.78) * mm, "end": v(52057.46, 73344.66) * mm});
            skLineSegment(sketch, "E4514", {"start": v(50335.55, 71943.3) * mm, "end": v(62508.1, 50109.41) * mm});
            skLineSegment(sketch, "E4515", {"start": v(51293.6, 72477.42) * mm, "end": v(50335.55, 71943.3) * mm});
            skArc(sketch, "E4516", {"start": v(51293.6, 72477.42) * mm, "mid": v(51337.5, 72535.9) * mm, "end": v(51323.48, 72607.68) * mm});
            skArc(sketch, "E4517", {"start": v(51323.48, 72607.68) * mm, "mid": v(51033.33, 72906.82) * mm, "end": v(50664.27, 73100.34) * mm});
            skLineSegment(sketch, "E4518", {"start": v(47500.23, 64725.39) * mm, "end": v(47384.13, 64750.73) * mm});
            skLineSegment(sketch, "E4519", {"start": v(47503.54, 64714.43) * mm, "end": v(47372.23, 64743.09) * mm});
            skLineSegment(sketch, "E4520", {"start": v(47496.08, 64739.09) * mm, "end": v(47399.01, 64760.27) * mm});
            skLineSegment(sketch, "E4521", {"start": v(47491.93, 64752.79) * mm, "end": v(47413.89, 64769.82) * mm});
            skLineSegment(sketch, "E4522", {"start": v(47503.54, 64714.43) * mm, "end": v(47500.23, 64725.39) * mm});
            skLineSegment(sketch, "E4523", {"start": v(47500.23, 64725.39) * mm, "end": v(47496.08, 64739.09) * mm});
            skLineSegment(sketch, "E4524", {"start": v(47496.08, 64739.09) * mm, "end": v(47491.93, 64752.79) * mm});
            skLineSegment(sketch, "E4525", {"start": v(47468.05, 64831.7) * mm, "end": v(47517.27, 64820.95) * mm});
            skLineSegment(sketch, "E4526", {"start": v(55769.55, 58844.48) * mm, "end": v(55908.4, 58595.44) * mm});
            skLineSegment(sketch, "E4527", {"start": v(55776.9, 58870.33) * mm, "end": v(55924.99, 58604.7) * mm});
            skLineSegment(sketch, "E4528", {"start": v(55759.89, 58810.47) * mm, "end": v(55886.56, 58583.27) * mm});
            skLineSegment(sketch, "E4529", {"start": v(55755.06, 58793.47) * mm, "end": v(55875.64, 58577.18) * mm});
            skLineSegment(sketch, "E4530", {"start": v(55727.23, 58695.52) * mm, "end": v(55812.75, 58542.12) * mm});
            skLineSegment(sketch, "E4531", {"start": v(53540.67, 62626.82) * mm, "end": v(54840.14, 58333.61) * mm});
            skLineSegment(sketch, "E4532", {"start": v(53574.96, 62565.32) * mm, "end": v(54850.15, 58352.31) * mm});
            skLineSegment(sketch, "E4533", {"start": v(53506.38, 62688.32) * mm, "end": v(54830.13, 58314.9) * mm});
            skLineSegment(sketch, "E4534", {"start": v(53472.1, 62749.83) * mm, "end": v(54820.12, 58296.2) * mm});
            skLineSegment(sketch, "E4535", {"start": v(53266.37, 63118.83) * mm, "end": v(54760.05, 58184) * mm});
            skLineSegment(sketch, "E4536", {"start": v(53430.95, 62823.63) * mm, "end": v(54808.1, 58273.76) * mm});
            skLineSegment(sketch, "E4537", {"start": v(53197.8, 63241.83) * mm, "end": v(54740.03, 58146.59) * mm});
            skLineSegment(sketch, "E4538", {"start": v(54840.14, 58333.61) * mm, "end": v(55839.38, 58636.06) * mm});
            skLineSegment(sketch, "E4539", {"start": v(54850.15, 58352.31) * mm, "end": v(55846.6, 58653.92) * mm});
            skLineSegment(sketch, "E4540", {"start": v(54830.13, 58314.9) * mm, "end": v(55832.16, 58618.2) * mm});
            skLineSegment(sketch, "E4541", {"start": v(54820.12, 58296.2) * mm, "end": v(55824.94, 58600.35) * mm});
            skLineSegment(sketch, "E4542", {"start": v(54760.05, 58184) * mm, "end": v(55781.63, 58493.2) * mm});
            skLineSegment(sketch, "E4543", {"start": v(54808.1, 58273.76) * mm, "end": v(55816.28, 58578.92) * mm});
            skLineSegment(sketch, "E4544", {"start": v(54740.03, 58146.59) * mm, "end": v(55767.2, 58457.5) * mm});
            skLineSegment(sketch, "E4545", {"start": v(44490.99, 68614) * mm, "end": v(44393.99, 68482.23) * mm});
            skLineSegment(sketch, "E4546", {"start": v(44504.97, 68616.13) * mm, "end": v(44402.04, 68476.3) * mm});
            skLineSegment(sketch, "E4547", {"start": v(44423.42, 68543.3) * mm, "end": v(44383.92, 68489.64) * mm});
            skLineSegment(sketch, "E4548", {"start": v(44405.94, 68540.64) * mm, "end": v(44373.86, 68497.05) * mm});
            skLineSegment(sketch, "E4549", {"start": v(44335.48, 68592.5) * mm, "end": v(44303.39, 68548.92) * mm});
            skLineSegment(sketch, "E4550", {"start": v(44345.54, 68585.1) * mm, "end": v(44313.46, 68541.51) * mm});
            skLineSegment(sketch, "E4551", {"start": v(44318, 68589.85) * mm, "end": v(44293.32, 68556.33) * mm});
            skLineSegment(sketch, "E4552", {"start": v(44304.02, 68587.73) * mm, "end": v(44285.27, 68562.26) * mm});
            skLineSegment(sketch, "E4553", {"start": v(44473.51, 68611.34) * mm, "end": v(44423.42, 68543.3) * mm});
            skLineSegment(sketch, "E4554", {"start": v(44405.94, 68540.64) * mm, "end": v(44345.54, 68585.1) * mm});
            skLineSegment(sketch, "E4555", {"start": v(44345.54, 68585.1) * mm, "end": v(44335.48, 68592.5) * mm});
            skLineSegment(sketch, "E4556", {"start": v(45189.75, 71312.52) * mm, "end": v(45210.85, 71341.18) * mm});
            skLineSegment(sketch, "E4557", {"start": v(45187.63, 71326.5) * mm, "end": v(45207.26, 71353.18) * mm});
            skLineSegment(sketch, "E4558", {"start": v(45192.4, 71295.04) * mm, "end": v(45215.33, 71326.19) * mm});
            skLineSegment(sketch, "E4559", {"start": v(45195.06, 71277.57) * mm, "end": v(45219.82, 71311.2) * mm});
            skLineSegment(sketch, "E4560", {"start": v(45213.02, 71159.42) * mm, "end": v(45250.12, 71209.82) * mm});
            skLineSegment(sketch, "E4561", {"start": v(45210.37, 71176.9) * mm, "end": v(45245.64, 71224.82) * mm});
            skLineSegment(sketch, "E4562", {"start": v(45215.68, 71141.95) * mm, "end": v(45254.6, 71194.82) * mm});
            skLineSegment(sketch, "E4563", {"start": v(45217.8, 71127.96) * mm, "end": v(45258.19, 71182.83) * mm});
            skLineSegment(sketch, "E4564", {"start": v(45211.66, 71342.28) * mm, "end": v(45956.17, 72353.67) * mm});
            skLineSegment(sketch, "E4565", {"start": v(45203.6, 71348.2) * mm, "end": v(45942.18, 72351.55) * mm});
            skLineSegment(sketch, "E4566", {"start": v(45221.73, 71334.87) * mm, "end": v(45973.64, 72356.33) * mm});
            skLineSegment(sketch, "E4567", {"start": v(45231.8, 71327.46) * mm, "end": v(45991.12, 72358.98) * mm});
            skLineSegment(sketch, "E4568", {"start": v(45289.78, 71284.78) * mm, "end": v(46091.79, 72374.28) * mm});
            skLineSegment(sketch, "E4569", {"start": v(51186.33, 66894.55) * mm, "end": v(51137.45, 66982.22) * mm});
            skLineSegment(sketch, "E4570", {"start": v(51171.15, 66896.1) * mm, "end": v(51135.22, 66960.54) * mm});
            skLineSegment(sketch, "E4571", {"start": v(51288.94, 66884.02) * mm, "end": v(51152.51, 67128.71) * mm});
            skLineSegment(sketch, "E4572", {"start": v(51273.76, 66885.58) * mm, "end": v(51150.28, 67107.04) * mm});
            skLineSegment(sketch, "E4573", {"start": v(51304.12, 66882.46) * mm, "end": v(51154.74, 67150.39) * mm});
            skLineSegment(sketch, "E4574", {"start": v(51316.27, 66881.22) * mm, "end": v(51156.52, 67167.72) * mm});
            skLineSegment(sketch, "E4575", {"start": v(59604.06, 51966.53) * mm, "end": v(55869.43, 58665.33) * mm});
            skLineSegment(sketch, "E4576", {"start": v(59582.22, 51954.36) * mm, "end": v(55847.59, 58653.16) * mm});
            skLineSegment(sketch, "E4577", {"start": v(59620.65, 51975.78) * mm, "end": v(55886.02, 58674.59) * mm});
            skLineSegment(sketch, "E4578", {"start": v(60243.94, 50818.79) * mm, "end": v(60054.97, 51157.73) * mm});
            skLineSegment(sketch, "E4579", {"start": v(60209.93, 50828.45) * mm, "end": v(60033.13, 51145.56) * mm});
            skLineSegment(sketch, "E4580", {"start": v(60269.78, 50811.44) * mm, "end": v(60071.57, 51166.98) * mm});
            skLineSegment(sketch, "E4581", {"start": v(59601.44, 51965.07) * mm, "end": v(59620.65, 51975.78) * mm});
            skLineSegment(sketch, "E4582", {"start": v(60052.35, 51156.27) * mm, "end": v(60071.57, 51166.98) * mm});
            skLineSegment(sketch, "E4583", {"start": v(59601.44, 51965.07) * mm, "end": v(59582.22, 51954.36) * mm});
            skLineSegment(sketch, "E4584", {"start": v(60052.35, 51156.27) * mm, "end": v(60033.13, 51145.56) * mm});
            skLineSegment(sketch, "E4585", {"start": v(60033.13, 51145.56) * mm, "end": v(59582.22, 51954.36) * mm});
            skLineSegment(sketch, "E4586", {"start": v(60071.57, 51166.98) * mm, "end": v(59620.65, 51975.78) * mm});
            skLineSegment(sketch, "E4587", {"start": v(60123.4, 50751.59) * mm, "end": v(60243.94, 50818.79) * mm});
            skLineSegment(sketch, "E4588", {"start": v(60132.65, 50735) * mm, "end": v(60269.78, 50811.44) * mm});
            skLineSegment(sketch, "E4589", {"start": v(51912.93, 65771.37) * mm, "end": v(54462.39, 61198.4) * mm});
            skLineSegment(sketch, "E4590", {"start": v(51929.52, 65780.62) * mm, "end": v(54488.24, 61191.07) * mm});
            skLineSegment(sketch, "E4591", {"start": v(51891.1, 65759.2) * mm, "end": v(54428.38, 61208.07) * mm});
            skLineSegment(sketch, "E4592", {"start": v(51880.17, 65753.11) * mm, "end": v(54411.38, 61212.9) * mm});
            skLineSegment(sketch, "E4593", {"start": v(53574.96, 62565.32) * mm, "end": v(54313.43, 61240.72) * mm});
            skLineSegment(sketch, "E4594", {"start": v(51817.29, 65718.05) * mm, "end": v(53197.8, 63241.83) * mm});
            skLineSegment(sketch, "E4595", {"start": v(51371.8, 66742) * mm, "end": v(51432.8, 66632.58) * mm});
            skLineSegment(sketch, "E4596", {"start": v(51379.14, 66767.85) * mm, "end": v(51449.4, 66641.83) * mm});
            skLineSegment(sketch, "E4597", {"start": v(51362.13, 66707.99) * mm, "end": v(51410.96, 66620.4) * mm});
            skLineSegment(sketch, "E4598", {"start": v(51357.3, 66690.98) * mm, "end": v(51400.04, 66614.32) * mm});
            skLineSegment(sketch, "E4599", {"start": v(51329.48, 66593.03) * mm, "end": v(51337.16, 66579.26) * mm});
            skLineSegment(sketch, "E4600", {"start": v(51943.44, 65774.65) * mm, "end": v(51823.78, 65707.94) * mm});
            skLineSegment(sketch, "E4601", {"start": v(51451.63, 66656.81) * mm, "end": v(51331.97, 66590.1) * mm});
            skLineSegment(sketch, "E4602", {"start": v(51943.44, 65774.65) * mm, "end": v(51923, 65811.33) * mm});
            skLineSegment(sketch, "E4603", {"start": v(51923, 65811.33) * mm, "end": v(51803.33, 65744.62) * mm});
            skLineSegment(sketch, "E4604", {"start": v(51803.33, 65744.62) * mm, "end": v(51823.78, 65707.94) * mm});
            skLineSegment(sketch, "E4605", {"start": v(51823.78, 65707.94) * mm, "end": v(51943.44, 65774.65) * mm});
            skLineSegment(sketch, "E4606", {"start": v(51472.08, 66620.13) * mm, "end": v(51451.63, 66656.81) * mm});
            skLineSegment(sketch, "E4607", {"start": v(51331.97, 66590.1) * mm, "end": v(51352.42, 66553.42) * mm});
            skLineSegment(sketch, "E4608", {"start": v(51352.42, 66553.42) * mm, "end": v(51472.08, 66620.13) * mm});
            skLineSegment(sketch, "E4609", {"start": v(51451.63, 66656.81) * mm, "end": v(51472.08, 66620.13) * mm});
            skLineSegment(sketch, "E4610", {"start": v(51823.78, 65707.94) * mm, "end": v(51803.33, 65744.62) * mm});
            skLineSegment(sketch, "E4611", {"start": v(51472.08, 66620.13) * mm, "end": v(51352.42, 66553.42) * mm});
            skArc(sketch, "E4612", {"start": v(51472.08, 66620.13) * mm, "mid": v(51669.93, 64920.58) * mm, "end": v(52731.8, 66262.24) * mm});
            skLineSegment(sketch, "E4613", {"start": v(51923, 65811.33) * mm, "end": v(52731.8, 66262.24) * mm});
            skLineSegment(sketch, "E4614", {"start": v(52731.8, 66262.24) * mm, "end": v(52710.37, 66300.67) * mm});
            skLineSegment(sketch, "E4615", {"start": v(52710.37, 66300.67) * mm, "end": v(51901.57, 65849.76) * mm});
            skLineSegment(sketch, "E4616", {"start": v(51901.57, 65849.76) * mm, "end": v(51923, 65811.33) * mm});
            skLineSegment(sketch, "E4617", {"start": v(51901.57, 65849.76) * mm, "end": v(52710.37, 66300.67) * mm});
            skLineSegment(sketch, "E4618", {"start": v(51923, 65811.33) * mm, "end": v(51901.57, 65849.76) * mm});
            skLineSegment(sketch, "E4619", {"start": v(43262.63, 71083.3) * mm, "end": v(41554.96, 72340.36) * mm});
            skLineSegment(sketch, "E4620", {"start": v(43256.7, 71075.25) * mm, "end": v(41550.58, 72331.16) * mm});
            skLineSegment(sketch, "E4621", {"start": v(43270.04, 71093.37) * mm, "end": v(41560.43, 72351.86) * mm});
            skLineSegment(sketch, "E4622", {"start": v(43277.45, 71103.44) * mm, "end": v(41565.9, 72363.35) * mm});
            skLineSegment(sketch, "E4623", {"start": v(43327.55, 71171.49) * mm, "end": v(41602.86, 72441.07) * mm});
            skLineSegment(sketch, "E4624", {"start": v(43320.14, 71161.42) * mm, "end": v(41597.4, 72429.57) * mm});
            skLineSegment(sketch, "E4625", {"start": v(43334.96, 71181.56) * mm, "end": v(41608.33, 72452.57) * mm});
            skLineSegment(sketch, "E4626", {"start": v(43340.88, 71189.6) * mm, "end": v(41612.7, 72461.76) * mm});
            skLineSegment(sketch, "E4627", {"start": v(43816.86, 73740.3) * mm, "end": v(41501.26, 73443.26) * mm});
            skLineSegment(sketch, "E4628", {"start": v(43808.21, 73729.11) * mm, "end": v(41512.45, 73434.61) * mm});
            skLineSegment(sketch, "E4629", {"start": v(43827.67, 73754.3) * mm, "end": v(41487.27, 73454.06) * mm});
            skLineSegment(sketch, "E4630", {"start": v(43838.47, 73768.28) * mm, "end": v(41473.28, 73464.87) * mm});
            skLineSegment(sketch, "E4631", {"start": v(43900.73, 73848.86) * mm, "end": v(41392.71, 73527.13) * mm});
            skLineSegment(sketch, "E4632", {"start": v(42700.3, 69353.86) * mm, "end": v(41910.7, 69114.87) * mm});
            skLineSegment(sketch, "E4633", {"start": v(42703.2, 69344.3) * mm, "end": v(41913.6, 69105.3) * mm});
            skLineSegment(sketch, "E4634", {"start": v(42696.69, 69365.83) * mm, "end": v(41907.08, 69126.83) * mm});
            skLineSegment(sketch, "E4635", {"start": v(42693.07, 69377.8) * mm, "end": v(41903.46, 69138.8) * mm});
            skLineSegment(sketch, "E4636", {"start": v(42668.59, 69458.67) * mm, "end": v(41878.98, 69219.67) * mm});
            skLineSegment(sketch, "E4637", {"start": v(42672.2, 69446.7) * mm, "end": v(41882.6, 69207.7) * mm});
            skLineSegment(sketch, "E4638", {"start": v(42664.96, 69470.63) * mm, "end": v(41875.36, 69231.63) * mm});
            skLineSegment(sketch, "E4639", {"start": v(42662.07, 69480.2) * mm, "end": v(41872.46, 69241.2) * mm});
            skLineSegment(sketch, "E4640", {"start": v(41556.39, 72343.37) * mm, "end": v(40705.03, 72085.67) * mm});
            skLineSegment(sketch, "E4641", {"start": v(41550.58, 72331.16) * mm, "end": v(40717.5, 72079) * mm});
            skLineSegment(sketch, "E4642", {"start": v(41563.65, 72358.63) * mm, "end": v(40689.45, 72094.02) * mm});
            skLineSegment(sketch, "E4643", {"start": v(41570.9, 72373.88) * mm, "end": v(40673.86, 72102.36) * mm});
            skLineSegment(sketch, "E4644", {"start": v(41612.7, 72461.76) * mm, "end": v(40584.1, 72150.41) * mm});
            skLineSegment(sketch, "E4645", {"start": v(41594.64, 69146.66) * mm, "end": v(41865.79, 69228.74) * mm});
            skLineSegment(sketch, "E4646", {"start": v(41601.32, 69159.13) * mm, "end": v(41872.46, 69241.2) * mm});
            skLineSegment(sketch, "E4647", {"start": v(41586.3, 69131.08) * mm, "end": v(41857.45, 69213.15) * mm});
            skLineSegment(sketch, "E4648", {"start": v(41577.96, 69115.5) * mm, "end": v(41849.1, 69197.57) * mm});
            skLineSegment(sketch, "E4649", {"start": v(41529.9, 69025.72) * mm, "end": v(41801.05, 69107.8) * mm});
            skLineSegment(sketch, "E4650", {"start": v(41618, 69190.3) * mm, "end": v(40748.67, 72062.31) * mm});
            skLineSegment(sketch, "E4651", {"start": v(41601.32, 69159.13) * mm, "end": v(40717.5, 72079) * mm});
            skLineSegment(sketch, "E4652", {"start": v(41630.68, 69214) * mm, "end": v(40772.36, 72049.63) * mm});
            skLineSegment(sketch, "E4653", {"start": v(40748.67, 72062.31) * mm, "end": v(41545.84, 72303.61) * mm});
            skLineSegment(sketch, "E4654", {"start": v(40717.5, 72079) * mm, "end": v(41550.58, 72331.16) * mm});
            skLineSegment(sketch, "E4655", {"start": v(40772.36, 72049.63) * mm, "end": v(41542.24, 72282.67) * mm});
            skLineSegment(sketch, "E4656", {"start": v(41545.84, 72303.61) * mm, "end": v(43221.75, 71069.94) * mm});
            skLineSegment(sketch, "E4657", {"start": v(41550.58, 72331.16) * mm, "end": v(43256.7, 71075.25) * mm});
            skLineSegment(sketch, "E4658", {"start": v(41542.24, 72282.67) * mm, "end": v(43195.18, 71065.9) * mm});
            skLineSegment(sketch, "E4659", {"start": v(42580.37, 70198.64) * mm, "end": v(42386.44, 69935.2) * mm});
            skLineSegment(sketch, "E4660", {"start": v(42600.5, 70183.82) * mm, "end": v(42414, 69930.45) * mm});
            skLineSegment(sketch, "E4661", {"start": v(42565.06, 70209.9) * mm, "end": v(42365.5, 69938.8) * mm});
            skLineSegment(sketch, "E4662", {"start": v(43221.75, 71069.94) * mm, "end": v(43070.04, 70863.84) * mm});
            skLineSegment(sketch, "E4663", {"start": v(43256.7, 71075.25) * mm, "end": v(43090.17, 70849.02) * mm});
            skLineSegment(sketch, "E4664", {"start": v(43195.18, 71065.9) * mm, "end": v(43054.74, 70875.1) * mm});
            skLineSegment(sketch, "E4665", {"start": v(43072.45, 70862.07) * mm, "end": v(43090.17, 70849.02) * mm});
            skLineSegment(sketch, "E4666", {"start": v(42582.78, 70196.86) * mm, "end": v(42600.5, 70183.82) * mm});
            skLineSegment(sketch, "E4667", {"start": v(43072.45, 70862.07) * mm, "end": v(43054.74, 70875.1) * mm});
            skLineSegment(sketch, "E4668", {"start": v(42582.78, 70196.86) * mm, "end": v(42565.06, 70209.9) * mm});
            skLineSegment(sketch, "E4669", {"start": v(42565.06, 70209.9) * mm, "end": v(43054.74, 70875.1) * mm});
            skLineSegment(sketch, "E4670", {"start": v(42600.5, 70183.82) * mm, "end": v(43090.17, 70849.02) * mm});
            skLineSegment(sketch, "E4671", {"start": v(42386.44, 69935.2) * mm, "end": v(42528.49, 69465.89) * mm});
            skLineSegment(sketch, "E4672", {"start": v(42414, 69930.45) * mm, "end": v(42559.66, 69449.2) * mm});
            skLineSegment(sketch, "E4673", {"start": v(42365.5, 69938.8) * mm, "end": v(42504.8, 69478.57) * mm});
            skLineSegment(sketch, "E4674", {"start": v(42528.49, 69465.89) * mm, "end": v(41618, 69190.3) * mm});
            skLineSegment(sketch, "E4675", {"start": v(42559.66, 69449.2) * mm, "end": v(41601.32, 69159.13) * mm});
            skLineSegment(sketch, "E4676", {"start": v(42504.8, 69478.57) * mm, "end": v(41630.68, 69214) * mm});
            skLineSegment(sketch, "E4677", {"start": v(44241.59, 60452.66) * mm, "end": v(43807.05, 61888.34) * mm});
            skLineSegment(sketch, "E4678", {"start": v(43807.05, 61888.34) * mm, "end": v(45242.73, 62322.88) * mm});
            skLineSegment(sketch, "E4679", {"start": v(45242.73, 62322.88) * mm, "end": v(45677.27, 60887.2) * mm});
            skLineSegment(sketch, "E4680", {"start": v(45677.27, 60887.2) * mm, "end": v(44241.59, 60452.66) * mm});
            skLineSegment(sketch, "E4681", {"start": v(46466.89, 61126.2) * mm, "end": v(46032.35, 62561.88) * mm});
            skLineSegment(sketch, "E4682", {"start": v(46032.35, 62561.88) * mm, "end": v(47468.03, 62996.42) * mm});
            skLineSegment(sketch, "E4683", {"start": v(47468.03, 62996.42) * mm, "end": v(47902.57, 61560.74) * mm});
            skLineSegment(sketch, "E4684", {"start": v(47902.57, 61560.74) * mm, "end": v(46466.89, 61126.2) * mm});
            skLineSegment(sketch, "E4685", {"start": v(47143.89, 66163.34) * mm, "end": v(47521.6, 67199.04) * mm});
            skLineSegment(sketch, "E4686", {"start": v(46906.86, 67778.13) * mm, "end": v(46536.16, 67433.85) * mm});
            skLineSegment(sketch, "E4687", {"start": v(45852.61, 68916.41) * mm, "end": v(46966, 69023.39) * mm});
            skLineSegment(sketch, "E4688", {"start": v(45817.62, 68638.8) * mm, "end": v(46924, 68848.35) * mm});
            skLineSegment(sketch, "E4689", {"start": v(45800.77, 68359.53) * mm, "end": v(46890.36, 68671.52) * mm});
            skLineSegment(sketch, "E4690", {"start": v(45803.8, 68086.25) * mm, "end": v(46866.29, 68493.14) * mm});
            skLineSegment(sketch, "E4691", {"start": v(45829.28, 67807.36) * mm, "end": v(46853.36, 68313.6) * mm});
            skLineSegment(sketch, "E4692", {"start": v(45880.44, 67531.66) * mm, "end": v(46853.7, 68133.6) * mm});
            skLineSegment(sketch, "E4693", {"start": v(45960.73, 67262.42) * mm, "end": v(46870.23, 67954.37) * mm});
            skLineSegment(sketch, "E4694", {"start": v(46073.58, 67004.21) * mm, "end": v(46536.16, 67433.85) * mm});
            skLineSegment(sketch, "E4695", {"start": v(46222.98, 66764.9) * mm, "end": v(46968.74, 67609.1) * mm});
            skLineSegment(sketch, "E4696", {"start": v(46408.92, 66552.85) * mm, "end": v(47061.62, 67454.92) * mm});
            skLineSegment(sketch, "E4697", {"start": v(46628.77, 66378) * mm, "end": v(47188.94, 67327.68) * mm});
            skLineSegment(sketch, "E4698", {"start": v(46876.63, 66247.8) * mm, "end": v(47346.44, 67240.54) * mm});
            skLineSegment(sketch, "E4699", {"start": v(47523.65, 67220.34) * mm, "end": v(47522.5, 67208.4) * mm});
            skLineSegment(sketch, "E4700", {"start": v(47524.51, 67229.3) * mm, "end": v(47521.63, 67199.44) * mm});
            skLineSegment(sketch, "E4701", {"start": v(47141.9, 66154.15) * mm, "end": v(47139.37, 66142.42) * mm});
            skLineSegment(sketch, "E4702", {"start": v(47143.8, 66162.95) * mm, "end": v(47137.47, 66133.63) * mm});
            skLineSegment(sketch, "E4703", {"start": v(47332.74, 66681.2) * mm, "end": v(47111.53, 66744.17) * mm});
            skLineSegment(sketch, "E4704", {"start": v(47111.53, 66744.17) * mm, "end": v(46908.85, 66852.84) * mm});
            skLineSegment(sketch, "E4705", {"start": v(46908.85, 66852.84) * mm, "end": v(46735.27, 67003.89) * mm});
            skLineSegment(sketch, "E4706", {"start": v(46735.27, 67003.89) * mm, "end": v(46599.66, 67191.3) * mm});
            skLineSegment(sketch, "E4707", {"start": v(46599.66, 67191.3) * mm, "end": v(46488.91, 67389.96) * mm});
            skLineSegment(sketch, "E4708", {"start": v(46488.91, 67389.96) * mm, "end": v(46415.48, 67608.4) * mm});
            skLineSegment(sketch, "E4709", {"start": v(46415.48, 67608.4) * mm, "end": v(46367.07, 67832.64) * mm});
            skLineSegment(sketch, "E4710", {"start": v(46367.07, 67832.64) * mm, "end": v(46341.32, 68060.49) * mm});
            skLineSegment(sketch, "E4711", {"start": v(46341.32, 68060.49) * mm, "end": v(46335.04, 68289.7) * mm});
            skLineSegment(sketch, "E4712", {"start": v(46335.04, 68289.7) * mm, "end": v(46335.04, 68512.51) * mm});
            skLineSegment(sketch, "E4713", {"start": v(46335.04, 68512.51) * mm, "end": v(46370.81, 68743.58) * mm});
            skLineSegment(sketch, "E4714", {"start": v(46370.81, 68743.58) * mm, "end": v(46409.3, 68969.9) * mm});
            skLineSegment(sketch, "E4715", {"start": v(45817.62, 68638.8) * mm, "end": v(46409.3, 68969.9) * mm});
            skLineSegment(sketch, "E4716", {"start": v(46409.3, 68969.9) * mm, "end": v(46924.4, 68848.27) * mm});
            skLineSegment(sketch, "E4717", {"start": v(54478.46, 61184.25) * mm, "end": v(55769.39, 58869.93) * mm});
            skLineSegment(sketch, "E4718", {"start": v(46067.88, 60975.83) * mm, "end": v(45988.44, 60951.79) * mm});
            skLineSegment(sketch, "E4719", {"start": v(45988.44, 60951.79) * mm, "end": v(45985.55, 60961.36) * mm});
            skArc(sketch, "E4720", {"start": v(45985.55, 60961.36) * mm, "mid": v(45986.3, 60968.97) * mm, "end": v(45992.22, 60973.83) * mm});
            skLineSegment(sketch, "E4721", {"start": v(45992.22, 60973.83) * mm, "end": v(46052.52, 60992.08) * mm});
            skArc(sketch, "E4722", {"start": v(46052.52, 60992.08) * mm, "mid": v(46060.13, 60991.32) * mm, "end": v(46064.99, 60985.4) * mm});
            skLineSegment(sketch, "E4723", {"start": v(46064.99, 60985.4) * mm, "end": v(46067.88, 60975.83) * mm});
            skLineSegment(sketch, "E4724", {"start": v(46036.73, 60987.3) * mm, "end": v(46008.01, 60978.6) * mm});
            skLineSegment(sketch, "E4725", {"start": v(46008.01, 60978.6) * mm, "end": v(46007.72, 60979.56) * mm});
            skLineSegment(sketch, "E4726", {"start": v(46007.72, 60979.56) * mm, "end": v(46036.44, 60988.25) * mm});
            skLineSegment(sketch, "E4727", {"start": v(46036.44, 60988.25) * mm, "end": v(46036.73, 60987.3) * mm});
            skLineSegment(sketch, "E4728", {"start": v(48410.5, 60764.72) * mm, "end": v(48399.78, 60800.14) * mm});
            skLineSegment(sketch, "E4729", {"start": v(48399.78, 60800.14) * mm, "end": v(48418.44, 60805.79) * mm});
            skLineSegment(sketch, "E4730", {"start": v(48554.35, 60846.92) * mm, "end": v(48573.02, 60852.57) * mm});
            skLineSegment(sketch, "E4731", {"start": v(48573.02, 60852.57) * mm, "end": v(48583.74, 60817.16) * mm});
            skLineSegment(sketch, "E4732", {"start": v(48824.5, 60011.35) * mm, "end": v(48827.37, 60012.22) * mm});
            skLineSegment(sketch, "E4733", {"start": v(48827.37, 60012.22) * mm, "end": v(48575.34, 60844.92) * mm});
            skLineSegment(sketch, "E4734", {"start": v(48657, 59960.66) * mm, "end": v(48672.8, 59965.44) * mm});
            skLineSegment(sketch, "E4735", {"start": v(48808.71, 60006.57) * mm, "end": v(48824.5, 60011.35) * mm});
            skLineSegment(sketch, "E4736", {"start": v(48654.14, 59959.79) * mm, "end": v(48657, 59960.66) * mm});
            skLineSegment(sketch, "E4737", {"start": v(48402.1, 60792.48) * mm, "end": v(48654.14, 59959.79) * mm});
            skLineSegment(sketch, "E4738", {"start": v(48642.8, 60672.05) * mm, "end": v(48628.93, 60667.85) * mm});
            skLineSegment(sketch, "E4739", {"start": v(48455.7, 60615.41) * mm, "end": v(48441.81, 60611.21) * mm});
            skLineSegment(sketch, "E4740", {"start": v(48441.81, 60611.21) * mm, "end": v(48586.66, 60132.65) * mm});
            skLineSegment(sketch, "E4741", {"start": v(48586.66, 60132.65) * mm, "end": v(48600.54, 60136.85) * mm});
            skLineSegment(sketch, "E4742", {"start": v(48773.78, 60189.3) * mm, "end": v(48787.66, 60193.5) * mm});
            skLineSegment(sketch, "E4743", {"start": v(48787.66, 60193.5) * mm, "end": v(48642.8, 60672.05) * mm});
            skLineSegment(sketch, "E4744", {"start": v(48468.92, 60846.14) * mm, "end": v(48466.6, 60853.8) * mm});
            skLineSegment(sketch, "E4745", {"start": v(48466.6, 60853.8) * mm, "end": v(48409.17, 60836.41) * mm});
            skLineSegment(sketch, "E4746", {"start": v(48409.17, 60836.41) * mm, "end": v(48411.5, 60828.76) * mm});
            skLineSegment(sketch, "E4747", {"start": v(48495.57, 60758.08) * mm, "end": v(48486.3, 60788.71) * mm});
            skLineSegment(sketch, "E4748", {"start": v(48411.5, 60828.76) * mm, "end": v(48438.14, 60740.7) * mm});
            skLineSegment(sketch, "E4749", {"start": v(48438.14, 60740.7) * mm, "end": v(48495.57, 60758.08) * mm});
            skLineSegment(sketch, "E4750", {"start": v(48486.3, 60788.71) * mm, "end": v(48468.92, 60846.14) * mm});
            skLineSegment(sketch, "E4751", {"start": v(48506.8, 60786.56) * mm, "end": v(48505.96, 60789.33) * mm});
            skLineSegment(sketch, "E4752", {"start": v(48490.65, 60784.7) * mm, "end": v(48491.49, 60781.92) * mm});
            skLineSegment(sketch, "E4753", {"start": v(48491.49, 60781.92) * mm, "end": v(48506.8, 60786.56) * mm});
            skLineSegment(sketch, "E4754", {"start": v(48505.96, 60789.33) * mm, "end": v(48503.58, 60797.21) * mm});
            skLineSegment(sketch, "E4755", {"start": v(48488.26, 60792.58) * mm, "end": v(48490.65, 60784.7) * mm});
            skLineSegment(sketch, "E4756", {"start": v(48503.58, 60797.21) * mm, "end": v(48500, 60809.01) * mm});
            skLineSegment(sketch, "E4757", {"start": v(48484.7, 60804.38) * mm, "end": v(48488.26, 60792.58) * mm});
            skLineSegment(sketch, "E4758", {"start": v(48500, 60809.01) * mm, "end": v(48491.58, 60836.85) * mm});
            skLineSegment(sketch, "E4759", {"start": v(48476.27, 60832.21) * mm, "end": v(48484.7, 60804.38) * mm});
            skLineSegment(sketch, "E4760", {"start": v(48491.58, 60836.85) * mm, "end": v(48488, 60848.65) * mm});
            skLineSegment(sketch, "E4761", {"start": v(48472.7, 60844.01) * mm, "end": v(48476.27, 60832.21) * mm});
            skLineSegment(sketch, "E4762", {"start": v(48488, 60848.65) * mm, "end": v(48485.62, 60856.53) * mm});
            skLineSegment(sketch, "E4763", {"start": v(48470.3, 60851.9) * mm, "end": v(48472.7, 60844.01) * mm});
            skLineSegment(sketch, "E4764", {"start": v(48485.62, 60856.53) * mm, "end": v(48484.79, 60859.3) * mm});
            skLineSegment(sketch, "E4765", {"start": v(48469.47, 60854.66) * mm, "end": v(48470.3, 60851.9) * mm});
            skLineSegment(sketch, "E4766", {"start": v(48483.73, 60861.07) * mm, "end": v(48486.5, 60861.9) * mm});
            skLineSegment(sketch, "E4767", {"start": v(48481.86, 60877.22) * mm, "end": v(48479.1, 60876.38) * mm});
            skLineSegment(sketch, "E4768", {"start": v(48486.5, 60861.9) * mm, "end": v(48494.38, 60864.3) * mm});
            skLineSegment(sketch, "E4769", {"start": v(48489.74, 60879.6) * mm, "end": v(48481.86, 60877.22) * mm});
            skLineSegment(sketch, "E4770", {"start": v(48494.38, 60864.3) * mm, "end": v(48506.18, 60867.87) * mm});
            skLineSegment(sketch, "E4771", {"start": v(48501.54, 60883.18) * mm, "end": v(48489.74, 60879.6) * mm});
            skLineSegment(sketch, "E4772", {"start": v(48506.18, 60867.87) * mm, "end": v(48545.82, 60879.86) * mm});
            skLineSegment(sketch, "E4773", {"start": v(48541.18, 60895.18) * mm, "end": v(48501.54, 60883.18) * mm});
            skLineSegment(sketch, "E4774", {"start": v(48545.82, 60879.86) * mm, "end": v(48553.7, 60882.25) * mm});
            skLineSegment(sketch, "E4775", {"start": v(48549.06, 60897.56) * mm, "end": v(48541.18, 60895.18) * mm});
            skLineSegment(sketch, "E4776", {"start": v(48553.7, 60882.25) * mm, "end": v(48556.47, 60883.09) * mm});
            skLineSegment(sketch, "E4777", {"start": v(48556.47, 60883.09) * mm, "end": v(48551.83, 60898.4) * mm});
            skLineSegment(sketch, "E4778", {"start": v(48551.83, 60898.4) * mm, "end": v(48549.06, 60897.56) * mm});
            skLineSegment(sketch, "E4779", {"start": v(48396.63, 60834.7) * mm, "end": v(48399.4, 60835.54) * mm});
            skLineSegment(sketch, "E4780", {"start": v(48394.76, 60850.86) * mm, "end": v(48392, 60850.02) * mm});
            skLineSegment(sketch, "E4781", {"start": v(48392, 60850.02) * mm, "end": v(48396.63, 60834.7) * mm});
            skLineSegment(sketch, "E4782", {"start": v(48399.4, 60835.54) * mm, "end": v(48407.28, 60837.93) * mm});
            skLineSegment(sketch, "E4783", {"start": v(48402.65, 60853.24) * mm, "end": v(48394.76, 60850.86) * mm});
            skLineSegment(sketch, "E4784", {"start": v(48407.28, 60837.93) * mm, "end": v(48419.08, 60841.5) * mm});
            skLineSegment(sketch, "E4785", {"start": v(48414.45, 60856.82) * mm, "end": v(48402.65, 60853.24) * mm});
            skLineSegment(sketch, "E4786", {"start": v(48419.08, 60841.5) * mm, "end": v(48433, 60845.72) * mm});
            skLineSegment(sketch, "E4787", {"start": v(48428.37, 60861.03) * mm, "end": v(48414.45, 60856.82) * mm});
            skLineSegment(sketch, "E4788", {"start": v(48433, 60845.72) * mm, "end": v(48446.92, 60849.93) * mm});
            skLineSegment(sketch, "E4789", {"start": v(48442.28, 60865.24) * mm, "end": v(48428.37, 60861.03) * mm});
            skLineSegment(sketch, "E4790", {"start": v(48446.92, 60849.93) * mm, "end": v(48458.72, 60853.5) * mm});
            skLineSegment(sketch, "E4791", {"start": v(48454.08, 60868.81) * mm, "end": v(48442.28, 60865.24) * mm});
            skLineSegment(sketch, "E4792", {"start": v(48458.72, 60853.5) * mm, "end": v(48466.6, 60855.89) * mm});
            skLineSegment(sketch, "E4793", {"start": v(48461.97, 60871.2) * mm, "end": v(48454.08, 60868.81) * mm});
            skLineSegment(sketch, "E4794", {"start": v(48466.6, 60855.89) * mm, "end": v(48483.73, 60861.07) * mm});
            skLineSegment(sketch, "E4795", {"start": v(48479.1, 60876.38) * mm, "end": v(48461.97, 60871.2) * mm});
            skLineSegment(sketch, "E4796", {"start": v(48507.36, 60795.09) * mm, "end": v(48516.63, 60764.46) * mm});
            skLineSegment(sketch, "E4797", {"start": v(48516.63, 60764.46) * mm, "end": v(48574.05, 60781.84) * mm});
            skLineSegment(sketch, "E4798", {"start": v(48574.05, 60781.84) * mm, "end": v(48547.4, 60869.9) * mm});
            skLineSegment(sketch, "E4799", {"start": v(48487.66, 60860.17) * mm, "end": v(48489.97, 60852.51) * mm});
            skLineSegment(sketch, "E4800", {"start": v(48547.4, 60869.9) * mm, "end": v(48545.08, 60877.55) * mm});
            skLineSegment(sketch, "E4801", {"start": v(48545.08, 60877.55) * mm, "end": v(48487.66, 60860.17) * mm});
            skLineSegment(sketch, "E4802", {"start": v(48489.97, 60852.51) * mm, "end": v(48507.36, 60795.09) * mm});
            skLineSegment(sketch, "E4803", {"start": v(48760.55, 59958.56) * mm, "end": v(48762.87, 59950.9) * mm});
            skLineSegment(sketch, "E4804", {"start": v(48762.87, 59950.9) * mm, "end": v(48820.3, 59968.29) * mm});
            skLineSegment(sketch, "E4805", {"start": v(48820.3, 59968.29) * mm, "end": v(48817.98, 59975.95) * mm});
            skLineSegment(sketch, "E4806", {"start": v(48733.9, 60046.62) * mm, "end": v(48743.17, 60016) * mm});
            skLineSegment(sketch, "E4807", {"start": v(48817.98, 59975.95) * mm, "end": v(48791.33, 60064) * mm});
            skLineSegment(sketch, "E4808", {"start": v(48791.33, 60064) * mm, "end": v(48733.9, 60046.62) * mm});
            skLineSegment(sketch, "E4809", {"start": v(48743.17, 60016) * mm, "end": v(48760.55, 59958.56) * mm});
            skLineSegment(sketch, "E4810", {"start": v(48722.67, 60018.14) * mm, "end": v(48723.5, 60015.38) * mm});
            skLineSegment(sketch, "E4811", {"start": v(48738.82, 60020.01) * mm, "end": v(48737.98, 60022.78) * mm});
            skLineSegment(sketch, "E4812", {"start": v(48737.98, 60022.78) * mm, "end": v(48722.67, 60018.14) * mm});
            skLineSegment(sketch, "E4813", {"start": v(48723.5, 60015.38) * mm, "end": v(48725.9, 60007.5) * mm});
            skLineSegment(sketch, "E4814", {"start": v(48741.2, 60012.13) * mm, "end": v(48738.82, 60020.01) * mm});
            skLineSegment(sketch, "E4815", {"start": v(48725.9, 60007.5) * mm, "end": v(48729.47, 59995.7) * mm});
            skLineSegment(sketch, "E4816", {"start": v(48753.2, 59972.5) * mm, "end": v(48741.2, 60012.13) * mm});
            skLineSegment(sketch, "E4817", {"start": v(48729.47, 59995.7) * mm, "end": v(48741.46, 59956.06) * mm});
            skLineSegment(sketch, "E4818", {"start": v(48756.78, 59960.7) * mm, "end": v(48753.2, 59972.5) * mm});
            skLineSegment(sketch, "E4819", {"start": v(48741.46, 59956.06) * mm, "end": v(48743.85, 59948.17) * mm});
            skLineSegment(sketch, "E4820", {"start": v(48759.16, 59952.8) * mm, "end": v(48756.78, 59960.7) * mm});
            skLineSegment(sketch, "E4821", {"start": v(48743.85, 59948.17) * mm, "end": v(48744.69, 59945.4) * mm});
            skLineSegment(sketch, "E4822", {"start": v(48760, 59950.04) * mm, "end": v(48759.16, 59952.8) * mm});
            skLineSegment(sketch, "E4823", {"start": v(48745.74, 59943.63) * mm, "end": v(48742.98, 59942.8) * mm});
            skLineSegment(sketch, "E4824", {"start": v(48747.61, 59927.48) * mm, "end": v(48750.38, 59928.32) * mm});
            skLineSegment(sketch, "E4825", {"start": v(48742.98, 59942.8) * mm, "end": v(48735.1, 59940.4) * mm});
            skLineSegment(sketch, "E4826", {"start": v(48739.73, 59925.1) * mm, "end": v(48747.61, 59927.48) * mm});
            skLineSegment(sketch, "E4827", {"start": v(48735.1, 59940.4) * mm, "end": v(48723.3, 59936.84) * mm});
            skLineSegment(sketch, "E4828", {"start": v(48727.93, 59921.52) * mm, "end": v(48739.73, 59925.1) * mm});
            skLineSegment(sketch, "E4829", {"start": v(48723.3, 59936.84) * mm, "end": v(48709.37, 59932.63) * mm});
            skLineSegment(sketch, "E4830", {"start": v(48714, 59917.31) * mm, "end": v(48727.93, 59921.52) * mm});
            skLineSegment(sketch, "E4831", {"start": v(48709.37, 59932.63) * mm, "end": v(48695.46, 59928.41) * mm});
            skLineSegment(sketch, "E4832", {"start": v(48700.1, 59913.1) * mm, "end": v(48714, 59917.31) * mm});
            skLineSegment(sketch, "E4833", {"start": v(48695.46, 59928.41) * mm, "end": v(48683.66, 59924.84) * mm});
            skLineSegment(sketch, "E4834", {"start": v(48688.3, 59909.53) * mm, "end": v(48700.1, 59913.1) * mm});
            skLineSegment(sketch, "E4835", {"start": v(48683.66, 59924.84) * mm, "end": v(48675.77, 59922.45) * mm});
            skLineSegment(sketch, "E4836", {"start": v(48680.4, 59907.14) * mm, "end": v(48688.3, 59909.53) * mm});
            skLineSegment(sketch, "E4837", {"start": v(48675.77, 59922.45) * mm, "end": v(48673, 59921.62) * mm});
            skLineSegment(sketch, "E4838", {"start": v(48673, 59921.62) * mm, "end": v(48677.64, 59906.3) * mm});
            skLineSegment(sketch, "E4839", {"start": v(48677.64, 59906.3) * mm, "end": v(48680.4, 59907.14) * mm});
            skLineSegment(sketch, "E4840", {"start": v(48837.48, 59954.68) * mm, "end": v(48832.84, 59970) * mm});
            skLineSegment(sketch, "E4841", {"start": v(48832.84, 59970) * mm, "end": v(48770.75, 59951.2) * mm});
            skLineSegment(sketch, "E4842", {"start": v(48775.39, 59935.89) * mm, "end": v(48837.48, 59954.68) * mm});
            skLineSegment(sketch, "E4843", {"start": v(48770.75, 59951.2) * mm, "end": v(48762.87, 59948.82) * mm});
            skLineSegment(sketch, "E4844", {"start": v(48767.5, 59933.5) * mm, "end": v(48775.39, 59935.89) * mm});
            skLineSegment(sketch, "E4845", {"start": v(48762.87, 59948.82) * mm, "end": v(48745.74, 59943.63) * mm});
            skLineSegment(sketch, "E4846", {"start": v(48750.38, 59928.32) * mm, "end": v(48767.5, 59933.5) * mm});
            skLineSegment(sketch, "E4847", {"start": v(48722.12, 60009.62) * mm, "end": v(48712.85, 60040.25) * mm});
            skLineSegment(sketch, "E4848", {"start": v(48712.85, 60040.25) * mm, "end": v(48655.42, 60022.86) * mm});
            skLineSegment(sketch, "E4849", {"start": v(48655.42, 60022.86) * mm, "end": v(48682.07, 59934.8) * mm});
            skLineSegment(sketch, "E4850", {"start": v(48741.82, 59944.53) * mm, "end": v(48739.5, 59952.2) * mm});
            skLineSegment(sketch, "E4851", {"start": v(48682.07, 59934.8) * mm, "end": v(48684.39, 59927.15) * mm});
            skLineSegment(sketch, "E4852", {"start": v(48684.39, 59927.15) * mm, "end": v(48741.82, 59944.53) * mm});
            skLineSegment(sketch, "E4853", {"start": v(48739.5, 59952.2) * mm, "end": v(48722.12, 60009.62) * mm});
            skLineSegment(sketch, "E4854", {"start": v(48573.32, 59482.93) * mm, "end": v(48100.24, 61045.9) * mm});
            skLineSegment(sketch, "E4855", {"start": v(46988.33, 59003.18) * mm, "end": v(48573.32, 59482.93) * mm});
            skLineSegment(sketch, "E4856", {"start": v(46827.27, 60660.6) * mm, "end": v(46808.73, 60721.85) * mm});
            skLineSegment(sketch, "E4857", {"start": v(46518.12, 60567.02) * mm, "end": v(46827.27, 60660.6) * mm});
            skLineSegment(sketch, "E4858", {"start": v(46515.25, 60566.15) * mm, "end": v(46988.33, 59003.18) * mm});
            skLineSegment(sketch, "E4859", {"start": v(47765.85, 61011.55) * mm, "end": v(47784.39, 60950.3) * mm});
            skLineSegment(sketch, "E4860", {"start": v(47784.39, 60950.3) * mm, "end": v(48097.37, 61045.03) * mm});
            skLineSegment(sketch, "E4861", {"start": v(47783.95, 60951.73) * mm, "end": v(46826.84, 60662.03) * mm});
            skLineSegment(sketch, "E4862", {"start": v(48600.75, 59468.24) * mm, "end": v(48121.3, 61052.27) * mm});
            skLineSegment(sketch, "E4863", {"start": v(48121.3, 61052.27) * mm, "end": v(48100.24, 61045.9) * mm});
            skLineSegment(sketch, "E4864", {"start": v(46515.25, 60566.15) * mm, "end": v(46494.2, 60559.78) * mm});
            skLineSegment(sketch, "E4865", {"start": v(46494.2, 60559.78) * mm, "end": v(46973.65, 58975.75) * mm});
            skLineSegment(sketch, "E4866", {"start": v(46973.65, 58975.75) * mm, "end": v(48600.75, 59468.24) * mm});
            skLineSegment(sketch, "E4867", {"start": v(48775.35, 59899.31) * mm, "end": v(48765.22, 59932.81) * mm});
            skLineSegment(sketch, "E4868", {"start": v(48760.58, 59948.12) * mm, "end": v(48760, 59950.04) * mm});
            skLineSegment(sketch, "E4869", {"start": v(48744.69, 59945.4) * mm, "end": v(48745.27, 59943.49) * mm});
            skLineSegment(sketch, "E4870", {"start": v(48749.9, 59928.18) * mm, "end": v(48760.04, 59894.68) * mm});
            skLineSegment(sketch, "E4871", {"start": v(48812.9, 59901.27) * mm, "end": v(48810.29, 59909.89) * mm});
            skLineSegment(sketch, "E4872", {"start": v(48810.29, 59909.89) * mm, "end": v(48775.35, 59899.31) * mm});
            skLineSegment(sketch, "E4873", {"start": v(48760.04, 59894.68) * mm, "end": v(48725.1, 59884.1) * mm});
            skLineSegment(sketch, "E4874", {"start": v(48725.1, 59884.1) * mm, "end": v(48727.71, 59875.49) * mm});
            skLineSegment(sketch, "E4875", {"start": v(48727.71, 59875.49) * mm, "end": v(48812.9, 59901.27) * mm});
            skLineSegment(sketch, "E4876", {"start": v(48454.12, 60905.4) * mm, "end": v(48464.26, 60871.9) * mm});
            skLineSegment(sketch, "E4877", {"start": v(48468.9, 60856.58) * mm, "end": v(48469.47, 60854.66) * mm});
            skLineSegment(sketch, "E4878", {"start": v(48484.79, 60859.3) * mm, "end": v(48484.2, 60861.21) * mm});
            skLineSegment(sketch, "E4879", {"start": v(48479.57, 60876.53) * mm, "end": v(48469.43, 60910.03) * mm});
            skLineSegment(sketch, "E4880", {"start": v(48501.76, 60929.22) * mm, "end": v(48416.58, 60903.43) * mm});
            skLineSegment(sketch, "E4881", {"start": v(48416.58, 60903.43) * mm, "end": v(48419.18, 60894.82) * mm});
            skLineSegment(sketch, "E4882", {"start": v(48419.18, 60894.82) * mm, "end": v(48454.12, 60905.4) * mm});
            skLineSegment(sketch, "E4883", {"start": v(48469.43, 60910.03) * mm, "end": v(48504.37, 60920.6) * mm});
            skLineSegment(sketch, "E4884", {"start": v(48504.37, 60920.6) * mm, "end": v(48501.76, 60929.22) * mm});
            skLineSegment(sketch, "E4885", {"start": v(46616.68, 59789.22) * mm, "end": v(46694.2, 59812.69) * mm});
            skLineSegment(sketch, "E4886", {"start": v(46689.57, 59828) * mm, "end": v(46612.04, 59804.54) * mm});
            skLineSegment(sketch, "E4887", {"start": v(46588.3, 59855.34) * mm, "end": v(46625.1, 59733.78) * mm});
            skLineSegment(sketch, "E4888", {"start": v(46625.1, 59733.78) * mm, "end": v(46632.76, 59736.1) * mm});
            skLineSegment(sketch, "E4889", {"start": v(46632.76, 59736.1) * mm, "end": v(46616.68, 59789.22) * mm});
            skLineSegment(sketch, "E4890", {"start": v(46612.04, 59804.54) * mm, "end": v(46595.96, 59857.66) * mm});
            skLineSegment(sketch, "E4891", {"start": v(46595.96, 59857.66) * mm, "end": v(46588.3, 59855.34) * mm});
            skLineSegment(sketch, "E4892", {"start": v(48442.05, 60358.44) * mm, "end": v(48364.52, 60334.98) * mm});
            skLineSegment(sketch, "E4893", {"start": v(48364.52, 60334.98) * mm, "end": v(48369.16, 60319.66) * mm});
            skLineSegment(sketch, "E4894", {"start": v(48369.16, 60319.66) * mm, "end": v(48446.69, 60343.13) * mm});
            skLineSegment(sketch, "E4895", {"start": v(48433.63, 60413.88) * mm, "end": v(48425.97, 60411.56) * mm});
            skLineSegment(sketch, "E4896", {"start": v(48425.97, 60411.56) * mm, "end": v(48442.05, 60358.44) * mm});
            skLineSegment(sketch, "E4897", {"start": v(48446.69, 60343.13) * mm, "end": v(48462.77, 60290) * mm});
            skLineSegment(sketch, "E4898", {"start": v(48462.77, 60290) * mm, "end": v(48470.42, 60292.33) * mm});
            skLineSegment(sketch, "E4899", {"start": v(48470.42, 60292.33) * mm, "end": v(48433.63, 60413.88) * mm});
            skLineSegment(sketch, "E4900", {"start": v(48318.8, 60931.3) * mm, "end": v(48339.86, 60937.68) * mm});
            skLineSegment(sketch, "E4901", {"start": v(48334.74, 60878.66) * mm, "end": v(48622.83, 60965.86) * mm});
            skLineSegment(sketch, "E4902", {"start": v(48621.1, 60971.6) * mm, "end": v(48622.83, 60965.86) * mm});
            skLineSegment(sketch, "E4903", {"start": v(48661.81, 59798.08) * mm, "end": v(48682.87, 59804.45) * mm});
            skLineSegment(sketch, "E4904", {"start": v(48645.88, 59850.72) * mm, "end": v(48933.97, 59937.92) * mm});
            skLineSegment(sketch, "E4905", {"start": v(48341.87, 60941.42) * mm, "end": v(48424.18, 60966.33) * mm});
            skArc(sketch, "E4906", {"start": v(48424.18, 60966.33) * mm, "mid": v(48447.86, 60985.74) * mm, "end": v(48450.88, 61016.2) * mm});
            skLineSegment(sketch, "E4907", {"start": v(48450.88, 61016.2) * mm, "end": v(48445.66, 61033.43) * mm});
            skLineSegment(sketch, "E4908", {"start": v(48445.66, 61033.43) * mm, "end": v(48449, 61039.67) * mm});
            skLineSegment(sketch, "E4909", {"start": v(48449, 61039.67) * mm, "end": v(48609.8, 61088.34) * mm});
            skLineSegment(sketch, "E4910", {"start": v(48609.8, 61088.34) * mm, "end": v(48643.1, 60978.27) * mm});
            skLineSegment(sketch, "E4911", {"start": v(48643.1, 60978.27) * mm, "end": v(48356.93, 60891.65) * mm});
            skLineSegment(sketch, "E4912", {"start": v(48356.93, 60891.65) * mm, "end": v(48350.7, 60894.98) * mm});
            skLineSegment(sketch, "E4913", {"start": v(48350.7, 60894.98) * mm, "end": v(48338.53, 60935.18) * mm});
            skLineSegment(sketch, "E4914", {"start": v(48338.53, 60935.18) * mm, "end": v(48341.87, 60941.42) * mm});
            skLineSegment(sketch, "E4915", {"start": v(48639.28, 60977.1) * mm, "end": v(48605.97, 61087.18) * mm});
            skLineSegment(sketch, "E4916", {"start": v(48686.61, 59802.45) * mm, "end": v(48768.92, 59827.36) * mm});
            skArc(sketch, "E4917", {"start": v(48768.92, 59827.36) * mm, "mid": v(48799.39, 59824.34) * mm, "end": v(48818.8, 59800.67) * mm});
            skLineSegment(sketch, "E4918", {"start": v(48818.8, 59800.67) * mm, "end": v(48824, 59783.44) * mm});
            skLineSegment(sketch, "E4919", {"start": v(48824, 59783.44) * mm, "end": v(48830.24, 59780.1) * mm});
            skLineSegment(sketch, "E4920", {"start": v(48830.24, 59780.1) * mm, "end": v(48991.04, 59828.77) * mm});
            skLineSegment(sketch, "E4921", {"start": v(48991.04, 59828.77) * mm, "end": v(48957.72, 59938.84) * mm});
            skLineSegment(sketch, "E4922", {"start": v(48957.72, 59938.84) * mm, "end": v(48671.55, 59852.22) * mm});
            skLineSegment(sketch, "E4923", {"start": v(48671.55, 59852.22) * mm, "end": v(48668.2, 59845.98) * mm});
            skLineSegment(sketch, "E4924", {"start": v(48668.2, 59845.98) * mm, "end": v(48680.38, 59805.79) * mm});
            skLineSegment(sketch, "E4925", {"start": v(48680.38, 59805.79) * mm, "end": v(48686.61, 59802.45) * mm});
            skLineSegment(sketch, "E4926", {"start": v(48953.9, 59937.68) * mm, "end": v(48987.21, 59827.61) * mm});
            skLineSegment(sketch, "E4927", {"start": v(48279.22, 60924.02) * mm, "end": v(48624.83, 59782.18) * mm});
            skLineSegment(sketch, "E4928", {"start": v(48624.83, 59782.18) * mm, "end": v(48663.12, 59793.77) * mm});
            skLineSegment(sketch, "E4929", {"start": v(48663.12, 59793.77) * mm, "end": v(48317.5, 60935.61) * mm});
            skLineSegment(sketch, "E4930", {"start": v(48317.5, 60935.61) * mm, "end": v(48279.22, 60924.02) * mm});
            skLineSegment(sketch, "E4931", {"start": v(48226.41, 61345.3) * mm, "end": v(47793.32, 61214.2) * mm});
            skLineSegment(sketch, "E4932", {"start": v(47711.96, 61189.58) * mm, "end": v(46754.85, 60899.88) * mm});
            skLineSegment(sketch, "E4933", {"start": v(46673.01, 60875.1) * mm, "end": v(46244.22, 60745.32) * mm});
            skLineSegment(sketch, "E4934", {"start": v(46244.22, 60745.32) * mm, "end": v(46276.1, 60640.04) * mm});
            skLineSegment(sketch, "E4935", {"start": v(46276.1, 60640.04) * mm, "end": v(48258.28, 61240) * mm});
            skLineSegment(sketch, "E4936", {"start": v(48258.28, 61240) * mm, "end": v(48226.41, 61345.3) * mm});
            skLineSegment(sketch, "E4937", {"start": v(47759.17, 61137) * mm, "end": v(47253.9, 60984.06) * mm});
            skLineSegment(sketch, "E4938", {"start": v(47253.9, 60984.06) * mm, "end": v(47265.2, 60946.74) * mm});
            skLineSegment(sketch, "E4939", {"start": v(47265.2, 60946.74) * mm, "end": v(47770.47, 61099.67) * mm});
            skLineSegment(sketch, "E4940", {"start": v(47770.47, 61099.67) * mm, "end": v(47759.17, 61137) * mm});
            skLineSegment(sketch, "E4941", {"start": v(47253.81, 60984.04) * mm, "end": v(46744.72, 60829.94) * mm});
            skLineSegment(sketch, "E4942", {"start": v(46744.72, 60829.94) * mm, "end": v(46756.02, 60792.62) * mm});
            skLineSegment(sketch, "E4943", {"start": v(46756.02, 60792.62) * mm, "end": v(47265.11, 60946.7) * mm});
            skLineSegment(sketch, "E4944", {"start": v(47265.11, 60946.7) * mm, "end": v(47253.81, 60984.04) * mm});
            skLineSegment(sketch, "E4945", {"start": v(48263.62, 61210.28) * mm, "end": v(46288.13, 60612.34) * mm});
            skLineSegment(sketch, "E4946", {"start": v(46288.13, 60612.34) * mm, "end": v(46320, 60507.06) * mm});
            skLineSegment(sketch, "E4947", {"start": v(46320, 60507.06) * mm, "end": v(46567.9, 60582.09) * mm});
            skLineSegment(sketch, "E4948", {"start": v(47961.46, 61003.9) * mm, "end": v(48295.49, 61105) * mm});
            skLineSegment(sketch, "E4949", {"start": v(48295.49, 61105) * mm, "end": v(48263.62, 61210.28) * mm});
            skLineSegment(sketch, "E4950", {"start": v(47780.91, 61060) * mm, "end": v(47277.08, 60907.5) * mm});
            skLineSegment(sketch, "E4951", {"start": v(47277.08, 60907.5) * mm, "end": v(47288.67, 60869.21) * mm});
            skLineSegment(sketch, "E4952", {"start": v(47288.67, 60869.21) * mm, "end": v(47792.5, 61021.7) * mm});
            skLineSegment(sketch, "E4953", {"start": v(47792.5, 61021.7) * mm, "end": v(47780.91, 61060) * mm});
            skLineSegment(sketch, "E4954", {"start": v(47276.99, 60907.47) * mm, "end": v(46769.33, 60753.8) * mm});
            skLineSegment(sketch, "E4955", {"start": v(46769.33, 60753.8) * mm, "end": v(46780.92, 60715.53) * mm});
            skLineSegment(sketch, "E4956", {"start": v(46780.92, 60715.53) * mm, "end": v(47288.58, 60869.18) * mm});
            skLineSegment(sketch, "E4957", {"start": v(47288.58, 60869.18) * mm, "end": v(47276.99, 60907.47) * mm});
            skLineSegment(sketch, "E4958", {"start": v(46507.27, 59722.67) * mm, "end": v(46504.95, 59730.33) * mm});
            skLineSegment(sketch, "E4959", {"start": v(46504.95, 59730.33) * mm, "end": v(46465.26, 59861.45) * mm});
            skLineSegment(sketch, "E4960", {"start": v(46465.26, 59861.45) * mm, "end": v(46468.6, 59867.69) * mm});
            skLineSegment(sketch, "E4961", {"start": v(46468.6, 59867.69) * mm, "end": v(46549.95, 59892.31) * mm});
            skLineSegment(sketch, "E4962", {"start": v(46549.95, 59892.31) * mm, "end": v(46613.69, 59681.75) * mm});
            skLineSegment(sketch, "E4963", {"start": v(46613.69, 59681.75) * mm, "end": v(46532.33, 59657.12) * mm});
            skLineSegment(sketch, "E4964", {"start": v(46532.33, 59657.12) * mm, "end": v(46526.1, 59660.46) * mm});
            skLineSegment(sketch, "E4965", {"start": v(46526.1, 59660.46) * mm, "end": v(46509.58, 59715.01) * mm});
            skLineSegment(sketch, "E4966", {"start": v(46509.58, 59715.01) * mm, "end": v(46507.27, 59722.67) * mm});
            skLineSegment(sketch, "E4967", {"start": v(46568.7, 59668.13) * mm, "end": v(46573.05, 59653.77) * mm});
            skLineSegment(sketch, "E4968", {"start": v(46573.05, 59653.77) * mm, "end": v(46556.36, 59622.6) * mm});
            skLineSegment(sketch, "E4969", {"start": v(46556.36, 59622.6) * mm, "end": v(46494.15, 59603.77) * mm});
            skLineSegment(sketch, "E4970", {"start": v(46494.15, 59603.77) * mm, "end": v(46407.24, 59890.9) * mm});
            skLineSegment(sketch, "E4971", {"start": v(46407.24, 59890.9) * mm, "end": v(46469.45, 59909.74) * mm});
            skLineSegment(sketch, "E4972", {"start": v(46469.45, 59909.74) * mm, "end": v(46500.62, 59893.05) * mm});
            skLineSegment(sketch, "E4973", {"start": v(46500.62, 59893.05) * mm, "end": v(46504.97, 59878.7) * mm});
            skLineSegment(sketch, "E4974", {"start": v(46689.57, 59828) * mm, "end": v(46694.2, 59812.69) * mm});
            skLineSegment(sketch, "E4975", {"start": v(46131.53, 59226.02) * mm, "end": v(46133.93, 59226.75) * mm});
            skLineSegment(sketch, "E4976", {"start": v(46135.66, 59221) * mm, "end": v(46111.74, 59213.76) * mm});
            skLineSegment(sketch, "E4977", {"start": v(46111.74, 59213.76) * mm, "end": v(45806.1, 60223.52) * mm});
            skLineSegment(sketch, "E4978", {"start": v(45806.1, 60223.52) * mm, "end": v(45830.03, 60230.76) * mm});
            skLineSegment(sketch, "E4979", {"start": v(45830.03, 60230.76) * mm, "end": v(46135.66, 59221) * mm});
            skLineSegment(sketch, "E4980", {"start": v(45846.62, 60241.53) * mm, "end": v(46012.2, 60291.65) * mm});
            skLineSegment(sketch, "E4981", {"start": v(46012.2, 60291.65) * mm, "end": v(46000.61, 60329.94) * mm});
            skLineSegment(sketch, "E4982", {"start": v(46000.61, 60329.94) * mm, "end": v(45988.15, 60336.6) * mm});
            skLineSegment(sketch, "E4983", {"start": v(45988.15, 60336.6) * mm, "end": v(45841.7, 60292.29) * mm});
            skLineSegment(sketch, "E4984", {"start": v(45841.7, 60292.29) * mm, "end": v(45835.03, 60279.82) * mm});
            skLineSegment(sketch, "E4985", {"start": v(45835.03, 60279.82) * mm, "end": v(45846.62, 60241.53) * mm});
            skLineSegment(sketch, "E4986", {"start": v(46155.44, 59221.25) * mm, "end": v(46321.02, 59271.36) * mm});
            skLineSegment(sketch, "E4987", {"start": v(46321.02, 59271.36) * mm, "end": v(46332.61, 59233.08) * mm});
            skLineSegment(sketch, "E4988", {"start": v(46332.61, 59233.08) * mm, "end": v(46325.94, 59220.61) * mm});
            skLineSegment(sketch, "E4989", {"start": v(46325.94, 59220.61) * mm, "end": v(46179.5, 59176.29) * mm});
            skLineSegment(sketch, "E4990", {"start": v(46179.5, 59176.29) * mm, "end": v(46167.03, 59182.96) * mm});
            skLineSegment(sketch, "E4991", {"start": v(46167.03, 59182.96) * mm, "end": v(46155.44, 59221.25) * mm});
            skLineSegment(sketch, "E4992", {"start": v(45930.58, 59791.56) * mm, "end": v(45975.77, 59642.25) * mm});
            skLineSegment(sketch, "E4993", {"start": v(45975.77, 59642.25) * mm, "end": v(45981.52, 59643.99) * mm});
            skLineSegment(sketch, "E4994", {"start": v(45981.52, 59643.99) * mm, "end": v(45936.32, 59793.3) * mm});
            skLineSegment(sketch, "E4995", {"start": v(45936.32, 59793.3) * mm, "end": v(45930.58, 59791.56) * mm});
            skLineSegment(sketch, "E4996", {"start": v(46027.41, 60417.45) * mm, "end": v(46059.28, 60312.17) * mm});
            skLineSegment(sketch, "E4997", {"start": v(46033.15, 60419.19) * mm, "end": v(46065.02, 60313.9) * mm});
            skLineSegment(sketch, "E4998", {"start": v(46008.09, 60349.88) * mm, "end": v(46027.49, 60386.13) * mm});
            skLineSegment(sketch, "E4999", {"start": v(46027.49, 60386.13) * mm, "end": v(46021.4, 60406.23) * mm});
            skLineSegment(sketch, "E5000", {"start": v(46021.4, 60406.23) * mm, "end": v(46027.41, 60417.45) * mm});
            skLineSegment(sketch, "E5001", {"start": v(46027.41, 60417.45) * mm, "end": v(46037.94, 60420.64) * mm});
            skLineSegment(sketch, "E5002", {"start": v(46037.94, 60420.64) * mm, "end": v(46069.8, 60315.35) * mm});
            skLineSegment(sketch, "E5003", {"start": v(46069.8, 60315.35) * mm, "end": v(45884.13, 60259.15) * mm});
            skLineSegment(sketch, "E5004", {"start": v(45884.13, 60259.15) * mm, "end": v(45872.9, 60265.16) * mm});
            skLineSegment(sketch, "E5005", {"start": v(45872.9, 60265.16) * mm, "end": v(45864.21, 60293.87) * mm});
            skLineSegment(sketch, "E5006", {"start": v(45864.21, 60293.87) * mm, "end": v(45870.22, 60305.1) * mm});
            skLineSegment(sketch, "E5007", {"start": v(45870.22, 60305.1) * mm, "end": v(46002.17, 60345.03) * mm});
            skArc(sketch, "E5008", {"start": v(46002.17, 60345.03) * mm, "mid": v(46005.6, 60346.87) * mm, "end": v(46008.09, 60349.88) * mm});
            skLineSegment(sketch, "E5009", {"start": v(46403.44, 59175.11) * mm, "end": v(46371.57, 59280.4) * mm});
            skLineSegment(sketch, "E5010", {"start": v(46409.18, 59176.85) * mm, "end": v(46377.32, 59282.13) * mm});
            skLineSegment(sketch, "E5011", {"start": v(46349.9, 59220.62) * mm, "end": v(46386.14, 59201.22) * mm});
            skLineSegment(sketch, "E5012", {"start": v(46386.14, 59201.22) * mm, "end": v(46392.22, 59181.12) * mm});
            skLineSegment(sketch, "E5013", {"start": v(46392.22, 59181.12) * mm, "end": v(46403.44, 59175.11) * mm});
            skLineSegment(sketch, "E5014", {"start": v(46403.44, 59175.11) * mm, "end": v(46413.97, 59178.3) * mm});
            skLineSegment(sketch, "E5015", {"start": v(46413.97, 59178.3) * mm, "end": v(46382.1, 59283.58) * mm});
            skLineSegment(sketch, "E5016", {"start": v(46382.1, 59283.58) * mm, "end": v(46196.42, 59227.38) * mm});
            skLineSegment(sketch, "E5017", {"start": v(46196.42, 59227.38) * mm, "end": v(46190.42, 59216.16) * mm});
            skLineSegment(sketch, "E5018", {"start": v(46190.42, 59216.16) * mm, "end": v(46199.1, 59187.45) * mm});
            skLineSegment(sketch, "E5019", {"start": v(46199.1, 59187.45) * mm, "end": v(46210.33, 59181.44) * mm});
            skLineSegment(sketch, "E5020", {"start": v(46210.33, 59181.44) * mm, "end": v(46342.27, 59221.38) * mm});
            skArc(sketch, "E5021", {"start": v(46342.27, 59221.38) * mm, "mid": v(46346.16, 59221.76) * mm, "end": v(46349.9, 59220.62) * mm});
            skLineSegment(sketch, "E5022", {"start": v(46239.06, 59338.5) * mm, "end": v(46149.1, 59311.27) * mm});
            skLineSegment(sketch, "E5023", {"start": v(46239.06, 59338.5) * mm, "end": v(45981.23, 60190.33) * mm});
            skLineSegment(sketch, "E5024", {"start": v(45891.26, 60163.1) * mm, "end": v(46149.1, 59311.27) * mm});
            skLineSegment(sketch, "E5025", {"start": v(45915.24, 60083.87) * mm, "end": v(45905.4, 60062.9) * mm});
            skLineSegment(sketch, "E5026", {"start": v(45905.4, 60062.9) * mm, "end": v(46105.29, 59402.49) * mm});
            skLineSegment(sketch, "E5027", {"start": v(46105.29, 59402.49) * mm, "end": v(46125.1, 59390.5) * mm});
            skLineSegment(sketch, "E5028", {"start": v(46215.08, 59417.73) * mm, "end": v(46224.93, 59438.7) * mm});
            skLineSegment(sketch, "E5029", {"start": v(46224.93, 59438.7) * mm, "end": v(46025.03, 60099.11) * mm});
            skLineSegment(sketch, "E5030", {"start": v(46025.03, 60099.11) * mm, "end": v(46005.2, 60111.1) * mm});
            skLineSegment(sketch, "E5031", {"start": v(45931.94, 60175.41) * mm, "end": v(45917.45, 60223.27) * mm});
            skLineSegment(sketch, "E5032", {"start": v(45917.45, 60223.27) * mm, "end": v(45888.74, 60214.58) * mm});
            skLineSegment(sketch, "E5033", {"start": v(45888.74, 60214.58) * mm, "end": v(45903.22, 60166.72) * mm});
            skLineSegment(sketch, "E5034", {"start": v(45969.26, 60186.71) * mm, "end": v(45954.78, 60234.57) * mm});
            skLineSegment(sketch, "E5035", {"start": v(45954.78, 60234.57) * mm, "end": v(45926.06, 60225.88) * mm});
            skLineSegment(sketch, "E5036", {"start": v(45926.06, 60225.88) * mm, "end": v(45940.55, 60178.02) * mm});
            skLineSegment(sketch, "E5037", {"start": v(46175.54, 59267.03) * mm, "end": v(46204.25, 59275.72) * mm});
            skLineSegment(sketch, "E5038", {"start": v(46204.25, 59275.72) * mm, "end": v(46189.77, 59323.58) * mm});
            skLineSegment(sketch, "E5039", {"start": v(46189.77, 59323.58) * mm, "end": v(46161.05, 59314.89) * mm});
            skLineSegment(sketch, "E5040", {"start": v(46161.05, 59314.89) * mm, "end": v(46175.54, 59267.03) * mm});
            skLineSegment(sketch, "E5041", {"start": v(46212.87, 59278.33) * mm, "end": v(46241.58, 59287.02) * mm});
            skLineSegment(sketch, "E5042", {"start": v(46241.58, 59287.02) * mm, "end": v(46227.1, 59334.88) * mm});
            skLineSegment(sketch, "E5043", {"start": v(46227.1, 59334.88) * mm, "end": v(46198.38, 59326.19) * mm});
            skLineSegment(sketch, "E5044", {"start": v(46198.38, 59326.19) * mm, "end": v(46212.87, 59278.33) * mm});
            skLineSegment(sketch, "E5045", {"start": v(46076.57, 58967.51) * mm, "end": v(45669.68, 60311.79) * mm});
            skLineSegment(sketch, "E5046", {"start": v(45018, 58647.1) * mm, "end": v(46076.57, 58967.51) * mm});
            skLineSegment(sketch, "E5047", {"start": v(44764.66, 60036.29) * mm, "end": v(44746.12, 60097.54) * mm});
            skLineSegment(sketch, "E5048", {"start": v(44614.42, 59990.81) * mm, "end": v(44764.66, 60036.29) * mm});
            skLineSegment(sketch, "E5049", {"start": v(44611.54, 59989.94) * mm, "end": v(45018, 58647.1) * mm});
            skLineSegment(sketch, "E5050", {"start": v(45669.68, 60311.79) * mm, "end": v(44764.22, 60037.72) * mm});
            skLineSegment(sketch, "E5051", {"start": v(46104, 58952.83) * mm, "end": v(45691.17, 60316.72) * mm});
            skLineSegment(sketch, "E5052", {"start": v(45691.17, 60316.72) * mm, "end": v(45670.12, 60310.35) * mm});
            skLineSegment(sketch, "E5053", {"start": v(44611.54, 59989.94) * mm, "end": v(44590.49, 59983.57) * mm});
            skLineSegment(sketch, "E5054", {"start": v(44590.49, 59983.57) * mm, "end": v(44865.7, 59074.3) * mm});
            skLineSegment(sketch, "E5055", {"start": v(44865.7, 59074.3) * mm, "end": v(45003.31, 58619.68) * mm});
            skLineSegment(sketch, "E5056", {"start": v(45003.31, 58619.68) * mm, "end": v(46104, 58952.83) * mm});
            skLineSegment(sketch, "E5057", {"start": v(45909.05, 60251.02) * mm, "end": v(45926.14, 60194.55) * mm});
            skLineSegment(sketch, "E5058", {"start": v(45934.76, 60197.16) * mm, "end": v(45917.66, 60253.63) * mm});
            skLineSegment(sketch, "E5059", {"start": v(45953.34, 60273.83) * mm, "end": v(45868.16, 60248.05) * mm});
            skLineSegment(sketch, "E5060", {"start": v(45868.16, 60248.05) * mm, "end": v(45870.76, 60239.44) * mm});
            skLineSegment(sketch, "E5061", {"start": v(45870.76, 60239.44) * mm, "end": v(45909.05, 60251.02) * mm});
            skLineSegment(sketch, "E5062", {"start": v(45917.66, 60253.63) * mm, "end": v(45955.95, 60265.22) * mm});
            skLineSegment(sketch, "E5063", {"start": v(45955.95, 60265.22) * mm, "end": v(45953.34, 60273.83) * mm});
            skLineSegment(sketch, "E5064", {"start": v(46221.27, 59250.57) * mm, "end": v(46204.18, 59307.04) * mm});
            skLineSegment(sketch, "E5065", {"start": v(46195.56, 59304.44) * mm, "end": v(46212.65, 59247.97) * mm});
            skLineSegment(sketch, "E5066", {"start": v(46262.16, 59253.55) * mm, "end": v(46259.55, 59262.16) * mm});
            skLineSegment(sketch, "E5067", {"start": v(46259.55, 59262.16) * mm, "end": v(46221.27, 59250.57) * mm});
            skLineSegment(sketch, "E5068", {"start": v(46212.65, 59247.97) * mm, "end": v(46174.37, 59236.38) * mm});
            skLineSegment(sketch, "E5069", {"start": v(46174.37, 59236.38) * mm, "end": v(46176.98, 59227.76) * mm});
            skLineSegment(sketch, "E5070", {"start": v(46176.98, 59227.76) * mm, "end": v(46262.16, 59253.55) * mm});
            skLineSegment(sketch, "E5071", {"start": v(45942.24, 59721.95) * mm, "end": v(45891.52, 59706.6) * mm});
            skLineSegment(sketch, "E5072", {"start": v(45891.52, 59706.6) * mm, "end": v(45896.15, 59691.29) * mm});
            skLineSegment(sketch, "E5073", {"start": v(45896.15, 59691.29) * mm, "end": v(45946.88, 59706.64) * mm});
            skLineSegment(sketch, "E5074", {"start": v(45931.67, 59756.89) * mm, "end": v(45942.24, 59721.95) * mm});
            skLineSegment(sketch, "E5075", {"start": v(45946.88, 59706.64) * mm, "end": v(45957.45, 59671.7) * mm});
            skLineSegment(sketch, "E5076", {"start": v(45966.07, 59674.31) * mm, "end": v(45940.28, 59759.5) * mm});
            skLineSegment(sketch, "E5077", {"start": v(44716.03, 59334.09) * mm, "end": v(44766.75, 59349.44) * mm});
            skLineSegment(sketch, "E5078", {"start": v(44762.12, 59364.75) * mm, "end": v(44711.4, 59349.4) * mm});
            skLineSegment(sketch, "E5079", {"start": v(44692.2, 59381.73) * mm, "end": v(44717.99, 59296.54) * mm});
            skLineSegment(sketch, "E5080", {"start": v(44717.99, 59296.54) * mm, "end": v(44726.6, 59299.15) * mm});
            skLineSegment(sketch, "E5081", {"start": v(44726.6, 59299.15) * mm, "end": v(44716.03, 59334.09) * mm});
            skLineSegment(sketch, "E5082", {"start": v(44711.4, 59349.4) * mm, "end": v(44700.82, 59384.33) * mm});
            skLineSegment(sketch, "E5083", {"start": v(44700.82, 59384.33) * mm, "end": v(44692.2, 59381.73) * mm});
            skLineSegment(sketch, "E5084", {"start": v(45866.16, 60630.9) * mm, "end": v(45539.38, 60531.98) * mm});
            skLineSegment(sketch, "E5085", {"start": v(45458.03, 60507.36) * mm, "end": v(44692.23, 60275.57) * mm});
            skLineSegment(sketch, "E5086", {"start": v(44610.4, 60250.8) * mm, "end": v(44270.65, 60147.96) * mm});
            skLineSegment(sketch, "E5087", {"start": v(44270.65, 60147.96) * mm, "end": v(44302.51, 60042.68) * mm});
            skLineSegment(sketch, "E5088", {"start": v(44302.51, 60042.68) * mm, "end": v(44685.34, 60158.55) * mm});
            skLineSegment(sketch, "E5089", {"start": v(44704.96, 60164.49) * mm, "end": v(45898.03, 60525.6) * mm});
            skLineSegment(sketch, "E5090", {"start": v(45898.03, 60525.6) * mm, "end": v(45866.16, 60630.9) * mm});
            skLineSegment(sketch, "E5091", {"start": v(45505.23, 60454.78) * mm, "end": v(45087, 60328.18) * mm});
            skLineSegment(sketch, "E5092", {"start": v(45087, 60328.18) * mm, "end": v(45098.3, 60290.86) * mm});
            skLineSegment(sketch, "E5093", {"start": v(45516.53, 60417.45) * mm, "end": v(45505.23, 60454.78) * mm});
            skLineSegment(sketch, "E5094", {"start": v(45086.9, 60328.16) * mm, "end": v(44688.76, 60207.65) * mm});
            skLineSegment(sketch, "E5095", {"start": v(44688.76, 60207.65) * mm, "end": v(44682.1, 60205.63) * mm});
            skLineSegment(sketch, "E5096", {"start": v(44682.1, 60205.63) * mm, "end": v(44693.4, 60168.3) * mm});
            skLineSegment(sketch, "E5097", {"start": v(45100.22, 60284.13) * mm, "end": v(45086.9, 60328.16) * mm});
            skLineSegment(sketch, "E5098", {"start": v(45903.37, 60495.88) * mm, "end": v(44314.56, 60014.98) * mm});
            skLineSegment(sketch, "E5099", {"start": v(44314.56, 60014.98) * mm, "end": v(44346.42, 59909.7) * mm});
            skLineSegment(sketch, "E5100", {"start": v(44346.42, 59909.7) * mm, "end": v(44694.79, 60015.14) * mm});
            skLineSegment(sketch, "E5101", {"start": v(45691.17, 60316.72) * mm, "end": v(45935.24, 60390.6) * mm});
            skLineSegment(sketch, "E5102", {"start": v(45935.24, 60390.6) * mm, "end": v(45903.37, 60495.88) * mm});
            skLineSegment(sketch, "E5103", {"start": v(45526.98, 60377.77) * mm, "end": v(45110.17, 60251.61) * mm});
            skLineSegment(sketch, "E5104", {"start": v(45110.17, 60251.61) * mm, "end": v(45121.76, 60213.33) * mm});
            skLineSegment(sketch, "E5105", {"start": v(45121.76, 60213.33) * mm, "end": v(45538.56, 60339.49) * mm});
            skLineSegment(sketch, "E5106", {"start": v(45538.56, 60339.49) * mm, "end": v(45526.98, 60377.77) * mm});
            skLineSegment(sketch, "E5107", {"start": v(45110.07, 60251.59) * mm, "end": v(44706.72, 60129.5) * mm});
            skLineSegment(sketch, "E5108", {"start": v(44706.72, 60129.5) * mm, "end": v(44718.3, 60091.21) * mm});
            skLineSegment(sketch, "E5109", {"start": v(44718.3, 60091.21) * mm, "end": v(45121.66, 60213.3) * mm});
            skLineSegment(sketch, "E5110", {"start": v(45121.66, 60213.3) * mm, "end": v(45110.07, 60251.59) * mm});
            skLineSegment(sketch, "E5111", {"start": v(44605.12, 59389.85) * mm, "end": v(44682.64, 59413.31) * mm});
            skLineSegment(sketch, "E5112", {"start": v(44682.64, 59413.31) * mm, "end": v(44727.55, 59264.96) * mm});
            skLineSegment(sketch, "E5113", {"start": v(44727.55, 59264.96) * mm, "end": v(44650.02, 59241.5) * mm});
            skLineSegment(sketch, "E5114", {"start": v(44650.02, 59241.5) * mm, "end": v(44643.79, 59244.83) * mm});
            skLineSegment(sketch, "E5115", {"start": v(44643.79, 59244.83) * mm, "end": v(44601.78, 59383.61) * mm});
            skLineSegment(sketch, "E5116", {"start": v(44601.78, 59383.61) * mm, "end": v(44605.12, 59389.85) * mm});
            skLineSegment(sketch, "E5117", {"start": v(44649.14, 59403.17) * mm, "end": v(44430.92, 59337.12) * mm});
            skLineSegment(sketch, "E5118", {"start": v(44430.92, 59337.12) * mm, "end": v(44434.4, 59325.63) * mm});
            skLineSegment(sketch, "E5119", {"start": v(44434.4, 59325.63) * mm, "end": v(44426.74, 59323.32) * mm});
            skLineSegment(sketch, "E5120", {"start": v(44426.74, 59323.32) * mm, "end": v(44464.7, 59197.93) * mm});
            skLineSegment(sketch, "E5121", {"start": v(44464.7, 59197.93) * mm, "end": v(44472.35, 59200.25) * mm});
            skLineSegment(sketch, "E5122", {"start": v(44472.35, 59200.25) * mm, "end": v(44475.82, 59188.77) * mm});
            skLineSegment(sketch, "E5123", {"start": v(44475.82, 59188.77) * mm, "end": v(44694.05, 59254.82) * mm});
            skLineSegment(sketch, "E5124", {"start": v(45931.67, 59756.89) * mm, "end": v(45940.28, 59759.5) * mm});
            skLineSegment(sketch, "E5125", {"start": v(45957.45, 59671.7) * mm, "end": v(45966.07, 59674.31) * mm});
            skLineSegment(sketch, "E5126", {"start": v(44693.4, 60168.3) * mm, "end": v(44700.06, 60170.32) * mm});
            skLineSegment(sketch, "E5127", {"start": v(44700.06, 60170.32) * mm, "end": v(44702.09, 60163.62) * mm});
            skLineSegment(sketch, "E5128", {"start": v(44702.09, 60163.62) * mm, "end": v(44704.96, 60164.49) * mm});
            skLineSegment(sketch, "E5129", {"start": v(45516.53, 60417.45) * mm, "end": v(45509.88, 60415.44) * mm});
            skLineSegment(sketch, "E5130", {"start": v(45509.88, 60415.44) * mm, "end": v(45511.9, 60408.74) * mm});
            skLineSegment(sketch, "E5131", {"start": v(45511.9, 60408.74) * mm, "end": v(45509.04, 60407.87) * mm});
            skLineSegment(sketch, "E5132", {"start": v(44766.75, 59349.44) * mm, "end": v(44762.12, 59364.75) * mm});
            skLineSegment(sketch, "E5133", {"start": v(45981.23, 60190.33) * mm, "end": v(45891.26, 60163.1) * mm});
            skLineSegment(sketch, "E5134", {"start": v(45516.57, 60265.44) * mm, "end": v(45497.88, 60327.17) * mm});
            skLineSegment(sketch, "E5135", {"start": v(64586.51, 51154.5) * mm, "end": v(62556.44, 50022.73) * mm});
            skLineSegment(sketch, "E5136", {"start": v(64603.52, 51149.68) * mm, "end": v(62562.52, 50011.8) * mm});
            skLineSegment(sketch, "E5137", {"start": v(64471.56, 51187.17) * mm, "end": v(62515.29, 50096.53) * mm});
            skLineSegment(sketch, "E5138", {"start": v(64488.56, 51182.34) * mm, "end": v(62521.38, 50085.61) * mm});
            skLineSegment(sketch, "E5139", {"start": v(64454.55, 51192) * mm, "end": v(62509.2, 50107.45) * mm});
            skLineSegment(sketch, "E5140", {"start": v(64440.95, 51195.86) * mm, "end": v(62504.33, 50116.18) * mm});
            skArc(sketch, "E5141", {"start": v(60287.16, 50572.52) * mm, "mid": v(61314.1, 49853.02) * mm, "end": v(62556.45, 50022.74) * mm});
            skArc(sketch, "E5142", {"start": v(60282.99, 50556.27) * mm, "mid": v(61316.6, 49839.56) * mm, "end": v(62562.55, 50011.82) * mm});
            skArc(sketch, "E5143", {"start": v(60316.08, 50685.07) * mm, "mid": v(61296.3, 49944.75) * mm, "end": v(62515.26, 50096.51) * mm});
            skArc(sketch, "E5144", {"start": v(60311.71, 50668.1) * mm, "mid": v(61299.03, 49931.1) * mm, "end": v(62521.35, 50085.6) * mm});
            skArc(sketch, "E5145", {"start": v(60320.47, 50702.18) * mm, "mid": v(61293.53, 49958.45) * mm, "end": v(62509.17, 50107.43) * mm});
            skArc(sketch, "E5146", {"start": v(60324.01, 50715.96) * mm, "mid": v(61291.28, 49969.43) * mm, "end": v(62504.3, 50116.16) * mm});
            skLineSegment(sketch, "E5147", {"start": v(60287.28, 50572.98) * mm, "end": v(60153.5, 50498.4) * mm});
            skLineSegment(sketch, "E5148", {"start": v(60282.99, 50556.27) * mm, "end": v(60148.67, 50481.4) * mm});
            skLineSegment(sketch, "E5149", {"start": v(60316.29, 50685.9) * mm, "end": v(60186.16, 50613.35) * mm});
            skLineSegment(sketch, "E5150", {"start": v(60312, 50669.2) * mm, "end": v(60181.33, 50596.34) * mm});
            skLineSegment(sketch, "E5151", {"start": v(60320.58, 50702.6) * mm, "end": v(60191, 50630.35) * mm});
            skLineSegment(sketch, "E5152", {"start": v(60324.01, 50715.96) * mm, "end": v(60194.86, 50643.96) * mm});
            skLineSegment(sketch, "E5153", {"start": v(51337.5, 74919.22) * mm, "end": v(64586.51, 51154.5) * mm});
            skLineSegment(sketch, "E5154", {"start": v(51348.42, 74925.3) * mm, "end": v(64603.52, 51149.68) * mm});
            skLineSegment(sketch, "E5155", {"start": v(51263.7, 74878.08) * mm, "end": v(64471.56, 51187.17) * mm});
            skLineSegment(sketch, "E5156", {"start": v(51274.61, 74884.16) * mm, "end": v(64488.56, 51182.34) * mm});
            skLineSegment(sketch, "E5157", {"start": v(51252.78, 74871.99) * mm, "end": v(64454.55, 51192) * mm});
            skLineSegment(sketch, "E5158", {"start": v(51244.04, 74867.12) * mm, "end": v(64440.95, 51195.86) * mm});
            skLineSegment(sketch, "E5159", {"start": v(60153.5, 50498.4) * mm, "end": v(59979.27, 50810.91) * mm});
            skLineSegment(sketch, "E5160", {"start": v(60148.67, 50481.4) * mm, "end": v(59962.27, 50815.74) * mm});
            skLineSegment(sketch, "E5161", {"start": v(60186.16, 50613.35) * mm, "end": v(60094.22, 50778.25) * mm});
            skLineSegment(sketch, "E5162", {"start": v(60181.33, 50596.34) * mm, "end": v(60077.22, 50783.09) * mm});
            skLineSegment(sketch, "E5163", {"start": v(60191, 50630.35) * mm, "end": v(60111.23, 50773.42) * mm});
            skLineSegment(sketch, "E5164", {"start": v(60194.86, 50643.96) * mm, "end": v(60124.83, 50769.56) * mm});
            skLineSegment(sketch, "E5165", {"start": v(40705.03, 72085.67) * mm, "end": v(41594.64, 69146.66) * mm});
            skLineSegment(sketch, "E5166", {"start": v(40717.5, 72079) * mm, "end": v(41601.32, 69159.13) * mm});
            skLineSegment(sketch, "E5167", {"start": v(40689.45, 72094.02) * mm, "end": v(41586.3, 69131.08) * mm});
            skLineSegment(sketch, "E5168", {"start": v(40673.86, 72102.36) * mm, "end": v(41577.96, 69115.5) * mm});
            skLineSegment(sketch, "E5169", {"start": v(40584.1, 72150.41) * mm, "end": v(41529.9, 69025.72) * mm});
            skLineSegment(sketch, "E5170", {"start": v(42507.66, 67108.13) * mm, "end": v(43511.28, 66369.54) * mm});
            skLineSegment(sketch, "E5171", {"start": v(42516.26, 67114.2) * mm, "end": v(43517.2, 66377.6) * mm});
            skLineSegment(sketch, "E5172", {"start": v(42496.9, 67100.52) * mm, "end": v(43503.87, 66359.47) * mm});
            skLineSegment(sketch, "E5173", {"start": v(42486.14, 67092.92) * mm, "end": v(43496.46, 66349.4) * mm});
            skLineSegment(sketch, "E5174", {"start": v(42424.17, 67049.13) * mm, "end": v(43453.79, 66291.42) * mm});
            skLineSegment(sketch, "E5175", {"start": v(43847.96, 73497.83) * mm, "end": v(43816.86, 73740.3) * mm});
            skLineSegment(sketch, "E5176", {"start": v(43838.04, 73496.56) * mm, "end": v(43808.21, 73729.11) * mm});
            skLineSegment(sketch, "E5177", {"start": v(43860.36, 73499.42) * mm, "end": v(43827.67, 73754.3) * mm});
            skLineSegment(sketch, "E5178", {"start": v(43872.76, 73501.01) * mm, "end": v(43838.47, 73768.28) * mm});
            skLineSegment(sketch, "E5179", {"start": v(43944.17, 73510.17) * mm, "end": v(43900.73, 73848.86) * mm});
            skLineSegment(sketch, "E5180", {"start": v(45297.5, 65650.7) * mm, "end": v(44492.15, 64556.34) * mm});
            skLineSegment(sketch, "E5181", {"start": v(45303.43, 65626.69) * mm, "end": v(44518.72, 64560.38) * mm});
            skLineSegment(sketch, "E5182", {"start": v(45289.72, 65682.28) * mm, "end": v(44457.2, 64551.02) * mm});
            skLineSegment(sketch, "E5183", {"start": v(45285.82, 65698.07) * mm, "end": v(44439.72, 64548.36) * mm});
            skLineSegment(sketch, "E5184", {"start": v(45263.37, 65789.04) * mm, "end": v(44339.06, 64533.05) * mm});
            skLineSegment(sketch, "E5185", {"start": v(44492.15, 64556.34) * mm, "end": v(44554.7, 64510.32) * mm});
            skLineSegment(sketch, "E5186", {"start": v(44518.72, 64560.38) * mm, "end": v(44581.26, 64514.36) * mm});
            skLineSegment(sketch, "E5187", {"start": v(44457.2, 64551.02) * mm, "end": v(44519.74, 64505) * mm});
            skLineSegment(sketch, "E5188", {"start": v(44439.72, 64548.36) * mm, "end": v(44502.26, 64502.34) * mm});
            skLineSegment(sketch, "E5189", {"start": v(44339.06, 64533.05) * mm, "end": v(44401.6, 64487.03) * mm});
            skLineSegment(sketch, "E5190", {"start": v(44554.7, 64510.32) * mm, "end": v(43431.74, 62984.39) * mm});
            skLineSegment(sketch, "E5191", {"start": v(44581.26, 64514.36) * mm, "end": v(43452.68, 62980.79) * mm});
            skLineSegment(sketch, "E5192", {"start": v(44519.74, 64505) * mm, "end": v(43404.18, 62989.13) * mm});
            skLineSegment(sketch, "E5193", {"start": v(44502.26, 64502.34) * mm, "end": v(43390.4, 62991.5) * mm});
            skLineSegment(sketch, "E5194", {"start": v(44401.6, 64487.03) * mm, "end": v(43311.05, 63005.14) * mm});
            skLineSegment(sketch, "E5195", {"start": v(48682.1, 64352.3) * mm, "end": v(50863.24, 65012.63) * mm});
            skLineSegment(sketch, "E5196", {"start": v(48673.4, 64381) * mm, "end": v(50825.84, 65032.65) * mm});
            skLineSegment(sketch, "E5197", {"start": v(48696.58, 64304.44) * mm, "end": v(50925.58, 64979.26) * mm});
            skLineSegment(sketch, "E5198", {"start": v(48703.82, 64280.51) * mm, "end": v(50956.76, 64962.58) * mm});
            skLineSegment(sketch, "E5199", {"start": v(50666.18, 64874.6) * mm, "end": v(50956.76, 64962.58) * mm});
            skLineSegment(sketch, "E5200", {"start": v(49417.02, 64496.43) * mm, "end": v(50565.68, 64844.18) * mm});
            skLineSegment(sketch, "E5201", {"start": v(48703.82, 64280.51) * mm, "end": v(49316.53, 64466) * mm});
            skLineSegment(sketch, "E5202", {"start": v(48119.55, 62898.12) * mm, "end": v(47504.87, 64928.93) * mm});
            skLineSegment(sketch, "E5203", {"start": v(48105.2, 62893.78) * mm, "end": v(47490.51, 64924.59) * mm});
            skLineSegment(sketch, "E5204", {"start": v(48133.91, 62902.47) * mm, "end": v(47519.23, 64933.28) * mm});
            skLineSegment(sketch, "E5205", {"start": v(48186.55, 62918.4) * mm, "end": v(47571.87, 64949.2) * mm});
            skLineSegment(sketch, "E5206", {"start": v(48200.9, 62922.75) * mm, "end": v(47586.23, 64953.56) * mm});
            skLineSegment(sketch, "E5207", {"start": v(48215.27, 62927.1) * mm, "end": v(47600.58, 64957.9) * mm});
            skLineSegment(sketch, "E5208", {"start": v(48515.13, 61591.21) * mm, "end": v(48408.1, 61944.83) * mm});
            skLineSegment(sketch, "E5209", {"start": v(48505.12, 61572.51) * mm, "end": v(48393.74, 61940.49) * mm});
            skLineSegment(sketch, "E5210", {"start": v(48525.14, 61609.92) * mm, "end": v(48422.45, 61949.18) * mm});
            skLineSegment(sketch, "E5211", {"start": v(48561.85, 61678.5) * mm, "end": v(48475.1, 61965.11) * mm});
            skLineSegment(sketch, "E5212", {"start": v(48571.86, 61697.2) * mm, "end": v(48489.45, 61969.46) * mm});
            skLineSegment(sketch, "E5213", {"start": v(48581.87, 61715.9) * mm, "end": v(48503.8, 61973.8) * mm});
            skLineSegment(sketch, "E5214", {"start": v(48160.23, 62910.43) * mm, "end": v(48215.27, 62927.1) * mm});
            skLineSegment(sketch, "E5215", {"start": v(48448.77, 61957.14) * mm, "end": v(48503.8, 61973.8) * mm});
            skLineSegment(sketch, "E5216", {"start": v(48160.23, 62910.43) * mm, "end": v(48105.2, 62893.78) * mm});
            skLineSegment(sketch, "E5217", {"start": v(48448.77, 61957.14) * mm, "end": v(48393.74, 61940.49) * mm});
            skLineSegment(sketch, "E5218", {"start": v(48393.74, 61940.49) * mm, "end": v(48383.6, 61973.99) * mm});
            skLineSegment(sketch, "E5219", {"start": v(48105.2, 62893.78) * mm, "end": v(48115.34, 62860.28) * mm});
            skLineSegment(sketch, "E5220", {"start": v(48393.74, 61940.49) * mm, "end": v(48503.8, 61973.8) * mm});
            skLineSegment(sketch, "E5221", {"start": v(48105.2, 62893.78) * mm, "end": v(48215.27, 62927.1) * mm});
            skLineSegment(sketch, "E5222", {"start": v(48383.6, 61973.99) * mm, "end": v(48493.67, 62007.3) * mm});
            skLineSegment(sketch, "E5223", {"start": v(48493.67, 62007.3) * mm, "end": v(48503.8, 61973.8) * mm});
            skLineSegment(sketch, "E5224", {"start": v(48503.8, 61973.8) * mm, "end": v(48393.74, 61940.49) * mm});
            skLineSegment(sketch, "E5225", {"start": v(48115.34, 62860.28) * mm, "end": v(48105.2, 62893.78) * mm});
            skLineSegment(sketch, "E5226", {"start": v(48215.27, 62927.1) * mm, "end": v(48225.4, 62893.6) * mm});
            skLineSegment(sketch, "E5227", {"start": v(48225.4, 62893.6) * mm, "end": v(48115.34, 62860.28) * mm});
            skLineSegment(sketch, "E5228", {"start": v(48503.8, 61973.8) * mm, "end": v(48493.67, 62007.3) * mm});
            skLineSegment(sketch, "E5229", {"start": v(48115.34, 62860.28) * mm, "end": v(48225.4, 62893.6) * mm});
            skLineSegment(sketch, "E5230", {"start": v(48383.6, 61973.99) * mm, "end": v(48393.74, 61940.49) * mm});
            skLineSegment(sketch, "E5231", {"start": v(48345.88, 61926) * mm, "end": v(48335.74, 61959.5) * mm});
            skLineSegment(sketch, "E5232", {"start": v(48335.74, 61959.5) * mm, "end": v(48383.6, 61973.99) * mm});
            skLineSegment(sketch, "E5233", {"start": v(48393.74, 61940.49) * mm, "end": v(48345.88, 61926) * mm});
            skLineSegment(sketch, "E5234", {"start": v(48067.48, 62845.8) * mm, "end": v(48057.34, 62879.3) * mm});
            skLineSegment(sketch, "E5235", {"start": v(48057.34, 62879.3) * mm, "end": v(48105.2, 62893.78) * mm});
            skLineSegment(sketch, "E5236", {"start": v(48115.34, 62860.28) * mm, "end": v(48067.48, 62845.8) * mm});
            skLineSegment(sketch, "E5237", {"start": v(48335.74, 61959.5) * mm, "end": v(48345.88, 61926) * mm});
            skLineSegment(sketch, "E5238", {"start": v(48067.48, 62845.8) * mm, "end": v(48115.34, 62860.28) * mm});
            skLineSegment(sketch, "E5239", {"start": v(48345.88, 61926) * mm, "end": v(48393.74, 61940.49) * mm});
            skLineSegment(sketch, "E5240", {"start": v(48393.74, 61940.49) * mm, "end": v(48105.2, 62893.78) * mm});
            skLineSegment(sketch, "E5241", {"start": v(48503.8, 61973.8) * mm, "end": v(48215.27, 62927.1) * mm});
            skLineSegment(sketch, "E5242", {"start": v(50826.84, 64085.1) * mm, "end": v(50594.4, 64852.88) * mm});
            skLineSegment(sketch, "E5243", {"start": v(50798.12, 64076.42) * mm, "end": v(50565.68, 64844.18) * mm});
            skLineSegment(sketch, "E5244", {"start": v(50874.7, 64099.6) * mm, "end": v(50642.25, 64867.36) * mm});
            skLineSegment(sketch, "E5245", {"start": v(50898.62, 64106.84) * mm, "end": v(50666.18, 64874.6) * mm});
            skLineSegment(sketch, "E5246", {"start": v(52145.63, 61439.68) * mm, "end": v(52174.6, 61343.97) * mm});
            skLineSegment(sketch, "E5247", {"start": v(52160, 61444.03) * mm, "end": v(52188.95, 61348.31) * mm});
            skLineSegment(sketch, "E5248", {"start": v(52131.28, 61435.34) * mm, "end": v(52160.24, 61339.62) * mm});
            skLineSegment(sketch, "E5249", {"start": v(52078.63, 61419.41) * mm, "end": v(52107.6, 61323.7) * mm});
            skLineSegment(sketch, "E5250", {"start": v(52064.28, 61415.07) * mm, "end": v(52093.24, 61319.35) * mm});
            skLineSegment(sketch, "E5251", {"start": v(52049.92, 61410.72) * mm, "end": v(52078.88, 61315) * mm});
            skLineSegment(sketch, "E5252", {"start": v(51797.63, 62589.83) * mm, "end": v(51853.13, 62406.4) * mm});
            skLineSegment(sketch, "E5253", {"start": v(51811.99, 62594.17) * mm, "end": v(51867.49, 62410.75) * mm});
            skLineSegment(sketch, "E5254", {"start": v(51783.27, 62585.49) * mm, "end": v(51838.77, 62402.06) * mm});
            skLineSegment(sketch, "E5255", {"start": v(51730.63, 62569.56) * mm, "end": v(51786.13, 62386.13) * mm});
            skLineSegment(sketch, "E5256", {"start": v(51716.27, 62565.21) * mm, "end": v(51771.77, 62381.78) * mm});
            skLineSegment(sketch, "E5257", {"start": v(51701.92, 62560.87) * mm, "end": v(51757.42, 62377.44) * mm});
            skLineSegment(sketch, "E5258", {"start": v(51867.49, 62410.74) * mm, "end": v(51757.42, 62377.44) * mm});
            skLineSegment(sketch, "E5259", {"start": v(52159.99, 61444.03) * mm, "end": v(52049.92, 61410.72) * mm});
            skLineSegment(sketch, "E5260", {"start": v(51867.49, 62410.74) * mm, "end": v(51879.65, 62370.54) * mm});
            skLineSegment(sketch, "E5261", {"start": v(51879.65, 62370.54) * mm, "end": v(51769.58, 62337.24) * mm});
            skLineSegment(sketch, "E5262", {"start": v(51769.58, 62337.24) * mm, "end": v(51757.42, 62377.44) * mm});
            skLineSegment(sketch, "E5263", {"start": v(51757.42, 62377.44) * mm, "end": v(51867.49, 62410.74) * mm});
            skLineSegment(sketch, "E5264", {"start": v(52147.83, 61484.23) * mm, "end": v(52159.99, 61444.03) * mm});
            skLineSegment(sketch, "E5265", {"start": v(52049.92, 61410.72) * mm, "end": v(52037.75, 61450.92) * mm});
            skLineSegment(sketch, "E5266", {"start": v(52037.75, 61450.92) * mm, "end": v(52147.83, 61484.23) * mm});
            skLineSegment(sketch, "E5267", {"start": v(52159.99, 61444.03) * mm, "end": v(52147.83, 61484.23) * mm});
            skLineSegment(sketch, "E5268", {"start": v(51757.42, 62377.44) * mm, "end": v(51769.58, 62337.24) * mm});
            skLineSegment(sketch, "E5269", {"start": v(52147.83, 61484.23) * mm, "end": v(52037.75, 61450.92) * mm});
            skArc(sketch, "E5270", {"start": v(52147.83, 61484.23) * mm, "mid": v(52696, 61933.45) * mm, "end": v(52765.97, 62638.72) * mm});
            skLineSegment(sketch, "E5271", {"start": v(51879.65, 62370.54) * mm, "end": v(52765.97, 62638.72) * mm});
            skLineSegment(sketch, "E5272", {"start": v(52765.97, 62638.72) * mm, "end": v(52778.84, 62596.17) * mm});
            skLineSegment(sketch, "E5273", {"start": v(52778.84, 62596.17) * mm, "end": v(51892.52, 62328) * mm});
            skLineSegment(sketch, "E5274", {"start": v(51892.52, 62328) * mm, "end": v(51879.65, 62370.54) * mm});
            skLineSegment(sketch, "E5275", {"start": v(51892.52, 62328) * mm, "end": v(52778.84, 62596.17) * mm});
            skLineSegment(sketch, "E5276", {"start": v(51879.65, 62370.54) * mm, "end": v(51892.52, 62328) * mm});
            skLineSegment(sketch, "E5277", {"start": v(50695.25, 62339.9) * mm, "end": v(53189.95, 63095) * mm});
            skLineSegment(sketch, "E5278", {"start": v(50690.9, 62354.26) * mm, "end": v(53182.47, 63108.4) * mm});
            skLineSegment(sketch, "E5279", {"start": v(50699.6, 62325.54) * mm, "end": v(53197.43, 63081.58) * mm});
            skLineSegment(sketch, "E5280", {"start": v(50715.53, 62272.9) * mm, "end": v(53224.84, 63032.42) * mm});
            skLineSegment(sketch, "E5281", {"start": v(50719.88, 62258.54) * mm, "end": v(53232.32, 63019) * mm});
            skLineSegment(sketch, "E5282", {"start": v(50724.22, 62244.19) * mm, "end": v(53239.8, 63005.6) * mm});
            skLineSegment(sketch, "E5283", {"start": v(51078.54, 62471.58) * mm, "end": v(53182.47, 63108.4) * mm});
            skLineSegment(sketch, "E5284", {"start": v(50690.9, 62354.26) * mm, "end": v(50978.04, 62441.17) * mm});
            skLineSegment(sketch, "E5285", {"start": v(49278, 61910.93) * mm, "end": v(49728.56, 62047.3) * mm});
            skLineSegment(sketch, "E5286", {"start": v(49273.66, 61925.29) * mm, "end": v(49724.22, 62061.66) * mm});
            skLineSegment(sketch, "E5287", {"start": v(49282.35, 61896.57) * mm, "end": v(49732.9, 62032.95) * mm});
            skLineSegment(sketch, "E5288", {"start": v(49298.29, 61843.93) * mm, "end": v(49748.84, 61980.3) * mm});
            skLineSegment(sketch, "E5289", {"start": v(49302.63, 61829.57) * mm, "end": v(49753.19, 61965.95) * mm});
            skLineSegment(sketch, "E5290", {"start": v(49306.98, 61815.22) * mm, "end": v(49757.53, 61951.6) * mm});
            skLineSegment(sketch, "E5291", {"start": v(49414.17, 61847.66) * mm, "end": v(49757.53, 61951.6) * mm});
            skLineSegment(sketch, "E5292", {"start": v(49306.98, 61815.22) * mm, "end": v(49313.68, 61817.24) * mm});
            skLineSegment(sketch, "E5293", {"start": v(48571.86, 61697.2) * mm, "end": v(48847.3, 61780.56) * mm});
            skLineSegment(sketch, "E5294", {"start": v(48581.87, 61715.9) * mm, "end": v(48842.96, 61794.92) * mm});
            skLineSegment(sketch, "E5295", {"start": v(48561.85, 61678.5) * mm, "end": v(48851.65, 61766.2) * mm});
            skLineSegment(sketch, "E5296", {"start": v(48525.14, 61609.92) * mm, "end": v(48867.58, 61713.57) * mm});
            skLineSegment(sketch, "E5297", {"start": v(48515.13, 61591.21) * mm, "end": v(48871.93, 61699.2) * mm});
            skLineSegment(sketch, "E5298", {"start": v(48505.12, 61572.51) * mm, "end": v(48876.27, 61684.85) * mm});
            skLineSegment(sketch, "E5299", {"start": v(48859.62, 61739.89) * mm, "end": v(48876.27, 61684.85) * mm});
            skLineSegment(sketch, "E5300", {"start": v(49290.32, 61870.25) * mm, "end": v(49306.98, 61815.22) * mm});
            skLineSegment(sketch, "E5301", {"start": v(48859.62, 61739.89) * mm, "end": v(48842.96, 61794.92) * mm});
            skLineSegment(sketch, "E5302", {"start": v(49290.32, 61870.25) * mm, "end": v(49273.66, 61925.29) * mm});
            skArc(sketch, "E5303", {"start": v(48842.96, 61794.92) * mm, "mid": v(49721.47, 61880.9) * mm, "end": v(48876.93, 62137.66) * mm});
            skLineSegment(sketch, "E5304", {"start": v(49273.66, 61925.29) * mm, "end": v(48876.93, 62137.66) * mm});
            skLineSegment(sketch, "E5305", {"start": v(48876.93, 62137.66) * mm, "end": v(48855.95, 62098.47) * mm});
            skLineSegment(sketch, "E5306", {"start": v(48855.95, 62098.47) * mm, "end": v(49252.68, 61886.1) * mm});
            skLineSegment(sketch, "E5307", {"start": v(49252.68, 61886.1) * mm, "end": v(49273.66, 61925.29) * mm});
            skLineSegment(sketch, "E5308", {"start": v(49252.68, 61886.1) * mm, "end": v(48855.95, 62098.47) * mm});
            skLineSegment(sketch, "E5309", {"start": v(49273.66, 61925.29) * mm, "end": v(49252.68, 61886.1) * mm});
            skLineSegment(sketch, "E5310", {"start": v(49273.66, 61925.29) * mm, "end": v(48842.96, 61794.92) * mm});
            skLineSegment(sketch, "E5311", {"start": v(49306.98, 61815.22) * mm, "end": v(48876.27, 61684.85) * mm});
            skLineSegment(sketch, "E5312", {"start": v(49757.53, 61951.6) * mm, "end": v(49724.22, 62061.66) * mm});
            skLineSegment(sketch, "E5313", {"start": v(50724.22, 62244.19) * mm, "end": v(50690.9, 62354.26) * mm});
            skLineSegment(sketch, "E5314", {"start": v(49757.53, 61951.6) * mm, "end": v(49797.73, 61963.76) * mm});
            skLineSegment(sketch, "E5315", {"start": v(49797.73, 61963.76) * mm, "end": v(49764.42, 62073.83) * mm});
            skLineSegment(sketch, "E5316", {"start": v(49764.42, 62073.83) * mm, "end": v(49724.22, 62061.66) * mm});
            skLineSegment(sketch, "E5317", {"start": v(49724.22, 62061.66) * mm, "end": v(49757.53, 61951.6) * mm});
            skLineSegment(sketch, "E5318", {"start": v(50684.02, 62232.02) * mm, "end": v(50724.22, 62244.19) * mm});
            skLineSegment(sketch, "E5319", {"start": v(50690.9, 62354.26) * mm, "end": v(50650.7, 62342.09) * mm});
            skLineSegment(sketch, "E5320", {"start": v(50650.7, 62342.09) * mm, "end": v(50684.02, 62232.02) * mm});
            skLineSegment(sketch, "E5321", {"start": v(50724.22, 62244.19) * mm, "end": v(50684.02, 62232.02) * mm});
            skLineSegment(sketch, "E5322", {"start": v(49724.22, 62061.66) * mm, "end": v(49764.42, 62073.83) * mm});
            skLineSegment(sketch, "E5323", {"start": v(50684.02, 62232.02) * mm, "end": v(50650.7, 62342.09) * mm});
            skArc(sketch, "E5324", {"start": v(50684.02, 62232.02) * mm, "mid": v(48981.34, 62400.77) * mm, "end": v(50066, 61077.47) * mm});
            skLineSegment(sketch, "E5325", {"start": v(49797.73, 61963.76) * mm, "end": v(50066, 61077.47) * mm});
            skLineSegment(sketch, "E5326", {"start": v(50066, 61077.47) * mm, "end": v(50108.54, 61090.35) * mm});
            skLineSegment(sketch, "E5327", {"start": v(50108.54, 61090.35) * mm, "end": v(49840.28, 61976.64) * mm});
            skLineSegment(sketch, "E5328", {"start": v(49840.28, 61976.64) * mm, "end": v(49797.73, 61963.76) * mm});
            skLineSegment(sketch, "E5329", {"start": v(49840.28, 61976.64) * mm, "end": v(50108.54, 61090.35) * mm});
            skLineSegment(sketch, "E5330", {"start": v(49797.73, 61963.76) * mm, "end": v(49840.28, 61976.64) * mm});
            skLineSegment(sketch, "E5331", {"start": v(48122.64, 63245.2) * mm, "end": v(48119.27, 63244.18) * mm});
            skLineSegment(sketch, "E5332", {"start": v(48131.3, 63216.48) * mm, "end": v(48127.94, 63215.46) * mm});
            skLineSegment(sketch, "E5333", {"start": v(48108.19, 63293.06) * mm, "end": v(48104.82, 63292.05) * mm});
            skLineSegment(sketch, "E5334", {"start": v(48100.96, 63317) * mm, "end": v(48097.6, 63315.98) * mm});
            skLineSegment(sketch, "E5335", {"start": v(49662.56, 63710.07) * mm, "end": v(49545.23, 63674.65) * mm});
            skLineSegment(sketch, "E5336", {"start": v(49671.23, 63681.35) * mm, "end": v(49553.9, 63645.93) * mm});
            skLineSegment(sketch, "E5337", {"start": v(49648.1, 63757.94) * mm, "end": v(49530.78, 63722.52) * mm});
            skLineSegment(sketch, "E5338", {"start": v(49640.88, 63781.87) * mm, "end": v(49523.55, 63746.45) * mm});
            skLineSegment(sketch, "E5339", {"start": v(50911.96, 64087.25) * mm, "end": v(50797.95, 64052.83) * mm});
            skLineSegment(sketch, "E5340", {"start": v(50920.63, 64058.53) * mm, "end": v(50806.62, 64024.1) * mm});
            skLineSegment(sketch, "E5341", {"start": v(50897.51, 64135.11) * mm, "end": v(50783.5, 64100.7) * mm});
            skLineSegment(sketch, "E5342", {"start": v(50890.29, 64159.05) * mm, "end": v(50776.27, 64124.63) * mm});
            skLineSegment(sketch, "E5343", {"start": v(52464.33, 64555.88) * mm, "end": v(52047.36, 64430) * mm});
            skLineSegment(sketch, "E5344", {"start": v(52473, 64527.16) * mm, "end": v(52056.03, 64401.28) * mm});
            skLineSegment(sketch, "E5345", {"start": v(52449.88, 64603.75) * mm, "end": v(52032.9, 64477.87) * mm});
            skLineSegment(sketch, "E5346", {"start": v(52442.65, 64627.68) * mm, "end": v(52025.68, 64501.8) * mm});
            skLineSegment(sketch, "E5347", {"start": v(48116.14, 63266.73) * mm, "end": v(48100.96, 63317) * mm});
            skLineSegment(sketch, "E5348", {"start": v(49538.73, 63696.2) * mm, "end": v(49523.55, 63746.45) * mm});
            skLineSegment(sketch, "E5349", {"start": v(48116.14, 63266.73) * mm, "end": v(48131.3, 63216.48) * mm});
            skLineSegment(sketch, "E5350", {"start": v(49538.73, 63696.2) * mm, "end": v(49553.9, 63645.93) * mm});
            skLineSegment(sketch, "E5351", {"start": v(49553.18, 63648.33) * mm, "end": v(49524.28, 63744.06) * mm});
            skLineSegment(sketch, "E5352", {"start": v(48130.59, 63218.87) * mm, "end": v(48101.69, 63314.6) * mm});
            skLineSegment(sketch, "E5353", {"start": v(49553.18, 63648.33) * mm, "end": v(49519.67, 63638.21) * mm});
            skLineSegment(sketch, "E5354", {"start": v(49519.67, 63638.21) * mm, "end": v(49490.77, 63733.94) * mm});
            skLineSegment(sketch, "E5355", {"start": v(49490.77, 63733.94) * mm, "end": v(49524.28, 63744.06) * mm});
            skLineSegment(sketch, "E5356", {"start": v(49524.28, 63744.06) * mm, "end": v(49553.18, 63648.33) * mm});
            skLineSegment(sketch, "E5357", {"start": v(48164.1, 63228.98) * mm, "end": v(48130.59, 63218.87) * mm});
            skLineSegment(sketch, "E5358", {"start": v(48101.69, 63314.6) * mm, "end": v(48135.2, 63324.72) * mm});
            skLineSegment(sketch, "E5359", {"start": v(48135.2, 63324.72) * mm, "end": v(48164.1, 63228.98) * mm});
            skLineSegment(sketch, "E5360", {"start": v(48130.59, 63218.87) * mm, "end": v(48164.1, 63228.98) * mm});
            skLineSegment(sketch, "E5361", {"start": v(49524.28, 63744.06) * mm, "end": v(49490.77, 63733.94) * mm});
            skLineSegment(sketch, "E5362", {"start": v(48164.1, 63228.98) * mm, "end": v(48135.2, 63324.72) * mm});
            skArc(sketch, "E5363", {"start": v(48841.88, 63433.6) * mm, "mid": v(48971.78, 63189.8) * mm, "end": v(49185.08, 63014.26) * mm});
            skLineSegment(sketch, "E5364", {"start": v(49519.67, 63638.21) * mm, "end": v(49185.08, 63014.26) * mm});
            skLineSegment(sketch, "E5365", {"start": v(49185.08, 63014.26) * mm, "end": v(49145.91, 63035.26) * mm});
            skLineSegment(sketch, "E5366", {"start": v(49145.91, 63035.26) * mm, "end": v(49480.5, 63659.22) * mm});
            skLineSegment(sketch, "E5367", {"start": v(49480.5, 63659.22) * mm, "end": v(49519.67, 63638.21) * mm});
            skLineSegment(sketch, "E5368", {"start": v(49480.5, 63659.22) * mm, "end": v(49145.91, 63035.26) * mm});
            skLineSegment(sketch, "E5369", {"start": v(49519.67, 63638.21) * mm, "end": v(49480.5, 63659.22) * mm});
            skArc(sketch, "E5370", {"start": v(48788.05, 62894.4) * mm, "mid": v(48868.6, 63158.64) * mm, "end": v(48841.88, 63433.6) * mm});
            skLineSegment(sketch, "E5371", {"start": v(48788.05, 62894.4) * mm, "end": v(48164.1, 63228.98) * mm});
            skLineSegment(sketch, "E5372", {"start": v(48164.1, 63228.98) * mm, "end": v(48185.1, 63268.16) * mm});
            skLineSegment(sketch, "E5373", {"start": v(48185.1, 63268.16) * mm, "end": v(48809.05, 62933.57) * mm});
            skLineSegment(sketch, "E5374", {"start": v(48809.05, 62933.57) * mm, "end": v(48788.05, 62894.4) * mm});
            skLineSegment(sketch, "E5375", {"start": v(48809.05, 62933.57) * mm, "end": v(48185.1, 63268.16) * mm});
            skLineSegment(sketch, "E5376", {"start": v(48788.05, 62894.4) * mm, "end": v(48809.05, 62933.57) * mm});
            skLineSegment(sketch, "E5377", {"start": v(49553.9, 63645.93) * mm, "end": v(48131.3, 63216.48) * mm});
            skLineSegment(sketch, "E5378", {"start": v(49523.55, 63746.45) * mm, "end": v(48100.96, 63317) * mm});
            skLineSegment(sketch, "E5379", {"start": v(49656.05, 63731.61) * mm, "end": v(49640.88, 63781.87) * mm});
            skLineSegment(sketch, "E5380", {"start": v(50791.45, 64074.37) * mm, "end": v(50776.27, 64124.63) * mm});
            skLineSegment(sketch, "E5381", {"start": v(49656.05, 63731.61) * mm, "end": v(49671.23, 63681.35) * mm});
            skLineSegment(sketch, "E5382", {"start": v(50791.45, 64074.37) * mm, "end": v(50806.62, 64024.1) * mm});
            skLineSegment(sketch, "E5383", {"start": v(50805.9, 64026.5) * mm, "end": v(50777, 64122.23) * mm});
            skLineSegment(sketch, "E5384", {"start": v(49670.5, 63683.74) * mm, "end": v(49641.6, 63779.48) * mm});
            skLineSegment(sketch, "E5385", {"start": v(50805.9, 64026.5) * mm, "end": v(50772.39, 64016.39) * mm});
            skLineSegment(sketch, "E5386", {"start": v(50772.39, 64016.39) * mm, "end": v(50743.49, 64112.12) * mm});
            skLineSegment(sketch, "E5387", {"start": v(50743.49, 64112.12) * mm, "end": v(50777, 64122.23) * mm});
            skLineSegment(sketch, "E5388", {"start": v(50777, 64122.23) * mm, "end": v(50805.9, 64026.5) * mm});
            skLineSegment(sketch, "E5389", {"start": v(49704.01, 63693.86) * mm, "end": v(49670.5, 63683.74) * mm});
            skLineSegment(sketch, "E5390", {"start": v(49641.6, 63779.48) * mm, "end": v(49675.11, 63789.6) * mm});
            skLineSegment(sketch, "E5391", {"start": v(49675.11, 63789.6) * mm, "end": v(49704.01, 63693.86) * mm});
            skLineSegment(sketch, "E5392", {"start": v(49670.5, 63683.74) * mm, "end": v(49704.01, 63693.86) * mm});
            skLineSegment(sketch, "E5393", {"start": v(50777, 64122.23) * mm, "end": v(50743.49, 64112.12) * mm});
            skLineSegment(sketch, "E5394", {"start": v(49704.01, 63693.86) * mm, "end": v(49675.11, 63789.6) * mm});
            skArc(sketch, "E5395", {"start": v(50238.2, 63855.12) * mm, "mid": v(50340.58, 63662.97) * mm, "end": v(50508.7, 63524.63) * mm});
            skLineSegment(sketch, "E5396", {"start": v(50772.39, 64016.39) * mm, "end": v(50508.7, 63524.63) * mm});
            skLineSegment(sketch, "E5397", {"start": v(50508.7, 63524.63) * mm, "end": v(50469.52, 63545.63) * mm});
            skLineSegment(sketch, "E5398", {"start": v(50469.52, 63545.63) * mm, "end": v(50733.22, 64037.4) * mm});
            skLineSegment(sketch, "E5399", {"start": v(50733.22, 64037.4) * mm, "end": v(50772.39, 64016.39) * mm});
            skLineSegment(sketch, "E5400", {"start": v(50733.22, 64037.4) * mm, "end": v(50469.52, 63545.63) * mm});
            skLineSegment(sketch, "E5401", {"start": v(50772.39, 64016.39) * mm, "end": v(50733.22, 64037.4) * mm});
            skArc(sketch, "E5402", {"start": v(50195.77, 63430.16) * mm, "mid": v(50259.25, 63638.42) * mm, "end": v(50238.2, 63855.12) * mm});
            skLineSegment(sketch, "E5403", {"start": v(50195.77, 63430.16) * mm, "end": v(49704.01, 63693.86) * mm});
            skLineSegment(sketch, "E5404", {"start": v(49704.01, 63693.86) * mm, "end": v(49725.02, 63733.03) * mm});
            skLineSegment(sketch, "E5405", {"start": v(49725.02, 63733.03) * mm, "end": v(50216.78, 63469.33) * mm});
            skLineSegment(sketch, "E5406", {"start": v(50216.78, 63469.33) * mm, "end": v(50195.77, 63430.16) * mm});
            skLineSegment(sketch, "E5407", {"start": v(50216.78, 63469.33) * mm, "end": v(49725.02, 63733.03) * mm});
            skLineSegment(sketch, "E5408", {"start": v(50195.77, 63430.16) * mm, "end": v(50216.78, 63469.33) * mm});
            skLineSegment(sketch, "E5409", {"start": v(50806.62, 64024.1) * mm, "end": v(49671.23, 63681.35) * mm});
            skLineSegment(sketch, "E5410", {"start": v(50776.27, 64124.63) * mm, "end": v(49640.88, 63781.87) * mm});
            skLineSegment(sketch, "E5411", {"start": v(50905.46, 64108.79) * mm, "end": v(50890.29, 64159.05) * mm});
            skLineSegment(sketch, "E5412", {"start": v(52040.85, 64451.54) * mm, "end": v(52025.68, 64501.8) * mm});
            skLineSegment(sketch, "E5413", {"start": v(50905.46, 64108.79) * mm, "end": v(50920.63, 64058.53) * mm});
            skLineSegment(sketch, "E5414", {"start": v(52040.85, 64451.54) * mm, "end": v(52056.03, 64401.28) * mm});
            skLineSegment(sketch, "E5415", {"start": v(52055.3, 64403.68) * mm, "end": v(52026.4, 64499.4) * mm});
            skLineSegment(sketch, "E5416", {"start": v(50919.91, 64060.92) * mm, "end": v(50891.01, 64156.65) * mm});
            skLineSegment(sketch, "E5417", {"start": v(52055.3, 64403.68) * mm, "end": v(52021.8, 64393.56) * mm});
            skLineSegment(sketch, "E5418", {"start": v(52021.8, 64393.56) * mm, "end": v(51992.9, 64489.3) * mm});
            skLineSegment(sketch, "E5419", {"start": v(51992.9, 64489.3) * mm, "end": v(52026.4, 64499.4) * mm});
            skLineSegment(sketch, "E5420", {"start": v(52026.4, 64499.4) * mm, "end": v(52055.3, 64403.68) * mm});
            skLineSegment(sketch, "E5421", {"start": v(50953.42, 64071.04) * mm, "end": v(50919.91, 64060.92) * mm});
            skLineSegment(sketch, "E5422", {"start": v(50891.01, 64156.65) * mm, "end": v(50924.52, 64166.77) * mm});
            skLineSegment(sketch, "E5423", {"start": v(50924.52, 64166.77) * mm, "end": v(50953.42, 64071.04) * mm});
            skLineSegment(sketch, "E5424", {"start": v(50919.91, 64060.92) * mm, "end": v(50953.42, 64071.04) * mm});
            skLineSegment(sketch, "E5425", {"start": v(52026.4, 64499.4) * mm, "end": v(51992.9, 64489.3) * mm});
            skLineSegment(sketch, "E5426", {"start": v(50953.42, 64071.04) * mm, "end": v(50924.52, 64166.77) * mm});
            skArc(sketch, "E5427", {"start": v(51487.6, 64232.3) * mm, "mid": v(51589.98, 64040.15) * mm, "end": v(51758.1, 63901.8) * mm});
            skLineSegment(sketch, "E5428", {"start": v(52021.8, 64393.56) * mm, "end": v(51758.1, 63901.8) * mm});
            skLineSegment(sketch, "E5429", {"start": v(51758.1, 63901.8) * mm, "end": v(51718.92, 63922.8) * mm});
            skLineSegment(sketch, "E5430", {"start": v(51718.92, 63922.8) * mm, "end": v(51982.62, 64414.57) * mm});
            skLineSegment(sketch, "E5431", {"start": v(51982.62, 64414.57) * mm, "end": v(52021.8, 64393.56) * mm});
            skLineSegment(sketch, "E5432", {"start": v(51982.62, 64414.57) * mm, "end": v(51718.92, 63922.8) * mm});
            skLineSegment(sketch, "E5433", {"start": v(52021.8, 64393.56) * mm, "end": v(51982.62, 64414.57) * mm});
            skArc(sketch, "E5434", {"start": v(51445.18, 63807.34) * mm, "mid": v(51508.66, 64015.6) * mm, "end": v(51487.6, 64232.3) * mm});
            skLineSegment(sketch, "E5435", {"start": v(51445.18, 63807.34) * mm, "end": v(50953.42, 64071.04) * mm});
            skLineSegment(sketch, "E5436", {"start": v(50953.42, 64071.04) * mm, "end": v(50974.42, 64110.2) * mm});
            skLineSegment(sketch, "E5437", {"start": v(50974.42, 64110.2) * mm, "end": v(51466.18, 63846.51) * mm});
            skLineSegment(sketch, "E5438", {"start": v(51466.18, 63846.51) * mm, "end": v(51445.18, 63807.34) * mm});
            skLineSegment(sketch, "E5439", {"start": v(51466.18, 63846.51) * mm, "end": v(50974.42, 64110.2) * mm});
            skLineSegment(sketch, "E5440", {"start": v(51445.18, 63807.34) * mm, "end": v(51466.18, 63846.51) * mm});
            skLineSegment(sketch, "E5441", {"start": v(52056.03, 64401.28) * mm, "end": v(50920.63, 64058.53) * mm});
            skLineSegment(sketch, "E5442", {"start": v(52025.68, 64501.8) * mm, "end": v(50890.29, 64159.05) * mm});
            skLineSegment(sketch, "E5443", {"start": v(49577.68, 63706.93) * mm, "end": v(49345.24, 64474.7) * mm});
            skLineSegment(sketch, "E5444", {"start": v(49548.97, 63698.24) * mm, "end": v(49316.53, 64466) * mm});
            skLineSegment(sketch, "E5445", {"start": v(49625.54, 63721.42) * mm, "end": v(49393.1, 64489.19) * mm});
            skLineSegment(sketch, "E5446", {"start": v(49649.46, 63728.66) * mm, "end": v(49417.02, 64496.43) * mm});
            skLineSegment(sketch, "E5447", {"start": v(50910.74, 62922.3) * mm, "end": v(51049.83, 62462.9) * mm});
            skLineSegment(sketch, "E5448", {"start": v(50948.15, 62902.27) * mm, "end": v(51078.54, 62471.58) * mm});
            skLineSegment(sketch, "E5449", {"start": v(50848.4, 62955.66) * mm, "end": v(51001.97, 62448.4) * mm});
            skLineSegment(sketch, "E5450", {"start": v(50817.23, 62972.34) * mm, "end": v(50978.04, 62441.17) * mm});
            skLineSegment(sketch, "E5451", {"start": v(50939.46, 62930.98) * mm, "end": v(50910.74, 62922.3) * mm});
            skLineSegment(sketch, "E5452", {"start": v(50924.97, 62978.84) * mm, "end": v(50848.4, 62955.66) * mm});
            skLineSegment(sketch, "E5453", {"start": v(50917.72, 63002.77) * mm, "end": v(50817.23, 62972.34) * mm});
            skLineSegment(sketch, "E5454", {"start": v(53019.28, 63560.65) * mm, "end": v(52826.86, 63502.4) * mm});
            skLineSegment(sketch, "E5455", {"start": v(53027.97, 63531.93) * mm, "end": v(52835.55, 63473.68) * mm});
            skLineSegment(sketch, "E5456", {"start": v(53004.79, 63608.5) * mm, "end": v(52812.37, 63550.25) * mm});
            skLineSegment(sketch, "E5457", {"start": v(52997.54, 63632.43) * mm, "end": v(52805.12, 63574.17) * mm});
            skLineSegment(sketch, "E5458", {"start": v(51876.64, 63238.22) * mm, "end": v(51891.85, 63187.98) * mm});
            skLineSegment(sketch, "E5459", {"start": v(52820.34, 63523.93) * mm, "end": v(52835.55, 63473.68) * mm});
            skLineSegment(sketch, "E5460", {"start": v(51876.64, 63238.22) * mm, "end": v(51861.42, 63288.47) * mm});
            skLineSegment(sketch, "E5461", {"start": v(52820.34, 63523.93) * mm, "end": v(52805.12, 63574.17) * mm});
            skLineSegment(sketch, "E5462", {"start": v(52805.85, 63571.78) * mm, "end": v(52834.82, 63476.07) * mm});
            skLineSegment(sketch, "E5463", {"start": v(51862.15, 63286.08) * mm, "end": v(51891.13, 63190.37) * mm});
            skLineSegment(sketch, "E5464", {"start": v(52805.85, 63571.78) * mm, "end": v(52772.35, 63561.64) * mm});
            skLineSegment(sketch, "E5465", {"start": v(52772.35, 63561.64) * mm, "end": v(52801.33, 63465.93) * mm});
            skLineSegment(sketch, "E5466", {"start": v(52801.33, 63465.93) * mm, "end": v(52834.82, 63476.07) * mm});
            skLineSegment(sketch, "E5467", {"start": v(52834.82, 63476.07) * mm, "end": v(52805.85, 63571.78) * mm});
            skLineSegment(sketch, "E5468", {"start": v(51895.65, 63296.22) * mm, "end": v(51862.15, 63286.08) * mm});
            skLineSegment(sketch, "E5469", {"start": v(51891.13, 63190.37) * mm, "end": v(51924.62, 63200.5) * mm});
            skLineSegment(sketch, "E5470", {"start": v(51924.62, 63200.5) * mm, "end": v(51895.65, 63296.22) * mm});
            skLineSegment(sketch, "E5471", {"start": v(51862.15, 63286.08) * mm, "end": v(51895.65, 63296.22) * mm});
            skLineSegment(sketch, "E5472", {"start": v(52834.82, 63476.07) * mm, "end": v(52801.33, 63465.93) * mm});
            skLineSegment(sketch, "E5473", {"start": v(51895.65, 63296.22) * mm, "end": v(51924.62, 63200.5) * mm});
            skArc(sketch, "E5474", {"start": v(52334, 63428.93) * mm, "mid": v(53228.12, 63516.5) * mm, "end": v(52368.55, 63777.76) * mm});
            skLineSegment(sketch, "E5475", {"start": v(52772.35, 63561.64) * mm, "end": v(52368.55, 63777.76) * mm});
            skLineSegment(sketch, "E5476", {"start": v(52368.55, 63777.76) * mm, "end": v(52347.57, 63738.57) * mm});
            skLineSegment(sketch, "E5477", {"start": v(52347.57, 63738.57) * mm, "end": v(52751.38, 63522.45) * mm});
            skLineSegment(sketch, "E5478", {"start": v(52751.38, 63522.45) * mm, "end": v(52772.35, 63561.64) * mm});
            skLineSegment(sketch, "E5479", {"start": v(52751.38, 63522.45) * mm, "end": v(52347.57, 63738.57) * mm});
            skLineSegment(sketch, "E5480", {"start": v(52772.35, 63561.64) * mm, "end": v(52751.38, 63522.45) * mm});
            skArc(sketch, "E5481", {"start": v(52111.77, 63700.02) * mm, "mid": v(51541.45, 63005.86) * mm, "end": v(52334, 63428.93) * mm});
            skLineSegment(sketch, "E5482", {"start": v(52111.77, 63700.02) * mm, "end": v(51895.65, 63296.22) * mm});
            skLineSegment(sketch, "E5483", {"start": v(51895.65, 63296.22) * mm, "end": v(51934.84, 63275.24) * mm});
            skLineSegment(sketch, "E5484", {"start": v(51934.84, 63275.24) * mm, "end": v(52150.96, 63679.05) * mm});
            skLineSegment(sketch, "E5485", {"start": v(52150.96, 63679.05) * mm, "end": v(52111.77, 63700.02) * mm});
            skLineSegment(sketch, "E5486", {"start": v(52150.96, 63679.05) * mm, "end": v(51934.84, 63275.24) * mm});
            skLineSegment(sketch, "E5487", {"start": v(52111.77, 63700.02) * mm, "end": v(52150.96, 63679.05) * mm});
            skLineSegment(sketch, "E5488", {"start": v(52805.12, 63574.17) * mm, "end": v(51861.42, 63288.47) * mm});
            skLineSegment(sketch, "E5489", {"start": v(52835.55, 63473.68) * mm, "end": v(51891.85, 63187.98) * mm});
            skLineSegment(sketch, "E5490", {"start": v(50932.94, 62952.52) * mm, "end": v(50948.15, 62902.27) * mm});
            skLineSegment(sketch, "E5491", {"start": v(50932.94, 62952.52) * mm, "end": v(50917.72, 63002.77) * mm});
            skLineSegment(sketch, "E5492", {"start": v(50918.45, 63000.37) * mm, "end": v(50947.43, 62904.66) * mm});
            skLineSegment(sketch, "E5493", {"start": v(51862.15, 63286.08) * mm, "end": v(51828.65, 63275.94) * mm});
            skLineSegment(sketch, "E5494", {"start": v(51828.65, 63275.94) * mm, "end": v(51857.63, 63180.23) * mm});
            skLineSegment(sketch, "E5495", {"start": v(51857.63, 63180.23) * mm, "end": v(51891.13, 63190.37) * mm});
            skLineSegment(sketch, "E5496", {"start": v(51891.13, 63190.37) * mm, "end": v(51862.15, 63286.08) * mm});
            skLineSegment(sketch, "E5497", {"start": v(50951.95, 63010.52) * mm, "end": v(50918.45, 63000.37) * mm});
            skLineSegment(sketch, "E5498", {"start": v(50947.43, 62904.66) * mm, "end": v(50980.92, 62914.8) * mm});
            skLineSegment(sketch, "E5499", {"start": v(50980.92, 62914.8) * mm, "end": v(50951.95, 63010.52) * mm});
            skLineSegment(sketch, "E5500", {"start": v(50918.45, 63000.37) * mm, "end": v(50951.95, 63010.52) * mm});
            skLineSegment(sketch, "E5501", {"start": v(51891.13, 63190.37) * mm, "end": v(51857.63, 63180.23) * mm});
            skLineSegment(sketch, "E5502", {"start": v(50951.95, 63010.52) * mm, "end": v(50980.92, 62914.8) * mm});
            skArc(sketch, "E5503", {"start": v(51390.3, 63143.23) * mm, "mid": v(52284.42, 63230.8) * mm, "end": v(51424.85, 63492.06) * mm});
            skLineSegment(sketch, "E5504", {"start": v(51828.65, 63275.94) * mm, "end": v(51424.85, 63492.06) * mm});
            skLineSegment(sketch, "E5505", {"start": v(51424.85, 63492.06) * mm, "end": v(51403.87, 63452.87) * mm});
            skLineSegment(sketch, "E5506", {"start": v(51403.87, 63452.87) * mm, "end": v(51807.68, 63236.75) * mm});
            skLineSegment(sketch, "E5507", {"start": v(51807.68, 63236.75) * mm, "end": v(51828.65, 63275.94) * mm});
            skLineSegment(sketch, "E5508", {"start": v(51807.68, 63236.75) * mm, "end": v(51403.87, 63452.87) * mm});
            skLineSegment(sketch, "E5509", {"start": v(51828.65, 63275.94) * mm, "end": v(51807.68, 63236.75) * mm});
            skArc(sketch, "E5510", {"start": v(51168.07, 63414.32) * mm, "mid": v(50597.75, 62720.16) * mm, "end": v(51390.3, 63143.23) * mm});
            skLineSegment(sketch, "E5511", {"start": v(51168.07, 63414.32) * mm, "end": v(50951.95, 63010.52) * mm});
            skLineSegment(sketch, "E5512", {"start": v(50951.95, 63010.52) * mm, "end": v(50991.14, 62989.54) * mm});
            skLineSegment(sketch, "E5513", {"start": v(50991.14, 62989.54) * mm, "end": v(51207.26, 63393.34) * mm});
            skLineSegment(sketch, "E5514", {"start": v(51207.26, 63393.34) * mm, "end": v(51168.07, 63414.32) * mm});
            skLineSegment(sketch, "E5515", {"start": v(51207.26, 63393.34) * mm, "end": v(50991.14, 62989.54) * mm});
            skLineSegment(sketch, "E5516", {"start": v(51168.07, 63414.32) * mm, "end": v(51207.26, 63393.34) * mm});
            skLineSegment(sketch, "E5517", {"start": v(51861.42, 63288.47) * mm, "end": v(50917.72, 63002.77) * mm});
            skLineSegment(sketch, "E5518", {"start": v(51891.85, 63187.98) * mm, "end": v(50948.15, 62902.27) * mm});
            skLineSegment(sketch, "E5519", {"start": v(51739.1, 65225.54) * mm, "end": v(51558.73, 65821.45) * mm});
            skLineSegment(sketch, "E5520", {"start": v(51719.08, 65188.14) * mm, "end": v(51538.7, 65784.08) * mm});
            skLineSegment(sketch, "E5521", {"start": v(51772.47, 65287.89) * mm, "end": v(51592.12, 65883.73) * mm});
            skLineSegment(sketch, "E5522", {"start": v(51789.16, 65319.06) * mm, "end": v(51608.81, 65914.87) * mm});
            skLineSegment(sketch, "E5523", {"start": v(50740.07, 65574.8) * mm, "end": v(50919.35, 64982.6) * mm});
            skLineSegment(sketch, "E5524", {"start": v(50777.48, 65554.74) * mm, "end": v(50956.76, 64962.58) * mm});
            skLineSegment(sketch, "E5525", {"start": v(50677.7, 65608.23) * mm, "end": v(50857, 65015.97) * mm});
            skLineSegment(sketch, "E5526", {"start": v(50646.52, 65624.94) * mm, "end": v(50825.84, 65032.65) * mm});
            skLineSegment(sketch, "E5527", {"start": v(50805.32, 65594.46) * mm, "end": v(50740.07, 65574.8) * mm});
            skLineSegment(sketch, "E5528", {"start": v(50813.98, 65565.73) * mm, "end": v(50777.48, 65554.74) * mm});
            skLineSegment(sketch, "E5529", {"start": v(50790.9, 65642.33) * mm, "end": v(50677.7, 65608.23) * mm});
            skLineSegment(sketch, "E5530", {"start": v(50783.69, 65666.27) * mm, "end": v(50646.52, 65624.94) * mm});
            skLineSegment(sketch, "E5531", {"start": v(51558.73, 65821.45) * mm, "end": v(51485.14, 65799.27) * mm});
            skLineSegment(sketch, "E5532", {"start": v(51538.7, 65784.08) * mm, "end": v(51493.8, 65770.55) * mm});
            skLineSegment(sketch, "E5533", {"start": v(51592.12, 65883.73) * mm, "end": v(51470.72, 65847.15) * mm});
            skLineSegment(sketch, "E5534", {"start": v(51608.81, 65914.87) * mm, "end": v(51463.5, 65871.09) * mm});
            skLineSegment(sketch, "E5535", {"start": v(50783.69, 65666.27) * mm, "end": v(50813.98, 65565.73) * mm});
            skLineSegment(sketch, "E5536", {"start": v(51463.5, 65871.09) * mm, "end": v(51493.8, 65770.55) * mm});
            skLineSegment(sketch, "E5537", {"start": v(50783.69, 65666.27) * mm, "end": v(50823.9, 65678.38) * mm});
            skLineSegment(sketch, "E5538", {"start": v(50823.9, 65678.38) * mm, "end": v(50854.2, 65577.85) * mm});
            skLineSegment(sketch, "E5539", {"start": v(50854.2, 65577.85) * mm, "end": v(50813.98, 65565.73) * mm});
            skLineSegment(sketch, "E5540", {"start": v(50813.98, 65565.73) * mm, "end": v(50783.69, 65666.27) * mm});
            skLineSegment(sketch, "E5541", {"start": v(51423.3, 65858.97) * mm, "end": v(51463.5, 65871.09) * mm});
            skLineSegment(sketch, "E5542", {"start": v(51493.8, 65770.55) * mm, "end": v(51453.58, 65758.43) * mm});
            skLineSegment(sketch, "E5543", {"start": v(51453.58, 65758.43) * mm, "end": v(51423.3, 65858.97) * mm});
            skLineSegment(sketch, "E5544", {"start": v(51463.5, 65871.09) * mm, "end": v(51423.3, 65858.97) * mm});
            skLineSegment(sketch, "E5545", {"start": v(50813.98, 65565.73) * mm, "end": v(50854.2, 65577.85) * mm});
            skLineSegment(sketch, "E5546", {"start": v(51423.3, 65858.97) * mm, "end": v(51453.58, 65758.43) * mm});
            skArc(sketch, "E5547", {"start": v(51423.3, 65858.97) * mm, "mid": v(51308.56, 66074.6) * mm, "end": v(51120.04, 66229.9) * mm});
            skLineSegment(sketch, "E5548", {"start": v(50823.9, 65678.38) * mm, "end": v(51120.04, 66229.9) * mm});
            skLineSegment(sketch, "E5549", {"start": v(51120.04, 66229.9) * mm, "end": v(51159.2, 66208.88) * mm});
            skLineSegment(sketch, "E5550", {"start": v(51159.2, 66208.88) * mm, "end": v(50863.07, 65657.36) * mm});
            skLineSegment(sketch, "E5551", {"start": v(50863.07, 65657.36) * mm, "end": v(50823.9, 65678.38) * mm});
            skLineSegment(sketch, "E5552", {"start": v(50863.07, 65657.36) * mm, "end": v(51159.2, 66208.88) * mm});
            skLineSegment(sketch, "E5553", {"start": v(50823.9, 65678.38) * mm, "end": v(50863.07, 65657.36) * mm});
            skLineSegment(sketch, "E5554", {"start": v(52040.14, 65316.67) * mm, "end": v(51739.1, 65225.54) * mm});
            skLineSegment(sketch, "E5555", {"start": v(52048.83, 65287.95) * mm, "end": v(51719.08, 65188.14) * mm});
            skLineSegment(sketch, "E5556", {"start": v(52025.66, 65364.52) * mm, "end": v(51772.47, 65287.89) * mm});
            skLineSegment(sketch, "E5557", {"start": v(52018.42, 65388.45) * mm, "end": v(51789.16, 65319.06) * mm});
            skLineSegment(sketch, "E5558", {"start": v(49385.46, 61838.97) * mm, "end": v(49914.26, 60091.92) * mm});
            skLineSegment(sketch, "E5559", {"start": v(49414.17, 61847.66) * mm, "end": v(49942.97, 60100.61) * mm});
            skLineSegment(sketch, "E5560", {"start": v(49337.6, 61824.49) * mm, "end": v(49866.4, 60077.44) * mm});
            skLineSegment(sketch, "E5561", {"start": v(49313.68, 61817.24) * mm, "end": v(49842.47, 60070.2) * mm});
            skLineSegment(sketch, "E5562", {"start": v(44828.64, 65198.31) * mm, "end": v(41831.82, 67403.73) * mm});
            skLineSegment(sketch, "E5563", {"start": v(44528.04, 65152.58) * mm, "end": v(41704.38, 67230.56) * mm});
            skLineSegment(sketch, "E5564", {"start": v(38801.77, 57903.8) * mm, "end": v(42759, 59101.57) * mm});
            skLineSegment(sketch, "E5565", {"start": v(38739.49, 58109.58) * mm, "end": v(42490.93, 59245.07) * mm});
            skLineSegment(sketch, "E5566", {"start": v(36836.96, 64395.2) * mm, "end": v(40930.85, 69983.1) * mm});
            skLineSegment(sketch, "E5567", {"start": v(36600.07, 64435.67) * mm, "end": v(40852.93, 70240.53) * mm});
            skLineSegment(sketch, "E5568", {"start": v(41901.15, 62712.73) * mm, "end": v(37728.48, 61449.75) * mm});
            skLineSegment(sketch, "E5569", {"start": v(41963.43, 62506.95) * mm, "end": v(37790.77, 61243.97) * mm});
            skLineSegment(sketch, "E5570", {"start": v(41542.21, 62379.46) * mm, "end": v(37790.77, 61243.97) * mm});
            skLineSegment(sketch, "E5571", {"start": v(41963.43, 62506.95) * mm, "end": v(41748, 62441.74) * mm});
            skLineSegment(sketch, "E5572", {"start": v(42970.77, 63036.49) * mm, "end": v(42772.13, 62976.36) * mm});
            skLineSegment(sketch, "E5573", {"start": v(43130.3, 62860.14) * mm, "end": v(42834.41, 62770.58) * mm});
            skLineSegment(sketch, "E5574", {"start": v(42772.13, 62976.36) * mm, "end": v(42834.41, 62770.58) * mm});
            skLineSegment(sketch, "E5575", {"start": v(41901.15, 62712.73) * mm, "end": v(41963.43, 62506.95) * mm});
            skLineSegment(sketch, "E5576", {"start": v(42772.13, 62976.36) * mm, "end": v(42731.93, 62964.2) * mm});
            skLineSegment(sketch, "E5577", {"start": v(42731.93, 62964.2) * mm, "end": v(42794.21, 62758.41) * mm});
            skLineSegment(sketch, "E5578", {"start": v(42794.21, 62758.41) * mm, "end": v(42834.41, 62770.58) * mm});
            skLineSegment(sketch, "E5579", {"start": v(42834.41, 62770.58) * mm, "end": v(42772.13, 62976.36) * mm});
            skLineSegment(sketch, "E5580", {"start": v(41941.35, 62724.9) * mm, "end": v(41901.15, 62712.73) * mm});
            skLineSegment(sketch, "E5581", {"start": v(41963.43, 62506.95) * mm, "end": v(42003.63, 62519.12) * mm});
            skLineSegment(sketch, "E5582", {"start": v(42003.63, 62519.12) * mm, "end": v(41941.35, 62724.9) * mm});
            skLineSegment(sketch, "E5583", {"start": v(41901.15, 62712.73) * mm, "end": v(41941.35, 62724.9) * mm});
            skLineSegment(sketch, "E5584", {"start": v(42834.41, 62770.58) * mm, "end": v(42794.21, 62758.41) * mm});
            skLineSegment(sketch, "E5585", {"start": v(41941.35, 62724.9) * mm, "end": v(42003.63, 62519.12) * mm});
            skArc(sketch, "E5586", {"start": v(41941.35, 62724.9) * mm, "mid": v(43460.16, 62574.37) * mm, "end": v(42492.64, 63754.77) * mm});
            skLineSegment(sketch, "E5587", {"start": v(42731.93, 62964.2) * mm, "end": v(42492.64, 63754.77) * mm});
            skLineSegment(sketch, "E5588", {"start": v(42492.64, 63754.77) * mm, "end": v(42450.1, 63741.9) * mm});
            skLineSegment(sketch, "E5589", {"start": v(42450.1, 63741.9) * mm, "end": v(42689.38, 62951.32) * mm});
            skLineSegment(sketch, "E5590", {"start": v(42689.38, 62951.32) * mm, "end": v(42731.93, 62964.2) * mm});
            skLineSegment(sketch, "E5591", {"start": v(42689.38, 62951.32) * mm, "end": v(42450.1, 63741.9) * mm});
            skLineSegment(sketch, "E5592", {"start": v(42731.93, 62964.2) * mm, "end": v(42689.38, 62951.32) * mm});
            skLineSegment(sketch, "E5593", {"start": v(37824.84, 61131.4) * mm, "end": v(36836.96, 64395.2) * mm});
            skLineSegment(sketch, "E5594", {"start": v(37619.06, 61069.11) * mm, "end": v(36600.07, 64435.67) * mm});
            skLineSegment(sketch, "E5595", {"start": v(39129.82, 56820) * mm, "end": v(38088.47, 60260.42) * mm});
            skLineSegment(sketch, "E5596", {"start": v(38924.04, 56757.7) * mm, "end": v(37882.7, 60198.13) * mm});
            skLineSegment(sketch, "E5597", {"start": v(37824.84, 61131.4) * mm, "end": v(37619.06, 61069.11) * mm});
            skLineSegment(sketch, "E5598", {"start": v(38088.47, 60260.42) * mm, "end": v(37882.7, 60198.13) * mm});
            skLineSegment(sketch, "E5599", {"start": v(37824.84, 61131.4) * mm, "end": v(37837.01, 61091.2) * mm});
            skLineSegment(sketch, "E5600", {"start": v(37837.01, 61091.2) * mm, "end": v(37631.23, 61028.91) * mm});
            skLineSegment(sketch, "E5601", {"start": v(37631.23, 61028.91) * mm, "end": v(37619.06, 61069.11) * mm});
            skLineSegment(sketch, "E5602", {"start": v(37619.06, 61069.11) * mm, "end": v(37824.84, 61131.4) * mm});
            skLineSegment(sketch, "E5603", {"start": v(38076.3, 60300.62) * mm, "end": v(38088.47, 60260.42) * mm});
            skLineSegment(sketch, "E5604", {"start": v(37882.7, 60198.13) * mm, "end": v(37870.52, 60238.33) * mm});
            skLineSegment(sketch, "E5605", {"start": v(37870.52, 60238.33) * mm, "end": v(38076.3, 60300.62) * mm});
            skLineSegment(sketch, "E5606", {"start": v(38088.47, 60260.42) * mm, "end": v(38076.3, 60300.62) * mm});
            skLineSegment(sketch, "E5607", {"start": v(37619.06, 61069.11) * mm, "end": v(37631.23, 61028.91) * mm});
            skLineSegment(sketch, "E5608", {"start": v(38076.3, 60300.62) * mm, "end": v(37870.52, 60238.33) * mm});
            skArc(sketch, "E5609", {"start": v(38076.3, 60300.62) * mm, "mid": v(38565.24, 60701.38) * mm, "end": v(38627.6, 61330.49) * mm});
            skLineSegment(sketch, "E5610", {"start": v(37837.01, 61091.2) * mm, "end": v(38627.6, 61330.49) * mm});
            skLineSegment(sketch, "E5611", {"start": v(38627.6, 61330.49) * mm, "end": v(38640.47, 61287.95) * mm});
            skLineSegment(sketch, "E5612", {"start": v(38640.47, 61287.95) * mm, "end": v(37849.89, 61048.65) * mm});
            skLineSegment(sketch, "E5613", {"start": v(37849.89, 61048.65) * mm, "end": v(37837.01, 61091.2) * mm});
            skLineSegment(sketch, "E5614", {"start": v(37849.89, 61048.65) * mm, "end": v(38640.47, 61287.95) * mm});
            skLineSegment(sketch, "E5615", {"start": v(37837.01, 61091.2) * mm, "end": v(37849.89, 61048.65) * mm});
            skLineSegment(sketch, "E5616", {"start": v(41782.07, 62329.17) * mm, "end": v(41748, 62441.74) * mm});
            skLineSegment(sketch, "E5617", {"start": v(41576.29, 62266.88) * mm, "end": v(41542.21, 62379.46) * mm});
            skLineSegment(sketch, "E5618", {"start": v(42759, 59101.57) * mm, "end": v(42045.7, 61458.2) * mm});
            skLineSegment(sketch, "E5619", {"start": v(42490.93, 59245.07) * mm, "end": v(41839.92, 61395.9) * mm});
            skLineSegment(sketch, "E5620", {"start": v(42045.7, 61458.2) * mm, "end": v(41839.92, 61395.9) * mm});
            skLineSegment(sketch, "E5621", {"start": v(41782.07, 62329.17) * mm, "end": v(41576.29, 62266.88) * mm});
            skLineSegment(sketch, "E5622", {"start": v(41576.29, 62266.88) * mm, "end": v(41782.07, 62329.17) * mm});
            skLineSegment(sketch, "E5623", {"start": v(41839.92, 61395.9) * mm, "end": v(42045.7, 61458.2) * mm});
            skLineSegment(sketch, "E5624", {"start": v(41576.29, 62266.88) * mm, "end": v(41588.46, 62226.68) * mm});
            skLineSegment(sketch, "E5625", {"start": v(41588.46, 62226.68) * mm, "end": v(41794.24, 62288.97) * mm});
            skLineSegment(sketch, "E5626", {"start": v(41794.24, 62288.97) * mm, "end": v(41782.07, 62329.17) * mm});
            skLineSegment(sketch, "E5627", {"start": v(41827.75, 61436.1) * mm, "end": v(41839.92, 61395.9) * mm});
            skLineSegment(sketch, "E5628", {"start": v(42045.7, 61458.2) * mm, "end": v(42033.53, 61498.4) * mm});
            skLineSegment(sketch, "E5629", {"start": v(42033.53, 61498.4) * mm, "end": v(41827.75, 61436.1) * mm});
            skLineSegment(sketch, "E5630", {"start": v(41839.92, 61395.9) * mm, "end": v(41827.75, 61436.1) * mm});
            skLineSegment(sketch, "E5631", {"start": v(41782.07, 62329.17) * mm, "end": v(41794.24, 62288.97) * mm});
            skLineSegment(sketch, "E5632", {"start": v(41827.75, 61436.1) * mm, "end": v(42033.53, 61498.4) * mm});
            skArc(sketch, "E5633", {"start": v(41827.75, 61436.1) * mm, "mid": v(41978.28, 62954.91) * mm, "end": v(40797.88, 61987.4) * mm});
            skLineSegment(sketch, "E5634", {"start": v(41588.46, 62226.68) * mm, "end": v(40797.88, 61987.4) * mm});
            skLineSegment(sketch, "E5635", {"start": v(40797.88, 61987.4) * mm, "end": v(40810.75, 61944.85) * mm});
            skLineSegment(sketch, "E5636", {"start": v(40810.75, 61944.85) * mm, "end": v(41601.33, 62184.14) * mm});
            skLineSegment(sketch, "E5637", {"start": v(41601.33, 62184.14) * mm, "end": v(41588.46, 62226.68) * mm});
            skLineSegment(sketch, "E5638", {"start": v(41601.33, 62184.14) * mm, "end": v(40810.75, 61944.85) * mm});
            skLineSegment(sketch, "E5639", {"start": v(41588.46, 62226.68) * mm, "end": v(41601.33, 62184.14) * mm});
            skLineSegment(sketch, "E5640", {"start": v(44528.04, 65152.58) * mm, "end": v(42970.77, 63036.49) * mm});
            skLineSegment(sketch, "E5641", {"start": v(44828.64, 65198.31) * mm, "end": v(43282.95, 63097.96) * mm});
            skLineSegment(sketch, "E5642", {"start": v(43355.67, 62857.7) * mm, "end": v(43282.95, 63097.96) * mm});
            skLineSegment(sketch, "E5643", {"start": v(43149.9, 62795.42) * mm, "end": v(43130.3, 62860.14) * mm});
            skLineSegment(sketch, "E5644", {"start": v(43746, 61568.17) * mm, "end": v(43648.27, 61891.02) * mm});
            skLineSegment(sketch, "E5645", {"start": v(43540.21, 61505.88) * mm, "end": v(43442.5, 61828.73) * mm});
            skLineSegment(sketch, "E5646", {"start": v(43545.38, 61859.88) * mm, "end": v(43648.27, 61891.02) * mm});
            skLineSegment(sketch, "E5647", {"start": v(43252.78, 62826.56) * mm, "end": v(43355.67, 62857.7) * mm});
            skLineSegment(sketch, "E5648", {"start": v(43545.38, 61859.88) * mm, "end": v(43442.5, 61828.73) * mm});
            skLineSegment(sketch, "E5649", {"start": v(43252.78, 62826.56) * mm, "end": v(43149.9, 62795.42) * mm});
            skLineSegment(sketch, "E5650", {"start": v(43149.9, 62795.42) * mm, "end": v(43355.67, 62857.7) * mm});
            skLineSegment(sketch, "E5651", {"start": v(43442.5, 61828.73) * mm, "end": v(43648.27, 61891.02) * mm});
            skLineSegment(sketch, "E5652", {"start": v(43149.9, 62795.42) * mm, "end": v(43158.58, 62766.7) * mm});
            skLineSegment(sketch, "E5653", {"start": v(43158.58, 62766.7) * mm, "end": v(43364.36, 62829) * mm});
            skLineSegment(sketch, "E5654", {"start": v(43364.36, 62829) * mm, "end": v(43355.67, 62857.7) * mm});
            skLineSegment(sketch, "E5655", {"start": v(43355.67, 62857.7) * mm, "end": v(43149.9, 62795.42) * mm});
            skLineSegment(sketch, "E5656", {"start": v(43433.8, 61857.45) * mm, "end": v(43442.5, 61828.73) * mm});
            skLineSegment(sketch, "E5657", {"start": v(43648.27, 61891.02) * mm, "end": v(43639.58, 61919.73) * mm});
            skLineSegment(sketch, "E5658", {"start": v(43639.58, 61919.73) * mm, "end": v(43433.8, 61857.45) * mm});
            skLineSegment(sketch, "E5659", {"start": v(43442.5, 61828.73) * mm, "end": v(43433.8, 61857.45) * mm});
            skLineSegment(sketch, "E5660", {"start": v(43355.67, 62857.7) * mm, "end": v(43364.36, 62829) * mm});
            skLineSegment(sketch, "E5661", {"start": v(43433.8, 61857.45) * mm, "end": v(43639.58, 61919.73) * mm});
            skLineSegment(sketch, "E5662", {"start": v(43149.9, 62795.42) * mm, "end": v(43442.5, 61828.73) * mm});
            skLineSegment(sketch, "E5663", {"start": v(43355.67, 62857.7) * mm, "end": v(43648.27, 61891.02) * mm});
            skLineSegment(sketch, "E5664", {"start": v(51034.23, 60515.14) * mm, "end": v(51135.12, 60546.2) * mm});
            skLineSegment(sketch, "E5665", {"start": v(51025.4, 60543.8) * mm, "end": v(51126.29, 60574.88) * mm});
            skLineSegment(sketch, "E5666", {"start": v(51048.94, 60467.35) * mm, "end": v(51149.83, 60498.42) * mm});
            skLineSegment(sketch, "E5667", {"start": v(51056.3, 60443.46) * mm, "end": v(51157.19, 60474.53) * mm});
            skLineSegment(sketch, "E5668", {"start": v(49920.9, 60172.3) * mm, "end": v(50355.67, 60306.18) * mm});
            skLineSegment(sketch, "E5669", {"start": v(49912.07, 60200.96) * mm, "end": v(50346.84, 60334.85) * mm});
            skLineSegment(sketch, "E5670", {"start": v(49935.61, 60124.5) * mm, "end": v(50370.39, 60258.4) * mm});
            skLineSegment(sketch, "E5671", {"start": v(49942.97, 60100.61) * mm, "end": v(50377.75, 60234.5) * mm});
            skLineSegment(sketch, "E5672", {"start": v(50346.84, 60334.85) * mm, "end": v(50377.75, 60234.5) * mm});
            skLineSegment(sketch, "E5673", {"start": v(51025.4, 60543.8) * mm, "end": v(51056.3, 60443.46) * mm});
            skLineSegment(sketch, "E5674", {"start": v(50346.84, 60334.85) * mm, "end": v(50386.98, 60347.21) * mm});
            skLineSegment(sketch, "E5675", {"start": v(50386.98, 60347.21) * mm, "end": v(50417.89, 60246.86) * mm});
            skLineSegment(sketch, "E5676", {"start": v(50417.89, 60246.86) * mm, "end": v(50377.75, 60234.5) * mm});
            skLineSegment(sketch, "E5677", {"start": v(50377.75, 60234.5) * mm, "end": v(50346.84, 60334.85) * mm});
            skLineSegment(sketch, "E5678", {"start": v(50985.26, 60531.45) * mm, "end": v(51025.4, 60543.8) * mm});
            skLineSegment(sketch, "E5679", {"start": v(51056.3, 60443.46) * mm, "end": v(51016.16, 60431.1) * mm});
            skLineSegment(sketch, "E5680", {"start": v(51016.16, 60431.1) * mm, "end": v(50985.26, 60531.45) * mm});
            skLineSegment(sketch, "E5681", {"start": v(51025.4, 60543.8) * mm, "end": v(50985.26, 60531.45) * mm});
            skLineSegment(sketch, "E5682", {"start": v(50377.75, 60234.5) * mm, "end": v(50417.89, 60246.86) * mm});
            skLineSegment(sketch, "E5683", {"start": v(50985.26, 60531.45) * mm, "end": v(51016.16, 60431.1) * mm});
            skArc(sketch, "E5684", {"start": v(50985.26, 60531.45) * mm, "mid": v(50869.21, 60746.37) * mm, "end": v(50679.75, 60900.53) * mm});
            skLineSegment(sketch, "E5685", {"start": v(50386.98, 60347.21) * mm, "end": v(50679.75, 60900.53) * mm});
            skLineSegment(sketch, "E5686", {"start": v(50679.75, 60900.53) * mm, "end": v(50719.04, 60879.74) * mm});
            skLineSegment(sketch, "E5687", {"start": v(50719.04, 60879.74) * mm, "end": v(50426.27, 60326.42) * mm});
            skLineSegment(sketch, "E5688", {"start": v(50426.27, 60326.42) * mm, "end": v(50386.98, 60347.21) * mm});
            skLineSegment(sketch, "E5689", {"start": v(50426.27, 60326.42) * mm, "end": v(50719.04, 60879.74) * mm});
            skLineSegment(sketch, "E5690", {"start": v(50386.98, 60347.21) * mm, "end": v(50426.27, 60326.42) * mm});
            skLineSegment(sketch, "E5691", {"start": v(51097.57, 60566.19) * mm, "end": v(51633.9, 58794.25) * mm});
            skLineSegment(sketch, "E5692", {"start": v(51126.29, 60574.88) * mm, "end": v(51662.62, 58802.94) * mm});
            skLineSegment(sketch, "E5693", {"start": v(51049.72, 60551.7) * mm, "end": v(51586.05, 58779.77) * mm});
            skLineSegment(sketch, "E5694", {"start": v(51025.79, 60544.46) * mm, "end": v(51562.12, 58772.53) * mm});
            skLineSegment(sketch, "E5695", {"start": v(39876.73, 73465.62) * mm, "end": v(41669.06, 67544.29) * mm});
            skLineSegment(sketch, "E5696", {"start": v(40082.5, 73527.9) * mm, "end": v(41874.84, 67606.57) * mm});
            skLineSegment(sketch, "E5697", {"start": v(40930.85, 69983.1) * mm, "end": v(41669.06, 67544.29) * mm});
            skLineSegment(sketch, "E5698", {"start": v(39876.73, 73465.62) * mm, "end": v(40852.93, 70240.53) * mm});
            skLineSegment(sketch, "E5699", {"start": v(36993.44, 52881.57) * mm, "end": v(36668.63, 53953.44) * mm});
            skLineSegment(sketch, "E5700", {"start": v(36701.98, 54015.8) * mm, "end": v(37333.62, 54207.2) * mm});
            skLineSegment(sketch, "E5701", {"start": v(37395.97, 54173.85) * mm, "end": v(37720.78, 53101.98) * mm});
            skLineSegment(sketch, "E5702", {"start": v(37687.43, 53039.63) * mm, "end": v(37055.8, 52848.22) * mm});
            skCircle(sketch, "E5703", {"center": v(37194.75, 53527.73) * mm, "radius": 311.76 * mm});
            skLineSegment(sketch, "E5704", {"start": v(37055.8, 52848.22) * mm, "end": v(36993.44, 52881.57) * mm});
            skLineSegment(sketch, "E5705", {"start": v(37687.43, 53039.63) * mm, "end": v(37720.78, 53101.98) * mm});
            skLineSegment(sketch, "E5706", {"start": v(36701.98, 54015.8) * mm, "end": v(36668.63, 53953.44) * mm});
            skLineSegment(sketch, "E5707", {"start": v(37333.62, 54207.2) * mm, "end": v(37395.97, 54173.85) * mm});
            skCircle(sketch, "E5708", {"center": v(37194.75, 53527.73) * mm, "radius": 69.13 * mm});
            skCircle(sketch, "E5709", {"center": v(37194.75, 53527.73) * mm, "radius": 109.13 * mm});
            skCircle(sketch, "E5710", {"center": v(37194.75, 53527.73) * mm, "radius": 149.13 * mm});
            skCircle(sketch, "E5711", {"center": v(37194.75, 53527.73) * mm, "radius": 189.13 * mm});
            skCircle(sketch, "E5712", {"center": v(37194.75, 53527.73) * mm, "radius": 229.13 * mm});
            skCircle(sketch, "E5713", {"center": v(37194.75, 53527.73) * mm, "radius": 269.13 * mm});
            skLineSegment(sketch, "E5714", {"start": v(37128.59, 53507.68) * mm, "end": v(37090.3, 53496.08) * mm});
            skLineSegment(sketch, "E5715", {"start": v(37143.28, 53431.5) * mm, "end": v(37124.41, 53396.22) * mm});
            skLineSegment(sketch, "E5716", {"start": v(37238, 53385) * mm, "end": v(37249.6, 53346.72) * mm});
            skLineSegment(sketch, "E5717", {"start": v(37361.53, 53438.52) * mm, "end": v(37396.8, 53419.66) * mm});
            skLineSegment(sketch, "E5718", {"start": v(37414.04, 53594.18) * mm, "end": v(37452.32, 53605.78) * mm});
            skLineSegment(sketch, "E5719", {"start": v(37321.69, 53765.05) * mm, "end": v(37341.8, 53802.63) * mm});
            skLineSegment(sketch, "E5720", {"start": v(37147.48, 53477.28) * mm, "end": v(37120.13, 53448.1) * mm});
            skLineSegment(sketch, "E5721", {"start": v(37198.3, 53418.65) * mm, "end": v(37199.6, 53378.67) * mm});
            skLineSegment(sketch, "E5722", {"start": v(37303.57, 53425.75) * mm, "end": v(37332.76, 53398.4) * mm});
            skLineSegment(sketch, "E5723", {"start": v(37383.79, 53533.86) * mm, "end": v(37423.77, 53535.16) * mm});
            skLineSegment(sketch, "E5724", {"start": v(37351.43, 53694.92) * mm, "end": v(37378.79, 53724.1) * mm});
            skLineSegment(sketch, "E5725", {"start": v(37186.02, 53796.72) * mm, "end": v(37184.64, 53839.32) * mm});
            skLineSegment(sketch, "E5726", {"start": v(37179.03, 53460.4) * mm, "end": v(37169.94, 53421.45) * mm});
            skLineSegment(sketch, "E5727", {"start": v(37252.36, 53435.03) * mm, "end": v(37273.47, 53401.06) * mm});
            skLineSegment(sketch, "E5728", {"start": v(37339.98, 53493.82) * mm, "end": v(37378.93, 53484.73) * mm});
            skLineSegment(sketch, "E5729", {"start": v(37355.4, 53627.56) * mm, "end": v(37389.37, 53648.67) * mm});
            skLineSegment(sketch, "E5730", {"start": v(37246.85, 53750.86) * mm, "end": v(37255.94, 53789.81) * mm});
            skLineSegment(sketch, "E5731", {"start": v(37052.7, 53756.32) * mm, "end": v(37030.2, 53792.52) * mm});
            skLineSegment(sketch, "E5732", {"start": v(37214.8, 53461.56) * mm, "end": v(37226.4, 53423.28) * mm});
            skLineSegment(sketch, "E5733", {"start": v(37290.99, 53476.25) * mm, "end": v(37326.26, 53457.39) * mm});
            skLineSegment(sketch, "E5734", {"start": v(37337.48, 53570.98) * mm, "end": v(37375.76, 53582.58) * mm});
            skLineSegment(sketch, "E5735", {"start": v(37283.96, 53694.5) * mm, "end": v(37302.82, 53729.77) * mm});
            skLineSegment(sketch, "E5736", {"start": v(37128.3, 53747.01) * mm, "end": v(37116.7, 53785.3) * mm});
            skLineSegment(sketch, "E5737", {"start": v(36957.43, 53654.66) * mm, "end": v(36919.85, 53674.77) * mm});
            skLineSegment(sketch, "E5738", {"start": v(37245.2, 53480.45) * mm, "end": v(37274.39, 53453.1) * mm});
            skLineSegment(sketch, "E5739", {"start": v(37303.83, 53531.27) * mm, "end": v(37343.8, 53532.56) * mm});
            skLineSegment(sketch, "E5740", {"start": v(37296.73, 53636.54) * mm, "end": v(37324.08, 53665.73) * mm});
            skLineSegment(sketch, "E5741", {"start": v(37188.62, 53716.76) * mm, "end": v(37187.32, 53756.74) * mm});
            skLineSegment(sketch, "E5742", {"start": v(37027.56, 53684.4) * mm, "end": v(36998.37, 53711.76) * mm});
            skLineSegment(sketch, "E5743", {"start": v(36925.76, 53519) * mm, "end": v(36883.16, 53517.61) * mm});
            skLineSegment(sketch, "E5744", {"start": v(37262.08, 53512) * mm, "end": v(37301.03, 53502.91) * mm});
            skLineSegment(sketch, "E5745", {"start": v(37287.45, 53585.33) * mm, "end": v(37321.42, 53606.44) * mm});
            skLineSegment(sketch, "E5746", {"start": v(37228.66, 53672.95) * mm, "end": v(37237.75, 53711.9) * mm});
            skLineSegment(sketch, "E5747", {"start": v(37094.92, 53688.37) * mm, "end": v(37073.8, 53722.34) * mm});
            skLineSegment(sketch, "E5748", {"start": v(36971.62, 53579.82) * mm, "end": v(36932.67, 53588.91) * mm});
            skLineSegment(sketch, "E5749", {"start": v(36966.16, 53385.67) * mm, "end": v(36929.96, 53363.17) * mm});
            skLineSegment(sketch, "E5750", {"start": v(37260.92, 53547.78) * mm, "end": v(37299.2, 53559.38) * mm});
            skLineSegment(sketch, "E5751", {"start": v(37246.23, 53623.96) * mm, "end": v(37265.1, 53659.23) * mm});
            skLineSegment(sketch, "E5752", {"start": v(37151.5, 53670.45) * mm, "end": v(37139.9, 53708.73) * mm});
            skLineSegment(sketch, "E5753", {"start": v(37027.98, 53616.93) * mm, "end": v(36992.7, 53635.8) * mm});
            skLineSegment(sketch, "E5754", {"start": v(36975.47, 53461.27) * mm, "end": v(36937.19, 53449.67) * mm});
            skLineSegment(sketch, "E5755", {"start": v(37067.82, 53290.4) * mm, "end": v(37047.71, 53252.82) * mm});
            skLineSegment(sketch, "E5756", {"start": v(37242.03, 53578.17) * mm, "end": v(37269.38, 53607.36) * mm});
            skLineSegment(sketch, "E5757", {"start": v(37191.21, 53636.8) * mm, "end": v(37189.92, 53676.78) * mm});
            skLineSegment(sketch, "E5758", {"start": v(37085.93, 53629.7) * mm, "end": v(37056.75, 53657.06) * mm});
            skLineSegment(sketch, "E5759", {"start": v(37005.72, 53521.6) * mm, "end": v(36965.74, 53520.3) * mm});
            skLineSegment(sketch, "E5760", {"start": v(37038.07, 53360.53) * mm, "end": v(37010.72, 53331.35) * mm});
            skLineSegment(sketch, "E5761", {"start": v(37203.48, 53258.73) * mm, "end": v(37204.86, 53216.13) * mm});
            skLineSegment(sketch, "E5762", {"start": v(37210.47, 53595.05) * mm, "end": v(37219.56, 53634) * mm});
            skLineSegment(sketch, "E5763", {"start": v(37137.15, 53620.42) * mm, "end": v(37116.04, 53654.4) * mm});
            skLineSegment(sketch, "E5764", {"start": v(37049.52, 53561.63) * mm, "end": v(37010.57, 53570.73) * mm});
            skLineSegment(sketch, "E5765", {"start": v(37034.11, 53427.9) * mm, "end": v(37000.14, 53406.78) * mm});
            skLineSegment(sketch, "E5766", {"start": v(37142.66, 53304.6) * mm, "end": v(37133.56, 53265.64) * mm});
            skLineSegment(sketch, "E5767", {"start": v(37336.8, 53299.14) * mm, "end": v(37359.3, 53262.93) * mm});
            skLineSegment(sketch, "E5768", {"start": v(37174.7, 53593.89) * mm, "end": v(37163.1, 53632.17) * mm});
            skLineSegment(sketch, "E5769", {"start": v(37098.52, 53579.2) * mm, "end": v(37063.25, 53598.06) * mm});
            skLineSegment(sketch, "E5770", {"start": v(37052.03, 53484.47) * mm, "end": v(37013.75, 53472.87) * mm});
            skLineSegment(sketch, "E5771", {"start": v(37105.55, 53360.95) * mm, "end": v(37086.68, 53325.68) * mm});
            skLineSegment(sketch, "E5772", {"start": v(37261.2, 53308.44) * mm, "end": v(37272.8, 53270.16) * mm});
            skLineSegment(sketch, "E5773", {"start": v(37432.07, 53400.79) * mm, "end": v(37469.66, 53380.69) * mm});
            skLineSegment(sketch, "E5774", {"start": v(37144.3, 53575) * mm, "end": v(37115.12, 53602.35) * mm});
            skLineSegment(sketch, "E5775", {"start": v(37085.68, 53524.19) * mm, "end": v(37045.7, 53522.89) * mm});
            skLineSegment(sketch, "E5776", {"start": v(37092.77, 53418.9) * mm, "end": v(37065.42, 53389.72) * mm});
            skLineSegment(sketch, "E5777", {"start": v(37200.89, 53338.7) * mm, "end": v(37202.19, 53298.71) * mm});
            skLineSegment(sketch, "E5778", {"start": v(37361.95, 53371.04) * mm, "end": v(37391.13, 53343.7) * mm});
            skLineSegment(sketch, "E5779", {"start": v(37463.75, 53536.46) * mm, "end": v(37506.35, 53537.84) * mm});
            skLineSegment(sketch, "E5780", {"start": v(37127.43, 53543.44) * mm, "end": v(37088.48, 53552.54) * mm});
            skLineSegment(sketch, "E5781", {"start": v(37102.06, 53470.12) * mm, "end": v(37068.09, 53449) * mm});
            skLineSegment(sketch, "E5782", {"start": v(37160.85, 53382.5) * mm, "end": v(37151.75, 53343.54) * mm});
            skLineSegment(sketch, "E5783", {"start": v(37294.58, 53367.08) * mm, "end": v(37315.7, 53333.1) * mm});
            skLineSegment(sketch, "E5784", {"start": v(37417.89, 53475.63) * mm, "end": v(37456.84, 53466.54) * mm});
            skLineSegment(sketch, "E5785", {"start": v(37423.34, 53669.78) * mm, "end": v(37459.55, 53692.28) * mm});
            skLineSegment(sketch, "E5786", {"start": v(37555.95, 53315.23) * mm, "end": v(37540.5, 53326.25) * mm});
            skLineSegment(sketch, "E5787", {"start": v(37533.93, 53290.45) * mm, "end": v(37544.66, 53281.43) * mm});
            skLineSegment(sketch, "E5788", {"start": v(37544.66, 53281.43) * mm, "end": v(37502.86, 53271.2) * mm});
            skLineSegment(sketch, "E5789", {"start": v(37502.86, 53271.2) * mm, "end": v(37515.02, 53307.95) * mm});
            skLineSegment(sketch, "E5790", {"start": v(37515.02, 53307.95) * mm, "end": v(37526.56, 53298.32) * mm});
            skLineSegment(sketch, "E5791", {"start": v(36833.56, 53740.22) * mm, "end": v(36849, 53729.2) * mm});
            skLineSegment(sketch, "E5792", {"start": v(36855.58, 53765) * mm, "end": v(36844.84, 53774.03) * mm});
            skLineSegment(sketch, "E5793", {"start": v(36844.84, 53774.03) * mm, "end": v(36886.65, 53784.25) * mm});
            skLineSegment(sketch, "E5794", {"start": v(36886.65, 53784.25) * mm, "end": v(36874.48, 53747.5) * mm});
            skLineSegment(sketch, "E5795", {"start": v(36874.48, 53747.5) * mm, "end": v(36862.95, 53757.14) * mm});
            skCircle(sketch, "E5796", {"center": v(37364.27, 52968.16) * mm, "radius": 7.85 * mm});
            skCircle(sketch, "E5797", {"center": v(37224.84, 52925.9) * mm, "radius": 7.85 * mm});
            skCircle(sketch, "E5798", {"center": v(37096.17, 52886.9) * mm, "radius": 7.85 * mm});
            skCircle(sketch, "E5799", {"center": v(37503.7, 53010.4) * mm, "radius": 7.85 * mm});
            skCircle(sketch, "E5800", {"center": v(37632.38, 53049.4) * mm, "radius": 7.85 * mm});
            skCircle(sketch, "E5801", {"center": v(37025.14, 54087.27) * mm, "radius": 7.85 * mm});
            skCircle(sketch, "E5802", {"center": v(36885.7, 54045.01) * mm, "radius": 7.85 * mm});
            skCircle(sketch, "E5803", {"center": v(36757.04, 54006.02) * mm, "radius": 7.85 * mm});
            skCircle(sketch, "E5804", {"center": v(37164.57, 54129.52) * mm, "radius": 7.85 * mm});
            skCircle(sketch, "E5805", {"center": v(37293.24, 54168.51) * mm, "radius": 7.85 * mm});
            skLineSegment(sketch, "E5806", {"start": v(36611.33, 54145.17) * mm, "end": v(36375.28, 54930.46) * mm});
            skLineSegment(sketch, "E5807", {"start": v(36408.77, 54992.74) * mm, "end": v(37040.84, 55182.73) * mm});
            skLineSegment(sketch, "E5808", {"start": v(37103.11, 55149.24) * mm, "end": v(37339.16, 54363.95) * mm});
            skLineSegment(sketch, "E5809", {"start": v(37305.67, 54301.67) * mm, "end": v(36673.6, 54111.68) * mm});
            skCircle(sketch, "E5810", {"center": v(36857.22, 54647.2) * mm, "radius": 311.76 * mm});
            skLineSegment(sketch, "E5811", {"start": v(36673.6, 54111.68) * mm, "end": v(36611.33, 54145.17) * mm});
            skLineSegment(sketch, "E5812", {"start": v(37305.67, 54301.67) * mm, "end": v(37339.16, 54363.95) * mm});
            skLineSegment(sketch, "E5813", {"start": v(36408.77, 54992.74) * mm, "end": v(36375.28, 54930.46) * mm});
            skLineSegment(sketch, "E5814", {"start": v(37040.84, 55182.73) * mm, "end": v(37103.11, 55149.24) * mm});
            skCircle(sketch, "E5815", {"center": v(36857.22, 54647.2) * mm, "radius": 69.13 * mm});
            skCircle(sketch, "E5816", {"center": v(36857.22, 54647.2) * mm, "radius": 109.13 * mm});
            skCircle(sketch, "E5817", {"center": v(36857.22, 54647.2) * mm, "radius": 149.13 * mm});
            skCircle(sketch, "E5818", {"center": v(36857.22, 54647.2) * mm, "radius": 189.13 * mm});
            skCircle(sketch, "E5819", {"center": v(36857.22, 54647.2) * mm, "radius": 229.13 * mm});
            skCircle(sketch, "E5820", {"center": v(36857.22, 54647.2) * mm, "radius": 269.13 * mm});
            skLineSegment(sketch, "E5821", {"start": v(36791.01, 54627.3) * mm, "end": v(36752.7, 54615.8) * mm});
            skLineSegment(sketch, "E5822", {"start": v(36805.53, 54551.09) * mm, "end": v(36786.59, 54515.86) * mm});
            skLineSegment(sketch, "E5823", {"start": v(36900.15, 54504.39) * mm, "end": v(36911.67, 54466.08) * mm});
            skLineSegment(sketch, "E5824", {"start": v(37023.8, 54557.63) * mm, "end": v(37059.03, 54538.68) * mm});
            skLineSegment(sketch, "E5825", {"start": v(37076.66, 54713.17) * mm, "end": v(37114.96, 54724.68) * mm});
            skLineSegment(sketch, "E5826", {"start": v(36984.7, 54884.24) * mm, "end": v(37004.88, 54921.78) * mm});
            skLineSegment(sketch, "E5827", {"start": v(36809.84, 54596.87) * mm, "end": v(36782.42, 54567.74) * mm});
            skLineSegment(sketch, "E5828", {"start": v(36860.52, 54538.12) * mm, "end": v(36861.73, 54498.14) * mm});
            skLineSegment(sketch, "E5829", {"start": v(36965.81, 54544.99) * mm, "end": v(36994.94, 54517.57) * mm});
            skLineSegment(sketch, "E5830", {"start": v(37046.27, 54652.92) * mm, "end": v(37086.25, 54654.13) * mm});
            skLineSegment(sketch, "E5831", {"start": v(37014.28, 54814.05) * mm, "end": v(37041.7, 54843.17) * mm});
            skLineSegment(sketch, "E5832", {"start": v(36849.1, 54916.22) * mm, "end": v(36847.8, 54958.82) * mm});
            skLineSegment(sketch, "E5833", {"start": v(36841.35, 54579.92) * mm, "end": v(36832.17, 54540.99) * mm});
            skLineSegment(sketch, "E5834", {"start": v(36914.62, 54554.38) * mm, "end": v(36935.66, 54520.36) * mm});
            skLineSegment(sketch, "E5835", {"start": v(37002.38, 54612.98) * mm, "end": v(37041.3, 54603.8) * mm});
            skLineSegment(sketch, "E5836", {"start": v(37018.09, 54746.68) * mm, "end": v(37052.1, 54767.71) * mm});
            skLineSegment(sketch, "E5837", {"start": v(36909.82, 54870.22) * mm, "end": v(36919, 54909.16) * mm});
            skLineSegment(sketch, "E5838", {"start": v(36715.68, 54876.12) * mm, "end": v(36693.26, 54912.37) * mm});
            skLineSegment(sketch, "E5839", {"start": v(36877.12, 54581) * mm, "end": v(36888.64, 54542.7) * mm});
            skLineSegment(sketch, "E5840", {"start": v(36953.34, 54595.52) * mm, "end": v(36988.57, 54576.57) * mm});
            skLineSegment(sketch, "E5841", {"start": v(37000.04, 54690.14) * mm, "end": v(37038.35, 54701.65) * mm});
            skLineSegment(sketch, "E5842", {"start": v(36946.8, 54813.78) * mm, "end": v(36965.75, 54849.01) * mm});
            skLineSegment(sketch, "E5843", {"start": v(36791.26, 54866.64) * mm, "end": v(36779.75, 54904.95) * mm});
            skLineSegment(sketch, "E5844", {"start": v(36620.19, 54774.68) * mm, "end": v(36582.65, 54794.86) * mm});
            skLineSegment(sketch, "E5845", {"start": v(36907.56, 54599.82) * mm, "end": v(36936.69, 54572.4) * mm});
            skLineSegment(sketch, "E5846", {"start": v(36966.3, 54650.5) * mm, "end": v(37006.29, 54651.71) * mm});
            skLineSegment(sketch, "E5847", {"start": v(36959.44, 54755.8) * mm, "end": v(36986.86, 54784.92) * mm});
            skLineSegment(sketch, "E5848", {"start": v(36851.51, 54836.26) * mm, "end": v(36850.3, 54876.24) * mm});
            skLineSegment(sketch, "E5849", {"start": v(36690.38, 54804.26) * mm, "end": v(36661.26, 54831.68) * mm});
            skLineSegment(sketch, "E5850", {"start": v(36588.21, 54639.08) * mm, "end": v(36545.6, 54637.8) * mm});
            skLineSegment(sketch, "E5851", {"start": v(36924.51, 54631.34) * mm, "end": v(36963.44, 54622.16) * mm});
            skLineSegment(sketch, "E5852", {"start": v(36950.05, 54704.6) * mm, "end": v(36984.07, 54725.64) * mm});
            skLineSegment(sketch, "E5853", {"start": v(36891.45, 54792.36) * mm, "end": v(36900.64, 54831.3) * mm});
            skLineSegment(sketch, "E5854", {"start": v(36757.75, 54808.07) * mm, "end": v(36736.72, 54842.1) * mm});
            skLineSegment(sketch, "E5855", {"start": v(36634.2, 54699.8) * mm, "end": v(36595.27, 54708.98) * mm});
            skLineSegment(sketch, "E5856", {"start": v(36628.31, 54505.66) * mm, "end": v(36592.06, 54483.25) * mm});
            skLineSegment(sketch, "E5857", {"start": v(36923.43, 54667.1) * mm, "end": v(36961.74, 54678.62) * mm});
            skLineSegment(sketch, "E5858", {"start": v(36908.91, 54743.33) * mm, "end": v(36927.86, 54778.55) * mm});
            skLineSegment(sketch, "E5859", {"start": v(36814.3, 54790.03) * mm, "end": v(36802.78, 54828.34) * mm});
            skLineSegment(sketch, "E5860", {"start": v(36690.65, 54736.79) * mm, "end": v(36655.42, 54755.73) * mm});
            skLineSegment(sketch, "E5861", {"start": v(36637.79, 54581.25) * mm, "end": v(36599.48, 54569.73) * mm});
            skLineSegment(sketch, "E5862", {"start": v(36729.75, 54410.17) * mm, "end": v(36709.57, 54372.63) * mm});
            skLineSegment(sketch, "E5863", {"start": v(36904.6, 54697.55) * mm, "end": v(36932.03, 54726.67) * mm});
            skLineSegment(sketch, "E5864", {"start": v(36853.93, 54756.3) * mm, "end": v(36852.72, 54796.27) * mm});
            skLineSegment(sketch, "E5865", {"start": v(36748.63, 54749.43) * mm, "end": v(36719.5, 54776.85) * mm});
            skLineSegment(sketch, "E5866", {"start": v(36668.17, 54641.5) * mm, "end": v(36628.2, 54640.29) * mm});
            skLineSegment(sketch, "E5867", {"start": v(36700.17, 54480.37) * mm, "end": v(36672.75, 54451.24) * mm});
            skLineSegment(sketch, "E5868", {"start": v(36865.35, 54378.2) * mm, "end": v(36866.63, 54335.6) * mm});
            skLineSegment(sketch, "E5869", {"start": v(36873.1, 54714.5) * mm, "end": v(36882.27, 54753.43) * mm});
            skLineSegment(sketch, "E5870", {"start": v(36799.83, 54740.03) * mm, "end": v(36778.79, 54774.05) * mm});
            skLineSegment(sketch, "E5871", {"start": v(36712.07, 54681.44) * mm, "end": v(36673.14, 54690.62) * mm});
            skLineSegment(sketch, "E5872", {"start": v(36696.36, 54547.74) * mm, "end": v(36662.34, 54526.7) * mm});
            skLineSegment(sketch, "E5873", {"start": v(36804.63, 54424.2) * mm, "end": v(36795.45, 54385.26) * mm});
            skLineSegment(sketch, "E5874", {"start": v(36998.77, 54418.3) * mm, "end": v(37021.18, 54382.05) * mm});
            skLineSegment(sketch, "E5875", {"start": v(36837.32, 54713.42) * mm, "end": v(36825.8, 54751.72) * mm});
            skLineSegment(sketch, "E5876", {"start": v(36761.1, 54698.9) * mm, "end": v(36725.88, 54717.84) * mm});
            skLineSegment(sketch, "E5877", {"start": v(36714.4, 54604.28) * mm, "end": v(36676.1, 54592.76) * mm});
            skLineSegment(sketch, "E5878", {"start": v(36767.64, 54480.63) * mm, "end": v(36748.7, 54445.4) * mm});
            skLineSegment(sketch, "E5879", {"start": v(36923.18, 54427.77) * mm, "end": v(36934.7, 54389.47) * mm});
            skLineSegment(sketch, "E5880", {"start": v(37094.26, 54519.74) * mm, "end": v(37131.8, 54499.55) * mm});
            skLineSegment(sketch, "E5881", {"start": v(36806.88, 54694.6) * mm, "end": v(36777.76, 54722.01) * mm});
            skLineSegment(sketch, "E5882", {"start": v(36748.14, 54643.91) * mm, "end": v(36708.16, 54642.7) * mm});
            skLineSegment(sketch, "E5883", {"start": v(36755, 54538.62) * mm, "end": v(36727.58, 54509.5) * mm});
            skLineSegment(sketch, "E5884", {"start": v(36862.93, 54458.16) * mm, "end": v(36864.14, 54418.18) * mm});
            skLineSegment(sketch, "E5885", {"start": v(37024.06, 54490.15) * mm, "end": v(37053.19, 54462.73) * mm});
            skLineSegment(sketch, "E5886", {"start": v(37126.23, 54655.33) * mm, "end": v(37168.84, 54656.62) * mm});
            skLineSegment(sketch, "E5887", {"start": v(36789.93, 54663.08) * mm, "end": v(36751, 54672.26) * mm});
            skLineSegment(sketch, "E5888", {"start": v(36764.4, 54589.81) * mm, "end": v(36730.38, 54568.77) * mm});
            skLineSegment(sketch, "E5889", {"start": v(36823, 54502.05) * mm, "end": v(36813.8, 54463.12) * mm});
            skLineSegment(sketch, "E5890", {"start": v(36956.7, 54486.34) * mm, "end": v(36977.73, 54452.32) * mm});
            skLineSegment(sketch, "E5891", {"start": v(37080.24, 54594.61) * mm, "end": v(37119.17, 54585.43) * mm});
            skLineSegment(sketch, "E5892", {"start": v(37086.13, 54788.75) * mm, "end": v(37122.38, 54811.17) * mm});
            skLineSegment(sketch, "E5893", {"start": v(37217.94, 54433.9) * mm, "end": v(37202.52, 54444.95) * mm});
            skLineSegment(sketch, "E5894", {"start": v(37195.87, 54409.17) * mm, "end": v(37206.58, 54400.12) * mm});
            skLineSegment(sketch, "E5895", {"start": v(37206.58, 54400.12) * mm, "end": v(37164.75, 54389.99) * mm});
            skLineSegment(sketch, "E5896", {"start": v(37164.75, 54389.99) * mm, "end": v(37177, 54426.71) * mm});
            skLineSegment(sketch, "E5897", {"start": v(37177, 54426.71) * mm, "end": v(37188.51, 54417.05) * mm});
            skLineSegment(sketch, "E5898", {"start": v(36496.5, 54860.51) * mm, "end": v(36511.93, 54849.46) * mm});
            skLineSegment(sketch, "E5899", {"start": v(36518.58, 54885.25) * mm, "end": v(36507.87, 54894.3) * mm});
            skLineSegment(sketch, "E5900", {"start": v(36507.87, 54894.3) * mm, "end": v(36549.7, 54904.43) * mm});
            skLineSegment(sketch, "E5901", {"start": v(36549.7, 54904.43) * mm, "end": v(36537.45, 54867.7) * mm});
            skLineSegment(sketch, "E5902", {"start": v(36537.45, 54867.7) * mm, "end": v(36525.93, 54877.36) * mm});
            skCircle(sketch, "E5903", {"center": v(36982.35, 54230.92) * mm, "radius": 7.85 * mm});
            skCircle(sketch, "E5904", {"center": v(36842.82, 54188.98) * mm, "radius": 7.85 * mm});
            skCircle(sketch, "E5905", {"center": v(36714.07, 54150.28) * mm, "radius": 7.85 * mm});
            skCircle(sketch, "E5906", {"center": v(37121.88, 54272.86) * mm, "radius": 7.85 * mm});
            skCircle(sketch, "E5907", {"center": v(37250.64, 54311.57) * mm, "radius": 7.85 * mm});
            skCircle(sketch, "E5908", {"center": v(36732.1, 55063.5) * mm, "radius": 7.85 * mm});
            skCircle(sketch, "E5909", {"center": v(36592.56, 55021.55) * mm, "radius": 7.85 * mm});
            skCircle(sketch, "E5910", {"center": v(36463.8, 54982.85) * mm, "radius": 7.85 * mm});
            skCircle(sketch, "E5911", {"center": v(36871.62, 55105.43) * mm, "radius": 7.85 * mm});
            skCircle(sketch, "E5912", {"center": v(37000.38, 55144.14) * mm, "radius": 7.85 * mm});
            skLineSegment(sketch, "E5913", {"start": v(36317.42, 55121.8) * mm, "end": v(35992.6, 56193.66) * mm});
            skLineSegment(sketch, "E5914", {"start": v(36025.96, 56256.01) * mm, "end": v(36657.6, 56447.42) * mm});
            skLineSegment(sketch, "E5915", {"start": v(36719.94, 56414.07) * mm, "end": v(37044.76, 55342.2) * mm});
            skLineSegment(sketch, "E5916", {"start": v(37011.4, 55279.85) * mm, "end": v(36379.77, 55088.44) * mm});
            skCircle(sketch, "E5917", {"center": v(36518.73, 55767.95) * mm, "radius": 311.76 * mm});
            skLineSegment(sketch, "E5918", {"start": v(36379.77, 55088.44) * mm, "end": v(36317.42, 55121.8) * mm});
            skLineSegment(sketch, "E5919", {"start": v(37011.4, 55279.85) * mm, "end": v(37044.76, 55342.2) * mm});
            skLineSegment(sketch, "E5920", {"start": v(36025.96, 56256.01) * mm, "end": v(35992.6, 56193.66) * mm});
            skLineSegment(sketch, "E5921", {"start": v(36657.6, 56447.42) * mm, "end": v(36719.94, 56414.07) * mm});
            skCircle(sketch, "E5922", {"center": v(36518.73, 55767.95) * mm, "radius": 69.13 * mm});
            skCircle(sketch, "E5923", {"center": v(36518.73, 55767.95) * mm, "radius": 109.13 * mm});
            skCircle(sketch, "E5924", {"center": v(36518.73, 55767.95) * mm, "radius": 149.13 * mm});
            skCircle(sketch, "E5925", {"center": v(36518.73, 55767.95) * mm, "radius": 189.13 * mm});
            skCircle(sketch, "E5926", {"center": v(36518.73, 55767.95) * mm, "radius": 229.13 * mm});
            skCircle(sketch, "E5927", {"center": v(36518.73, 55767.95) * mm, "radius": 269.13 * mm});
            skLineSegment(sketch, "E5928", {"start": v(36452.57, 55747.9) * mm, "end": v(36414.28, 55736.3) * mm});
            skLineSegment(sketch, "E5929", {"start": v(36467.26, 55671.71) * mm, "end": v(36448.39, 55636.44) * mm});
            skLineSegment(sketch, "E5930", {"start": v(36561.98, 55625.22) * mm, "end": v(36573.58, 55586.94) * mm});
            skLineSegment(sketch, "E5931", {"start": v(36685.5, 55678.74) * mm, "end": v(36720.78, 55659.88) * mm});
            skLineSegment(sketch, "E5932", {"start": v(36738.02, 55834.4) * mm, "end": v(36776.3, 55846) * mm});
            skLineSegment(sketch, "E5933", {"start": v(36645.66, 56005.27) * mm, "end": v(36665.77, 56042.85) * mm});
            skLineSegment(sketch, "E5934", {"start": v(36471.45, 55717.5) * mm, "end": v(36444.1, 55688.31) * mm});
            skLineSegment(sketch, "E5935", {"start": v(36522.27, 55658.87) * mm, "end": v(36523.57, 55618.89) * mm});
            skLineSegment(sketch, "E5936", {"start": v(36627.55, 55665.97) * mm, "end": v(36656.73, 55638.62) * mm});
            skLineSegment(sketch, "E5937", {"start": v(36707.76, 55774.08) * mm, "end": v(36747.74, 55775.38) * mm});
            skLineSegment(sketch, "E5938", {"start": v(36675.41, 55935.14) * mm, "end": v(36702.76, 55964.33) * mm});
            skLineSegment(sketch, "E5939", {"start": v(36510, 56036.94) * mm, "end": v(36508.62, 56079.54) * mm});
            skLineSegment(sketch, "E5940", {"start": v(36503.01, 55700.62) * mm, "end": v(36493.92, 55661.67) * mm});
            skLineSegment(sketch, "E5941", {"start": v(36576.33, 55675.25) * mm, "end": v(36597.45, 55641.28) * mm});
            skLineSegment(sketch, "E5942", {"start": v(36663.96, 55734.04) * mm, "end": v(36702.91, 55724.95) * mm});
            skLineSegment(sketch, "E5943", {"start": v(36679.37, 55867.78) * mm, "end": v(36713.34, 55888.89) * mm});
            skLineSegment(sketch, "E5944", {"start": v(36570.82, 55991.08) * mm, "end": v(36579.92, 56030.03) * mm});
            skLineSegment(sketch, "E5945", {"start": v(36376.67, 55996.54) * mm, "end": v(36354.17, 56032.74) * mm});
            skLineSegment(sketch, "E5946", {"start": v(36538.78, 55701.78) * mm, "end": v(36550.38, 55663.5) * mm});
            skLineSegment(sketch, "E5947", {"start": v(36614.96, 55716.47) * mm, "end": v(36650.23, 55697.6) * mm});
            skLineSegment(sketch, "E5948", {"start": v(36661.45, 55811.2) * mm, "end": v(36699.73, 55822.8) * mm});
            skLineSegment(sketch, "E5949", {"start": v(36607.93, 55934.72) * mm, "end": v(36626.8, 55970) * mm});
            skLineSegment(sketch, "E5950", {"start": v(36452.28, 55987.23) * mm, "end": v(36440.68, 56025.51) * mm});
            skLineSegment(sketch, "E5951", {"start": v(36281.4, 55894.88) * mm, "end": v(36243.82, 55914.99) * mm});
            skLineSegment(sketch, "E5952", {"start": v(36569.17, 55720.67) * mm, "end": v(36598.36, 55693.32) * mm});
            skLineSegment(sketch, "E5953", {"start": v(36627.8, 55771.49) * mm, "end": v(36667.78, 55772.78) * mm});
            skLineSegment(sketch, "E5954", {"start": v(36620.7, 55876.76) * mm, "end": v(36648.06, 55905.95) * mm});
            skLineSegment(sketch, "E5955", {"start": v(36512.6, 55956.98) * mm, "end": v(36511.3, 55996.96) * mm});
            skLineSegment(sketch, "E5956", {"start": v(36351.54, 55924.63) * mm, "end": v(36322.35, 55951.98) * mm});
            skLineSegment(sketch, "E5957", {"start": v(36249.74, 55759.22) * mm, "end": v(36207.13, 55757.83) * mm});
            skLineSegment(sketch, "E5958", {"start": v(36586.05, 55752.23) * mm, "end": v(36625, 55743.13) * mm});
            skLineSegment(sketch, "E5959", {"start": v(36611.42, 55825.55) * mm, "end": v(36645.4, 55846.66) * mm});
            skLineSegment(sketch, "E5960", {"start": v(36552.63, 55913.18) * mm, "end": v(36561.73, 55952.13) * mm});
            skLineSegment(sketch, "E5961", {"start": v(36418.9, 55928.59) * mm, "end": v(36397.79, 55962.56) * mm});
            skLineSegment(sketch, "E5962", {"start": v(36295.6, 55820.04) * mm, "end": v(36256.64, 55829.13) * mm});
            skLineSegment(sketch, "E5963", {"start": v(36290.14, 55625.89) * mm, "end": v(36253.94, 55603.4) * mm});
            skLineSegment(sketch, "E5964", {"start": v(36584.9, 55788) * mm, "end": v(36623.17, 55799.6) * mm});
            skLineSegment(sketch, "E5965", {"start": v(36570.2, 55864.18) * mm, "end": v(36589.07, 55899.45) * mm});
            skLineSegment(sketch, "E5966", {"start": v(36475.48, 55910.67) * mm, "end": v(36463.88, 55948.95) * mm});
            skLineSegment(sketch, "E5967", {"start": v(36351.95, 55857.15) * mm, "end": v(36316.68, 55876.02) * mm});
            skLineSegment(sketch, "E5968", {"start": v(36299.44, 55701.5) * mm, "end": v(36261.16, 55689.9) * mm});
            skLineSegment(sketch, "E5969", {"start": v(36391.8, 55530.63) * mm, "end": v(36371.69, 55493.04) * mm});
            skLineSegment(sketch, "E5970", {"start": v(36566, 55818.4) * mm, "end": v(36593.35, 55847.58) * mm});
            skLineSegment(sketch, "E5971", {"start": v(36515.19, 55877.02) * mm, "end": v(36513.9, 55917) * mm});
            skLineSegment(sketch, "E5972", {"start": v(36409.9, 55869.92) * mm, "end": v(36380.72, 55897.28) * mm});
            skLineSegment(sketch, "E5973", {"start": v(36329.7, 55761.81) * mm, "end": v(36289.71, 55760.51) * mm});
            skLineSegment(sketch, "E5974", {"start": v(36362.05, 55600.75) * mm, "end": v(36334.7, 55571.57) * mm});
            skLineSegment(sketch, "E5975", {"start": v(36527.46, 55498.95) * mm, "end": v(36528.84, 55456.35) * mm});
            skLineSegment(sketch, "E5976", {"start": v(36534.45, 55835.27) * mm, "end": v(36543.54, 55874.22) * mm});
            skLineSegment(sketch, "E5977", {"start": v(36461.12, 55860.64) * mm, "end": v(36440.01, 55894.61) * mm});
            skLineSegment(sketch, "E5978", {"start": v(36373.5, 55801.85) * mm, "end": v(36334.55, 55810.95) * mm});
            skLineSegment(sketch, "E5979", {"start": v(36358.09, 55668.12) * mm, "end": v(36324.11, 55647) * mm});
            skLineSegment(sketch, "E5980", {"start": v(36466.63, 55544.81) * mm, "end": v(36457.54, 55505.86) * mm});
            skLineSegment(sketch, "E5981", {"start": v(36660.78, 55539.36) * mm, "end": v(36683.28, 55503.15) * mm});
            skLineSegment(sketch, "E5982", {"start": v(36498.68, 55834.1) * mm, "end": v(36487.08, 55872.4) * mm});
            skLineSegment(sketch, "E5983", {"start": v(36422.5, 55819.42) * mm, "end": v(36387.22, 55838.28) * mm});
            skLineSegment(sketch, "E5984", {"start": v(36376, 55724.7) * mm, "end": v(36337.72, 55713.1) * mm});
            skLineSegment(sketch, "E5985", {"start": v(36429.52, 55601.17) * mm, "end": v(36410.66, 55565.9) * mm});
            skLineSegment(sketch, "E5986", {"start": v(36585.18, 55548.66) * mm, "end": v(36596.78, 55510.38) * mm});
            skLineSegment(sketch, "E5987", {"start": v(36756.05, 55641) * mm, "end": v(36793.63, 55620.9) * mm});
            skLineSegment(sketch, "E5988", {"start": v(36468.28, 55815.22) * mm, "end": v(36439.1, 55842.57) * mm});
            skLineSegment(sketch, "E5989", {"start": v(36409.65, 55764.4) * mm, "end": v(36369.67, 55763.1) * mm});
            skLineSegment(sketch, "E5990", {"start": v(36416.75, 55659.13) * mm, "end": v(36389.4, 55629.94) * mm});
            skLineSegment(sketch, "E5991", {"start": v(36524.86, 55578.91) * mm, "end": v(36526.16, 55538.93) * mm});
            skLineSegment(sketch, "E5992", {"start": v(36685.92, 55611.26) * mm, "end": v(36715.1, 55583.91) * mm});
            skLineSegment(sketch, "E5993", {"start": v(36787.72, 55776.68) * mm, "end": v(36830.32, 55778.06) * mm});
            skLineSegment(sketch, "E5994", {"start": v(36451.4, 55783.66) * mm, "end": v(36412.45, 55792.76) * mm});
            skLineSegment(sketch, "E5995", {"start": v(36426.03, 55710.34) * mm, "end": v(36392.06, 55689.23) * mm});
            skLineSegment(sketch, "E5996", {"start": v(36484.82, 55622.72) * mm, "end": v(36475.73, 55583.76) * mm});
            skLineSegment(sketch, "E5997", {"start": v(36618.56, 55607.3) * mm, "end": v(36639.67, 55573.33) * mm});
            skLineSegment(sketch, "E5998", {"start": v(36741.86, 55715.85) * mm, "end": v(36780.82, 55706.76) * mm});
            skLineSegment(sketch, "E5999", {"start": v(36747.32, 55910) * mm, "end": v(36783.52, 55932.5) * mm});
            skLineSegment(sketch, "E6000", {"start": v(36879.92, 55555.45) * mm, "end": v(36864.48, 55566.47) * mm});
            skLineSegment(sketch, "E6001", {"start": v(36857.9, 55530.67) * mm, "end": v(36868.64, 55521.65) * mm});
            skLineSegment(sketch, "E6002", {"start": v(36868.64, 55521.65) * mm, "end": v(36826.83, 55511.42) * mm});
            skLineSegment(sketch, "E6003", {"start": v(36826.83, 55511.42) * mm, "end": v(36839, 55548.17) * mm});
            skLineSegment(sketch, "E6004", {"start": v(36839, 55548.17) * mm, "end": v(36850.53, 55538.54) * mm});
            skLineSegment(sketch, "E6005", {"start": v(36157.54, 55980.44) * mm, "end": v(36172.98, 55969.42) * mm});
            skLineSegment(sketch, "E6006", {"start": v(36179.55, 56005.22) * mm, "end": v(36168.82, 56014.25) * mm});
            skLineSegment(sketch, "E6007", {"start": v(36168.82, 56014.25) * mm, "end": v(36210.62, 56024.47) * mm});
            skLineSegment(sketch, "E6008", {"start": v(36210.62, 56024.47) * mm, "end": v(36198.46, 55987.72) * mm});
            skLineSegment(sketch, "E6009", {"start": v(36198.46, 55987.72) * mm, "end": v(36186.92, 55997.36) * mm});
            skCircle(sketch, "E6010", {"center": v(36688.25, 55208.38) * mm, "radius": 7.85 * mm});
            skCircle(sketch, "E6011", {"center": v(36548.81, 55166.12) * mm, "radius": 7.85 * mm});
            skCircle(sketch, "E6012", {"center": v(36420.14, 55127.13) * mm, "radius": 7.85 * mm});
            skCircle(sketch, "E6013", {"center": v(36827.68, 55250.63) * mm, "radius": 7.85 * mm});
            skCircle(sketch, "E6014", {"center": v(36956.35, 55289.62) * mm, "radius": 7.85 * mm});
            skCircle(sketch, "E6015", {"center": v(36349.12, 56327.49) * mm, "radius": 7.85 * mm});
            skCircle(sketch, "E6016", {"center": v(36209.68, 56285.23) * mm, "radius": 7.85 * mm});
            skCircle(sketch, "E6017", {"center": v(36081.01, 56246.24) * mm, "radius": 7.85 * mm});
            skCircle(sketch, "E6018", {"center": v(36488.55, 56369.74) * mm, "radius": 7.85 * mm});
            skCircle(sketch, "E6019", {"center": v(36617.22, 56408.73) * mm, "radius": 7.85 * mm});
            skLineSegment(sketch, "E6020", {"start": v(35934.6, 56385.06) * mm, "end": v(35609.79, 57456.93) * mm});
            skLineSegment(sketch, "E6021", {"start": v(35643.14, 57519.28) * mm, "end": v(36274.77, 57710.69) * mm});
            skLineSegment(sketch, "E6022", {"start": v(36337.13, 57677.34) * mm, "end": v(36661.94, 56605.47) * mm});
            skLineSegment(sketch, "E6023", {"start": v(36628.59, 56543.12) * mm, "end": v(35996.95, 56351.71) * mm});
            skCircle(sketch, "E6024", {"center": v(36135.91, 57031.22) * mm, "radius": 311.76 * mm});
            skLineSegment(sketch, "E6025", {"start": v(35996.95, 56351.71) * mm, "end": v(35934.6, 56385.06) * mm});
            skLineSegment(sketch, "E6026", {"start": v(36628.59, 56543.12) * mm, "end": v(36661.94, 56605.47) * mm});
            skLineSegment(sketch, "E6027", {"start": v(35643.14, 57519.28) * mm, "end": v(35609.79, 57456.93) * mm});
            skLineSegment(sketch, "E6028", {"start": v(36274.77, 57710.69) * mm, "end": v(36337.13, 57677.34) * mm});
            skCircle(sketch, "E6029", {"center": v(36135.91, 57031.22) * mm, "radius": 69.13 * mm});
            skCircle(sketch, "E6030", {"center": v(36135.91, 57031.22) * mm, "radius": 109.13 * mm});
            skCircle(sketch, "E6031", {"center": v(36135.91, 57031.22) * mm, "radius": 149.13 * mm});
            skCircle(sketch, "E6032", {"center": v(36135.91, 57031.22) * mm, "radius": 189.13 * mm});
            skCircle(sketch, "E6033", {"center": v(36135.91, 57031.22) * mm, "radius": 229.13 * mm});
            skCircle(sketch, "E6034", {"center": v(36135.91, 57031.22) * mm, "radius": 269.13 * mm});
            skLineSegment(sketch, "E6035", {"start": v(36069.75, 57011.17) * mm, "end": v(36031.47, 56999.57) * mm});
            skLineSegment(sketch, "E6036", {"start": v(36084.44, 56934.98) * mm, "end": v(36065.57, 56899.71) * mm});
            skLineSegment(sketch, "E6037", {"start": v(36179.16, 56888.5) * mm, "end": v(36190.76, 56850.2) * mm});
            skLineSegment(sketch, "E6038", {"start": v(36302.69, 56942.01) * mm, "end": v(36337.96, 56923.15) * mm});
            skLineSegment(sketch, "E6039", {"start": v(36355.2, 57097.67) * mm, "end": v(36393.48, 57109.27) * mm});
            skLineSegment(sketch, "E6040", {"start": v(36262.85, 57268.54) * mm, "end": v(36282.95, 57306.12) * mm});
            skLineSegment(sketch, "E6041", {"start": v(36088.64, 56980.77) * mm, "end": v(36061.28, 56951.58) * mm});
            skLineSegment(sketch, "E6042", {"start": v(36139.45, 56922.14) * mm, "end": v(36140.75, 56882.16) * mm});
            skLineSegment(sketch, "E6043", {"start": v(36244.73, 56929.24) * mm, "end": v(36273.92, 56901.89) * mm});
            skLineSegment(sketch, "E6044", {"start": v(36324.95, 57037.35) * mm, "end": v(36364.92, 57038.65) * mm});
            skLineSegment(sketch, "E6045", {"start": v(36292.6, 57198.4) * mm, "end": v(36319.94, 57227.6) * mm});
            skLineSegment(sketch, "E6046", {"start": v(36127.18, 57300.2) * mm, "end": v(36125.8, 57342.8) * mm});
            skLineSegment(sketch, "E6047", {"start": v(36120.2, 56963.9) * mm, "end": v(36111.1, 56924.94) * mm});
            skLineSegment(sketch, "E6048", {"start": v(36193.52, 56938.52) * mm, "end": v(36214.63, 56904.55) * mm});
            skLineSegment(sketch, "E6049", {"start": v(36281.14, 56997.3) * mm, "end": v(36320.1, 56988.22) * mm});
            skLineSegment(sketch, "E6050", {"start": v(36296.55, 57131.05) * mm, "end": v(36330.53, 57152.16) * mm});
            skLineSegment(sketch, "E6051", {"start": v(36188, 57254.35) * mm, "end": v(36197.1, 57293.3) * mm});
            skLineSegment(sketch, "E6052", {"start": v(35993.85, 57259.8) * mm, "end": v(35971.36, 57296) * mm});
            skLineSegment(sketch, "E6053", {"start": v(36155.96, 56965.05) * mm, "end": v(36167.56, 56926.77) * mm});
            skLineSegment(sketch, "E6054", {"start": v(36232.14, 56979.74) * mm, "end": v(36267.42, 56960.88) * mm});
            skLineSegment(sketch, "E6055", {"start": v(36278.64, 57074.47) * mm, "end": v(36316.92, 57086.07) * mm});
            skLineSegment(sketch, "E6056", {"start": v(36225.12, 57198) * mm, "end": v(36243.98, 57233.26) * mm});
            skLineSegment(sketch, "E6057", {"start": v(36069.46, 57250.5) * mm, "end": v(36057.86, 57288.78) * mm});
            skLineSegment(sketch, "E6058", {"start": v(35898.6, 57158.15) * mm, "end": v(35861, 57178.26) * mm});
            skLineSegment(sketch, "E6059", {"start": v(36186.36, 56983.94) * mm, "end": v(36215.54, 56956.59) * mm});
            skLineSegment(sketch, "E6060", {"start": v(36244.99, 57034.76) * mm, "end": v(36284.97, 57036.05) * mm});
            skLineSegment(sketch, "E6061", {"start": v(36237.89, 57140.03) * mm, "end": v(36265.24, 57169.22) * mm});
            skLineSegment(sketch, "E6062", {"start": v(36129.78, 57220.25) * mm, "end": v(36128.48, 57260.23) * mm});
            skLineSegment(sketch, "E6063", {"start": v(35968.72, 57187.9) * mm, "end": v(35939.53, 57215.25) * mm});
            skLineSegment(sketch, "E6064", {"start": v(35866.92, 57022.49) * mm, "end": v(35824.32, 57021.1) * mm});
            skLineSegment(sketch, "E6065", {"start": v(36203.24, 57015.5) * mm, "end": v(36242.19, 57006.4) * mm});
            skLineSegment(sketch, "E6066", {"start": v(36228.6, 57088.82) * mm, "end": v(36262.58, 57109.93) * mm});
            skLineSegment(sketch, "E6067", {"start": v(36169.82, 57176.44) * mm, "end": v(36178.91, 57215.4) * mm});
            skLineSegment(sketch, "E6068", {"start": v(36036.08, 57191.86) * mm, "end": v(36014.97, 57225.83) * mm});
            skLineSegment(sketch, "E6069", {"start": v(35912.78, 57083.31) * mm, "end": v(35873.82, 57092.4) * mm});
            skLineSegment(sketch, "E6070", {"start": v(35907.32, 56889.16) * mm, "end": v(35871.12, 56866.66) * mm});
            skLineSegment(sketch, "E6071", {"start": v(36202.07, 57051.27) * mm, "end": v(36240.36, 57062.87) * mm});
            skLineSegment(sketch, "E6072", {"start": v(36187.38, 57127.45) * mm, "end": v(36206.25, 57162.72) * mm});
            skLineSegment(sketch, "E6073", {"start": v(36092.66, 57173.94) * mm, "end": v(36081.06, 57212.22) * mm});
            skLineSegment(sketch, "E6074", {"start": v(35969.13, 57120.42) * mm, "end": v(35933.86, 57139.29) * mm});
            skLineSegment(sketch, "E6075", {"start": v(35916.62, 56964.76) * mm, "end": v(35878.34, 56953.16) * mm});
            skLineSegment(sketch, "E6076", {"start": v(36008.97, 56793.9) * mm, "end": v(35988.87, 56756.31) * mm});
            skLineSegment(sketch, "E6077", {"start": v(36183.19, 57081.66) * mm, "end": v(36210.54, 57110.85) * mm});
            skLineSegment(sketch, "E6078", {"start": v(36132.37, 57140.3) * mm, "end": v(36131.07, 57180.27) * mm});
            skLineSegment(sketch, "E6079", {"start": v(36027.1, 57133.2) * mm, "end": v(35997.9, 57160.55) * mm});
            skLineSegment(sketch, "E6080", {"start": v(35946.88, 57025.08) * mm, "end": v(35906.9, 57023.78) * mm});
            skLineSegment(sketch, "E6081", {"start": v(35979.23, 56864.02) * mm, "end": v(35951.88, 56834.84) * mm});
            skLineSegment(sketch, "E6082", {"start": v(36144.64, 56762.22) * mm, "end": v(36146.02, 56719.62) * mm});
            skLineSegment(sketch, "E6083", {"start": v(36151.63, 57098.54) * mm, "end": v(36160.72, 57137.5) * mm});
            skLineSegment(sketch, "E6084", {"start": v(36078.3, 57123.9) * mm, "end": v(36057.2, 57157.88) * mm});
            skLineSegment(sketch, "E6085", {"start": v(35990.68, 57065.12) * mm, "end": v(35951.73, 57074.22) * mm});
            skLineSegment(sketch, "E6086", {"start": v(35975.27, 56931.39) * mm, "end": v(35941.3, 56910.27) * mm});
            skLineSegment(sketch, "E6087", {"start": v(36083.82, 56808.08) * mm, "end": v(36074.72, 56769.13) * mm});
            skLineSegment(sketch, "E6088", {"start": v(36277.97, 56802.63) * mm, "end": v(36300.47, 56766.42) * mm});
            skLineSegment(sketch, "E6089", {"start": v(36115.86, 57097.38) * mm, "end": v(36104.26, 57135.66) * mm});
            skLineSegment(sketch, "E6090", {"start": v(36039.68, 57082.69) * mm, "end": v(36004.4, 57101.55) * mm});
            skLineSegment(sketch, "E6091", {"start": v(35993.19, 56987.96) * mm, "end": v(35954.9, 56976.36) * mm});
            skLineSegment(sketch, "E6092", {"start": v(36046.7, 56864.44) * mm, "end": v(36027.84, 56829.17) * mm});
            skLineSegment(sketch, "E6093", {"start": v(36202.36, 56811.93) * mm, "end": v(36213.96, 56773.65) * mm});
            skLineSegment(sketch, "E6094", {"start": v(36373.23, 56904.28) * mm, "end": v(36410.82, 56884.18) * mm});
            skLineSegment(sketch, "E6095", {"start": v(36085.47, 57078.49) * mm, "end": v(36056.28, 57105.84) * mm});
            skLineSegment(sketch, "E6096", {"start": v(36026.83, 57027.68) * mm, "end": v(35986.85, 57026.38) * mm});
            skLineSegment(sketch, "E6097", {"start": v(36033.93, 56922.4) * mm, "end": v(36006.58, 56893.2) * mm});
            skLineSegment(sketch, "E6098", {"start": v(36142.05, 56842.18) * mm, "end": v(36143.34, 56802.2) * mm});
            skLineSegment(sketch, "E6099", {"start": v(36303.1, 56874.53) * mm, "end": v(36332.3, 56847.18) * mm});
            skLineSegment(sketch, "E6100", {"start": v(36404.9, 57039.95) * mm, "end": v(36447.5, 57041.33) * mm});
            skLineSegment(sketch, "E6101", {"start": v(36068.59, 57046.93) * mm, "end": v(36029.63, 57056.03) * mm});
            skLineSegment(sketch, "E6102", {"start": v(36043.22, 56973.61) * mm, "end": v(36009.24, 56952.5) * mm});
            skLineSegment(sketch, "E6103", {"start": v(36102, 56885.99) * mm, "end": v(36092.91, 56847.03) * mm});
            skLineSegment(sketch, "E6104", {"start": v(36235.74, 56870.57) * mm, "end": v(36256.85, 56836.6) * mm});
            skLineSegment(sketch, "E6105", {"start": v(36359.05, 56979.12) * mm, "end": v(36398, 56970.03) * mm});
            skLineSegment(sketch, "E6106", {"start": v(36364.5, 57173.27) * mm, "end": v(36400.7, 57195.77) * mm});
            skLineSegment(sketch, "E6107", {"start": v(36497.1, 56818.72) * mm, "end": v(36481.66, 56829.74) * mm});
            skLineSegment(sketch, "E6108", {"start": v(36475.09, 56793.94) * mm, "end": v(36485.82, 56784.92) * mm});
            skLineSegment(sketch, "E6109", {"start": v(36485.82, 56784.92) * mm, "end": v(36444.02, 56774.69) * mm});
            skLineSegment(sketch, "E6110", {"start": v(36444.02, 56774.69) * mm, "end": v(36456.18, 56811.44) * mm});
            skLineSegment(sketch, "E6111", {"start": v(36456.18, 56811.44) * mm, "end": v(36467.72, 56801.8) * mm});
            skLineSegment(sketch, "E6112", {"start": v(35774.72, 57243.71) * mm, "end": v(35790.16, 57232.7) * mm});
            skLineSegment(sketch, "E6113", {"start": v(35796.73, 57268.5) * mm, "end": v(35786, 57277.52) * mm});
            skLineSegment(sketch, "E6114", {"start": v(35786, 57277.52) * mm, "end": v(35827.8, 57287.74) * mm});
            skLineSegment(sketch, "E6115", {"start": v(35827.8, 57287.74) * mm, "end": v(35815.64, 57251) * mm});
            skLineSegment(sketch, "E6116", {"start": v(35815.64, 57251) * mm, "end": v(35804.1, 57260.63) * mm});
            skCircle(sketch, "E6117", {"center": v(36305.43, 56471.65) * mm, "radius": 7.85 * mm});
            skCircle(sketch, "E6118", {"center": v(36166, 56429.4) * mm, "radius": 7.85 * mm});
            skCircle(sketch, "E6119", {"center": v(36037.33, 56390.4) * mm, "radius": 7.85 * mm});
            skCircle(sketch, "E6120", {"center": v(36444.87, 56513.9) * mm, "radius": 7.85 * mm});
            skCircle(sketch, "E6121", {"center": v(36573.53, 56552.9) * mm, "radius": 7.85 * mm});
            skCircle(sketch, "E6122", {"center": v(35966.3, 57590.76) * mm, "radius": 7.85 * mm});
            skCircle(sketch, "E6123", {"center": v(35826.86, 57548.5) * mm, "radius": 7.85 * mm});
            skCircle(sketch, "E6124", {"center": v(35698.2, 57509.51) * mm, "radius": 7.85 * mm});
            skCircle(sketch, "E6125", {"center": v(36105.73, 57633.01) * mm, "radius": 7.85 * mm});
            skCircle(sketch, "E6126", {"center": v(36234.4, 57672) * mm, "radius": 7.85 * mm});
            skLineSegment(sketch, "E6127", {"start": v(38372.03, 53769.6) * mm, "end": v(38047.22, 54841.46) * mm});
            skLineSegment(sketch, "E6128", {"start": v(38080.57, 54903.81) * mm, "end": v(38712.2, 55095.22) * mm});
            skLineSegment(sketch, "E6129", {"start": v(38774.56, 55061.87) * mm, "end": v(39099.37, 53990) * mm});
            skLineSegment(sketch, "E6130", {"start": v(39066.02, 53927.65) * mm, "end": v(38434.38, 53736.24) * mm});
            skCircle(sketch, "E6131", {"center": v(38573.34, 54415.75) * mm, "radius": 311.76 * mm});
            skLineSegment(sketch, "E6132", {"start": v(38434.38, 53736.24) * mm, "end": v(38372.03, 53769.6) * mm});
            skLineSegment(sketch, "E6133", {"start": v(39066.02, 53927.65) * mm, "end": v(39099.37, 53990) * mm});
            skLineSegment(sketch, "E6134", {"start": v(38080.57, 54903.81) * mm, "end": v(38047.22, 54841.46) * mm});
            skLineSegment(sketch, "E6135", {"start": v(38712.2, 55095.22) * mm, "end": v(38774.56, 55061.87) * mm});
            skCircle(sketch, "E6136", {"center": v(38573.34, 54415.75) * mm, "radius": 69.13 * mm});
            skCircle(sketch, "E6137", {"center": v(38573.34, 54415.75) * mm, "radius": 109.13 * mm});
            skCircle(sketch, "E6138", {"center": v(38573.34, 54415.75) * mm, "radius": 149.13 * mm});
            skCircle(sketch, "E6139", {"center": v(38573.34, 54415.75) * mm, "radius": 189.13 * mm});
            skCircle(sketch, "E6140", {"center": v(38573.34, 54415.75) * mm, "radius": 229.13 * mm});
            skCircle(sketch, "E6141", {"center": v(38573.34, 54415.75) * mm, "radius": 269.13 * mm});
            skLineSegment(sketch, "E6142", {"start": v(38507.18, 54395.7) * mm, "end": v(38468.9, 54384.1) * mm});
            skLineSegment(sketch, "E6143", {"start": v(38521.87, 54319.51) * mm, "end": v(38503, 54284.24) * mm});
            skLineSegment(sketch, "E6144", {"start": v(38616.6, 54273.02) * mm, "end": v(38628.2, 54234.74) * mm});
            skLineSegment(sketch, "E6145", {"start": v(38740.12, 54326.54) * mm, "end": v(38775.39, 54307.68) * mm});
            skLineSegment(sketch, "E6146", {"start": v(38792.63, 54482.2) * mm, "end": v(38830.9, 54493.8) * mm});
            skLineSegment(sketch, "E6147", {"start": v(38700.28, 54653.07) * mm, "end": v(38720.38, 54690.65) * mm});
            skLineSegment(sketch, "E6148", {"start": v(38526.07, 54365.3) * mm, "end": v(38498.71, 54336.11) * mm});
            skLineSegment(sketch, "E6149", {"start": v(38576.88, 54306.67) * mm, "end": v(38578.18, 54266.7) * mm});
            skLineSegment(sketch, "E6150", {"start": v(38682.16, 54313.77) * mm, "end": v(38711.35, 54286.42) * mm});
            skLineSegment(sketch, "E6151", {"start": v(38762.38, 54421.88) * mm, "end": v(38802.36, 54423.18) * mm});
            skLineSegment(sketch, "E6152", {"start": v(38730.02, 54582.94) * mm, "end": v(38757.38, 54612.13) * mm});
            skLineSegment(sketch, "E6153", {"start": v(38564.61, 54684.74) * mm, "end": v(38563.23, 54727.34) * mm});
            skLineSegment(sketch, "E6154", {"start": v(38557.62, 54348.42) * mm, "end": v(38548.53, 54309.47) * mm});
            skLineSegment(sketch, "E6155", {"start": v(38630.95, 54323.05) * mm, "end": v(38652.06, 54289.08) * mm});
            skLineSegment(sketch, "E6156", {"start": v(38718.57, 54381.84) * mm, "end": v(38757.52, 54372.75) * mm});
            skLineSegment(sketch, "E6157", {"start": v(38733.98, 54515.58) * mm, "end": v(38767.96, 54536.7) * mm});
            skLineSegment(sketch, "E6158", {"start": v(38625.44, 54638.88) * mm, "end": v(38634.53, 54677.83) * mm});
            skLineSegment(sketch, "E6159", {"start": v(38431.28, 54644.34) * mm, "end": v(38408.79, 54680.54) * mm});
            skLineSegment(sketch, "E6160", {"start": v(38593.4, 54349.58) * mm, "end": v(38605, 54311.3) * mm});
            skLineSegment(sketch, "E6161", {"start": v(38669.57, 54364.27) * mm, "end": v(38704.85, 54345.4) * mm});
            skLineSegment(sketch, "E6162", {"start": v(38716.07, 54459) * mm, "end": v(38754.35, 54470.6) * mm});
            skLineSegment(sketch, "E6163", {"start": v(38662.55, 54582.52) * mm, "end": v(38681.41, 54617.8) * mm});
            skLineSegment(sketch, "E6164", {"start": v(38506.89, 54635.03) * mm, "end": v(38495.29, 54673.31) * mm});
            skLineSegment(sketch, "E6165", {"start": v(38336.02, 54542.68) * mm, "end": v(38298.44, 54562.79) * mm});
            skLineSegment(sketch, "E6166", {"start": v(38623.79, 54368.47) * mm, "end": v(38652.97, 54341.12) * mm});
            skLineSegment(sketch, "E6167", {"start": v(38682.42, 54419.29) * mm, "end": v(38722.4, 54420.58) * mm});
            skLineSegment(sketch, "E6168", {"start": v(38675.32, 54524.57) * mm, "end": v(38702.67, 54553.75) * mm});
            skLineSegment(sketch, "E6169", {"start": v(38567.2, 54604.78) * mm, "end": v(38565.9, 54644.76) * mm});
            skLineSegment(sketch, "E6170", {"start": v(38406.15, 54572.43) * mm, "end": v(38376.96, 54599.78) * mm});
            skLineSegment(sketch, "E6171", {"start": v(38304.35, 54407.02) * mm, "end": v(38261.75, 54405.63) * mm});
            skLineSegment(sketch, "E6172", {"start": v(38640.67, 54400.03) * mm, "end": v(38679.62, 54390.93) * mm});
            skLineSegment(sketch, "E6173", {"start": v(38666.03, 54473.35) * mm, "end": v(38700, 54494.46) * mm});
            skLineSegment(sketch, "E6174", {"start": v(38607.25, 54560.98) * mm, "end": v(38616.34, 54599.93) * mm});
            skLineSegment(sketch, "E6175", {"start": v(38473.51, 54576.39) * mm, "end": v(38452.4, 54610.36) * mm});
            skLineSegment(sketch, "E6176", {"start": v(38350.2, 54467.84) * mm, "end": v(38311.25, 54476.94) * mm});
            skLineSegment(sketch, "E6177", {"start": v(38344.75, 54273.7) * mm, "end": v(38308.55, 54251.2) * mm});
            skLineSegment(sketch, "E6178", {"start": v(38639.5, 54435.8) * mm, "end": v(38677.79, 54447.4) * mm});
            skLineSegment(sketch, "E6179", {"start": v(38624.81, 54511.98) * mm, "end": v(38643.68, 54547.25) * mm});
            skLineSegment(sketch, "E6180", {"start": v(38530.09, 54558.47) * mm, "end": v(38518.49, 54596.75) * mm});
            skLineSegment(sketch, "E6181", {"start": v(38406.56, 54504.95) * mm, "end": v(38371.3, 54523.82) * mm});
            skLineSegment(sketch, "E6182", {"start": v(38354.05, 54349.3) * mm, "end": v(38315.77, 54337.7) * mm});
            skLineSegment(sketch, "E6183", {"start": v(38446.4, 54178.43) * mm, "end": v(38426.3, 54140.84) * mm});
            skLineSegment(sketch, "E6184", {"start": v(38620.62, 54466.2) * mm, "end": v(38647.97, 54495.38) * mm});
            skLineSegment(sketch, "E6185", {"start": v(38569.8, 54524.82) * mm, "end": v(38568.5, 54564.8) * mm});
            skLineSegment(sketch, "E6186", {"start": v(38464.52, 54517.72) * mm, "end": v(38435.34, 54545.08) * mm});
            skLineSegment(sketch, "E6187", {"start": v(38384.3, 54409.61) * mm, "end": v(38344.33, 54408.31) * mm});
            skLineSegment(sketch, "E6188", {"start": v(38416.66, 54248.55) * mm, "end": v(38389.3, 54219.37) * mm});
            skLineSegment(sketch, "E6189", {"start": v(38582.07, 54146.75) * mm, "end": v(38583.45, 54104.15) * mm});
            skLineSegment(sketch, "E6190", {"start": v(38589.06, 54483.07) * mm, "end": v(38598.15, 54522.02) * mm});
            skLineSegment(sketch, "E6191", {"start": v(38515.74, 54508.44) * mm, "end": v(38494.62, 54542.41) * mm});
            skLineSegment(sketch, "E6192", {"start": v(38428.11, 54449.65) * mm, "end": v(38389.16, 54458.75) * mm});
            skLineSegment(sketch, "E6193", {"start": v(38412.7, 54315.92) * mm, "end": v(38378.73, 54294.8) * mm});
            skLineSegment(sketch, "E6194", {"start": v(38521.25, 54192.61) * mm, "end": v(38512.15, 54153.66) * mm});
            skLineSegment(sketch, "E6195", {"start": v(38715.4, 54187.16) * mm, "end": v(38737.9, 54150.95) * mm});
            skLineSegment(sketch, "E6196", {"start": v(38553.3, 54481.91) * mm, "end": v(38541.7, 54520.2) * mm});
            skLineSegment(sketch, "E6197", {"start": v(38477.1, 54467.22) * mm, "end": v(38441.84, 54486.09) * mm});
            skLineSegment(sketch, "E6198", {"start": v(38430.62, 54372.5) * mm, "end": v(38392.33, 54360.9) * mm});
            skLineSegment(sketch, "E6199", {"start": v(38484.14, 54248.97) * mm, "end": v(38465.27, 54213.7) * mm});
            skLineSegment(sketch, "E6200", {"start": v(38639.8, 54196.46) * mm, "end": v(38651.4, 54158.18) * mm});
            skLineSegment(sketch, "E6201", {"start": v(38810.66, 54288.81) * mm, "end": v(38848.25, 54268.7) * mm});
            skLineSegment(sketch, "E6202", {"start": v(38522.9, 54463.02) * mm, "end": v(38493.7, 54490.37) * mm});
            skLineSegment(sketch, "E6203", {"start": v(38464.26, 54412.2) * mm, "end": v(38424.28, 54410.9) * mm});
            skLineSegment(sketch, "E6204", {"start": v(38471.36, 54306.93) * mm, "end": v(38444.01, 54277.74) * mm});
            skLineSegment(sketch, "E6205", {"start": v(38579.48, 54226.71) * mm, "end": v(38580.77, 54186.73) * mm});
            skLineSegment(sketch, "E6206", {"start": v(38740.53, 54259.06) * mm, "end": v(38769.72, 54231.71) * mm});
            skLineSegment(sketch, "E6207", {"start": v(38842.33, 54424.48) * mm, "end": v(38884.94, 54425.86) * mm});
            skLineSegment(sketch, "E6208", {"start": v(38506.02, 54431.46) * mm, "end": v(38467.06, 54440.56) * mm});
            skLineSegment(sketch, "E6209", {"start": v(38480.65, 54358.14) * mm, "end": v(38446.67, 54337.03) * mm});
            skLineSegment(sketch, "E6210", {"start": v(38539.43, 54270.52) * mm, "end": v(38530.34, 54231.57) * mm});
            skLineSegment(sketch, "E6211", {"start": v(38673.17, 54255.1) * mm, "end": v(38694.28, 54221.13) * mm});
            skLineSegment(sketch, "E6212", {"start": v(38796.48, 54363.65) * mm, "end": v(38835.43, 54354.56) * mm});
            skLineSegment(sketch, "E6213", {"start": v(38801.93, 54557.8) * mm, "end": v(38838.13, 54580.3) * mm});
            skLineSegment(sketch, "E6214", {"start": v(38934.53, 54203.25) * mm, "end": v(38919.1, 54214.27) * mm});
            skLineSegment(sketch, "E6215", {"start": v(38912.52, 54178.47) * mm, "end": v(38923.25, 54169.45) * mm});
            skLineSegment(sketch, "E6216", {"start": v(38923.25, 54169.45) * mm, "end": v(38881.45, 54159.22) * mm});
            skLineSegment(sketch, "E6217", {"start": v(38881.45, 54159.22) * mm, "end": v(38893.61, 54195.97) * mm});
            skLineSegment(sketch, "E6218", {"start": v(38893.61, 54195.97) * mm, "end": v(38905.15, 54186.34) * mm});
            skLineSegment(sketch, "E6219", {"start": v(38212.15, 54628.24) * mm, "end": v(38227.6, 54617.22) * mm});
            skLineSegment(sketch, "E6220", {"start": v(38234.16, 54653.02) * mm, "end": v(38223.43, 54662.05) * mm});
            skLineSegment(sketch, "E6221", {"start": v(38223.43, 54662.05) * mm, "end": v(38265.23, 54672.27) * mm});
            skLineSegment(sketch, "E6222", {"start": v(38265.23, 54672.27) * mm, "end": v(38253.07, 54635.52) * mm});
            skLineSegment(sketch, "E6223", {"start": v(38253.07, 54635.52) * mm, "end": v(38241.54, 54645.16) * mm});
            skCircle(sketch, "E6224", {"center": v(38742.86, 53856.18) * mm, "radius": 7.85 * mm});
            skCircle(sketch, "E6225", {"center": v(38603.43, 53813.92) * mm, "radius": 7.85 * mm});
            skCircle(sketch, "E6226", {"center": v(38474.76, 53774.93) * mm, "radius": 7.85 * mm});
            skCircle(sketch, "E6227", {"center": v(38882.3, 53898.43) * mm, "radius": 7.85 * mm});
            skCircle(sketch, "E6228", {"center": v(39010.96, 53937.42) * mm, "radius": 7.85 * mm});
            skCircle(sketch, "E6229", {"center": v(38403.73, 54975.29) * mm, "radius": 7.85 * mm});
            skCircle(sketch, "E6230", {"center": v(38264.3, 54933.03) * mm, "radius": 7.85 * mm});
            skCircle(sketch, "E6231", {"center": v(38135.62, 54894.04) * mm, "radius": 7.85 * mm});
            skCircle(sketch, "E6232", {"center": v(38543.16, 55017.54) * mm, "radius": 7.85 * mm});
            skCircle(sketch, "E6233", {"center": v(38671.83, 55056.53) * mm, "radius": 7.85 * mm});
            skLineSegment(sketch, "E6234", {"start": v(37989.22, 55032.86) * mm, "end": v(37664.4, 56104.73) * mm});
            skLineSegment(sketch, "E6235", {"start": v(37697.75, 56167.08) * mm, "end": v(38329.39, 56358.5) * mm});
            skLineSegment(sketch, "E6236", {"start": v(38391.74, 56325.14) * mm, "end": v(38716.55, 55253.27) * mm});
            skLineSegment(sketch, "E6237", {"start": v(38683.2, 55190.92) * mm, "end": v(38051.57, 54999.51) * mm});
            skCircle(sketch, "E6238", {"center": v(38190.52, 55679.02) * mm, "radius": 311.76 * mm});
            skLineSegment(sketch, "E6239", {"start": v(38051.57, 54999.51) * mm, "end": v(37989.22, 55032.86) * mm});
            skLineSegment(sketch, "E6240", {"start": v(38683.2, 55190.92) * mm, "end": v(38716.55, 55253.27) * mm});
            skLineSegment(sketch, "E6241", {"start": v(37697.75, 56167.08) * mm, "end": v(37664.4, 56104.73) * mm});
            skLineSegment(sketch, "E6242", {"start": v(38329.39, 56358.5) * mm, "end": v(38391.74, 56325.14) * mm});
            skCircle(sketch, "E6243", {"center": v(38190.52, 55679.02) * mm, "radius": 69.13 * mm});
            skCircle(sketch, "E6244", {"center": v(38190.52, 55679.02) * mm, "radius": 109.13 * mm});
            skCircle(sketch, "E6245", {"center": v(38190.52, 55679.02) * mm, "radius": 149.13 * mm});
            skCircle(sketch, "E6246", {"center": v(38190.52, 55679.02) * mm, "radius": 189.13 * mm});
            skCircle(sketch, "E6247", {"center": v(38190.52, 55679.02) * mm, "radius": 229.13 * mm});
            skCircle(sketch, "E6248", {"center": v(38190.52, 55679.02) * mm, "radius": 269.13 * mm});
            skLineSegment(sketch, "E6249", {"start": v(38124.36, 55658.97) * mm, "end": v(38086.08, 55647.37) * mm});
            skLineSegment(sketch, "E6250", {"start": v(38139.05, 55582.78) * mm, "end": v(38120.18, 55547.51) * mm});
            skLineSegment(sketch, "E6251", {"start": v(38233.77, 55536.3) * mm, "end": v(38245.38, 55498.01) * mm});
            skLineSegment(sketch, "E6252", {"start": v(38357.3, 55589.81) * mm, "end": v(38392.57, 55570.95) * mm});
            skLineSegment(sketch, "E6253", {"start": v(38409.81, 55745.47) * mm, "end": v(38448.1, 55757.07) * mm});
            skLineSegment(sketch, "E6254", {"start": v(38317.46, 55916.34) * mm, "end": v(38337.56, 55953.92) * mm});
            skLineSegment(sketch, "E6255", {"start": v(38143.25, 55628.57) * mm, "end": v(38115.9, 55599.38) * mm});
            skLineSegment(sketch, "E6256", {"start": v(38194.06, 55569.94) * mm, "end": v(38195.36, 55529.96) * mm});
            skLineSegment(sketch, "E6257", {"start": v(38299.34, 55577.04) * mm, "end": v(38328.53, 55549.69) * mm});
            skLineSegment(sketch, "E6258", {"start": v(38379.56, 55685.15) * mm, "end": v(38419.54, 55686.45) * mm});
            skLineSegment(sketch, "E6259", {"start": v(38347.2, 55846.2) * mm, "end": v(38374.56, 55875.4) * mm});
            skLineSegment(sketch, "E6260", {"start": v(38181.8, 55948) * mm, "end": v(38180.41, 55990.61) * mm});
            skLineSegment(sketch, "E6261", {"start": v(38174.8, 55611.7) * mm, "end": v(38165.71, 55572.74) * mm});
            skLineSegment(sketch, "E6262", {"start": v(38248.13, 55586.32) * mm, "end": v(38269.24, 55552.35) * mm});
            skLineSegment(sketch, "E6263", {"start": v(38335.75, 55645.11) * mm, "end": v(38374.7, 55636.02) * mm});
            skLineSegment(sketch, "E6264", {"start": v(38351.17, 55778.85) * mm, "end": v(38385.14, 55799.96) * mm});
            skLineSegment(sketch, "E6265", {"start": v(38242.62, 55902.15) * mm, "end": v(38251.71, 55941.1) * mm});
            skLineSegment(sketch, "E6266", {"start": v(38048.47, 55907.6) * mm, "end": v(38025.97, 55943.8) * mm});
            skLineSegment(sketch, "E6267", {"start": v(38210.57, 55612.85) * mm, "end": v(38222.17, 55574.57) * mm});
            skLineSegment(sketch, "E6268", {"start": v(38286.76, 55627.54) * mm, "end": v(38322.03, 55608.68) * mm});
            skLineSegment(sketch, "E6269", {"start": v(38333.25, 55722.27) * mm, "end": v(38371.53, 55733.87) * mm});
            skLineSegment(sketch, "E6270", {"start": v(38279.73, 55845.8) * mm, "end": v(38298.6, 55881.06) * mm});
            skLineSegment(sketch, "E6271", {"start": v(38124.07, 55898.3) * mm, "end": v(38112.47, 55936.58) * mm});
            skLineSegment(sketch, "E6272", {"start": v(37953.2, 55805.95) * mm, "end": v(37915.62, 55826.06) * mm});
            skLineSegment(sketch, "E6273", {"start": v(38240.97, 55631.74) * mm, "end": v(38270.16, 55604.4) * mm});
            skLineSegment(sketch, "E6274", {"start": v(38299.6, 55682.56) * mm, "end": v(38339.58, 55683.85) * mm});
            skLineSegment(sketch, "E6275", {"start": v(38292.5, 55787.84) * mm, "end": v(38319.85, 55817.02) * mm});
            skLineSegment(sketch, "E6276", {"start": v(38184.39, 55868.05) * mm, "end": v(38183.1, 55908.03) * mm});
            skLineSegment(sketch, "E6277", {"start": v(38023.33, 55835.7) * mm, "end": v(37994.14, 55863.05) * mm});
            skLineSegment(sketch, "E6278", {"start": v(37921.53, 55670.29) * mm, "end": v(37878.93, 55668.9) * mm});
            skLineSegment(sketch, "E6279", {"start": v(38257.85, 55663.3) * mm, "end": v(38296.8, 55654.2) * mm});
            skLineSegment(sketch, "E6280", {"start": v(38283.22, 55736.62) * mm, "end": v(38317.2, 55757.73) * mm});
            skLineSegment(sketch, "E6281", {"start": v(38224.43, 55824.25) * mm, "end": v(38233.52, 55863.2) * mm});
            skLineSegment(sketch, "E6282", {"start": v(38090.7, 55839.66) * mm, "end": v(38069.58, 55873.63) * mm});
            skLineSegment(sketch, "E6283", {"start": v(37967.39, 55731.11) * mm, "end": v(37928.44, 55740.2) * mm});
            skLineSegment(sketch, "E6284", {"start": v(37961.93, 55536.96) * mm, "end": v(37925.73, 55514.46) * mm});
            skLineSegment(sketch, "E6285", {"start": v(38256.69, 55699.07) * mm, "end": v(38294.97, 55710.67) * mm});
            skLineSegment(sketch, "E6286", {"start": v(38242, 55775.25) * mm, "end": v(38260.86, 55810.52) * mm});
            skLineSegment(sketch, "E6287", {"start": v(38147.27, 55821.74) * mm, "end": v(38135.67, 55860.02) * mm});
            skLineSegment(sketch, "E6288", {"start": v(38023.75, 55768.22) * mm, "end": v(37988.48, 55787.09) * mm});
            skLineSegment(sketch, "E6289", {"start": v(37971.24, 55612.56) * mm, "end": v(37932.96, 55600.96) * mm});
            skLineSegment(sketch, "E6290", {"start": v(38063.59, 55441.7) * mm, "end": v(38043.48, 55404.11) * mm});
            skLineSegment(sketch, "E6291", {"start": v(38237.8, 55729.46) * mm, "end": v(38265.15, 55758.65) * mm});
            skLineSegment(sketch, "E6292", {"start": v(38186.98, 55788.1) * mm, "end": v(38185.69, 55828.07) * mm});
            skLineSegment(sketch, "E6293", {"start": v(38081.7, 55781) * mm, "end": v(38052.52, 55808.35) * mm});
            skLineSegment(sketch, "E6294", {"start": v(38001.49, 55672.88) * mm, "end": v(37961.5, 55671.58) * mm});
            skLineSegment(sketch, "E6295", {"start": v(38033.84, 55511.82) * mm, "end": v(38006.49, 55482.64) * mm});
            skLineSegment(sketch, "E6296", {"start": v(38199.25, 55410.02) * mm, "end": v(38200.64, 55367.42) * mm});
            skLineSegment(sketch, "E6297", {"start": v(38206.24, 55746.34) * mm, "end": v(38215.34, 55785.3) * mm});
            skLineSegment(sketch, "E6298", {"start": v(38132.92, 55771.71) * mm, "end": v(38111.8, 55805.68) * mm});
            skLineSegment(sketch, "E6299", {"start": v(38045.3, 55712.92) * mm, "end": v(38006.34, 55722.02) * mm});
            skLineSegment(sketch, "E6300", {"start": v(38029.88, 55579.19) * mm, "end": v(37995.9, 55558.07) * mm});
            skLineSegment(sketch, "E6301", {"start": v(38138.43, 55455.88) * mm, "end": v(38129.34, 55416.93) * mm});
            skLineSegment(sketch, "E6302", {"start": v(38332.58, 55450.43) * mm, "end": v(38355.08, 55414.22) * mm});
            skLineSegment(sketch, "E6303", {"start": v(38170.47, 55745.18) * mm, "end": v(38158.87, 55783.46) * mm});
            skLineSegment(sketch, "E6304", {"start": v(38094.29, 55730.49) * mm, "end": v(38059.02, 55749.36) * mm});
            skLineSegment(sketch, "E6305", {"start": v(38047.8, 55635.77) * mm, "end": v(38009.52, 55624.17) * mm});
            skLineSegment(sketch, "E6306", {"start": v(38101.32, 55512.24) * mm, "end": v(38082.45, 55476.97) * mm});
            skLineSegment(sketch, "E6307", {"start": v(38256.98, 55459.73) * mm, "end": v(38268.58, 55421.45) * mm});
            skLineSegment(sketch, "E6308", {"start": v(38427.84, 55552.08) * mm, "end": v(38465.43, 55531.98) * mm});
            skLineSegment(sketch, "E6309", {"start": v(38140.08, 55726.3) * mm, "end": v(38110.9, 55753.64) * mm});
            skLineSegment(sketch, "E6310", {"start": v(38081.45, 55675.48) * mm, "end": v(38041.47, 55674.18) * mm});
            skLineSegment(sketch, "E6311", {"start": v(38088.55, 55570.2) * mm, "end": v(38061.2, 55541.01) * mm});
            skLineSegment(sketch, "E6312", {"start": v(38196.66, 55489.98) * mm, "end": v(38197.96, 55450) * mm});
            skLineSegment(sketch, "E6313", {"start": v(38357.72, 55522.33) * mm, "end": v(38386.9, 55494.98) * mm});
            skLineSegment(sketch, "E6314", {"start": v(38459.52, 55687.75) * mm, "end": v(38502.12, 55689.13) * mm});
            skLineSegment(sketch, "E6315", {"start": v(38123.2, 55694.73) * mm, "end": v(38084.25, 55703.83) * mm});
            skLineSegment(sketch, "E6316", {"start": v(38097.83, 55621.41) * mm, "end": v(38063.86, 55600.3) * mm});
            skLineSegment(sketch, "E6317", {"start": v(38156.62, 55533.79) * mm, "end": v(38147.52, 55494.83) * mm});
            skLineSegment(sketch, "E6318", {"start": v(38290.35, 55518.37) * mm, "end": v(38311.47, 55484.4) * mm});
            skLineSegment(sketch, "E6319", {"start": v(38413.66, 55626.92) * mm, "end": v(38452.61, 55617.83) * mm});
            skLineSegment(sketch, "E6320", {"start": v(38419.11, 55821.07) * mm, "end": v(38455.32, 55843.57) * mm});
            skLineSegment(sketch, "E6321", {"start": v(38551.72, 55466.52) * mm, "end": v(38536.27, 55477.54) * mm});
            skLineSegment(sketch, "E6322", {"start": v(38529.7, 55441.74) * mm, "end": v(38540.43, 55432.72) * mm});
            skLineSegment(sketch, "E6323", {"start": v(38540.43, 55432.72) * mm, "end": v(38498.63, 55422.49) * mm});
            skLineSegment(sketch, "E6324", {"start": v(38498.63, 55422.49) * mm, "end": v(38510.8, 55459.24) * mm});
            skLineSegment(sketch, "E6325", {"start": v(38510.8, 55459.24) * mm, "end": v(38522.33, 55449.6) * mm});
            skLineSegment(sketch, "E6326", {"start": v(37829.33, 55891.51) * mm, "end": v(37844.77, 55880.5) * mm});
            skLineSegment(sketch, "E6327", {"start": v(37851.35, 55916.3) * mm, "end": v(37840.61, 55925.32) * mm});
            skLineSegment(sketch, "E6328", {"start": v(37840.61, 55925.32) * mm, "end": v(37882.42, 55935.54) * mm});
            skLineSegment(sketch, "E6329", {"start": v(37882.42, 55935.54) * mm, "end": v(37870.25, 55898.8) * mm});
            skLineSegment(sketch, "E6330", {"start": v(37870.25, 55898.8) * mm, "end": v(37858.72, 55908.43) * mm});
            skCircle(sketch, "E6331", {"center": v(38360.04, 55119.45) * mm, "radius": 7.85 * mm});
            skCircle(sketch, "E6332", {"center": v(38220.6, 55077.2) * mm, "radius": 7.85 * mm});
            skCircle(sketch, "E6333", {"center": v(38091.94, 55038.2) * mm, "radius": 7.85 * mm});
            skCircle(sketch, "E6334", {"center": v(38499.48, 55161.7) * mm, "radius": 7.85 * mm});
            skCircle(sketch, "E6335", {"center": v(38628.15, 55200.7) * mm, "radius": 7.85 * mm});
            skCircle(sketch, "E6336", {"center": v(38020.91, 56238.56) * mm, "radius": 7.85 * mm});
            skCircle(sketch, "E6337", {"center": v(37881.48, 56196.3) * mm, "radius": 7.85 * mm});
            skCircle(sketch, "E6338", {"center": v(37752.8, 56157.31) * mm, "radius": 7.85 * mm});
            skCircle(sketch, "E6339", {"center": v(38160.35, 56280.81) * mm, "radius": 7.85 * mm});
            skCircle(sketch, "E6340", {"center": v(38289.01, 56319.8) * mm, "radius": 7.85 * mm});
            skLineSegment(sketch, "E6341", {"start": v(37606.4, 56296.13) * mm, "end": v(37281.58, 57368) * mm});
            skLineSegment(sketch, "E6342", {"start": v(37314.93, 57430.35) * mm, "end": v(37946.57, 57621.76) * mm});
            skLineSegment(sketch, "E6343", {"start": v(38008.92, 57588.4) * mm, "end": v(38333.74, 56516.54) * mm});
            skLineSegment(sketch, "E6344", {"start": v(38300.38, 56454.2) * mm, "end": v(37668.75, 56262.78) * mm});
            skCircle(sketch, "E6345", {"center": v(37807.7, 56942.29) * mm, "radius": 311.76 * mm});
            skLineSegment(sketch, "E6346", {"start": v(37668.75, 56262.78) * mm, "end": v(37606.4, 56296.13) * mm});
            skLineSegment(sketch, "E6347", {"start": v(38300.38, 56454.2) * mm, "end": v(38333.74, 56516.54) * mm});
            skLineSegment(sketch, "E6348", {"start": v(37314.93, 57430.35) * mm, "end": v(37281.58, 57368) * mm});
            skLineSegment(sketch, "E6349", {"start": v(37946.57, 57621.76) * mm, "end": v(38008.92, 57588.4) * mm});
            skCircle(sketch, "E6350", {"center": v(37807.7, 56942.29) * mm, "radius": 69.13 * mm});
            skCircle(sketch, "E6351", {"center": v(37807.7, 56942.29) * mm, "radius": 109.13 * mm});
            skCircle(sketch, "E6352", {"center": v(37807.7, 56942.29) * mm, "radius": 149.13 * mm});
            skCircle(sketch, "E6353", {"center": v(37807.7, 56942.29) * mm, "radius": 189.13 * mm});
            skCircle(sketch, "E6354", {"center": v(37807.7, 56942.29) * mm, "radius": 229.13 * mm});
            skCircle(sketch, "E6355", {"center": v(37807.7, 56942.29) * mm, "radius": 269.13 * mm});
            skLineSegment(sketch, "E6356", {"start": v(37741.54, 56922.24) * mm, "end": v(37703.26, 56910.64) * mm});
            skLineSegment(sketch, "E6357", {"start": v(37756.23, 56846.05) * mm, "end": v(37737.37, 56810.78) * mm});
            skLineSegment(sketch, "E6358", {"start": v(37850.96, 56799.56) * mm, "end": v(37862.56, 56761.28) * mm});
            skLineSegment(sketch, "E6359", {"start": v(37974.48, 56853.08) * mm, "end": v(38009.75, 56834.22) * mm});
            skLineSegment(sketch, "E6360", {"start": v(38027, 57008.74) * mm, "end": v(38065.27, 57020.34) * mm});
            skLineSegment(sketch, "E6361", {"start": v(37934.64, 57179.6) * mm, "end": v(37954.75, 57217.2) * mm});
            skLineSegment(sketch, "E6362", {"start": v(37760.43, 56891.84) * mm, "end": v(37733.08, 56862.65) * mm});
            skLineSegment(sketch, "E6363", {"start": v(37811.25, 56833.2) * mm, "end": v(37812.54, 56793.23) * mm});
            skLineSegment(sketch, "E6364", {"start": v(37916.53, 56840.3) * mm, "end": v(37945.71, 56812.96) * mm});
            skLineSegment(sketch, "E6365", {"start": v(37996.74, 56948.42) * mm, "end": v(38036.72, 56949.72) * mm});
            skLineSegment(sketch, "E6366", {"start": v(37964.39, 57109.48) * mm, "end": v(37991.74, 57138.67) * mm});
            skLineSegment(sketch, "E6367", {"start": v(37798.98, 57211.28) * mm, "end": v(37797.6, 57253.88) * mm});
            skLineSegment(sketch, "E6368", {"start": v(37791.99, 56874.96) * mm, "end": v(37782.9, 56836) * mm});
            skLineSegment(sketch, "E6369", {"start": v(37865.31, 56849.6) * mm, "end": v(37886.42, 56815.62) * mm});
            skLineSegment(sketch, "E6370", {"start": v(37952.94, 56908.38) * mm, "end": v(37991.89, 56899.29) * mm});
            skLineSegment(sketch, "E6371", {"start": v(37968.35, 57042.12) * mm, "end": v(38002.32, 57063.23) * mm});
            skLineSegment(sketch, "E6372", {"start": v(37859.8, 57165.42) * mm, "end": v(37868.9, 57204.37) * mm});
            skLineSegment(sketch, "E6373", {"start": v(37665.65, 57170.88) * mm, "end": v(37643.15, 57207.08) * mm});
            skLineSegment(sketch, "E6374", {"start": v(37827.76, 56876.12) * mm, "end": v(37839.36, 56837.84) * mm});
            skLineSegment(sketch, "E6375", {"start": v(37903.94, 56890.81) * mm, "end": v(37939.21, 56871.95) * mm});
            skLineSegment(sketch, "E6376", {"start": v(37950.43, 56985.54) * mm, "end": v(37988.71, 56997.14) * mm});
            skLineSegment(sketch, "E6377", {"start": v(37896.91, 57109.06) * mm, "end": v(37915.78, 57144.33) * mm});
            skLineSegment(sketch, "E6378", {"start": v(37741.25, 57161.57) * mm, "end": v(37729.65, 57199.85) * mm});
            skLineSegment(sketch, "E6379", {"start": v(37570.39, 57069.22) * mm, "end": v(37532.8, 57089.33) * mm});
            skLineSegment(sketch, "E6380", {"start": v(37858.15, 56895.01) * mm, "end": v(37887.34, 56867.66) * mm});
            skLineSegment(sketch, "E6381", {"start": v(37916.78, 56945.83) * mm, "end": v(37956.76, 56947.12) * mm});
            skLineSegment(sketch, "E6382", {"start": v(37909.68, 57051.1) * mm, "end": v(37937.04, 57080.3) * mm});
            skLineSegment(sketch, "E6383", {"start": v(37801.57, 57131.32) * mm, "end": v(37800.27, 57171.3) * mm});
            skLineSegment(sketch, "E6384", {"start": v(37640.51, 57098.97) * mm, "end": v(37611.33, 57126.32) * mm});
            skLineSegment(sketch, "E6385", {"start": v(37538.71, 56933.56) * mm, "end": v(37496.11, 56932.17) * mm});
            skLineSegment(sketch, "E6386", {"start": v(37875.03, 56926.57) * mm, "end": v(37913.98, 56917.47) * mm});
            skLineSegment(sketch, "E6387", {"start": v(37900.4, 56999.9) * mm, "end": v(37934.37, 57021) * mm});
            skLineSegment(sketch, "E6388", {"start": v(37841.61, 57087.52) * mm, "end": v(37850.7, 57126.47) * mm});
            skLineSegment(sketch, "E6389", {"start": v(37707.88, 57102.93) * mm, "end": v(37686.76, 57136.9) * mm});
            skLineSegment(sketch, "E6390", {"start": v(37584.57, 56994.38) * mm, "end": v(37545.62, 57003.47) * mm});
            skLineSegment(sketch, "E6391", {"start": v(37579.12, 56800.23) * mm, "end": v(37542.91, 56777.73) * mm});
            skLineSegment(sketch, "E6392", {"start": v(37873.87, 56962.34) * mm, "end": v(37912.15, 56973.94) * mm});
            skLineSegment(sketch, "E6393", {"start": v(37859.18, 57038.52) * mm, "end": v(37878.04, 57073.8) * mm});
            skLineSegment(sketch, "E6394", {"start": v(37764.46, 57085.01) * mm, "end": v(37752.85, 57123.3) * mm});
            skLineSegment(sketch, "E6395", {"start": v(37640.93, 57031.5) * mm, "end": v(37605.66, 57050.36) * mm});
            skLineSegment(sketch, "E6396", {"start": v(37588.42, 56875.83) * mm, "end": v(37550.14, 56864.23) * mm});
            skLineSegment(sketch, "E6397", {"start": v(37680.77, 56704.97) * mm, "end": v(37660.67, 56667.38) * mm});
            skLineSegment(sketch, "E6398", {"start": v(37854.98, 56992.73) * mm, "end": v(37882.33, 57021.92) * mm});
            skLineSegment(sketch, "E6399", {"start": v(37804.17, 57051.36) * mm, "end": v(37802.87, 57091.34) * mm});
            skLineSegment(sketch, "E6400", {"start": v(37698.89, 57044.26) * mm, "end": v(37669.7, 57071.62) * mm});
            skLineSegment(sketch, "E6401", {"start": v(37618.67, 56936.15) * mm, "end": v(37578.7, 56934.85) * mm});
            skLineSegment(sketch, "E6402", {"start": v(37651.02, 56775.1) * mm, "end": v(37623.67, 56745.9) * mm});
            skLineSegment(sketch, "E6403", {"start": v(37816.44, 56673.3) * mm, "end": v(37817.82, 56630.7) * mm});
            skLineSegment(sketch, "E6404", {"start": v(37823.42, 57009.61) * mm, "end": v(37832.52, 57048.56) * mm});
            skLineSegment(sketch, "E6405", {"start": v(37750.1, 57034.98) * mm, "end": v(37728.99, 57068.95) * mm});
            skLineSegment(sketch, "E6406", {"start": v(37662.48, 56976.2) * mm, "end": v(37623.52, 56985.29) * mm});
            skLineSegment(sketch, "E6407", {"start": v(37647.06, 56842.46) * mm, "end": v(37613.1, 56821.34) * mm});
            skLineSegment(sketch, "E6408", {"start": v(37755.61, 56719.15) * mm, "end": v(37746.52, 56680.2) * mm});
            skLineSegment(sketch, "E6409", {"start": v(37949.76, 56713.7) * mm, "end": v(37972.26, 56677.5) * mm});
            skLineSegment(sketch, "E6410", {"start": v(37787.66, 57008.45) * mm, "end": v(37776.06, 57046.73) * mm});
            skLineSegment(sketch, "E6411", {"start": v(37711.47, 56993.76) * mm, "end": v(37676.2, 57012.63) * mm});
            skLineSegment(sketch, "E6412", {"start": v(37664.98, 56899.04) * mm, "end": v(37626.7, 56887.43) * mm});
            skLineSegment(sketch, "E6413", {"start": v(37718.5, 56775.5) * mm, "end": v(37699.64, 56740.24) * mm});
            skLineSegment(sketch, "E6414", {"start": v(37874.16, 56723) * mm, "end": v(37885.76, 56684.72) * mm});
            skLineSegment(sketch, "E6415", {"start": v(38045.03, 56815.35) * mm, "end": v(38082.61, 56795.25) * mm});
            skLineSegment(sketch, "E6416", {"start": v(37757.26, 56989.56) * mm, "end": v(37728.07, 57016.91) * mm});
            skLineSegment(sketch, "E6417", {"start": v(37698.63, 56938.75) * mm, "end": v(37658.65, 56937.45) * mm});
            skLineSegment(sketch, "E6418", {"start": v(37705.73, 56833.47) * mm, "end": v(37678.38, 56804.28) * mm});
            skLineSegment(sketch, "E6419", {"start": v(37813.84, 56753.25) * mm, "end": v(37815.14, 56713.27) * mm});
            skLineSegment(sketch, "E6420", {"start": v(37974.9, 56785.6) * mm, "end": v(38004.09, 56758.25) * mm});
            skLineSegment(sketch, "E6421", {"start": v(38076.7, 56951.02) * mm, "end": v(38119.3, 56952.4) * mm});
            skLineSegment(sketch, "E6422", {"start": v(37740.38, 56958) * mm, "end": v(37701.43, 56967.1) * mm});
            skLineSegment(sketch, "E6423", {"start": v(37715.01, 56884.68) * mm, "end": v(37681.04, 56863.57) * mm});
            skLineSegment(sketch, "E6424", {"start": v(37773.8, 56797.06) * mm, "end": v(37764.7, 56758.1) * mm});
            skLineSegment(sketch, "E6425", {"start": v(37907.54, 56781.64) * mm, "end": v(37928.65, 56747.67) * mm});
            skLineSegment(sketch, "E6426", {"start": v(38030.84, 56890.2) * mm, "end": v(38069.8, 56881.1) * mm});
            skLineSegment(sketch, "E6427", {"start": v(38036.3, 57084.34) * mm, "end": v(38072.5, 57106.84) * mm});
            skLineSegment(sketch, "E6428", {"start": v(38168.9, 56729.8) * mm, "end": v(38153.46, 56740.8) * mm});
            skLineSegment(sketch, "E6429", {"start": v(38146.88, 56705) * mm, "end": v(38157.62, 56695.99) * mm});
            skLineSegment(sketch, "E6430", {"start": v(38157.62, 56695.99) * mm, "end": v(38115.81, 56685.76) * mm});
            skLineSegment(sketch, "E6431", {"start": v(38115.81, 56685.76) * mm, "end": v(38127.98, 56722.5) * mm});
            skLineSegment(sketch, "E6432", {"start": v(38127.98, 56722.5) * mm, "end": v(38139.51, 56712.88) * mm});
            skLineSegment(sketch, "E6433", {"start": v(37446.51, 57154.78) * mm, "end": v(37461.96, 57143.76) * mm});
            skLineSegment(sketch, "E6434", {"start": v(37468.53, 57179.56) * mm, "end": v(37457.8, 57188.59) * mm});
            skLineSegment(sketch, "E6435", {"start": v(37457.8, 57188.59) * mm, "end": v(37499.6, 57198.81) * mm});
            skLineSegment(sketch, "E6436", {"start": v(37499.6, 57198.81) * mm, "end": v(37487.44, 57162.06) * mm});
            skLineSegment(sketch, "E6437", {"start": v(37487.44, 57162.06) * mm, "end": v(37475.9, 57171.7) * mm});
            skCircle(sketch, "E6438", {"center": v(37977.23, 56382.72) * mm, "radius": 7.85 * mm});
            skCircle(sketch, "E6439", {"center": v(37837.8, 56340.46) * mm, "radius": 7.85 * mm});
            skCircle(sketch, "E6440", {"center": v(37709.12, 56301.47) * mm, "radius": 7.85 * mm});
            skCircle(sketch, "E6441", {"center": v(38116.66, 56424.97) * mm, "radius": 7.85 * mm});
            skCircle(sketch, "E6442", {"center": v(38245.33, 56463.96) * mm, "radius": 7.85 * mm});
            skCircle(sketch, "E6443", {"center": v(37638.1, 57501.83) * mm, "radius": 7.85 * mm});
            skCircle(sketch, "E6444", {"center": v(37498.66, 57459.57) * mm, "radius": 7.85 * mm});
            skCircle(sketch, "E6445", {"center": v(37369.99, 57420.58) * mm, "radius": 7.85 * mm});
            skCircle(sketch, "E6446", {"center": v(37777.53, 57544.08) * mm, "radius": 7.85 * mm});
            skCircle(sketch, "E6447", {"center": v(37906.2, 57583.07) * mm, "radius": 7.85 * mm});
            skLineSegment(sketch, "E6448", {"start": v(37223.58, 57559.4) * mm, "end": v(36898.77, 58631.27) * mm});
            skLineSegment(sketch, "E6449", {"start": v(36932.12, 58693.62) * mm, "end": v(37563.75, 58885.03) * mm});
            skLineSegment(sketch, "E6450", {"start": v(37626.1, 58851.68) * mm, "end": v(37950.92, 57779.81) * mm});
            skLineSegment(sketch, "E6451", {"start": v(37917.57, 57717.46) * mm, "end": v(37285.93, 57526.05) * mm});
            skCircle(sketch, "E6452", {"center": v(37424.89, 58205.56) * mm, "radius": 311.76 * mm});
            skLineSegment(sketch, "E6453", {"start": v(37285.93, 57526.05) * mm, "end": v(37223.58, 57559.4) * mm});
            skLineSegment(sketch, "E6454", {"start": v(37917.57, 57717.46) * mm, "end": v(37950.92, 57779.81) * mm});
            skLineSegment(sketch, "E6455", {"start": v(36932.12, 58693.62) * mm, "end": v(36898.77, 58631.27) * mm});
            skLineSegment(sketch, "E6456", {"start": v(37563.75, 58885.03) * mm, "end": v(37626.1, 58851.68) * mm});
            skCircle(sketch, "E6457", {"center": v(37424.89, 58205.56) * mm, "radius": 69.13 * mm});
            skCircle(sketch, "E6458", {"center": v(37424.89, 58205.56) * mm, "radius": 109.13 * mm});
            skCircle(sketch, "E6459", {"center": v(37424.89, 58205.56) * mm, "radius": 149.13 * mm});
            skCircle(sketch, "E6460", {"center": v(37424.89, 58205.56) * mm, "radius": 189.13 * mm});
            skCircle(sketch, "E6461", {"center": v(37424.89, 58205.56) * mm, "radius": 229.13 * mm});
            skCircle(sketch, "E6462", {"center": v(37424.89, 58205.56) * mm, "radius": 269.13 * mm});
            skLineSegment(sketch, "E6463", {"start": v(37358.73, 58185.5) * mm, "end": v(37320.44, 58173.9) * mm});
            skLineSegment(sketch, "E6464", {"start": v(37373.42, 58109.32) * mm, "end": v(37354.55, 58074.05) * mm});
            skLineSegment(sketch, "E6465", {"start": v(37468.14, 58062.83) * mm, "end": v(37479.74, 58024.55) * mm});
            skLineSegment(sketch, "E6466", {"start": v(37591.67, 58116.35) * mm, "end": v(37626.94, 58097.49) * mm});
            skLineSegment(sketch, "E6467", {"start": v(37644.18, 58272) * mm, "end": v(37682.46, 58283.6) * mm});
            skLineSegment(sketch, "E6468", {"start": v(37551.83, 58442.88) * mm, "end": v(37571.93, 58480.46) * mm});
            skLineSegment(sketch, "E6469", {"start": v(37377.61, 58155.11) * mm, "end": v(37350.26, 58125.92) * mm});
            skLineSegment(sketch, "E6470", {"start": v(37428.43, 58096.48) * mm, "end": v(37429.73, 58056.5) * mm});
            skLineSegment(sketch, "E6471", {"start": v(37533.7, 58103.58) * mm, "end": v(37562.9, 58076.23) * mm});
            skLineSegment(sketch, "E6472", {"start": v(37613.92, 58211.7) * mm, "end": v(37653.9, 58212.99) * mm});
            skLineSegment(sketch, "E6473", {"start": v(37581.57, 58372.75) * mm, "end": v(37608.92, 58401.94) * mm});
            skLineSegment(sketch, "E6474", {"start": v(37416.16, 58474.55) * mm, "end": v(37414.78, 58517.15) * mm});
            skLineSegment(sketch, "E6475", {"start": v(37409.17, 58138.23) * mm, "end": v(37400.08, 58099.28) * mm});
            skLineSegment(sketch, "E6476", {"start": v(37482.5, 58112.86) * mm, "end": v(37503.6, 58078.89) * mm});
            skLineSegment(sketch, "E6477", {"start": v(37570.12, 58171.65) * mm, "end": v(37609.07, 58162.56) * mm});
            skLineSegment(sketch, "E6478", {"start": v(37585.53, 58305.39) * mm, "end": v(37619.5, 58326.5) * mm});
            skLineSegment(sketch, "E6479", {"start": v(37476.98, 58428.7) * mm, "end": v(37486.08, 58467.64) * mm});
            skLineSegment(sketch, "E6480", {"start": v(37282.83, 58434.15) * mm, "end": v(37260.33, 58470.35) * mm});
            skLineSegment(sketch, "E6481", {"start": v(37444.94, 58139.4) * mm, "end": v(37456.54, 58101.11) * mm});
            skLineSegment(sketch, "E6482", {"start": v(37521.12, 58154.08) * mm, "end": v(37556.4, 58135.22) * mm});
            skLineSegment(sketch, "E6483", {"start": v(37567.61, 58248.8) * mm, "end": v(37605.9, 58260.4) * mm});
            skLineSegment(sketch, "E6484", {"start": v(37514.1, 58372.33) * mm, "end": v(37532.96, 58407.6) * mm});
            skLineSegment(sketch, "E6485", {"start": v(37358.44, 58424.84) * mm, "end": v(37346.84, 58463.12) * mm});
            skLineSegment(sketch, "E6486", {"start": v(37187.57, 58332.5) * mm, "end": v(37149.98, 58352.6) * mm});
            skLineSegment(sketch, "E6487", {"start": v(37475.33, 58158.28) * mm, "end": v(37504.52, 58130.93) * mm});
            skLineSegment(sketch, "E6488", {"start": v(37533.97, 58209.1) * mm, "end": v(37573.94, 58210.4) * mm});
            skLineSegment(sketch, "E6489", {"start": v(37526.87, 58314.38) * mm, "end": v(37554.22, 58343.56) * mm});
            skLineSegment(sketch, "E6490", {"start": v(37418.75, 58394.6) * mm, "end": v(37417.46, 58434.57) * mm});
            skLineSegment(sketch, "E6491", {"start": v(37257.7, 58362.24) * mm, "end": v(37228.5, 58389.6) * mm});
            skLineSegment(sketch, "E6492", {"start": v(37155.9, 58196.83) * mm, "end": v(37113.3, 58195.44) * mm});
            skLineSegment(sketch, "E6493", {"start": v(37492.21, 58189.84) * mm, "end": v(37531.17, 58180.74) * mm});
            skLineSegment(sketch, "E6494", {"start": v(37517.58, 58263.16) * mm, "end": v(37551.56, 58284.27) * mm});
            skLineSegment(sketch, "E6495", {"start": v(37458.8, 58350.79) * mm, "end": v(37467.89, 58389.74) * mm});
            skLineSegment(sketch, "E6496", {"start": v(37325.06, 58366.2) * mm, "end": v(37303.95, 58400.17) * mm});
            skLineSegment(sketch, "E6497", {"start": v(37201.75, 58257.65) * mm, "end": v(37162.8, 58266.74) * mm});
            skLineSegment(sketch, "E6498", {"start": v(37196.3, 58063.5) * mm, "end": v(37160.1, 58041) * mm});
            skLineSegment(sketch, "E6499", {"start": v(37491.05, 58225.6) * mm, "end": v(37529.33, 58237.2) * mm});
            skLineSegment(sketch, "E6500", {"start": v(37476.36, 58301.79) * mm, "end": v(37495.23, 58337.06) * mm});
            skLineSegment(sketch, "E6501", {"start": v(37381.64, 58348.28) * mm, "end": v(37370.04, 58386.56) * mm});
            skLineSegment(sketch, "E6502", {"start": v(37258.11, 58294.76) * mm, "end": v(37222.84, 58313.63) * mm});
            skLineSegment(sketch, "E6503", {"start": v(37205.6, 58139.1) * mm, "end": v(37167.32, 58127.5) * mm});
            skLineSegment(sketch, "E6504", {"start": v(37297.95, 57968.24) * mm, "end": v(37277.85, 57930.65) * mm});
            skLineSegment(sketch, "E6505", {"start": v(37472.16, 58256) * mm, "end": v(37499.51, 58285.19) * mm});
            skLineSegment(sketch, "E6506", {"start": v(37421.35, 58314.63) * mm, "end": v(37420.05, 58354.61) * mm});
            skLineSegment(sketch, "E6507", {"start": v(37316.07, 58307.53) * mm, "end": v(37286.88, 58334.89) * mm});
            skLineSegment(sketch, "E6508", {"start": v(37235.85, 58199.42) * mm, "end": v(37195.87, 58198.12) * mm});
            skLineSegment(sketch, "E6509", {"start": v(37268.2, 58038.36) * mm, "end": v(37240.85, 58009.18) * mm});
            skLineSegment(sketch, "E6510", {"start": v(37433.62, 57936.56) * mm, "end": v(37435, 57893.96) * mm});
            skLineSegment(sketch, "E6511", {"start": v(37440.6, 58272.88) * mm, "end": v(37449.7, 58311.83) * mm});
            skLineSegment(sketch, "E6512", {"start": v(37367.28, 58298.25) * mm, "end": v(37346.17, 58332.22) * mm});
            skLineSegment(sketch, "E6513", {"start": v(37279.66, 58239.46) * mm, "end": v(37240.7, 58248.56) * mm});
            skLineSegment(sketch, "E6514", {"start": v(37264.25, 58105.73) * mm, "end": v(37230.27, 58084.61) * mm});
            skLineSegment(sketch, "E6515", {"start": v(37372.8, 57982.42) * mm, "end": v(37363.7, 57943.47) * mm});
            skLineSegment(sketch, "E6516", {"start": v(37566.95, 57976.97) * mm, "end": v(37589.44, 57940.76) * mm});
            skLineSegment(sketch, "E6517", {"start": v(37404.84, 58271.72) * mm, "end": v(37393.24, 58310) * mm});
            skLineSegment(sketch, "E6518", {"start": v(37328.65, 58257.03) * mm, "end": v(37293.38, 58275.9) * mm});
            skLineSegment(sketch, "E6519", {"start": v(37282.16, 58162.3) * mm, "end": v(37243.88, 58150.7) * mm});
            skLineSegment(sketch, "E6520", {"start": v(37335.68, 58038.78) * mm, "end": v(37316.82, 58003.5) * mm});
            skLineSegment(sketch, "E6521", {"start": v(37491.34, 57986.27) * mm, "end": v(37502.94, 57947.99) * mm});
            skLineSegment(sketch, "E6522", {"start": v(37662.2, 58078.62) * mm, "end": v(37699.8, 58058.52) * mm});
            skLineSegment(sketch, "E6523", {"start": v(37374.44, 58252.83) * mm, "end": v(37345.26, 58280.18) * mm});
            skLineSegment(sketch, "E6524", {"start": v(37315.81, 58202.02) * mm, "end": v(37275.83, 58200.72) * mm});
            skLineSegment(sketch, "E6525", {"start": v(37322.91, 58096.74) * mm, "end": v(37295.56, 58067.55) * mm});
            skLineSegment(sketch, "E6526", {"start": v(37431.02, 58016.52) * mm, "end": v(37432.32, 57976.54) * mm});
            skLineSegment(sketch, "E6527", {"start": v(37592.08, 58048.87) * mm, "end": v(37621.27, 58021.52) * mm});
            skLineSegment(sketch, "E6528", {"start": v(37693.88, 58214.29) * mm, "end": v(37736.48, 58215.67) * mm});
            skLineSegment(sketch, "E6529", {"start": v(37357.56, 58221.27) * mm, "end": v(37318.61, 58230.37) * mm});
            skLineSegment(sketch, "E6530", {"start": v(37332.2, 58147.95) * mm, "end": v(37298.22, 58126.84) * mm});
            skLineSegment(sketch, "E6531", {"start": v(37390.98, 58060.33) * mm, "end": v(37381.89, 58021.37) * mm});
            skLineSegment(sketch, "E6532", {"start": v(37524.72, 58044.91) * mm, "end": v(37545.83, 58010.94) * mm});
            skLineSegment(sketch, "E6533", {"start": v(37648.02, 58153.46) * mm, "end": v(37686.98, 58144.37) * mm});
            skLineSegment(sketch, "E6534", {"start": v(37653.48, 58347.61) * mm, "end": v(37689.68, 58370.11) * mm});
            skLineSegment(sketch, "E6535", {"start": v(37786.08, 57993.06) * mm, "end": v(37770.64, 58004.08) * mm});
            skLineSegment(sketch, "E6536", {"start": v(37764.07, 57968.28) * mm, "end": v(37774.8, 57959.26) * mm});
            skLineSegment(sketch, "E6537", {"start": v(37774.8, 57959.26) * mm, "end": v(37733, 57949.03) * mm});
            skLineSegment(sketch, "E6538", {"start": v(37733, 57949.03) * mm, "end": v(37745.16, 57985.78) * mm});
            skLineSegment(sketch, "E6539", {"start": v(37745.16, 57985.78) * mm, "end": v(37756.7, 57976.15) * mm});
            skLineSegment(sketch, "E6540", {"start": v(37063.7, 58418.05) * mm, "end": v(37079.14, 58407.03) * mm});
            skLineSegment(sketch, "E6541", {"start": v(37085.71, 58442.83) * mm, "end": v(37074.98, 58451.86) * mm});
            skLineSegment(sketch, "E6542", {"start": v(37074.98, 58451.86) * mm, "end": v(37116.78, 58462.08) * mm});
            skLineSegment(sketch, "E6543", {"start": v(37116.78, 58462.08) * mm, "end": v(37104.62, 58425.33) * mm});
            skLineSegment(sketch, "E6544", {"start": v(37104.62, 58425.33) * mm, "end": v(37093.08, 58434.97) * mm});
            skCircle(sketch, "E6545", {"center": v(37594.4, 57645.99) * mm, "radius": 7.85 * mm});
            skCircle(sketch, "E6546", {"center": v(37454.97, 57603.73) * mm, "radius": 7.85 * mm});
            skCircle(sketch, "E6547", {"center": v(37326.3, 57564.74) * mm, "radius": 7.85 * mm});
            skCircle(sketch, "E6548", {"center": v(37733.84, 57688.24) * mm, "radius": 7.85 * mm});
            skCircle(sketch, "E6549", {"center": v(37862.51, 57727.23) * mm, "radius": 7.85 * mm});
            skCircle(sketch, "E6550", {"center": v(37255.28, 58765.1) * mm, "radius": 7.85 * mm});
            skCircle(sketch, "E6551", {"center": v(37115.84, 58722.84) * mm, "radius": 7.85 * mm});
            skCircle(sketch, "E6552", {"center": v(36987.17, 58683.85) * mm, "radius": 7.85 * mm});
            skCircle(sketch, "E6553", {"center": v(37394.71, 58807.35) * mm, "radius": 7.85 * mm});
            skCircle(sketch, "E6554", {"center": v(37523.38, 58846.34) * mm, "radius": 7.85 * mm});
            skLineSegment(sketch, "E6555", {"start": v(36840.76, 58822.67) * mm, "end": v(36515.95, 59894.54) * mm});
            skLineSegment(sketch, "E6556", {"start": v(36549.3, 59956.9) * mm, "end": v(37180.93, 60148.3) * mm});
            skLineSegment(sketch, "E6557", {"start": v(37243.29, 60114.95) * mm, "end": v(37568.1, 59043.08) * mm});
            skLineSegment(sketch, "E6558", {"start": v(37534.75, 58980.73) * mm, "end": v(36903.11, 58789.32) * mm});
            skCircle(sketch, "E6559", {"center": v(37042.07, 59468.83) * mm, "radius": 311.76 * mm});
            skLineSegment(sketch, "E6560", {"start": v(36903.11, 58789.32) * mm, "end": v(36840.76, 58822.67) * mm});
            skLineSegment(sketch, "E6561", {"start": v(37534.75, 58980.73) * mm, "end": v(37568.1, 59043.08) * mm});
            skLineSegment(sketch, "E6562", {"start": v(36549.3, 59956.9) * mm, "end": v(36515.95, 59894.54) * mm});
            skLineSegment(sketch, "E6563", {"start": v(37180.93, 60148.3) * mm, "end": v(37243.29, 60114.95) * mm});
            skCircle(sketch, "E6564", {"center": v(37042.07, 59468.83) * mm, "radius": 69.13 * mm});
            skCircle(sketch, "E6565", {"center": v(37042.07, 59468.83) * mm, "radius": 109.13 * mm});
            skCircle(sketch, "E6566", {"center": v(37042.07, 59468.83) * mm, "radius": 149.13 * mm});
            skCircle(sketch, "E6567", {"center": v(37042.07, 59468.83) * mm, "radius": 189.13 * mm});
            skCircle(sketch, "E6568", {"center": v(37042.07, 59468.83) * mm, "radius": 229.13 * mm});
            skCircle(sketch, "E6569", {"center": v(37042.07, 59468.83) * mm, "radius": 269.13 * mm});
            skLineSegment(sketch, "E6570", {"start": v(36975.9, 59448.78) * mm, "end": v(36937.63, 59437.18) * mm});
            skLineSegment(sketch, "E6571", {"start": v(36990.6, 59372.6) * mm, "end": v(36971.73, 59337.32) * mm});
            skLineSegment(sketch, "E6572", {"start": v(37085.32, 59326.1) * mm, "end": v(37096.92, 59287.82) * mm});
            skLineSegment(sketch, "E6573", {"start": v(37208.85, 59379.62) * mm, "end": v(37244.12, 59360.76) * mm});
            skLineSegment(sketch, "E6574", {"start": v(37261.36, 59535.28) * mm, "end": v(37299.64, 59546.88) * mm});
            skLineSegment(sketch, "E6575", {"start": v(37169, 59706.15) * mm, "end": v(37189.11, 59743.73) * mm});
            skLineSegment(sketch, "E6576", {"start": v(36994.8, 59418.38) * mm, "end": v(36967.44, 59389.2) * mm});
            skLineSegment(sketch, "E6577", {"start": v(37045.61, 59359.75) * mm, "end": v(37046.9, 59319.77) * mm});
            skLineSegment(sketch, "E6578", {"start": v(37150.9, 59366.85) * mm, "end": v(37180.08, 59339.5) * mm});
            skLineSegment(sketch, "E6579", {"start": v(37231.1, 59474.96) * mm, "end": v(37271.09, 59476.26) * mm});
            skLineSegment(sketch, "E6580", {"start": v(37198.75, 59636.02) * mm, "end": v(37226.1, 59665.2) * mm});
            skLineSegment(sketch, "E6581", {"start": v(37033.34, 59737.82) * mm, "end": v(37031.96, 59780.42) * mm});
            skLineSegment(sketch, "E6582", {"start": v(37026.35, 59401.5) * mm, "end": v(37017.26, 59362.55) * mm});
            skLineSegment(sketch, "E6583", {"start": v(37099.68, 59376.13) * mm, "end": v(37120.79, 59342.16) * mm});
            skLineSegment(sketch, "E6584", {"start": v(37187.3, 59434.92) * mm, "end": v(37226.25, 59425.83) * mm});
            skLineSegment(sketch, "E6585", {"start": v(37202.71, 59568.66) * mm, "end": v(37236.69, 59589.77) * mm});
            skLineSegment(sketch, "E6586", {"start": v(37094.17, 59691.96) * mm, "end": v(37103.26, 59730.91) * mm});
            skLineSegment(sketch, "E6587", {"start": v(36900.01, 59697.42) * mm, "end": v(36877.52, 59733.62) * mm});
            skLineSegment(sketch, "E6588", {"start": v(37062.12, 59402.66) * mm, "end": v(37073.72, 59364.38) * mm});
            skLineSegment(sketch, "E6589", {"start": v(37138.3, 59417.35) * mm, "end": v(37173.58, 59398.49) * mm});
            skLineSegment(sketch, "E6590", {"start": v(37184.8, 59512.08) * mm, "end": v(37223.08, 59523.68) * mm});
            skLineSegment(sketch, "E6591", {"start": v(37131.28, 59635.6) * mm, "end": v(37150.14, 59670.87) * mm});
            skLineSegment(sketch, "E6592", {"start": v(36975.62, 59688.11) * mm, "end": v(36964.02, 59726.4) * mm});
            skLineSegment(sketch, "E6593", {"start": v(36804.75, 59595.76) * mm, "end": v(36767.17, 59615.87) * mm});
            skLineSegment(sketch, "E6594", {"start": v(37092.52, 59421.55) * mm, "end": v(37121.7, 59394.2) * mm});
            skLineSegment(sketch, "E6595", {"start": v(37151.15, 59472.37) * mm, "end": v(37191.13, 59473.66) * mm});
            skLineSegment(sketch, "E6596", {"start": v(37144.05, 59577.65) * mm, "end": v(37171.4, 59606.83) * mm});
            skLineSegment(sketch, "E6597", {"start": v(37035.94, 59657.86) * mm, "end": v(37034.64, 59697.84) * mm});
            skLineSegment(sketch, "E6598", {"start": v(36874.88, 59625.5) * mm, "end": v(36845.7, 59652.86) * mm});
            skLineSegment(sketch, "E6599", {"start": v(36773.08, 59460.1) * mm, "end": v(36730.48, 59458.71) * mm});
            skLineSegment(sketch, "E6600", {"start": v(37109.4, 59453.1) * mm, "end": v(37148.35, 59444.01) * mm});
            skLineSegment(sketch, "E6601", {"start": v(37134.76, 59526.43) * mm, "end": v(37168.74, 59547.54) * mm});
            skLineSegment(sketch, "E6602", {"start": v(37075.98, 59614.06) * mm, "end": v(37085.07, 59653) * mm});
            skLineSegment(sketch, "E6603", {"start": v(36942.24, 59629.47) * mm, "end": v(36921.13, 59663.44) * mm});
            skLineSegment(sketch, "E6604", {"start": v(36818.94, 59520.92) * mm, "end": v(36779.98, 59530.01) * mm});
            skLineSegment(sketch, "E6605", {"start": v(36813.48, 59326.77) * mm, "end": v(36777.28, 59304.27) * mm});
            skLineSegment(sketch, "E6606", {"start": v(37108.23, 59488.88) * mm, "end": v(37146.52, 59500.48) * mm});
            skLineSegment(sketch, "E6607", {"start": v(37093.54, 59565.06) * mm, "end": v(37112.4, 59600.33) * mm});
            skLineSegment(sketch, "E6608", {"start": v(36998.82, 59611.55) * mm, "end": v(36987.22, 59649.83) * mm});
            skLineSegment(sketch, "E6609", {"start": v(36875.3, 59558.03) * mm, "end": v(36840.02, 59576.9) * mm});
            skLineSegment(sketch, "E6610", {"start": v(36822.78, 59402.37) * mm, "end": v(36784.5, 59390.77) * mm});
            skLineSegment(sketch, "E6611", {"start": v(36915.13, 59231.5) * mm, "end": v(36895.03, 59193.92) * mm});
            skLineSegment(sketch, "E6612", {"start": v(37089.35, 59519.27) * mm, "end": v(37116.7, 59548.46) * mm});
            skLineSegment(sketch, "E6613", {"start": v(37038.53, 59577.9) * mm, "end": v(37037.23, 59617.88) * mm});
            skLineSegment(sketch, "E6614", {"start": v(36933.25, 59570.8) * mm, "end": v(36904.07, 59598.16) * mm});
            skLineSegment(sketch, "E6615", {"start": v(36853.04, 59462.7) * mm, "end": v(36813.06, 59461.4) * mm});
            skLineSegment(sketch, "E6616", {"start": v(36885.39, 59301.63) * mm, "end": v(36858.04, 59272.45) * mm});
            skLineSegment(sketch, "E6617", {"start": v(37050.8, 59199.83) * mm, "end": v(37052.18, 59157.23) * mm});
            skLineSegment(sketch, "E6618", {"start": v(37057.79, 59536.15) * mm, "end": v(37066.88, 59575.1) * mm});
            skLineSegment(sketch, "E6619", {"start": v(36984.47, 59561.52) * mm, "end": v(36963.35, 59595.5) * mm});
            skLineSegment(sketch, "E6620", {"start": v(36896.84, 59502.73) * mm, "end": v(36857.89, 59511.83) * mm});
            skLineSegment(sketch, "E6621", {"start": v(36881.43, 59369) * mm, "end": v(36847.46, 59347.88) * mm});
            skLineSegment(sketch, "E6622", {"start": v(36989.98, 59245.7) * mm, "end": v(36980.88, 59206.74) * mm});
            skLineSegment(sketch, "E6623", {"start": v(37184.13, 59240.24) * mm, "end": v(37206.63, 59204.03) * mm});
            skLineSegment(sketch, "E6624", {"start": v(37022.02, 59534.99) * mm, "end": v(37010.42, 59573.27) * mm});
            skLineSegment(sketch, "E6625", {"start": v(36945.84, 59520.3) * mm, "end": v(36910.57, 59539.17) * mm});
            skLineSegment(sketch, "E6626", {"start": v(36899.35, 59425.58) * mm, "end": v(36861.06, 59413.97) * mm});
            skLineSegment(sketch, "E6627", {"start": v(36952.87, 59302.05) * mm, "end": v(36934, 59266.78) * mm});
            skLineSegment(sketch, "E6628", {"start": v(37108.52, 59249.54) * mm, "end": v(37120.12, 59211.26) * mm});
            skLineSegment(sketch, "E6629", {"start": v(37279.4, 59341.89) * mm, "end": v(37316.98, 59321.79) * mm});
            skLineSegment(sketch, "E6630", {"start": v(36991.63, 59516.1) * mm, "end": v(36962.44, 59543.45) * mm});
            skLineSegment(sketch, "E6631", {"start": v(36933, 59465.29) * mm, "end": v(36893.01, 59463.99) * mm});
            skLineSegment(sketch, "E6632", {"start": v(36940.1, 59360) * mm, "end": v(36912.74, 59330.82) * mm});
            skLineSegment(sketch, "E6633", {"start": v(37048.2, 59279.8) * mm, "end": v(37049.5, 59239.81) * mm});
            skLineSegment(sketch, "E6634", {"start": v(37209.26, 59312.14) * mm, "end": v(37238.45, 59284.8) * mm});
            skLineSegment(sketch, "E6635", {"start": v(37311.06, 59477.56) * mm, "end": v(37353.67, 59478.94) * mm});
            skLineSegment(sketch, "E6636", {"start": v(36974.75, 59484.54) * mm, "end": v(36935.8, 59493.64) * mm});
            skLineSegment(sketch, "E6637", {"start": v(36949.38, 59411.22) * mm, "end": v(36915.4, 59390.1) * mm});
            skLineSegment(sketch, "E6638", {"start": v(37008.16, 59323.6) * mm, "end": v(36999.07, 59284.64) * mm});
            skLineSegment(sketch, "E6639", {"start": v(37141.9, 59308.18) * mm, "end": v(37163.01, 59274.21) * mm});
            skLineSegment(sketch, "E6640", {"start": v(37265.2, 59416.73) * mm, "end": v(37304.16, 59407.64) * mm});
            skLineSegment(sketch, "E6641", {"start": v(37270.66, 59610.88) * mm, "end": v(37306.86, 59633.38) * mm});
            skLineSegment(sketch, "E6642", {"start": v(37403.26, 59256.33) * mm, "end": v(37387.82, 59267.35) * mm});
            skLineSegment(sketch, "E6643", {"start": v(37381.25, 59231.55) * mm, "end": v(37391.98, 59222.53) * mm});
            skLineSegment(sketch, "E6644", {"start": v(37391.98, 59222.53) * mm, "end": v(37350.18, 59212.3) * mm});
            skLineSegment(sketch, "E6645", {"start": v(37350.18, 59212.3) * mm, "end": v(37362.34, 59249.05) * mm});
            skLineSegment(sketch, "E6646", {"start": v(37362.34, 59249.05) * mm, "end": v(37373.88, 59239.42) * mm});
            skLineSegment(sketch, "E6647", {"start": v(36680.88, 59681.32) * mm, "end": v(36696.32, 59670.3) * mm});
            skLineSegment(sketch, "E6648", {"start": v(36702.9, 59706.1) * mm, "end": v(36692.16, 59715.13) * mm});
            skLineSegment(sketch, "E6649", {"start": v(36692.16, 59715.13) * mm, "end": v(36733.96, 59725.35) * mm});
            skLineSegment(sketch, "E6650", {"start": v(36733.96, 59725.35) * mm, "end": v(36721.8, 59688.6) * mm});
            skLineSegment(sketch, "E6651", {"start": v(36721.8, 59688.6) * mm, "end": v(36710.27, 59698.24) * mm});
            skCircle(sketch, "E6652", {"center": v(37211.6, 58909.26) * mm, "radius": 7.85 * mm});
            skCircle(sketch, "E6653", {"center": v(37072.16, 58867) * mm, "radius": 7.85 * mm});
            skCircle(sketch, "E6654", {"center": v(36943.49, 58828.01) * mm, "radius": 7.85 * mm});
            skCircle(sketch, "E6655", {"center": v(37351.03, 58951.5) * mm, "radius": 7.85 * mm});
            skCircle(sketch, "E6656", {"center": v(37479.7, 58990.5) * mm, "radius": 7.85 * mm});
            skCircle(sketch, "E6657", {"center": v(36872.46, 60028.37) * mm, "radius": 7.85 * mm});
            skCircle(sketch, "E6658", {"center": v(36733.02, 59986.11) * mm, "radius": 7.85 * mm});
            skCircle(sketch, "E6659", {"center": v(36604.35, 59947.12) * mm, "radius": 7.85 * mm});
            skCircle(sketch, "E6660", {"center": v(37011.9, 60070.62) * mm, "radius": 7.85 * mm});
            skCircle(sketch, "E6661", {"center": v(37140.56, 60109.61) * mm, "radius": 7.85 * mm});
            skLineSegment(sketch, "E6662", {"start": v(39605.1, 60539.37) * mm, "end": v(38138.41, 60095.43) * mm});
            skLineSegment(sketch, "E6663", {"start": v(39667.4, 60333.6) * mm, "end": v(38200.7, 59889.65) * mm});
            skLineSegment(sketch, "E6664", {"start": v(41889.85, 61230.92) * mm, "end": v(40476.08, 60803) * mm});
            skLineSegment(sketch, "E6665", {"start": v(41952.14, 61025.14) * mm, "end": v(40538.37, 60597.22) * mm});
            skLineSegment(sketch, "E6666", {"start": v(39605.1, 60539.37) * mm, "end": v(39667.4, 60333.6) * mm});
            skLineSegment(sketch, "E6667", {"start": v(40476.08, 60803) * mm, "end": v(40538.37, 60597.22) * mm});
            skLineSegment(sketch, "E6668", {"start": v(39605.1, 60539.37) * mm, "end": v(39645.3, 60551.54) * mm});
            skLineSegment(sketch, "E6669", {"start": v(39645.3, 60551.54) * mm, "end": v(39707.6, 60345.76) * mm});
            skLineSegment(sketch, "E6670", {"start": v(39707.6, 60345.76) * mm, "end": v(39667.4, 60333.6) * mm});
            skLineSegment(sketch, "E6671", {"start": v(39667.4, 60333.6) * mm, "end": v(39605.1, 60539.37) * mm});
            skLineSegment(sketch, "E6672", {"start": v(40435.89, 60790.83) * mm, "end": v(40476.08, 60803) * mm});
            skLineSegment(sketch, "E6673", {"start": v(40538.37, 60597.22) * mm, "end": v(40498.17, 60585.05) * mm});
            skLineSegment(sketch, "E6674", {"start": v(40498.17, 60585.05) * mm, "end": v(40435.89, 60790.83) * mm});
            skLineSegment(sketch, "E6675", {"start": v(40476.08, 60803) * mm, "end": v(40435.89, 60790.83) * mm});
            skLineSegment(sketch, "E6676", {"start": v(39667.4, 60333.6) * mm, "end": v(39707.6, 60345.76) * mm});
            skLineSegment(sketch, "E6677", {"start": v(40435.89, 60790.83) * mm, "end": v(40498.17, 60585.05) * mm});
            skArc(sketch, "E6678", {"start": v(40435.89, 60790.83) * mm, "mid": v(40035.12, 61279.77) * mm, "end": v(39406.01, 61342.12) * mm});
            skLineSegment(sketch, "E6679", {"start": v(39645.3, 60551.54) * mm, "end": v(39406.01, 61342.12) * mm});
            skLineSegment(sketch, "E6680", {"start": v(39406.01, 61342.12) * mm, "end": v(39448.56, 61355) * mm});
            skLineSegment(sketch, "E6681", {"start": v(39448.56, 61355) * mm, "end": v(39687.85, 60564.42) * mm});
            skLineSegment(sketch, "E6682", {"start": v(39687.85, 60564.42) * mm, "end": v(39645.3, 60551.54) * mm});
            skLineSegment(sketch, "E6683", {"start": v(39687.85, 60564.42) * mm, "end": v(39448.56, 61355) * mm});
            skLineSegment(sketch, "E6684", {"start": v(39645.3, 60551.54) * mm, "end": v(39687.85, 60564.42) * mm});
            skLineSegment(sketch, "E6685", {"start": v(40024.83, 67734) * mm, "end": v(38542.93, 65720.56) * mm});
            skLineSegment(sketch, "E6686", {"start": v(38542.93, 65720.56) * mm, "end": v(40153.7, 64535.04) * mm});
            skLineSegment(sketch, "E6687", {"start": v(41635.6, 66548.49) * mm, "end": v(40024.83, 67734) * mm});
            skLineSegment(sketch, "E6688", {"start": v(40024.83, 67734) * mm, "end": v(40894.64, 65541.76) * mm});
            skLineSegment(sketch, "E6689", {"start": v(40153.7, 64535.04) * mm, "end": v(41635.6, 66548.49) * mm});
            skLineSegment(sketch, "E6690", {"start": v(41635.6, 66548.49) * mm, "end": v(39283.88, 66727.28) * mm});
            skLineSegment(sketch, "E6691", {"start": v(40024.83, 67734) * mm, "end": v(41635.6, 66548.49) * mm});
            skLineSegment(sketch, "E6692", {"start": v(39283.88, 66727.28) * mm, "end": v(40894.64, 65541.76) * mm});
            skLineSegment(sketch, "E6693", {"start": v(39283.88, 66727.28) * mm, "end": v(40141.36, 64544.11) * mm});
            skLineSegment(sketch, "E6694", {"start": v(40894.64, 65541.76) * mm, "end": v(38542.93, 65720.56) * mm});
            skLineSegment(sketch, "E6695", {"start": v(40293.12, 63699.64) * mm, "end": v(42474.67, 66663.7) * mm});
            skLineSegment(sketch, "E6696", {"start": v(42474.67, 66663.7) * mm, "end": v(39897.26, 68572.89) * mm});
            skLineSegment(sketch, "E6697", {"start": v(39897.26, 68572.89) * mm, "end": v(37704.05, 65592.99) * mm});
            skLineSegment(sketch, "E6698", {"start": v(37704.05, 65592.99) * mm, "end": v(40293.12, 63699.64) * mm});
            skLineSegment(sketch, "E6699", {"start": v(40083.63, 57116.22) * mm, "end": v(40185.03, 57146.91) * mm});
            skLineSegment(sketch, "E6700", {"start": v(40185.03, 57146.91) * mm, "end": v(40131.87, 57322.54) * mm});
            skLineSegment(sketch, "E6701", {"start": v(40424.31, 57219.34) * mm, "end": v(40245.7, 57809.4) * mm});
            skLineSegment(sketch, "E6702", {"start": v(40185.03, 57146.91) * mm, "end": v(40424.31, 57219.34) * mm});
            skLineSegment(sketch, "E6703", {"start": v(40663.6, 57291.76) * mm, "end": v(40359.54, 58296.27) * mm});
            skLineSegment(sketch, "E6704", {"start": v(40424.31, 57219.34) * mm, "end": v(40663.6, 57291.76) * mm});
            skLineSegment(sketch, "E6705", {"start": v(40584.2, 58417.02) * mm, "end": v(40372.82, 58353.03) * mm});
            skLineSegment(sketch, "E6706", {"start": v(40663.6, 57291.76) * mm, "end": v(40902.87, 57364.19) * mm});
            skLineSegment(sketch, "E6707", {"start": v(40902.87, 57364.19) * mm, "end": v(40584.2, 58417.02) * mm});
            skLineSegment(sketch, "E6708", {"start": v(40902.87, 57364.19) * mm, "end": v(41142.15, 57436.61) * mm});
            skLineSegment(sketch, "E6709", {"start": v(40584.2, 58417.02) * mm, "end": v(40823.48, 58489.44) * mm});
            skLineSegment(sketch, "E6710", {"start": v(41142.15, 57436.61) * mm, "end": v(41381.43, 57509.04) * mm});
            skLineSegment(sketch, "E6711", {"start": v(40823.48, 58489.44) * mm, "end": v(41062.76, 58561.87) * mm});
            skLineSegment(sketch, "E6712", {"start": v(41142.15, 57436.61) * mm, "end": v(40823.48, 58489.44) * mm});
            skLineSegment(sketch, "E6713", {"start": v(41381.43, 57509.04) * mm, "end": v(41620.7, 57581.46) * mm});
            skLineSegment(sketch, "E6714", {"start": v(41062.76, 58561.87) * mm, "end": v(41302.04, 58634.3) * mm});
            skLineSegment(sketch, "E6715", {"start": v(41381.43, 57509.04) * mm, "end": v(41062.76, 58561.87) * mm});
            skLineSegment(sketch, "E6716", {"start": v(41620.7, 57581.46) * mm, "end": v(41859.99, 57653.89) * mm});
            skLineSegment(sketch, "E6717", {"start": v(41302.04, 58634.3) * mm, "end": v(41541.32, 58706.72) * mm});
            skLineSegment(sketch, "E6718", {"start": v(41620.7, 57581.46) * mm, "end": v(41302.04, 58634.3) * mm});
            skLineSegment(sketch, "E6719", {"start": v(41859.99, 57653.89) * mm, "end": v(42099.27, 57726.31) * mm});
            skLineSegment(sketch, "E6720", {"start": v(41541.32, 58706.72) * mm, "end": v(41780.6, 58779.14) * mm});
            skLineSegment(sketch, "E6721", {"start": v(41859.99, 57653.89) * mm, "end": v(41541.32, 58706.72) * mm});
            skLineSegment(sketch, "E6722", {"start": v(42099.27, 57726.31) * mm, "end": v(42338.55, 57798.74) * mm});
            skLineSegment(sketch, "E6723", {"start": v(41780.6, 58779.14) * mm, "end": v(42019.88, 58851.57) * mm});
            skLineSegment(sketch, "E6724", {"start": v(42099.27, 57726.31) * mm, "end": v(41780.6, 58779.14) * mm});
            skLineSegment(sketch, "E6725", {"start": v(42338.55, 57798.74) * mm, "end": v(42577.83, 57871.16) * mm});
            skLineSegment(sketch, "E6726", {"start": v(42019.88, 58851.57) * mm, "end": v(42259.16, 58924) * mm});
            skLineSegment(sketch, "E6727", {"start": v(42338.55, 57798.74) * mm, "end": v(42019.88, 58851.57) * mm});
            skLineSegment(sketch, "E6728", {"start": v(42577.83, 57871.16) * mm, "end": v(42817.1, 57943.59) * mm});
            skLineSegment(sketch, "E6729", {"start": v(42259.16, 58924) * mm, "end": v(42498.43, 58996.42) * mm});
            skLineSegment(sketch, "E6730", {"start": v(42577.83, 57871.16) * mm, "end": v(42259.16, 58924) * mm});
            skLineSegment(sketch, "E6731", {"start": v(42817.1, 57943.59) * mm, "end": v(43056.38, 58016.01) * mm});
            skLineSegment(sketch, "E6732", {"start": v(42498.43, 58996.42) * mm, "end": v(42737.71, 59068.84) * mm});
            skLineSegment(sketch, "E6733", {"start": v(42817.1, 57943.59) * mm, "end": v(42498.43, 58996.42) * mm});
            skLineSegment(sketch, "E6734", {"start": v(43056.38, 58016.01) * mm, "end": v(42737.71, 59068.84) * mm});
            skLineSegment(sketch, "E6735", {"start": v(40213.75, 57155.6) * mm, "end": v(40145.53, 57380.96) * mm});
            skLineSegment(sketch, "E6736", {"start": v(40453.02, 57228.03) * mm, "end": v(40259.37, 57867.83) * mm});
            skLineSegment(sketch, "E6737", {"start": v(40692.3, 57300.45) * mm, "end": v(40373.63, 58353.28) * mm});
            skLineSegment(sketch, "E6738", {"start": v(40931.58, 57372.88) * mm, "end": v(40612.91, 58425.7) * mm});
            skLineSegment(sketch, "E6739", {"start": v(41170.86, 57445.3) * mm, "end": v(40852.2, 58498.13) * mm});
            skLineSegment(sketch, "E6740", {"start": v(41410.14, 57517.73) * mm, "end": v(41091.47, 58570.56) * mm});
            skLineSegment(sketch, "E6741", {"start": v(41649.42, 57590.15) * mm, "end": v(41330.75, 58642.98) * mm});
            skLineSegment(sketch, "E6742", {"start": v(41888.7, 57662.58) * mm, "end": v(41570.03, 58715.4) * mm});
            skLineSegment(sketch, "E6743", {"start": v(42127.98, 57735) * mm, "end": v(41809.31, 58787.83) * mm});
            skLineSegment(sketch, "E6744", {"start": v(42367.26, 57807.43) * mm, "end": v(42048.59, 58860.26) * mm});
            skLineSegment(sketch, "E6745", {"start": v(42606.54, 57879.85) * mm, "end": v(42287.87, 58932.68) * mm});
            skLineSegment(sketch, "E6746", {"start": v(42845.82, 57952.28) * mm, "end": v(42527.15, 59005.1) * mm});
            skLineSegment(sketch, "E6747", {"start": v(43085.1, 58024.7) * mm, "end": v(42766.43, 59077.53) * mm});
            skLineSegment(sketch, "E6748", {"start": v(40228.23, 57734.63) * mm, "end": v(42897.05, 58542.43) * mm});
            skLineSegment(sketch, "E6749", {"start": v(42615.96, 58608.15) * mm, "end": v(42897.05, 58542.43) * mm});
            skLineSegment(sketch, "E6750", {"start": v(42897.05, 58542.43) * mm, "end": v(42699.58, 58331.85) * mm});
            skLineSegment(sketch, "E6751", {"start": v(42699.58, 58331.85) * mm, "end": v(42615.96, 58608.15) * mm});
            skLineSegment(sketch, "E6752", {"start": v(40349.16, 58251.84) * mm, "end": v(42763.79, 58982.7) * mm});
            skLineSegment(sketch, "E6753", {"start": v(42763.79, 58982.7) * mm, "end": v(42750.75, 59025.77) * mm});
            skLineSegment(sketch, "E6754", {"start": v(42750.75, 59025.77) * mm, "end": v(40360.99, 58302.44) * mm});
            skLineSegment(sketch, "E6755", {"start": v(40360.99, 58302.44) * mm, "end": v(40349.16, 58251.84) * mm});
            skLineSegment(sketch, "E6756", {"start": v(40107.3, 57217.41) * mm, "end": v(43030.31, 58102.15) * mm});
            skLineSegment(sketch, "E6757", {"start": v(43030.31, 58102.15) * mm, "end": v(43043.35, 58059.08) * mm});
            skLineSegment(sketch, "E6758", {"start": v(43043.35, 58059.08) * mm, "end": v(40095.46, 57166.82) * mm});
            skLineSegment(sketch, "E6759", {"start": v(40095.46, 57166.82) * mm, "end": v(40107.3, 57217.41) * mm});
            skLineSegment(sketch, "E6760", {"start": v(40083.63, 57116.22) * mm, "end": v(40372.82, 58353.03) * mm});
            skLineSegment(sketch, "E6761", {"start": v(60235.96, 50658) * mm, "end": v(60192.14, 50736.6) * mm});
            skEllipse(sketch, "E6762", {"center": v(46453.64, 62403.9) * mm, "majorRadius": 119.06 * mm, "minorRadius": 119.06 * mm, "majorAxis": v(1, 0)});
            skArc(sketch, "E6763", {"start": v(46339.68, 62369.4) * mm, "mid": v(46397.45, 62298.92) * mm, "end": v(46488.13, 62289.94) * mm});
            skArc(sketch, "E6764", {"start": v(46567.6, 62438.38) * mm, "mid": v(46509.83, 62508.86) * mm, "end": v(46419.15, 62517.85) * mm});
            skLineSegment(sketch, "E6765", {"start": v(46488.13, 62289.94) * mm, "end": v(46419.15, 62517.85) * mm});
            skLineSegment(sketch, "E6766", {"start": v(46567.6, 62438.38) * mm, "end": v(46339.68, 62369.4) * mm});
            skLineSegment(sketch, "E6767", {"start": v(46419.15, 62517.85) * mm, "end": v(46169.46, 63342.76) * mm});
            skLineSegment(sketch, "E6768", {"start": v(43785.9, 47980.97) * mm, "end": v(41725.14, 54896.4) * mm});
            skLineSegment(sketch, "E6769", {"start": v(41725.14, 54896.4) * mm, "end": v(48582.16, 57001.67) * mm});
            skLineSegment(sketch, "E6770", {"start": v(48582.16, 57001.67) * mm, "end": v(50679.83, 50071.15) * mm});
            skLineSegment(sketch, "E6771", {"start": v(50679.83, 50071.15) * mm, "end": v(47628.14, 49145.9) * mm});
            skLineSegment(sketch, "E6772", {"start": v(47628.14, 49145.9) * mm, "end": v(47641.24, 49102.68) * mm});
            skLineSegment(sketch, "E6773", {"start": v(47641.24, 49102.68) * mm, "end": v(46838.37, 48859.26) * mm});
            skLineSegment(sketch, "E6774", {"start": v(46838.37, 48859.26) * mm, "end": v(46825.27, 48902.48) * mm});
            skLineSegment(sketch, "E6775", {"start": v(46825.27, 48902.48) * mm, "end": v(43785.9, 47980.97) * mm});
            skCircle(sketch, "E6776", {"center": v(0, 0) * mm, "radius": 1927.6 * mm});
            skLineSegment(sketch, "E6777", {"start": v(0, 5000) * mm, "end": v(0, -5000) * mm});
            skLineSegment(sketch, "E6778", {"start": v(5000, 0) * mm, "end": v(-5000, 0) * mm});
            skLineSegment(sketch, "E6779", {"start": v(51002.14, 60985.18) * mm, "end": v(51074.56, 60745.9) * mm});
            skLineSegment(sketch, "E6780", {"start": v(52054.97, 61303.85) * mm, "end": v(52127.4, 61064.58) * mm});
            skLineSegment(sketch, "E6781", {"start": v(51002.14, 60985.18) * mm, "end": v(52054.97, 61303.85) * mm});
            skLineSegment(sketch, "E6782", {"start": v(51074.56, 60745.9) * mm, "end": v(51146.99, 60506.63) * mm});
            skLineSegment(sketch, "E6783", {"start": v(52127.4, 61064.58) * mm, "end": v(52199.82, 60825.3) * mm});
            skLineSegment(sketch, "E6784", {"start": v(51074.56, 60745.9) * mm, "end": v(52127.4, 61064.58) * mm});
            skLineSegment(sketch, "E6785", {"start": v(51146.99, 60506.63) * mm, "end": v(51219.41, 60267.35) * mm});
            skLineSegment(sketch, "E6786", {"start": v(52199.82, 60825.3) * mm, "end": v(52272.24, 60586.02) * mm});
            skLineSegment(sketch, "E6787", {"start": v(51146.99, 60506.63) * mm, "end": v(52199.82, 60825.3) * mm});
            skLineSegment(sketch, "E6788", {"start": v(51219.41, 60267.35) * mm, "end": v(51283.4, 60055.96) * mm});
            skLineSegment(sketch, "E6789", {"start": v(51340.16, 60042.7) * mm, "end": v(52344.67, 60346.74) * mm});
            skLineSegment(sketch, "E6790", {"start": v(52344.67, 60346.74) * mm, "end": v(52272.24, 60586.02) * mm});
            skLineSegment(sketch, "E6791", {"start": v(52272.24, 60586.02) * mm, "end": v(51219.41, 60267.35) * mm});
            skLineSegment(sketch, "E6792", {"start": v(51827.02, 59928.86) * mm, "end": v(52417.1, 60107.46) * mm});
            skLineSegment(sketch, "E6793", {"start": v(52417.1, 60107.46) * mm, "end": v(52344.67, 60346.74) * mm});
            skLineSegment(sketch, "E6794", {"start": v(52313.9, 59815.02) * mm, "end": v(52489.52, 59868.18) * mm});
            skLineSegment(sketch, "E6795", {"start": v(52489.52, 59868.18) * mm, "end": v(52417.1, 60107.46) * mm});
            skLineSegment(sketch, "E6796", {"start": v(52520.2, 59766.78) * mm, "end": v(52489.52, 59868.18) * mm});
            skLineSegment(sketch, "E6797", {"start": v(51010.83, 60956.47) * mm, "end": v(52063.66, 61275.14) * mm});
            skLineSegment(sketch, "E6798", {"start": v(51083.26, 60717.2) * mm, "end": v(52136.08, 61035.86) * mm});
            skLineSegment(sketch, "E6799", {"start": v(51155.68, 60477.91) * mm, "end": v(52208.5, 60796.58) * mm});
            skLineSegment(sketch, "E6800", {"start": v(51228.1, 60238.63) * mm, "end": v(52280.93, 60557.3) * mm});
            skLineSegment(sketch, "E6801", {"start": v(51398.58, 60029.03) * mm, "end": v(52353.36, 60318.02) * mm});
            skLineSegment(sketch, "E6802", {"start": v(51885.45, 59915.2) * mm, "end": v(52425.78, 60078.74) * mm});
            skLineSegment(sketch, "E6803", {"start": v(52372.32, 59801.36) * mm, "end": v(52498.2, 59839.46) * mm});
            skLineSegment(sketch, "E6804", {"start": v(51528.55, 61144.52) * mm, "end": v(51901.8, 59911.37) * mm});
            skLineSegment(sketch, "E6805", {"start": v(51959.26, 61274.88) * mm, "end": v(52407.77, 59793.07) * mm});
            skLineSegment(sketch, "E6806", {"start": v(52407.77, 59793.07) * mm, "end": v(52464, 59779.93) * mm});
            skLineSegment(sketch, "E6807", {"start": v(52464, 59779.93) * mm, "end": v(52007.11, 61289.37) * mm});
            skLineSegment(sketch, "E6808", {"start": v(52007.11, 61289.37) * mm, "end": v(51959.26, 61274.88) * mm});
            skLineSegment(sketch, "E6809", {"start": v(51097.85, 61014.15) * mm, "end": v(51395.83, 60029.67) * mm});
            skLineSegment(sketch, "E6810", {"start": v(51395.83, 60029.67) * mm, "end": v(51339.62, 60042.82) * mm});
            skLineSegment(sketch, "E6811", {"start": v(51339.62, 60042.82) * mm, "end": v(51050, 60999.67) * mm});
            skLineSegment(sketch, "E6812", {"start": v(51050, 60999.67) * mm, "end": v(51097.85, 61014.15) * mm});
            skLineSegment(sketch, "E6813", {"start": v(51283.4, 60055.96) * mm, "end": v(52520.2, 59766.78) * mm});
            skLineSegment(sketch, "E6814", {"start": v(43985.95, 48355.1) * mm, "end": v(50305.83, 50271.24) * mm});
            skLineSegment(sketch, "E6815", {"start": v(43784.47, 47980.54) * mm, "end": v(50679.83, 50071.15) * mm});
            skLineSegment(sketch, "E6816", {"start": v(42097.56, 54696.9) * mm, "end": v(43985.95, 48355.1) * mm});
            skLineSegment(sketch, "E6817", {"start": v(41725.14, 54896.4) * mm, "end": v(43784.47, 47980.54) * mm});
            skLineSegment(sketch, "E6818", {"start": v(48382.3, 56626.46) * mm, "end": v(42097.56, 54696.9) * mm});
            skLineSegment(sketch, "E6819", {"start": v(48582.17, 57001.65) * mm, "end": v(41725.14, 54896.4) * mm});
            skLineSegment(sketch, "E6820", {"start": v(50305.83, 50271.24) * mm, "end": v(48382.3, 56626.46) * mm});
            skLineSegment(sketch, "E6821", {"start": v(50679.83, 50071.15) * mm, "end": v(48582.17, 57001.65) * mm});
            skLineSegment(sketch, "E6822", {"start": v(57540.02, 51837.9) * mm, "end": v(57275.63, 55356.23) * mm});
            skLineSegment(sketch, "E6823", {"start": v(58823.27, 52580.61) * mm, "end": v(56540.9, 55133.84) * mm});
            skLineSegment(sketch, "E6824", {"start": v(47974.9, 63323.96) * mm, "end": v(47113.47, 63063.28) * mm});
            skLineSegment(sketch, "E6825", {"start": v(47113.47, 63063.28) * mm, "end": v(46707.98, 64403.28) * mm});
            skLineSegment(sketch, "E6826", {"start": v(46707.98, 64403.28) * mm, "end": v(47569.4, 64663.95) * mm});
            skLineSegment(sketch, "E6827", {"start": v(47569.4, 64663.95) * mm, "end": v(47974.9, 63323.96) * mm});
            skLineSegment(sketch, "E6828", {"start": v(55404.2, 55615.96) * mm, "end": v(55183.76, 56336.64) * mm});
            skArc(sketch, "E6829", {"start": v(55183.76, 56336.64) * mm, "mid": v(55151.27, 56418.05) * mm, "end": v(55105.81, 56493) * mm});
            skLineSegment(sketch, "E6830", {"start": v(55105.81, 56493) * mm, "end": v(54918.55, 56708.12) * mm});
            skArc(sketch, "E6831", {"start": v(54918.55, 56708.12) * mm, "mid": v(54880.33, 56741.05) * mm, "end": v(54834.36, 56761.83) * mm});
            skArc(sketch, "E6832", {"start": v(54834.36, 56761.83) * mm, "mid": v(54603.02, 56798.17) * mm, "end": v(54369.9, 56775.98) * mm});
            skArc(sketch, "E6833", {"start": v(54369.9, 56775.98) * mm, "mid": v(54242.18, 56742.23) * mm, "end": v(54114.1, 56709.85) * mm});
            skLineSegment(sketch, "E6834", {"start": v(55404.2, 55615.96) * mm, "end": v(55410.16, 55596.48) * mm});
            skLineSegment(sketch, "E6835", {"start": v(55450.83, 55463.5) * mm, "end": v(55663.66, 54767.71) * mm});
            skArc(sketch, "E6836", {"start": v(55663.66, 54767.71) * mm, "mid": v(55872.02, 54064.85) * mm, "end": v(56068.16, 53358.48) * mm});
            skArc(sketch, "E6837", {"start": v(56068.16, 53358.48) * mm, "mid": v(56071.33, 53337.15) * mm, "end": v(56069.56, 53315.65) * mm});
            skArc(sketch, "E6838", {"start": v(56069.56, 53315.65) * mm, "mid": v(56045.83, 53208.3) * mm, "end": v(56017.66, 53102.03) * mm});
            skArc(sketch, "E6839", {"start": v(56017.66, 53102.03) * mm, "mid": v(55992.59, 53043) * mm, "end": v(55954, 52991.78) * mm});
            skArc(sketch, "E6840", {"start": v(55954, 52991.78) * mm, "mid": v(55821.28, 52882.97) * mm, "end": v(55666.98, 52807.8) * mm});
            skLineSegment(sketch, "E6841", {"start": v(55666.98, 52807.8) * mm, "end": v(55342.62, 52693.54) * mm});
            skLineSegment(sketch, "E6842", {"start": v(55315.55, 55496.15) * mm, "end": v(55424.5, 55468.5) * mm});
            skArc(sketch, "E6843", {"start": v(55424.5, 55468.5) * mm, "mid": v(55486.97, 55461.9) * mm, "end": v(55548.76, 55473.2) * mm});
            skArc(sketch, "E6844", {"start": v(55548.76, 55473.2) * mm, "mid": v(55564.17, 55488.67) * mm, "end": v(55561.05, 55510.28) * mm});
            skArc(sketch, "E6845", {"start": v(55561.05, 55510.28) * mm, "mid": v(55528.25, 55546.33) * mm, "end": v(55487.2, 55572.6) * mm});
            skLineSegment(sketch, "E6846", {"start": v(55487.2, 55572.6) * mm, "end": v(55338.84, 55618.58) * mm});
            skArc(sketch, "E6847", {"start": v(55338.84, 55618.58) * mm, "mid": v(55300.52, 55562.44) * mm, "end": v(55315.55, 55496.15) * mm});
            skLineSegment(sketch, "E6848", {"start": v(54694.21, 56616.1) * mm, "end": v(54837, 56552.94) * mm});
            skArc(sketch, "E6849", {"start": v(54837, 56552.94) * mm, "mid": v(54899.66, 56529.74) * mm, "end": v(54964.7, 56514.42) * mm});
            skArc(sketch, "E6850", {"start": v(54964.7, 56514.42) * mm, "mid": v(54996.48, 56527.18) * mm, "end": v(54999.45, 56561.3) * mm});
            skArc(sketch, "E6851", {"start": v(54999.45, 56561.3) * mm, "mid": v(54948.88, 56631.07) * mm, "end": v(54878.67, 56681.04) * mm});
            skArc(sketch, "E6852", {"start": v(54878.67, 56681.04) * mm, "mid": v(54771.55, 56716.99) * mm, "end": v(54658.75, 56723.69) * mm});
            skArc(sketch, "E6853", {"start": v(54658.75, 56723.69) * mm, "mid": v(54617.3, 56715.93) * mm, "end": v(54578.6, 56699.17) * mm});
            skLineSegment(sketch, "E6854", {"start": v(54578.6, 56699.17) * mm, "end": v(54587.1, 56671.37) * mm});
            skLineSegment(sketch, "E6855", {"start": v(54587.1, 56671.37) * mm, "end": v(54694.21, 56616.1) * mm});
            skLineSegment(sketch, "E6856", {"start": v(54612.17, 56619.78) * mm, "end": v(55038.55, 55832.05) * mm});
            skLineSegment(sketch, "E6857", {"start": v(54927.48, 56500.63) * mm, "end": v(54970.33, 56401.97) * mm});
            skLineSegment(sketch, "E6858", {"start": v(54970.33, 56401.97) * mm, "end": v(55164.9, 55818.57) * mm});
            skArc(sketch, "E6859", {"start": v(54912.13, 55850.45) * mm, "mid": v(54654.27, 55827.43) * mm, "end": v(54402.66, 55766.5) * mm});
            skArc(sketch, "E6860", {"start": v(54912.62, 55817.17) * mm, "mid": v(54659.68, 55794.59) * mm, "end": v(54412.87, 55734.81) * mm});
            skArc(sketch, "E6861", {"start": v(55175, 55779.14) * mm, "mid": v(55047.43, 55829.07) * mm, "end": v(54912.13, 55850.45) * mm});
            skArc(sketch, "E6862", {"start": v(55202.44, 55724.97) * mm, "mid": v(55062.45, 55789.98) * mm, "end": v(54910.51, 55817.2) * mm});
            skArc(sketch, "E6863", {"start": v(54956.56, 55705.21) * mm, "mid": v(54699.95, 55675.98) * mm, "end": v(54448.94, 55615.18) * mm});
            skArc(sketch, "E6864", {"start": v(55148.45, 55677.45) * mm, "mid": v(55054.1, 55702.39) * mm, "end": v(54956.56, 55705.21) * mm});
            skLineSegment(sketch, "E6865", {"start": v(55148.45, 55677.45) * mm, "end": v(55167.03, 55653.3) * mm});
            skLineSegment(sketch, "E6866", {"start": v(55167.03, 55653.3) * mm, "end": v(55177.3, 55619.7) * mm});
            skLineSegment(sketch, "E6867", {"start": v(55177.3, 55619.7) * mm, "end": v(55218.2, 55079.27) * mm});
            skLineSegment(sketch, "E6868", {"start": v(55218.2, 55079.27) * mm, "end": v(55182.46, 55081.41) * mm});
            skArc(sketch, "E6869", {"start": v(55182.46, 55081.41) * mm, "mid": v(54909.8, 55046.13) * mm, "end": v(54641.9, 54984.35) * mm});
            skLineSegment(sketch, "E6870", {"start": v(55110.48, 53224.42) * mm, "end": v(55670.5, 53395.72) * mm});
            skArc(sketch, "E6871", {"start": v(55670.5, 53395.72) * mm, "mid": v(55697.87, 53397.97) * mm, "end": v(55723.69, 53388.61) * mm});
            skLineSegment(sketch, "E6872", {"start": v(55723.69, 53388.61) * mm, "end": v(55910.36, 53226.81) * mm});
            skLineSegment(sketch, "E6873", {"start": v(55910.36, 53226.81) * mm, "end": v(55975.95, 53246.87) * mm});
            skLineSegment(sketch, "E6874", {"start": v(55975.95, 53246.87) * mm, "end": v(56005, 53326.48) * mm});
            skLineSegment(sketch, "E6875", {"start": v(56005, 53326.48) * mm, "end": v(56008.39, 53368.87) * mm});
            skLineSegment(sketch, "E6876", {"start": v(56008.39, 53368.87) * mm, "end": v(56030.37, 53415.23) * mm});
            skLineSegment(sketch, "E6877", {"start": v(56030.37, 53415.23) * mm, "end": v(56048.36, 53432) * mm});
            skArc(sketch, "E6878", {"start": v(55988.08, 53167.3) * mm, "mid": v(56011, 53245.35) * mm, "end": v(56005, 53326.48) * mm});
            skArc(sketch, "E6879", {"start": v(55834.17, 53001.84) * mm, "mid": v(55921.55, 53074.87) * mm, "end": v(55988.08, 53167.3) * mm});
            skArc(sketch, "E6880", {"start": v(55455.2, 53183.04) * mm, "mid": v(55608.8, 53260.91) * mm, "end": v(55730.78, 53382.47) * mm});
            skLineSegment(sketch, "E6881", {"start": v(55455.2, 53183.04) * mm, "end": v(55215.33, 53109.67) * mm});
            skArc(sketch, "E6882", {"start": v(55730.99, 53277.3) * mm, "mid": v(55694.72, 53294.6) * mm, "end": v(55654.67, 53298.01) * mm});
            skLineSegment(sketch, "E6883", {"start": v(55730.99, 53277.3) * mm, "end": v(55813.28, 53197.22) * mm});
            skArc(sketch, "E6884", {"start": v(55813.28, 53197.22) * mm, "mid": v(55830.06, 53169.73) * mm, "end": v(55831.54, 53137.55) * mm});
            skArc(sketch, "E6885", {"start": v(55831.54, 53137.55) * mm, "mid": v(55825.37, 53121.97) * mm, "end": v(55814.34, 53109.35) * mm});
            skArc(sketch, "E6886", {"start": v(55814.34, 53109.35) * mm, "mid": v(55700.54, 53027.83) * mm, "end": v(55577.9, 52960.32) * mm});
            skArc(sketch, "E6887", {"start": v(55577.9, 52960.32) * mm, "mid": v(55438, 52900.84) * mm, "end": v(55294.86, 52849.66) * mm});
            skLineSegment(sketch, "E6888", {"start": v(55834.17, 53001.84) * mm, "end": v(55604.98, 52874.48) * mm});
            skLineSegment(sketch, "E6889", {"start": v(55604.98, 52874.48) * mm, "end": v(55318.71, 52771.7) * mm});
            skLineSegment(sketch, "E6890", {"start": v(55642.48, 53387.15) * mm, "end": v(55465.43, 54106.1) * mm});
            skLineSegment(sketch, "E6891", {"start": v(55465.43, 54106.1) * mm, "end": v(55262.85, 55006.9) * mm});
            skLineSegment(sketch, "E6892", {"start": v(55262.85, 55006.9) * mm, "end": v(55248.46, 55083.42) * mm});
            skLineSegment(sketch, "E6893", {"start": v(55248.46, 55083.42) * mm, "end": v(55207.13, 55694.76) * mm});
            skArc(sketch, "E6894", {"start": v(55207.13, 55694.76) * mm, "mid": v(55198.02, 55739) * mm, "end": v(55176.15, 55778.54) * mm});
            skArc(sketch, "E6895", {"start": v(55368.6, 55732.35) * mm, "mid": v(55286.62, 55624.56) * mm, "end": v(55268.14, 55490.4) * mm});
            skLineSegment(sketch, "E6896", {"start": v(55268.14, 55490.4) * mm, "end": v(55307.89, 55078.28) * mm});
            skArc(sketch, "E6897", {"start": v(55307.89, 55078.28) * mm, "mid": v(55321.65, 54962.02) * mm, "end": v(55340.42, 54846.46) * mm});
            skLineSegment(sketch, "E6898", {"start": v(55340.42, 54846.46) * mm, "end": v(55412.43, 54555.52) * mm});
            skLineSegment(sketch, "E6899", {"start": v(55412.43, 54555.52) * mm, "end": v(55594.81, 53912.15) * mm});
            skLineSegment(sketch, "E6900", {"start": v(55594.81, 53912.15) * mm, "end": v(55650.5, 53730.1) * mm});
            skArc(sketch, "E6901", {"start": v(55650.5, 53730.1) * mm, "mid": v(55670.9, 53693.51) * mm, "end": v(55704.51, 53668.53) * mm});
            skLineSegment(sketch, "E6902", {"start": v(55704.51, 53668.53) * mm, "end": v(55787.56, 53637.84) * mm});
            skArc(sketch, "E6903", {"start": v(55787.56, 53637.84) * mm, "mid": v(55821.39, 53636.87) * mm, "end": v(55848.88, 53656.6) * mm});
            skLineSegment(sketch, "E6904", {"start": v(55848.88, 53656.6) * mm, "end": v(55916.89, 53797.28) * mm});
            skLineSegment(sketch, "E6905", {"start": v(55916.89, 53797.28) * mm, "end": v(55927.6, 53869.43) * mm});
            skLineSegment(sketch, "E6906", {"start": v(55358.3, 55485.3) * mm, "end": v(55549.29, 54860.93) * mm});
            skArc(sketch, "E6907", {"start": v(55549.29, 54860.93) * mm, "mid": v(55698.16, 54304.48) * mm, "end": v(55807.25, 53738.88) * mm});
            skArc(sketch, "E6908", {"start": v(55807.25, 53738.88) * mm, "mid": v(55803.46, 53710.97) * mm, "end": v(55784.99, 53689.7) * mm});
            skLineSegment(sketch, "E6909", {"start": v(55784.99, 53689.7) * mm, "end": v(55769.86, 53685.07) * mm});
            skLineSegment(sketch, "E6910", {"start": v(55769.86, 53685.07) * mm, "end": v(55759.45, 53688.82) * mm});
            skArc(sketch, "E6911", {"start": v(55759.45, 53688.82) * mm, "mid": v(55728.03, 53697.04) * mm, "end": v(55698.35, 53710.21) * mm});
            skArc(sketch, "E6912", {"start": v(55698.35, 53710.21) * mm, "mid": v(55674.62, 53726.07) * mm, "end": v(55657.52, 53748.92) * mm});
            skLineSegment(sketch, "E6913", {"start": v(55657.52, 53748.92) * mm, "end": v(55421.92, 54565.68) * mm});
            skArc(sketch, "E6914", {"start": v(55292.28, 55468.94) * mm, "mid": v(55328.58, 55013.22) * mm, "end": v(55421.92, 54565.68) * mm});
            skArc(sketch, "E6915", {"start": v(55315.55, 55496.15) * mm, "mid": v(55300.75, 55485.26) * mm, "end": v(55292.28, 55468.94) * mm});
            skLineSegment(sketch, "E6916", {"start": v(55589.58, 54725) * mm, "end": v(55422.16, 54564.83) * mm});
            skLineSegment(sketch, "E6917", {"start": v(55639.1, 54544.58) * mm, "end": v(55458.87, 54437.56) * mm});
            skLineSegment(sketch, "E6918", {"start": v(55429.67, 54494.7) * mm, "end": v(55683.9, 54701.36) * mm});
            skArc(sketch, "E6919", {"start": v(54498.98, 56707.37) * mm, "mid": v(54425.5, 56728.2) * mm, "end": v(54349.23, 56724.04) * mm});
            skLineSegment(sketch, "E6920", {"start": v(54349.23, 56724.04) * mm, "end": v(54126.7, 56668.69) * mm});
            skArc(sketch, "E6921", {"start": v(54587.1, 56671.37) * mm, "mid": v(54367.63, 56637.98) * mm, "end": v(54151.23, 56588.48) * mm});
            skLineSegment(sketch, "E6922", {"start": v(53656.71, 55081.43) * mm, "end": v(53436.27, 55802.11) * mm});
            skArc(sketch, "E6923", {"start": v(53436.27, 55802.11) * mm, "mid": v(53417.65, 55887.77) * mm, "end": v(53413.4, 55975.32) * mm});
            skLineSegment(sketch, "E6924", {"start": v(53413.4, 55975.32) * mm, "end": v(53448.28, 56258.39) * mm});
            skArc(sketch, "E6925", {"start": v(53448.28, 56258.39) * mm, "mid": v(53461.54, 56307.07) * mm, "end": v(53488.02, 56350) * mm});
            skArc(sketch, "E6926", {"start": v(53488.02, 56350) * mm, "mid": v(53659.44, 56509.54) * mm, "end": v(53865.08, 56621.56) * mm});
            skArc(sketch, "E6927", {"start": v(53865.08, 56621.56) * mm, "mid": v(53989.83, 56665.04) * mm, "end": v(54114.1, 56709.85) * mm});
            skLineSegment(sketch, "E6928", {"start": v(53656.71, 55081.43) * mm, "end": v(53662.67, 55061.95) * mm});
            skLineSegment(sketch, "E6929", {"start": v(53703.34, 54928.98) * mm, "end": v(53916.17, 54233.19) * mm});
            skArc(sketch, "E6930", {"start": v(53916.17, 54233.19) * mm, "mid": v(54136.67, 53534.04) * mm, "end": v(54369.24, 52838.81) * mm});
            skArc(sketch, "E6931", {"start": v(54369.24, 52838.81) * mm, "mid": v(54378.55, 52819.36) * mm, "end": v(54392.04, 52802.53) * mm});
            skArc(sketch, "E6932", {"start": v(54392.04, 52802.53) * mm, "mid": v(54471.77, 52726.83) * mm, "end": v(54554.57, 52654.5) * mm});
            skArc(sketch, "E6933", {"start": v(54554.57, 52654.5) * mm, "mid": v(54608.37, 52619.6) * mm, "end": v(54669, 52598.72) * mm});
            skArc(sketch, "E6934", {"start": v(54669, 52598.72) * mm, "mid": v(54839.9, 52582.78) * mm, "end": v(55009.84, 52606.79) * mm});
            skLineSegment(sketch, "E6935", {"start": v(55009.84, 52606.79) * mm, "end": v(55342.62, 52693.54) * mm});
            skLineSegment(sketch, "E6936", {"start": v(53797.21, 55031.72) * mm, "end": v(53722.37, 54947.86) * mm});
            skArc(sketch, "E6937", {"start": v(53722.37, 54947.86) * mm, "mid": v(53674.3, 54907.44) * mm, "end": v(53616.75, 54882.23) * mm});
            skArc(sketch, "E6938", {"start": v(53616.75, 54882.23) * mm, "mid": v(53595.32, 54886.43) * mm, "end": v(53585.82, 54906.09) * mm});
            skArc(sketch, "E6939", {"start": v(53585.82, 54906.09) * mm, "mid": v(53592.84, 54954.32) * mm, "end": v(53612.17, 54999.06) * mm});
            skLineSegment(sketch, "E6940", {"start": v(53612.17, 54999.06) * mm, "end": v(53709.42, 55120.17) * mm});
            skArc(sketch, "E6941", {"start": v(53709.42, 55120.17) * mm, "mid": v(53772.59, 55095.08) * mm, "end": v(53797.21, 55031.72) * mm});
            skLineSegment(sketch, "E6942", {"start": v(53685.7, 56307.62) * mm, "end": v(53602.68, 56175.39) * mm});
            skArc(sketch, "E6943", {"start": v(53602.68, 56175.39) * mm, "mid": v(53563.73, 56121.1) * mm, "end": v(53518.39, 56072.02) * mm});
            skArc(sketch, "E6944", {"start": v(53518.39, 56072.02) * mm, "mid": v(53484.9, 56064.81) * mm, "end": v(53463.36, 56091.44) * mm});
            skArc(sketch, "E6945", {"start": v(53463.36, 56091.44) * mm, "mid": v(53466.24, 56177.56) * mm, "end": v(53496.48, 56258.26) * mm});
            skArc(sketch, "E6946", {"start": v(53496.48, 56258.26) * mm, "mid": v(53565.17, 56347.98) * mm, "end": v(53654.91, 56416.63) * mm});
            skArc(sketch, "E6947", {"start": v(53654.91, 56416.63) * mm, "mid": v(53693.61, 56433.4) * mm, "end": v(53735.07, 56441.15) * mm});
            skLineSegment(sketch, "E6948", {"start": v(53735.07, 56441.15) * mm, "end": v(53743.58, 56413.35) * mm});
            skLineSegment(sketch, "E6949", {"start": v(53743.58, 56413.35) * mm, "end": v(53685.7, 56307.62) * mm});
            skLineSegment(sketch, "E6950", {"start": v(53751.65, 56356.56) * mm, "end": v(53838.9, 55465.1) * mm});
            skLineSegment(sketch, "E6951", {"start": v(53556.95, 56081.4) * mm, "end": v(53576.63, 55975.66) * mm});
            skLineSegment(sketch, "E6952", {"start": v(53576.63, 55975.66) * mm, "end": v(53741.71, 55383.24) * mm});
            skArc(sketch, "E6953", {"start": v(54402.66, 55766.5) * mm, "mid": v(54160.01, 55676.24) * mm, "end": v(53933.4, 55551.07) * mm});
            skArc(sketch, "E6954", {"start": v(54411.92, 55734.52) * mm, "mid": v(54173.9, 55646) * mm, "end": v(53951.6, 55523.21) * mm});
            skArc(sketch, "E6955", {"start": v(53933.4, 55551.07) * mm, "mid": v(53833.21, 55457.66) * mm, "end": v(53755.4, 55344.92) * mm});
            skArc(sketch, "E6956", {"start": v(53953.34, 55524.42) * mm, "mid": v(53842.63, 55416.86) * mm, "end": v(53762.96, 55284.66) * mm});
            skArc(sketch, "E6957", {"start": v(54448.94, 55615.18) * mm, "mid": v(54206.87, 55525.16) * mm, "end": v(53977.82, 55405.83) * mm});
            skArc(sketch, "E6958", {"start": v(53977.82, 55405.83) * mm, "mid": v(53898.55, 55348.92) * mm, "end": v(53834.3, 55275.47) * mm});
            skLineSegment(sketch, "E6959", {"start": v(53834.3, 55275.47) * mm, "end": v(53832.41, 55245.06) * mm});
            skLineSegment(sketch, "E6960", {"start": v(53832.41, 55245.06) * mm, "end": v(53842.69, 55211.47) * mm});
            skLineSegment(sketch, "E6961", {"start": v(53842.69, 55211.47) * mm, "end": v(54111.11, 54740.63) * mm});
            skLineSegment(sketch, "E6962", {"start": v(54111.11, 54740.63) * mm, "end": v(54139.55, 54762.4) * mm});
            skArc(sketch, "E6963", {"start": v(54641.9, 54984.35) * mm, "mid": v(54385.28, 54885.7) * mm, "end": v(54139.55, 54762.4) * mm});
            skLineSegment(sketch, "E6964", {"start": v(55238.05, 53263.44) * mm, "end": v(54678.02, 53092.14) * mm});
            skArc(sketch, "E6965", {"start": v(54678.02, 53092.14) * mm, "mid": v(54654.08, 53078.7) * mm, "end": v(54637.92, 53056.5) * mm});
            skLineSegment(sketch, "E6966", {"start": v(54637.92, 53056.5) * mm, "end": v(54573.7, 52817.95) * mm});
            skLineSegment(sketch, "E6967", {"start": v(54573.7, 52817.95) * mm, "end": v(54508.11, 52797.89) * mm});
            skLineSegment(sketch, "E6968", {"start": v(54508.11, 52797.89) * mm, "end": v(54439.5, 52847.63) * mm});
            skLineSegment(sketch, "E6969", {"start": v(54439.5, 52847.63) * mm, "end": v(54412.98, 52880.86) * mm});
            skLineSegment(sketch, "E6970", {"start": v(54412.98, 52880.86) * mm, "end": v(54368.82, 52906.99) * mm});
            skLineSegment(sketch, "E6971", {"start": v(54368.82, 52906.99) * mm, "end": v(54344.53, 52910.82) * mm});
            skArc(sketch, "E6972", {"start": v(54439.5, 52847.63) * mm, "mid": v(54479.9, 52777.01) * mm, "end": v(54542.58, 52725.14) * mm});
            skArc(sketch, "E6973", {"start": v(54542.58, 52725.14) * mm, "mid": v(54649.43, 52685.75) * mm, "end": v(54762.71, 52674.1) * mm});
            skArc(sketch, "E6974", {"start": v(54635.48, 53047.44) * mm, "mid": v(54804.58, 53014.92) * mm, "end": v(54975.46, 53036.3) * mm});
            skLineSegment(sketch, "E6975", {"start": v(54975.46, 53036.3) * mm, "end": v(55215.33, 53109.67) * mm});
            skArc(sketch, "E6976", {"start": v(54745.8, 53020.01) * mm, "mid": v(54714.52, 52994.78) * mm, "end": v(54694.14, 52960.14) * mm});
            skLineSegment(sketch, "E6977", {"start": v(54694.14, 52960.14) * mm, "end": v(54670.72, 52847.73) * mm});
            skArc(sketch, "E6978", {"start": v(54670.72, 52847.73) * mm, "mid": v(54672.2, 52815.56) * mm, "end": v(54688.97, 52788.06) * mm});
            skArc(sketch, "E6979", {"start": v(54688.97, 52788.06) * mm, "mid": v(54702.8, 52778.6) * mm, "end": v(54719, 52774.31) * mm});
            skArc(sketch, "E6980", {"start": v(54719, 52774.31) * mm, "mid": v(54858.93, 52770.4) * mm, "end": v(54998.35, 52783.05) * mm});
            skArc(sketch, "E6981", {"start": v(54998.35, 52783.05) * mm, "mid": v(55147.58, 52812) * mm, "end": v(55294.86, 52849.66) * mm});
            skLineSegment(sketch, "E6982", {"start": v(54762.71, 52674.1) * mm, "end": v(55023.93, 52696.74) * mm});
            skLineSegment(sketch, "E6983", {"start": v(55023.93, 52696.74) * mm, "end": v(55318.71, 52771.7) * mm});
            skLineSegment(sketch, "E6984", {"start": v(54706.04, 53100.7) * mm, "end": v(54450.6, 53795.7) * mm});
            skLineSegment(sketch, "E6985", {"start": v(54450.6, 53795.7) * mm, "end": v(54114.59, 54655.67) * mm});
            skLineSegment(sketch, "E6986", {"start": v(54114.59, 54655.67) * mm, "end": v(54083.72, 54727.15) * mm});
            skLineSegment(sketch, "E6987", {"start": v(54083.72, 54727.15) * mm, "end": v(53775.97, 55257) * mm});
            skArc(sketch, "E6988", {"start": v(53775.97, 55257) * mm, "mid": v(53758.77, 55298.77) * mm, "end": v(53754.79, 55343.77) * mm});
            skArc(sketch, "E6989", {"start": v(53839.73, 55053.48) * mm, "mid": v(53749.36, 55154.34) * mm, "end": v(53621.1, 55197.82) * mm});
            skLineSegment(sketch, "E6990", {"start": v(53839.73, 55053.48) * mm, "end": v(54037.33, 54689.64) * mm});
            skArc(sketch, "E6991", {"start": v(54037.33, 54689.64) * mm, "mid": v(54090.97, 54585.58) * mm, "end": v(54140.05, 54479.29) * mm});
            skLineSegment(sketch, "E6992", {"start": v(54140.05, 54479.29) * mm, "end": v(54243.12, 54197.85) * mm});
            skLineSegment(sketch, "E6993", {"start": v(54243.12, 54197.85) * mm, "end": v(54451.86, 53562.54) * mm});
            skLineSegment(sketch, "E6994", {"start": v(54451.86, 53562.54) * mm, "end": v(54507.55, 53380.5) * mm});
            skArc(sketch, "E6995", {"start": v(54507.55, 53380.5) * mm, "mid": v(54511.11, 53338.76) * mm, "end": v(54497.22, 53299.24) * mm});
            skLineSegment(sketch, "E6996", {"start": v(54497.22, 53299.24) * mm, "end": v(54445.55, 53227.34) * mm});
            skArc(sketch, "E6997", {"start": v(54445.55, 53227.34) * mm, "mid": v(54418.06, 53207.62) * mm, "end": v(54384.23, 53208.59) * mm});
            skLineSegment(sketch, "E6998", {"start": v(54384.23, 53208.59) * mm, "end": v(54249.16, 53287.16) * mm});
            skLineSegment(sketch, "E6999", {"start": v(54249.16, 53287.16) * mm, "end": v(54199.92, 53340.96) * mm});
            skLineSegment(sketch, "E7000", {"start": v(53767.84, 54998.81) * mm, "end": v(53958.83, 54374.43) * mm});
            skArc(sketch, "E7001", {"start": v(53958.83, 54374.43) * mm, "mid": v(54146.73, 53829.92) * mm, "end": v(54372.7, 53300.08) * mm});
            skArc(sketch, "E7002", {"start": v(54372.7, 53300.08) * mm, "mid": v(54391.46, 53279.06) * mm, "end": v(54418.67, 53271.77) * mm});
            skLineSegment(sketch, "E7003", {"start": v(54418.67, 53271.77) * mm, "end": v(54433.8, 53276.4) * mm});
            skLineSegment(sketch, "E7004", {"start": v(54433.8, 53276.4) * mm, "end": v(54440.33, 53285.33) * mm});
            skArc(sketch, "E7005", {"start": v(54440.33, 53285.33) * mm, "mid": v(54461.78, 53309.71) * mm, "end": v(54479.01, 53337.24) * mm});
            skArc(sketch, "E7006", {"start": v(54479.01, 53337.24) * mm, "mid": v(54489.8, 53363.66) * mm, "end": v(54491.2, 53392.16) * mm});
            skLineSegment(sketch, "E7007", {"start": v(54491.2, 53392.16) * mm, "end": v(54229.57, 54200.97) * mm});
            skArc(sketch, "E7008", {"start": v(54229.57, 54200.97) * mm, "mid": v(54056.57, 54624.13) * mm, "end": v(53831.72, 55022.18) * mm});
            skArc(sketch, "E7009", {"start": v(53831.72, 55022.18) * mm, "mid": v(53815.58, 55030.97) * mm, "end": v(53797.21, 55031.72) * mm});
            skLineSegment(sketch, "E7010", {"start": v(54001.48, 54239.22) * mm, "end": v(54229.85, 54200.12) * mm});
            skLineSegment(sketch, "E7011", {"start": v(54061.36, 54061.98) * mm, "end": v(54270.61, 54074.1) * mm});
            skLineSegment(sketch, "E7012", {"start": v(54262.85, 54137.8) * mm, "end": v(53936.52, 54166.87) * mm});
            skArc(sketch, "E7013", {"start": v(53911.28, 56590.08) * mm, "mid": v(53845.73, 56550.87) * mm, "end": v(53796.48, 56492.49) * mm});
            skLineSegment(sketch, "E7014", {"start": v(53911.28, 56590.08) * mm, "end": v(54126.7, 56668.69) * mm});
            skArc(sketch, "E7015", {"start": v(54151.23, 56588.48) * mm, "mid": v(53944.17, 56508.45) * mm, "end": v(53743.58, 56413.35) * mm});
            skArc(sketch, "E7016", {"start": v(54132.44, 56590.62) * mm, "mid": v(54167.9, 56592.95) * mm, "end": v(54198.6, 56610.85) * mm});
            skArc(sketch, "E7017", {"start": v(54177.4, 56676.37) * mm, "mid": v(54143.16, 56673.84) * mm, "end": v(54113.37, 56656.78) * mm});
            skArc(sketch, "E7018", {"start": v(54196.43, 56608.87) * mm, "mid": v(54208.58, 56648.96) * mm, "end": v(54176.96, 56676.43) * mm});
            skArc(sketch, "E7019", {"start": v(54113.7, 56657.08) * mm, "mid": v(54102.86, 56616.62) * mm, "end": v(54135.35, 56590.19) * mm});
            skLineSegment(sketch, "E7020", {"start": v(34100, 72522.1) * mm, "end": v(32052.06, 72259.39) * mm});
            skLineSegment(sketch, "E7021", {"start": v(32052.06, 72259.39) * mm, "end": v(32032.97, 72408.17) * mm});
            skLineSegment(sketch, "E7022", {"start": v(32032.97, 72408.17) * mm, "end": v(39441.15, 73358.44) * mm});
            skLineSegment(sketch, "E7023", {"start": v(39441.15, 73358.44) * mm, "end": v(39460.24, 73209.66) * mm});
            skLineSegment(sketch, "E7024", {"start": v(39460.24, 73209.66) * mm, "end": v(37865.53, 73005.14) * mm});
            skLineSegment(sketch, "E7025", {"start": v(34858.83, 59379.88) * mm, "end": v(38413.86, 56763.64) * mm});
            skLineSegment(sketch, "E7026", {"start": v(38413.86, 56763.64) * mm, "end": v(39517.39, 53123.3) * mm});
            skLineSegment(sketch, "E7027", {"start": v(39517.39, 53123.3) * mm, "end": v(36984.58, 52356.66) * mm});
            skLineSegment(sketch, "E7028", {"start": v(36984.58, 52356.66) * mm, "end": v(34858.83, 59379.88) * mm});
            skLineSegment(sketch, "E7029", {"start": v(31997.32, 72403.55) * mm, "end": v(33353.34, 67923.5) * mm});
            skLineSegment(sketch, "E7030", {"start": v(40437.2, 70067.64) * mm, "end": v(39441.15, 73358.44) * mm});
            skLineSegment(sketch, "E7031", {"start": v(38345.1, 73217.84) * mm, "end": v(38345.1, 73217.85) * mm});
            skLineSegment(sketch, "E7032", {"start": v(35567.85, 72861.58) * mm, "end": v(35567.85, 72861.59) * mm});
            skLineSegment(sketch, "E7033", {"start": v(48630.18, 64524.82) * mm, "end": v(50782.31, 65176.37) * mm});
            skLineSegment(sketch, "E7034", {"start": v(50853.58, 64936.6) * mm, "end": v(48702.6, 64285.54) * mm});
            skLineSegment(sketch, "E7035", {"start": v(53328.4, 61951.88) * mm, "end": v(48991, 60639.04) * mm});
            skLineSegment(sketch, "E7036", {"start": v(53328.4, 61951.88) * mm, "end": v(53400.82, 61712.6) * mm});
            skLineSegment(sketch, "E7037", {"start": v(57239.17, 51925.82) * mm, "end": v(54176.2, 50998.75) * mm});
            skLineSegment(sketch, "E7038", {"start": v(55604.89, 57867.13) * mm, "end": v(57345.71, 52125.24) * mm});
            skLineSegment(sketch, "E7039", {"start": v(52345.35, 57047.72) * mm, "end": v(55408.08, 57974.72) * mm});
            skLineSegment(sketch, "E7040", {"start": v(53976.63, 51105.79) * mm, "end": v(52238.56, 56848.23) * mm});
            skLineSegment(sketch, "E7041", {"start": v(52391.7, 56894.58) * mm, "end": v(54129.84, 51151.89) * mm});
            skLineSegment(sketch, "E7042", {"start": v(55454.43, 57821.58) * mm, "end": v(52391.7, 56894.58) * mm});
            skLineSegment(sketch, "E7043", {"start": v(57192.58, 52078.89) * mm, "end": v(55454.43, 57821.58) * mm});
            skLineSegment(sketch, "E7044", {"start": v(54129.84, 51151.89) * mm, "end": v(57192.58, 52078.89) * mm});
            skLineSegment(sketch, "E7045", {"start": v(54176.2, 50998.75) * mm, "end": v(54023.05, 50952.4) * mm});
            skLineSegment(sketch, "E7046", {"start": v(54023.05, 50952.4) * mm, "end": v(54020.55, 50960.69) * mm});
            skLineSegment(sketch, "E7047", {"start": v(54020.55, 50960.69) * mm, "end": v(54086.56, 50980.7) * mm});
            skArc(sketch, "E7048", {"start": v(54086.56, 50980.7) * mm, "mid": v(54091.32, 50984.6) * mm, "end": v(54091.92, 50990.7) * mm});
            skLineSegment(sketch, "E7049", {"start": v(54091.92, 50990.7) * mm, "end": v(54055.4, 51111.92) * mm});
            skArc(sketch, "E7050", {"start": v(54055.4, 51111.92) * mm, "mid": v(54051.1, 51116.56) * mm, "end": v(54044.8, 51117.1) * mm});
            skLineSegment(sketch, "E7051", {"start": v(54044.8, 51117.1) * mm, "end": v(53979.21, 51097.25) * mm});
            skLineSegment(sketch, "E7052", {"start": v(53979.21, 51097.25) * mm, "end": v(53976.7, 51105.54) * mm});
            skLineSegment(sketch, "E7053", {"start": v(53976.7, 51105.54) * mm, "end": v(54129.84, 51151.89) * mm});
            skLineSegment(sketch, "E7054", {"start": v(54129.84, 51151.89) * mm, "end": v(54132.35, 51143.6) * mm});
            skLineSegment(sketch, "E7055", {"start": v(54132.35, 51143.6) * mm, "end": v(54066.16, 51123.56) * mm});
            skArc(sketch, "E7056", {"start": v(54066.16, 51123.56) * mm, "mid": v(54061.44, 51119.65) * mm, "end": v(54060.82, 51113.56) * mm});
            skLineSegment(sketch, "E7057", {"start": v(54060.82, 51113.56) * mm, "end": v(54097.35, 50992.34) * mm});
            skArc(sketch, "E7058", {"start": v(54097.35, 50992.34) * mm, "mid": v(54101.31, 50987.56) * mm, "end": v(54107.5, 50987) * mm});
            skLineSegment(sketch, "E7059", {"start": v(54107.5, 50987) * mm, "end": v(54173.68, 51007.04) * mm});
            skLineSegment(sketch, "E7060", {"start": v(54173.68, 51007.04) * mm, "end": v(54176.2, 50998.75) * mm});
            skLineSegment(sketch, "E7061", {"start": v(57392.07, 51972.1) * mm, "end": v(57238.93, 51925.75) * mm});
            skLineSegment(sketch, "E7062", {"start": v(57238.93, 51925.75) * mm, "end": v(57236.42, 51934.04) * mm});
            skLineSegment(sketch, "E7063", {"start": v(57236.42, 51934.04) * mm, "end": v(57302.44, 51954.06) * mm});
            skArc(sketch, "E7064", {"start": v(57302.44, 51954.06) * mm, "mid": v(57307.19, 51957.94) * mm, "end": v(57307.8, 51964.05) * mm});
            skLineSegment(sketch, "E7065", {"start": v(57307.8, 51964.05) * mm, "end": v(57271.27, 52085.27) * mm});
            skArc(sketch, "E7066", {"start": v(57271.27, 52085.27) * mm, "mid": v(57266.98, 52089.9) * mm, "end": v(57260.68, 52090.45) * mm});
            skLineSegment(sketch, "E7067", {"start": v(57260.68, 52090.45) * mm, "end": v(57195.08, 52070.6) * mm});
            skLineSegment(sketch, "E7068", {"start": v(57195.08, 52070.6) * mm, "end": v(57192.58, 52078.89) * mm});
            skLineSegment(sketch, "E7069", {"start": v(57192.58, 52078.89) * mm, "end": v(57345.71, 52125.24) * mm});
            skLineSegment(sketch, "E7070", {"start": v(57345.71, 52125.24) * mm, "end": v(57348.22, 52116.95) * mm});
            skLineSegment(sketch, "E7071", {"start": v(57348.22, 52116.95) * mm, "end": v(57282.03, 52096.92) * mm});
            skArc(sketch, "E7072", {"start": v(57282.03, 52096.92) * mm, "mid": v(57277.31, 52093) * mm, "end": v(57276.69, 52086.9) * mm});
            skLineSegment(sketch, "E7073", {"start": v(57276.69, 52086.9) * mm, "end": v(57313.22, 51965.7) * mm});
            skArc(sketch, "E7074", {"start": v(57313.22, 51965.7) * mm, "mid": v(57317.18, 51960.91) * mm, "end": v(57323.37, 51960.36) * mm});
            skLineSegment(sketch, "E7075", {"start": v(57323.37, 51960.36) * mm, "end": v(57389.56, 51980.4) * mm});
            skLineSegment(sketch, "E7076", {"start": v(57389.56, 51980.4) * mm, "end": v(57392.07, 51972.1) * mm});
            skLineSegment(sketch, "E7077", {"start": v(55607.57, 57867.94) * mm, "end": v(55454.43, 57821.58) * mm});
            skLineSegment(sketch, "E7078", {"start": v(55454.43, 57821.58) * mm, "end": v(55451.92, 57829.87) * mm});
            skLineSegment(sketch, "E7079", {"start": v(55451.92, 57829.87) * mm, "end": v(55517.94, 57849.9) * mm});
            skArc(sketch, "E7080", {"start": v(55517.94, 57849.9) * mm, "mid": v(55522.7, 57853.78) * mm, "end": v(55523.3, 57859.89) * mm});
            skLineSegment(sketch, "E7081", {"start": v(55523.3, 57859.89) * mm, "end": v(55486.78, 57981.1) * mm});
            skArc(sketch, "E7082", {"start": v(55486.78, 57981.1) * mm, "mid": v(55482.48, 57985.74) * mm, "end": v(55476.18, 57986.29) * mm});
            skLineSegment(sketch, "E7083", {"start": v(55476.18, 57986.29) * mm, "end": v(55410.59, 57966.43) * mm});
            skLineSegment(sketch, "E7084", {"start": v(55410.59, 57966.43) * mm, "end": v(55408.08, 57974.72) * mm});
            skLineSegment(sketch, "E7085", {"start": v(55408.08, 57974.72) * mm, "end": v(55561.22, 58021.08) * mm});
            skLineSegment(sketch, "E7086", {"start": v(55561.22, 58021.08) * mm, "end": v(55563.73, 58012.79) * mm});
            skLineSegment(sketch, "E7087", {"start": v(55563.73, 58012.79) * mm, "end": v(55497.54, 57992.75) * mm});
            skArc(sketch, "E7088", {"start": v(55497.54, 57992.75) * mm, "mid": v(55492.82, 57988.84) * mm, "end": v(55492.2, 57982.74) * mm});
            skLineSegment(sketch, "E7089", {"start": v(55492.2, 57982.74) * mm, "end": v(55528.73, 57861.53) * mm});
            skArc(sketch, "E7090", {"start": v(55528.73, 57861.53) * mm, "mid": v(55532.69, 57856.75) * mm, "end": v(55538.87, 57856.2) * mm});
            skLineSegment(sketch, "E7091", {"start": v(55538.87, 57856.2) * mm, "end": v(55605.06, 57876.23) * mm});
            skLineSegment(sketch, "E7092", {"start": v(55605.06, 57876.23) * mm, "end": v(55607.57, 57867.94) * mm});
            skLineSegment(sketch, "E7093", {"start": v(52391.7, 56894.58) * mm, "end": v(52238.56, 56848.23) * mm});
            skLineSegment(sketch, "E7094", {"start": v(52238.56, 56848.23) * mm, "end": v(52236.05, 56856.52) * mm});
            skLineSegment(sketch, "E7095", {"start": v(52236.05, 56856.52) * mm, "end": v(52302.07, 56876.54) * mm});
            skArc(sketch, "E7096", {"start": v(52302.07, 56876.54) * mm, "mid": v(52306.82, 56880.43) * mm, "end": v(52307.43, 56886.53) * mm});
            skLineSegment(sketch, "E7097", {"start": v(52307.43, 56886.53) * mm, "end": v(52270.9, 57007.75) * mm});
            skArc(sketch, "E7098", {"start": v(52270.9, 57007.75) * mm, "mid": v(52266.6, 57012.4) * mm, "end": v(52260.3, 57012.93) * mm});
            skLineSegment(sketch, "E7099", {"start": v(52260.3, 57012.93) * mm, "end": v(52194.72, 56993.08) * mm});
            skLineSegment(sketch, "E7100", {"start": v(52194.72, 56993.08) * mm, "end": v(52192.2, 57001.37) * mm});
            skLineSegment(sketch, "E7101", {"start": v(52192.2, 57001.37) * mm, "end": v(52345.35, 57047.72) * mm});
            skLineSegment(sketch, "E7102", {"start": v(52345.35, 57047.72) * mm, "end": v(52347.86, 57039.43) * mm});
            skLineSegment(sketch, "E7103", {"start": v(52347.86, 57039.43) * mm, "end": v(52281.67, 57019.4) * mm});
            skArc(sketch, "E7104", {"start": v(52281.67, 57019.4) * mm, "mid": v(52276.94, 57015.49) * mm, "end": v(52276.32, 57009.39) * mm});
            skLineSegment(sketch, "E7105", {"start": v(52276.32, 57009.39) * mm, "end": v(52312.86, 56888.17) * mm});
            skArc(sketch, "E7106", {"start": v(52312.86, 56888.17) * mm, "mid": v(52316.82, 56883.4) * mm, "end": v(52323, 56882.84) * mm});
            skLineSegment(sketch, "E7107", {"start": v(52323, 56882.84) * mm, "end": v(52389.19, 56902.87) * mm});
            skLineSegment(sketch, "E7108", {"start": v(52389.19, 56902.87) * mm, "end": v(52391.7, 56894.58) * mm});
            skLineSegment(sketch, "E7109", {"start": v(55694.63, 56724.4) * mm, "end": v(55675.8, 56786.62) * mm});
            skLineSegment(sketch, "E7110", {"start": v(55675.8, 56786.62) * mm, "end": v(55672.2, 56785.53) * mm});
            skArc(sketch, "E7111", {"start": v(55672.2, 56785.53) * mm, "mid": v(55669.63, 56783.5) * mm, "end": v(55669.12, 56780.27) * mm});
            skLineSegment(sketch, "E7112", {"start": v(55669.12, 56780.27) * mm, "end": v(55678.43, 56737.44) * mm});
            skArc(sketch, "E7113", {"start": v(55671.21, 56725.15) * mm, "mid": v(55677.22, 56729.88) * mm, "end": v(55678.43, 56737.44) * mm});
            skLineSegment(sketch, "E7114", {"start": v(55671.21, 56725.15) * mm, "end": v(55560.55, 56691.66) * mm});
            skArc(sketch, "E7115", {"start": v(55547.74, 56697.88) * mm, "mid": v(55552.93, 56692.26) * mm, "end": v(55560.55, 56691.66) * mm});
            skLineSegment(sketch, "E7116", {"start": v(55547.74, 56697.88) * mm, "end": v(55531.74, 56738.69) * mm});
            skArc(sketch, "E7117", {"start": v(55531.74, 56738.69) * mm, "mid": v(55529.51, 56741.1) * mm, "end": v(55526.24, 56741.35) * mm});
            skLineSegment(sketch, "E7118", {"start": v(55526.24, 56741.35) * mm, "end": v(55522.66, 56740.27) * mm});
            skLineSegment(sketch, "E7119", {"start": v(55522.66, 56740.27) * mm, "end": v(55541.49, 56678.05) * mm});
            skLineSegment(sketch, "E7120", {"start": v(55541.49, 56678.05) * mm, "end": v(55694.63, 56724.4) * mm});
            skLineSegment(sketch, "E7121", {"start": v(55616.8, 56429.2) * mm, "end": v(55635.64, 56366.99) * mm});
            skLineSegment(sketch, "E7122", {"start": v(55635.64, 56366.99) * mm, "end": v(55639.22, 56368.08) * mm});
            skArc(sketch, "E7123", {"start": v(55639.22, 56368.08) * mm, "mid": v(55641.8, 56370.1) * mm, "end": v(55642.32, 56373.34) * mm});
            skLineSegment(sketch, "E7124", {"start": v(55642.32, 56373.34) * mm, "end": v(55633, 56416.17) * mm});
            skArc(sketch, "E7125", {"start": v(55640.22, 56428.45) * mm, "mid": v(55634.2, 56423.72) * mm, "end": v(55633, 56416.17) * mm});
            skLineSegment(sketch, "E7126", {"start": v(55640.22, 56428.45) * mm, "end": v(55750.88, 56461.95) * mm});
            skArc(sketch, "E7127", {"start": v(55763.7, 56455.73) * mm, "mid": v(55758.5, 56461.34) * mm, "end": v(55750.88, 56461.95) * mm});
            skLineSegment(sketch, "E7128", {"start": v(55763.7, 56455.73) * mm, "end": v(55779.7, 56414.92) * mm});
            skArc(sketch, "E7129", {"start": v(55779.7, 56414.92) * mm, "mid": v(55781.92, 56412.51) * mm, "end": v(55785.19, 56412.26) * mm});
            skLineSegment(sketch, "E7130", {"start": v(55785.19, 56412.26) * mm, "end": v(55788.78, 56413.34) * mm});
            skLineSegment(sketch, "E7131", {"start": v(55788.78, 56413.34) * mm, "end": v(55769.95, 56475.55) * mm});
            skLineSegment(sketch, "E7132", {"start": v(55769.95, 56475.55) * mm, "end": v(55616.8, 56429.2) * mm});
            skCircle(sketch, "E7133", {"center": v(55655.72, 56576.8) * mm, "radius": 0.25 * mm});
            skCircle(sketch, "E7134", {"center": v(55655.72, 56576.8) * mm, "radius": 57.5 * mm});
            skCircle(sketch, "E7135", {"center": v(55655.72, 56576.8) * mm, "radius": 59.5 * mm});
            skCircle(sketch, "E7136", {"center": v(55655.72, 56576.8) * mm, "radius": 63.5 * mm});
            skLineSegment(sketch, "E7137", {"start": v(55607.5, 56356.38) * mm, "end": v(55636.22, 56365.08) * mm});
            skLineSegment(sketch, "E7138", {"start": v(55636.22, 56365.08) * mm, "end": v(55621.73, 56412.93) * mm});
            skLineSegment(sketch, "E7139", {"start": v(55621.73, 56412.93) * mm, "end": v(55593.02, 56404.24) * mm});
            skLineSegment(sketch, "E7140", {"start": v(55593.02, 56404.24) * mm, "end": v(55607.5, 56356.38) * mm});
            skLineSegment(sketch, "E7141", {"start": v(55636.22, 56365.08) * mm, "end": v(55635.64, 56366.99) * mm});
            skLineSegment(sketch, "E7142", {"start": v(55635.64, 56366.99) * mm, "end": v(55621.73, 56412.93) * mm});
            skLineSegment(sketch, "E7143", {"start": v(52875.62, 55599.52) * mm, "end": v(52894.45, 55537.3) * mm});
            skLineSegment(sketch, "E7144", {"start": v(52894.45, 55537.3) * mm, "end": v(52898.03, 55538.4) * mm});
            skArc(sketch, "E7145", {"start": v(52898.03, 55538.4) * mm, "mid": v(52900.6, 55540.42) * mm, "end": v(52901.13, 55543.66) * mm});
            skLineSegment(sketch, "E7146", {"start": v(52901.13, 55543.66) * mm, "end": v(52891.81, 55586.5) * mm});
            skArc(sketch, "E7147", {"start": v(52899.03, 55598.77) * mm, "mid": v(52893.02, 55594.04) * mm, "end": v(52891.81, 55586.5) * mm});
            skLineSegment(sketch, "E7148", {"start": v(52899.03, 55598.77) * mm, "end": v(53009.69, 55632.26) * mm});
            skArc(sketch, "E7149", {"start": v(53022.5, 55626.05) * mm, "mid": v(53017.31, 55631.66) * mm, "end": v(53009.69, 55632.26) * mm});
            skLineSegment(sketch, "E7150", {"start": v(53022.5, 55626.05) * mm, "end": v(53038.5, 55585.24) * mm});
            skArc(sketch, "E7151", {"start": v(53038.5, 55585.24) * mm, "mid": v(53040.73, 55582.83) * mm, "end": v(53044, 55582.57) * mm});
            skLineSegment(sketch, "E7152", {"start": v(53044, 55582.57) * mm, "end": v(53047.59, 55583.66) * mm});
            skLineSegment(sketch, "E7153", {"start": v(53047.59, 55583.66) * mm, "end": v(53028.76, 55645.87) * mm});
            skLineSegment(sketch, "E7154", {"start": v(53028.76, 55645.87) * mm, "end": v(52875.62, 55599.52) * mm});
            skLineSegment(sketch, "E7155", {"start": v(52953.44, 55894.72) * mm, "end": v(52934.6, 55956.94) * mm});
            skLineSegment(sketch, "E7156", {"start": v(52934.6, 55956.94) * mm, "end": v(52931.02, 55955.85) * mm});
            skArc(sketch, "E7157", {"start": v(52931.02, 55955.85) * mm, "mid": v(52928.44, 55953.82) * mm, "end": v(52927.92, 55950.59) * mm});
            skLineSegment(sketch, "E7158", {"start": v(52927.92, 55950.59) * mm, "end": v(52937.24, 55907.75) * mm});
            skArc(sketch, "E7159", {"start": v(52930.02, 55895.47) * mm, "mid": v(52936.03, 55900.2) * mm, "end": v(52937.24, 55907.75) * mm});
            skLineSegment(sketch, "E7160", {"start": v(52930.02, 55895.47) * mm, "end": v(52819.36, 55861.98) * mm});
            skArc(sketch, "E7161", {"start": v(52806.55, 55868.2) * mm, "mid": v(52811.74, 55862.58) * mm, "end": v(52819.36, 55861.98) * mm});
            skLineSegment(sketch, "E7162", {"start": v(52806.55, 55868.2) * mm, "end": v(52790.55, 55909) * mm});
            skArc(sketch, "E7163", {"start": v(52790.55, 55909) * mm, "mid": v(52788.32, 55911.41) * mm, "end": v(52785.05, 55911.67) * mm});
            skLineSegment(sketch, "E7164", {"start": v(52785.05, 55911.67) * mm, "end": v(52781.47, 55910.59) * mm});
            skLineSegment(sketch, "E7165", {"start": v(52781.47, 55910.59) * mm, "end": v(52800.3, 55848.37) * mm});
            skLineSegment(sketch, "E7166", {"start": v(52800.3, 55848.37) * mm, "end": v(52953.44, 55894.72) * mm});
            skCircle(sketch, "E7167", {"center": v(52914.53, 55747.12) * mm, "radius": 0.25 * mm});
            skCircle(sketch, "E7168", {"center": v(52914.53, 55747.12) * mm, "radius": 57.5 * mm});
            skCircle(sketch, "E7169", {"center": v(52914.53, 55747.12) * mm, "radius": 59.5 * mm});
            skCircle(sketch, "E7170", {"center": v(52914.53, 55747.12) * mm, "radius": 63.5 * mm});
            skLineSegment(sketch, "E7171", {"start": v(53045.04, 55592.08) * mm, "end": v(53073.75, 55600.77) * mm});
            skLineSegment(sketch, "E7172", {"start": v(53073.75, 55600.77) * mm, "end": v(53062.4, 55638.3) * mm});
            skLineSegment(sketch, "E7173", {"start": v(53062.4, 55638.3) * mm, "end": v(53033.68, 55629.6) * mm});
            skLineSegment(sketch, "E7174", {"start": v(53033.68, 55629.6) * mm, "end": v(53045.04, 55592.08) * mm});
            skLineSegment(sketch, "E7175", {"start": v(53076.88, 55590.44) * mm, "end": v(53073.75, 55600.77) * mm});
            skLineSegment(sketch, "E7176", {"start": v(53048.16, 55581.75) * mm, "end": v(53076.88, 55590.44) * mm});
            skLineSegment(sketch, "E7177", {"start": v(53048.16, 55581.75) * mm, "end": v(53047.59, 55583.66) * mm});
            skLineSegment(sketch, "E7178", {"start": v(53889.54, 52249.6) * mm, "end": v(53908.37, 52187.4) * mm});
            skLineSegment(sketch, "E7179", {"start": v(53908.37, 52187.4) * mm, "end": v(53911.96, 52188.48) * mm});
            skArc(sketch, "E7180", {"start": v(53911.96, 52188.48) * mm, "mid": v(53914.53, 52190.5) * mm, "end": v(53915.05, 52193.74) * mm});
            skLineSegment(sketch, "E7181", {"start": v(53915.05, 52193.74) * mm, "end": v(53905.74, 52236.57) * mm});
            skArc(sketch, "E7182", {"start": v(53912.96, 52248.85) * mm, "mid": v(53906.95, 52244.12) * mm, "end": v(53905.74, 52236.57) * mm});
            skLineSegment(sketch, "E7183", {"start": v(53912.96, 52248.85) * mm, "end": v(54023.61, 52282.35) * mm});
            skArc(sketch, "E7184", {"start": v(54036.43, 52276.13) * mm, "mid": v(54031.24, 52281.74) * mm, "end": v(54023.61, 52282.35) * mm});
            skLineSegment(sketch, "E7185", {"start": v(54036.43, 52276.13) * mm, "end": v(54052.43, 52235.32) * mm});
            skArc(sketch, "E7186", {"start": v(54052.43, 52235.32) * mm, "mid": v(54054.66, 52232.91) * mm, "end": v(54057.92, 52232.66) * mm});
            skLineSegment(sketch, "E7187", {"start": v(54057.92, 52232.66) * mm, "end": v(54061.51, 52233.74) * mm});
            skLineSegment(sketch, "E7188", {"start": v(54061.51, 52233.74) * mm, "end": v(54042.68, 52295.95) * mm});
            skLineSegment(sketch, "E7189", {"start": v(54042.68, 52295.95) * mm, "end": v(53889.54, 52249.6) * mm});
            skLineSegment(sketch, "E7190", {"start": v(53967.36, 52544.8) * mm, "end": v(53948.53, 52607.02) * mm});
            skLineSegment(sketch, "E7191", {"start": v(53948.53, 52607.02) * mm, "end": v(53944.94, 52605.93) * mm});
            skArc(sketch, "E7192", {"start": v(53944.94, 52605.93) * mm, "mid": v(53942.37, 52603.9) * mm, "end": v(53941.85, 52600.67) * mm});
            skLineSegment(sketch, "E7193", {"start": v(53941.85, 52600.67) * mm, "end": v(53951.17, 52557.84) * mm});
            skArc(sketch, "E7194", {"start": v(53943.95, 52545.55) * mm, "mid": v(53949.96, 52550.28) * mm, "end": v(53951.17, 52557.84) * mm});
            skLineSegment(sketch, "E7195", {"start": v(53943.95, 52545.55) * mm, "end": v(53833.3, 52512.06) * mm});
            skArc(sketch, "E7196", {"start": v(53820.47, 52518.28) * mm, "mid": v(53825.67, 52512.66) * mm, "end": v(53833.3, 52512.06) * mm});
            skLineSegment(sketch, "E7197", {"start": v(53820.47, 52518.28) * mm, "end": v(53804.47, 52559.09) * mm});
            skArc(sketch, "E7198", {"start": v(53804.47, 52559.09) * mm, "mid": v(53802.25, 52561.5) * mm, "end": v(53798.98, 52561.75) * mm});
            skLineSegment(sketch, "E7199", {"start": v(53798.98, 52561.75) * mm, "end": v(53795.4, 52560.67) * mm});
            skLineSegment(sketch, "E7200", {"start": v(53795.4, 52560.67) * mm, "end": v(53814.22, 52498.45) * mm});
            skLineSegment(sketch, "E7201", {"start": v(53814.22, 52498.45) * mm, "end": v(53967.36, 52544.8) * mm});
            skCircle(sketch, "E7202", {"center": v(53928.45, 52397.2) * mm, "radius": 0.25 * mm});
            skCircle(sketch, "E7203", {"center": v(53928.45, 52397.2) * mm, "radius": 57.5 * mm});
            skCircle(sketch, "E7204", {"center": v(53928.45, 52397.2) * mm, "radius": 59.5 * mm});
            skCircle(sketch, "E7205", {"center": v(53928.45, 52397.2) * mm, "radius": 63.5 * mm});
            skLineSegment(sketch, "E7206", {"start": v(53976.67, 52617.62) * mm, "end": v(53947.95, 52608.93) * mm});
            skLineSegment(sketch, "E7207", {"start": v(53947.95, 52608.93) * mm, "end": v(53962.44, 52561.08) * mm});
            skLineSegment(sketch, "E7208", {"start": v(53962.44, 52561.08) * mm, "end": v(53991.15, 52569.77) * mm});
            skLineSegment(sketch, "E7209", {"start": v(53991.15, 52569.77) * mm, "end": v(53976.67, 52617.62) * mm});
            skLineSegment(sketch, "E7210", {"start": v(53947.95, 52608.93) * mm, "end": v(53948.53, 52607.02) * mm});
            skLineSegment(sketch, "E7211", {"start": v(53948.53, 52607.02) * mm, "end": v(53962.44, 52561.08) * mm});
            skLineSegment(sketch, "E7212", {"start": v(56708.55, 53374.49) * mm, "end": v(56689.72, 53436.7) * mm});
            skLineSegment(sketch, "E7213", {"start": v(56689.72, 53436.7) * mm, "end": v(56686.13, 53435.61) * mm});
            skArc(sketch, "E7214", {"start": v(56686.13, 53435.61) * mm, "mid": v(56683.56, 53433.59) * mm, "end": v(56683.04, 53430.35) * mm});
            skLineSegment(sketch, "E7215", {"start": v(56683.04, 53430.35) * mm, "end": v(56692.36, 53387.52) * mm});
            skArc(sketch, "E7216", {"start": v(56685.14, 53375.24) * mm, "mid": v(56691.15, 53379.96) * mm, "end": v(56692.36, 53387.52) * mm});
            skLineSegment(sketch, "E7217", {"start": v(56685.14, 53375.24) * mm, "end": v(56574.48, 53341.74) * mm});
            skArc(sketch, "E7218", {"start": v(56561.66, 53347.96) * mm, "mid": v(56566.86, 53342.35) * mm, "end": v(56574.48, 53341.74) * mm});
            skLineSegment(sketch, "E7219", {"start": v(56561.66, 53347.96) * mm, "end": v(56545.66, 53388.77) * mm});
            skArc(sketch, "E7220", {"start": v(56545.66, 53388.77) * mm, "mid": v(56543.44, 53391.18) * mm, "end": v(56540.17, 53391.43) * mm});
            skLineSegment(sketch, "E7221", {"start": v(56540.17, 53391.43) * mm, "end": v(56536.58, 53390.35) * mm});
            skLineSegment(sketch, "E7222", {"start": v(56536.58, 53390.35) * mm, "end": v(56555.41, 53328.14) * mm});
            skLineSegment(sketch, "E7223", {"start": v(56555.41, 53328.14) * mm, "end": v(56708.55, 53374.49) * mm});
            skLineSegment(sketch, "E7224", {"start": v(56630.73, 53079.28) * mm, "end": v(56649.56, 53017.07) * mm});
            skLineSegment(sketch, "E7225", {"start": v(56649.56, 53017.07) * mm, "end": v(56653.15, 53018.16) * mm});
            skArc(sketch, "E7226", {"start": v(56653.15, 53018.16) * mm, "mid": v(56655.73, 53020.18) * mm, "end": v(56656.24, 53023.42) * mm});
            skLineSegment(sketch, "E7227", {"start": v(56656.24, 53023.42) * mm, "end": v(56646.93, 53066.25) * mm});
            skArc(sketch, "E7228", {"start": v(56654.15, 53078.53) * mm, "mid": v(56648.14, 53073.8) * mm, "end": v(56646.93, 53066.25) * mm});
            skLineSegment(sketch, "E7229", {"start": v(56654.15, 53078.53) * mm, "end": v(56764.8, 53112.03) * mm});
            skArc(sketch, "E7230", {"start": v(56777.62, 53105.81) * mm, "mid": v(56772.43, 53111.43) * mm, "end": v(56764.8, 53112.03) * mm});
            skLineSegment(sketch, "E7231", {"start": v(56777.62, 53105.81) * mm, "end": v(56793.62, 53065) * mm});
            skArc(sketch, "E7232", {"start": v(56793.62, 53065) * mm, "mid": v(56795.85, 53062.6) * mm, "end": v(56799.11, 53062.34) * mm});
            skLineSegment(sketch, "E7233", {"start": v(56799.11, 53062.34) * mm, "end": v(56802.7, 53063.42) * mm});
            skLineSegment(sketch, "E7234", {"start": v(56802.7, 53063.42) * mm, "end": v(56783.87, 53125.64) * mm});
            skLineSegment(sketch, "E7235", {"start": v(56783.87, 53125.64) * mm, "end": v(56630.73, 53079.28) * mm});
            skCircle(sketch, "E7236", {"center": v(56669.64, 53226.89) * mm, "radius": 0.25 * mm});
            skCircle(sketch, "E7237", {"center": v(56669.64, 53226.89) * mm, "radius": 57.5 * mm});
            skCircle(sketch, "E7238", {"center": v(56669.64, 53226.89) * mm, "radius": 59.5 * mm});
            skCircle(sketch, "E7239", {"center": v(56669.64, 53226.89) * mm, "radius": 63.5 * mm});
            skLineSegment(sketch, "E7240", {"start": v(56539.13, 53381.93) * mm, "end": v(56510.42, 53373.23) * mm});
            skLineSegment(sketch, "E7241", {"start": v(56510.42, 53373.23) * mm, "end": v(56521.77, 53335.72) * mm});
            skLineSegment(sketch, "E7242", {"start": v(56521.77, 53335.72) * mm, "end": v(56550.49, 53344.4) * mm});
            skLineSegment(sketch, "E7243", {"start": v(56550.49, 53344.4) * mm, "end": v(56539.13, 53381.93) * mm});
            skLineSegment(sketch, "E7244", {"start": v(56507.29, 53383.57) * mm, "end": v(56510.42, 53373.23) * mm});
            skLineSegment(sketch, "E7245", {"start": v(56536, 53392.26) * mm, "end": v(56507.29, 53383.57) * mm});
            skLineSegment(sketch, "E7246", {"start": v(56536, 53392.26) * mm, "end": v(56536.58, 53390.35) * mm});
            skLineSegment(sketch, "E7247", {"start": v(54409.66, 51283.84) * mm, "end": v(52697.54, 56940.4) * mm});
            skLineSegment(sketch, "E7248", {"start": v(52697.54, 56940.4) * mm, "end": v(55174.56, 57690.15) * mm});
            skLineSegment(sketch, "E7249", {"start": v(55174.56, 57690.15) * mm, "end": v(56886.68, 52033.59) * mm});
            skLineSegment(sketch, "E7250", {"start": v(56886.68, 52033.59) * mm, "end": v(54409.66, 51283.84) * mm});
            skLineSegment(sketch, "E7251", {"start": v(67446.81, 49725.81) * mm, "end": v(53744.87, 45578.51) * mm});
            skLineSegment(sketch, "E7252", {"start": v(67150.92, 50263.13) * mm, "end": v(54145.32, 46326.6) * mm});
            skLineSegment(sketch, "E7253", {"start": v(53744.87, 45578.51) * mm, "end": v(49515.03, 59553.16) * mm});
            skLineSegment(sketch, "E7254", {"start": v(50089.3, 59726.98) * mm, "end": v(49515.03, 59553.16) * mm});
            skLineSegment(sketch, "E7255", {"start": v(54145.32, 46326.6) * mm, "end": v(50089.3, 59726.98) * mm});
            skLineSegment(sketch, "E7256", {"start": v(53235.88, 75531.31) * mm, "end": v(30437.41, 72606.72) * mm});
            skLineSegment(sketch, "E7257", {"start": v(53564.5, 76178.39) * mm, "end": v(29657.7, 73111.61) * mm});
            skLineSegment(sketch, "E7258", {"start": v(30437.41, 72606.72) * mm, "end": v(36717.97, 51856.85) * mm});
            skLineSegment(sketch, "E7259", {"start": v(29657.7, 73111.61) * mm, "end": v(36317.52, 51108.76) * mm});
            skLineSegment(sketch, "E7260", {"start": v(38916.37, 56343.94) * mm, "end": v(44571.14, 58055.53) * mm});
            skLineSegment(sketch, "E7261", {"start": v(39664.46, 55943.5) * mm, "end": v(44744.96, 57481.26) * mm});
            skLineSegment(sketch, "E7262", {"start": v(36717.97, 51856.85) * mm, "end": v(39976.03, 52843) * mm});
            skLineSegment(sketch, "E7263", {"start": v(36317.52, 51108.76) * mm, "end": v(40724.12, 52442.55) * mm});
            skLineSegment(sketch, "E7264", {"start": v(39976.03, 52843) * mm, "end": v(38916.37, 56343.94) * mm});
            skLineSegment(sketch, "E7265", {"start": v(40724.12, 52442.55) * mm, "end": v(39664.46, 55943.5) * mm});
            skLineSegment(sketch, "E7266", {"start": v(67662.85, 49333.51) * mm, "end": v(53235.88, 75531.31) * mm});
            skLineSegment(sketch, "E7267", {"start": v(67150.92, 50263.13) * mm, "end": v(53235.88, 75531.31) * mm});
            skLineSegment(sketch, "E7268", {"start": v(68188.43, 49622.94) * mm, "end": v(53564.5, 76178.39) * mm});
            skLineSegment(sketch, "E7269", {"start": v(67662.85, 49333.51) * mm, "end": v(67446.81, 49725.81) * mm});
            skLineSegment(sketch, "E7270", {"start": v(68188.43, 49622.94) * mm, "end": v(67662.85, 49333.51) * mm});
            skLineSegment(sketch, "E7271", {"start": v(38841.66, 63847.55) * mm, "end": v(39375.14, 64572.39) * mm});
            skLineSegment(sketch, "E7272", {"start": v(39616.76, 64394.56) * mm, "end": v(39375.14, 64572.39) * mm});
            skLineSegment(sketch, "E7273", {"start": v(39083.27, 63669.72) * mm, "end": v(39616.76, 64394.56) * mm});
            skLineSegment(sketch, "E7274", {"start": v(39083.27, 63669.72) * mm, "end": v(38841.66, 63847.55) * mm});
            skLineSegment(sketch, "E7275", {"start": v(34646.67, 67032.26) * mm, "end": v(35364.5, 67249.58) * mm});
            skLineSegment(sketch, "E7276", {"start": v(35451.43, 66962.45) * mm, "end": v(35364.5, 67249.58) * mm});
            skLineSegment(sketch, "E7277", {"start": v(34733.6, 66745.13) * mm, "end": v(35451.43, 66962.45) * mm});
            skLineSegment(sketch, "E7278", {"start": v(34733.6, 66745.13) * mm, "end": v(34646.67, 67032.26) * mm});
            skLineSegment(sketch, "E7279", {"start": v(41369.6, 67281.8) * mm, "end": v(41932.72, 68046.92) * mm});
            skLineSegment(sketch, "E7280", {"start": v(42174.33, 67869.09) * mm, "end": v(41932.72, 68046.92) * mm});
            skLineSegment(sketch, "E7281", {"start": v(41611.2, 67103.98) * mm, "end": v(42174.33, 67869.09) * mm});
            skLineSegment(sketch, "E7282", {"start": v(41611.2, 67103.98) * mm, "end": v(41369.6, 67281.8) * mm});
            skLineSegment(sketch, "E7283", {"start": v(47761.24, 64287.93) * mm, "end": v(48622.63, 64548.71) * mm});
            skLineSegment(sketch, "E7284", {"start": v(48709.55, 64261.58) * mm, "end": v(48622.63, 64548.71) * mm});
            skLineSegment(sketch, "E7285", {"start": v(47848.16, 64000.8) * mm, "end": v(48709.55, 64261.58) * mm});
            skLineSegment(sketch, "E7286", {"start": v(47848.16, 64000.8) * mm, "end": v(47761.24, 64287.93) * mm});
            skLineSegment(sketch, "E7287", {"start": v(50775.12, 65200.15) * mm, "end": v(51636.5, 65460.94) * mm});
            skLineSegment(sketch, "E7288", {"start": v(51723.43, 65173.8) * mm, "end": v(51636.5, 65460.94) * mm});
            skLineSegment(sketch, "E7289", {"start": v(50862.04, 64913.02) * mm, "end": v(51723.43, 65173.8) * mm});
            skLineSegment(sketch, "E7290", {"start": v(50862.04, 64913.02) * mm, "end": v(50775.12, 65200.15) * mm});
            skLineSegment(sketch, "E7291", {"start": v(51286.26, 57153.17) * mm, "end": v(54486.1, 58121.7) * mm});
            skLineSegment(sketch, "E7292", {"start": v(52093.19, 57397.4) * mm, "end": v(54486.1, 58121.7) * mm});
            skLineSegment(sketch, "E7293", {"start": v(51358.69, 56913.89) * mm, "end": v(54558.52, 57882.41) * mm});
            skLineSegment(sketch, "E7294", {"start": v(51286.26, 57153.17) * mm, "end": v(51853.9, 57324.98) * mm});
            skLineSegment(sketch, "E7295", {"start": v(54486.1, 58121.7) * mm, "end": v(54558.1, 57883.79) * mm});
            skLineSegment(sketch, "E7296", {"start": v(54558.1, 57883.79) * mm, "end": v(54558.52, 57882.41) * mm});
            skLineSegment(sketch, "E7297", {"start": v(54485.98, 58121.66) * mm, "end": v(53326.1, 61953.71) * mm});
            skLineSegment(sketch, "E7298", {"start": v(53565.37, 62026.14) * mm, "end": v(53326.1, 61953.71) * mm});
            skLineSegment(sketch, "E7299", {"start": v(54739.33, 58147.6) * mm, "end": v(53565.37, 62026.14) * mm});
            skLineSegment(sketch, "E7300", {"start": v(54739.44, 58147.63) * mm, "end": v(55773.63, 58460.66) * mm});
            skLineSegment(sketch, "E7301", {"start": v(54558.1, 57883.79) * mm, "end": v(55677.4, 58222.57) * mm});
            skLineSegment(sketch, "E7302", {"start": v(52846.86, 58791.21) * mm, "end": v(52082.47, 61316.09) * mm});
            skLineSegment(sketch, "E7303", {"start": v(52321.74, 61388.52) * mm, "end": v(52082.47, 61316.09) * mm});
            skLineSegment(sketch, "E7304", {"start": v(53086.14, 58863.65) * mm, "end": v(52321.74, 61388.52) * mm});
            skLineSegment(sketch, "E7305", {"start": v(53086.14, 58863.65) * mm, "end": v(52846.86, 58791.21) * mm});
            skLineSegment(sketch, "E7306", {"start": v(57793.68, 52268.9) * mm, "end": v(58968.18, 52624.48) * mm});
            skLineSegment(sketch, "E7307", {"start": v(59098.58, 52193.79) * mm, "end": v(58968.18, 52624.48) * mm});
            skLineSegment(sketch, "E7308", {"start": v(57924.07, 51838.21) * mm, "end": v(59098.58, 52193.79) * mm});
            skLineSegment(sketch, "E7309", {"start": v(57924.07, 51838.21) * mm, "end": v(57793.68, 52268.9) * mm});
            skLineSegment(sketch, "E7310", {"start": v(55773.63, 58460.66) * mm, "end": v(59287.5, 52158.7) * mm});
            skLineSegment(sketch, "E7311", {"start": v(55677.4, 58222.57) * mm, "end": v(58991.9, 52278.2) * mm});
            skLineSegment(sketch, "E7312", {"start": v(59287.5, 52158.7) * mm, "end": v(53342.63, 50359.31) * mm});
            skLineSegment(sketch, "E7313", {"start": v(58991.9, 52278.2) * mm, "end": v(53284.69, 50550.73) * mm});
            skFitSpline(sketch, "E7314", {"points": [v(50033.58, 70237.61) * mm, v(50033.58, 70157.21) * mm, v(50114.02, 70018.01) * mm, v(50253.28, 69937.61) * mm, v(50414.15, 69937.61) * mm, v(50553.4, 70018.01) * mm, v(50633.84, 70157.21) * mm, v(50633.84, 70318.01) * mm, v(50553.4, 70457.21) * mm, v(50414.15, 70537.61) * mm, v(50253.28, 70537.61) * mm, v(50114.02, 70457.21) * mm, v(50033.58, 70318.01) * mm, v(50033.58, 70237.61) * mm]});
            skLineSegment(sketch, "E7315", {"start": v(30437.38, 72606.71) * mm, "end": v(53075.2, 75510.7) * mm});
            skLineSegment(sketch, "E7316", {"start": v(31027.58, 72279.15) * mm, "end": v(52857.63, 75079.51) * mm});
            skLineSegment(sketch, "E7317", {"start": v(66559.72, 50502.1) * mm, "end": v(54412.29, 46825.33) * mm});
            skLineSegment(sketch, "E7318", {"start": v(39517.02, 53123.18) * mm, "end": v(38457.35, 56624.15) * mm});
            skLineSegment(sketch, "E7319", {"start": v(39977.46, 52844.63) * mm, "end": v(38917.8, 56345.6) * mm});
            skLineSegment(sketch, "E7320", {"start": v(38457.35, 56624.15) * mm, "end": v(44386.82, 58418.88) * mm});
            skLineSegment(sketch, "E7321", {"start": v(44502.7, 58036.03) * mm, "end": v(44386.82, 58418.88) * mm});
            skLineSegment(sketch, "E7322", {"start": v(38917.8, 56345.6) * mm, "end": v(44502.7, 58036.03) * mm});
            skLineSegment(sketch, "E7323", {"start": v(54412.29, 46825.33) * mm, "end": v(50356.27, 60225.7) * mm});
            skLineSegment(sketch, "E7324", {"start": v(50089.3, 59726.98) * mm, "end": v(49336.06, 59499) * mm});
            skLineSegment(sketch, "E7325", {"start": v(49220.18, 59881.84) * mm, "end": v(49336.06, 59499) * mm});
            skLineSegment(sketch, "E7326", {"start": v(50356.27, 60225.7) * mm, "end": v(49220.18, 59881.84) * mm});
            skLineSegment(sketch, "E7327", {"start": v(66559.72, 50502.1) * mm, "end": v(52857.63, 75079.51) * mm});
            skLineSegment(sketch, "E7328", {"start": v(67150.92, 50263.13) * mm, "end": v(53075.2, 75510.7) * mm});
            skLineSegment(sketch, "E7329", {"start": v(32831.65, 66077.32) * mm, "end": v(36984.61, 52356.67) * mm});
            skLineSegment(sketch, "E7330", {"start": v(32448.8, 65961.44) * mm, "end": v(36717.64, 51857.95) * mm});
            skLineSegment(sketch, "E7331", {"start": v(36984.61, 52356.67) * mm, "end": v(39517.02, 53123.18) * mm});
            skLineSegment(sketch, "E7332", {"start": v(36717.64, 51857.95) * mm, "end": v(39977.46, 52844.63) * mm});
            skLineSegment(sketch, "E7333", {"start": v(32448.77, 65961.43) * mm, "end": v(30437.38, 72606.71) * mm});
            skLineSegment(sketch, "E7334", {"start": v(32898.61, 66097.6) * mm, "end": v(31027.58, 72279.15) * mm});
            skLineSegment(sketch, "E7335", {"start": v(32448.77, 65961.43) * mm, "end": v(32448.8, 65961.44) * mm});
            skLineSegment(sketch, "E7336", {"start": v(32831.65, 66077.32) * mm, "end": v(32898.61, 66097.6) * mm});
            skCircle(sketch, "E7337", {"center": v(40161.14, 53266.98) * mm, "radius": 300 * mm});
            skCircle(sketch, "E7338", {"center": v(39509.32, 55420.5) * mm, "radius": 300 * mm});
            skCircle(sketch, "E7339", {"center": v(39726.6, 54702.66) * mm, "radius": 300 * mm});
            skCircle(sketch, "E7340", {"center": v(39943.87, 53984.82) * mm, "radius": 300 * mm});
            skCircle(sketch, "E7341", {"center": v(53400.19, 75854.85) * mm, "radius": 300 * mm});
            skCircle(sketch, "E7342", {"center": v(53759.7, 75202) * mm, "radius": 300 * mm});
            skCircle(sketch, "E7343", {"center": v(54119.23, 74549.16) * mm, "radius": 300 * mm});
            skCircle(sketch, "E7344", {"center": v(54478.74, 73896.31) * mm, "radius": 300 * mm});
            skCircle(sketch, "E7345", {"center": v(54838.26, 73243.47) * mm, "radius": 300 * mm});
            skCircle(sketch, "E7346", {"center": v(55197.78, 72590.62) * mm, "radius": 300 * mm});
            skCircle(sketch, "E7347", {"center": v(55557.3, 71937.77) * mm, "radius": 300 * mm});
            skCircle(sketch, "E7348", {"center": v(55916.82, 71284.93) * mm, "radius": 300 * mm});
            skCircle(sketch, "E7349", {"center": v(56276.34, 70632.08) * mm, "radius": 300 * mm});
            skCircle(sketch, "E7350", {"center": v(56635.85, 69979.24) * mm, "radius": 300 * mm});
            skCircle(sketch, "E7351", {"center": v(56995.37, 69326.4) * mm, "radius": 300 * mm});
            skCircle(sketch, "E7352", {"center": v(57354.9, 68673.55) * mm, "radius": 300 * mm});
            skCircle(sketch, "E7353", {"center": v(57714.4, 68020.7) * mm, "radius": 300 * mm});
            skCircle(sketch, "E7354", {"center": v(58073.93, 67367.85) * mm, "radius": 300 * mm});
            skCircle(sketch, "E7355", {"center": v(58433.45, 66715) * mm, "radius": 300 * mm});
            skCircle(sketch, "E7356", {"center": v(58792.97, 66062.16) * mm, "radius": 300 * mm});
            skCircle(sketch, "E7357", {"center": v(59152.48, 65409.32) * mm, "radius": 300 * mm});
            skCircle(sketch, "E7358", {"center": v(59512, 64756.47) * mm, "radius": 300 * mm});
            skCircle(sketch, "E7359", {"center": v(59871.52, 64103.62) * mm, "radius": 300 * mm});
            skCircle(sketch, "E7360", {"center": v(60231.04, 63450.78) * mm, "radius": 300 * mm});
            skCircle(sketch, "E7361", {"center": v(60590.56, 62797.93) * mm, "radius": 300 * mm});
            skCircle(sketch, "E7362", {"center": v(60950.08, 62145.09) * mm, "radius": 300 * mm});
            skCircle(sketch, "E7363", {"center": v(61309.6, 61492.24) * mm, "radius": 300 * mm});
            skCircle(sketch, "E7364", {"center": v(61669.11, 60839.4) * mm, "radius": 300 * mm});
            skCircle(sketch, "E7365", {"center": v(62028.63, 60186.55) * mm, "radius": 300 * mm});
            skCircle(sketch, "E7366", {"center": v(62388.15, 59533.7) * mm, "radius": 300 * mm});
            skCircle(sketch, "E7367", {"center": v(62747.67, 58880.86) * mm, "radius": 300 * mm});
            skCircle(sketch, "E7368", {"center": v(63107.19, 58228.01) * mm, "radius": 300 * mm});
            skCircle(sketch, "E7369", {"center": v(63466.7, 57575.16) * mm, "radius": 300 * mm});
            skCircle(sketch, "E7370", {"center": v(63826.22, 56922.32) * mm, "radius": 300 * mm});
            skCircle(sketch, "E7371", {"center": v(64185.74, 56269.47) * mm, "radius": 300 * mm});
            skCircle(sketch, "E7372", {"center": v(64545.26, 55616.63) * mm, "radius": 300 * mm});
            skCircle(sketch, "E7373", {"center": v(64904.78, 54963.78) * mm, "radius": 300 * mm});
            skCircle(sketch, "E7374", {"center": v(65264.3, 54310.94) * mm, "radius": 300 * mm});
            skCircle(sketch, "E7375", {"center": v(65623.81, 53658.09) * mm, "radius": 300 * mm});
            skCircle(sketch, "E7376", {"center": v(65983.33, 53005.24) * mm, "radius": 300 * mm});
            skCircle(sketch, "E7377", {"center": v(66342.85, 52352.4) * mm, "radius": 300 * mm});
            skCircle(sketch, "E7378", {"center": v(66702.37, 51699.55) * mm, "radius": 300 * mm});
            skCircle(sketch, "E7379", {"center": v(67061.89, 51046.7) * mm, "radius": 300 * mm});
            skCircle(sketch, "E7380", {"center": v(67421.4, 50393.86) * mm, "radius": 300 * mm});
            skCircle(sketch, "E7381", {"center": v(67780.92, 49741.01) * mm, "radius": 300 * mm});
            skCircle(sketch, "E7382", {"center": v(53579.95, 75528.43) * mm, "radius": 300 * mm});
            skCircle(sketch, "E7383", {"center": v(53939.47, 74875.58) * mm, "radius": 300 * mm});
            skCircle(sketch, "E7384", {"center": v(54298.99, 74222.74) * mm, "radius": 300 * mm});
            skCircle(sketch, "E7385", {"center": v(54658.5, 73569.89) * mm, "radius": 300 * mm});
            skCircle(sketch, "E7386", {"center": v(55018.02, 72917.04) * mm, "radius": 300 * mm});
            skCircle(sketch, "E7387", {"center": v(55377.54, 72264.2) * mm, "radius": 300 * mm});
            skCircle(sketch, "E7388", {"center": v(55737.06, 71611.35) * mm, "radius": 300 * mm});
            skCircle(sketch, "E7389", {"center": v(56096.58, 70958.5) * mm, "radius": 300 * mm});
            skCircle(sketch, "E7390", {"center": v(56456.1, 70305.66) * mm, "radius": 300 * mm});
            skCircle(sketch, "E7391", {"center": v(56815.61, 69652.81) * mm, "radius": 300 * mm});
            skCircle(sketch, "E7392", {"center": v(57175.13, 68999.97) * mm, "radius": 300 * mm});
            skCircle(sketch, "E7393", {"center": v(57534.65, 68347.12) * mm, "radius": 300 * mm});
            skCircle(sketch, "E7394", {"center": v(57894.17, 67694.28) * mm, "radius": 300 * mm});
            skCircle(sketch, "E7395", {"center": v(58253.69, 67041.43) * mm, "radius": 300 * mm});
            skCircle(sketch, "E7396", {"center": v(58613.2, 66388.58) * mm, "radius": 300 * mm});
            skCircle(sketch, "E7397", {"center": v(58972.72, 65735.74) * mm, "radius": 300 * mm});
            skCircle(sketch, "E7398", {"center": v(59332.24, 65082.9) * mm, "radius": 300 * mm});
            skCircle(sketch, "E7399", {"center": v(59691.76, 64430.05) * mm, "radius": 300 * mm});
            skCircle(sketch, "E7400", {"center": v(60051.28, 63777.2) * mm, "radius": 300 * mm});
            skCircle(sketch, "E7401", {"center": v(60410.8, 63124.35) * mm, "radius": 300 * mm});
            skCircle(sketch, "E7402", {"center": v(60770.32, 62471.5) * mm, "radius": 300 * mm});
            skCircle(sketch, "E7403", {"center": v(61129.83, 61818.66) * mm, "radius": 300 * mm});
            skCircle(sketch, "E7404", {"center": v(61489.35, 61165.82) * mm, "radius": 300 * mm});
            skCircle(sketch, "E7405", {"center": v(61848.87, 60512.97) * mm, "radius": 300 * mm});
            skCircle(sketch, "E7406", {"center": v(62208.39, 59860.13) * mm, "radius": 300 * mm});
            skCircle(sketch, "E7407", {"center": v(62567.9, 59207.28) * mm, "radius": 300 * mm});
            skCircle(sketch, "E7408", {"center": v(62927.43, 58554.43) * mm, "radius": 300 * mm});
            skCircle(sketch, "E7409", {"center": v(63286.94, 57901.59) * mm, "radius": 300 * mm});
            skCircle(sketch, "E7410", {"center": v(63646.46, 57248.74) * mm, "radius": 300 * mm});
            skCircle(sketch, "E7411", {"center": v(64005.98, 56595.9) * mm, "radius": 300 * mm});
            skCircle(sketch, "E7412", {"center": v(64725.02, 55290.2) * mm, "radius": 300 * mm});
            skCircle(sketch, "E7413", {"center": v(65084.54, 54637.36) * mm, "radius": 300 * mm});
            skCircle(sketch, "E7414", {"center": v(65444.05, 53984.51) * mm, "radius": 300 * mm});
            skCircle(sketch, "E7415", {"center": v(64365.5, 55943.05) * mm, "radius": 300 * mm});
            skCircle(sketch, "E7416", {"center": v(65803.57, 53331.67) * mm, "radius": 300 * mm});
            skCircle(sketch, "E7417", {"center": v(66163.1, 52678.82) * mm, "radius": 300 * mm});
            skCircle(sketch, "E7418", {"center": v(66882.13, 51373.13) * mm, "radius": 300 * mm});
            skCircle(sketch, "E7419", {"center": v(67241.65, 50720.28) * mm, "radius": 300 * mm});
            skCircle(sketch, "E7420", {"center": v(67601.17, 50067.44) * mm, "radius": 300 * mm});
            skCircle(sketch, "E7421", {"center": v(66522.61, 52025.97) * mm, "radius": 300 * mm});
            skCircle(sketch, "E7422", {"center": v(49888.89, 59352.88) * mm, "radius": 300 * mm});
            skCircle(sketch, "E7423", {"center": v(53945.1, 45952.56) * mm, "radius": 300 * mm});
            skCircle(sketch, "E7424", {"center": v(44086.3, 57596.56) * mm, "radius": 300 * mm});
            skCircle(sketch, "E7425", {"center": v(30047.42, 72859.15) * mm, "radius": 300 * mm});
            skCircle(sketch, "E7426", {"center": v(42647.96, 57161.2) * mm, "radius": 300 * mm});
            skCircle(sketch, "E7427", {"center": v(43367, 57378.84) * mm, "radius": 300 * mm});
            skCircle(sketch, "E7428", {"center": v(33483.8, 61505.57) * mm, "radius": 300 * mm});
            skCircle(sketch, "E7429", {"center": v(33275.53, 62192.53) * mm, "radius": 300 * mm});
            skCircle(sketch, "E7430", {"center": v(33066.54, 62883.79) * mm, "radius": 300 * mm});
            skCircle(sketch, "E7431", {"center": v(32860.74, 63564.43) * mm, "radius": 300 * mm});
            skCircle(sketch, "E7432", {"center": v(32644.34, 64279.4) * mm, "radius": 300 * mm});
            skCircle(sketch, "E7433", {"center": v(32427.93, 64994.36) * mm, "radius": 300 * mm});
            skCircle(sketch, "E7434", {"center": v(32211.53, 65709.33) * mm, "radius": 300 * mm});
            skCircle(sketch, "E7435", {"center": v(31995.12, 66424.3) * mm, "radius": 300 * mm});
            skCircle(sketch, "E7436", {"center": v(31778.71, 67139.26) * mm, "radius": 300 * mm});
            skCircle(sketch, "E7437", {"center": v(31562.3, 67854.23) * mm, "radius": 300 * mm});
            skCircle(sketch, "E7438", {"center": v(31345.9, 68569.2) * mm, "radius": 300 * mm});
            skCircle(sketch, "E7439", {"center": v(31129.5, 69284.16) * mm, "radius": 300 * mm});
            skCircle(sketch, "E7440", {"center": v(30913.1, 69999.13) * mm, "radius": 300 * mm});
            skCircle(sketch, "E7441", {"center": v(30696.68, 70714.1) * mm, "radius": 300 * mm});
            skCircle(sketch, "E7442", {"center": v(30480.28, 71429.06) * mm, "radius": 300 * mm});
            skCircle(sketch, "E7443", {"center": v(30263.87, 72144.03) * mm, "radius": 300 * mm});
            skCircle(sketch, "E7444", {"center": v(30777.44, 72952.8) * mm, "radius": 300 * mm});
            skCircle(sketch, "E7445", {"center": v(31507.46, 73046.44) * mm, "radius": 300 * mm});
            skCircle(sketch, "E7446", {"center": v(32237.47, 73140.09) * mm, "radius": 300 * mm});
            skCircle(sketch, "E7447", {"center": v(32967.5, 73233.74) * mm, "radius": 300 * mm});
            skCircle(sketch, "E7448", {"center": v(33697.51, 73327.38) * mm, "radius": 300 * mm});
            skCircle(sketch, "E7449", {"center": v(34427.53, 73421.03) * mm, "radius": 300 * mm});
            skCircle(sketch, "E7450", {"center": v(35157.55, 73514.68) * mm, "radius": 300 * mm});
            skCircle(sketch, "E7451", {"center": v(35887.56, 73608.32) * mm, "radius": 300 * mm});
            skCircle(sketch, "E7452", {"center": v(36617.58, 73701.97) * mm, "radius": 300 * mm});
            skCircle(sketch, "E7453", {"center": v(37347.6, 73795.62) * mm, "radius": 300 * mm});
            skCircle(sketch, "E7454", {"center": v(38077.62, 73889.27) * mm, "radius": 300 * mm});
            skCircle(sketch, "E7455", {"center": v(38807.64, 73982.91) * mm, "radius": 300 * mm});
            skCircle(sketch, "E7456", {"center": v(39537.65, 74076.56) * mm, "radius": 300 * mm});
            skCircle(sketch, "E7457", {"center": v(40267.67, 74170.2) * mm, "radius": 300 * mm});
            skCircle(sketch, "E7458", {"center": v(40997.7, 74263.85) * mm, "radius": 300 * mm});
            skCircle(sketch, "E7459", {"center": v(41727.7, 74357.5) * mm, "radius": 300 * mm});
            skCircle(sketch, "E7460", {"center": v(42457.73, 74451.15) * mm, "radius": 300 * mm});
            skCircle(sketch, "E7461", {"center": v(43187.74, 74544.8) * mm, "radius": 300 * mm});
            skCircle(sketch, "E7462", {"center": v(43917.76, 74638.44) * mm, "radius": 300 * mm});
            skCircle(sketch, "E7463", {"center": v(44647.78, 74732.09) * mm, "radius": 300 * mm});
            skCircle(sketch, "E7464", {"center": v(45377.8, 74825.74) * mm, "radius": 300 * mm});
            skCircle(sketch, "E7465", {"center": v(46107.82, 74919.38) * mm, "radius": 300 * mm});
            skCircle(sketch, "E7466", {"center": v(46837.83, 75013.03) * mm, "radius": 300 * mm});
            skCircle(sketch, "E7467", {"center": v(47567.85, 75106.68) * mm, "radius": 300 * mm});
            skCircle(sketch, "E7468", {"center": v(48297.87, 75200.32) * mm, "radius": 300 * mm});
            skCircle(sketch, "E7469", {"center": v(49027.89, 75293.97) * mm, "radius": 300 * mm});
            skCircle(sketch, "E7470", {"center": v(49757.9, 75387.62) * mm, "radius": 300 * mm});
            skCircle(sketch, "E7471", {"center": v(50487.92, 75481.26) * mm, "radius": 300 * mm});
            skCircle(sketch, "E7472", {"center": v(51217.94, 75574.91) * mm, "radius": 300 * mm});
            skCircle(sketch, "E7473", {"center": v(51947.96, 75668.56) * mm, "radius": 300 * mm});
            skCircle(sketch, "E7474", {"center": v(52677.98, 75762.2) * mm, "radius": 300 * mm});
            skCircle(sketch, "E7475", {"center": v(54664.85, 46170.41) * mm, "radius": 300 * mm});
            skCircle(sketch, "E7476", {"center": v(55384.6, 46388.28) * mm, "radius": 300 * mm});
            skCircle(sketch, "E7477", {"center": v(56104.35, 46606.14) * mm, "radius": 300 * mm});
            skCircle(sketch, "E7478", {"center": v(56824.1, 46824) * mm, "radius": 300 * mm});
            skCircle(sketch, "E7479", {"center": v(57543.85, 47041.87) * mm, "radius": 300 * mm});
            skCircle(sketch, "E7480", {"center": v(58263.6, 47259.73) * mm, "radius": 300 * mm});
            skCircle(sketch, "E7481", {"center": v(58983.35, 47477.6) * mm, "radius": 300 * mm});
            skCircle(sketch, "E7482", {"center": v(59703.1, 47695.46) * mm, "radius": 300 * mm});
            skCircle(sketch, "E7483", {"center": v(60422.84, 47913.33) * mm, "radius": 300 * mm});
            skCircle(sketch, "E7484", {"center": v(61142.6, 48131.2) * mm, "radius": 300 * mm});
            skCircle(sketch, "E7485", {"center": v(61862.34, 48349.06) * mm, "radius": 300 * mm});
            skCircle(sketch, "E7486", {"center": v(62582.1, 48566.92) * mm, "radius": 300 * mm});
            skCircle(sketch, "E7487", {"center": v(63301.84, 48784.78) * mm, "radius": 300 * mm});
            skCircle(sketch, "E7488", {"center": v(64021.6, 49002.65) * mm, "radius": 300 * mm});
            skCircle(sketch, "E7489", {"center": v(64741.34, 49220.51) * mm, "radius": 300 * mm});
            skCircle(sketch, "E7490", {"center": v(65461.09, 49438.38) * mm, "radius": 300 * mm});
            skCircle(sketch, "E7491", {"center": v(66180.84, 49656.24) * mm, "radius": 300 * mm});
            skCircle(sketch, "E7492", {"center": v(66900.59, 49874.1) * mm, "radius": 300 * mm});
            skCircle(sketch, "E7493", {"center": v(53731.58, 46657.95) * mm, "radius": 300 * mm});
            skCircle(sketch, "E7494", {"center": v(53518.06, 47363.34) * mm, "radius": 300 * mm});
            skCircle(sketch, "E7495", {"center": v(53304.54, 48068.73) * mm, "radius": 300 * mm});
            skCircle(sketch, "E7496", {"center": v(53091.02, 48774.13) * mm, "radius": 300 * mm});
            skCircle(sketch, "E7497", {"center": v(52877.5, 49479.52) * mm, "radius": 300 * mm});
            skCircle(sketch, "E7498", {"center": v(52663.99, 50184.91) * mm, "radius": 300 * mm});
            skCircle(sketch, "E7499", {"center": v(52450.47, 50890.3) * mm, "radius": 300 * mm});
            skCircle(sketch, "E7500", {"center": v(52236.95, 51595.7) * mm, "radius": 300 * mm});
            skCircle(sketch, "E7501", {"center": v(52023.43, 52301.1) * mm, "radius": 300 * mm});
            skCircle(sketch, "E7502", {"center": v(51809.91, 53006.48) * mm, "radius": 300 * mm});
            skCircle(sketch, "E7503", {"center": v(51596.4, 53711.88) * mm, "radius": 300 * mm});
            skCircle(sketch, "E7504", {"center": v(51382.87, 54417.27) * mm, "radius": 300 * mm});
            skCircle(sketch, "E7505", {"center": v(51169.35, 55122.66) * mm, "radius": 300 * mm});
            skCircle(sketch, "E7506", {"center": v(50955.84, 55828.05) * mm, "radius": 300 * mm});
            skCircle(sketch, "E7507", {"center": v(50742.32, 56533.45) * mm, "radius": 300 * mm});
            skCircle(sketch, "E7508", {"center": v(50528.8, 57238.84) * mm, "radius": 300 * mm});
            skCircle(sketch, "E7509", {"center": v(50315.28, 57944.23) * mm, "radius": 300 * mm});
            skCircle(sketch, "E7510", {"center": v(50101.76, 58649.62) * mm, "radius": 300 * mm});
            skLineSegment(sketch, "E7511", {"start": v(40350.08, 52642.78) * mm, "end": v(39290.08, 56144.84) * mm});
            skLineSegment(sketch, "E7512", {"start": v(36517.3, 51483.84) * mm, "end": v(35457.62, 54984.83) * mm});
            skLineSegment(sketch, "E7513", {"start": v(53945.1, 45952.56) * mm, "end": v(49888.89, 59352.88) * mm});
            skLineSegment(sketch, "E7514", {"start": v(53945.1, 45952.56) * mm, "end": v(66900.59, 49874.1) * mm});
            skLineSegment(sketch, "E7515", {"start": v(53400.19, 75854.85) * mm, "end": v(67780.92, 49741.01) * mm});
            skLineSegment(sketch, "E7516", {"start": v(30047.42, 72859.15) * mm, "end": v(53400.19, 75854.85) * mm});
            skCircle(sketch, "E7517", {"center": v(33621.22, 60726.77) * mm, "radius": 375 * mm});
            skLineSegment(sketch, "E7518", {"start": v(35123.8, 56106.32) * mm, "end": v(35600.08, 54499.8) * mm});
            skLineSegment(sketch, "E7519", {"start": v(34931.23, 56052.24) * mm, "end": v(35408.33, 54442.95) * mm});
            skLineSegment(sketch, "E7520", {"start": v(34713.87, 57650.93) * mm, "end": v(35123.8, 56106.32) * mm});
            skLineSegment(sketch, "E7521", {"start": v(34522.07, 57593.97) * mm, "end": v(34931.23, 56052.24) * mm});
            skLineSegment(sketch, "E7522", {"start": v(34069.7, 59608.22) * mm, "end": v(34713.87, 57650.93) * mm});
            skLineSegment(sketch, "E7523", {"start": v(33879.73, 59545.7) * mm, "end": v(34522.07, 57593.97) * mm});
            skLineSegment(sketch, "E7524", {"start": v(33879.73, 59545.7) * mm, "end": v(34069.7, 59608.22) * mm});
            skCircle(sketch, "E7525", {"center": v(35503.23, 54471.13) * mm, "radius": 375 * mm});
            skCircle(sketch, "E7526", {"center": v(35024.65, 56078.4) * mm, "radius": 375 * mm});
            skCircle(sketch, "E7527", {"center": v(34617.97, 57622.45) * mm, "radius": 300 * mm});
            skCircle(sketch, "E7528", {"center": v(33974.72, 59576.96) * mm, "radius": 375 * mm});
            skCircle(sketch, "E7529", {"center": v(35948.4, 52971.91) * mm, "radius": 375 * mm});
            skCircle(sketch, "E7530", {"center": v(36387.31, 51517) * mm, "radius": 375 * mm});
            skCircle(sketch, "E7531", {"center": v(37796.6, 51792.76) * mm, "radius": 375 * mm});
            skCircle(sketch, "E7532", {"center": v(39835.27, 56332.54) * mm, "radius": 375 * mm});
            skCircle(sketch, "E7533", {"center": v(41846.6, 56950.07) * mm, "radius": 375 * mm});
            skLineSegment(sketch, "E7534", {"start": v(35706.21, 54140.42) * mm, "end": v(35937.9, 53360.17) * mm});
            skLineSegment(sketch, "E7535", {"start": v(35746.17, 53303.24) * mm, "end": v(35937.9, 53360.17) * mm});
            skLineSegment(sketch, "E7536", {"start": v(35514.49, 54083.49) * mm, "end": v(35746.17, 53303.24) * mm});
            skLineSegment(sketch, "E7537", {"start": v(35514.49, 54083.49) * mm, "end": v(35706.21, 54140.42) * mm});
            skLineSegment(sketch, "E7538", {"start": v(36152.82, 52642.08) * mm, "end": v(36375.12, 51905.21) * mm});
            skLineSegment(sketch, "E7539", {"start": v(36183.64, 51847.45) * mm, "end": v(36375.12, 51905.21) * mm});
            skLineSegment(sketch, "E7540", {"start": v(35961.34, 52584.32) * mm, "end": v(36183.64, 51847.45) * mm});
            skLineSegment(sketch, "E7541", {"start": v(35961.34, 52584.32) * mm, "end": v(36152.82, 52642.08) * mm});
            skLineSegment(sketch, "E7542", {"start": v(36736.53, 51687.4) * mm, "end": v(37409.39, 51818.95) * mm});
            skLineSegment(sketch, "E7543", {"start": v(37447.76, 51622.67) * mm, "end": v(37409.39, 51818.95) * mm});
            skLineSegment(sketch, "E7544", {"start": v(36774.9, 51491.12) * mm, "end": v(37447.76, 51622.67) * mm});
            skLineSegment(sketch, "E7545", {"start": v(36774.9, 51491.12) * mm, "end": v(36736.53, 51687.4) * mm});
            skLineSegment(sketch, "E7546", {"start": v(40164.4, 56538.2) * mm, "end": v(41458.77, 56935.6) * mm});
            skLineSegment(sketch, "E7547", {"start": v(41517.47, 56744.4) * mm, "end": v(41458.77, 56935.6) * mm});
            skLineSegment(sketch, "E7548", {"start": v(40223.1, 56347) * mm, "end": v(41517.47, 56744.4) * mm});
            skLineSegment(sketch, "E7549", {"start": v(40223.1, 56347) * mm, "end": v(40164.4, 56538.2) * mm});
            skCircle(sketch, "E7550", {"center": v(38530.81, 52093.36) * mm, "radius": 300 * mm});
            skCircle(sketch, "E7551", {"center": v(39248.7, 52310.48) * mm, "radius": 300 * mm});
            skCircle(sketch, "E7552", {"center": v(39966.5, 52527.84) * mm, "radius": 300 * mm});
            skLineSegment(sketch, "E7553", {"start": v(39290.08, 56144.84) * mm, "end": v(49888.89, 59352.88) * mm});
            skLineSegment(sketch, "E7554", {"start": v(36517.4, 51483.94) * mm, "end": v(40348.6, 52643.57) * mm});
            skLineSegment(sketch, "E7555", {"start": v(30047.42, 72859.15) * mm, "end": v(36517.66, 51482.64) * mm});
            skLineSegment(sketch, "E7556", {"start": v(43861.14, 60155.86) * mm, "end": v(43459.76, 61481.53) * mm});
            skLineSegment(sketch, "E7557", {"start": v(43746.89, 61568.47) * mm, "end": v(43459.76, 61481.53) * mm});
            skLineSegment(sketch, "E7558", {"start": v(44148.27, 60242.8) * mm, "end": v(43746.89, 61568.47) * mm});
            skLineSegment(sketch, "E7559", {"start": v(44643.85, 60262.18) * mm, "end": v(44184.43, 60123.13) * mm});
            skLineSegment(sketch, "E7560", {"start": v(44571.42, 60501.46) * mm, "end": v(43824.88, 60275.5) * mm});
            skLineSegment(sketch, "E7561", {"start": v(46706.46, 60886.47) * mm, "end": v(45505.25, 60522.9) * mm});
            skLineSegment(sketch, "E7562", {"start": v(46634.04, 61125.75) * mm, "end": v(45432.83, 60762.18) * mm});
            skLineSegment(sketch, "E7563", {"start": v(48505.85, 61431.1) * mm, "end": v(47759.3, 61205.13) * mm});
            skLineSegment(sketch, "E7564", {"start": v(48672.7, 61742.8) * mm, "end": v(47686.87, 61444.41) * mm});
            skLineSegment(sketch, "E7565", {"start": v(45469.04, 60642.54) * mm, "end": v(45505.25, 60522.9) * mm});
            skLineSegment(sketch, "E7566", {"start": v(44607.63, 60381.82) * mm, "end": v(44643.85, 60262.18) * mm});
            skLineSegment(sketch, "E7567", {"start": v(45469.04, 60642.54) * mm, "end": v(45432.83, 60762.18) * mm});
            skLineSegment(sketch, "E7568", {"start": v(44607.63, 60381.82) * mm, "end": v(44571.42, 60501.46) * mm});
            skLineSegment(sketch, "E7569", {"start": v(44571.42, 60501.46) * mm, "end": v(45432.83, 60762.18) * mm});
            skLineSegment(sketch, "E7570", {"start": v(44643.85, 60262.18) * mm, "end": v(45505.25, 60522.9) * mm});
            skLineSegment(sketch, "E7571", {"start": v(47723.08, 61324.77) * mm, "end": v(47759.3, 61205.13) * mm});
            skLineSegment(sketch, "E7572", {"start": v(46670.25, 61006.11) * mm, "end": v(46706.46, 60886.47) * mm});
            skLineSegment(sketch, "E7573", {"start": v(47723.08, 61324.77) * mm, "end": v(47686.87, 61444.41) * mm});
            skLineSegment(sketch, "E7574", {"start": v(46670.25, 61006.11) * mm, "end": v(46634.04, 61125.75) * mm});
            skLineSegment(sketch, "E7575", {"start": v(46634.04, 61125.75) * mm, "end": v(47686.87, 61444.41) * mm});
            skLineSegment(sketch, "E7576", {"start": v(46706.46, 60886.47) * mm, "end": v(47759.3, 61205.13) * mm});
            skLineSegment(sketch, "E7577", {"start": v(48672.7, 61742.8) * mm, "end": v(49476.62, 59086.75) * mm});
            skLineSegment(sketch, "E7578", {"start": v(48505.85, 61431.1) * mm, "end": v(49091.04, 59497.67) * mm});
            skLineSegment(sketch, "E7579", {"start": v(44184.43, 60123.13) * mm, "end": v(44769.56, 58189.64) * mm});
            skLineSegment(sketch, "E7580", {"start": v(43824.88, 60275.5) * mm, "end": v(44628.7, 57619.38) * mm});
            skLineSegment(sketch, "E7581", {"start": v(46549.88, 58728.5) * mm, "end": v(45964.7, 60661.96) * mm});
            skLineSegment(sketch, "E7582", {"start": v(46741.3, 58786.45) * mm, "end": v(46156.12, 60719.9) * mm});
            skLineSegment(sketch, "E7583", {"start": v(49725.98, 58953.26) * mm, "end": v(44495.22, 57370.06) * mm});
            skLineSegment(sketch, "E7584", {"start": v(49476.62, 59086.75) * mm, "end": v(44628.7, 57619.42) * mm});
            skLineSegment(sketch, "E7585", {"start": v(49476.62, 59086.75) * mm, "end": v(44628.7, 57619.38) * mm});
            skLineSegment(sketch, "E7586", {"start": v(46549.88, 58728.5) * mm, "end": v(44769.56, 58189.64) * mm});
            skLineSegment(sketch, "E7587", {"start": v(49091.04, 59497.67) * mm, "end": v(46741.3, 58786.45) * mm});
            skLineSegment(sketch, "E7588", {"start": v(44386.73, 58418.85) * mm, "end": v(44628.7, 57619.42) * mm});
            skLineSegment(sketch, "E7589", {"start": v(44195.31, 58360.91) * mm, "end": v(44495.22, 57370.06) * mm});
            skLineSegment(sketch, "E7590", {"start": v(44195.31, 58360.91) * mm, "end": v(44386.73, 58418.85) * mm});
            skLineSegment(sketch, "E7591", {"start": v(49476.62, 59086.75) * mm, "end": v(49350.51, 59503.37) * mm});
            skLineSegment(sketch, "E7592", {"start": v(49725.98, 58953.26) * mm, "end": v(49541.94, 59561.3) * mm});
            skLineSegment(sketch, "E7593", {"start": v(34583.64, 74073.32) * mm, "end": v(34277.71, 74103.31) * mm});
            skLineSegment(sketch, "E7594", {"start": v(36509.2, 74336.72) * mm, "end": v(36210.42, 74264.44) * mm});
            skLineSegment(sketch, "E7595", {"start": v(38568.06, 74568.37) * mm, "end": v(38260.66, 74568.37) * mm});
            skLineSegment(sketch, "E7596", {"start": v(40630.85, 74832.8) * mm, "end": v(40326.88, 74787.02) * mm});
            skLineSegment(sketch, "E7597", {"start": v(42529.89, 75035.76) * mm, "end": v(42224.21, 75003.22) * mm});
            skLineSegment(sketch, "E7598", {"start": v(44620.7, 75346.4) * mm, "end": v(44315.83, 75306.98) * mm});
            skLineSegment(sketch, "E7599", {"start": v(46260.89, 75467.94) * mm, "end": v(45954.04, 75449.5) * mm});
            skLineSegment(sketch, "E7600", {"start": v(48411.94, 75732.02) * mm, "end": v(48106.56, 75696.83) * mm});
            skLineSegment(sketch, "E7601", {"start": v(34308.4, 74416.31) * mm, "end": v(34614.33, 74386.32) * mm});
            skLineSegment(sketch, "E7602", {"start": v(34306.57, 74397.7) * mm, "end": v(34612.5, 74367.7) * mm});
            skLineSegment(sketch, "E7603", {"start": v(34614.33, 74386.32) * mm, "end": v(34612.5, 74367.7) * mm});
            skLineSegment(sketch, "E7604", {"start": v(34585.47, 74091.93) * mm, "end": v(34583.64, 74073.32) * mm});
            skLineSegment(sketch, "E7605", {"start": v(34585.47, 74091.93) * mm, "end": v(34279.53, 74121.92) * mm});
            skLineSegment(sketch, "E7606", {"start": v(34277.71, 74103.31) * mm, "end": v(34279.53, 74121.92) * mm});
            skLineSegment(sketch, "E7607", {"start": v(34306.57, 74397.7) * mm, "end": v(34308.4, 74416.31) * mm});
            skLineSegment(sketch, "E7608", {"start": v(34465.5, 74382.12) * mm, "end": v(34438.47, 74106.34) * mm});
            skLineSegment(sketch, "E7609", {"start": v(34453.57, 74383.29) * mm, "end": v(34426.53, 74107.51) * mm});
            skLineSegment(sketch, "E7610", {"start": v(36136.47, 74570.12) * mm, "end": v(36435.25, 74642.4) * mm});
            skLineSegment(sketch, "E7611", {"start": v(36140.87, 74551.95) * mm, "end": v(36439.65, 74624.22) * mm});
            skLineSegment(sketch, "E7612", {"start": v(36435.25, 74642.4) * mm, "end": v(36439.65, 74624.22) * mm});
            skLineSegment(sketch, "E7613", {"start": v(36504.8, 74354.9) * mm, "end": v(36509.2, 74336.72) * mm});
            skLineSegment(sketch, "E7614", {"start": v(36504.8, 74354.9) * mm, "end": v(36206.02, 74282.62) * mm});
            skLineSegment(sketch, "E7615", {"start": v(36210.42, 74264.44) * mm, "end": v(36206.02, 74282.62) * mm});
            skLineSegment(sketch, "E7616", {"start": v(36140.87, 74551.95) * mm, "end": v(36136.47, 74570.12) * mm});
            skLineSegment(sketch, "E7617", {"start": v(36296.1, 74589.5) * mm, "end": v(36361.24, 74320.16) * mm});
            skLineSegment(sketch, "E7618", {"start": v(36284.43, 74586.68) * mm, "end": v(36349.58, 74317.34) * mm});
            skLineSegment(sketch, "E7619", {"start": v(38260.66, 74882.87) * mm, "end": v(38568.06, 74882.87) * mm});
            skLineSegment(sketch, "E7620", {"start": v(38260.66, 74864.17) * mm, "end": v(38568.06, 74864.17) * mm});
            skLineSegment(sketch, "E7621", {"start": v(38568.06, 74882.87) * mm, "end": v(38568.06, 74864.17) * mm});
            skLineSegment(sketch, "E7622", {"start": v(38568.06, 74587.07) * mm, "end": v(38568.06, 74568.37) * mm});
            skLineSegment(sketch, "E7623", {"start": v(38568.06, 74587.07) * mm, "end": v(38260.66, 74587.07) * mm});
            skLineSegment(sketch, "E7624", {"start": v(38260.66, 74568.37) * mm, "end": v(38260.66, 74587.07) * mm});
            skLineSegment(sketch, "E7625", {"start": v(38260.66, 74864.17) * mm, "end": v(38260.66, 74882.87) * mm});
            skLineSegment(sketch, "E7626", {"start": v(38420.36, 74864.17) * mm, "end": v(38420.36, 74587.07) * mm});
            skLineSegment(sketch, "E7627", {"start": v(38408.36, 74864.17) * mm, "end": v(38408.36, 74587.07) * mm});
            skLineSegment(sketch, "E7628", {"start": v(40280.05, 75098.01) * mm, "end": v(40584.02, 75143.79) * mm});
            skLineSegment(sketch, "E7629", {"start": v(40282.83, 75079.52) * mm, "end": v(40586.8, 75125.3) * mm});
            skLineSegment(sketch, "E7630", {"start": v(40584.02, 75143.79) * mm, "end": v(40586.8, 75125.3) * mm});
            skLineSegment(sketch, "E7631", {"start": v(40628.07, 74851.29) * mm, "end": v(40630.85, 74832.8) * mm});
            skLineSegment(sketch, "E7632", {"start": v(40628.07, 74851.29) * mm, "end": v(40324.1, 74805.5) * mm});
            skLineSegment(sketch, "E7633", {"start": v(40326.88, 74787.02) * mm, "end": v(40324.1, 74805.5) * mm});
            skLineSegment(sketch, "E7634", {"start": v(40282.83, 75079.52) * mm, "end": v(40280.05, 75098.01) * mm});
            skLineSegment(sketch, "E7635", {"start": v(40440.75, 75103.3) * mm, "end": v(40482.02, 74829.3) * mm});
            skLineSegment(sketch, "E7636", {"start": v(40428.89, 75101.51) * mm, "end": v(40470.15, 74827.5) * mm});
            skLineSegment(sketch, "E7637", {"start": v(42190.92, 75315.95) * mm, "end": v(42496.6, 75348.5) * mm});
            skLineSegment(sketch, "E7638", {"start": v(42192.9, 75297.36) * mm, "end": v(42498.58, 75329.9) * mm});
            skLineSegment(sketch, "E7639", {"start": v(42496.6, 75348.5) * mm, "end": v(42498.58, 75329.9) * mm});
            skLineSegment(sketch, "E7640", {"start": v(42527.9, 75054.35) * mm, "end": v(42529.89, 75035.76) * mm});
            skLineSegment(sketch, "E7641", {"start": v(42527.9, 75054.35) * mm, "end": v(42222.24, 75021.82) * mm});
            skLineSegment(sketch, "E7642", {"start": v(42224.21, 75003.22) * mm, "end": v(42222.24, 75021.82) * mm});
            skLineSegment(sketch, "E7643", {"start": v(42192.9, 75297.36) * mm, "end": v(42190.92, 75315.95) * mm});
            skLineSegment(sketch, "E7644", {"start": v(42351.7, 75314.26) * mm, "end": v(42381.04, 75038.72) * mm});
            skLineSegment(sketch, "E7645", {"start": v(42339.77, 75313) * mm, "end": v(42369.1, 75037.45) * mm});
            skLineSegment(sketch, "E7646", {"start": v(44275.5, 75618.88) * mm, "end": v(44580.37, 75658.3) * mm});
            skLineSegment(sketch, "E7647", {"start": v(44277.9, 75600.34) * mm, "end": v(44582.77, 75639.76) * mm});
            skLineSegment(sketch, "E7648", {"start": v(44580.37, 75658.3) * mm, "end": v(44582.77, 75639.76) * mm});
            skLineSegment(sketch, "E7649", {"start": v(44618.3, 75364.94) * mm, "end": v(44620.7, 75346.4) * mm});
            skLineSegment(sketch, "E7650", {"start": v(44618.3, 75364.94) * mm, "end": v(44313.44, 75325.53) * mm});
            skLineSegment(sketch, "E7651", {"start": v(44315.83, 75306.98) * mm, "end": v(44313.44, 75325.53) * mm});
            skLineSegment(sketch, "E7652", {"start": v(44277.9, 75600.34) * mm, "end": v(44275.5, 75618.88) * mm});
            skLineSegment(sketch, "E7653", {"start": v(44436.28, 75620.82) * mm, "end": v(44471.82, 75346) * mm});
            skLineSegment(sketch, "E7654", {"start": v(44424.38, 75619.28) * mm, "end": v(44459.92, 75344.46) * mm});
            skLineSegment(sketch, "E7655", {"start": v(45935.18, 75763.44) * mm, "end": v(46242.02, 75781.88) * mm});
            skLineSegment(sketch, "E7656", {"start": v(45936.3, 75744.77) * mm, "end": v(46243.14, 75763.21) * mm});
            skLineSegment(sketch, "E7657", {"start": v(46242.02, 75781.88) * mm, "end": v(46243.14, 75763.21) * mm});
            skLineSegment(sketch, "E7658", {"start": v(46259.76, 75486.61) * mm, "end": v(46260.89, 75467.94) * mm});
            skLineSegment(sketch, "E7659", {"start": v(46259.76, 75486.61) * mm, "end": v(45952.92, 75468.17) * mm});
            skLineSegment(sketch, "E7660", {"start": v(45954.04, 75449.5) * mm, "end": v(45952.92, 75468.17) * mm});
            skLineSegment(sketch, "E7661", {"start": v(45936.3, 75744.77) * mm, "end": v(45935.18, 75763.44) * mm});
            skLineSegment(sketch, "E7662", {"start": v(46095.71, 75754.35) * mm, "end": v(46112.33, 75477.75) * mm});
            skLineSegment(sketch, "E7663", {"start": v(46083.73, 75753.63) * mm, "end": v(46100.35, 75477.03) * mm});
            skLineSegment(sketch, "E7664", {"start": v(48070.56, 76009.27) * mm, "end": v(48375.94, 76044.45) * mm});
            skLineSegment(sketch, "E7665", {"start": v(48072.7, 75990.69) * mm, "end": v(48378.08, 76025.87) * mm});
            skLineSegment(sketch, "E7666", {"start": v(48375.94, 76044.45) * mm, "end": v(48378.08, 76025.87) * mm});
            skLineSegment(sketch, "E7667", {"start": v(48409.8, 75750.6) * mm, "end": v(48411.94, 75732.02) * mm});
            skLineSegment(sketch, "E7668", {"start": v(48409.8, 75750.6) * mm, "end": v(48104.42, 75715.4) * mm});
            skLineSegment(sketch, "E7669", {"start": v(48106.56, 75696.83) * mm, "end": v(48104.42, 75715.4) * mm});
            skLineSegment(sketch, "E7670", {"start": v(48072.7, 75990.69) * mm, "end": v(48070.56, 76009.27) * mm});
            skLineSegment(sketch, "E7671", {"start": v(48231.35, 76008.97) * mm, "end": v(48263.07, 75733.69) * mm});
            skLineSegment(sketch, "E7672", {"start": v(48219.43, 76007.6) * mm, "end": v(48251.15, 75732.31) * mm});
            skLineSegment(sketch, "E7673", {"start": v(34452, 74244.23) * mm, "end": v(34440.05, 74245.4) * mm});
            skLineSegment(sketch, "E7674", {"start": v(36328.67, 74454.83) * mm, "end": v(36317, 74452) * mm});
            skLineSegment(sketch, "E7675", {"start": v(38420.36, 74725.62) * mm, "end": v(38408.36, 74725.62) * mm});
            skLineSegment(sketch, "E7676", {"start": v(40461.39, 74966.3) * mm, "end": v(40449.52, 74964.5) * mm});
            skLineSegment(sketch, "E7677", {"start": v(42366.37, 75176.5) * mm, "end": v(42354.44, 75175.22) * mm});
            skLineSegment(sketch, "E7678", {"start": v(44454.05, 75483.4) * mm, "end": v(44442.15, 75481.87) * mm});
            skLineSegment(sketch, "E7679", {"start": v(46104.02, 75616.05) * mm, "end": v(46092.04, 75615.33) * mm});
            skLineSegment(sketch, "E7680", {"start": v(48247.21, 75871.33) * mm, "end": v(48235.3, 75869.95) * mm});
            skCircle(sketch, "E7681", {"center": v(34446.02, 74244.82) * mm, "radius": 300 * mm});
            skCircle(sketch, "E7682", {"center": v(36322.84, 74453.42) * mm, "radius": 300 * mm});
            skCircle(sketch, "E7683", {"center": v(38414.36, 74725.62) * mm, "radius": 300 * mm});
            skCircle(sketch, "E7684", {"center": v(40455.45, 74965.4) * mm, "radius": 300 * mm});
            skCircle(sketch, "E7685", {"center": v(42360.4, 75175.86) * mm, "radius": 300 * mm});
            skCircle(sketch, "E7686", {"center": v(44448.1, 75482.64) * mm, "radius": 300 * mm});
            skCircle(sketch, "E7687", {"center": v(46098.03, 75615.7) * mm, "radius": 300 * mm});
            skCircle(sketch, "E7688", {"center": v(48241.25, 75870.64) * mm, "radius": 300 * mm});
            skLineSegment(sketch, "E7689", {"start": v(35107.62, 70149.24) * mm, "end": v(35339.38, 69383.55) * mm});
            skLineSegment(sketch, "E7690", {"start": v(35052.25, 69296.64) * mm, "end": v(35339.38, 69383.55) * mm});
            skLineSegment(sketch, "E7691", {"start": v(34820.49, 70062.33) * mm, "end": v(35052.25, 69296.64) * mm});
            skLineSegment(sketch, "E7692", {"start": v(34820.49, 70062.33) * mm, "end": v(35107.62, 70149.24) * mm});
            skLineSegment(sketch, "E7693", {"start": v(44215.6, 60106.43) * mm, "end": v(45947.99, 60630.79) * mm});
            skLineSegment(sketch, "E7694", {"start": v(45947.99, 60630.79) * mm, "end": v(46469.45, 58907.97) * mm});
            skLineSegment(sketch, "E7695", {"start": v(46469.45, 58907.97) * mm, "end": v(44737.06, 58383.62) * mm});
            skLineSegment(sketch, "E7696", {"start": v(44737.06, 58383.62) * mm, "end": v(44215.6, 60106.43) * mm});
            skLineSegment(sketch, "E7697", {"start": v(46187.33, 60703.22) * mm, "end": v(48489.2, 61399.95) * mm});
            skLineSegment(sketch, "E7698", {"start": v(48489.2, 61399.95) * mm, "end": v(49059.9, 59514.43) * mm});
            skLineSegment(sketch, "E7699", {"start": v(49059.9, 59514.43) * mm, "end": v(46758.03, 58817.7) * mm});
            skLineSegment(sketch, "E7700", {"start": v(46758.03, 58817.7) * mm, "end": v(46187.33, 60703.22) * mm});
            skLineSegment(sketch, "E7701", {"start": v(46187.3, 60703.2) * mm, "end": v(49055.09, 59512.96) * mm});
            skLineSegment(sketch, "E7702", {"start": v(48489.16, 61399.93) * mm, "end": v(46758, 58817.68) * mm});
            skLineSegment(sketch, "E7703", {"start": v(45947.99, 60630.79) * mm, "end": v(44737.06, 58383.62) * mm});
            skLineSegment(sketch, "E7704", {"start": v(44215.6, 60106.43) * mm, "end": v(46469.45, 58907.97) * mm});
            skLineSegment(sketch, "E7705", {"start": v(51853.9, 57324.98) * mm, "end": v(51428.05, 58731.95) * mm});
            skLineSegment(sketch, "E7706", {"start": v(51667.33, 58804.37) * mm, "end": v(51428.05, 58731.95) * mm});
            skLineSegment(sketch, "E7707", {"start": v(52093.19, 57397.4) * mm, "end": v(51667.33, 58804.37) * mm});
            skLineSegment(sketch, "E7708", {"start": v(58318.92, 63332.61) * mm, "end": v(58586.76, 62852.24) * mm});
            skLineSegment(sketch, "E7709", {"start": v(58368.41, 62730.5) * mm, "end": v(58586.76, 62852.24) * mm});
            skLineSegment(sketch, "E7710", {"start": v(58100.57, 63210.86) * mm, "end": v(58368.41, 62730.5) * mm});
            skLineSegment(sketch, "E7711", {"start": v(58100.57, 63210.86) * mm, "end": v(58318.92, 63332.61) * mm});
            skLineSegment(sketch, "E7712", {"start": v(59393.32, 61405.46) * mm, "end": v(59661.17, 60925.09) * mm});
            skLineSegment(sketch, "E7713", {"start": v(59442.82, 60803.34) * mm, "end": v(59661.17, 60925.09) * mm});
            skLineSegment(sketch, "E7714", {"start": v(59174.97, 61283.7) * mm, "end": v(59442.82, 60803.34) * mm});
            skLineSegment(sketch, "E7715", {"start": v(59174.97, 61283.7) * mm, "end": v(59393.32, 61405.46) * mm});
            skLineSegment(sketch, "E7716", {"start": v(61824.92, 57043.9) * mm, "end": v(62092.77, 56563.53) * mm});
            skLineSegment(sketch, "E7717", {"start": v(61874.42, 56441.78) * mm, "end": v(62092.77, 56563.53) * mm});
            skLineSegment(sketch, "E7718", {"start": v(61606.57, 56922.15) * mm, "end": v(61874.42, 56441.78) * mm});
            skLineSegment(sketch, "E7719", {"start": v(61606.57, 56922.15) * mm, "end": v(61824.92, 57043.9) * mm});
            skLineSegment(sketch, "E7720", {"start": v(62899.33, 55116.74) * mm, "end": v(63167.18, 54636.37) * mm});
            skLineSegment(sketch, "E7721", {"start": v(62948.82, 54514.62) * mm, "end": v(63167.18, 54636.37) * mm});
            skLineSegment(sketch, "E7722", {"start": v(62680.98, 54995) * mm, "end": v(62948.82, 54514.62) * mm});
            skLineSegment(sketch, "E7723", {"start": v(62680.98, 54995) * mm, "end": v(62899.33, 55116.74) * mm});
            skLineSegment(sketch, "E7724", {"start": v(55887.31, 67694.17) * mm, "end": v(56155.16, 67213.8) * mm});
            skLineSegment(sketch, "E7725", {"start": v(55936.81, 67092.05) * mm, "end": v(56155.16, 67213.8) * mm});
            skLineSegment(sketch, "E7726", {"start": v(55668.96, 67572.42) * mm, "end": v(55936.81, 67092.05) * mm});
            skLineSegment(sketch, "E7727", {"start": v(55668.96, 67572.42) * mm, "end": v(55887.31, 67694.17) * mm});
            skLineSegment(sketch, "E7728", {"start": v(54812.9, 69621.33) * mm, "end": v(55080.76, 69140.96) * mm});
            skLineSegment(sketch, "E7729", {"start": v(54862.4, 69019.2) * mm, "end": v(55080.76, 69140.96) * mm});
            skLineSegment(sketch, "E7730", {"start": v(54594.56, 69499.58) * mm, "end": v(54862.4, 69019.2) * mm});
            skLineSegment(sketch, "E7731", {"start": v(54594.56, 69499.58) * mm, "end": v(54812.9, 69621.33) * mm});
            skLineSegment(sketch, "E7732", {"start": v(53322.5, 61948.71) * mm, "end": v(49005.84, 60642.15) * mm});
            skLineSegment(sketch, "E7733", {"start": v(53394.94, 61709.43) * mm, "end": v(52319.25, 61383.85) * mm});
            skLineSegment(sketch, "E7734", {"start": v(52079.98, 61311.4) * mm, "end": v(49078.26, 60402.87) * mm});
            skLineSegment(sketch, "E7735", {"start": v(52380.65, 73984.06) * mm, "end": v(52648.5, 73503.69) * mm});
            skLineSegment(sketch, "E7736", {"start": v(52430.15, 73381.94) * mm, "end": v(52648.5, 73503.69) * mm});
            skLineSegment(sketch, "E7737", {"start": v(52162.3, 73862.3) * mm, "end": v(52430.15, 73381.94) * mm});
            skLineSegment(sketch, "E7738", {"start": v(52162.3, 73862.3) * mm, "end": v(52380.65, 73984.06) * mm});
            skLineSegment(sketch, "E7739", {"start": v(35085.6, 70142.58) * mm, "end": v(34311.4, 72700.4) * mm});
            skLineSegment(sketch, "E7740", {"start": v(34842.5, 70069) * mm, "end": v(34055.95, 72667.63) * mm});
            skLineSegment(sketch, "E7741", {"start": v(37225.7, 69095.58) * mm, "end": v(36066.45, 72925.54) * mm});
            skLineSegment(sketch, "E7742", {"start": v(36982.59, 69022) * mm, "end": v(35810.98, 72892.77) * mm});
            skLineSegment(sketch, "E7743", {"start": v(38895.86, 69601.11) * mm, "end": v(37821.48, 73150.67) * mm});
            skLineSegment(sketch, "E7744", {"start": v(38652.76, 69527.53) * mm, "end": v(37566.02, 73117.9) * mm});
            skLineSegment(sketch, "E7745", {"start": v(34899.58, 69801.04) * mm, "end": v(32962.5, 69214.73) * mm});
            skLineSegment(sketch, "E7746", {"start": v(32962.5, 69214.73) * mm, "end": v(33036.1, 68971.62) * mm});
            skLineSegment(sketch, "E7747", {"start": v(33036.1, 68971.62) * mm, "end": v(34973.16, 69557.93) * mm});
            skLineSegment(sketch, "E7748", {"start": v(36591.76, 70313.23) * mm, "end": v(35186.71, 69887.95) * mm});
            skLineSegment(sketch, "E7749", {"start": v(35186.71, 69887.95) * mm, "end": v(35260.3, 69644.84) * mm});
            skLineSegment(sketch, "E7750", {"start": v(35260.3, 69644.84) * mm, "end": v(36665.34, 70070.12) * mm});
            skLineSegment(sketch, "E7751", {"start": v(36908.45, 70143.7) * mm, "end": v(38335.51, 70575.64) * mm});
            skLineSegment(sketch, "E7752", {"start": v(38578.62, 70649.23) * mm, "end": v(40119.97, 71115.76) * mm});
            skLineSegment(sketch, "E7753", {"start": v(40119.97, 71115.76) * mm, "end": v(40046.38, 71358.87) * mm});
            skLineSegment(sketch, "E7754", {"start": v(40046.38, 71358.87) * mm, "end": v(38505.04, 70892.34) * mm});
            skLineSegment(sketch, "E7755", {"start": v(38261.93, 70818.75) * mm, "end": v(36834.87, 70386.8) * mm});
            skLineSegment(sketch, "E7756", {"start": v(35375.27, 69394.4) * mm, "end": v(35613.43, 68607.58) * mm});
            skLineSegment(sketch, "E7757", {"start": v(35613.43, 68607.58) * mm, "end": v(35254.51, 68498.95) * mm});
            skLineSegment(sketch, "E7758", {"start": v(35254.51, 68498.95) * mm, "end": v(35016.36, 69285.77) * mm});
            skLineSegment(sketch, "E7759", {"start": v(35016.36, 69285.77) * mm, "end": v(35375.27, 69394.4) * mm});
            skLineSegment(sketch, "E7760", {"start": v(37610.07, 72972.37) * mm, "end": v(36110.5, 72780) * mm});
            skLineSegment(sketch, "E7761", {"start": v(35855.03, 72747.23) * mm, "end": v(34355.46, 72554.87) * mm});
            skLineSegment(sketch, "E7762", {"start": v(36360.56, 71077.05) * mm, "end": v(34933.5, 70645.1) * mm});
            skLineSegment(sketch, "E7763", {"start": v(34690.4, 70571.5) * mm, "end": v(32730.07, 69978.12) * mm});
            skLineSegment(sketch, "E7764", {"start": v(32730.07, 69978.12) * mm, "end": v(32686.62, 70121.69) * mm});
            skLineSegment(sketch, "E7765", {"start": v(32686.62, 70121.69) * mm, "end": v(34646.95, 70715.07) * mm});
            skLineSegment(sketch, "E7766", {"start": v(34890.05, 70788.66) * mm, "end": v(36317.1, 71220.62) * mm});
            skLineSegment(sketch, "E7767", {"start": v(36560.22, 71294.2) * mm, "end": v(37987.27, 71726.17) * mm});
            skLineSegment(sketch, "E7768", {"start": v(38230.38, 71799.76) * mm, "end": v(39771.33, 72266.2) * mm});
            skLineSegment(sketch, "E7769", {"start": v(39771.33, 72266.2) * mm, "end": v(39814.79, 72122.63) * mm});
            skLineSegment(sketch, "E7770", {"start": v(39814.79, 72122.63) * mm, "end": v(38273.83, 71656.2) * mm});
            skLineSegment(sketch, "E7771", {"start": v(38030.73, 71582.6) * mm, "end": v(36603.67, 71150.64) * mm});
            skLineSegment(sketch, "E7772", {"start": v(36270.52, 72251.33) * mm, "end": v(37697.57, 72683.29) * mm});
            skLineSegment(sketch, "E7773", {"start": v(37940.68, 72756.88) * mm, "end": v(39481.63, 73223.31) * mm});
            skLineSegment(sketch, "E7774", {"start": v(39481.63, 73223.31) * mm, "end": v(39525.09, 73079.75) * mm});
            skLineSegment(sketch, "E7775", {"start": v(39525.09, 73079.75) * mm, "end": v(37984.13, 72613.3) * mm});
            skLineSegment(sketch, "E7776", {"start": v(37741.03, 72539.72) * mm, "end": v(36313.97, 72107.76) * mm});
            skLineSegment(sketch, "E7777", {"start": v(36070.86, 72034.17) * mm, "end": v(34643.8, 71602.2) * mm});
            skLineSegment(sketch, "E7778", {"start": v(34400.7, 71528.62) * mm, "end": v(32440.37, 70935.24) * mm});
            skLineSegment(sketch, "E7779", {"start": v(32440.37, 70935.24) * mm, "end": v(32396.92, 71078.8) * mm});
            skLineSegment(sketch, "E7780", {"start": v(32396.92, 71078.8) * mm, "end": v(34357.25, 71672.19) * mm});
            skLineSegment(sketch, "E7781", {"start": v(34600.35, 71745.78) * mm, "end": v(36027.4, 72177.74) * mm});
            skLineSegment(sketch, "E7782", {"start": v(32136.19, 71940.21) * mm, "end": v(34096.5, 72533.66) * mm});
            skLineSegment(sketch, "E7783", {"start": v(34096.5, 72533.66) * mm, "end": v(34139.95, 72390.1) * mm});
            skLineSegment(sketch, "E7784", {"start": v(34139.95, 72390.1) * mm, "end": v(32179.64, 71796.65) * mm});
            skLineSegment(sketch, "E7785", {"start": v(32179.64, 71796.65) * mm, "end": v(32136.19, 71940.21) * mm});
            skLineSegment(sketch, "E7786", {"start": v(35569.98, 68751.14) * mm, "end": v(36939.13, 69165.57) * mm});
            skLineSegment(sketch, "E7787", {"start": v(37182.24, 69239.16) * mm, "end": v(38609.3, 69671.12) * mm});
            skLineSegment(sketch, "E7788", {"start": v(38852.4, 69744.7) * mm, "end": v(40393.35, 70211.15) * mm});
            skLineSegment(sketch, "E7789", {"start": v(40393.35, 70211.15) * mm, "end": v(40436.81, 70067.58) * mm});
            skLineSegment(sketch, "E7790", {"start": v(40436.81, 70067.58) * mm, "end": v(33352.1, 67923.07) * mm});
            skLineSegment(sketch, "E7791", {"start": v(33352.1, 67923.07) * mm, "end": v(33308.64, 68066.64) * mm});
            skLineSegment(sketch, "E7792", {"start": v(33308.64, 68066.64) * mm, "end": v(35211.06, 68642.5) * mm});
            skLineSegment(sketch, "E7793", {"start": v(55288.15, 51156.63) * mm, "end": v(55346.09, 50965.2) * mm});
            skLineSegment(sketch, "E7794", {"start": v(55346.09, 50965.2) * mm, "end": v(54676.1, 50762.41) * mm});
            skLineSegment(sketch, "E7795", {"start": v(54676.1, 50762.41) * mm, "end": v(54618.17, 50953.84) * mm});
            skLineSegment(sketch, "E7796", {"start": v(54618.17, 50953.84) * mm, "end": v(55288.15, 51156.63) * mm});
            skLineSegment(sketch, "E7797", {"start": v(56436.78, 51503.96) * mm, "end": v(56494.72, 51312.54) * mm});
            skLineSegment(sketch, "E7798", {"start": v(56494.72, 51312.54) * mm, "end": v(55824.74, 51109.75) * mm});
            skLineSegment(sketch, "E7799", {"start": v(55824.74, 51109.75) * mm, "end": v(55766.8, 51301.17) * mm});
            skLineSegment(sketch, "E7800", {"start": v(55766.8, 51301.17) * mm, "end": v(56436.78, 51503.96) * mm});
            skLineSegment(sketch, "E7801", {"start": v(32882.84, 66524.7) * mm, "end": v(32930.7, 66539.19) * mm});
            skLineSegment(sketch, "E7802", {"start": v(33353.92, 67921.59) * mm, "end": v(39569.78, 72933.46) * mm});
            skLineSegment(sketch, "E7803", {"start": v(40437.2, 70067.64) * mm, "end": v(32125.95, 71978.57) * mm});
            skLineSegment(sketch, "E7804", {"start": v(32139.44, 71933.99) * mm, "end": v(33354.29, 67920.36) * mm});
            skLineSegment(sketch, "E7805", {"start": v(39569.33, 72931.51) * mm, "end": v(32125.95, 71978.57) * mm});
            skLineSegment(sketch, "E7806", {"start": v(40437.2, 70067.64) * mm, "end": v(39582.82, 72886.93) * mm});
            skLineSegment(sketch, "E7807", {"start": v(33353.34, 67923.5) * mm, "end": v(40437.2, 70067.64) * mm});
            skEllipse(sketch, "E7808", {"center": v(50534.92, 62319.96) * mm, "majorRadius": 158.75 * mm, "minorRadius": 158.75 * mm, "majorAxis": v(1, 0)});
            skArc(sketch, "E7809", {"start": v(50382.98, 62273.97) * mm, "mid": v(50460, 62180) * mm, "end": v(50580.9, 62168.02) * mm});
            skArc(sketch, "E7810", {"start": v(50686.86, 62365.95) * mm, "mid": v(50609.84, 62459.92) * mm, "end": v(50488.93, 62471.9) * mm});
            skLineSegment(sketch, "E7811", {"start": v(50580.9, 62168.02) * mm, "end": v(50488.93, 62471.9) * mm});
            skLineSegment(sketch, "E7812", {"start": v(50686.86, 62365.95) * mm, "end": v(50382.98, 62273.97) * mm});
            skLineSegment(sketch, "E7813", {"start": v(50488.93, 62471.9) * mm, "end": v(50146.36, 63603.7) * mm});
            skEllipse(sketch, "E7814", {"center": v(56148.5, 63937.99) * mm, "majorRadius": 158.75 * mm, "minorRadius": 158.75 * mm, "majorAxis": v(1, 0)});
            skArc(sketch, "E7815", {"start": v(55996.56, 63892) * mm, "mid": v(56073.58, 63798.03) * mm, "end": v(56194.5, 63786.04) * mm});
            skArc(sketch, "E7816", {"start": v(56300.44, 63983.98) * mm, "mid": v(56223.42, 64077.94) * mm, "end": v(56102.51, 64089.93) * mm});
            skLineSegment(sketch, "E7817", {"start": v(56194.5, 63786.04) * mm, "end": v(56102.51, 64089.93) * mm});
            skLineSegment(sketch, "E7818", {"start": v(56300.44, 63983.98) * mm, "end": v(55996.56, 63892) * mm});
            skLineSegment(sketch, "E7819", {"start": v(56102.51, 64089.93) * mm, "end": v(55759.94, 65221.72) * mm});
            skLineSegment(sketch, "E7820", {"start": v(68800.03, 49613.6) * mm, "end": v(52895.98, 44799.76) * mm});
            skLineSegment(sketch, "E7821", {"start": v(64824.99, 62739.91) * mm, "end": v(48922.75, 57926.63) * mm});
            skLineSegment(sketch, "E7822", {"start": v(63051.1, 64454.54) * mm, "end": v(48298.44, 59989.21) * mm});
            skLineSegment(sketch, "E7823", {"start": v(58279.05, 77095.62) * mm, "end": v(29227.41, 73368.86) * mm});
            skLineSegment(sketch, "E7824", {"start": v(50700.72, 66312.66) * mm, "end": v(57291.8, 44536.93) * mm});
            skLineSegment(sketch, "E7825", {"start": v(56137.88, 61183.94) * mm, "end": v(34457.3, 54621.67) * mm});
            skLineSegment(sketch, "E7826", {"start": v(53763.43, 65950.46) * mm, "end": v(32900.17, 59635.57) * mm});
            skLineSegment(sketch, "E7827", {"start": v(37800.23, 67883.79) * mm, "end": v(31024.37, 65832.87) * mm});
            skLineSegment(sketch, "E7828", {"start": v(61637.16, 69125.21) * mm, "end": v(32680.7, 60360.68) * mm});
            skLineSegment(sketch, "E7829", {"start": v(59917.1, 70856.14) * mm, "end": v(32056.39, 62423.27) * mm});
            skLineSegment(sketch, "E7830", {"start": v(58503.37, 75526.87) * mm, "end": v(30642.65, 67094) * mm});
            skLineSegment(sketch, "E7831", {"start": v(66863.03, 56006.6) * mm, "end": v(50960.79, 51193.3) * mm});
            skLineSegment(sketch, "E7832", {"start": v(67188.94, 54929.83) * mm, "end": v(51286.7, 50116.55) * mm});
            skLineSegment(sketch, "E7833", {"start": v(48161.86, 80551.5) * mm, "end": v(59147.71, 44256.2) * mm});
            skLineSegment(sketch, "E7834", {"start": v(46080.13, 79921.4) * mm, "end": v(50825.96, 64242) * mm});
            skLineSegment(sketch, "E7835", {"start": v(38710.33, 77690.7) * mm, "end": v(45197.28, 56258.97) * mm});
            skLineSegment(sketch, "E7836", {"start": v(32335.92, 75761.3) * mm, "end": v(38822.87, 54329.57) * mm});
            skLineSegment(sketch, "E7837", {"start": v(29943.13, 75037.05) * mm, "end": v(36430.08, 53605.32) * mm});
            skLineSegment(sketch, "E7838", {"start": v(67769.85, 47708.43) * mm, "end": v(50010.94, 79562.53) * mm});
            skCircle(sketch, "E7839", {"center": v(29827.25, 75419.9) * mm, "radius": 400 * mm});
            skCircle(sketch, "E7840", {"center": v(32220.04, 76144.15) * mm, "radius": 400 * mm});
            skCircle(sketch, "E7841", {"center": v(38594.44, 78073.55) * mm, "radius": 400 * mm});
            skCircle(sketch, "E7842", {"center": v(45967.29, 80305.16) * mm, "radius": 400 * mm});
            skCircle(sketch, "E7843", {"center": v(48042.95, 80933.4) * mm, "radius": 400 * mm});
            skCircle(sketch, "E7844", {"center": v(58675.8, 77146.49) * mm, "radius": 400 * mm});
            skCircle(sketch, "E7845", {"center": v(51669.85, 81022.14) * mm, "radius": 400 * mm});
            skCircle(sketch, "E7846", {"center": v(55953.69, 77875.9) * mm, "radius": 400 * mm});
            skCircle(sketch, "E7847", {"center": v(58886.21, 75642.75) * mm, "radius": 400 * mm});
            skCircle(sketch, "E7848", {"center": v(60299.95, 70972.02) * mm, "radius": 400 * mm});
            skCircle(sketch, "E7849", {"center": v(62020, 69241.1) * mm, "radius": 400 * mm});
            skCircle(sketch, "E7850", {"center": v(63433.94, 64570.42) * mm, "radius": 400 * mm});
            skCircle(sketch, "E7851", {"center": v(65207.84, 62855.8) * mm, "radius": 400 * mm});
            skCircle(sketch, "E7852", {"center": v(66621.57, 58185.06) * mm, "radius": 400 * mm});
            skCircle(sketch, "E7853", {"center": v(67245.88, 56122.47) * mm, "radius": 400 * mm});
            skCircle(sketch, "E7854", {"center": v(69182.88, 49729.47) * mm, "radius": 400 * mm});
            skCircle(sketch, "E7855", {"center": v(28686.24, 72177.64) * mm, "radius": 400 * mm});
            skCircle(sketch, "E7856", {"center": v(30641.28, 65716.92) * mm, "radius": 400 * mm});
            skCircle(sketch, "E7857", {"center": v(32515.18, 59519.04) * mm, "radius": 400 * mm});
            skCircle(sketch, "E7858", {"center": v(34071.81, 54504.99) * mm, "radius": 400 * mm});
            skCircle(sketch, "E7859", {"center": v(48987.18, 56326.68) * mm, "radius": 400 * mm});
            skCircle(sketch, "E7860", {"center": v(49399.16, 79054.72) * mm, "radius": 400 * mm});
            skLineSegment(sketch, "E7861", {"start": v(36305.06, 74483.7) * mm, "end": v(29069.58, 72293.67) * mm});
            skLineSegment(sketch, "E7862", {"start": v(66238.73, 58069.18) * mm, "end": v(50336.48, 53255.9) * mm});
            skLineSegment(sketch, "E7863", {"start": v(53375.44, 75865.5) * mm, "end": v(51312.22, 74715.25) * mm});
            skLineSegment(sketch, "E7864", {"start": v(51499.4, 78348.17) * mm, "end": v(51983.24, 74576.36) * mm});
            skLineSegment(sketch, "E7865", {"start": v(35636.54, 59235.4) * mm, "end": v(51432.72, 80700.01) * mm});
            skLineSegment(sketch, "E7866", {"start": v(39916.94, 56084.63) * mm, "end": v(55716.5, 77553.82) * mm});
            skCircle(sketch, "E7867", {"center": v(67571.79, 55045.71) * mm, "radius": 400 * mm});
            skCircle(sketch, "E7868", {"center": v(65653.83, 61371.34) * mm, "radius": 400 * mm});
            skCircle(sketch, "E7869", {"center": v(63682.27, 63752.25) * mm, "radius": 400 * mm});
            skLineSegment(sketch, "E7870", {"start": v(65270.99, 61255.46) * mm, "end": v(49371.78, 56443.1) * mm});
            skCircle(sketch, "E7871", {"center": v(57407.68, 44154.09) * mm, "radius": 400 * mm});
            skCircle(sketch, "E7872", {"center": v(54584.18, 43299.47) * mm, "radius": 400 * mm});
            skCircle(sketch, "E7873", {"center": v(67964.63, 47359.05) * mm, "radius": 400 * mm});
            skLineSegment(sketch, "E7874", {"start": v(54468.58, 43682.4) * mm, "end": v(49533.34, 59987.56) * mm});
            skLineSegment(sketch, "E7875", {"start": v(67004.16, 47476.67) * mm, "end": v(49593.94, 78705.35) * mm});
            skCircle(sketch, "E7876", {"center": v(49816.16, 79911.9) * mm, "radius": 400 * mm});
            skCircle(sketch, "E7877", {"center": v(67198.94, 47127.3) * mm, "radius": 400 * mm});
            skLineSegment(sketch, "E7878", {"start": v(63299.42, 63636.4) * mm, "end": v(48546.14, 59170.88) * mm});
            skSolve(sketch);
        }
        {
            var Q0;
            Q0=makeQuery(id+"F17.imprint","IMPRINT",FACE,{"disambiguationData":[TD([[makeQuery(id+"F17.imprint","IMPRINT",EDGE,{"derivedFrom":sQuery(id+"F17.wireOp",EDGE,"E2527")}),-1.0]])]});
            var sketch = newSketch(context, id + "F26", { "sketchPlane" : qUnion([Q0])});
            skLineSegment(sketch, "E7879.0", {"start": v(37824.84, 61131.4) * mm, "end": v(37790.77, 61243.97) * mm});
            skLineSegment(sketch, "E7879.1", {"start": v(37619.06, 61069.11) * mm, "end": v(36600.07, 64435.67) * mm});
            skLineSegment(sketch, "E7879.2", {"start": v(36836.96, 64395.2) * mm, "end": v(40930.85, 69983.1) * mm});
            skLineSegment(sketch, "E7879.3", {"start": v(36600.07, 64435.67) * mm, "end": v(40852.93, 70240.53) * mm});
            skLineSegment(sketch, "E7879.4", {"start": v(40930.85, 69983.1) * mm, "end": v(41638.09, 67646.6) * mm});
            skLineSegment(sketch, "E7879.5", {"start": v(40107.91, 73443.98) * mm, "end": v(41797.26, 67862.87) * mm});
            skLineSegment(sketch, "E7879.6", {"start": v(39891.68, 73416.24) * mm, "end": v(40852.93, 70240.53) * mm});
            skLineSegment(sketch, "E7880.0", {"start": v(38924.04, 56757.7) * mm, "end": v(37882.7, 60198.13) * mm});
            skLineSegment(sketch, "E7880.1", {"start": v(39129.82, 56820) * mm, "end": v(38801.77, 57903.8) * mm});
            skLineSegment(sketch, "E7880.2", {"start": v(38739.49, 58109.58) * mm, "end": v(42490.93, 59245.07) * mm});
            skLineSegment(sketch, "E7880.3", {"start": v(38801.77, 57903.8) * mm, "end": v(42759, 59101.57) * mm});
            skLineSegment(sketch, "E7880.4", {"start": v(42759, 59101.57) * mm, "end": v(42045.7, 61458.2) * mm});
            skLineSegment(sketch, "E7880.5", {"start": v(42490.93, 59245.07) * mm, "end": v(41952.14, 61025.14) * mm});
            skLineSegment(sketch, "E7880.6", {"start": v(41889.85, 61230.92) * mm, "end": v(40476.08, 60803) * mm});
            skLineSegment(sketch, "E7880.7", {"start": v(41952.14, 61025.14) * mm, "end": v(40538.37, 60597.22) * mm});
            skLineSegment(sketch, "E7880.8", {"start": v(39667.4, 60333.6) * mm, "end": v(38200.7, 59889.65) * mm});
            skLineSegment(sketch, "E7880.9", {"start": v(39605.1, 60539.37) * mm, "end": v(38138.41, 60095.43) * mm});
            skLineSegment(sketch, "E7881.1", {"start": v(43861.14, 60155.86) * mm, "end": v(43459.76, 61481.53) * mm});
            skLineSegment(sketch, "E7881.2", {"start": v(43746.89, 61568.47) * mm, "end": v(43745.98, 61568.2) * mm});
            skLineSegment(sketch, "E7881.3", {"start": v(43540.21, 61505.88) * mm, "end": v(43442.5, 61828.73) * mm});
            skLineSegment(sketch, "E7881.4", {"start": v(43442.5, 61828.73) * mm, "end": v(43648.27, 61891.02) * mm});
            skLineSegment(sketch, "E7881.5", {"start": v(43746, 61568.17) * mm, "end": v(43648.27, 61891.02) * mm});
            skLineSegment(sketch, "E7881.6", {"start": v(43648.2, 61891.26) * mm, "end": v(44111.17, 60361.68) * mm});
            skLineSegment(sketch, "E7881.7", {"start": v(44571.42, 60501.46) * mm, "end": v(44111.04, 60362.11) * mm});
            skLineSegment(sketch, "E7881.8", {"start": v(45433.2, 60761.82) * mm, "end": v(45432.96, 60761.75) * mm});
            skLineSegment(sketch, "E7881.11", {"start": v(44643.85, 60262.18) * mm, "end": v(44184.43, 60123.13) * mm});
            skLineSegment(sketch, "E7881.12", {"start": v(44184.43, 60123.13) * mm, "end": v(44672.81, 58509.33) * mm});
            skLineSegment(sketch, "E7881.14", {"start": v(46453.32, 59047.54) * mm, "end": v(45964.7, 60661.96) * mm});
            skLineSegment(sketch, "E7881.15", {"start": v(45964.7, 60661.96) * mm, "end": v(45505.25, 60522.9) * mm});
            skLineSegment(sketch, "E7881.16", {"start": v(45469.04, 60642.54) * mm, "end": v(45505.25, 60522.9) * mm});
            skLineSegment(sketch, "E7881.17", {"start": v(45469.04, 60642.54) * mm, "end": v(45432.83, 60762.18) * mm});
            skLineSegment(sketch, "E7882.0", {"start": v(46634.17, 61125.32) * mm, "end": v(45433.2, 60761.82) * mm});
            skLineSegment(sketch, "E7883.trimOffspring", {"start": v(43824.91, 60275.51) * mm, "end": v(43824.88, 60275.5) * mm});
            skLineSegment(sketch, "E7884.trimOffspring", {"start": v(43540.2, 61505.89) * mm, "end": v(43459.76, 61481.53) * mm});
            skLineSegment(sketch, "E7885.0", {"start": v(41901.15, 62712.73) * mm, "end": v(37728.48, 61449.75) * mm});
            skLineSegment(sketch, "E7885.1", {"start": v(41542.21, 62379.46) * mm, "end": v(37790.77, 61243.97) * mm});
            skLineSegment(sketch, "E7885.2", {"start": v(41576.29, 62266.88) * mm, "end": v(41542.21, 62379.46) * mm});
            skLineSegment(sketch, "E7885.3", {"start": v(41576.29, 62266.88) * mm, "end": v(41782.07, 62329.17) * mm});
            skLineSegment(sketch, "E7885.4", {"start": v(41782.07, 62329.17) * mm, "end": v(41748, 62441.74) * mm});
            skLineSegment(sketch, "E7885.5", {"start": v(41963.43, 62506.95) * mm, "end": v(41748, 62441.74) * mm});
            skLineSegment(sketch, "E7885.6", {"start": v(41901.15, 62712.73) * mm, "end": v(41963.43, 62506.95) * mm});
            skPoint(sketch, "E7885.7", {"position": v(41765.03, 62385.46) * mm});
            skLineSegment(sketch, "E7886.0", {"start": v(44828.64, 65198.31) * mm, "end": v(41831.82, 67403.73) * mm});
            skLineSegment(sketch, "E7886.1", {"start": v(44528.04, 65152.58) * mm, "end": v(41704.38, 67230.56) * mm});
            skLineSegment(sketch, "E7886.2", {"start": v(44528.04, 65152.58) * mm, "end": v(42970.77, 63036.49) * mm});
            skLineSegment(sketch, "E7886.3", {"start": v(42970.77, 63036.49) * mm, "end": v(42772.13, 62976.36) * mm});
            skLineSegment(sketch, "E7886.4", {"start": v(42834.41, 62770.58) * mm, "end": v(42772.13, 62976.36) * mm});
            skLineSegment(sketch, "E7886.5", {"start": v(43130.3, 62860.14) * mm, "end": v(42834.41, 62770.58) * mm});
            skLineSegment(sketch, "E7886.6", {"start": v(43355.67, 62857.7) * mm, "end": v(43282.95, 63097.96) * mm});
            skLineSegment(sketch, "E7886.7", {"start": v(43355.67, 62857.7) * mm, "end": v(43149.9, 62795.42) * mm});
            skLineSegment(sketch, "E7886.8", {"start": v(43149.9, 62795.42) * mm, "end": v(43130.3, 62860.14) * mm});
            skLineSegment(sketch, "E7886.9", {"start": v(44828.64, 65198.31) * mm, "end": v(43282.95, 63097.96) * mm});
            skLineSegment(sketch, "E7887.1", {"start": v(46644.72, 59105.55) * mm, "end": v(46156.12, 60719.9) * mm});
            skLineSegment(sketch, "E7887.2", {"start": v(48505.85, 61431.1) * mm, "end": v(48994.2, 59817.6) * mm});
            skLineSegment(sketch, "E7887.3", {"start": v(48505.85, 61431.1) * mm, "end": v(47759.3, 61205.13) * mm});
            skLineSegment(sketch, "E7887.4", {"start": v(47723.08, 61324.77) * mm, "end": v(47686.87, 61444.41) * mm});
            skLineSegment(sketch, "E7887.5", {"start": v(47723.08, 61324.77) * mm, "end": v(47759.3, 61205.13) * mm});
            skLineSegment(sketch, "E7887.6", {"start": v(48672.7, 61742.8) * mm, "end": v(47686.87, 61444.41) * mm});
            skLineSegment(sketch, "E7887.7", {"start": v(48672.7, 61742.8) * mm, "end": v(49233.46, 59890.11) * mm});
            skLineSegment(sketch, "E7888.trimOffspring", {"start": v(37728.48, 61449.75) * mm, "end": v(36836.96, 64395.2) * mm});
            skLineSegment(sketch, "E7889", {"start": v(37824.84, 61131.4) * mm, "end": v(37619.06, 61069.11) * mm});
            skLineSegment(sketch, "E7890", {"start": v(38088.47, 60260.42) * mm, "end": v(37882.7, 60198.13) * mm});
            skLineSegment(sketch, "E7891.trimOffspring", {"start": v(38138.41, 60095.43) * mm, "end": v(38088.47, 60260.42) * mm});
            skLineSegment(sketch, "E7892", {"start": v(39605.1, 60539.37) * mm, "end": v(39667.4, 60333.6) * mm});
            skLineSegment(sketch, "E7893", {"start": v(40476.08, 60803) * mm, "end": v(40538.37, 60597.22) * mm});
            skLineSegment(sketch, "E7894", {"start": v(42045.7, 61458.2) * mm, "end": v(41839.92, 61395.9) * mm});
            skLineSegment(sketch, "E7895.trimOffspring", {"start": v(41889.85, 61230.92) * mm, "end": v(41839.92, 61395.9) * mm});
            skLineSegment(sketch, "E7896", {"start": v(46634.17, 61125.32) * mm, "end": v(46706.46, 60886.47) * mm});
            skLineSegment(sketch, "E7897.0", {"start": v(41638.09, 67646.6) * mm, "end": v(41797.26, 67862.87) * mm});
            skPoint(sketch, "E7898.orphan", {"position": v(41369.6, 67281.8) * mm});
            skLineSegment(sketch, "E7899", {"start": v(41831.82, 67403.73) * mm, "end": v(41704.38, 67230.56) * mm});
            skPoint(sketch, "E7900.orphan", {"position": v(41932.72, 68046.92) * mm});
            skLineSegment(sketch, "E7901.0", {"start": v(39891.68, 73416.24) * mm, "end": v(40107.91, 73443.98) * mm});
            skPoint(sketch, "E7902.orphan", {"position": v(31027.58, 72279.15) * mm});
            skPoint(sketch, "E7903.orphan", {"position": v(52857.63, 75079.51) * mm});
            skLineSegment(sketch, "E7904", {"start": v(38924.04, 56757.7) * mm, "end": v(39129.82, 56820) * mm});
            skLineSegment(sketch, "E7905.trimOffspring", {"start": v(38739.49, 58109.58) * mm, "end": v(38200.7, 59889.65) * mm});
            skLineSegment(sketch, "E7906", {"start": v(44571.42, 60501.46) * mm, "end": v(44643.85, 60262.18) * mm});
            skLineSegment(sketch, "E7907", {"start": v(46156.12, 60719.9) * mm, "end": v(46706.46, 60886.47) * mm});
            skLineSegment(sketch, "E7908.0", {"start": v(38457.33, 56624.2) * mm, "end": v(38921.84, 56764.98) * mm});
            skPoint(sketch, "E7881.13.end.orphan", {"position": v(44769.56, 58189.64) * mm});
            skPoint(sketch, "E7881.13.start.orphan", {"position": v(46549.88, 58728.5) * mm});
            skPoint(sketch, "E7909.orphan", {"position": v(50354.93, 60230) * mm});
            skLineSegment(sketch, "E7910.trimOffspring", {"start": v(46453.32, 59047.54) * mm, "end": v(46644.72, 59105.55) * mm});
            skPoint(sketch, "E7887.0.end.orphan", {"position": v(46741.3, 58786.45) * mm});
            skPoint(sketch, "E7887.0.start.orphan", {"position": v(49091.04, 59497.67) * mm});
            skPoint(sketch, "E7887.8.start.orphan", {"position": v(49476.62, 59086.75) * mm});
            skPoint(sketch, "E7881.0.start.orphan", {"position": v(43824.88, 60275.5) * mm});
            skLineSegment(sketch, "E7911.trimOffspring", {"start": v(48994.2, 59817.6) * mm, "end": v(49233.46, 59890.11) * mm});
            skLineSegment(sketch, "E7912", {"start": v(43861.14, 60155.86) * mm, "end": v(44385.92, 58422.6) * mm});
            skLineSegment(sketch, "E7913", {"start": v(44672.81, 58509.33) * mm, "end": v(44385.92, 58422.6) * mm});
            skSolve(sketch);
        }
        {
            var Q0;
            Q0 = qSketchRegion(id + "F26", true);
            extrude(context, id + "F27", {"entities" : qUnion([Q0]), "operationType" : NewBodyOperationType.ADD, "depth" : 2680 * mm, "offsetDistance" : 25 * mm});
        }
        {
            var Q0;
            Q0=makeQuery(id+"F2.opExtrude","CAP_FACE",FACE,{"disambiguationData":[OSD([sQuery(id+"F1.wireOp",EDGE,"E1146"),sQuery(id+"F1.wireOp",EDGE,"E1147"),sQuery(id+"F1.wireOp",EDGE,"E1148"),sQuery(id+"F1.wireOp",EDGE,"E1149")])],"isStart":false});
            var sketch = newSketch(context, id + "F28", { "sketchPlane" : qUnion([Q0])});
            skLineSegment(sketch, "E7914.0", {"start": v(28663.3, 61329.63) * mm, "end": v(29791.98, 57600.7) * mm});
            skLineSegment(sketch, "E7914.3", {"start": v(29791.98, 57600.7) * mm, "end": v(22484.38, 55388.84) * mm});
            skLineSegment(sketch, "E7915.0", {"start": v(29661.06, 57670.78) * mm, "end": v(28591.78, 61203.5) * mm});
            skLineSegment(sketch, "E7916.0", {"start": v(22554.46, 55519.76) * mm, "end": v(29661.06, 57670.78) * mm});
            skLineSegment(sketch, "E7917.trimOffspring", {"start": v(28591.78, 61203.5) * mm, "end": v(21485.18, 59052.48) * mm});
            skLineSegment(sketch, "E7918", {"start": v(22235.8, 56572.59) * mm, "end": v(24278.54, 57190.89) * mm});
            skLineSegment(sketch, "E7919", {"start": v(24278.54, 57190.89) * mm, "end": v(24307.5, 57095.17) * mm});
            skLineSegment(sketch, "E7920", {"start": v(24307.5, 57095.17) * mm, "end": v(22264.76, 56476.88) * mm});
            skLineSegment(sketch, "E7921.trimOffspring", {"start": v(22264.76, 56476.88) * mm, "end": v(22554.46, 55519.76) * mm});
            skLineSegment(sketch, "E7922", {"start": v(21485.18, 59052.48) * mm, "end": v(22235.8, 56572.59) * mm});
            skLineSegment(sketch, "E7923", {"start": v(21355.71, 59117.77) * mm, "end": v(22484.38, 55388.84) * mm});
            skLineSegment(sketch, "E7924", {"start": v(21355.71, 59117.77) * mm, "end": v(28663.3, 61329.63) * mm});
            skLineSegment(sketch, "E7925", {"start": v(29791.98, 57600.7) * mm, "end": v(28663.3, 61329.63) * mm});
            skSolve(sketch);
        }
        {
            var Q0;
            Q0 = qSketchRegion(id + "F28", true);
            extrude(context, id + "F29", {"entities" : qUnion([Q0]), "operationType" : NewBodyOperationType.ADD, "depth" : 3760 * mm, "offsetDistance" : 25 * mm});
        }
    });
